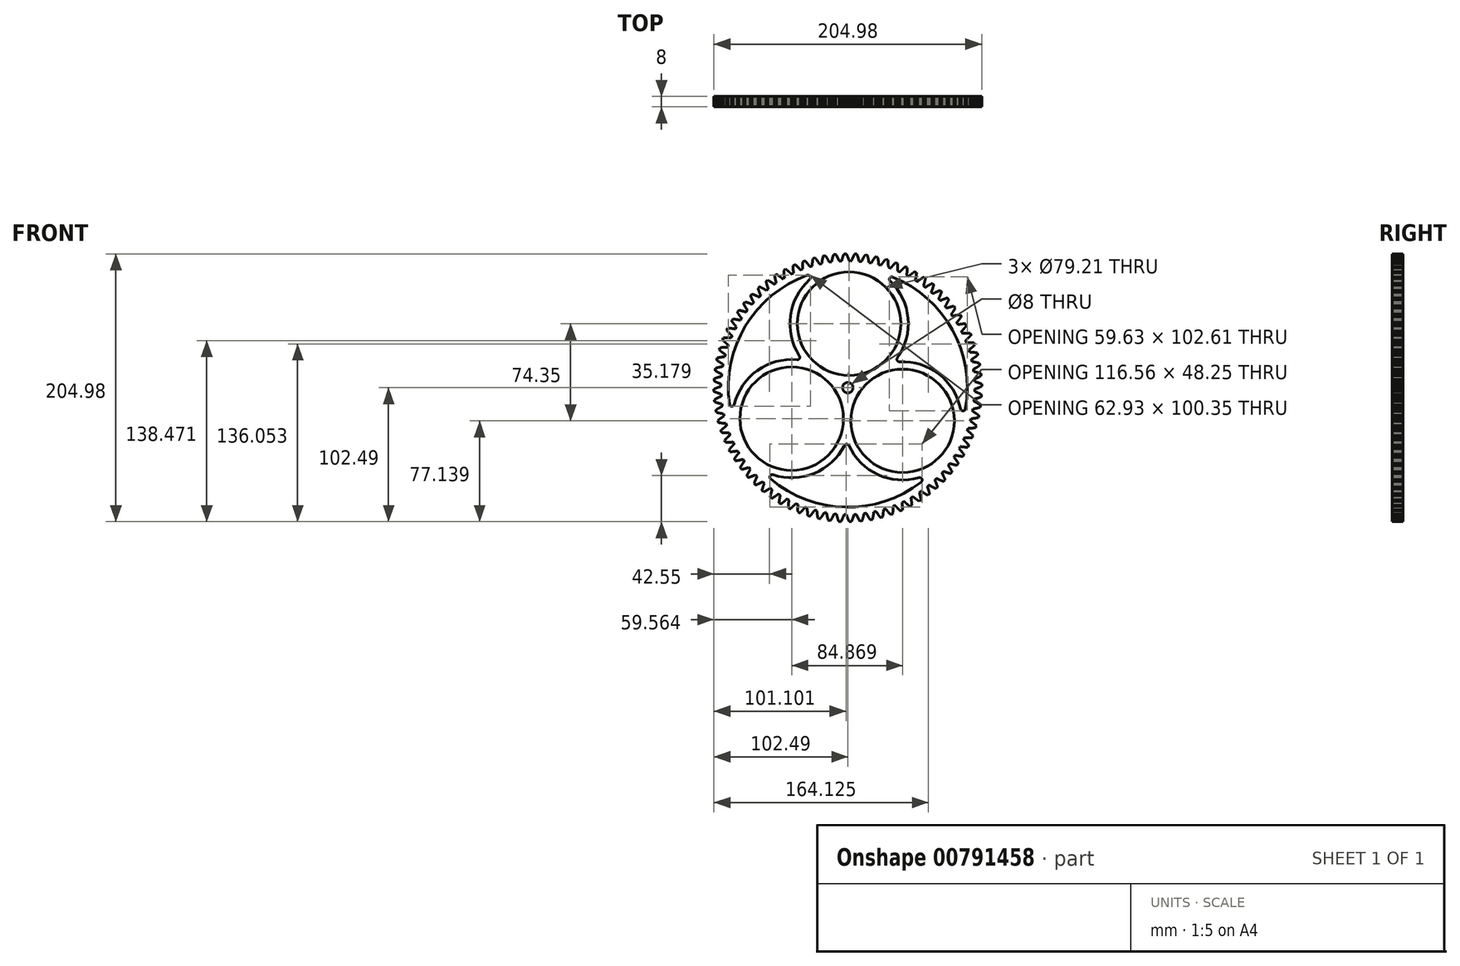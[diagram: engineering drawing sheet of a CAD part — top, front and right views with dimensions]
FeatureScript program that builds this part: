
annotation { "Feature Type Name" : "Feature", "Feature Type Description" : "" }
export const myFeature = defineFeature(function(context is Context, id is Id, definition is map)
    precondition{}
    {
        {
            var Q0;
            Q0=qCreatedBy(makeId("Front.planeOp"),FACE);
            var sketch = newSketch(context, id + "F0", { "sketchPlane" : qUnion([Q0])});
            skCircle(sketch, "E0", {"center": v(0, 0) * mm, "radius": 100 * mm, "construction": true});
            skCircle(sketch, "E1", {"center": v(0.98, 49) * mm, "radius": 39.6 * mm});
            skArc(sketch, "E2", {"start": v(37.95, 22.85) * mm, "mid": v(46.06, 53.26) * mm, "end": v(32.39, 81.62) * mm});
            skCircle(sketch, "E3", {"center": v(41.94, -25.35) * mm, "radius": 39.6 * mm});
            skArc(sketch, "E4", {"start": v(37.95, 22.85) * mm, "mid": v(37.83, 20.84) * mm, "end": v(39.59, 19.87) * mm});
            skArc(sketch, "E5", {"start": v(86.3, -16.23) * mm, "mid": v(69.63, 10.47) * mm, "end": v(39.59, 19.87) * mm});
            skArc(sketch, "E6", {"start": v(90, -16.19) * mm, "mid": v(80.1, 44.13) * mm, "end": v(34.41, 84.73) * mm});
            skArc(sketch, "E7", {"start": v(86.3, -16.23) * mm, "mid": v(88.17, -17.74) * mm, "end": v(90, -16.19) * mm});
            skArc(sketch, "E8", {"start": v(34.41, 84.73) * mm, "mid": v(32.11, 84) * mm, "end": v(32.39, 81.62) * mm});
            skCircle(sketch, "E9", {"center": v(-42.93, -23.65) * mm, "radius": 39.6 * mm});
            skArc(sketch, "E10", {"start": v(-38.76, 21.44) * mm, "mid": v(-36.97, 22.34) * mm, "end": v(-37, 24.35) * mm});
            skArc(sketch, "E11", {"start": v(-29.09, 82.85) * mm, "mid": v(-43.89, 55.07) * mm, "end": v(-37, 24.35) * mm});
            skArc(sketch, "E12", {"start": v(-38.76, 21.44) * mm, "mid": v(-69.16, 13.26) * mm, "end": v(-86.88, -12.76) * mm});
            skArc(sketch, "E13", {"start": v(-30.99, 86.04) * mm, "mid": v(-78.27, 47.3) * mm, "end": v(-90.59, -12.56) * mm});
            skArc(sketch, "E14", {"start": v(-29.09, 82.85) * mm, "mid": v(-28.72, 85.23) * mm, "end": v(-30.99, 86.04) * mm});
            skArc(sketch, "E15", {"start": v(-90.59, -12.56) * mm, "mid": v(-88.81, -14.2) * mm, "end": v(-86.88, -12.76) * mm});
            skArc(sketch, "E16", {"start": v(-57.2, -66.62) * mm, "mid": v(-59.45, -67.49) * mm, "end": v(-59.02, -69.86) * mm});
            skArc(sketch, "E17", {"start": v(-57.2, -66.62) * mm, "mid": v(-25.75, -65.54) * mm, "end": v(-2.59, -44.22) * mm});
            skArc(sketch, "E18", {"start": v(-59.02, -69.86) * mm, "mid": v(-1.83, -91.43) * mm, "end": v(56.17, -72.17) * mm});
            skArc(sketch, "E19", {"start": v(56.17, -72.17) * mm, "mid": v(56.7, -69.82) * mm, "end": v(54.49, -68.86) * mm});
            skArc(sketch, "E20", {"start": v(0.81, -44.29) * mm, "mid": v(23.1, -66.52) * mm, "end": v(54.49, -68.86) * mm});
            skArc(sketch, "E21", {"start": v(0.81, -44.29) * mm, "mid": v(-0.87, -43.19) * mm, "end": v(-2.59, -44.22) * mm});
            skCircle(sketch, "E22", {"center": v(0, 0) * mm, "radius": 4 * mm});
            skLineSegment(sketch, "E23", {"start": v(-97.1, 1.94) * mm, "end": v(-97.18, 1) * mm});
            skLineSegment(sketch, "E24", {"start": v(-97.18, 1) * mm, "end": v(-97.3, 0.96) * mm});
            skLineSegment(sketch, "E25", {"start": v(-97.3, 0.96) * mm, "end": v(-97.43, 0.92) * mm});
            skLineSegment(sketch, "E26", {"start": v(-97.43, 0.92) * mm, "end": v(-97.55, 0.88) * mm});
            skLineSegment(sketch, "E27", {"start": v(-97.55, 0.88) * mm, "end": v(-97.68, 0.84) * mm});
            skLineSegment(sketch, "E28", {"start": v(-97.68, 0.84) * mm, "end": v(-97.8, 0.8) * mm});
            skLineSegment(sketch, "E29", {"start": v(-97.8, 0.8) * mm, "end": v(-97.94, 0.76) * mm});
            skLineSegment(sketch, "E30", {"start": v(-97.94, 0.76) * mm, "end": v(-98.07, 0.72) * mm});
            skLineSegment(sketch, "E31", {"start": v(-98.07, 0.72) * mm, "end": v(-98.2, 0.67) * mm});
            skLineSegment(sketch, "E32", {"start": v(-98.2, 0.67) * mm, "end": v(-98.34, 0.62) * mm});
            skLineSegment(sketch, "E33", {"start": v(-98.34, 0.62) * mm, "end": v(-98.47, 0.58) * mm});
            skLineSegment(sketch, "E34", {"start": v(-98.47, 0.58) * mm, "end": v(-98.6, 0.53) * mm});
            skLineSegment(sketch, "E35", {"start": v(-98.6, 0.53) * mm, "end": v(-98.75, 0.48) * mm});
            skLineSegment(sketch, "E36", {"start": v(-98.75, 0.48) * mm, "end": v(-98.89, 0.43) * mm});
            skLineSegment(sketch, "E37", {"start": v(-98.89, 0.43) * mm, "end": v(-99.03, 0.38) * mm});
            skLineSegment(sketch, "E38", {"start": v(-99.03, 0.38) * mm, "end": v(-99.17, 0.32) * mm});
            skLineSegment(sketch, "E39", {"start": v(-99.17, 0.32) * mm, "end": v(-99.32, 0.27) * mm});
            skLineSegment(sketch, "E40", {"start": v(-99.32, 0.27) * mm, "end": v(-99.46, 0.21) * mm});
            skLineSegment(sketch, "E41", {"start": v(-99.46, 0.21) * mm, "end": v(-99.61, 0.15) * mm});
            skLineSegment(sketch, "E42", {"start": v(-99.61, 0.15) * mm, "end": v(-99.76, 0.1) * mm});
            skLineSegment(sketch, "E43", {"start": v(-99.76, 0.1) * mm, "end": v(-99.9, 0.04) * mm});
            skLineSegment(sketch, "E44", {"start": v(-99.9, 0.04) * mm, "end": v(-100.06, -0.02) * mm});
            skLineSegment(sketch, "E45", {"start": v(-100.06, -0.02) * mm, "end": v(-100.21, -0.09) * mm});
            skLineSegment(sketch, "E46", {"start": v(-100.21, -0.09) * mm, "end": v(-100.37, -0.15) * mm});
            skLineSegment(sketch, "E47", {"start": v(-100.37, -0.15) * mm, "end": v(-100.52, -0.22) * mm});
            skLineSegment(sketch, "E48", {"start": v(-100.52, -0.22) * mm, "end": v(-100.68, -0.28) * mm});
            skLineSegment(sketch, "E49", {"start": v(-100.68, -0.28) * mm, "end": v(-100.84, -0.35) * mm});
            skLineSegment(sketch, "E50", {"start": v(-100.84, -0.35) * mm, "end": v(-101, -0.42) * mm});
            skLineSegment(sketch, "E51", {"start": v(-101, -0.42) * mm, "end": v(-101.16, -0.5) * mm});
            skLineSegment(sketch, "E52", {"start": v(-101.16, -0.5) * mm, "end": v(-101.32, -0.56) * mm});
            skLineSegment(sketch, "E53", {"start": v(-101.32, -0.56) * mm, "end": v(-101.48, -0.64) * mm});
            skLineSegment(sketch, "E54", {"start": v(-101.48, -0.64) * mm, "end": v(-101.65, -0.71) * mm});
            skLineSegment(sketch, "E55", {"start": v(-101.65, -0.71) * mm, "end": v(-101.82, -0.79) * mm});
            skLineSegment(sketch, "E56", {"start": v(-101.82, -0.79) * mm, "end": v(-101.98, -0.87) * mm});
            skLineSegment(sketch, "E57", {"start": v(-101.98, -0.87) * mm, "end": v(-102.15, -0.94) * mm});
            skLineSegment(sketch, "E58", {"start": v(-102.15, -0.94) * mm, "end": v(-102.32, -1.03) * mm});
            skLineSegment(sketch, "E59", {"start": v(-102.32, -1.03) * mm, "end": v(-102.5, -1.1) * mm});
            skLineSegment(sketch, "E60", {"start": v(-102.5, -1.1) * mm, "end": v(-102.5, -1.19) * mm});
            skLineSegment(sketch, "E61", {"start": v(-102.5, -1.19) * mm, "end": v(-102.46, -2.76) * mm});
            skLineSegment(sketch, "E62", {"start": v(-102.46, -2.76) * mm, "end": v(-102.46, -2.84) * mm});
            skLineSegment(sketch, "E63", {"start": v(-102.46, -2.84) * mm, "end": v(-102.28, -2.92) * mm});
            skLineSegment(sketch, "E64", {"start": v(-102.28, -2.92) * mm, "end": v(-102.11, -3) * mm});
            skLineSegment(sketch, "E65", {"start": v(-102.11, -3) * mm, "end": v(-101.94, -3.06) * mm});
            skLineSegment(sketch, "E66", {"start": v(-101.94, -3.06) * mm, "end": v(-101.77, -3.14) * mm});
            skLineSegment(sketch, "E67", {"start": v(-101.77, -3.14) * mm, "end": v(-101.6, -3.2) * mm});
            skLineSegment(sketch, "E68", {"start": v(-101.6, -3.2) * mm, "end": v(-101.43, -3.27) * mm});
            skLineSegment(sketch, "E69", {"start": v(-101.43, -3.27) * mm, "end": v(-101.27, -3.34) * mm});
            skLineSegment(sketch, "E70", {"start": v(-101.27, -3.34) * mm, "end": v(-101.1, -3.4) * mm});
            skLineSegment(sketch, "E71", {"start": v(-101.1, -3.4) * mm, "end": v(-100.94, -3.47) * mm});
            skLineSegment(sketch, "E72", {"start": v(-100.94, -3.47) * mm, "end": v(-100.78, -3.54) * mm});
            skLineSegment(sketch, "E73", {"start": v(-100.78, -3.54) * mm, "end": v(-100.62, -3.6) * mm});
            skLineSegment(sketch, "E74", {"start": v(-100.62, -3.6) * mm, "end": v(-100.46, -3.66) * mm});
            skLineSegment(sketch, "E75", {"start": v(-100.46, -3.66) * mm, "end": v(-100.3, -3.72) * mm});
            skLineSegment(sketch, "E76", {"start": v(-100.3, -3.72) * mm, "end": v(-100.14, -3.77) * mm});
            skLineSegment(sketch, "E77", {"start": v(-100.14, -3.77) * mm, "end": v(-99.99, -3.83) * mm});
            skLineSegment(sketch, "E78", {"start": v(-99.99, -3.83) * mm, "end": v(-99.83, -3.89) * mm});
            skLineSegment(sketch, "E79", {"start": v(-99.83, -3.89) * mm, "end": v(-99.68, -3.94) * mm});
            skLineSegment(sketch, "E80", {"start": v(-99.68, -3.94) * mm, "end": v(-99.53, -4) * mm});
            skLineSegment(sketch, "E81", {"start": v(-99.53, -4) * mm, "end": v(-99.38, -4.04) * mm});
            skLineSegment(sketch, "E82", {"start": v(-99.38, -4.04) * mm, "end": v(-99.23, -4.1) * mm});
            skLineSegment(sketch, "E83", {"start": v(-99.23, -4.1) * mm, "end": v(-99.09, -4.14) * mm});
            skLineSegment(sketch, "E84", {"start": v(-99.09, -4.14) * mm, "end": v(-98.94, -4.2) * mm});
            skLineSegment(sketch, "E85", {"start": v(-98.94, -4.2) * mm, "end": v(-98.8, -4.24) * mm});
            skLineSegment(sketch, "E86", {"start": v(-98.8, -4.24) * mm, "end": v(-98.66, -4.28) * mm});
            skLineSegment(sketch, "E87", {"start": v(-98.66, -4.28) * mm, "end": v(-98.52, -4.33) * mm});
            skLineSegment(sketch, "E88", {"start": v(-98.52, -4.33) * mm, "end": v(-98.38, -4.37) * mm});
            skLineSegment(sketch, "E89", {"start": v(-98.38, -4.37) * mm, "end": v(-98.24, -4.41) * mm});
            skLineSegment(sketch, "E90", {"start": v(-98.24, -4.41) * mm, "end": v(-98.1, -4.45) * mm});
            skLineSegment(sketch, "E91", {"start": v(-98.1, -4.45) * mm, "end": v(-97.97, -4.5) * mm});
            skLineSegment(sketch, "E92", {"start": v(-97.97, -4.5) * mm, "end": v(-97.84, -4.53) * mm});
            skLineSegment(sketch, "E93", {"start": v(-97.84, -4.53) * mm, "end": v(-97.7, -4.57) * mm});
            skLineSegment(sketch, "E94", {"start": v(-97.7, -4.57) * mm, "end": v(-97.57, -4.6) * mm});
            skLineSegment(sketch, "E95", {"start": v(-97.57, -4.6) * mm, "end": v(-97.45, -4.64) * mm});
            skLineSegment(sketch, "E96", {"start": v(-97.45, -4.64) * mm, "end": v(-97.32, -4.68) * mm});
            skLineSegment(sketch, "E97", {"start": v(-97.32, -4.68) * mm, "end": v(-97.2, -4.71) * mm});
            skLineSegment(sketch, "E98", {"start": v(-97.2, -4.71) * mm, "end": v(-97.07, -4.74) * mm});
            skLineSegment(sketch, "E99", {"start": v(-97.07, -4.74) * mm, "end": v(-96.96, -5.68) * mm});
            skLineSegment(sketch, "E100", {"start": v(-96.96, -5.68) * mm, "end": v(-96.96, -6.63) * mm});
            skLineSegment(sketch, "E101", {"start": v(-96.96, -6.63) * mm, "end": v(-97.08, -6.67) * mm});
            skLineSegment(sketch, "E102", {"start": v(-97.08, -6.67) * mm, "end": v(-97.2, -6.72) * mm});
            skLineSegment(sketch, "E103", {"start": v(-97.2, -6.72) * mm, "end": v(-97.32, -6.77) * mm});
            skLineSegment(sketch, "E104", {"start": v(-97.32, -6.77) * mm, "end": v(-97.44, -6.82) * mm});
            skLineSegment(sketch, "E105", {"start": v(-97.44, -6.82) * mm, "end": v(-97.57, -6.87) * mm});
            skLineSegment(sketch, "E106", {"start": v(-97.57, -6.87) * mm, "end": v(-97.7, -6.93) * mm});
            skLineSegment(sketch, "E107", {"start": v(-97.7, -6.93) * mm, "end": v(-97.82, -6.98) * mm});
            skLineSegment(sketch, "E108", {"start": v(-97.82, -6.98) * mm, "end": v(-97.95, -7.04) * mm});
            skLineSegment(sketch, "E109", {"start": v(-97.95, -7.04) * mm, "end": v(-98.08, -7.1) * mm});
            skLineSegment(sketch, "E110", {"start": v(-98.08, -7.1) * mm, "end": v(-98.21, -7.15) * mm});
            skLineSegment(sketch, "E111", {"start": v(-98.21, -7.15) * mm, "end": v(-98.35, -7.2) * mm});
            skLineSegment(sketch, "E112", {"start": v(-98.35, -7.2) * mm, "end": v(-98.48, -7.27) * mm});
            skLineSegment(sketch, "E113", {"start": v(-98.48, -7.27) * mm, "end": v(-98.62, -7.33) * mm});
            skLineSegment(sketch, "E114", {"start": v(-98.62, -7.33) * mm, "end": v(-98.75, -7.4) * mm});
            skLineSegment(sketch, "E115", {"start": v(-98.75, -7.4) * mm, "end": v(-98.9, -7.46) * mm});
            skLineSegment(sketch, "E116", {"start": v(-98.9, -7.46) * mm, "end": v(-99.03, -7.53) * mm});
            skLineSegment(sketch, "E117", {"start": v(-99.03, -7.53) * mm, "end": v(-99.17, -7.6) * mm});
            skLineSegment(sketch, "E118", {"start": v(-99.17, -7.6) * mm, "end": v(-99.32, -7.66) * mm});
            skLineSegment(sketch, "E119", {"start": v(-99.32, -7.66) * mm, "end": v(-99.46, -7.73) * mm});
            skLineSegment(sketch, "E120", {"start": v(-99.46, -7.73) * mm, "end": v(-99.6, -7.8) * mm});
            skLineSegment(sketch, "E121", {"start": v(-99.6, -7.8) * mm, "end": v(-99.75, -7.88) * mm});
            skLineSegment(sketch, "E122", {"start": v(-99.75, -7.88) * mm, "end": v(-99.9, -7.95) * mm});
            skLineSegment(sketch, "E123", {"start": v(-99.9, -7.95) * mm, "end": v(-100.05, -8.03) * mm});
            skLineSegment(sketch, "E124", {"start": v(-100.05, -8.03) * mm, "end": v(-100.2, -8.1) * mm});
            skLineSegment(sketch, "E125", {"start": v(-100.2, -8.1) * mm, "end": v(-100.35, -8.18) * mm});
            skLineSegment(sketch, "E126", {"start": v(-100.35, -8.18) * mm, "end": v(-100.5, -8.26) * mm});
            skLineSegment(sketch, "E127", {"start": v(-100.5, -8.26) * mm, "end": v(-100.65, -8.34) * mm});
            skLineSegment(sketch, "E128", {"start": v(-100.65, -8.34) * mm, "end": v(-100.8, -8.43) * mm});
            skLineSegment(sketch, "E129", {"start": v(-100.8, -8.43) * mm, "end": v(-100.96, -8.51) * mm});
            skLineSegment(sketch, "E130", {"start": v(-100.96, -8.51) * mm, "end": v(-101.12, -8.6) * mm});
            skLineSegment(sketch, "E131", {"start": v(-101.12, -8.6) * mm, "end": v(-101.28, -8.68) * mm});
            skLineSegment(sketch, "E132", {"start": v(-101.28, -8.68) * mm, "end": v(-101.44, -8.77) * mm});
            skLineSegment(sketch, "E133", {"start": v(-101.44, -8.77) * mm, "end": v(-101.6, -8.86) * mm});
            skLineSegment(sketch, "E134", {"start": v(-101.6, -8.86) * mm, "end": v(-101.76, -8.96) * mm});
            skLineSegment(sketch, "E135", {"start": v(-101.76, -8.96) * mm, "end": v(-101.92, -9.05) * mm});
            skLineSegment(sketch, "E136", {"start": v(-101.92, -9.05) * mm, "end": v(-102.09, -9.15) * mm});
            skLineSegment(sketch, "E137", {"start": v(-102.09, -9.15) * mm, "end": v(-102.08, -9.23) * mm});
            skLineSegment(sketch, "E138", {"start": v(-102.08, -9.23) * mm, "end": v(-101.93, -10.8) * mm});
            skLineSegment(sketch, "E139", {"start": v(-101.93, -10.8) * mm, "end": v(-101.92, -10.87) * mm});
            skLineSegment(sketch, "E140", {"start": v(-101.92, -10.87) * mm, "end": v(-101.74, -10.93) * mm});
            skLineSegment(sketch, "E141", {"start": v(-101.74, -10.93) * mm, "end": v(-101.56, -11) * mm});
            skLineSegment(sketch, "E142", {"start": v(-101.56, -11) * mm, "end": v(-101.39, -11.05) * mm});
            skLineSegment(sketch, "E143", {"start": v(-101.39, -11.05) * mm, "end": v(-101.21, -11.11) * mm});
            skLineSegment(sketch, "E144", {"start": v(-101.21, -11.11) * mm, "end": v(-101.04, -11.17) * mm});
            skLineSegment(sketch, "E145", {"start": v(-101.04, -11.17) * mm, "end": v(-100.86, -11.22) * mm});
            skLineSegment(sketch, "E146", {"start": v(-100.86, -11.22) * mm, "end": v(-100.7, -11.28) * mm});
            skLineSegment(sketch, "E147", {"start": v(-100.7, -11.28) * mm, "end": v(-100.52, -11.33) * mm});
            skLineSegment(sketch, "E148", {"start": v(-100.52, -11.33) * mm, "end": v(-100.36, -11.38) * mm});
            skLineSegment(sketch, "E149", {"start": v(-100.36, -11.38) * mm, "end": v(-100.19, -11.43) * mm});
            skLineSegment(sketch, "E150", {"start": v(-100.19, -11.43) * mm, "end": v(-100.02, -11.48) * mm});
            skLineSegment(sketch, "E151", {"start": v(-100.02, -11.48) * mm, "end": v(-99.86, -11.53) * mm});
            skLineSegment(sketch, "E152", {"start": v(-99.86, -11.53) * mm, "end": v(-99.7, -11.57) * mm});
            skLineSegment(sketch, "E153", {"start": v(-99.7, -11.57) * mm, "end": v(-99.54, -11.62) * mm});
            skLineSegment(sketch, "E154", {"start": v(-99.54, -11.62) * mm, "end": v(-99.38, -11.66) * mm});
            skLineSegment(sketch, "E155", {"start": v(-99.38, -11.66) * mm, "end": v(-99.22, -11.7) * mm});
            skLineSegment(sketch, "E156", {"start": v(-99.22, -11.7) * mm, "end": v(-99.07, -11.75) * mm});
            skLineSegment(sketch, "E157", {"start": v(-99.07, -11.75) * mm, "end": v(-98.91, -11.79) * mm});
            skLineSegment(sketch, "E158", {"start": v(-98.91, -11.79) * mm, "end": v(-98.76, -11.83) * mm});
            skLineSegment(sketch, "E159", {"start": v(-98.76, -11.83) * mm, "end": v(-98.6, -11.87) * mm});
            skLineSegment(sketch, "E160", {"start": v(-98.6, -11.87) * mm, "end": v(-98.46, -11.9) * mm});
            skLineSegment(sketch, "E161", {"start": v(-98.46, -11.9) * mm, "end": v(-98.3, -11.94) * mm});
            skLineSegment(sketch, "E162", {"start": v(-98.3, -11.94) * mm, "end": v(-98.16, -11.98) * mm});
            skLineSegment(sketch, "E163", {"start": v(-98.16, -11.98) * mm, "end": v(-98.02, -12.01) * mm});
            skLineSegment(sketch, "E164", {"start": v(-98.02, -12.01) * mm, "end": v(-97.87, -12.04) * mm});
            skLineSegment(sketch, "E165", {"start": v(-97.87, -12.04) * mm, "end": v(-97.73, -12.08) * mm});
            skLineSegment(sketch, "E166", {"start": v(-97.73, -12.08) * mm, "end": v(-97.6, -12.1) * mm});
            skLineSegment(sketch, "E167", {"start": v(-97.6, -12.1) * mm, "end": v(-97.45, -12.14) * mm});
            skLineSegment(sketch, "E168", {"start": v(-97.45, -12.14) * mm, "end": v(-97.31, -12.17) * mm});
            skLineSegment(sketch, "E169", {"start": v(-97.31, -12.17) * mm, "end": v(-97.18, -12.2) * mm});
            skLineSegment(sketch, "E170", {"start": v(-97.18, -12.2) * mm, "end": v(-97.04, -12.22) * mm});
            skLineSegment(sketch, "E171", {"start": v(-97.04, -12.22) * mm, "end": v(-96.91, -12.25) * mm});
            skLineSegment(sketch, "E172", {"start": v(-96.91, -12.25) * mm, "end": v(-96.78, -12.27) * mm});
            skLineSegment(sketch, "E173", {"start": v(-96.78, -12.27) * mm, "end": v(-96.65, -12.3) * mm});
            skLineSegment(sketch, "E174", {"start": v(-96.65, -12.3) * mm, "end": v(-96.52, -12.32) * mm});
            skLineSegment(sketch, "E175", {"start": v(-96.52, -12.32) * mm, "end": v(-96.4, -12.35) * mm});
            skLineSegment(sketch, "E176", {"start": v(-96.4, -12.35) * mm, "end": v(-96.21, -13.27) * mm});
            skLineSegment(sketch, "E177", {"start": v(-96.21, -13.27) * mm, "end": v(-96.14, -14.21) * mm});
            skLineSegment(sketch, "E178", {"start": v(-96.14, -14.21) * mm, "end": v(-96.26, -14.27) * mm});
            skLineSegment(sketch, "E179", {"start": v(-96.26, -14.27) * mm, "end": v(-96.37, -14.33) * mm});
            skLineSegment(sketch, "E180", {"start": v(-96.37, -14.33) * mm, "end": v(-96.5, -14.39) * mm});
            skLineSegment(sketch, "E181", {"start": v(-96.5, -14.39) * mm, "end": v(-96.6, -14.45) * mm});
            skLineSegment(sketch, "E182", {"start": v(-96.6, -14.45) * mm, "end": v(-96.73, -14.5) * mm});
            skLineSegment(sketch, "E183", {"start": v(-96.73, -14.5) * mm, "end": v(-96.85, -14.57) * mm});
            skLineSegment(sketch, "E184", {"start": v(-96.85, -14.57) * mm, "end": v(-96.97, -14.63) * mm});
            skLineSegment(sketch, "E185", {"start": v(-96.97, -14.63) * mm, "end": v(-97.1, -14.7) * mm});
            skLineSegment(sketch, "E186", {"start": v(-97.1, -14.7) * mm, "end": v(-97.22, -14.77) * mm});
            skLineSegment(sketch, "E187", {"start": v(-97.22, -14.77) * mm, "end": v(-97.35, -14.83) * mm});
            skLineSegment(sketch, "E188", {"start": v(-97.35, -14.83) * mm, "end": v(-97.48, -14.9) * mm});
            skLineSegment(sketch, "E189", {"start": v(-97.48, -14.9) * mm, "end": v(-97.6, -14.97) * mm});
            skLineSegment(sketch, "E190", {"start": v(-97.6, -14.97) * mm, "end": v(-97.74, -15.05) * mm});
            skLineSegment(sketch, "E191", {"start": v(-97.74, -15.05) * mm, "end": v(-97.87, -15.12) * mm});
            skLineSegment(sketch, "E192", {"start": v(-97.87, -15.12) * mm, "end": v(-98, -15.2) * mm});
            skLineSegment(sketch, "E193", {"start": v(-98, -15.2) * mm, "end": v(-98.14, -15.27) * mm});
            skLineSegment(sketch, "E194", {"start": v(-98.14, -15.27) * mm, "end": v(-98.27, -15.35) * mm});
            skLineSegment(sketch, "E195", {"start": v(-98.27, -15.35) * mm, "end": v(-98.4, -15.43) * mm});
            skLineSegment(sketch, "E196", {"start": v(-98.4, -15.43) * mm, "end": v(-98.55, -15.51) * mm});
            skLineSegment(sketch, "E197", {"start": v(-98.55, -15.51) * mm, "end": v(-98.69, -15.6) * mm});
            skLineSegment(sketch, "E198", {"start": v(-98.69, -15.6) * mm, "end": v(-98.83, -15.68) * mm});
            skLineSegment(sketch, "E199", {"start": v(-98.83, -15.68) * mm, "end": v(-98.97, -15.76) * mm});
            skLineSegment(sketch, "E200", {"start": v(-98.97, -15.76) * mm, "end": v(-99.1, -15.85) * mm});
            skLineSegment(sketch, "E201", {"start": v(-99.1, -15.85) * mm, "end": v(-99.25, -15.94) * mm});
            skLineSegment(sketch, "E202", {"start": v(-99.25, -15.94) * mm, "end": v(-99.4, -16.03) * mm});
            skLineSegment(sketch, "E203", {"start": v(-99.4, -16.03) * mm, "end": v(-99.54, -16.12) * mm});
            skLineSegment(sketch, "E204", {"start": v(-99.54, -16.12) * mm, "end": v(-99.69, -16.21) * mm});
            skLineSegment(sketch, "E205", {"start": v(-99.69, -16.21) * mm, "end": v(-99.84, -16.3) * mm});
            skLineSegment(sketch, "E206", {"start": v(-99.84, -16.3) * mm, "end": v(-99.99, -16.4) * mm});
            skLineSegment(sketch, "E207", {"start": v(-99.99, -16.4) * mm, "end": v(-100.14, -16.5) * mm});
            skLineSegment(sketch, "E208", {"start": v(-100.14, -16.5) * mm, "end": v(-100.29, -16.6) * mm});
            skLineSegment(sketch, "E209", {"start": v(-100.29, -16.6) * mm, "end": v(-100.44, -16.7) * mm});
            skLineSegment(sketch, "E210", {"start": v(-100.44, -16.7) * mm, "end": v(-100.6, -16.8) * mm});
            skLineSegment(sketch, "E211", {"start": v(-100.6, -16.8) * mm, "end": v(-100.75, -16.91) * mm});
            skLineSegment(sketch, "E212", {"start": v(-100.75, -16.91) * mm, "end": v(-100.9, -17.02) * mm});
            skLineSegment(sketch, "E213", {"start": v(-100.9, -17.02) * mm, "end": v(-101.06, -17.13) * mm});
            skLineSegment(sketch, "E214", {"start": v(-101.06, -17.13) * mm, "end": v(-101.05, -17.2) * mm});
            skLineSegment(sketch, "E215", {"start": v(-101.05, -17.2) * mm, "end": v(-100.77, -18.76) * mm});
            skLineSegment(sketch, "E216", {"start": v(-100.77, -18.76) * mm, "end": v(-100.75, -18.84) * mm});
            skLineSegment(sketch, "E217", {"start": v(-100.75, -18.84) * mm, "end": v(-100.57, -18.88) * mm});
            skLineSegment(sketch, "E218", {"start": v(-100.57, -18.88) * mm, "end": v(-100.39, -18.93) * mm});
            skLineSegment(sketch, "E219", {"start": v(-100.39, -18.93) * mm, "end": v(-100.2, -18.97) * mm});
            skLineSegment(sketch, "E220", {"start": v(-100.2, -18.97) * mm, "end": v(-100.03, -19.02) * mm});
            skLineSegment(sketch, "E221", {"start": v(-100.03, -19.02) * mm, "end": v(-99.85, -19.06) * mm});
            skLineSegment(sketch, "E222", {"start": v(-99.85, -19.06) * mm, "end": v(-99.67, -19.1) * mm});
            skLineSegment(sketch, "E223", {"start": v(-99.67, -19.1) * mm, "end": v(-99.5, -19.14) * mm});
            skLineSegment(sketch, "E224", {"start": v(-99.5, -19.14) * mm, "end": v(-99.32, -19.18) * mm});
            skLineSegment(sketch, "E225", {"start": v(-99.32, -19.18) * mm, "end": v(-99.15, -19.22) * mm});
            skLineSegment(sketch, "E226", {"start": v(-99.15, -19.22) * mm, "end": v(-98.98, -19.26) * mm});
            skLineSegment(sketch, "E227", {"start": v(-98.98, -19.26) * mm, "end": v(-98.82, -19.3) * mm});
            skLineSegment(sketch, "E228", {"start": v(-98.82, -19.3) * mm, "end": v(-98.65, -19.33) * mm});
            skLineSegment(sketch, "E229", {"start": v(-98.65, -19.33) * mm, "end": v(-98.48, -19.36) * mm});
            skLineSegment(sketch, "E230", {"start": v(-98.48, -19.36) * mm, "end": v(-98.32, -19.4) * mm});
            skLineSegment(sketch, "E231", {"start": v(-98.32, -19.4) * mm, "end": v(-98.16, -19.43) * mm});
            skLineSegment(sketch, "E232", {"start": v(-98.16, -19.43) * mm, "end": v(-98, -19.46) * mm});
            skLineSegment(sketch, "E233", {"start": v(-98, -19.46) * mm, "end": v(-97.84, -19.49) * mm});
            skLineSegment(sketch, "E234", {"start": v(-97.84, -19.49) * mm, "end": v(-97.68, -19.51) * mm});
            skLineSegment(sketch, "E235", {"start": v(-97.68, -19.51) * mm, "end": v(-97.53, -19.54) * mm});
            skLineSegment(sketch, "E236", {"start": v(-97.53, -19.54) * mm, "end": v(-97.37, -19.57) * mm});
            skLineSegment(sketch, "E237", {"start": v(-97.37, -19.57) * mm, "end": v(-97.22, -19.6) * mm});
            skLineSegment(sketch, "E238", {"start": v(-97.22, -19.6) * mm, "end": v(-97.07, -19.62) * mm});
            skLineSegment(sketch, "E239", {"start": v(-97.07, -19.62) * mm, "end": v(-96.92, -19.64) * mm});
            skLineSegment(sketch, "E240", {"start": v(-96.92, -19.64) * mm, "end": v(-96.77, -19.66) * mm});
            skLineSegment(sketch, "E241", {"start": v(-96.77, -19.66) * mm, "end": v(-96.63, -19.69) * mm});
            skLineSegment(sketch, "E242", {"start": v(-96.63, -19.69) * mm, "end": v(-96.48, -19.7) * mm});
            skLineSegment(sketch, "E243", {"start": v(-96.48, -19.7) * mm, "end": v(-96.34, -19.73) * mm});
            skLineSegment(sketch, "E244", {"start": v(-96.34, -19.73) * mm, "end": v(-96.2, -19.75) * mm});
            skLineSegment(sketch, "E245", {"start": v(-96.2, -19.75) * mm, "end": v(-96.06, -19.76) * mm});
            skLineSegment(sketch, "E246", {"start": v(-96.06, -19.76) * mm, "end": v(-95.92, -19.78) * mm});
            skLineSegment(sketch, "E247", {"start": v(-95.92, -19.78) * mm, "end": v(-95.79, -19.8) * mm});
            skLineSegment(sketch, "E248", {"start": v(-95.79, -19.8) * mm, "end": v(-95.65, -19.81) * mm});
            skLineSegment(sketch, "E249", {"start": v(-95.65, -19.81) * mm, "end": v(-95.52, -19.83) * mm});
            skLineSegment(sketch, "E250", {"start": v(-95.52, -19.83) * mm, "end": v(-95.39, -19.84) * mm});
            skLineSegment(sketch, "E251", {"start": v(-95.39, -19.84) * mm, "end": v(-95.26, -19.86) * mm});
            skLineSegment(sketch, "E252", {"start": v(-95.26, -19.86) * mm, "end": v(-95.13, -19.87) * mm});
            skLineSegment(sketch, "E253", {"start": v(-95.13, -19.87) * mm, "end": v(-94.88, -20.78) * mm});
            skLineSegment(sketch, "E254", {"start": v(-94.88, -20.78) * mm, "end": v(-94.73, -21.71) * mm});
            skLineSegment(sketch, "E255", {"start": v(-94.73, -21.71) * mm, "end": v(-94.84, -21.78) * mm});
            skLineSegment(sketch, "E256", {"start": v(-94.84, -21.78) * mm, "end": v(-94.95, -21.85) * mm});
            skLineSegment(sketch, "E257", {"start": v(-94.95, -21.85) * mm, "end": v(-95.06, -21.91) * mm});
            skLineSegment(sketch, "E258", {"start": v(-95.06, -21.91) * mm, "end": v(-95.18, -21.98) * mm});
            skLineSegment(sketch, "E259", {"start": v(-95.18, -21.98) * mm, "end": v(-95.3, -22.05) * mm});
            skLineSegment(sketch, "E260", {"start": v(-95.3, -22.05) * mm, "end": v(-95.4, -22.12) * mm});
            skLineSegment(sketch, "E261", {"start": v(-95.4, -22.12) * mm, "end": v(-95.53, -22.2) * mm});
            skLineSegment(sketch, "E262", {"start": v(-95.53, -22.2) * mm, "end": v(-95.65, -22.27) * mm});
            skLineSegment(sketch, "E263", {"start": v(-95.65, -22.27) * mm, "end": v(-95.77, -22.35) * mm});
            skLineSegment(sketch, "E264", {"start": v(-95.77, -22.35) * mm, "end": v(-95.89, -22.43) * mm});
            skLineSegment(sketch, "E265", {"start": v(-95.89, -22.43) * mm, "end": v(-96, -22.5) * mm});
            skLineSegment(sketch, "E266", {"start": v(-96, -22.5) * mm, "end": v(-96.13, -22.59) * mm});
            skLineSegment(sketch, "E267", {"start": v(-96.13, -22.59) * mm, "end": v(-96.26, -22.67) * mm});
            skLineSegment(sketch, "E268", {"start": v(-96.26, -22.67) * mm, "end": v(-96.38, -22.75) * mm});
            skLineSegment(sketch, "E269", {"start": v(-96.38, -22.75) * mm, "end": v(-96.5, -22.84) * mm});
            skLineSegment(sketch, "E270", {"start": v(-96.5, -22.84) * mm, "end": v(-96.64, -22.92) * mm});
            skLineSegment(sketch, "E271", {"start": v(-96.64, -22.92) * mm, "end": v(-96.77, -23.01) * mm});
            skLineSegment(sketch, "E272", {"start": v(-96.77, -23.01) * mm, "end": v(-96.9, -23.1) * mm});
            skLineSegment(sketch, "E273", {"start": v(-96.9, -23.1) * mm, "end": v(-97.03, -23.2) * mm});
            skLineSegment(sketch, "E274", {"start": v(-97.03, -23.2) * mm, "end": v(-97.16, -23.29) * mm});
            skLineSegment(sketch, "E275", {"start": v(-97.16, -23.29) * mm, "end": v(-97.3, -23.38) * mm});
            skLineSegment(sketch, "E276", {"start": v(-97.3, -23.38) * mm, "end": v(-97.42, -23.48) * mm});
            skLineSegment(sketch, "E277", {"start": v(-97.42, -23.48) * mm, "end": v(-97.56, -23.58) * mm});
            skLineSegment(sketch, "E278", {"start": v(-97.56, -23.58) * mm, "end": v(-97.7, -23.68) * mm});
            skLineSegment(sketch, "E279", {"start": v(-97.7, -23.68) * mm, "end": v(-97.83, -23.78) * mm});
            skLineSegment(sketch, "E280", {"start": v(-97.83, -23.78) * mm, "end": v(-97.97, -23.88) * mm});
            skLineSegment(sketch, "E281", {"start": v(-97.97, -23.88) * mm, "end": v(-98.1, -23.99) * mm});
            skLineSegment(sketch, "E282", {"start": v(-98.1, -23.99) * mm, "end": v(-98.25, -24.1) * mm});
            skLineSegment(sketch, "E283", {"start": v(-98.25, -24.1) * mm, "end": v(-98.4, -24.2) * mm});
            skLineSegment(sketch, "E284", {"start": v(-98.4, -24.2) * mm, "end": v(-98.53, -24.3) * mm});
            skLineSegment(sketch, "E285", {"start": v(-98.53, -24.3) * mm, "end": v(-98.67, -24.42) * mm});
            skLineSegment(sketch, "E286", {"start": v(-98.67, -24.42) * mm, "end": v(-98.82, -24.53) * mm});
            skLineSegment(sketch, "E287", {"start": v(-98.82, -24.53) * mm, "end": v(-98.96, -24.65) * mm});
            skLineSegment(sketch, "E288", {"start": v(-98.96, -24.65) * mm, "end": v(-99.1, -24.77) * mm});
            skLineSegment(sketch, "E289", {"start": v(-99.1, -24.77) * mm, "end": v(-99.25, -24.88) * mm});
            skLineSegment(sketch, "E290", {"start": v(-99.25, -24.88) * mm, "end": v(-99.4, -25) * mm});
            skLineSegment(sketch, "E291", {"start": v(-99.4, -25) * mm, "end": v(-99.38, -25.08) * mm});
            skLineSegment(sketch, "E292", {"start": v(-99.38, -25.08) * mm, "end": v(-98.99, -26.6) * mm});
            skLineSegment(sketch, "E293", {"start": v(-98.99, -26.6) * mm, "end": v(-98.96, -26.68) * mm});
            skLineSegment(sketch, "E294", {"start": v(-98.96, -26.68) * mm, "end": v(-98.78, -26.72) * mm});
            skLineSegment(sketch, "E295", {"start": v(-98.78, -26.72) * mm, "end": v(-98.6, -26.75) * mm});
            skLineSegment(sketch, "E296", {"start": v(-98.6, -26.75) * mm, "end": v(-98.4, -26.78) * mm});
            skLineSegment(sketch, "E297", {"start": v(-98.4, -26.78) * mm, "end": v(-98.23, -26.8) * mm});
            skLineSegment(sketch, "E298", {"start": v(-98.23, -26.8) * mm, "end": v(-98.05, -26.84) * mm});
            skLineSegment(sketch, "E299", {"start": v(-98.05, -26.84) * mm, "end": v(-97.87, -26.86) * mm});
            skLineSegment(sketch, "E300", {"start": v(-97.87, -26.86) * mm, "end": v(-97.69, -26.9) * mm});
            skLineSegment(sketch, "E301", {"start": v(-97.69, -26.9) * mm, "end": v(-97.51, -26.92) * mm});
            skLineSegment(sketch, "E302", {"start": v(-97.51, -26.92) * mm, "end": v(-97.34, -26.94) * mm});
            skLineSegment(sketch, "E303", {"start": v(-97.34, -26.94) * mm, "end": v(-97.17, -26.96) * mm});
            skLineSegment(sketch, "E304", {"start": v(-97.17, -26.96) * mm, "end": v(-97, -26.99) * mm});
            skLineSegment(sketch, "E305", {"start": v(-97, -26.99) * mm, "end": v(-96.83, -27) * mm});
            skLineSegment(sketch, "E306", {"start": v(-96.83, -27) * mm, "end": v(-96.66, -27.03) * mm});
            skLineSegment(sketch, "E307", {"start": v(-96.66, -27.03) * mm, "end": v(-96.5, -27.05) * mm});
            skLineSegment(sketch, "E308", {"start": v(-96.5, -27.05) * mm, "end": v(-96.33, -27.07) * mm});
            skLineSegment(sketch, "E309", {"start": v(-96.33, -27.07) * mm, "end": v(-96.17, -27.08) * mm});
            skLineSegment(sketch, "E310", {"start": v(-96.17, -27.08) * mm, "end": v(-96, -27.1) * mm});
            skLineSegment(sketch, "E311", {"start": v(-96, -27.1) * mm, "end": v(-95.85, -27.12) * mm});
            skLineSegment(sketch, "E312", {"start": v(-95.85, -27.12) * mm, "end": v(-95.7, -27.13) * mm});
            skLineSegment(sketch, "E313", {"start": v(-95.7, -27.13) * mm, "end": v(-95.54, -27.15) * mm});
            skLineSegment(sketch, "E314", {"start": v(-95.54, -27.15) * mm, "end": v(-95.38, -27.16) * mm});
            skLineSegment(sketch, "E315", {"start": v(-95.38, -27.16) * mm, "end": v(-95.23, -27.17) * mm});
            skLineSegment(sketch, "E316", {"start": v(-95.23, -27.17) * mm, "end": v(-95.08, -27.19) * mm});
            skLineSegment(sketch, "E317", {"start": v(-95.08, -27.19) * mm, "end": v(-94.93, -27.2) * mm});
            skLineSegment(sketch, "E318", {"start": v(-94.93, -27.2) * mm, "end": v(-94.78, -27.2) * mm});
            skLineSegment(sketch, "E319", {"start": v(-94.78, -27.2) * mm, "end": v(-94.64, -27.22) * mm});
            skLineSegment(sketch, "E320", {"start": v(-94.64, -27.22) * mm, "end": v(-94.5, -27.23) * mm});
            skLineSegment(sketch, "E321", {"start": v(-94.5, -27.23) * mm, "end": v(-94.35, -27.23) * mm});
            skLineSegment(sketch, "E322", {"start": v(-94.35, -27.23) * mm, "end": v(-94.21, -27.24) * mm});
            skLineSegment(sketch, "E323", {"start": v(-94.21, -27.24) * mm, "end": v(-94.07, -27.25) * mm});
            skLineSegment(sketch, "E324", {"start": v(-94.07, -27.25) * mm, "end": v(-93.94, -27.25) * mm});
            skLineSegment(sketch, "E325", {"start": v(-93.94, -27.25) * mm, "end": v(-93.8, -27.26) * mm});
            skLineSegment(sketch, "E326", {"start": v(-93.8, -27.26) * mm, "end": v(-93.67, -27.26) * mm});
            skLineSegment(sketch, "E327", {"start": v(-93.67, -27.26) * mm, "end": v(-93.54, -27.27) * mm});
            skLineSegment(sketch, "E328", {"start": v(-93.54, -27.27) * mm, "end": v(-93.4, -27.27) * mm});
            skLineSegment(sketch, "E329", {"start": v(-93.4, -27.27) * mm, "end": v(-93.28, -27.27) * mm});
            skLineSegment(sketch, "E330", {"start": v(-93.28, -27.27) * mm, "end": v(-92.95, -28.16) * mm});
            skLineSegment(sketch, "E331", {"start": v(-92.95, -28.16) * mm, "end": v(-92.73, -29.08) * mm});
            skLineSegment(sketch, "E332", {"start": v(-92.73, -29.08) * mm, "end": v(-92.84, -29.15) * mm});
            skLineSegment(sketch, "E333", {"start": v(-92.84, -29.15) * mm, "end": v(-92.94, -29.23) * mm});
            skLineSegment(sketch, "E334", {"start": v(-92.94, -29.23) * mm, "end": v(-93.05, -29.3) * mm});
            skLineSegment(sketch, "E335", {"start": v(-93.05, -29.3) * mm, "end": v(-93.16, -29.38) * mm});
            skLineSegment(sketch, "E336", {"start": v(-93.16, -29.38) * mm, "end": v(-93.27, -29.46) * mm});
            skLineSegment(sketch, "E337", {"start": v(-93.27, -29.46) * mm, "end": v(-93.38, -29.54) * mm});
            skLineSegment(sketch, "E338", {"start": v(-93.38, -29.54) * mm, "end": v(-93.5, -29.62) * mm});
            skLineSegment(sketch, "E339", {"start": v(-93.5, -29.62) * mm, "end": v(-93.6, -29.7) * mm});
            skLineSegment(sketch, "E340", {"start": v(-93.6, -29.7) * mm, "end": v(-93.72, -29.8) * mm});
            skLineSegment(sketch, "E341", {"start": v(-93.72, -29.8) * mm, "end": v(-93.83, -29.88) * mm});
            skLineSegment(sketch, "E342", {"start": v(-93.83, -29.88) * mm, "end": v(-93.95, -29.97) * mm});
            skLineSegment(sketch, "E343", {"start": v(-93.95, -29.97) * mm, "end": v(-94.06, -30.06) * mm});
            skLineSegment(sketch, "E344", {"start": v(-94.06, -30.06) * mm, "end": v(-94.18, -30.15) * mm});
            skLineSegment(sketch, "E345", {"start": v(-94.18, -30.15) * mm, "end": v(-94.3, -30.24) * mm});
            skLineSegment(sketch, "E346", {"start": v(-94.3, -30.24) * mm, "end": v(-94.42, -30.34) * mm});
            skLineSegment(sketch, "E347", {"start": v(-94.42, -30.34) * mm, "end": v(-94.54, -30.44) * mm});
            skLineSegment(sketch, "E348", {"start": v(-94.54, -30.44) * mm, "end": v(-94.66, -30.53) * mm});
            skLineSegment(sketch, "E349", {"start": v(-94.66, -30.53) * mm, "end": v(-94.78, -30.63) * mm});
            skLineSegment(sketch, "E350", {"start": v(-94.78, -30.63) * mm, "end": v(-94.9, -30.74) * mm});
            skLineSegment(sketch, "E351", {"start": v(-94.9, -30.74) * mm, "end": v(-95.03, -30.84) * mm});
            skLineSegment(sketch, "E352", {"start": v(-95.03, -30.84) * mm, "end": v(-95.16, -30.94) * mm});
            skLineSegment(sketch, "E353", {"start": v(-95.16, -30.94) * mm, "end": v(-95.28, -31.05) * mm});
            skLineSegment(sketch, "E354", {"start": v(-95.28, -31.05) * mm, "end": v(-95.4, -31.16) * mm});
            skLineSegment(sketch, "E355", {"start": v(-95.4, -31.16) * mm, "end": v(-95.54, -31.27) * mm});
            skLineSegment(sketch, "E356", {"start": v(-95.54, -31.27) * mm, "end": v(-95.67, -31.38) * mm});
            skLineSegment(sketch, "E357", {"start": v(-95.67, -31.38) * mm, "end": v(-95.8, -31.5) * mm});
            skLineSegment(sketch, "E358", {"start": v(-95.8, -31.5) * mm, "end": v(-95.93, -31.6) * mm});
            skLineSegment(sketch, "E359", {"start": v(-95.93, -31.6) * mm, "end": v(-96.06, -31.73) * mm});
            skLineSegment(sketch, "E360", {"start": v(-96.06, -31.73) * mm, "end": v(-96.19, -31.84) * mm});
            skLineSegment(sketch, "E361", {"start": v(-96.19, -31.84) * mm, "end": v(-96.32, -31.97) * mm});
            skLineSegment(sketch, "E362", {"start": v(-96.32, -31.97) * mm, "end": v(-96.45, -32.09) * mm});
            skLineSegment(sketch, "E363", {"start": v(-96.45, -32.09) * mm, "end": v(-96.59, -32.21) * mm});
            skLineSegment(sketch, "E364", {"start": v(-96.59, -32.21) * mm, "end": v(-96.72, -32.34) * mm});
            skLineSegment(sketch, "E365", {"start": v(-96.72, -32.34) * mm, "end": v(-96.86, -32.46) * mm});
            skLineSegment(sketch, "E366", {"start": v(-96.86, -32.46) * mm, "end": v(-97, -32.6) * mm});
            skLineSegment(sketch, "E367", {"start": v(-97, -32.6) * mm, "end": v(-97.13, -32.73) * mm});
            skLineSegment(sketch, "E368", {"start": v(-97.13, -32.73) * mm, "end": v(-97.1, -32.8) * mm});
            skLineSegment(sketch, "E369", {"start": v(-97.1, -32.8) * mm, "end": v(-96.6, -34.29) * mm});
            skLineSegment(sketch, "E370", {"start": v(-96.6, -34.29) * mm, "end": v(-96.57, -34.36) * mm});
            skLineSegment(sketch, "E371", {"start": v(-96.57, -34.36) * mm, "end": v(-96.38, -34.38) * mm});
            skLineSegment(sketch, "E372", {"start": v(-96.38, -34.38) * mm, "end": v(-96.19, -34.4) * mm});
            skLineSegment(sketch, "E373", {"start": v(-96.19, -34.4) * mm, "end": v(-96, -34.42) * mm});
            skLineSegment(sketch, "E374", {"start": v(-96, -34.42) * mm, "end": v(-95.82, -34.43) * mm});
            skLineSegment(sketch, "E375", {"start": v(-95.82, -34.43) * mm, "end": v(-95.64, -34.45) * mm});
            skLineSegment(sketch, "E376", {"start": v(-95.64, -34.45) * mm, "end": v(-95.46, -34.46) * mm});
            skLineSegment(sketch, "E377", {"start": v(-95.46, -34.46) * mm, "end": v(-95.28, -34.47) * mm});
            skLineSegment(sketch, "E378", {"start": v(-95.28, -34.47) * mm, "end": v(-95.1, -34.48) * mm});
            skLineSegment(sketch, "E379", {"start": v(-95.1, -34.48) * mm, "end": v(-94.93, -34.5) * mm});
            skLineSegment(sketch, "E380", {"start": v(-94.93, -34.5) * mm, "end": v(-94.75, -34.5) * mm});
            skLineSegment(sketch, "E381", {"start": v(-94.75, -34.5) * mm, "end": v(-94.58, -34.51) * mm});
            skLineSegment(sketch, "E382", {"start": v(-94.58, -34.51) * mm, "end": v(-94.41, -34.52) * mm});
            skLineSegment(sketch, "E383", {"start": v(-94.41, -34.52) * mm, "end": v(-94.24, -34.53) * mm});
            skLineSegment(sketch, "E384", {"start": v(-94.24, -34.53) * mm, "end": v(-94.08, -34.54) * mm});
            skLineSegment(sketch, "E385", {"start": v(-94.08, -34.54) * mm, "end": v(-93.91, -34.54) * mm});
            skLineSegment(sketch, "E386", {"start": v(-93.91, -34.54) * mm, "end": v(-93.75, -34.55) * mm});
            skLineSegment(sketch, "E387", {"start": v(-93.75, -34.55) * mm, "end": v(-93.59, -34.55) * mm});
            skLineSegment(sketch, "E388", {"start": v(-93.59, -34.55) * mm, "end": v(-93.43, -34.55) * mm});
            skLineSegment(sketch, "E389", {"start": v(-93.43, -34.55) * mm, "end": v(-93.27, -34.56) * mm});
            skLineSegment(sketch, "E390", {"start": v(-93.27, -34.56) * mm, "end": v(-93.11, -34.56) * mm});
            skLineSegment(sketch, "E391", {"start": v(-93.11, -34.56) * mm, "end": v(-92.96, -34.56) * mm});
            skLineSegment(sketch, "E392", {"start": v(-92.96, -34.56) * mm, "end": v(-92.8, -34.56) * mm});
            skLineSegment(sketch, "E393", {"start": v(-92.8, -34.56) * mm, "end": v(-92.65, -34.56) * mm});
            skLineSegment(sketch, "E394", {"start": v(-92.65, -34.56) * mm, "end": v(-92.5, -34.56) * mm});
            skLineSegment(sketch, "E395", {"start": v(-92.5, -34.56) * mm, "end": v(-92.36, -34.56) * mm});
            skLineSegment(sketch, "E396", {"start": v(-92.36, -34.56) * mm, "end": v(-92.21, -34.56) * mm});
            skLineSegment(sketch, "E397", {"start": v(-92.21, -34.56) * mm, "end": v(-92.07, -34.56) * mm});
            skLineSegment(sketch, "E398", {"start": v(-92.07, -34.56) * mm, "end": v(-91.93, -34.55) * mm});
            skLineSegment(sketch, "E399", {"start": v(-91.93, -34.55) * mm, "end": v(-91.79, -34.55) * mm});
            skLineSegment(sketch, "E400", {"start": v(-91.79, -34.55) * mm, "end": v(-91.65, -34.54) * mm});
            skLineSegment(sketch, "E401", {"start": v(-91.65, -34.54) * mm, "end": v(-91.51, -34.54) * mm});
            skLineSegment(sketch, "E402", {"start": v(-91.51, -34.54) * mm, "end": v(-91.38, -34.53) * mm});
            skLineSegment(sketch, "E403", {"start": v(-91.38, -34.53) * mm, "end": v(-91.24, -34.53) * mm});
            skLineSegment(sketch, "E404", {"start": v(-91.24, -34.53) * mm, "end": v(-91.11, -34.52) * mm});
            skLineSegment(sketch, "E405", {"start": v(-91.11, -34.52) * mm, "end": v(-90.98, -34.52) * mm});
            skLineSegment(sketch, "E406", {"start": v(-90.98, -34.52) * mm, "end": v(-90.85, -34.5) * mm});
            skLineSegment(sketch, "E407", {"start": v(-90.85, -34.5) * mm, "end": v(-90.46, -35.37) * mm});
            skLineSegment(sketch, "E408", {"start": v(-90.46, -35.37) * mm, "end": v(-90.17, -36.27) * mm});
            skLineSegment(sketch, "E409", {"start": v(-90.17, -36.27) * mm, "end": v(-90.27, -36.35) * mm});
            skLineSegment(sketch, "E410", {"start": v(-90.27, -36.35) * mm, "end": v(-90.36, -36.43) * mm});
            skLineSegment(sketch, "E411", {"start": v(-90.36, -36.43) * mm, "end": v(-90.47, -36.51) * mm});
            skLineSegment(sketch, "E412", {"start": v(-90.47, -36.51) * mm, "end": v(-90.57, -36.6) * mm});
            skLineSegment(sketch, "E413", {"start": v(-90.57, -36.6) * mm, "end": v(-90.67, -36.69) * mm});
            skLineSegment(sketch, "E414", {"start": v(-90.67, -36.69) * mm, "end": v(-90.77, -36.78) * mm});
            skLineSegment(sketch, "E415", {"start": v(-90.77, -36.78) * mm, "end": v(-90.88, -36.87) * mm});
            skLineSegment(sketch, "E416", {"start": v(-90.88, -36.87) * mm, "end": v(-90.98, -36.96) * mm});
            skLineSegment(sketch, "E417", {"start": v(-90.98, -36.96) * mm, "end": v(-91.1, -37.05) * mm});
            skLineSegment(sketch, "E418", {"start": v(-91.1, -37.05) * mm, "end": v(-91.2, -37.15) * mm});
            skLineSegment(sketch, "E419", {"start": v(-91.2, -37.15) * mm, "end": v(-91.3, -37.25) * mm});
            skLineSegment(sketch, "E420", {"start": v(-91.3, -37.25) * mm, "end": v(-91.42, -37.35) * mm});
            skLineSegment(sketch, "E421", {"start": v(-91.42, -37.35) * mm, "end": v(-91.53, -37.45) * mm});
            skLineSegment(sketch, "E422", {"start": v(-91.53, -37.45) * mm, "end": v(-91.64, -37.55) * mm});
            skLineSegment(sketch, "E423", {"start": v(-91.64, -37.55) * mm, "end": v(-91.75, -37.65) * mm});
            skLineSegment(sketch, "E424", {"start": v(-91.75, -37.65) * mm, "end": v(-91.86, -37.76) * mm});
            skLineSegment(sketch, "E425", {"start": v(-91.86, -37.76) * mm, "end": v(-91.97, -37.87) * mm});
            skLineSegment(sketch, "E426", {"start": v(-91.97, -37.87) * mm, "end": v(-92.09, -37.98) * mm});
            skLineSegment(sketch, "E427", {"start": v(-92.09, -37.98) * mm, "end": v(-92.2, -38.09) * mm});
            skLineSegment(sketch, "E428", {"start": v(-92.2, -38.09) * mm, "end": v(-92.32, -38.2) * mm});
            skLineSegment(sketch, "E429", {"start": v(-92.32, -38.2) * mm, "end": v(-92.44, -38.31) * mm});
            skLineSegment(sketch, "E430", {"start": v(-92.44, -38.31) * mm, "end": v(-92.55, -38.43) * mm});
            skLineSegment(sketch, "E431", {"start": v(-92.55, -38.43) * mm, "end": v(-92.67, -38.55) * mm});
            skLineSegment(sketch, "E432", {"start": v(-92.67, -38.55) * mm, "end": v(-92.79, -38.67) * mm});
            skLineSegment(sketch, "E433", {"start": v(-92.79, -38.67) * mm, "end": v(-92.9, -38.79) * mm});
            skLineSegment(sketch, "E434", {"start": v(-92.9, -38.79) * mm, "end": v(-93.03, -38.91) * mm});
            skLineSegment(sketch, "E435", {"start": v(-93.03, -38.91) * mm, "end": v(-93.15, -39.04) * mm});
            skLineSegment(sketch, "E436", {"start": v(-93.15, -39.04) * mm, "end": v(-93.27, -39.16) * mm});
            skLineSegment(sketch, "E437", {"start": v(-93.27, -39.16) * mm, "end": v(-93.4, -39.3) * mm});
            skLineSegment(sketch, "E438", {"start": v(-93.4, -39.3) * mm, "end": v(-93.52, -39.42) * mm});
            skLineSegment(sketch, "E439", {"start": v(-93.52, -39.42) * mm, "end": v(-93.64, -39.56) * mm});
            skLineSegment(sketch, "E440", {"start": v(-93.64, -39.56) * mm, "end": v(-93.76, -39.7) * mm});
            skLineSegment(sketch, "E441", {"start": v(-93.76, -39.7) * mm, "end": v(-93.89, -39.83) * mm});
            skLineSegment(sketch, "E442", {"start": v(-93.89, -39.83) * mm, "end": v(-94.01, -39.96) * mm});
            skLineSegment(sketch, "E443", {"start": v(-94.01, -39.96) * mm, "end": v(-94.14, -40.1) * mm});
            skLineSegment(sketch, "E444", {"start": v(-94.14, -40.1) * mm, "end": v(-94.27, -40.25) * mm});
            skLineSegment(sketch, "E445", {"start": v(-94.27, -40.25) * mm, "end": v(-94.24, -40.32) * mm});
            skLineSegment(sketch, "E446", {"start": v(-94.24, -40.32) * mm, "end": v(-93.6, -41.76) * mm});
            skLineSegment(sketch, "E447", {"start": v(-93.6, -41.76) * mm, "end": v(-93.57, -41.83) * mm});
            skLineSegment(sketch, "E448", {"start": v(-93.57, -41.83) * mm, "end": v(-93.38, -41.84) * mm});
            skLineSegment(sketch, "E449", {"start": v(-93.38, -41.84) * mm, "end": v(-93.2, -41.84) * mm});
            skLineSegment(sketch, "E450", {"start": v(-93.2, -41.84) * mm, "end": v(-93, -41.84) * mm});
            skLineSegment(sketch, "E451", {"start": v(-93, -41.84) * mm, "end": v(-92.82, -41.84) * mm});
            skLineSegment(sketch, "E452", {"start": v(-92.82, -41.84) * mm, "end": v(-92.64, -41.84) * mm});
            skLineSegment(sketch, "E453", {"start": v(-92.64, -41.84) * mm, "end": v(-92.46, -41.84) * mm});
            skLineSegment(sketch, "E454", {"start": v(-92.46, -41.84) * mm, "end": v(-92.28, -41.84) * mm});
            skLineSegment(sketch, "E455", {"start": v(-92.28, -41.84) * mm, "end": v(-92.1, -41.84) * mm});
            skLineSegment(sketch, "E456", {"start": v(-92.1, -41.84) * mm, "end": v(-91.93, -41.84) * mm});
            skLineSegment(sketch, "E457", {"start": v(-91.93, -41.84) * mm, "end": v(-91.75, -41.83) * mm});
            skLineSegment(sketch, "E458", {"start": v(-91.75, -41.83) * mm, "end": v(-91.58, -41.83) * mm});
            skLineSegment(sketch, "E459", {"start": v(-91.58, -41.83) * mm, "end": v(-91.41, -41.82) * mm});
            skLineSegment(sketch, "E460", {"start": v(-91.41, -41.82) * mm, "end": v(-91.24, -41.82) * mm});
            skLineSegment(sketch, "E461", {"start": v(-91.24, -41.82) * mm, "end": v(-91.08, -41.81) * mm});
            skLineSegment(sketch, "E462", {"start": v(-91.08, -41.81) * mm, "end": v(-90.91, -41.8) * mm});
            skLineSegment(sketch, "E463", {"start": v(-90.91, -41.8) * mm, "end": v(-90.75, -41.8) * mm});
            skLineSegment(sketch, "E464", {"start": v(-90.75, -41.8) * mm, "end": v(-90.59, -41.79) * mm});
            skLineSegment(sketch, "E465", {"start": v(-90.59, -41.79) * mm, "end": v(-90.43, -41.78) * mm});
            skLineSegment(sketch, "E466", {"start": v(-90.43, -41.78) * mm, "end": v(-90.27, -41.77) * mm});
            skLineSegment(sketch, "E467", {"start": v(-90.27, -41.77) * mm, "end": v(-90.11, -41.76) * mm});
            skLineSegment(sketch, "E468", {"start": v(-90.11, -41.76) * mm, "end": v(-89.96, -41.75) * mm});
            skLineSegment(sketch, "E469", {"start": v(-89.96, -41.75) * mm, "end": v(-89.8, -41.74) * mm});
            skLineSegment(sketch, "E470", {"start": v(-89.8, -41.74) * mm, "end": v(-89.66, -41.72) * mm});
            skLineSegment(sketch, "E471", {"start": v(-89.66, -41.72) * mm, "end": v(-89.5, -41.71) * mm});
            skLineSegment(sketch, "E472", {"start": v(-89.5, -41.71) * mm, "end": v(-89.36, -41.7) * mm});
            skLineSegment(sketch, "E473", {"start": v(-89.36, -41.7) * mm, "end": v(-89.22, -41.69) * mm});
            skLineSegment(sketch, "E474", {"start": v(-89.22, -41.69) * mm, "end": v(-89.07, -41.67) * mm});
            skLineSegment(sketch, "E475", {"start": v(-89.07, -41.67) * mm, "end": v(-88.93, -41.66) * mm});
            skLineSegment(sketch, "E476", {"start": v(-88.93, -41.66) * mm, "end": v(-88.8, -41.64) * mm});
            skLineSegment(sketch, "E477", {"start": v(-88.8, -41.64) * mm, "end": v(-88.65, -41.63) * mm});
            skLineSegment(sketch, "E478", {"start": v(-88.65, -41.63) * mm, "end": v(-88.52, -41.61) * mm});
            skLineSegment(sketch, "E479", {"start": v(-88.52, -41.61) * mm, "end": v(-88.38, -41.6) * mm});
            skLineSegment(sketch, "E480", {"start": v(-88.38, -41.6) * mm, "end": v(-88.25, -41.58) * mm});
            skLineSegment(sketch, "E481", {"start": v(-88.25, -41.58) * mm, "end": v(-88.12, -41.56) * mm});
            skLineSegment(sketch, "E482", {"start": v(-88.12, -41.56) * mm, "end": v(-88, -41.55) * mm});
            skLineSegment(sketch, "E483", {"start": v(-88, -41.55) * mm, "end": v(-87.87, -41.53) * mm});
            skLineSegment(sketch, "E484", {"start": v(-87.87, -41.53) * mm, "end": v(-87.4, -42.35) * mm});
            skLineSegment(sketch, "E485", {"start": v(-87.4, -42.35) * mm, "end": v(-87.04, -43.23) * mm});
            skLineSegment(sketch, "E486", {"start": v(-87.04, -43.23) * mm, "end": v(-87.14, -43.32) * mm});
            skLineSegment(sketch, "E487", {"start": v(-87.14, -43.32) * mm, "end": v(-87.23, -43.4) * mm});
            skLineSegment(sketch, "E488", {"start": v(-87.23, -43.4) * mm, "end": v(-87.32, -43.5) * mm});
            skLineSegment(sketch, "E489", {"start": v(-87.32, -43.5) * mm, "end": v(-87.42, -43.6) * mm});
            skLineSegment(sketch, "E490", {"start": v(-87.42, -43.6) * mm, "end": v(-87.51, -43.69) * mm});
            skLineSegment(sketch, "E491", {"start": v(-87.51, -43.69) * mm, "end": v(-87.6, -43.79) * mm});
            skLineSegment(sketch, "E492", {"start": v(-87.6, -43.79) * mm, "end": v(-87.7, -43.88) * mm});
            skLineSegment(sketch, "E493", {"start": v(-87.7, -43.88) * mm, "end": v(-87.8, -43.99) * mm});
            skLineSegment(sketch, "E494", {"start": v(-87.8, -43.99) * mm, "end": v(-87.9, -44.09) * mm});
            skLineSegment(sketch, "E495", {"start": v(-87.9, -44.09) * mm, "end": v(-88, -44.2) * mm});
            skLineSegment(sketch, "E496", {"start": v(-88, -44.2) * mm, "end": v(-88.1, -44.3) * mm});
            skLineSegment(sketch, "E497", {"start": v(-88.1, -44.3) * mm, "end": v(-88.2, -44.4) * mm});
            skLineSegment(sketch, "E498", {"start": v(-88.2, -44.4) * mm, "end": v(-88.3, -44.51) * mm});
            skLineSegment(sketch, "E499", {"start": v(-88.3, -44.51) * mm, "end": v(-88.4, -44.62) * mm});
            skLineSegment(sketch, "E500", {"start": v(-88.4, -44.62) * mm, "end": v(-88.51, -44.74) * mm});
            skLineSegment(sketch, "E501", {"start": v(-88.51, -44.74) * mm, "end": v(-88.61, -44.85) * mm});
            skLineSegment(sketch, "E502", {"start": v(-88.61, -44.85) * mm, "end": v(-88.72, -44.97) * mm});
            skLineSegment(sketch, "E503", {"start": v(-88.72, -44.97) * mm, "end": v(-88.82, -45.08) * mm});
            skLineSegment(sketch, "E504", {"start": v(-88.82, -45.08) * mm, "end": v(-88.93, -45.2) * mm});
            skLineSegment(sketch, "E505", {"start": v(-88.93, -45.2) * mm, "end": v(-89.04, -45.33) * mm});
            skLineSegment(sketch, "E506", {"start": v(-89.04, -45.33) * mm, "end": v(-89.14, -45.45) * mm});
            skLineSegment(sketch, "E507", {"start": v(-89.14, -45.45) * mm, "end": v(-89.25, -45.57) * mm});
            skLineSegment(sketch, "E508", {"start": v(-89.25, -45.57) * mm, "end": v(-89.36, -45.7) * mm});
            skLineSegment(sketch, "E509", {"start": v(-89.36, -45.7) * mm, "end": v(-89.47, -45.83) * mm});
            skLineSegment(sketch, "E510", {"start": v(-89.47, -45.83) * mm, "end": v(-89.58, -45.96) * mm});
            skLineSegment(sketch, "E511", {"start": v(-89.58, -45.96) * mm, "end": v(-89.69, -46.1) * mm});
            skLineSegment(sketch, "E512", {"start": v(-89.69, -46.1) * mm, "end": v(-89.8, -46.23) * mm});
            skLineSegment(sketch, "E513", {"start": v(-89.8, -46.23) * mm, "end": v(-89.91, -46.36) * mm});
            skLineSegment(sketch, "E514", {"start": v(-89.91, -46.36) * mm, "end": v(-90.02, -46.5) * mm});
            skLineSegment(sketch, "E515", {"start": v(-90.02, -46.5) * mm, "end": v(-90.13, -46.64) * mm});
            skLineSegment(sketch, "E516", {"start": v(-90.13, -46.64) * mm, "end": v(-90.25, -46.78) * mm});
            skLineSegment(sketch, "E517", {"start": v(-90.25, -46.78) * mm, "end": v(-90.36, -46.92) * mm});
            skLineSegment(sketch, "E518", {"start": v(-90.36, -46.92) * mm, "end": v(-90.47, -47.07) * mm});
            skLineSegment(sketch, "E519", {"start": v(-90.47, -47.07) * mm, "end": v(-90.59, -47.22) * mm});
            skLineSegment(sketch, "E520", {"start": v(-90.59, -47.22) * mm, "end": v(-90.7, -47.37) * mm});
            skLineSegment(sketch, "E521", {"start": v(-90.7, -47.37) * mm, "end": v(-90.82, -47.52) * mm});
            skLineSegment(sketch, "E522", {"start": v(-90.82, -47.52) * mm, "end": v(-90.78, -47.6) * mm});
            skLineSegment(sketch, "E523", {"start": v(-90.78, -47.6) * mm, "end": v(-90.04, -48.98) * mm});
            skLineSegment(sketch, "E524", {"start": v(-90.04, -48.98) * mm, "end": v(-90, -49.05) * mm});
            skLineSegment(sketch, "E525", {"start": v(-90, -49.05) * mm, "end": v(-89.81, -49.04) * mm});
            skLineSegment(sketch, "E526", {"start": v(-89.81, -49.04) * mm, "end": v(-89.62, -49.02) * mm});
            skLineSegment(sketch, "E527", {"start": v(-89.62, -49.02) * mm, "end": v(-89.44, -49.01) * mm});
            skLineSegment(sketch, "E528", {"start": v(-89.44, -49.01) * mm, "end": v(-89.25, -49) * mm});
            skLineSegment(sketch, "E529", {"start": v(-89.25, -49) * mm, "end": v(-89.07, -48.98) * mm});
            skLineSegment(sketch, "E530", {"start": v(-89.07, -48.98) * mm, "end": v(-88.9, -48.97) * mm});
            skLineSegment(sketch, "E531", {"start": v(-88.9, -48.97) * mm, "end": v(-88.71, -48.95) * mm});
            skLineSegment(sketch, "E532", {"start": v(-88.71, -48.95) * mm, "end": v(-88.54, -48.94) * mm});
            skLineSegment(sketch, "E533", {"start": v(-88.54, -48.94) * mm, "end": v(-88.36, -48.92) * mm});
            skLineSegment(sketch, "E534", {"start": v(-88.36, -48.92) * mm, "end": v(-88.19, -48.9) * mm});
            skLineSegment(sketch, "E535", {"start": v(-88.19, -48.9) * mm, "end": v(-88.02, -48.88) * mm});
            skLineSegment(sketch, "E536", {"start": v(-88.02, -48.88) * mm, "end": v(-87.85, -48.87) * mm});
            skLineSegment(sketch, "E537", {"start": v(-87.85, -48.87) * mm, "end": v(-87.68, -48.85) * mm});
            skLineSegment(sketch, "E538", {"start": v(-87.68, -48.85) * mm, "end": v(-87.51, -48.83) * mm});
            skLineSegment(sketch, "E539", {"start": v(-87.51, -48.83) * mm, "end": v(-87.35, -48.8) * mm});
            skLineSegment(sketch, "E540", {"start": v(-87.35, -48.8) * mm, "end": v(-87.19, -48.79) * mm});
            skLineSegment(sketch, "E541", {"start": v(-87.19, -48.79) * mm, "end": v(-87.03, -48.77) * mm});
            skLineSegment(sketch, "E542", {"start": v(-87.03, -48.77) * mm, "end": v(-86.87, -48.74) * mm});
            skLineSegment(sketch, "E543", {"start": v(-86.87, -48.74) * mm, "end": v(-86.71, -48.72) * mm});
            skLineSegment(sketch, "E544", {"start": v(-86.71, -48.72) * mm, "end": v(-86.56, -48.7) * mm});
            skLineSegment(sketch, "E545", {"start": v(-86.56, -48.7) * mm, "end": v(-86.4, -48.68) * mm});
            skLineSegment(sketch, "E546", {"start": v(-86.4, -48.68) * mm, "end": v(-86.26, -48.65) * mm});
            skLineSegment(sketch, "E547", {"start": v(-86.26, -48.65) * mm, "end": v(-86.1, -48.63) * mm});
            skLineSegment(sketch, "E548", {"start": v(-86.1, -48.63) * mm, "end": v(-85.96, -48.6) * mm});
            skLineSegment(sketch, "E549", {"start": v(-85.96, -48.6) * mm, "end": v(-85.81, -48.58) * mm});
            skLineSegment(sketch, "E550", {"start": v(-85.81, -48.58) * mm, "end": v(-85.67, -48.56) * mm});
            skLineSegment(sketch, "E551", {"start": v(-85.67, -48.56) * mm, "end": v(-85.53, -48.53) * mm});
            skLineSegment(sketch, "E552", {"start": v(-85.53, -48.53) * mm, "end": v(-85.39, -48.5) * mm});
            skLineSegment(sketch, "E553", {"start": v(-85.39, -48.5) * mm, "end": v(-85.25, -48.48) * mm});
            skLineSegment(sketch, "E554", {"start": v(-85.25, -48.48) * mm, "end": v(-85.11, -48.46) * mm});
            skLineSegment(sketch, "E555", {"start": v(-85.11, -48.46) * mm, "end": v(-84.98, -48.43) * mm});
            skLineSegment(sketch, "E556", {"start": v(-84.98, -48.43) * mm, "end": v(-84.85, -48.4) * mm});
            skLineSegment(sketch, "E557", {"start": v(-84.85, -48.4) * mm, "end": v(-84.72, -48.38) * mm});
            skLineSegment(sketch, "E558", {"start": v(-84.72, -48.38) * mm, "end": v(-84.59, -48.35) * mm});
            skLineSegment(sketch, "E559", {"start": v(-84.59, -48.35) * mm, "end": v(-84.46, -48.32) * mm});
            skLineSegment(sketch, "E560", {"start": v(-84.46, -48.32) * mm, "end": v(-84.34, -48.3) * mm});
            skLineSegment(sketch, "E561", {"start": v(-84.34, -48.3) * mm, "end": v(-83.81, -49.08) * mm});
            skLineSegment(sketch, "E562", {"start": v(-83.81, -49.08) * mm, "end": v(-83.38, -49.92) * mm});
            skLineSegment(sketch, "E563", {"start": v(-83.38, -49.92) * mm, "end": v(-83.47, -50.02) * mm});
            skLineSegment(sketch, "E564", {"start": v(-83.47, -50.02) * mm, "end": v(-83.55, -50.12) * mm});
            skLineSegment(sketch, "E565", {"start": v(-83.55, -50.12) * mm, "end": v(-83.64, -50.22) * mm});
            skLineSegment(sketch, "E566", {"start": v(-83.64, -50.22) * mm, "end": v(-83.73, -50.32) * mm});
            skLineSegment(sketch, "E567", {"start": v(-83.73, -50.32) * mm, "end": v(-83.81, -50.42) * mm});
            skLineSegment(sketch, "E568", {"start": v(-83.81, -50.42) * mm, "end": v(-83.9, -50.52) * mm});
            skLineSegment(sketch, "E569", {"start": v(-83.9, -50.52) * mm, "end": v(-84, -50.63) * mm});
            skLineSegment(sketch, "E570", {"start": v(-84, -50.63) * mm, "end": v(-84.08, -50.74) * mm});
            skLineSegment(sketch, "E571", {"start": v(-84.08, -50.74) * mm, "end": v(-84.17, -50.85) * mm});
            skLineSegment(sketch, "E572", {"start": v(-84.17, -50.85) * mm, "end": v(-84.26, -50.96) * mm});
            skLineSegment(sketch, "E573", {"start": v(-84.26, -50.96) * mm, "end": v(-84.36, -51.07) * mm});
            skLineSegment(sketch, "E574", {"start": v(-84.36, -51.07) * mm, "end": v(-84.45, -51.19) * mm});
            skLineSegment(sketch, "E575", {"start": v(-84.45, -51.19) * mm, "end": v(-84.54, -51.3) * mm});
            skLineSegment(sketch, "E576", {"start": v(-84.54, -51.3) * mm, "end": v(-84.63, -51.42) * mm});
            skLineSegment(sketch, "E577", {"start": v(-84.63, -51.42) * mm, "end": v(-84.73, -51.54) * mm});
            skLineSegment(sketch, "E578", {"start": v(-84.73, -51.54) * mm, "end": v(-84.82, -51.67) * mm});
            skLineSegment(sketch, "E579", {"start": v(-84.82, -51.67) * mm, "end": v(-84.92, -51.79) * mm});
            skLineSegment(sketch, "E580", {"start": v(-84.92, -51.79) * mm, "end": v(-85.01, -51.91) * mm});
            skLineSegment(sketch, "E581", {"start": v(-85.01, -51.91) * mm, "end": v(-85.1, -52.04) * mm});
            skLineSegment(sketch, "E582", {"start": v(-85.1, -52.04) * mm, "end": v(-85.2, -52.17) * mm});
            skLineSegment(sketch, "E583", {"start": v(-85.2, -52.17) * mm, "end": v(-85.3, -52.3) * mm});
            skLineSegment(sketch, "E584", {"start": v(-85.3, -52.3) * mm, "end": v(-85.4, -52.44) * mm});
            skLineSegment(sketch, "E585", {"start": v(-85.4, -52.44) * mm, "end": v(-85.5, -52.57) * mm});
            skLineSegment(sketch, "E586", {"start": v(-85.5, -52.57) * mm, "end": v(-85.6, -52.7) * mm});
            skLineSegment(sketch, "E587", {"start": v(-85.6, -52.7) * mm, "end": v(-85.7, -52.85) * mm});
            skLineSegment(sketch, "E588", {"start": v(-85.7, -52.85) * mm, "end": v(-85.8, -52.99) * mm});
            skLineSegment(sketch, "E589", {"start": v(-85.8, -52.99) * mm, "end": v(-85.9, -53.13) * mm});
            skLineSegment(sketch, "E590", {"start": v(-85.9, -53.13) * mm, "end": v(-86, -53.27) * mm});
            skLineSegment(sketch, "E591", {"start": v(-86, -53.27) * mm, "end": v(-86.1, -53.42) * mm});
            skLineSegment(sketch, "E592", {"start": v(-86.1, -53.42) * mm, "end": v(-86.2, -53.57) * mm});
            skLineSegment(sketch, "E593", {"start": v(-86.2, -53.57) * mm, "end": v(-86.3, -53.72) * mm});
            skLineSegment(sketch, "E594", {"start": v(-86.3, -53.72) * mm, "end": v(-86.4, -53.87) * mm});
            skLineSegment(sketch, "E595", {"start": v(-86.4, -53.87) * mm, "end": v(-86.5, -54.02) * mm});
            skLineSegment(sketch, "E596", {"start": v(-86.5, -54.02) * mm, "end": v(-86.6, -54.18) * mm});
            skLineSegment(sketch, "E597", {"start": v(-86.6, -54.18) * mm, "end": v(-86.7, -54.34) * mm});
            skLineSegment(sketch, "E598", {"start": v(-86.7, -54.34) * mm, "end": v(-86.8, -54.5) * mm});
            skLineSegment(sketch, "E599", {"start": v(-86.8, -54.5) * mm, "end": v(-86.77, -54.57) * mm});
            skLineSegment(sketch, "E600", {"start": v(-86.77, -54.57) * mm, "end": v(-85.92, -55.9) * mm});
            skLineSegment(sketch, "E601", {"start": v(-85.92, -55.9) * mm, "end": v(-85.87, -55.96) * mm});
            skLineSegment(sketch, "E602", {"start": v(-85.87, -55.96) * mm, "end": v(-85.69, -55.93) * mm});
            skLineSegment(sketch, "E603", {"start": v(-85.69, -55.93) * mm, "end": v(-85.5, -55.9) * mm});
            skLineSegment(sketch, "E604", {"start": v(-85.5, -55.9) * mm, "end": v(-85.32, -55.88) * mm});
            skLineSegment(sketch, "E605", {"start": v(-85.32, -55.88) * mm, "end": v(-85.13, -55.85) * mm});
            skLineSegment(sketch, "E606", {"start": v(-85.13, -55.85) * mm, "end": v(-84.95, -55.82) * mm});
            skLineSegment(sketch, "E607", {"start": v(-84.95, -55.82) * mm, "end": v(-84.78, -55.8) * mm});
            skLineSegment(sketch, "E608", {"start": v(-84.78, -55.8) * mm, "end": v(-84.6, -55.76) * mm});
            skLineSegment(sketch, "E609", {"start": v(-84.6, -55.76) * mm, "end": v(-84.42, -55.73) * mm});
            skLineSegment(sketch, "E610", {"start": v(-84.42, -55.73) * mm, "end": v(-84.25, -55.7) * mm});
            skLineSegment(sketch, "E611", {"start": v(-84.25, -55.7) * mm, "end": v(-84.08, -55.67) * mm});
            skLineSegment(sketch, "E612", {"start": v(-84.08, -55.67) * mm, "end": v(-83.91, -55.64) * mm});
            skLineSegment(sketch, "E613", {"start": v(-83.91, -55.64) * mm, "end": v(-83.74, -55.6) * mm});
            skLineSegment(sketch, "E614", {"start": v(-83.74, -55.6) * mm, "end": v(-83.58, -55.58) * mm});
            skLineSegment(sketch, "E615", {"start": v(-83.58, -55.58) * mm, "end": v(-83.41, -55.54) * mm});
            skLineSegment(sketch, "E616", {"start": v(-83.41, -55.54) * mm, "end": v(-83.25, -55.5) * mm});
            skLineSegment(sketch, "E617", {"start": v(-83.25, -55.5) * mm, "end": v(-83.1, -55.48) * mm});
            skLineSegment(sketch, "E618", {"start": v(-83.1, -55.48) * mm, "end": v(-82.93, -55.44) * mm});
            skLineSegment(sketch, "E619", {"start": v(-82.93, -55.44) * mm, "end": v(-82.78, -55.4) * mm});
            skLineSegment(sketch, "E620", {"start": v(-82.78, -55.4) * mm, "end": v(-82.62, -55.38) * mm});
            skLineSegment(sketch, "E621", {"start": v(-82.62, -55.38) * mm, "end": v(-82.47, -55.34) * mm});
            skLineSegment(sketch, "E622", {"start": v(-82.47, -55.34) * mm, "end": v(-82.32, -55.3) * mm});
            skLineSegment(sketch, "E623", {"start": v(-82.32, -55.3) * mm, "end": v(-82.17, -55.27) * mm});
            skLineSegment(sketch, "E624", {"start": v(-82.17, -55.27) * mm, "end": v(-82.03, -55.24) * mm});
            skLineSegment(sketch, "E625", {"start": v(-82.03, -55.24) * mm, "end": v(-81.88, -55.2) * mm});
            skLineSegment(sketch, "E626", {"start": v(-81.88, -55.2) * mm, "end": v(-81.74, -55.16) * mm});
            skLineSegment(sketch, "E627", {"start": v(-81.74, -55.16) * mm, "end": v(-81.6, -55.13) * mm});
            skLineSegment(sketch, "E628", {"start": v(-81.6, -55.13) * mm, "end": v(-81.46, -55.1) * mm});
            skLineSegment(sketch, "E629", {"start": v(-81.46, -55.1) * mm, "end": v(-81.32, -55.06) * mm});
            skLineSegment(sketch, "E630", {"start": v(-81.32, -55.06) * mm, "end": v(-81.18, -55.02) * mm});
            skLineSegment(sketch, "E631", {"start": v(-81.18, -55.02) * mm, "end": v(-81.05, -54.98) * mm});
            skLineSegment(sketch, "E632", {"start": v(-81.05, -54.98) * mm, "end": v(-80.92, -54.95) * mm});
            skLineSegment(sketch, "E633", {"start": v(-80.92, -54.95) * mm, "end": v(-80.79, -54.91) * mm});
            skLineSegment(sketch, "E634", {"start": v(-80.79, -54.91) * mm, "end": v(-80.66, -54.87) * mm});
            skLineSegment(sketch, "E635", {"start": v(-80.66, -54.87) * mm, "end": v(-80.53, -54.84) * mm});
            skLineSegment(sketch, "E636", {"start": v(-80.53, -54.84) * mm, "end": v(-80.4, -54.8) * mm});
            skLineSegment(sketch, "E637", {"start": v(-80.4, -54.8) * mm, "end": v(-80.29, -54.76) * mm});
            skLineSegment(sketch, "E638", {"start": v(-80.29, -54.76) * mm, "end": v(-79.7, -55.5) * mm});
            skLineSegment(sketch, "E639", {"start": v(-79.7, -55.5) * mm, "end": v(-79.2, -56.31) * mm});
            skLineSegment(sketch, "E640", {"start": v(-79.2, -56.31) * mm, "end": v(-79.29, -56.41) * mm});
            skLineSegment(sketch, "E641", {"start": v(-79.29, -56.41) * mm, "end": v(-79.36, -56.52) * mm});
            skLineSegment(sketch, "E642", {"start": v(-79.36, -56.52) * mm, "end": v(-79.44, -56.62) * mm});
            skLineSegment(sketch, "E643", {"start": v(-79.44, -56.62) * mm, "end": v(-79.52, -56.73) * mm});
            skLineSegment(sketch, "E644", {"start": v(-79.52, -56.73) * mm, "end": v(-79.6, -56.84) * mm});
            skLineSegment(sketch, "E645", {"start": v(-79.6, -56.84) * mm, "end": v(-79.68, -56.95) * mm});
            skLineSegment(sketch, "E646", {"start": v(-79.68, -56.95) * mm, "end": v(-79.76, -57.06) * mm});
            skLineSegment(sketch, "E647", {"start": v(-79.76, -57.06) * mm, "end": v(-79.84, -57.18) * mm});
            skLineSegment(sketch, "E648", {"start": v(-79.84, -57.18) * mm, "end": v(-79.92, -57.3) * mm});
            skLineSegment(sketch, "E649", {"start": v(-79.92, -57.3) * mm, "end": v(-80, -57.41) * mm});
            skLineSegment(sketch, "E650", {"start": v(-80, -57.41) * mm, "end": v(-80.09, -57.53) * mm});
            skLineSegment(sketch, "E651", {"start": v(-80.09, -57.53) * mm, "end": v(-80.17, -57.66) * mm});
            skLineSegment(sketch, "E652", {"start": v(-80.17, -57.66) * mm, "end": v(-80.25, -57.78) * mm});
            skLineSegment(sketch, "E653", {"start": v(-80.25, -57.78) * mm, "end": v(-80.34, -57.9) * mm});
            skLineSegment(sketch, "E654", {"start": v(-80.34, -57.9) * mm, "end": v(-80.42, -58.03) * mm});
            skLineSegment(sketch, "E655", {"start": v(-80.42, -58.03) * mm, "end": v(-80.5, -58.16) * mm});
            skLineSegment(sketch, "E656", {"start": v(-80.5, -58.16) * mm, "end": v(-80.6, -58.3) * mm});
            skLineSegment(sketch, "E657", {"start": v(-80.6, -58.3) * mm, "end": v(-80.68, -58.42) * mm});
            skLineSegment(sketch, "E658", {"start": v(-80.68, -58.42) * mm, "end": v(-80.76, -58.56) * mm});
            skLineSegment(sketch, "E659", {"start": v(-80.76, -58.56) * mm, "end": v(-80.85, -58.7) * mm});
            skLineSegment(sketch, "E660", {"start": v(-80.85, -58.7) * mm, "end": v(-80.94, -58.83) * mm});
            skLineSegment(sketch, "E661", {"start": v(-80.94, -58.83) * mm, "end": v(-81.02, -58.97) * mm});
            skLineSegment(sketch, "E662", {"start": v(-81.02, -58.97) * mm, "end": v(-81.11, -59.12) * mm});
            skLineSegment(sketch, "E663", {"start": v(-81.11, -59.12) * mm, "end": v(-81.2, -59.26) * mm});
            skLineSegment(sketch, "E664", {"start": v(-81.2, -59.26) * mm, "end": v(-81.29, -59.4) * mm});
            skLineSegment(sketch, "E665", {"start": v(-81.29, -59.4) * mm, "end": v(-81.37, -59.56) * mm});
            skLineSegment(sketch, "E666", {"start": v(-81.37, -59.56) * mm, "end": v(-81.46, -59.7) * mm});
            skLineSegment(sketch, "E667", {"start": v(-81.46, -59.7) * mm, "end": v(-81.55, -59.86) * mm});
            skLineSegment(sketch, "E668", {"start": v(-81.55, -59.86) * mm, "end": v(-81.64, -60.01) * mm});
            skLineSegment(sketch, "E669", {"start": v(-81.64, -60.01) * mm, "end": v(-81.73, -60.17) * mm});
            skLineSegment(sketch, "E670", {"start": v(-81.73, -60.17) * mm, "end": v(-81.82, -60.32) * mm});
            skLineSegment(sketch, "E671", {"start": v(-81.82, -60.32) * mm, "end": v(-81.9, -60.48) * mm});
            skLineSegment(sketch, "E672", {"start": v(-81.9, -60.48) * mm, "end": v(-82, -60.64) * mm});
            skLineSegment(sketch, "E673", {"start": v(-82, -60.64) * mm, "end": v(-82.09, -60.8) * mm});
            skLineSegment(sketch, "E674", {"start": v(-82.09, -60.8) * mm, "end": v(-82.18, -60.97) * mm});
            skLineSegment(sketch, "E675", {"start": v(-82.18, -60.97) * mm, "end": v(-82.27, -61.14) * mm});
            skLineSegment(sketch, "E676", {"start": v(-82.27, -61.14) * mm, "end": v(-82.22, -61.2) * mm});
            skLineSegment(sketch, "E677", {"start": v(-82.22, -61.2) * mm, "end": v(-81.27, -62.46) * mm});
            skLineSegment(sketch, "E678", {"start": v(-81.27, -62.46) * mm, "end": v(-81.22, -62.52) * mm});
            skLineSegment(sketch, "E679", {"start": v(-81.22, -62.52) * mm, "end": v(-81.03, -62.48) * mm});
            skLineSegment(sketch, "E680", {"start": v(-81.03, -62.48) * mm, "end": v(-80.85, -62.44) * mm});
            skLineSegment(sketch, "E681", {"start": v(-80.85, -62.44) * mm, "end": v(-80.67, -62.4) * mm});
            skLineSegment(sketch, "E682", {"start": v(-80.67, -62.4) * mm, "end": v(-80.5, -62.36) * mm});
            skLineSegment(sketch, "E683", {"start": v(-80.5, -62.36) * mm, "end": v(-80.31, -62.31) * mm});
            skLineSegment(sketch, "E684", {"start": v(-80.31, -62.31) * mm, "end": v(-80.14, -62.27) * mm});
            skLineSegment(sketch, "E685", {"start": v(-80.14, -62.27) * mm, "end": v(-79.96, -62.23) * mm});
            skLineSegment(sketch, "E686", {"start": v(-79.96, -62.23) * mm, "end": v(-79.8, -62.18) * mm});
            skLineSegment(sketch, "E687", {"start": v(-79.8, -62.18) * mm, "end": v(-79.62, -62.14) * mm});
            skLineSegment(sketch, "E688", {"start": v(-79.62, -62.14) * mm, "end": v(-79.45, -62.1) * mm});
            skLineSegment(sketch, "E689", {"start": v(-79.45, -62.1) * mm, "end": v(-79.29, -62.05) * mm});
            skLineSegment(sketch, "E690", {"start": v(-79.29, -62.05) * mm, "end": v(-79.12, -62) * mm});
            skLineSegment(sketch, "E691", {"start": v(-79.12, -62) * mm, "end": v(-78.96, -61.96) * mm});
            skLineSegment(sketch, "E692", {"start": v(-78.96, -61.96) * mm, "end": v(-78.8, -61.92) * mm});
            skLineSegment(sketch, "E693", {"start": v(-78.8, -61.92) * mm, "end": v(-78.64, -61.87) * mm});
            skLineSegment(sketch, "E694", {"start": v(-78.64, -61.87) * mm, "end": v(-78.48, -61.83) * mm});
            skLineSegment(sketch, "E695", {"start": v(-78.48, -61.83) * mm, "end": v(-78.33, -61.78) * mm});
            skLineSegment(sketch, "E696", {"start": v(-78.33, -61.78) * mm, "end": v(-78.18, -61.73) * mm});
            skLineSegment(sketch, "E697", {"start": v(-78.18, -61.73) * mm, "end": v(-78.02, -61.69) * mm});
            skLineSegment(sketch, "E698", {"start": v(-78.02, -61.69) * mm, "end": v(-77.88, -61.64) * mm});
            skLineSegment(sketch, "E699", {"start": v(-77.88, -61.64) * mm, "end": v(-77.73, -61.6) * mm});
            skLineSegment(sketch, "E700", {"start": v(-77.73, -61.6) * mm, "end": v(-77.58, -61.55) * mm});
            skLineSegment(sketch, "E701", {"start": v(-77.58, -61.55) * mm, "end": v(-77.44, -61.5) * mm});
            skLineSegment(sketch, "E702", {"start": v(-77.44, -61.5) * mm, "end": v(-77.3, -61.45) * mm});
            skLineSegment(sketch, "E703", {"start": v(-77.3, -61.45) * mm, "end": v(-77.16, -61.4) * mm});
            skLineSegment(sketch, "E704", {"start": v(-77.16, -61.4) * mm, "end": v(-77.02, -61.36) * mm});
            skLineSegment(sketch, "E705", {"start": v(-77.02, -61.36) * mm, "end": v(-76.88, -61.31) * mm});
            skLineSegment(sketch, "E706", {"start": v(-76.88, -61.31) * mm, "end": v(-76.75, -61.27) * mm});
            skLineSegment(sketch, "E707", {"start": v(-76.75, -61.27) * mm, "end": v(-76.62, -61.22) * mm});
            skLineSegment(sketch, "E708", {"start": v(-76.62, -61.22) * mm, "end": v(-76.49, -61.17) * mm});
            skLineSegment(sketch, "E709", {"start": v(-76.49, -61.17) * mm, "end": v(-76.36, -61.13) * mm});
            skLineSegment(sketch, "E710", {"start": v(-76.36, -61.13) * mm, "end": v(-76.23, -61.08) * mm});
            skLineSegment(sketch, "E711", {"start": v(-76.23, -61.08) * mm, "end": v(-76.1, -61.03) * mm});
            skLineSegment(sketch, "E712", {"start": v(-76.1, -61.03) * mm, "end": v(-75.98, -60.99) * mm});
            skLineSegment(sketch, "E713", {"start": v(-75.98, -60.99) * mm, "end": v(-75.86, -60.94) * mm});
            skLineSegment(sketch, "E714", {"start": v(-75.86, -60.94) * mm, "end": v(-75.74, -60.9) * mm});
            skLineSegment(sketch, "E715", {"start": v(-75.74, -60.9) * mm, "end": v(-75.1, -61.59) * mm});
            skLineSegment(sketch, "E716", {"start": v(-75.1, -61.59) * mm, "end": v(-74.55, -62.35) * mm});
            skLineSegment(sketch, "E717", {"start": v(-74.55, -62.35) * mm, "end": v(-74.62, -62.46) * mm});
            skLineSegment(sketch, "E718", {"start": v(-74.62, -62.46) * mm, "end": v(-74.68, -62.57) * mm});
            skLineSegment(sketch, "E719", {"start": v(-74.68, -62.57) * mm, "end": v(-74.75, -62.68) * mm});
            skLineSegment(sketch, "E720", {"start": v(-74.75, -62.68) * mm, "end": v(-74.82, -62.8) * mm});
            skLineSegment(sketch, "E721", {"start": v(-74.82, -62.8) * mm, "end": v(-74.9, -62.91) * mm});
            skLineSegment(sketch, "E722", {"start": v(-74.9, -62.91) * mm, "end": v(-74.97, -63.03) * mm});
            skLineSegment(sketch, "E723", {"start": v(-74.97, -63.03) * mm, "end": v(-75.04, -63.15) * mm});
            skLineSegment(sketch, "E724", {"start": v(-75.04, -63.15) * mm, "end": v(-75.1, -63.27) * mm});
            skLineSegment(sketch, "E725", {"start": v(-75.1, -63.27) * mm, "end": v(-75.18, -63.39) * mm});
            skLineSegment(sketch, "E726", {"start": v(-75.18, -63.39) * mm, "end": v(-75.25, -63.51) * mm});
            skLineSegment(sketch, "E727", {"start": v(-75.25, -63.51) * mm, "end": v(-75.33, -63.64) * mm});
            skLineSegment(sketch, "E728", {"start": v(-75.33, -63.64) * mm, "end": v(-75.4, -63.77) * mm});
            skLineSegment(sketch, "E729", {"start": v(-75.4, -63.77) * mm, "end": v(-75.47, -63.9) * mm});
            skLineSegment(sketch, "E730", {"start": v(-75.47, -63.9) * mm, "end": v(-75.55, -64.03) * mm});
            skLineSegment(sketch, "E731", {"start": v(-75.55, -64.03) * mm, "end": v(-75.62, -64.16) * mm});
            skLineSegment(sketch, "E732", {"start": v(-75.62, -64.16) * mm, "end": v(-75.7, -64.3) * mm});
            skLineSegment(sketch, "E733", {"start": v(-75.7, -64.3) * mm, "end": v(-75.77, -64.44) * mm});
            skLineSegment(sketch, "E734", {"start": v(-75.77, -64.44) * mm, "end": v(-75.85, -64.57) * mm});
            skLineSegment(sketch, "E735", {"start": v(-75.85, -64.57) * mm, "end": v(-75.92, -64.72) * mm});
            skLineSegment(sketch, "E736", {"start": v(-75.92, -64.72) * mm, "end": v(-76, -64.86) * mm});
            skLineSegment(sketch, "E737", {"start": v(-76, -64.86) * mm, "end": v(-76.07, -65) * mm});
            skLineSegment(sketch, "E738", {"start": v(-76.07, -65) * mm, "end": v(-76.15, -65.15) * mm});
            skLineSegment(sketch, "E739", {"start": v(-76.15, -65.15) * mm, "end": v(-76.22, -65.3) * mm});
            skLineSegment(sketch, "E740", {"start": v(-76.22, -65.3) * mm, "end": v(-76.3, -65.45) * mm});
            skLineSegment(sketch, "E741", {"start": v(-76.3, -65.45) * mm, "end": v(-76.37, -65.6) * mm});
            skLineSegment(sketch, "E742", {"start": v(-76.37, -65.6) * mm, "end": v(-76.45, -65.76) * mm});
            skLineSegment(sketch, "E743", {"start": v(-76.45, -65.76) * mm, "end": v(-76.53, -65.91) * mm});
            skLineSegment(sketch, "E744", {"start": v(-76.53, -65.91) * mm, "end": v(-76.6, -66.07) * mm});
            skLineSegment(sketch, "E745", {"start": v(-76.6, -66.07) * mm, "end": v(-76.68, -66.23) * mm});
            skLineSegment(sketch, "E746", {"start": v(-76.68, -66.23) * mm, "end": v(-76.76, -66.4) * mm});
            skLineSegment(sketch, "E747", {"start": v(-76.76, -66.4) * mm, "end": v(-76.83, -66.56) * mm});
            skLineSegment(sketch, "E748", {"start": v(-76.83, -66.56) * mm, "end": v(-76.9, -66.72) * mm});
            skLineSegment(sketch, "E749", {"start": v(-76.9, -66.72) * mm, "end": v(-76.99, -66.9) * mm});
            skLineSegment(sketch, "E750", {"start": v(-76.99, -66.9) * mm, "end": v(-77.06, -67.06) * mm});
            skLineSegment(sketch, "E751", {"start": v(-77.06, -67.06) * mm, "end": v(-77.14, -67.23) * mm});
            skLineSegment(sketch, "E752", {"start": v(-77.14, -67.23) * mm, "end": v(-77.22, -67.4) * mm});
            skLineSegment(sketch, "E753", {"start": v(-77.22, -67.4) * mm, "end": v(-77.16, -67.47) * mm});
            skLineSegment(sketch, "E754", {"start": v(-77.16, -67.47) * mm, "end": v(-76.12, -68.64) * mm});
            skLineSegment(sketch, "E755", {"start": v(-76.12, -68.64) * mm, "end": v(-76.06, -68.7) * mm});
            skLineSegment(sketch, "E756", {"start": v(-76.06, -68.7) * mm, "end": v(-75.88, -68.65) * mm});
            skLineSegment(sketch, "E757", {"start": v(-75.88, -68.65) * mm, "end": v(-75.7, -68.6) * mm});
            skLineSegment(sketch, "E758", {"start": v(-75.7, -68.6) * mm, "end": v(-75.53, -68.54) * mm});
            skLineSegment(sketch, "E759", {"start": v(-75.53, -68.54) * mm, "end": v(-75.35, -68.48) * mm});
            skLineSegment(sketch, "E760", {"start": v(-75.35, -68.48) * mm, "end": v(-75.18, -68.42) * mm});
            skLineSegment(sketch, "E761", {"start": v(-75.18, -68.42) * mm, "end": v(-75, -68.37) * mm});
            skLineSegment(sketch, "E762", {"start": v(-75, -68.37) * mm, "end": v(-74.83, -68.3) * mm});
            skLineSegment(sketch, "E763", {"start": v(-74.83, -68.3) * mm, "end": v(-74.67, -68.25) * mm});
            skLineSegment(sketch, "E764", {"start": v(-74.67, -68.25) * mm, "end": v(-74.5, -68.2) * mm});
            skLineSegment(sketch, "E765", {"start": v(-74.5, -68.2) * mm, "end": v(-74.34, -68.14) * mm});
            skLineSegment(sketch, "E766", {"start": v(-74.34, -68.14) * mm, "end": v(-74.17, -68.08) * mm});
            skLineSegment(sketch, "E767", {"start": v(-74.17, -68.08) * mm, "end": v(-74.01, -68.02) * mm});
            skLineSegment(sketch, "E768", {"start": v(-74.01, -68.02) * mm, "end": v(-73.85, -67.97) * mm});
            skLineSegment(sketch, "E769", {"start": v(-73.85, -67.97) * mm, "end": v(-73.7, -67.9) * mm});
            skLineSegment(sketch, "E770", {"start": v(-73.7, -67.9) * mm, "end": v(-73.54, -67.85) * mm});
            skLineSegment(sketch, "E771", {"start": v(-73.54, -67.85) * mm, "end": v(-73.4, -67.8) * mm});
            skLineSegment(sketch, "E772", {"start": v(-73.4, -67.8) * mm, "end": v(-73.24, -67.73) * mm});
            skLineSegment(sketch, "E773", {"start": v(-73.24, -67.73) * mm, "end": v(-73.1, -67.68) * mm});
            skLineSegment(sketch, "E774", {"start": v(-73.1, -67.68) * mm, "end": v(-72.94, -67.62) * mm});
            skLineSegment(sketch, "E775", {"start": v(-72.94, -67.62) * mm, "end": v(-72.8, -67.56) * mm});
            skLineSegment(sketch, "E776", {"start": v(-72.8, -67.56) * mm, "end": v(-72.66, -67.5) * mm});
            skLineSegment(sketch, "E777", {"start": v(-72.66, -67.5) * mm, "end": v(-72.51, -67.45) * mm});
            skLineSegment(sketch, "E778", {"start": v(-72.51, -67.45) * mm, "end": v(-72.37, -67.39) * mm});
            skLineSegment(sketch, "E779", {"start": v(-72.37, -67.39) * mm, "end": v(-72.24, -67.33) * mm});
            skLineSegment(sketch, "E780", {"start": v(-72.24, -67.33) * mm, "end": v(-72.1, -67.27) * mm});
            skLineSegment(sketch, "E781", {"start": v(-72.1, -67.27) * mm, "end": v(-71.97, -67.21) * mm});
            skLineSegment(sketch, "E782", {"start": v(-71.97, -67.21) * mm, "end": v(-71.84, -67.16) * mm});
            skLineSegment(sketch, "E783", {"start": v(-71.84, -67.16) * mm, "end": v(-71.7, -67.1) * mm});
            skLineSegment(sketch, "E784", {"start": v(-71.7, -67.1) * mm, "end": v(-71.58, -67.04) * mm});
            skLineSegment(sketch, "E785", {"start": v(-71.58, -67.04) * mm, "end": v(-71.45, -66.99) * mm});
            skLineSegment(sketch, "E786", {"start": v(-71.45, -66.99) * mm, "end": v(-71.33, -66.93) * mm});
            skLineSegment(sketch, "E787", {"start": v(-71.33, -66.93) * mm, "end": v(-71.2, -66.87) * mm});
            skLineSegment(sketch, "E788", {"start": v(-71.2, -66.87) * mm, "end": v(-71.08, -66.82) * mm});
            skLineSegment(sketch, "E789", {"start": v(-71.08, -66.82) * mm, "end": v(-70.96, -66.76) * mm});
            skLineSegment(sketch, "E790", {"start": v(-70.96, -66.76) * mm, "end": v(-70.85, -66.7) * mm});
            skLineSegment(sketch, "E791", {"start": v(-70.85, -66.7) * mm, "end": v(-70.73, -66.65) * mm});
            skLineSegment(sketch, "E792", {"start": v(-70.73, -66.65) * mm, "end": v(-70.04, -67.3) * mm});
            skLineSegment(sketch, "E793", {"start": v(-70.04, -67.3) * mm, "end": v(-69.42, -68.01) * mm});
            skLineSegment(sketch, "E794", {"start": v(-69.42, -68.01) * mm, "end": v(-69.48, -68.12) * mm});
            skLineSegment(sketch, "E795", {"start": v(-69.48, -68.12) * mm, "end": v(-69.55, -68.24) * mm});
            skLineSegment(sketch, "E796", {"start": v(-69.55, -68.24) * mm, "end": v(-69.6, -68.35) * mm});
            skLineSegment(sketch, "E797", {"start": v(-69.6, -68.35) * mm, "end": v(-69.67, -68.47) * mm});
            skLineSegment(sketch, "E798", {"start": v(-69.67, -68.47) * mm, "end": v(-69.73, -68.6) * mm});
            skLineSegment(sketch, "E799", {"start": v(-69.73, -68.6) * mm, "end": v(-69.8, -68.72) * mm});
            skLineSegment(sketch, "E800", {"start": v(-69.8, -68.72) * mm, "end": v(-69.85, -68.84) * mm});
            skLineSegment(sketch, "E801", {"start": v(-69.85, -68.84) * mm, "end": v(-69.91, -68.97) * mm});
            skLineSegment(sketch, "E802", {"start": v(-69.91, -68.97) * mm, "end": v(-69.98, -69.1) * mm});
            skLineSegment(sketch, "E803", {"start": v(-69.98, -69.1) * mm, "end": v(-70.04, -69.22) * mm});
            skLineSegment(sketch, "E804", {"start": v(-70.04, -69.22) * mm, "end": v(-70.1, -69.35) * mm});
            skLineSegment(sketch, "E805", {"start": v(-70.1, -69.35) * mm, "end": v(-70.16, -69.49) * mm});
            skLineSegment(sketch, "E806", {"start": v(-70.16, -69.49) * mm, "end": v(-70.23, -69.62) * mm});
            skLineSegment(sketch, "E807", {"start": v(-70.23, -69.62) * mm, "end": v(-70.3, -69.76) * mm});
            skLineSegment(sketch, "E808", {"start": v(-70.3, -69.76) * mm, "end": v(-70.35, -69.9) * mm});
            skLineSegment(sketch, "E809", {"start": v(-70.35, -69.9) * mm, "end": v(-70.42, -70.04) * mm});
            skLineSegment(sketch, "E810", {"start": v(-70.42, -70.04) * mm, "end": v(-70.48, -70.18) * mm});
            skLineSegment(sketch, "E811", {"start": v(-70.48, -70.18) * mm, "end": v(-70.55, -70.33) * mm});
            skLineSegment(sketch, "E812", {"start": v(-70.55, -70.33) * mm, "end": v(-70.6, -70.47) * mm});
            skLineSegment(sketch, "E813", {"start": v(-70.6, -70.47) * mm, "end": v(-70.67, -70.62) * mm});
            skLineSegment(sketch, "E814", {"start": v(-70.67, -70.62) * mm, "end": v(-70.74, -70.77) * mm});
            skLineSegment(sketch, "E815", {"start": v(-70.74, -70.77) * mm, "end": v(-70.8, -70.92) * mm});
            skLineSegment(sketch, "E816", {"start": v(-70.8, -70.92) * mm, "end": v(-70.86, -71.08) * mm});
            skLineSegment(sketch, "E817", {"start": v(-70.86, -71.08) * mm, "end": v(-70.93, -71.23) * mm});
            skLineSegment(sketch, "E818", {"start": v(-70.93, -71.23) * mm, "end": v(-71, -71.4) * mm});
            skLineSegment(sketch, "E819", {"start": v(-71, -71.4) * mm, "end": v(-71.06, -71.55) * mm});
            skLineSegment(sketch, "E820", {"start": v(-71.06, -71.55) * mm, "end": v(-71.12, -71.71) * mm});
            skLineSegment(sketch, "E821", {"start": v(-71.12, -71.71) * mm, "end": v(-71.18, -71.88) * mm});
            skLineSegment(sketch, "E822", {"start": v(-71.18, -71.88) * mm, "end": v(-71.25, -72.04) * mm});
            skLineSegment(sketch, "E823", {"start": v(-71.25, -72.04) * mm, "end": v(-71.31, -72.21) * mm});
            skLineSegment(sketch, "E824", {"start": v(-71.31, -72.21) * mm, "end": v(-71.37, -72.38) * mm});
            skLineSegment(sketch, "E825", {"start": v(-71.37, -72.38) * mm, "end": v(-71.44, -72.55) * mm});
            skLineSegment(sketch, "E826", {"start": v(-71.44, -72.55) * mm, "end": v(-71.5, -72.72) * mm});
            skLineSegment(sketch, "E827", {"start": v(-71.5, -72.72) * mm, "end": v(-71.56, -72.9) * mm});
            skLineSegment(sketch, "E828", {"start": v(-71.56, -72.9) * mm, "end": v(-71.63, -73.08) * mm});
            skLineSegment(sketch, "E829", {"start": v(-71.63, -73.08) * mm, "end": v(-71.69, -73.26) * mm});
            skLineSegment(sketch, "E830", {"start": v(-71.69, -73.26) * mm, "end": v(-71.63, -73.31) * mm});
            skLineSegment(sketch, "E831", {"start": v(-71.63, -73.31) * mm, "end": v(-70.5, -74.4) * mm});
            skLineSegment(sketch, "E832", {"start": v(-70.5, -74.4) * mm, "end": v(-70.44, -74.46) * mm});
            skLineSegment(sketch, "E833", {"start": v(-70.44, -74.46) * mm, "end": v(-70.26, -74.39) * mm});
            skLineSegment(sketch, "E834", {"start": v(-70.26, -74.39) * mm, "end": v(-70.09, -74.32) * mm});
            skLineSegment(sketch, "E835", {"start": v(-70.09, -74.32) * mm, "end": v(-69.92, -74.25) * mm});
            skLineSegment(sketch, "E836", {"start": v(-69.92, -74.25) * mm, "end": v(-69.74, -74.18) * mm});
            skLineSegment(sketch, "E837", {"start": v(-69.74, -74.18) * mm, "end": v(-69.58, -74.11) * mm});
            skLineSegment(sketch, "E838", {"start": v(-69.58, -74.11) * mm, "end": v(-69.4, -74.04) * mm});
            skLineSegment(sketch, "E839", {"start": v(-69.4, -74.04) * mm, "end": v(-69.24, -73.97) * mm});
            skLineSegment(sketch, "E840", {"start": v(-69.24, -73.97) * mm, "end": v(-69.08, -73.9) * mm});
            skLineSegment(sketch, "E841", {"start": v(-69.08, -73.9) * mm, "end": v(-68.92, -73.83) * mm});
            skLineSegment(sketch, "E842", {"start": v(-68.92, -73.83) * mm, "end": v(-68.76, -73.76) * mm});
            skLineSegment(sketch, "E843", {"start": v(-68.76, -73.76) * mm, "end": v(-68.6, -73.7) * mm});
            skLineSegment(sketch, "E844", {"start": v(-68.6, -73.7) * mm, "end": v(-68.45, -73.62) * mm});
            skLineSegment(sketch, "E845", {"start": v(-68.45, -73.62) * mm, "end": v(-68.3, -73.55) * mm});
            skLineSegment(sketch, "E846", {"start": v(-68.3, -73.55) * mm, "end": v(-68.14, -73.48) * mm});
            skLineSegment(sketch, "E847", {"start": v(-68.14, -73.48) * mm, "end": v(-68, -73.41) * mm});
            skLineSegment(sketch, "E848", {"start": v(-68, -73.41) * mm, "end": v(-67.85, -73.34) * mm});
            skLineSegment(sketch, "E849", {"start": v(-67.85, -73.34) * mm, "end": v(-67.7, -73.27) * mm});
            skLineSegment(sketch, "E850", {"start": v(-67.7, -73.27) * mm, "end": v(-67.56, -73.2) * mm});
            skLineSegment(sketch, "E851", {"start": v(-67.56, -73.2) * mm, "end": v(-67.41, -73.13) * mm});
            skLineSegment(sketch, "E852", {"start": v(-67.41, -73.13) * mm, "end": v(-67.27, -73.06) * mm});
            skLineSegment(sketch, "E853", {"start": v(-67.27, -73.06) * mm, "end": v(-67.14, -73) * mm});
            skLineSegment(sketch, "E854", {"start": v(-67.14, -73) * mm, "end": v(-67, -72.93) * mm});
            skLineSegment(sketch, "E855", {"start": v(-67, -72.93) * mm, "end": v(-66.86, -72.86) * mm});
            skLineSegment(sketch, "E856", {"start": v(-66.86, -72.86) * mm, "end": v(-66.73, -72.8) * mm});
            skLineSegment(sketch, "E857", {"start": v(-66.73, -72.8) * mm, "end": v(-66.6, -72.72) * mm});
            skLineSegment(sketch, "E858", {"start": v(-66.6, -72.72) * mm, "end": v(-66.47, -72.65) * mm});
            skLineSegment(sketch, "E859", {"start": v(-66.47, -72.65) * mm, "end": v(-66.35, -72.59) * mm});
            skLineSegment(sketch, "E860", {"start": v(-66.35, -72.59) * mm, "end": v(-66.22, -72.52) * mm});
            skLineSegment(sketch, "E861", {"start": v(-66.22, -72.52) * mm, "end": v(-66.1, -72.45) * mm});
            skLineSegment(sketch, "E862", {"start": v(-66.1, -72.45) * mm, "end": v(-65.98, -72.39) * mm});
            skLineSegment(sketch, "E863", {"start": v(-65.98, -72.39) * mm, "end": v(-65.86, -72.32) * mm});
            skLineSegment(sketch, "E864", {"start": v(-65.86, -72.32) * mm, "end": v(-65.74, -72.25) * mm});
            skLineSegment(sketch, "E865", {"start": v(-65.74, -72.25) * mm, "end": v(-65.62, -72.19) * mm});
            skLineSegment(sketch, "E866", {"start": v(-65.62, -72.19) * mm, "end": v(-65.5, -72.12) * mm});
            skLineSegment(sketch, "E867", {"start": v(-65.5, -72.12) * mm, "end": v(-65.4, -72.06) * mm});
            skLineSegment(sketch, "E868", {"start": v(-65.4, -72.06) * mm, "end": v(-65.28, -72) * mm});
            skLineSegment(sketch, "E869", {"start": v(-65.28, -72) * mm, "end": v(-64.54, -72.58) * mm});
            skLineSegment(sketch, "E870", {"start": v(-64.54, -72.58) * mm, "end": v(-63.87, -73.25) * mm});
            skLineSegment(sketch, "E871", {"start": v(-63.87, -73.25) * mm, "end": v(-63.93, -73.36) * mm});
            skLineSegment(sketch, "E872", {"start": v(-63.93, -73.36) * mm, "end": v(-63.98, -73.48) * mm});
            skLineSegment(sketch, "E873", {"start": v(-63.98, -73.48) * mm, "end": v(-64.03, -73.6) * mm});
            skLineSegment(sketch, "E874", {"start": v(-64.03, -73.6) * mm, "end": v(-64.08, -73.73) * mm});
            skLineSegment(sketch, "E875", {"start": v(-64.08, -73.73) * mm, "end": v(-64.13, -73.85) * mm});
            skLineSegment(sketch, "E876", {"start": v(-64.13, -73.85) * mm, "end": v(-64.18, -73.98) * mm});
            skLineSegment(sketch, "E877", {"start": v(-64.18, -73.98) * mm, "end": v(-64.24, -74.1) * mm});
            skLineSegment(sketch, "E878", {"start": v(-64.24, -74.1) * mm, "end": v(-64.29, -74.24) * mm});
            skLineSegment(sketch, "E879", {"start": v(-64.29, -74.24) * mm, "end": v(-64.34, -74.37) * mm});
            skLineSegment(sketch, "E880", {"start": v(-64.34, -74.37) * mm, "end": v(-64.4, -74.5) * mm});
            skLineSegment(sketch, "E881", {"start": v(-64.4, -74.5) * mm, "end": v(-64.44, -74.64) * mm});
            skLineSegment(sketch, "E882", {"start": v(-64.44, -74.64) * mm, "end": v(-64.5, -74.78) * mm});
            skLineSegment(sketch, "E883", {"start": v(-64.5, -74.78) * mm, "end": v(-64.55, -74.92) * mm});
            skLineSegment(sketch, "E884", {"start": v(-64.55, -74.92) * mm, "end": v(-64.6, -75.06) * mm});
            skLineSegment(sketch, "E885", {"start": v(-64.6, -75.06) * mm, "end": v(-64.65, -75.2) * mm});
            skLineSegment(sketch, "E886", {"start": v(-64.65, -75.2) * mm, "end": v(-64.7, -75.35) * mm});
            skLineSegment(sketch, "E887", {"start": v(-64.7, -75.35) * mm, "end": v(-64.76, -75.5) * mm});
            skLineSegment(sketch, "E888", {"start": v(-64.76, -75.5) * mm, "end": v(-64.8, -75.64) * mm});
            skLineSegment(sketch, "E889", {"start": v(-64.8, -75.64) * mm, "end": v(-64.86, -75.8) * mm});
            skLineSegment(sketch, "E890", {"start": v(-64.86, -75.8) * mm, "end": v(-64.91, -75.95) * mm});
            skLineSegment(sketch, "E891", {"start": v(-64.91, -75.95) * mm, "end": v(-64.97, -76.1) * mm});
            skLineSegment(sketch, "E892", {"start": v(-64.97, -76.1) * mm, "end": v(-65.02, -76.26) * mm});
            skLineSegment(sketch, "E893", {"start": v(-65.02, -76.26) * mm, "end": v(-65.07, -76.42) * mm});
            skLineSegment(sketch, "E894", {"start": v(-65.07, -76.42) * mm, "end": v(-65.12, -76.58) * mm});
            skLineSegment(sketch, "E895", {"start": v(-65.12, -76.58) * mm, "end": v(-65.17, -76.74) * mm});
            skLineSegment(sketch, "E896", {"start": v(-65.17, -76.74) * mm, "end": v(-65.22, -76.9) * mm});
            skLineSegment(sketch, "E897", {"start": v(-65.22, -76.9) * mm, "end": v(-65.27, -77.07) * mm});
            skLineSegment(sketch, "E898", {"start": v(-65.27, -77.07) * mm, "end": v(-65.32, -77.24) * mm});
            skLineSegment(sketch, "E899", {"start": v(-65.32, -77.24) * mm, "end": v(-65.38, -77.41) * mm});
            skLineSegment(sketch, "E900", {"start": v(-65.38, -77.41) * mm, "end": v(-65.43, -77.58) * mm});
            skLineSegment(sketch, "E901", {"start": v(-65.43, -77.58) * mm, "end": v(-65.48, -77.76) * mm});
            skLineSegment(sketch, "E902", {"start": v(-65.48, -77.76) * mm, "end": v(-65.52, -77.93) * mm});
            skLineSegment(sketch, "E903", {"start": v(-65.52, -77.93) * mm, "end": v(-65.57, -78.1) * mm});
            skLineSegment(sketch, "E904", {"start": v(-65.57, -78.1) * mm, "end": v(-65.62, -78.29) * mm});
            skLineSegment(sketch, "E905", {"start": v(-65.62, -78.29) * mm, "end": v(-65.67, -78.47) * mm});
            skLineSegment(sketch, "E906", {"start": v(-65.67, -78.47) * mm, "end": v(-65.72, -78.65) * mm});
            skLineSegment(sketch, "E907", {"start": v(-65.72, -78.65) * mm, "end": v(-65.66, -78.7) * mm});
            skLineSegment(sketch, "E908", {"start": v(-65.66, -78.7) * mm, "end": v(-64.45, -79.7) * mm});
            skLineSegment(sketch, "E909", {"start": v(-64.45, -79.7) * mm, "end": v(-64.38, -79.76) * mm});
            skLineSegment(sketch, "E910", {"start": v(-64.38, -79.76) * mm, "end": v(-64.2, -79.67) * mm});
            skLineSegment(sketch, "E911", {"start": v(-64.2, -79.67) * mm, "end": v(-64.04, -79.59) * mm});
            skLineSegment(sketch, "E912", {"start": v(-64.04, -79.59) * mm, "end": v(-63.87, -79.5) * mm});
            skLineSegment(sketch, "E913", {"start": v(-63.87, -79.5) * mm, "end": v(-63.7, -79.42) * mm});
            skLineSegment(sketch, "E914", {"start": v(-63.7, -79.42) * mm, "end": v(-63.55, -79.34) * mm});
            skLineSegment(sketch, "E915", {"start": v(-63.55, -79.34) * mm, "end": v(-63.39, -79.26) * mm});
            skLineSegment(sketch, "E916", {"start": v(-63.39, -79.26) * mm, "end": v(-63.23, -79.17) * mm});
            skLineSegment(sketch, "E917", {"start": v(-63.23, -79.17) * mm, "end": v(-63.07, -79.1) * mm});
            skLineSegment(sketch, "E918", {"start": v(-63.07, -79.1) * mm, "end": v(-62.91, -79.01) * mm});
            skLineSegment(sketch, "E919", {"start": v(-62.91, -79.01) * mm, "end": v(-62.76, -78.93) * mm});
            skLineSegment(sketch, "E920", {"start": v(-62.76, -78.93) * mm, "end": v(-62.61, -78.85) * mm});
            skLineSegment(sketch, "E921", {"start": v(-62.61, -78.85) * mm, "end": v(-62.46, -78.76) * mm});
            skLineSegment(sketch, "E922", {"start": v(-62.46, -78.76) * mm, "end": v(-62.31, -78.68) * mm});
            skLineSegment(sketch, "E923", {"start": v(-62.31, -78.68) * mm, "end": v(-62.17, -78.6) * mm});
            skLineSegment(sketch, "E924", {"start": v(-62.17, -78.6) * mm, "end": v(-62.02, -78.52) * mm});
            skLineSegment(sketch, "E925", {"start": v(-62.02, -78.52) * mm, "end": v(-61.88, -78.44) * mm});
            skLineSegment(sketch, "E926", {"start": v(-61.88, -78.44) * mm, "end": v(-61.74, -78.36) * mm});
            skLineSegment(sketch, "E927", {"start": v(-61.74, -78.36) * mm, "end": v(-61.6, -78.28) * mm});
            skLineSegment(sketch, "E928", {"start": v(-61.6, -78.28) * mm, "end": v(-61.47, -78.2) * mm});
            skLineSegment(sketch, "E929", {"start": v(-61.47, -78.2) * mm, "end": v(-61.33, -78.12) * mm});
            skLineSegment(sketch, "E930", {"start": v(-61.33, -78.12) * mm, "end": v(-61.2, -78.04) * mm});
            skLineSegment(sketch, "E931", {"start": v(-61.2, -78.04) * mm, "end": v(-61.07, -77.96) * mm});
            skLineSegment(sketch, "E932", {"start": v(-61.07, -77.96) * mm, "end": v(-60.94, -77.88) * mm});
            skLineSegment(sketch, "E933", {"start": v(-60.94, -77.88) * mm, "end": v(-60.82, -77.8) * mm});
            skLineSegment(sketch, "E934", {"start": v(-60.82, -77.8) * mm, "end": v(-60.7, -77.72) * mm});
            skLineSegment(sketch, "E935", {"start": v(-60.7, -77.72) * mm, "end": v(-60.57, -77.65) * mm});
            skLineSegment(sketch, "E936", {"start": v(-60.57, -77.65) * mm, "end": v(-60.45, -77.57) * mm});
            skLineSegment(sketch, "E937", {"start": v(-60.45, -77.57) * mm, "end": v(-60.33, -77.5) * mm});
            skLineSegment(sketch, "E938", {"start": v(-60.33, -77.5) * mm, "end": v(-60.2, -77.42) * mm});
            skLineSegment(sketch, "E939", {"start": v(-60.2, -77.42) * mm, "end": v(-60.1, -77.34) * mm});
            skLineSegment(sketch, "E940", {"start": v(-60.1, -77.34) * mm, "end": v(-59.98, -77.26) * mm});
            skLineSegment(sketch, "E941", {"start": v(-59.98, -77.26) * mm, "end": v(-59.87, -77.19) * mm});
            skLineSegment(sketch, "E942", {"start": v(-59.87, -77.19) * mm, "end": v(-59.76, -77.11) * mm});
            skLineSegment(sketch, "E943", {"start": v(-59.76, -77.11) * mm, "end": v(-59.65, -77.04) * mm});
            skLineSegment(sketch, "E944", {"start": v(-59.65, -77.04) * mm, "end": v(-59.54, -76.97) * mm});
            skLineSegment(sketch, "E945", {"start": v(-59.54, -76.97) * mm, "end": v(-59.43, -76.9) * mm});
            skLineSegment(sketch, "E946", {"start": v(-59.43, -76.9) * mm, "end": v(-58.65, -77.42) * mm});
            skLineSegment(sketch, "E947", {"start": v(-58.65, -77.42) * mm, "end": v(-57.93, -78.03) * mm});
            skLineSegment(sketch, "E948", {"start": v(-57.93, -78.03) * mm, "end": v(-57.97, -78.15) * mm});
            skLineSegment(sketch, "E949", {"start": v(-57.97, -78.15) * mm, "end": v(-58.01, -78.28) * mm});
            skLineSegment(sketch, "E950", {"start": v(-58.01, -78.28) * mm, "end": v(-58.06, -78.4) * mm});
            skLineSegment(sketch, "E951", {"start": v(-58.06, -78.4) * mm, "end": v(-58.1, -78.53) * mm});
            skLineSegment(sketch, "E952", {"start": v(-58.1, -78.53) * mm, "end": v(-58.14, -78.66) * mm});
            skLineSegment(sketch, "E953", {"start": v(-58.14, -78.66) * mm, "end": v(-58.18, -78.79) * mm});
            skLineSegment(sketch, "E954", {"start": v(-58.18, -78.79) * mm, "end": v(-58.22, -78.92) * mm});
            skLineSegment(sketch, "E955", {"start": v(-58.22, -78.92) * mm, "end": v(-58.26, -79.05) * mm});
            skLineSegment(sketch, "E956", {"start": v(-58.26, -79.05) * mm, "end": v(-58.3, -79.19) * mm});
            skLineSegment(sketch, "E957", {"start": v(-58.3, -79.19) * mm, "end": v(-58.35, -79.33) * mm});
            skLineSegment(sketch, "E958", {"start": v(-58.35, -79.33) * mm, "end": v(-58.39, -79.47) * mm});
            skLineSegment(sketch, "E959", {"start": v(-58.39, -79.47) * mm, "end": v(-58.43, -79.6) * mm});
            skLineSegment(sketch, "E960", {"start": v(-58.43, -79.6) * mm, "end": v(-58.47, -79.75) * mm});
            skLineSegment(sketch, "E961", {"start": v(-58.47, -79.75) * mm, "end": v(-58.51, -79.9) * mm});
            skLineSegment(sketch, "E962", {"start": v(-58.51, -79.9) * mm, "end": v(-58.55, -80.04) * mm});
            skLineSegment(sketch, "E963", {"start": v(-58.55, -80.04) * mm, "end": v(-58.6, -80.2) * mm});
            skLineSegment(sketch, "E964", {"start": v(-58.6, -80.2) * mm, "end": v(-58.63, -80.34) * mm});
            skLineSegment(sketch, "E965", {"start": v(-58.63, -80.34) * mm, "end": v(-58.68, -80.5) * mm});
            skLineSegment(sketch, "E966", {"start": v(-58.68, -80.5) * mm, "end": v(-58.72, -80.65) * mm});
            skLineSegment(sketch, "E967", {"start": v(-58.72, -80.65) * mm, "end": v(-58.76, -80.8) * mm});
            skLineSegment(sketch, "E968", {"start": v(-58.76, -80.8) * mm, "end": v(-58.8, -80.97) * mm});
            skLineSegment(sketch, "E969", {"start": v(-58.8, -80.97) * mm, "end": v(-58.83, -81.13) * mm});
            skLineSegment(sketch, "E970", {"start": v(-58.83, -81.13) * mm, "end": v(-58.87, -81.29) * mm});
            skLineSegment(sketch, "E971", {"start": v(-58.87, -81.29) * mm, "end": v(-58.91, -81.45) * mm});
            skLineSegment(sketch, "E972", {"start": v(-58.91, -81.45) * mm, "end": v(-58.95, -81.62) * mm});
            skLineSegment(sketch, "E973", {"start": v(-58.95, -81.62) * mm, "end": v(-58.99, -81.79) * mm});
            skLineSegment(sketch, "E974", {"start": v(-58.99, -81.79) * mm, "end": v(-59.03, -81.96) * mm});
            skLineSegment(sketch, "E975", {"start": v(-59.03, -81.96) * mm, "end": v(-59.06, -82.13) * mm});
            skLineSegment(sketch, "E976", {"start": v(-59.06, -82.13) * mm, "end": v(-59.1, -82.3) * mm});
            skLineSegment(sketch, "E977", {"start": v(-59.1, -82.3) * mm, "end": v(-59.14, -82.48) * mm});
            skLineSegment(sketch, "E978", {"start": v(-59.14, -82.48) * mm, "end": v(-59.17, -82.65) * mm});
            skLineSegment(sketch, "E979", {"start": v(-59.17, -82.65) * mm, "end": v(-59.2, -82.83) * mm});
            skLineSegment(sketch, "E980", {"start": v(-59.2, -82.83) * mm, "end": v(-59.24, -83.01) * mm});
            skLineSegment(sketch, "E981", {"start": v(-59.24, -83.01) * mm, "end": v(-59.28, -83.2) * mm});
            skLineSegment(sketch, "E982", {"start": v(-59.28, -83.2) * mm, "end": v(-59.31, -83.38) * mm});
            skLineSegment(sketch, "E983", {"start": v(-59.31, -83.38) * mm, "end": v(-59.35, -83.57) * mm});
            skLineSegment(sketch, "E984", {"start": v(-59.35, -83.57) * mm, "end": v(-59.28, -83.62) * mm});
            skLineSegment(sketch, "E985", {"start": v(-59.28, -83.62) * mm, "end": v(-58, -84.52) * mm});
            skLineSegment(sketch, "E986", {"start": v(-58, -84.52) * mm, "end": v(-57.92, -84.56) * mm});
            skLineSegment(sketch, "E987", {"start": v(-57.92, -84.56) * mm, "end": v(-57.76, -84.46) * mm});
            skLineSegment(sketch, "E988", {"start": v(-57.76, -84.46) * mm, "end": v(-57.6, -84.37) * mm});
            skLineSegment(sketch, "E989", {"start": v(-57.6, -84.37) * mm, "end": v(-57.44, -84.27) * mm});
            skLineSegment(sketch, "E990", {"start": v(-57.44, -84.27) * mm, "end": v(-57.28, -84.18) * mm});
            skLineSegment(sketch, "E991", {"start": v(-57.28, -84.18) * mm, "end": v(-57.13, -84.08) * mm});
            skLineSegment(sketch, "E992", {"start": v(-57.13, -84.08) * mm, "end": v(-56.97, -83.99) * mm});
            skLineSegment(sketch, "E993", {"start": v(-56.97, -83.99) * mm, "end": v(-56.82, -83.9) * mm});
            skLineSegment(sketch, "E994", {"start": v(-56.82, -83.9) * mm, "end": v(-56.67, -83.8) * mm});
            skLineSegment(sketch, "E995", {"start": v(-56.67, -83.8) * mm, "end": v(-56.52, -83.7) * mm});
            skLineSegment(sketch, "E996", {"start": v(-56.52, -83.7) * mm, "end": v(-56.38, -83.6) * mm});
            skLineSegment(sketch, "E997", {"start": v(-56.38, -83.6) * mm, "end": v(-56.23, -83.51) * mm});
            skLineSegment(sketch, "E998", {"start": v(-56.23, -83.51) * mm, "end": v(-56.09, -83.42) * mm});
            skLineSegment(sketch, "E999", {"start": v(-56.09, -83.42) * mm, "end": v(-55.95, -83.33) * mm});
            skLineSegment(sketch, "E1000", {"start": v(-55.95, -83.33) * mm, "end": v(-55.8, -83.24) * mm});
            skLineSegment(sketch, "E1001", {"start": v(-55.8, -83.24) * mm, "end": v(-55.67, -83.14) * mm});
            skLineSegment(sketch, "E1002", {"start": v(-55.67, -83.14) * mm, "end": v(-55.54, -83.05) * mm});
            skLineSegment(sketch, "E1003", {"start": v(-55.54, -83.05) * mm, "end": v(-55.4, -82.96) * mm});
            skLineSegment(sketch, "E1004", {"start": v(-55.4, -82.96) * mm, "end": v(-55.27, -82.87) * mm});
            skLineSegment(sketch, "E1005", {"start": v(-55.27, -82.87) * mm, "end": v(-55.14, -82.78) * mm});
            skLineSegment(sketch, "E1006", {"start": v(-55.14, -82.78) * mm, "end": v(-55.02, -82.69) * mm});
            skLineSegment(sketch, "E1007", {"start": v(-55.02, -82.69) * mm, "end": v(-54.89, -82.6) * mm});
            skLineSegment(sketch, "E1008", {"start": v(-54.89, -82.6) * mm, "end": v(-54.77, -82.5) * mm});
            skLineSegment(sketch, "E1009", {"start": v(-54.77, -82.5) * mm, "end": v(-54.64, -82.42) * mm});
            skLineSegment(sketch, "E1010", {"start": v(-54.64, -82.42) * mm, "end": v(-54.52, -82.33) * mm});
            skLineSegment(sketch, "E1011", {"start": v(-54.52, -82.33) * mm, "end": v(-54.4, -82.25) * mm});
            skLineSegment(sketch, "E1012", {"start": v(-54.4, -82.25) * mm, "end": v(-54.29, -82.16) * mm});
            skLineSegment(sketch, "E1013", {"start": v(-54.29, -82.16) * mm, "end": v(-54.17, -82.07) * mm});
            skLineSegment(sketch, "E1014", {"start": v(-54.17, -82.07) * mm, "end": v(-54.06, -81.99) * mm});
            skLineSegment(sketch, "E1015", {"start": v(-54.06, -81.99) * mm, "end": v(-53.95, -81.9) * mm});
            skLineSegment(sketch, "E1016", {"start": v(-53.95, -81.9) * mm, "end": v(-53.84, -81.82) * mm});
            skLineSegment(sketch, "E1017", {"start": v(-53.84, -81.82) * mm, "end": v(-53.73, -81.73) * mm});
            skLineSegment(sketch, "E1018", {"start": v(-53.73, -81.73) * mm, "end": v(-53.63, -81.65) * mm});
            skLineSegment(sketch, "E1019", {"start": v(-53.63, -81.65) * mm, "end": v(-53.52, -81.56) * mm});
            skLineSegment(sketch, "E1020", {"start": v(-53.52, -81.56) * mm, "end": v(-53.42, -81.48) * mm});
            skLineSegment(sketch, "E1021", {"start": v(-53.42, -81.48) * mm, "end": v(-53.32, -81.4) * mm});
            skLineSegment(sketch, "E1022", {"start": v(-53.32, -81.4) * mm, "end": v(-53.22, -81.32) * mm});
            skLineSegment(sketch, "E1023", {"start": v(-53.22, -81.32) * mm, "end": v(-52.4, -81.78) * mm});
            skLineSegment(sketch, "E1024", {"start": v(-52.4, -81.78) * mm, "end": v(-51.63, -82.34) * mm});
            skLineSegment(sketch, "E1025", {"start": v(-51.63, -82.34) * mm, "end": v(-51.66, -82.46) * mm});
            skLineSegment(sketch, "E1026", {"start": v(-51.66, -82.46) * mm, "end": v(-51.7, -82.59) * mm});
            skLineSegment(sketch, "E1027", {"start": v(-51.7, -82.59) * mm, "end": v(-51.73, -82.72) * mm});
            skLineSegment(sketch, "E1028", {"start": v(-51.73, -82.72) * mm, "end": v(-51.76, -82.84) * mm});
            skLineSegment(sketch, "E1029", {"start": v(-51.76, -82.84) * mm, "end": v(-51.79, -82.98) * mm});
            skLineSegment(sketch, "E1030", {"start": v(-51.79, -82.98) * mm, "end": v(-51.82, -83.1) * mm});
            skLineSegment(sketch, "E1031", {"start": v(-51.82, -83.1) * mm, "end": v(-51.85, -83.24) * mm});
            skLineSegment(sketch, "E1032", {"start": v(-51.85, -83.24) * mm, "end": v(-51.88, -83.38) * mm});
            skLineSegment(sketch, "E1033", {"start": v(-51.88, -83.38) * mm, "end": v(-51.91, -83.52) * mm});
            skLineSegment(sketch, "E1034", {"start": v(-51.91, -83.52) * mm, "end": v(-51.94, -83.66) * mm});
            skLineSegment(sketch, "E1035", {"start": v(-51.94, -83.66) * mm, "end": v(-51.97, -83.8) * mm});
            skLineSegment(sketch, "E1036", {"start": v(-51.97, -83.8) * mm, "end": v(-52, -83.95) * mm});
            skLineSegment(sketch, "E1037", {"start": v(-52, -83.95) * mm, "end": v(-52.03, -84.1) * mm});
            skLineSegment(sketch, "E1038", {"start": v(-52.03, -84.1) * mm, "end": v(-52.06, -84.24) * mm});
            skLineSegment(sketch, "E1039", {"start": v(-52.06, -84.24) * mm, "end": v(-52.1, -84.4) * mm});
            skLineSegment(sketch, "E1040", {"start": v(-52.1, -84.4) * mm, "end": v(-52.12, -84.54) * mm});
            skLineSegment(sketch, "E1041", {"start": v(-52.12, -84.54) * mm, "end": v(-52.15, -84.7) * mm});
            skLineSegment(sketch, "E1042", {"start": v(-52.15, -84.7) * mm, "end": v(-52.18, -84.85) * mm});
            skLineSegment(sketch, "E1043", {"start": v(-52.18, -84.85) * mm, "end": v(-52.2, -85) * mm});
            skLineSegment(sketch, "E1044", {"start": v(-52.2, -85) * mm, "end": v(-52.23, -85.17) * mm});
            skLineSegment(sketch, "E1045", {"start": v(-52.23, -85.17) * mm, "end": v(-52.26, -85.33) * mm});
            skLineSegment(sketch, "E1046", {"start": v(-52.26, -85.33) * mm, "end": v(-52.29, -85.5) * mm});
            skLineSegment(sketch, "E1047", {"start": v(-52.29, -85.5) * mm, "end": v(-52.31, -85.66) * mm});
            skLineSegment(sketch, "E1048", {"start": v(-52.31, -85.66) * mm, "end": v(-52.34, -85.82) * mm});
            skLineSegment(sketch, "E1049", {"start": v(-52.34, -85.82) * mm, "end": v(-52.36, -86) * mm});
            skLineSegment(sketch, "E1050", {"start": v(-52.36, -86) * mm, "end": v(-52.39, -86.16) * mm});
            skLineSegment(sketch, "E1051", {"start": v(-52.39, -86.16) * mm, "end": v(-52.41, -86.33) * mm});
            skLineSegment(sketch, "E1052", {"start": v(-52.41, -86.33) * mm, "end": v(-52.44, -86.5) * mm});
            skLineSegment(sketch, "E1053", {"start": v(-52.44, -86.5) * mm, "end": v(-52.46, -86.68) * mm});
            skLineSegment(sketch, "E1054", {"start": v(-52.46, -86.68) * mm, "end": v(-52.48, -86.86) * mm});
            skLineSegment(sketch, "E1055", {"start": v(-52.48, -86.86) * mm, "end": v(-52.5, -87.04) * mm});
            skLineSegment(sketch, "E1056", {"start": v(-52.5, -87.04) * mm, "end": v(-52.53, -87.22) * mm});
            skLineSegment(sketch, "E1057", {"start": v(-52.53, -87.22) * mm, "end": v(-52.55, -87.4) * mm});
            skLineSegment(sketch, "E1058", {"start": v(-52.55, -87.4) * mm, "end": v(-52.57, -87.6) * mm});
            skLineSegment(sketch, "E1059", {"start": v(-52.57, -87.6) * mm, "end": v(-52.59, -87.78) * mm});
            skLineSegment(sketch, "E1060", {"start": v(-52.59, -87.78) * mm, "end": v(-52.6, -87.97) * mm});
            skLineSegment(sketch, "E1061", {"start": v(-52.6, -87.97) * mm, "end": v(-52.54, -88.01) * mm});
            skLineSegment(sketch, "E1062", {"start": v(-52.54, -88.01) * mm, "end": v(-51.18, -88.8) * mm});
            skLineSegment(sketch, "E1063", {"start": v(-51.18, -88.8) * mm, "end": v(-51.11, -88.84) * mm});
            skLineSegment(sketch, "E1064", {"start": v(-51.11, -88.84) * mm, "end": v(-50.96, -88.74) * mm});
            skLineSegment(sketch, "E1065", {"start": v(-50.96, -88.74) * mm, "end": v(-50.8, -88.63) * mm});
            skLineSegment(sketch, "E1066", {"start": v(-50.8, -88.63) * mm, "end": v(-50.65, -88.52) * mm});
            skLineSegment(sketch, "E1067", {"start": v(-50.65, -88.52) * mm, "end": v(-50.5, -88.41) * mm});
            skLineSegment(sketch, "E1068", {"start": v(-50.5, -88.41) * mm, "end": v(-50.35, -88.3) * mm});
            skLineSegment(sketch, "E1069", {"start": v(-50.35, -88.3) * mm, "end": v(-50.2, -88.2) * mm});
            skLineSegment(sketch, "E1070", {"start": v(-50.2, -88.2) * mm, "end": v(-50.06, -88.1) * mm});
            skLineSegment(sketch, "E1071", {"start": v(-50.06, -88.1) * mm, "end": v(-49.92, -87.98) * mm});
            skLineSegment(sketch, "E1072", {"start": v(-49.92, -87.98) * mm, "end": v(-49.78, -87.88) * mm});
            skLineSegment(sketch, "E1073", {"start": v(-49.78, -87.88) * mm, "end": v(-49.64, -87.77) * mm});
            skLineSegment(sketch, "E1074", {"start": v(-49.64, -87.77) * mm, "end": v(-49.5, -87.67) * mm});
            skLineSegment(sketch, "E1075", {"start": v(-49.5, -87.67) * mm, "end": v(-49.37, -87.57) * mm});
            skLineSegment(sketch, "E1076", {"start": v(-49.37, -87.57) * mm, "end": v(-49.24, -87.46) * mm});
            skLineSegment(sketch, "E1077", {"start": v(-49.24, -87.46) * mm, "end": v(-49.1, -87.36) * mm});
            skLineSegment(sketch, "E1078", {"start": v(-49.1, -87.36) * mm, "end": v(-48.98, -87.26) * mm});
            skLineSegment(sketch, "E1079", {"start": v(-48.98, -87.26) * mm, "end": v(-48.85, -87.15) * mm});
            skLineSegment(sketch, "E1080", {"start": v(-48.85, -87.15) * mm, "end": v(-48.72, -87.05) * mm});
            skLineSegment(sketch, "E1081", {"start": v(-48.72, -87.05) * mm, "end": v(-48.6, -86.95) * mm});
            skLineSegment(sketch, "E1082", {"start": v(-48.6, -86.95) * mm, "end": v(-48.48, -86.85) * mm});
            skLineSegment(sketch, "E1083", {"start": v(-48.48, -86.85) * mm, "end": v(-48.36, -86.75) * mm});
            skLineSegment(sketch, "E1084", {"start": v(-48.36, -86.75) * mm, "end": v(-48.24, -86.65) * mm});
            skLineSegment(sketch, "E1085", {"start": v(-48.24, -86.65) * mm, "end": v(-48.12, -86.55) * mm});
            skLineSegment(sketch, "E1086", {"start": v(-48.12, -86.55) * mm, "end": v(-48, -86.45) * mm});
            skLineSegment(sketch, "E1087", {"start": v(-48, -86.45) * mm, "end": v(-47.9, -86.36) * mm});
            skLineSegment(sketch, "E1088", {"start": v(-47.9, -86.36) * mm, "end": v(-47.78, -86.26) * mm});
            skLineSegment(sketch, "E1089", {"start": v(-47.78, -86.26) * mm, "end": v(-47.67, -86.16) * mm});
            skLineSegment(sketch, "E1090", {"start": v(-47.67, -86.16) * mm, "end": v(-47.57, -86.07) * mm});
            skLineSegment(sketch, "E1091", {"start": v(-47.57, -86.07) * mm, "end": v(-47.46, -85.97) * mm});
            skLineSegment(sketch, "E1092", {"start": v(-47.46, -85.97) * mm, "end": v(-47.36, -85.88) * mm});
            skLineSegment(sketch, "E1093", {"start": v(-47.36, -85.88) * mm, "end": v(-47.25, -85.79) * mm});
            skLineSegment(sketch, "E1094", {"start": v(-47.25, -85.79) * mm, "end": v(-47.15, -85.7) * mm});
            skLineSegment(sketch, "E1095", {"start": v(-47.15, -85.7) * mm, "end": v(-47.05, -85.6) * mm});
            skLineSegment(sketch, "E1096", {"start": v(-47.05, -85.6) * mm, "end": v(-46.96, -85.51) * mm});
            skLineSegment(sketch, "E1097", {"start": v(-46.96, -85.51) * mm, "end": v(-46.86, -85.42) * mm});
            skLineSegment(sketch, "E1098", {"start": v(-46.86, -85.42) * mm, "end": v(-46.77, -85.33) * mm});
            skLineSegment(sketch, "E1099", {"start": v(-46.77, -85.33) * mm, "end": v(-46.67, -85.24) * mm});
            skLineSegment(sketch, "E1100", {"start": v(-46.67, -85.24) * mm, "end": v(-45.82, -85.64) * mm});
            skLineSegment(sketch, "E1101", {"start": v(-45.82, -85.64) * mm, "end": v(-45.01, -86.13) * mm});
            skLineSegment(sketch, "E1102", {"start": v(-45.01, -86.13) * mm, "end": v(-45.03, -86.26) * mm});
            skLineSegment(sketch, "E1103", {"start": v(-45.03, -86.26) * mm, "end": v(-45.05, -86.39) * mm});
            skLineSegment(sketch, "E1104", {"start": v(-45.05, -86.39) * mm, "end": v(-45.08, -86.52) * mm});
            skLineSegment(sketch, "E1105", {"start": v(-45.08, -86.52) * mm, "end": v(-45.1, -86.65) * mm});
            skLineSegment(sketch, "E1106", {"start": v(-45.1, -86.65) * mm, "end": v(-45.12, -86.78) * mm});
            skLineSegment(sketch, "E1107", {"start": v(-45.12, -86.78) * mm, "end": v(-45.14, -86.92) * mm});
            skLineSegment(sketch, "E1108", {"start": v(-45.14, -86.92) * mm, "end": v(-45.16, -87.06) * mm});
            skLineSegment(sketch, "E1109", {"start": v(-45.16, -87.06) * mm, "end": v(-45.18, -87.2) * mm});
            skLineSegment(sketch, "E1110", {"start": v(-45.18, -87.2) * mm, "end": v(-45.2, -87.34) * mm});
            skLineSegment(sketch, "E1111", {"start": v(-45.2, -87.34) * mm, "end": v(-45.22, -87.48) * mm});
            skLineSegment(sketch, "E1112", {"start": v(-45.22, -87.48) * mm, "end": v(-45.24, -87.62) * mm});
            skLineSegment(sketch, "E1113", {"start": v(-45.24, -87.62) * mm, "end": v(-45.26, -87.77) * mm});
            skLineSegment(sketch, "E1114", {"start": v(-45.26, -87.77) * mm, "end": v(-45.28, -87.92) * mm});
            skLineSegment(sketch, "E1115", {"start": v(-45.28, -87.92) * mm, "end": v(-45.3, -88.07) * mm});
            skLineSegment(sketch, "E1116", {"start": v(-45.3, -88.07) * mm, "end": v(-45.31, -88.22) * mm});
            skLineSegment(sketch, "E1117", {"start": v(-45.31, -88.22) * mm, "end": v(-45.33, -88.37) * mm});
            skLineSegment(sketch, "E1118", {"start": v(-45.33, -88.37) * mm, "end": v(-45.34, -88.53) * mm});
            skLineSegment(sketch, "E1119", {"start": v(-45.34, -88.53) * mm, "end": v(-45.36, -88.68) * mm});
            skLineSegment(sketch, "E1120", {"start": v(-45.36, -88.68) * mm, "end": v(-45.38, -88.84) * mm});
            skLineSegment(sketch, "E1121", {"start": v(-45.38, -88.84) * mm, "end": v(-45.4, -89) * mm});
            skLineSegment(sketch, "E1122", {"start": v(-45.4, -89) * mm, "end": v(-45.4, -89.17) * mm});
            skLineSegment(sketch, "E1123", {"start": v(-45.4, -89.17) * mm, "end": v(-45.42, -89.33) * mm});
            skLineSegment(sketch, "E1124", {"start": v(-45.42, -89.33) * mm, "end": v(-45.43, -89.5) * mm});
            skLineSegment(sketch, "E1125", {"start": v(-45.43, -89.5) * mm, "end": v(-45.44, -89.67) * mm});
            skLineSegment(sketch, "E1126", {"start": v(-45.44, -89.67) * mm, "end": v(-45.46, -89.84) * mm});
            skLineSegment(sketch, "E1127", {"start": v(-45.46, -89.84) * mm, "end": v(-45.47, -90) * mm});
            skLineSegment(sketch, "E1128", {"start": v(-45.47, -90) * mm, "end": v(-45.48, -90.18) * mm});
            skLineSegment(sketch, "E1129", {"start": v(-45.48, -90.18) * mm, "end": v(-45.49, -90.36) * mm});
            skLineSegment(sketch, "E1130", {"start": v(-45.49, -90.36) * mm, "end": v(-45.5, -90.53) * mm});
            skLineSegment(sketch, "E1131", {"start": v(-45.5, -90.53) * mm, "end": v(-45.5, -90.71) * mm});
            skLineSegment(sketch, "E1132", {"start": v(-45.5, -90.71) * mm, "end": v(-45.51, -90.9) * mm});
            skLineSegment(sketch, "E1133", {"start": v(-45.51, -90.9) * mm, "end": v(-45.52, -91.08) * mm});
            skLineSegment(sketch, "E1134", {"start": v(-45.52, -91.08) * mm, "end": v(-45.53, -91.26) * mm});
            skLineSegment(sketch, "E1135", {"start": v(-45.53, -91.26) * mm, "end": v(-45.53, -91.45) * mm});
            skLineSegment(sketch, "E1136", {"start": v(-45.53, -91.45) * mm, "end": v(-45.54, -91.63) * mm});
            skLineSegment(sketch, "E1137", {"start": v(-45.54, -91.63) * mm, "end": v(-45.54, -91.82) * mm});
            skLineSegment(sketch, "E1138", {"start": v(-45.54, -91.82) * mm, "end": v(-45.47, -91.86) * mm});
            skLineSegment(sketch, "E1139", {"start": v(-45.47, -91.86) * mm, "end": v(-44.06, -92.55) * mm});
            skLineSegment(sketch, "E1140", {"start": v(-44.06, -92.55) * mm, "end": v(-43.98, -92.58) * mm});
            skLineSegment(sketch, "E1141", {"start": v(-43.98, -92.58) * mm, "end": v(-43.84, -92.46) * mm});
            skLineSegment(sketch, "E1142", {"start": v(-43.84, -92.46) * mm, "end": v(-43.7, -92.34) * mm});
            skLineSegment(sketch, "E1143", {"start": v(-43.7, -92.34) * mm, "end": v(-43.55, -92.22) * mm});
            skLineSegment(sketch, "E1144", {"start": v(-43.55, -92.22) * mm, "end": v(-43.4, -92.1) * mm});
            skLineSegment(sketch, "E1145", {"start": v(-43.4, -92.1) * mm, "end": v(-43.27, -91.98) * mm});
            skLineSegment(sketch, "E1146", {"start": v(-43.27, -91.98) * mm, "end": v(-43.13, -91.86) * mm});
            skLineSegment(sketch, "E1147", {"start": v(-43.13, -91.86) * mm, "end": v(-43, -91.75) * mm});
            skLineSegment(sketch, "E1148", {"start": v(-43, -91.75) * mm, "end": v(-42.86, -91.63) * mm});
            skLineSegment(sketch, "E1149", {"start": v(-42.86, -91.63) * mm, "end": v(-42.73, -91.51) * mm});
            skLineSegment(sketch, "E1150", {"start": v(-42.73, -91.51) * mm, "end": v(-42.6, -91.4) * mm});
            skLineSegment(sketch, "E1151", {"start": v(-42.6, -91.4) * mm, "end": v(-42.47, -91.28) * mm});
            skLineSegment(sketch, "E1152", {"start": v(-42.47, -91.28) * mm, "end": v(-42.35, -91.17) * mm});
            skLineSegment(sketch, "E1153", {"start": v(-42.35, -91.17) * mm, "end": v(-42.22, -91.05) * mm});
            skLineSegment(sketch, "E1154", {"start": v(-42.22, -91.05) * mm, "end": v(-42.1, -90.94) * mm});
            skLineSegment(sketch, "E1155", {"start": v(-42.1, -90.94) * mm, "end": v(-41.98, -90.83) * mm});
            skLineSegment(sketch, "E1156", {"start": v(-41.98, -90.83) * mm, "end": v(-41.86, -90.72) * mm});
            skLineSegment(sketch, "E1157", {"start": v(-41.86, -90.72) * mm, "end": v(-41.74, -90.6) * mm});
            skLineSegment(sketch, "E1158", {"start": v(-41.74, -90.6) * mm, "end": v(-41.63, -90.5) * mm});
            skLineSegment(sketch, "E1159", {"start": v(-41.63, -90.5) * mm, "end": v(-41.51, -90.39) * mm});
            skLineSegment(sketch, "E1160", {"start": v(-41.51, -90.39) * mm, "end": v(-41.4, -90.28) * mm});
            skLineSegment(sketch, "E1161", {"start": v(-41.4, -90.28) * mm, "end": v(-41.3, -90.17) * mm});
            skLineSegment(sketch, "E1162", {"start": v(-41.3, -90.17) * mm, "end": v(-41.18, -90.06) * mm});
            skLineSegment(sketch, "E1163", {"start": v(-41.18, -90.06) * mm, "end": v(-41.08, -89.95) * mm});
            skLineSegment(sketch, "E1164", {"start": v(-41.08, -89.95) * mm, "end": v(-40.97, -89.85) * mm});
            skLineSegment(sketch, "E1165", {"start": v(-40.97, -89.85) * mm, "end": v(-40.87, -89.74) * mm});
            skLineSegment(sketch, "E1166", {"start": v(-40.87, -89.74) * mm, "end": v(-40.77, -89.64) * mm});
            skLineSegment(sketch, "E1167", {"start": v(-40.77, -89.64) * mm, "end": v(-40.67, -89.54) * mm});
            skLineSegment(sketch, "E1168", {"start": v(-40.67, -89.54) * mm, "end": v(-40.57, -89.43) * mm});
            skLineSegment(sketch, "E1169", {"start": v(-40.57, -89.43) * mm, "end": v(-40.47, -89.33) * mm});
            skLineSegment(sketch, "E1170", {"start": v(-40.47, -89.33) * mm, "end": v(-40.38, -89.23) * mm});
            skLineSegment(sketch, "E1171", {"start": v(-40.38, -89.23) * mm, "end": v(-40.28, -89.13) * mm});
            skLineSegment(sketch, "E1172", {"start": v(-40.28, -89.13) * mm, "end": v(-40.2, -89.03) * mm});
            skLineSegment(sketch, "E1173", {"start": v(-40.2, -89.03) * mm, "end": v(-40.1, -88.93) * mm});
            skLineSegment(sketch, "E1174", {"start": v(-40.1, -88.93) * mm, "end": v(-40.01, -88.84) * mm});
            skLineSegment(sketch, "E1175", {"start": v(-40.01, -88.84) * mm, "end": v(-39.93, -88.74) * mm});
            skLineSegment(sketch, "E1176", {"start": v(-39.93, -88.74) * mm, "end": v(-39.84, -88.64) * mm});
            skLineSegment(sketch, "E1177", {"start": v(-39.84, -88.64) * mm, "end": v(-38.96, -88.97) * mm});
            skLineSegment(sketch, "E1178", {"start": v(-38.96, -88.97) * mm, "end": v(-38.11, -89.4) * mm});
            skLineSegment(sketch, "E1179", {"start": v(-38.11, -89.4) * mm, "end": v(-38.13, -89.53) * mm});
            skLineSegment(sketch, "E1180", {"start": v(-38.13, -89.53) * mm, "end": v(-38.14, -89.66) * mm});
            skLineSegment(sketch, "E1181", {"start": v(-38.14, -89.66) * mm, "end": v(-38.15, -89.79) * mm});
            skLineSegment(sketch, "E1182", {"start": v(-38.15, -89.79) * mm, "end": v(-38.16, -89.92) * mm});
            skLineSegment(sketch, "E1183", {"start": v(-38.16, -89.92) * mm, "end": v(-38.17, -90.06) * mm});
            skLineSegment(sketch, "E1184", {"start": v(-38.17, -90.06) * mm, "end": v(-38.18, -90.2) * mm});
            skLineSegment(sketch, "E1185", {"start": v(-38.18, -90.2) * mm, "end": v(-38.2, -90.33) * mm});
            skLineSegment(sketch, "E1186", {"start": v(-38.2, -90.33) * mm, "end": v(-38.2, -90.47) * mm});
            skLineSegment(sketch, "E1187", {"start": v(-38.2, -90.47) * mm, "end": v(-38.2, -90.61) * mm});
            skLineSegment(sketch, "E1188", {"start": v(-38.2, -90.61) * mm, "end": v(-38.22, -90.76) * mm});
            skLineSegment(sketch, "E1189", {"start": v(-38.22, -90.76) * mm, "end": v(-38.22, -90.9) * mm});
            skLineSegment(sketch, "E1190", {"start": v(-38.22, -90.9) * mm, "end": v(-38.23, -91.05) * mm});
            skLineSegment(sketch, "E1191", {"start": v(-38.23, -91.05) * mm, "end": v(-38.24, -91.2) * mm});
            skLineSegment(sketch, "E1192", {"start": v(-38.24, -91.2) * mm, "end": v(-38.24, -91.35) * mm});
            skLineSegment(sketch, "E1193", {"start": v(-38.24, -91.35) * mm, "end": v(-38.25, -91.5) * mm});
            skLineSegment(sketch, "E1194", {"start": v(-38.25, -91.5) * mm, "end": v(-38.25, -91.66) * mm});
            skLineSegment(sketch, "E1195", {"start": v(-38.25, -91.66) * mm, "end": v(-38.26, -91.81) * mm});
            skLineSegment(sketch, "E1196", {"start": v(-38.26, -91.81) * mm, "end": v(-38.26, -91.97) * mm});
            skLineSegment(sketch, "E1197", {"start": v(-38.26, -91.97) * mm, "end": v(-38.27, -92.13) * mm});
            skLineSegment(sketch, "E1198", {"start": v(-38.27, -92.13) * mm, "end": v(-38.27, -92.3) * mm});
            skLineSegment(sketch, "E1199", {"start": v(-38.27, -92.3) * mm, "end": v(-38.27, -92.45) * mm});
            skLineSegment(sketch, "E1200", {"start": v(-38.27, -92.45) * mm, "end": v(-38.27, -92.62) * mm});
            skLineSegment(sketch, "E1201", {"start": v(-38.27, -92.62) * mm, "end": v(-38.27, -92.79) * mm});
            skLineSegment(sketch, "E1202", {"start": v(-38.27, -92.79) * mm, "end": v(-38.27, -92.95) * mm});
            skLineSegment(sketch, "E1203", {"start": v(-38.27, -92.95) * mm, "end": v(-38.27, -93.12) * mm});
            skLineSegment(sketch, "E1204", {"start": v(-38.27, -93.12) * mm, "end": v(-38.27, -93.3) * mm});
            skLineSegment(sketch, "E1205", {"start": v(-38.27, -93.3) * mm, "end": v(-38.26, -93.47) * mm});
            skLineSegment(sketch, "E1206", {"start": v(-38.26, -93.47) * mm, "end": v(-38.26, -93.65) * mm});
            skLineSegment(sketch, "E1207", {"start": v(-38.26, -93.65) * mm, "end": v(-38.25, -93.82) * mm});
            skLineSegment(sketch, "E1208", {"start": v(-38.25, -93.82) * mm, "end": v(-38.25, -94) * mm});
            skLineSegment(sketch, "E1209", {"start": v(-38.25, -94) * mm, "end": v(-38.24, -94.18) * mm});
            skLineSegment(sketch, "E1210", {"start": v(-38.24, -94.18) * mm, "end": v(-38.24, -94.37) * mm});
            skLineSegment(sketch, "E1211", {"start": v(-38.24, -94.37) * mm, "end": v(-38.23, -94.55) * mm});
            skLineSegment(sketch, "E1212", {"start": v(-38.23, -94.55) * mm, "end": v(-38.22, -94.74) * mm});
            skLineSegment(sketch, "E1213", {"start": v(-38.22, -94.74) * mm, "end": v(-38.2, -94.92) * mm});
            skLineSegment(sketch, "E1214", {"start": v(-38.2, -94.92) * mm, "end": v(-38.2, -95.11) * mm});
            skLineSegment(sketch, "E1215", {"start": v(-38.2, -95.11) * mm, "end": v(-38.12, -95.15) * mm});
            skLineSegment(sketch, "E1216", {"start": v(-38.12, -95.15) * mm, "end": v(-36.66, -95.72) * mm});
            skLineSegment(sketch, "E1217", {"start": v(-36.66, -95.72) * mm, "end": v(-36.58, -95.75) * mm});
            skLineSegment(sketch, "E1218", {"start": v(-36.58, -95.75) * mm, "end": v(-36.45, -95.61) * mm});
            skLineSegment(sketch, "E1219", {"start": v(-36.45, -95.61) * mm, "end": v(-36.31, -95.48) * mm});
            skLineSegment(sketch, "E1220", {"start": v(-36.31, -95.48) * mm, "end": v(-36.18, -95.35) * mm});
            skLineSegment(sketch, "E1221", {"start": v(-36.18, -95.35) * mm, "end": v(-36.05, -95.22) * mm});
            skLineSegment(sketch, "E1222", {"start": v(-36.05, -95.22) * mm, "end": v(-35.92, -95.1) * mm});
            skLineSegment(sketch, "E1223", {"start": v(-35.92, -95.1) * mm, "end": v(-35.8, -94.97) * mm});
            skLineSegment(sketch, "E1224", {"start": v(-35.8, -94.97) * mm, "end": v(-35.67, -94.84) * mm});
            skLineSegment(sketch, "E1225", {"start": v(-35.67, -94.84) * mm, "end": v(-35.54, -94.71) * mm});
            skLineSegment(sketch, "E1226", {"start": v(-35.54, -94.71) * mm, "end": v(-35.42, -94.58) * mm});
            skLineSegment(sketch, "E1227", {"start": v(-35.42, -94.58) * mm, "end": v(-35.3, -94.46) * mm});
            skLineSegment(sketch, "E1228", {"start": v(-35.3, -94.46) * mm, "end": v(-35.18, -94.33) * mm});
            skLineSegment(sketch, "E1229", {"start": v(-35.18, -94.33) * mm, "end": v(-35.06, -94.21) * mm});
            skLineSegment(sketch, "E1230", {"start": v(-35.06, -94.21) * mm, "end": v(-34.95, -94.09) * mm});
            skLineSegment(sketch, "E1231", {"start": v(-34.95, -94.09) * mm, "end": v(-34.84, -93.96) * mm});
            skLineSegment(sketch, "E1232", {"start": v(-34.84, -93.96) * mm, "end": v(-34.72, -93.84) * mm});
            skLineSegment(sketch, "E1233", {"start": v(-34.72, -93.84) * mm, "end": v(-34.61, -93.72) * mm});
            skLineSegment(sketch, "E1234", {"start": v(-34.61, -93.72) * mm, "end": v(-34.5, -93.6) * mm});
            skLineSegment(sketch, "E1235", {"start": v(-34.5, -93.6) * mm, "end": v(-34.4, -93.48) * mm});
            skLineSegment(sketch, "E1236", {"start": v(-34.4, -93.48) * mm, "end": v(-34.3, -93.36) * mm});
            skLineSegment(sketch, "E1237", {"start": v(-34.3, -93.36) * mm, "end": v(-34.2, -93.25) * mm});
            skLineSegment(sketch, "E1238", {"start": v(-34.2, -93.25) * mm, "end": v(-34.1, -93.13) * mm});
            skLineSegment(sketch, "E1239", {"start": v(-34.1, -93.13) * mm, "end": v(-34, -93.02) * mm});
            skLineSegment(sketch, "E1240", {"start": v(-34, -93.02) * mm, "end": v(-33.9, -92.9) * mm});
            skLineSegment(sketch, "E1241", {"start": v(-33.9, -92.9) * mm, "end": v(-33.8, -92.79) * mm});
            skLineSegment(sketch, "E1242", {"start": v(-33.8, -92.79) * mm, "end": v(-33.7, -92.67) * mm});
            skLineSegment(sketch, "E1243", {"start": v(-33.7, -92.67) * mm, "end": v(-33.6, -92.56) * mm});
            skLineSegment(sketch, "E1244", {"start": v(-33.6, -92.56) * mm, "end": v(-33.52, -92.45) * mm});
            skLineSegment(sketch, "E1245", {"start": v(-33.52, -92.45) * mm, "end": v(-33.43, -92.34) * mm});
            skLineSegment(sketch, "E1246", {"start": v(-33.43, -92.34) * mm, "end": v(-33.34, -92.23) * mm});
            skLineSegment(sketch, "E1247", {"start": v(-33.34, -92.23) * mm, "end": v(-33.25, -92.12) * mm});
            skLineSegment(sketch, "E1248", {"start": v(-33.25, -92.12) * mm, "end": v(-33.17, -92.02) * mm});
            skLineSegment(sketch, "E1249", {"start": v(-33.17, -92.02) * mm, "end": v(-33.08, -91.91) * mm});
            skLineSegment(sketch, "E1250", {"start": v(-33.08, -91.91) * mm, "end": v(-33, -91.8) * mm});
            skLineSegment(sketch, "E1251", {"start": v(-33, -91.8) * mm, "end": v(-32.92, -91.7) * mm});
            skLineSegment(sketch, "E1252", {"start": v(-32.92, -91.7) * mm, "end": v(-32.84, -91.6) * mm});
            skLineSegment(sketch, "E1253", {"start": v(-32.84, -91.6) * mm, "end": v(-32.76, -91.5) * mm});
            skLineSegment(sketch, "E1254", {"start": v(-32.76, -91.5) * mm, "end": v(-31.85, -91.75) * mm});
            skLineSegment(sketch, "E1255", {"start": v(-31.85, -91.75) * mm, "end": v(-30.98, -92.12) * mm});
            skLineSegment(sketch, "E1256", {"start": v(-30.98, -92.12) * mm, "end": v(-30.98, -92.24) * mm});
            skLineSegment(sketch, "E1257", {"start": v(-30.98, -92.24) * mm, "end": v(-30.99, -92.37) * mm});
            skLineSegment(sketch, "E1258", {"start": v(-30.99, -92.37) * mm, "end": v(-30.99, -92.5) * mm});
            skLineSegment(sketch, "E1259", {"start": v(-30.99, -92.5) * mm, "end": v(-30.99, -92.64) * mm});
            skLineSegment(sketch, "E1260", {"start": v(-30.99, -92.64) * mm, "end": v(-30.99, -92.77) * mm});
            skLineSegment(sketch, "E1261", {"start": v(-30.99, -92.77) * mm, "end": v(-30.99, -92.9) * mm});
            skLineSegment(sketch, "E1262", {"start": v(-30.99, -92.9) * mm, "end": v(-30.99, -93.05) * mm});
            skLineSegment(sketch, "E1263", {"start": v(-30.99, -93.05) * mm, "end": v(-30.98, -93.19) * mm});
            skLineSegment(sketch, "E1264", {"start": v(-30.98, -93.19) * mm, "end": v(-30.98, -93.33) * mm});
            skLineSegment(sketch, "E1265", {"start": v(-30.98, -93.33) * mm, "end": v(-30.98, -93.47) * mm});
            skLineSegment(sketch, "E1266", {"start": v(-30.98, -93.47) * mm, "end": v(-30.98, -93.62) * mm});
            skLineSegment(sketch, "E1267", {"start": v(-30.98, -93.62) * mm, "end": v(-30.97, -93.77) * mm});
            skLineSegment(sketch, "E1268", {"start": v(-30.97, -93.77) * mm, "end": v(-30.97, -93.92) * mm});
            skLineSegment(sketch, "E1269", {"start": v(-30.97, -93.92) * mm, "end": v(-30.96, -94.07) * mm});
            skLineSegment(sketch, "E1270", {"start": v(-30.96, -94.07) * mm, "end": v(-30.95, -94.22) * mm});
            skLineSegment(sketch, "E1271", {"start": v(-30.95, -94.22) * mm, "end": v(-30.95, -94.37) * mm});
            skLineSegment(sketch, "E1272", {"start": v(-30.95, -94.37) * mm, "end": v(-30.94, -94.53) * mm});
            skLineSegment(sketch, "E1273", {"start": v(-30.94, -94.53) * mm, "end": v(-30.93, -94.69) * mm});
            skLineSegment(sketch, "E1274", {"start": v(-30.93, -94.69) * mm, "end": v(-30.92, -94.85) * mm});
            skLineSegment(sketch, "E1275", {"start": v(-30.92, -94.85) * mm, "end": v(-30.9, -95) * mm});
            skLineSegment(sketch, "E1276", {"start": v(-30.9, -95) * mm, "end": v(-30.9, -95.17) * mm});
            skLineSegment(sketch, "E1277", {"start": v(-30.9, -95.17) * mm, "end": v(-30.88, -95.34) * mm});
            skLineSegment(sketch, "E1278", {"start": v(-30.88, -95.34) * mm, "end": v(-30.87, -95.5) * mm});
            skLineSegment(sketch, "E1279", {"start": v(-30.87, -95.5) * mm, "end": v(-30.86, -95.67) * mm});
            skLineSegment(sketch, "E1280", {"start": v(-30.86, -95.67) * mm, "end": v(-30.84, -95.84) * mm});
            skLineSegment(sketch, "E1281", {"start": v(-30.84, -95.84) * mm, "end": v(-30.83, -96.01) * mm});
            skLineSegment(sketch, "E1282", {"start": v(-30.83, -96.01) * mm, "end": v(-30.81, -96.18) * mm});
            skLineSegment(sketch, "E1283", {"start": v(-30.81, -96.18) * mm, "end": v(-30.8, -96.36) * mm});
            skLineSegment(sketch, "E1284", {"start": v(-30.8, -96.36) * mm, "end": v(-30.78, -96.54) * mm});
            skLineSegment(sketch, "E1285", {"start": v(-30.78, -96.54) * mm, "end": v(-30.76, -96.71) * mm});
            skLineSegment(sketch, "E1286", {"start": v(-30.76, -96.71) * mm, "end": v(-30.74, -96.9) * mm});
            skLineSegment(sketch, "E1287", {"start": v(-30.74, -96.9) * mm, "end": v(-30.71, -97.08) * mm});
            skLineSegment(sketch, "E1288", {"start": v(-30.71, -97.08) * mm, "end": v(-30.7, -97.26) * mm});
            skLineSegment(sketch, "E1289", {"start": v(-30.7, -97.26) * mm, "end": v(-30.67, -97.44) * mm});
            skLineSegment(sketch, "E1290", {"start": v(-30.67, -97.44) * mm, "end": v(-30.64, -97.63) * mm});
            skLineSegment(sketch, "E1291", {"start": v(-30.64, -97.63) * mm, "end": v(-30.62, -97.82) * mm});
            skLineSegment(sketch, "E1292", {"start": v(-30.62, -97.82) * mm, "end": v(-30.54, -97.84) * mm});
            skLineSegment(sketch, "E1293", {"start": v(-30.54, -97.84) * mm, "end": v(-29.04, -98.3) * mm});
            skLineSegment(sketch, "E1294", {"start": v(-29.04, -98.3) * mm, "end": v(-28.96, -98.32) * mm});
            skLineSegment(sketch, "E1295", {"start": v(-28.96, -98.32) * mm, "end": v(-28.83, -98.18) * mm});
            skLineSegment(sketch, "E1296", {"start": v(-28.83, -98.18) * mm, "end": v(-28.7, -98.04) * mm});
            skLineSegment(sketch, "E1297", {"start": v(-28.7, -98.04) * mm, "end": v(-28.59, -97.9) * mm});
            skLineSegment(sketch, "E1298", {"start": v(-28.59, -97.9) * mm, "end": v(-28.47, -97.76) * mm});
            skLineSegment(sketch, "E1299", {"start": v(-28.47, -97.76) * mm, "end": v(-28.35, -97.62) * mm});
            skLineSegment(sketch, "E1300", {"start": v(-28.35, -97.62) * mm, "end": v(-28.23, -97.48) * mm});
            skLineSegment(sketch, "E1301", {"start": v(-28.23, -97.48) * mm, "end": v(-28.11, -97.34) * mm});
            skLineSegment(sketch, "E1302", {"start": v(-28.11, -97.34) * mm, "end": v(-28, -97.2) * mm});
            skLineSegment(sketch, "E1303", {"start": v(-28, -97.2) * mm, "end": v(-27.89, -97.07) * mm});
            skLineSegment(sketch, "E1304", {"start": v(-27.89, -97.07) * mm, "end": v(-27.78, -96.94) * mm});
            skLineSegment(sketch, "E1305", {"start": v(-27.78, -96.94) * mm, "end": v(-27.67, -96.8) * mm});
            skLineSegment(sketch, "E1306", {"start": v(-27.67, -96.8) * mm, "end": v(-27.56, -96.67) * mm});
            skLineSegment(sketch, "E1307", {"start": v(-27.56, -96.67) * mm, "end": v(-27.46, -96.54) * mm});
            skLineSegment(sketch, "E1308", {"start": v(-27.46, -96.54) * mm, "end": v(-27.36, -96.4) * mm});
            skLineSegment(sketch, "E1309", {"start": v(-27.36, -96.4) * mm, "end": v(-27.25, -96.28) * mm});
            skLineSegment(sketch, "E1310", {"start": v(-27.25, -96.28) * mm, "end": v(-27.15, -96.15) * mm});
            skLineSegment(sketch, "E1311", {"start": v(-27.15, -96.15) * mm, "end": v(-27.06, -96.02) * mm});
            skLineSegment(sketch, "E1312", {"start": v(-27.06, -96.02) * mm, "end": v(-26.96, -95.9) * mm});
            skLineSegment(sketch, "E1313", {"start": v(-26.96, -95.9) * mm, "end": v(-26.86, -95.77) * mm});
            skLineSegment(sketch, "E1314", {"start": v(-26.86, -95.77) * mm, "end": v(-26.77, -95.64) * mm});
            skLineSegment(sketch, "E1315", {"start": v(-26.77, -95.64) * mm, "end": v(-26.68, -95.52) * mm});
            skLineSegment(sketch, "E1316", {"start": v(-26.68, -95.52) * mm, "end": v(-26.59, -95.4) * mm});
            skLineSegment(sketch, "E1317", {"start": v(-26.59, -95.4) * mm, "end": v(-26.5, -95.27) * mm});
            skLineSegment(sketch, "E1318", {"start": v(-26.5, -95.27) * mm, "end": v(-26.41, -95.15) * mm});
            skLineSegment(sketch, "E1319", {"start": v(-26.41, -95.15) * mm, "end": v(-26.33, -95.03) * mm});
            skLineSegment(sketch, "E1320", {"start": v(-26.33, -95.03) * mm, "end": v(-26.24, -94.91) * mm});
            skLineSegment(sketch, "E1321", {"start": v(-26.24, -94.91) * mm, "end": v(-26.16, -94.8) * mm});
            skLineSegment(sketch, "E1322", {"start": v(-26.16, -94.8) * mm, "end": v(-26.08, -94.68) * mm});
            skLineSegment(sketch, "E1323", {"start": v(-26.08, -94.68) * mm, "end": v(-26, -94.56) * mm});
            skLineSegment(sketch, "E1324", {"start": v(-26, -94.56) * mm, "end": v(-25.92, -94.45) * mm});
            skLineSegment(sketch, "E1325", {"start": v(-25.92, -94.45) * mm, "end": v(-25.85, -94.34) * mm});
            skLineSegment(sketch, "E1326", {"start": v(-25.85, -94.34) * mm, "end": v(-25.77, -94.22) * mm});
            skLineSegment(sketch, "E1327", {"start": v(-25.77, -94.22) * mm, "end": v(-25.7, -94.11) * mm});
            skLineSegment(sketch, "E1328", {"start": v(-25.7, -94.11) * mm, "end": v(-25.62, -94) * mm});
            skLineSegment(sketch, "E1329", {"start": v(-25.62, -94) * mm, "end": v(-25.55, -93.9) * mm});
            skLineSegment(sketch, "E1330", {"start": v(-25.55, -93.9) * mm, "end": v(-25.48, -93.79) * mm});
            skLineSegment(sketch, "E1331", {"start": v(-25.48, -93.79) * mm, "end": v(-24.56, -93.97) * mm});
            skLineSegment(sketch, "E1332", {"start": v(-24.56, -93.97) * mm, "end": v(-23.66, -94.26) * mm});
            skLineSegment(sketch, "E1333", {"start": v(-23.66, -94.26) * mm, "end": v(-23.65, -94.4) * mm});
            skLineSegment(sketch, "E1334", {"start": v(-23.65, -94.4) * mm, "end": v(-23.64, -94.52) * mm});
            skLineSegment(sketch, "E1335", {"start": v(-23.64, -94.52) * mm, "end": v(-23.63, -94.65) * mm});
            skLineSegment(sketch, "E1336", {"start": v(-23.63, -94.65) * mm, "end": v(-23.62, -94.78) * mm});
            skLineSegment(sketch, "E1337", {"start": v(-23.62, -94.78) * mm, "end": v(-23.61, -94.92) * mm});
            skLineSegment(sketch, "E1338", {"start": v(-23.61, -94.92) * mm, "end": v(-23.6, -95.05) * mm});
            skLineSegment(sketch, "E1339", {"start": v(-23.6, -95.05) * mm, "end": v(-23.6, -95.2) * mm});
            skLineSegment(sketch, "E1340", {"start": v(-23.6, -95.2) * mm, "end": v(-23.58, -95.33) * mm});
            skLineSegment(sketch, "E1341", {"start": v(-23.58, -95.33) * mm, "end": v(-23.56, -95.47) * mm});
            skLineSegment(sketch, "E1342", {"start": v(-23.56, -95.47) * mm, "end": v(-23.55, -95.62) * mm});
            skLineSegment(sketch, "E1343", {"start": v(-23.55, -95.62) * mm, "end": v(-23.53, -95.76) * mm});
            skLineSegment(sketch, "E1344", {"start": v(-23.53, -95.76) * mm, "end": v(-23.52, -95.9) * mm});
            skLineSegment(sketch, "E1345", {"start": v(-23.52, -95.9) * mm, "end": v(-23.5, -96.06) * mm});
            skLineSegment(sketch, "E1346", {"start": v(-23.5, -96.06) * mm, "end": v(-23.48, -96.2) * mm});
            skLineSegment(sketch, "E1347", {"start": v(-23.48, -96.2) * mm, "end": v(-23.47, -96.36) * mm});
            skLineSegment(sketch, "E1348", {"start": v(-23.47, -96.36) * mm, "end": v(-23.45, -96.51) * mm});
            skLineSegment(sketch, "E1349", {"start": v(-23.45, -96.51) * mm, "end": v(-23.43, -96.67) * mm});
            skLineSegment(sketch, "E1350", {"start": v(-23.43, -96.67) * mm, "end": v(-23.4, -96.82) * mm});
            skLineSegment(sketch, "E1351", {"start": v(-23.4, -96.82) * mm, "end": v(-23.38, -96.98) * mm});
            skLineSegment(sketch, "E1352", {"start": v(-23.38, -96.98) * mm, "end": v(-23.36, -97.14) * mm});
            skLineSegment(sketch, "E1353", {"start": v(-23.36, -97.14) * mm, "end": v(-23.33, -97.3) * mm});
            skLineSegment(sketch, "E1354", {"start": v(-23.33, -97.3) * mm, "end": v(-23.3, -97.47) * mm});
            skLineSegment(sketch, "E1355", {"start": v(-23.3, -97.47) * mm, "end": v(-23.28, -97.63) * mm});
            skLineSegment(sketch, "E1356", {"start": v(-23.28, -97.63) * mm, "end": v(-23.26, -97.8) * mm});
            skLineSegment(sketch, "E1357", {"start": v(-23.26, -97.8) * mm, "end": v(-23.23, -97.96) * mm});
            skLineSegment(sketch, "E1358", {"start": v(-23.23, -97.96) * mm, "end": v(-23.2, -98.13) * mm});
            skLineSegment(sketch, "E1359", {"start": v(-23.2, -98.13) * mm, "end": v(-23.17, -98.3) * mm});
            skLineSegment(sketch, "E1360", {"start": v(-23.17, -98.3) * mm, "end": v(-23.14, -98.48) * mm});
            skLineSegment(sketch, "E1361", {"start": v(-23.14, -98.48) * mm, "end": v(-23.1, -98.65) * mm});
            skLineSegment(sketch, "E1362", {"start": v(-23.1, -98.65) * mm, "end": v(-23.07, -98.83) * mm});
            skLineSegment(sketch, "E1363", {"start": v(-23.07, -98.83) * mm, "end": v(-23.04, -99) * mm});
            skLineSegment(sketch, "E1364", {"start": v(-23.04, -99) * mm, "end": v(-23, -99.19) * mm});
            skLineSegment(sketch, "E1365", {"start": v(-23, -99.19) * mm, "end": v(-22.97, -99.37) * mm});
            skLineSegment(sketch, "E1366", {"start": v(-22.97, -99.37) * mm, "end": v(-22.93, -99.55) * mm});
            skLineSegment(sketch, "E1367", {"start": v(-22.93, -99.55) * mm, "end": v(-22.89, -99.73) * mm});
            skLineSegment(sketch, "E1368", {"start": v(-22.89, -99.73) * mm, "end": v(-22.85, -99.92) * mm});
            skLineSegment(sketch, "E1369", {"start": v(-22.85, -99.92) * mm, "end": v(-22.77, -99.94) * mm});
            skLineSegment(sketch, "E1370", {"start": v(-22.77, -99.94) * mm, "end": v(-21.24, -100.28) * mm});
            skLineSegment(sketch, "E1371", {"start": v(-21.24, -100.28) * mm, "end": v(-21.15, -100.3) * mm});
            skLineSegment(sketch, "E1372", {"start": v(-21.15, -100.3) * mm, "end": v(-21.04, -100.14) * mm});
            skLineSegment(sketch, "E1373", {"start": v(-21.04, -100.14) * mm, "end": v(-20.93, -99.99) * mm});
            skLineSegment(sketch, "E1374", {"start": v(-20.93, -99.99) * mm, "end": v(-20.82, -99.84) * mm});
            skLineSegment(sketch, "E1375", {"start": v(-20.82, -99.84) * mm, "end": v(-20.7, -99.7) * mm});
            skLineSegment(sketch, "E1376", {"start": v(-20.7, -99.7) * mm, "end": v(-20.6, -99.54) * mm});
            skLineSegment(sketch, "E1377", {"start": v(-20.6, -99.54) * mm, "end": v(-20.5, -99.4) * mm});
            skLineSegment(sketch, "E1378", {"start": v(-20.5, -99.4) * mm, "end": v(-20.4, -99.25) * mm});
            skLineSegment(sketch, "E1379", {"start": v(-20.4, -99.25) * mm, "end": v(-20.29, -99.1) * mm});
            skLineSegment(sketch, "E1380", {"start": v(-20.29, -99.1) * mm, "end": v(-20.19, -98.96) * mm});
            skLineSegment(sketch, "E1381", {"start": v(-20.19, -98.96) * mm, "end": v(-20.09, -98.82) * mm});
            skLineSegment(sketch, "E1382", {"start": v(-20.09, -98.82) * mm, "end": v(-20, -98.68) * mm});
            skLineSegment(sketch, "E1383", {"start": v(-20, -98.68) * mm, "end": v(-19.9, -98.54) * mm});
            skLineSegment(sketch, "E1384", {"start": v(-19.9, -98.54) * mm, "end": v(-19.8, -98.4) * mm});
            skLineSegment(sketch, "E1385", {"start": v(-19.8, -98.4) * mm, "end": v(-19.7, -98.26) * mm});
            skLineSegment(sketch, "E1386", {"start": v(-19.7, -98.26) * mm, "end": v(-19.62, -98.12) * mm});
            skLineSegment(sketch, "E1387", {"start": v(-19.62, -98.12) * mm, "end": v(-19.53, -97.98) * mm});
            skLineSegment(sketch, "E1388", {"start": v(-19.53, -97.98) * mm, "end": v(-19.44, -97.85) * mm});
            skLineSegment(sketch, "E1389", {"start": v(-19.44, -97.85) * mm, "end": v(-19.35, -97.71) * mm});
            skLineSegment(sketch, "E1390", {"start": v(-19.35, -97.71) * mm, "end": v(-19.27, -97.58) * mm});
            skLineSegment(sketch, "E1391", {"start": v(-19.27, -97.58) * mm, "end": v(-19.18, -97.45) * mm});
            skLineSegment(sketch, "E1392", {"start": v(-19.18, -97.45) * mm, "end": v(-19.1, -97.32) * mm});
            skLineSegment(sketch, "E1393", {"start": v(-19.1, -97.32) * mm, "end": v(-19.02, -97.19) * mm});
            skLineSegment(sketch, "E1394", {"start": v(-19.02, -97.19) * mm, "end": v(-18.94, -97.06) * mm});
            skLineSegment(sketch, "E1395", {"start": v(-18.94, -97.06) * mm, "end": v(-18.87, -96.93) * mm});
            skLineSegment(sketch, "E1396", {"start": v(-18.87, -96.93) * mm, "end": v(-18.79, -96.8) * mm});
            skLineSegment(sketch, "E1397", {"start": v(-18.79, -96.8) * mm, "end": v(-18.72, -96.68) * mm});
            skLineSegment(sketch, "E1398", {"start": v(-18.72, -96.68) * mm, "end": v(-18.64, -96.56) * mm});
            skLineSegment(sketch, "E1399", {"start": v(-18.64, -96.56) * mm, "end": v(-18.57, -96.43) * mm});
            skLineSegment(sketch, "E1400", {"start": v(-18.57, -96.43) * mm, "end": v(-18.5, -96.31) * mm});
            skLineSegment(sketch, "E1401", {"start": v(-18.5, -96.31) * mm, "end": v(-18.43, -96.2) * mm});
            skLineSegment(sketch, "E1402", {"start": v(-18.43, -96.2) * mm, "end": v(-18.36, -96.07) * mm});
            skLineSegment(sketch, "E1403", {"start": v(-18.36, -96.07) * mm, "end": v(-18.3, -95.95) * mm});
            skLineSegment(sketch, "E1404", {"start": v(-18.3, -95.95) * mm, "end": v(-18.23, -95.84) * mm});
            skLineSegment(sketch, "E1405", {"start": v(-18.23, -95.84) * mm, "end": v(-18.17, -95.72) * mm});
            skLineSegment(sketch, "E1406", {"start": v(-18.17, -95.72) * mm, "end": v(-18.1, -95.6) * mm});
            skLineSegment(sketch, "E1407", {"start": v(-18.1, -95.6) * mm, "end": v(-18.05, -95.5) * mm});
            skLineSegment(sketch, "E1408", {"start": v(-18.05, -95.5) * mm, "end": v(-17.1, -95.6) * mm});
            skLineSegment(sketch, "E1409", {"start": v(-17.1, -95.6) * mm, "end": v(-16.2, -95.83) * mm});
            skLineSegment(sketch, "E1410", {"start": v(-16.2, -95.83) * mm, "end": v(-16.17, -95.95) * mm});
            skLineSegment(sketch, "E1411", {"start": v(-16.17, -95.95) * mm, "end": v(-16.15, -96.08) * mm});
            skLineSegment(sketch, "E1412", {"start": v(-16.15, -96.08) * mm, "end": v(-16.13, -96.21) * mm});
            skLineSegment(sketch, "E1413", {"start": v(-16.13, -96.21) * mm, "end": v(-16.11, -96.35) * mm});
            skLineSegment(sketch, "E1414", {"start": v(-16.11, -96.35) * mm, "end": v(-16.1, -96.48) * mm});
            skLineSegment(sketch, "E1415", {"start": v(-16.1, -96.48) * mm, "end": v(-16.07, -96.61) * mm});
            skLineSegment(sketch, "E1416", {"start": v(-16.07, -96.61) * mm, "end": v(-16.05, -96.75) * mm});
            skLineSegment(sketch, "E1417", {"start": v(-16.05, -96.75) * mm, "end": v(-16.02, -96.89) * mm});
            skLineSegment(sketch, "E1418", {"start": v(-16.02, -96.89) * mm, "end": v(-16, -97.03) * mm});
            skLineSegment(sketch, "E1419", {"start": v(-16, -97.03) * mm, "end": v(-15.97, -97.17) * mm});
            skLineSegment(sketch, "E1420", {"start": v(-15.97, -97.17) * mm, "end": v(-15.95, -97.31) * mm});
            skLineSegment(sketch, "E1421", {"start": v(-15.95, -97.31) * mm, "end": v(-15.92, -97.46) * mm});
            skLineSegment(sketch, "E1422", {"start": v(-15.92, -97.46) * mm, "end": v(-15.9, -97.6) * mm});
            skLineSegment(sketch, "E1423", {"start": v(-15.9, -97.6) * mm, "end": v(-15.86, -97.75) * mm});
            skLineSegment(sketch, "E1424", {"start": v(-15.86, -97.75) * mm, "end": v(-15.83, -97.9) * mm});
            skLineSegment(sketch, "E1425", {"start": v(-15.83, -97.9) * mm, "end": v(-15.8, -98.05) * mm});
            skLineSegment(sketch, "E1426", {"start": v(-15.8, -98.05) * mm, "end": v(-15.77, -98.2) * mm});
            skLineSegment(sketch, "E1427", {"start": v(-15.77, -98.2) * mm, "end": v(-15.74, -98.36) * mm});
            skLineSegment(sketch, "E1428", {"start": v(-15.74, -98.36) * mm, "end": v(-15.7, -98.52) * mm});
            skLineSegment(sketch, "E1429", {"start": v(-15.7, -98.52) * mm, "end": v(-15.67, -98.67) * mm});
            skLineSegment(sketch, "E1430", {"start": v(-15.67, -98.67) * mm, "end": v(-15.63, -98.83) * mm});
            skLineSegment(sketch, "E1431", {"start": v(-15.63, -98.83) * mm, "end": v(-15.6, -99) * mm});
            skLineSegment(sketch, "E1432", {"start": v(-15.6, -99) * mm, "end": v(-15.55, -99.16) * mm});
            skLineSegment(sketch, "E1433", {"start": v(-15.55, -99.16) * mm, "end": v(-15.51, -99.32) * mm});
            skLineSegment(sketch, "E1434", {"start": v(-15.51, -99.32) * mm, "end": v(-15.47, -99.49) * mm});
            skLineSegment(sketch, "E1435", {"start": v(-15.47, -99.49) * mm, "end": v(-15.43, -99.65) * mm});
            skLineSegment(sketch, "E1436", {"start": v(-15.43, -99.65) * mm, "end": v(-15.39, -99.82) * mm});
            skLineSegment(sketch, "E1437", {"start": v(-15.39, -99.82) * mm, "end": v(-15.34, -100) * mm});
            skLineSegment(sketch, "E1438", {"start": v(-15.34, -100) * mm, "end": v(-15.3, -100.16) * mm});
            skLineSegment(sketch, "E1439", {"start": v(-15.3, -100.16) * mm, "end": v(-15.25, -100.33) * mm});
            skLineSegment(sketch, "E1440", {"start": v(-15.25, -100.33) * mm, "end": v(-15.2, -100.5) * mm});
            skLineSegment(sketch, "E1441", {"start": v(-15.2, -100.5) * mm, "end": v(-15.15, -100.68) * mm});
            skLineSegment(sketch, "E1442", {"start": v(-15.15, -100.68) * mm, "end": v(-15.1, -100.86) * mm});
            skLineSegment(sketch, "E1443", {"start": v(-15.1, -100.86) * mm, "end": v(-15.05, -101.04) * mm});
            skLineSegment(sketch, "E1444", {"start": v(-15.05, -101.04) * mm, "end": v(-15, -101.22) * mm});
            skLineSegment(sketch, "E1445", {"start": v(-15, -101.22) * mm, "end": v(-14.94, -101.4) * mm});
            skLineSegment(sketch, "E1446", {"start": v(-14.94, -101.4) * mm, "end": v(-14.86, -101.42) * mm});
            skLineSegment(sketch, "E1447", {"start": v(-14.86, -101.42) * mm, "end": v(-13.3, -101.63) * mm});
            skLineSegment(sketch, "E1448", {"start": v(-13.3, -101.63) * mm, "end": v(-13.22, -101.64) * mm});
            skLineSegment(sketch, "E1449", {"start": v(-13.22, -101.64) * mm, "end": v(-13.12, -101.48) * mm});
            skLineSegment(sketch, "E1450", {"start": v(-13.12, -101.48) * mm, "end": v(-13.02, -101.32) * mm});
            skLineSegment(sketch, "E1451", {"start": v(-13.02, -101.32) * mm, "end": v(-12.92, -101.16) * mm});
            skLineSegment(sketch, "E1452", {"start": v(-12.92, -101.16) * mm, "end": v(-12.82, -101) * mm});
            skLineSegment(sketch, "E1453", {"start": v(-12.82, -101) * mm, "end": v(-12.73, -100.85) * mm});
            skLineSegment(sketch, "E1454", {"start": v(-12.73, -100.85) * mm, "end": v(-12.63, -100.7) * mm});
            skLineSegment(sketch, "E1455", {"start": v(-12.63, -100.7) * mm, "end": v(-12.54, -100.54) * mm});
            skLineSegment(sketch, "E1456", {"start": v(-12.54, -100.54) * mm, "end": v(-12.45, -100.4) * mm});
            skLineSegment(sketch, "E1457", {"start": v(-12.45, -100.4) * mm, "end": v(-12.36, -100.24) * mm});
            skLineSegment(sketch, "E1458", {"start": v(-12.36, -100.24) * mm, "end": v(-12.27, -100.09) * mm});
            skLineSegment(sketch, "E1459", {"start": v(-12.27, -100.09) * mm, "end": v(-12.19, -99.94) * mm});
            skLineSegment(sketch, "E1460", {"start": v(-12.19, -99.94) * mm, "end": v(-12.1, -99.8) * mm});
            skLineSegment(sketch, "E1461", {"start": v(-12.1, -99.8) * mm, "end": v(-12.02, -99.65) * mm});
            skLineSegment(sketch, "E1462", {"start": v(-12.02, -99.65) * mm, "end": v(-11.94, -99.5) * mm});
            skLineSegment(sketch, "E1463", {"start": v(-11.94, -99.5) * mm, "end": v(-11.86, -99.36) * mm});
            skLineSegment(sketch, "E1464", {"start": v(-11.86, -99.36) * mm, "end": v(-11.78, -99.21) * mm});
            skLineSegment(sketch, "E1465", {"start": v(-11.78, -99.21) * mm, "end": v(-11.7, -99.07) * mm});
            skLineSegment(sketch, "E1466", {"start": v(-11.7, -99.07) * mm, "end": v(-11.63, -98.93) * mm});
            skLineSegment(sketch, "E1467", {"start": v(-11.63, -98.93) * mm, "end": v(-11.55, -98.8) * mm});
            skLineSegment(sketch, "E1468", {"start": v(-11.55, -98.8) * mm, "end": v(-11.48, -98.65) * mm});
            skLineSegment(sketch, "E1469", {"start": v(-11.48, -98.65) * mm, "end": v(-11.4, -98.52) * mm});
            skLineSegment(sketch, "E1470", {"start": v(-11.4, -98.52) * mm, "end": v(-11.34, -98.38) * mm});
            skLineSegment(sketch, "E1471", {"start": v(-11.34, -98.38) * mm, "end": v(-11.27, -98.25) * mm});
            skLineSegment(sketch, "E1472", {"start": v(-11.27, -98.25) * mm, "end": v(-11.2, -98.11) * mm});
            skLineSegment(sketch, "E1473", {"start": v(-11.2, -98.11) * mm, "end": v(-11.14, -97.98) * mm});
            skLineSegment(sketch, "E1474", {"start": v(-11.14, -97.98) * mm, "end": v(-11.07, -97.85) * mm});
            skLineSegment(sketch, "E1475", {"start": v(-11.07, -97.85) * mm, "end": v(-11, -97.72) * mm});
            skLineSegment(sketch, "E1476", {"start": v(-11, -97.72) * mm, "end": v(-10.95, -97.6) * mm});
            skLineSegment(sketch, "E1477", {"start": v(-10.95, -97.6) * mm, "end": v(-10.89, -97.47) * mm});
            skLineSegment(sketch, "E1478", {"start": v(-10.89, -97.47) * mm, "end": v(-10.83, -97.34) * mm});
            skLineSegment(sketch, "E1479", {"start": v(-10.83, -97.34) * mm, "end": v(-10.77, -97.22) * mm});
            skLineSegment(sketch, "E1480", {"start": v(-10.77, -97.22) * mm, "end": v(-10.71, -97.1) * mm});
            skLineSegment(sketch, "E1481", {"start": v(-10.71, -97.1) * mm, "end": v(-10.66, -96.97) * mm});
            skLineSegment(sketch, "E1482", {"start": v(-10.66, -96.97) * mm, "end": v(-10.6, -96.85) * mm});
            skLineSegment(sketch, "E1483", {"start": v(-10.6, -96.85) * mm, "end": v(-10.55, -96.73) * mm});
            skLineSegment(sketch, "E1484", {"start": v(-10.55, -96.73) * mm, "end": v(-10.5, -96.62) * mm});
            skLineSegment(sketch, "E1485", {"start": v(-10.5, -96.62) * mm, "end": v(-9.56, -96.65) * mm});
            skLineSegment(sketch, "E1486", {"start": v(-9.56, -96.65) * mm, "end": v(-8.62, -96.8) * mm});
            skLineSegment(sketch, "E1487", {"start": v(-8.62, -96.8) * mm, "end": v(-8.6, -96.93) * mm});
            skLineSegment(sketch, "E1488", {"start": v(-8.6, -96.93) * mm, "end": v(-8.57, -97.05) * mm});
            skLineSegment(sketch, "E1489", {"start": v(-8.57, -97.05) * mm, "end": v(-8.54, -97.18) * mm});
            skLineSegment(sketch, "E1490", {"start": v(-8.54, -97.18) * mm, "end": v(-8.5, -97.31) * mm});
            skLineSegment(sketch, "E1491", {"start": v(-8.5, -97.31) * mm, "end": v(-8.47, -97.44) * mm});
            skLineSegment(sketch, "E1492", {"start": v(-8.47, -97.44) * mm, "end": v(-8.44, -97.58) * mm});
            skLineSegment(sketch, "E1493", {"start": v(-8.44, -97.58) * mm, "end": v(-8.4, -97.71) * mm});
            skLineSegment(sketch, "E1494", {"start": v(-8.4, -97.71) * mm, "end": v(-8.37, -97.85) * mm});
            skLineSegment(sketch, "E1495", {"start": v(-8.37, -97.85) * mm, "end": v(-8.34, -97.98) * mm});
            skLineSegment(sketch, "E1496", {"start": v(-8.34, -97.98) * mm, "end": v(-8.3, -98.12) * mm});
            skLineSegment(sketch, "E1497", {"start": v(-8.3, -98.12) * mm, "end": v(-8.26, -98.26) * mm});
            skLineSegment(sketch, "E1498", {"start": v(-8.26, -98.26) * mm, "end": v(-8.23, -98.4) * mm});
            skLineSegment(sketch, "E1499", {"start": v(-8.23, -98.4) * mm, "end": v(-8.19, -98.55) * mm});
            skLineSegment(sketch, "E1500", {"start": v(-8.19, -98.55) * mm, "end": v(-8.14, -98.7) * mm});
            skLineSegment(sketch, "E1501", {"start": v(-8.14, -98.7) * mm, "end": v(-8.1, -98.84) * mm});
            skLineSegment(sketch, "E1502", {"start": v(-8.1, -98.84) * mm, "end": v(-8.06, -99) * mm});
            skLineSegment(sketch, "E1503", {"start": v(-8.06, -99) * mm, "end": v(-8.02, -99.14) * mm});
            skLineSegment(sketch, "E1504", {"start": v(-8.02, -99.14) * mm, "end": v(-7.97, -99.3) * mm});
            skLineSegment(sketch, "E1505", {"start": v(-7.97, -99.3) * mm, "end": v(-7.92, -99.44) * mm});
            skLineSegment(sketch, "E1506", {"start": v(-7.92, -99.44) * mm, "end": v(-7.88, -99.6) * mm});
            skLineSegment(sketch, "E1507", {"start": v(-7.88, -99.6) * mm, "end": v(-7.83, -99.75) * mm});
            skLineSegment(sketch, "E1508", {"start": v(-7.83, -99.75) * mm, "end": v(-7.78, -99.91) * mm});
            skLineSegment(sketch, "E1509", {"start": v(-7.78, -99.91) * mm, "end": v(-7.72, -100.07) * mm});
            skLineSegment(sketch, "E1510", {"start": v(-7.72, -100.07) * mm, "end": v(-7.67, -100.23) * mm});
            skLineSegment(sketch, "E1511", {"start": v(-7.67, -100.23) * mm, "end": v(-7.62, -100.4) * mm});
            skLineSegment(sketch, "E1512", {"start": v(-7.62, -100.4) * mm, "end": v(-7.56, -100.56) * mm});
            skLineSegment(sketch, "E1513", {"start": v(-7.56, -100.56) * mm, "end": v(-7.5, -100.72) * mm});
            skLineSegment(sketch, "E1514", {"start": v(-7.5, -100.72) * mm, "end": v(-7.45, -100.89) * mm});
            skLineSegment(sketch, "E1515", {"start": v(-7.45, -100.89) * mm, "end": v(-7.39, -101.05) * mm});
            skLineSegment(sketch, "E1516", {"start": v(-7.39, -101.05) * mm, "end": v(-7.33, -101.22) * mm});
            skLineSegment(sketch, "E1517", {"start": v(-7.33, -101.22) * mm, "end": v(-7.27, -101.4) * mm});
            skLineSegment(sketch, "E1518", {"start": v(-7.27, -101.4) * mm, "end": v(-7.2, -101.56) * mm});
            skLineSegment(sketch, "E1519", {"start": v(-7.2, -101.56) * mm, "end": v(-7.14, -101.74) * mm});
            skLineSegment(sketch, "E1520", {"start": v(-7.14, -101.74) * mm, "end": v(-7.07, -101.91) * mm});
            skLineSegment(sketch, "E1521", {"start": v(-7.07, -101.91) * mm, "end": v(-7, -102.09) * mm});
            skLineSegment(sketch, "E1522", {"start": v(-7, -102.09) * mm, "end": v(-6.94, -102.26) * mm});
            skLineSegment(sketch, "E1523", {"start": v(-6.94, -102.26) * mm, "end": v(-6.86, -102.27) * mm});
            skLineSegment(sketch, "E1524", {"start": v(-6.86, -102.27) * mm, "end": v(-5.29, -102.36) * mm});
            skLineSegment(sketch, "E1525", {"start": v(-5.29, -102.36) * mm, "end": v(-5.2, -102.37) * mm});
            skLineSegment(sketch, "E1526", {"start": v(-5.2, -102.37) * mm, "end": v(-5.12, -102.2) * mm});
            skLineSegment(sketch, "E1527", {"start": v(-5.12, -102.2) * mm, "end": v(-5.03, -102.03) * mm});
            skLineSegment(sketch, "E1528", {"start": v(-5.03, -102.03) * mm, "end": v(-4.94, -101.87) * mm});
            skLineSegment(sketch, "E1529", {"start": v(-4.94, -101.87) * mm, "end": v(-4.86, -101.7) * mm});
            skLineSegment(sketch, "E1530", {"start": v(-4.86, -101.7) * mm, "end": v(-4.78, -101.54) * mm});
            skLineSegment(sketch, "E1531", {"start": v(-4.78, -101.54) * mm, "end": v(-4.7, -101.38) * mm});
            skLineSegment(sketch, "E1532", {"start": v(-4.7, -101.38) * mm, "end": v(-4.61, -101.22) * mm});
            skLineSegment(sketch, "E1533", {"start": v(-4.61, -101.22) * mm, "end": v(-4.54, -101.06) * mm});
            skLineSegment(sketch, "E1534", {"start": v(-4.54, -101.06) * mm, "end": v(-4.46, -100.9) * mm});
            skLineSegment(sketch, "E1535", {"start": v(-4.46, -100.9) * mm, "end": v(-4.38, -100.74) * mm});
            skLineSegment(sketch, "E1536", {"start": v(-4.38, -100.74) * mm, "end": v(-4.3, -100.59) * mm});
            skLineSegment(sketch, "E1537", {"start": v(-4.3, -100.59) * mm, "end": v(-4.24, -100.43) * mm});
            skLineSegment(sketch, "E1538", {"start": v(-4.24, -100.43) * mm, "end": v(-4.16, -100.28) * mm});
            skLineSegment(sketch, "E1539", {"start": v(-4.16, -100.28) * mm, "end": v(-4.1, -100.13) * mm});
            skLineSegment(sketch, "E1540", {"start": v(-4.1, -100.13) * mm, "end": v(-4.03, -99.98) * mm});
            skLineSegment(sketch, "E1541", {"start": v(-4.03, -99.98) * mm, "end": v(-3.96, -99.83) * mm});
            skLineSegment(sketch, "E1542", {"start": v(-3.96, -99.83) * mm, "end": v(-3.9, -99.68) * mm});
            skLineSegment(sketch, "E1543", {"start": v(-3.9, -99.68) * mm, "end": v(-3.83, -99.54) * mm});
            skLineSegment(sketch, "E1544", {"start": v(-3.83, -99.54) * mm, "end": v(-3.77, -99.4) * mm});
            skLineSegment(sketch, "E1545", {"start": v(-3.77, -99.4) * mm, "end": v(-3.7, -99.25) * mm});
            skLineSegment(sketch, "E1546", {"start": v(-3.7, -99.25) * mm, "end": v(-3.64, -99.1) * mm});
            skLineSegment(sketch, "E1547", {"start": v(-3.64, -99.1) * mm, "end": v(-3.58, -98.97) * mm});
            skLineSegment(sketch, "E1548", {"start": v(-3.58, -98.97) * mm, "end": v(-3.53, -98.83) * mm});
            skLineSegment(sketch, "E1549", {"start": v(-3.53, -98.83) * mm, "end": v(-3.47, -98.69) * mm});
            skLineSegment(sketch, "E1550", {"start": v(-3.47, -98.69) * mm, "end": v(-3.41, -98.55) * mm});
            skLineSegment(sketch, "E1551", {"start": v(-3.41, -98.55) * mm, "end": v(-3.36, -98.42) * mm});
            skLineSegment(sketch, "E1552", {"start": v(-3.36, -98.42) * mm, "end": v(-3.3, -98.28) * mm});
            skLineSegment(sketch, "E1553", {"start": v(-3.3, -98.28) * mm, "end": v(-3.26, -98.15) * mm});
            skLineSegment(sketch, "E1554", {"start": v(-3.26, -98.15) * mm, "end": v(-3.2, -98.02) * mm});
            skLineSegment(sketch, "E1555", {"start": v(-3.2, -98.02) * mm, "end": v(-3.16, -97.9) * mm});
            skLineSegment(sketch, "E1556", {"start": v(-3.16, -97.9) * mm, "end": v(-3.1, -97.76) * mm});
            skLineSegment(sketch, "E1557", {"start": v(-3.1, -97.76) * mm, "end": v(-3.06, -97.64) * mm});
            skLineSegment(sketch, "E1558", {"start": v(-3.06, -97.64) * mm, "end": v(-3.02, -97.51) * mm});
            skLineSegment(sketch, "E1559", {"start": v(-3.02, -97.51) * mm, "end": v(-2.97, -97.39) * mm});
            skLineSegment(sketch, "E1560", {"start": v(-2.97, -97.39) * mm, "end": v(-2.93, -97.26) * mm});
            skLineSegment(sketch, "E1561", {"start": v(-2.93, -97.26) * mm, "end": v(-2.89, -97.14) * mm});
            skLineSegment(sketch, "E1562", {"start": v(-2.89, -97.14) * mm, "end": v(-1.94, -97.1) * mm});
            skLineSegment(sketch, "E1563", {"start": v(-1.94, -97.1) * mm, "end": v(-1, -97.18) * mm});
            skLineSegment(sketch, "E1564", {"start": v(-1, -97.18) * mm, "end": v(-0.96, -97.3) * mm});
            skLineSegment(sketch, "E1565", {"start": v(-0.96, -97.3) * mm, "end": v(-0.92, -97.43) * mm});
            skLineSegment(sketch, "E1566", {"start": v(-0.92, -97.43) * mm, "end": v(-0.88, -97.55) * mm});
            skLineSegment(sketch, "E1567", {"start": v(-0.88, -97.55) * mm, "end": v(-0.84, -97.68) * mm});
            skLineSegment(sketch, "E1568", {"start": v(-0.84, -97.68) * mm, "end": v(-0.8, -97.8) * mm});
            skLineSegment(sketch, "E1569", {"start": v(-0.8, -97.8) * mm, "end": v(-0.76, -97.94) * mm});
            skLineSegment(sketch, "E1570", {"start": v(-0.76, -97.94) * mm, "end": v(-0.72, -98.07) * mm});
            skLineSegment(sketch, "E1571", {"start": v(-0.72, -98.07) * mm, "end": v(-0.67, -98.2) * mm});
            skLineSegment(sketch, "E1572", {"start": v(-0.67, -98.2) * mm, "end": v(-0.62, -98.34) * mm});
            skLineSegment(sketch, "E1573", {"start": v(-0.62, -98.34) * mm, "end": v(-0.58, -98.47) * mm});
            skLineSegment(sketch, "E1574", {"start": v(-0.58, -98.47) * mm, "end": v(-0.53, -98.6) * mm});
            skLineSegment(sketch, "E1575", {"start": v(-0.53, -98.6) * mm, "end": v(-0.48, -98.75) * mm});
            skLineSegment(sketch, "E1576", {"start": v(-0.48, -98.75) * mm, "end": v(-0.43, -98.89) * mm});
            skLineSegment(sketch, "E1577", {"start": v(-0.43, -98.89) * mm, "end": v(-0.38, -99.03) * mm});
            skLineSegment(sketch, "E1578", {"start": v(-0.38, -99.03) * mm, "end": v(-0.32, -99.17) * mm});
            skLineSegment(sketch, "E1579", {"start": v(-0.32, -99.17) * mm, "end": v(-0.27, -99.32) * mm});
            skLineSegment(sketch, "E1580", {"start": v(-0.27, -99.32) * mm, "end": v(-0.21, -99.46) * mm});
            skLineSegment(sketch, "E1581", {"start": v(-0.21, -99.46) * mm, "end": v(-0.15, -99.61) * mm});
            skLineSegment(sketch, "E1582", {"start": v(-0.15, -99.61) * mm, "end": v(-0.1, -99.76) * mm});
            skLineSegment(sketch, "E1583", {"start": v(-0.1, -99.76) * mm, "end": v(-0.04, -99.9) * mm});
            skLineSegment(sketch, "E1584", {"start": v(-0.04, -99.9) * mm, "end": v(0.02, -100.06) * mm});
            skLineSegment(sketch, "E1585", {"start": v(0.02, -100.06) * mm, "end": v(0.09, -100.21) * mm});
            skLineSegment(sketch, "E1586", {"start": v(0.09, -100.21) * mm, "end": v(0.15, -100.37) * mm});
            skLineSegment(sketch, "E1587", {"start": v(0.15, -100.37) * mm, "end": v(0.22, -100.52) * mm});
            skLineSegment(sketch, "E1588", {"start": v(0.22, -100.52) * mm, "end": v(0.28, -100.68) * mm});
            skLineSegment(sketch, "E1589", {"start": v(0.28, -100.68) * mm, "end": v(0.35, -100.84) * mm});
            skLineSegment(sketch, "E1590", {"start": v(0.35, -100.84) * mm, "end": v(0.42, -101) * mm});
            skLineSegment(sketch, "E1591", {"start": v(0.42, -101) * mm, "end": v(0.5, -101.16) * mm});
            skLineSegment(sketch, "E1592", {"start": v(0.5, -101.16) * mm, "end": v(0.56, -101.32) * mm});
            skLineSegment(sketch, "E1593", {"start": v(0.56, -101.32) * mm, "end": v(0.64, -101.48) * mm});
            skLineSegment(sketch, "E1594", {"start": v(0.64, -101.48) * mm, "end": v(0.71, -101.65) * mm});
            skLineSegment(sketch, "E1595", {"start": v(0.71, -101.65) * mm, "end": v(0.79, -101.82) * mm});
            skLineSegment(sketch, "E1596", {"start": v(0.79, -101.82) * mm, "end": v(0.87, -101.98) * mm});
            skLineSegment(sketch, "E1597", {"start": v(0.87, -101.98) * mm, "end": v(0.94, -102.15) * mm});
            skLineSegment(sketch, "E1598", {"start": v(0.94, -102.15) * mm, "end": v(1.03, -102.32) * mm});
            skLineSegment(sketch, "E1599", {"start": v(1.03, -102.32) * mm, "end": v(1.1, -102.5) * mm});
            skLineSegment(sketch, "E1600", {"start": v(1.1, -102.5) * mm, "end": v(1.19, -102.5) * mm});
            skLineSegment(sketch, "E1601", {"start": v(1.19, -102.5) * mm, "end": v(2.76, -102.46) * mm});
            skLineSegment(sketch, "E1602", {"start": v(2.76, -102.46) * mm, "end": v(2.84, -102.46) * mm});
            skLineSegment(sketch, "E1603", {"start": v(2.84, -102.46) * mm, "end": v(2.92, -102.28) * mm});
            skLineSegment(sketch, "E1604", {"start": v(2.92, -102.28) * mm, "end": v(3, -102.11) * mm});
            skLineSegment(sketch, "E1605", {"start": v(3, -102.11) * mm, "end": v(3.06, -101.94) * mm});
            skLineSegment(sketch, "E1606", {"start": v(3.06, -101.94) * mm, "end": v(3.14, -101.77) * mm});
            skLineSegment(sketch, "E1607", {"start": v(3.14, -101.77) * mm, "end": v(3.2, -101.6) * mm});
            skLineSegment(sketch, "E1608", {"start": v(3.2, -101.6) * mm, "end": v(3.27, -101.43) * mm});
            skLineSegment(sketch, "E1609", {"start": v(3.27, -101.43) * mm, "end": v(3.34, -101.27) * mm});
            skLineSegment(sketch, "E1610", {"start": v(3.34, -101.27) * mm, "end": v(3.4, -101.1) * mm});
            skLineSegment(sketch, "E1611", {"start": v(3.4, -101.1) * mm, "end": v(3.47, -100.94) * mm});
            skLineSegment(sketch, "E1612", {"start": v(3.47, -100.94) * mm, "end": v(3.54, -100.78) * mm});
            skLineSegment(sketch, "E1613", {"start": v(3.54, -100.78) * mm, "end": v(3.6, -100.62) * mm});
            skLineSegment(sketch, "E1614", {"start": v(3.6, -100.62) * mm, "end": v(3.66, -100.46) * mm});
            skLineSegment(sketch, "E1615", {"start": v(3.66, -100.46) * mm, "end": v(3.72, -100.3) * mm});
            skLineSegment(sketch, "E1616", {"start": v(3.72, -100.3) * mm, "end": v(3.77, -100.14) * mm});
            skLineSegment(sketch, "E1617", {"start": v(3.77, -100.14) * mm, "end": v(3.83, -99.99) * mm});
            skLineSegment(sketch, "E1618", {"start": v(3.83, -99.99) * mm, "end": v(3.89, -99.83) * mm});
            skLineSegment(sketch, "E1619", {"start": v(3.89, -99.83) * mm, "end": v(3.94, -99.68) * mm});
            skLineSegment(sketch, "E1620", {"start": v(3.94, -99.68) * mm, "end": v(4, -99.53) * mm});
            skLineSegment(sketch, "E1621", {"start": v(4, -99.53) * mm, "end": v(4.04, -99.38) * mm});
            skLineSegment(sketch, "E1622", {"start": v(4.04, -99.38) * mm, "end": v(4.1, -99.23) * mm});
            skLineSegment(sketch, "E1623", {"start": v(4.1, -99.23) * mm, "end": v(4.14, -99.09) * mm});
            skLineSegment(sketch, "E1624", {"start": v(4.14, -99.09) * mm, "end": v(4.2, -98.94) * mm});
            skLineSegment(sketch, "E1625", {"start": v(4.2, -98.94) * mm, "end": v(4.24, -98.8) * mm});
            skLineSegment(sketch, "E1626", {"start": v(4.24, -98.8) * mm, "end": v(4.28, -98.66) * mm});
            skLineSegment(sketch, "E1627", {"start": v(4.28, -98.66) * mm, "end": v(4.33, -98.52) * mm});
            skLineSegment(sketch, "E1628", {"start": v(4.33, -98.52) * mm, "end": v(4.37, -98.38) * mm});
            skLineSegment(sketch, "E1629", {"start": v(4.37, -98.38) * mm, "end": v(4.41, -98.24) * mm});
            skLineSegment(sketch, "E1630", {"start": v(4.41, -98.24) * mm, "end": v(4.45, -98.1) * mm});
            skLineSegment(sketch, "E1631", {"start": v(4.45, -98.1) * mm, "end": v(4.5, -97.97) * mm});
            skLineSegment(sketch, "E1632", {"start": v(4.5, -97.97) * mm, "end": v(4.53, -97.84) * mm});
            skLineSegment(sketch, "E1633", {"start": v(4.53, -97.84) * mm, "end": v(4.57, -97.7) * mm});
            skLineSegment(sketch, "E1634", {"start": v(4.57, -97.7) * mm, "end": v(4.6, -97.57) * mm});
            skLineSegment(sketch, "E1635", {"start": v(4.6, -97.57) * mm, "end": v(4.64, -97.45) * mm});
            skLineSegment(sketch, "E1636", {"start": v(4.64, -97.45) * mm, "end": v(4.68, -97.32) * mm});
            skLineSegment(sketch, "E1637", {"start": v(4.68, -97.32) * mm, "end": v(4.71, -97.2) * mm});
            skLineSegment(sketch, "E1638", {"start": v(4.71, -97.2) * mm, "end": v(4.74, -97.07) * mm});
            skLineSegment(sketch, "E1639", {"start": v(4.74, -97.07) * mm, "end": v(5.68, -96.96) * mm});
            skLineSegment(sketch, "E1640", {"start": v(5.68, -96.96) * mm, "end": v(6.63, -96.96) * mm});
            skLineSegment(sketch, "E1641", {"start": v(6.63, -96.96) * mm, "end": v(6.67, -97.08) * mm});
            skLineSegment(sketch, "E1642", {"start": v(6.67, -97.08) * mm, "end": v(6.72, -97.2) * mm});
            skLineSegment(sketch, "E1643", {"start": v(6.72, -97.2) * mm, "end": v(6.77, -97.32) * mm});
            skLineSegment(sketch, "E1644", {"start": v(6.77, -97.32) * mm, "end": v(6.82, -97.44) * mm});
            skLineSegment(sketch, "E1645", {"start": v(6.82, -97.44) * mm, "end": v(6.87, -97.57) * mm});
            skLineSegment(sketch, "E1646", {"start": v(6.87, -97.57) * mm, "end": v(6.93, -97.7) * mm});
            skLineSegment(sketch, "E1647", {"start": v(6.93, -97.7) * mm, "end": v(6.98, -97.82) * mm});
            skLineSegment(sketch, "E1648", {"start": v(6.98, -97.82) * mm, "end": v(7.04, -97.95) * mm});
            skLineSegment(sketch, "E1649", {"start": v(7.04, -97.95) * mm, "end": v(7.1, -98.08) * mm});
            skLineSegment(sketch, "E1650", {"start": v(7.1, -98.08) * mm, "end": v(7.15, -98.21) * mm});
            skLineSegment(sketch, "E1651", {"start": v(7.15, -98.21) * mm, "end": v(7.2, -98.35) * mm});
            skLineSegment(sketch, "E1652", {"start": v(7.2, -98.35) * mm, "end": v(7.27, -98.48) * mm});
            skLineSegment(sketch, "E1653", {"start": v(7.27, -98.48) * mm, "end": v(7.33, -98.62) * mm});
            skLineSegment(sketch, "E1654", {"start": v(7.33, -98.62) * mm, "end": v(7.4, -98.75) * mm});
            skLineSegment(sketch, "E1655", {"start": v(7.4, -98.75) * mm, "end": v(7.46, -98.9) * mm});
            skLineSegment(sketch, "E1656", {"start": v(7.46, -98.9) * mm, "end": v(7.53, -99.03) * mm});
            skLineSegment(sketch, "E1657", {"start": v(7.53, -99.03) * mm, "end": v(7.6, -99.17) * mm});
            skLineSegment(sketch, "E1658", {"start": v(7.6, -99.17) * mm, "end": v(7.66, -99.32) * mm});
            skLineSegment(sketch, "E1659", {"start": v(7.66, -99.32) * mm, "end": v(7.73, -99.46) * mm});
            skLineSegment(sketch, "E1660", {"start": v(7.73, -99.46) * mm, "end": v(7.8, -99.6) * mm});
            skLineSegment(sketch, "E1661", {"start": v(7.8, -99.6) * mm, "end": v(7.88, -99.75) * mm});
            skLineSegment(sketch, "E1662", {"start": v(7.88, -99.75) * mm, "end": v(7.95, -99.9) * mm});
            skLineSegment(sketch, "E1663", {"start": v(7.95, -99.9) * mm, "end": v(8.03, -100.05) * mm});
            skLineSegment(sketch, "E1664", {"start": v(8.03, -100.05) * mm, "end": v(8.1, -100.2) * mm});
            skLineSegment(sketch, "E1665", {"start": v(8.1, -100.2) * mm, "end": v(8.18, -100.35) * mm});
            skLineSegment(sketch, "E1666", {"start": v(8.18, -100.35) * mm, "end": v(8.26, -100.5) * mm});
            skLineSegment(sketch, "E1667", {"start": v(8.26, -100.5) * mm, "end": v(8.34, -100.65) * mm});
            skLineSegment(sketch, "E1668", {"start": v(8.34, -100.65) * mm, "end": v(8.43, -100.8) * mm});
            skLineSegment(sketch, "E1669", {"start": v(8.43, -100.8) * mm, "end": v(8.51, -100.96) * mm});
            skLineSegment(sketch, "E1670", {"start": v(8.51, -100.96) * mm, "end": v(8.6, -101.12) * mm});
            skLineSegment(sketch, "E1671", {"start": v(8.6, -101.12) * mm, "end": v(8.68, -101.28) * mm});
            skLineSegment(sketch, "E1672", {"start": v(8.68, -101.28) * mm, "end": v(8.77, -101.44) * mm});
            skLineSegment(sketch, "E1673", {"start": v(8.77, -101.44) * mm, "end": v(8.86, -101.6) * mm});
            skLineSegment(sketch, "E1674", {"start": v(8.86, -101.6) * mm, "end": v(8.96, -101.76) * mm});
            skLineSegment(sketch, "E1675", {"start": v(8.96, -101.76) * mm, "end": v(9.05, -101.92) * mm});
            skLineSegment(sketch, "E1676", {"start": v(9.05, -101.92) * mm, "end": v(9.15, -102.09) * mm});
            skLineSegment(sketch, "E1677", {"start": v(9.15, -102.09) * mm, "end": v(9.23, -102.08) * mm});
            skLineSegment(sketch, "E1678", {"start": v(9.23, -102.08) * mm, "end": v(10.8, -101.93) * mm});
            skLineSegment(sketch, "E1679", {"start": v(10.8, -101.93) * mm, "end": v(10.87, -101.92) * mm});
            skLineSegment(sketch, "E1680", {"start": v(10.87, -101.92) * mm, "end": v(10.93, -101.74) * mm});
            skLineSegment(sketch, "E1681", {"start": v(10.93, -101.74) * mm, "end": v(11, -101.56) * mm});
            skLineSegment(sketch, "E1682", {"start": v(11, -101.56) * mm, "end": v(11.05, -101.39) * mm});
            skLineSegment(sketch, "E1683", {"start": v(11.05, -101.39) * mm, "end": v(11.11, -101.21) * mm});
            skLineSegment(sketch, "E1684", {"start": v(11.11, -101.21) * mm, "end": v(11.17, -101.04) * mm});
            skLineSegment(sketch, "E1685", {"start": v(11.17, -101.04) * mm, "end": v(11.22, -100.86) * mm});
            skLineSegment(sketch, "E1686", {"start": v(11.22, -100.86) * mm, "end": v(11.28, -100.7) * mm});
            skLineSegment(sketch, "E1687", {"start": v(11.28, -100.7) * mm, "end": v(11.33, -100.52) * mm});
            skLineSegment(sketch, "E1688", {"start": v(11.33, -100.52) * mm, "end": v(11.38, -100.36) * mm});
            skLineSegment(sketch, "E1689", {"start": v(11.38, -100.36) * mm, "end": v(11.43, -100.19) * mm});
            skLineSegment(sketch, "E1690", {"start": v(11.43, -100.19) * mm, "end": v(11.48, -100.02) * mm});
            skLineSegment(sketch, "E1691", {"start": v(11.48, -100.02) * mm, "end": v(11.53, -99.86) * mm});
            skLineSegment(sketch, "E1692", {"start": v(11.53, -99.86) * mm, "end": v(11.57, -99.7) * mm});
            skLineSegment(sketch, "E1693", {"start": v(11.57, -99.7) * mm, "end": v(11.62, -99.54) * mm});
            skLineSegment(sketch, "E1694", {"start": v(11.62, -99.54) * mm, "end": v(11.66, -99.38) * mm});
            skLineSegment(sketch, "E1695", {"start": v(11.66, -99.38) * mm, "end": v(11.7, -99.22) * mm});
            skLineSegment(sketch, "E1696", {"start": v(11.7, -99.22) * mm, "end": v(11.75, -99.07) * mm});
            skLineSegment(sketch, "E1697", {"start": v(11.75, -99.07) * mm, "end": v(11.79, -98.91) * mm});
            skLineSegment(sketch, "E1698", {"start": v(11.79, -98.91) * mm, "end": v(11.83, -98.76) * mm});
            skLineSegment(sketch, "E1699", {"start": v(11.83, -98.76) * mm, "end": v(11.87, -98.6) * mm});
            skLineSegment(sketch, "E1700", {"start": v(11.87, -98.6) * mm, "end": v(11.9, -98.46) * mm});
            skLineSegment(sketch, "E1701", {"start": v(11.9, -98.46) * mm, "end": v(11.94, -98.3) * mm});
            skLineSegment(sketch, "E1702", {"start": v(11.94, -98.3) * mm, "end": v(11.98, -98.16) * mm});
            skLineSegment(sketch, "E1703", {"start": v(11.98, -98.16) * mm, "end": v(12.01, -98.02) * mm});
            skLineSegment(sketch, "E1704", {"start": v(12.01, -98.02) * mm, "end": v(12.04, -97.87) * mm});
            skLineSegment(sketch, "E1705", {"start": v(12.04, -97.87) * mm, "end": v(12.08, -97.73) * mm});
            skLineSegment(sketch, "E1706", {"start": v(12.08, -97.73) * mm, "end": v(12.1, -97.6) * mm});
            skLineSegment(sketch, "E1707", {"start": v(12.1, -97.6) * mm, "end": v(12.14, -97.45) * mm});
            skLineSegment(sketch, "E1708", {"start": v(12.14, -97.45) * mm, "end": v(12.17, -97.31) * mm});
            skLineSegment(sketch, "E1709", {"start": v(12.17, -97.31) * mm, "end": v(12.2, -97.18) * mm});
            skLineSegment(sketch, "E1710", {"start": v(12.2, -97.18) * mm, "end": v(12.22, -97.04) * mm});
            skLineSegment(sketch, "E1711", {"start": v(12.22, -97.04) * mm, "end": v(12.25, -96.91) * mm});
            skLineSegment(sketch, "E1712", {"start": v(12.25, -96.91) * mm, "end": v(12.27, -96.78) * mm});
            skLineSegment(sketch, "E1713", {"start": v(12.27, -96.78) * mm, "end": v(12.3, -96.65) * mm});
            skLineSegment(sketch, "E1714", {"start": v(12.3, -96.65) * mm, "end": v(12.32, -96.52) * mm});
            skLineSegment(sketch, "E1715", {"start": v(12.32, -96.52) * mm, "end": v(12.35, -96.4) * mm});
            skLineSegment(sketch, "E1716", {"start": v(12.35, -96.4) * mm, "end": v(13.27, -96.21) * mm});
            skLineSegment(sketch, "E1717", {"start": v(13.27, -96.21) * mm, "end": v(14.21, -96.14) * mm});
            skLineSegment(sketch, "E1718", {"start": v(14.21, -96.14) * mm, "end": v(14.27, -96.26) * mm});
            skLineSegment(sketch, "E1719", {"start": v(14.27, -96.26) * mm, "end": v(14.33, -96.37) * mm});
            skLineSegment(sketch, "E1720", {"start": v(14.33, -96.37) * mm, "end": v(14.39, -96.5) * mm});
            skLineSegment(sketch, "E1721", {"start": v(14.39, -96.5) * mm, "end": v(14.45, -96.6) * mm});
            skLineSegment(sketch, "E1722", {"start": v(14.45, -96.6) * mm, "end": v(14.5, -96.73) * mm});
            skLineSegment(sketch, "E1723", {"start": v(14.5, -96.73) * mm, "end": v(14.57, -96.85) * mm});
            skLineSegment(sketch, "E1724", {"start": v(14.57, -96.85) * mm, "end": v(14.63, -96.97) * mm});
            skLineSegment(sketch, "E1725", {"start": v(14.63, -96.97) * mm, "end": v(14.7, -97.1) * mm});
            skLineSegment(sketch, "E1726", {"start": v(14.7, -97.1) * mm, "end": v(14.77, -97.22) * mm});
            skLineSegment(sketch, "E1727", {"start": v(14.77, -97.22) * mm, "end": v(14.83, -97.35) * mm});
            skLineSegment(sketch, "E1728", {"start": v(14.83, -97.35) * mm, "end": v(14.9, -97.48) * mm});
            skLineSegment(sketch, "E1729", {"start": v(14.9, -97.48) * mm, "end": v(14.97, -97.6) * mm});
            skLineSegment(sketch, "E1730", {"start": v(14.97, -97.6) * mm, "end": v(15.05, -97.74) * mm});
            skLineSegment(sketch, "E1731", {"start": v(15.05, -97.74) * mm, "end": v(15.12, -97.87) * mm});
            skLineSegment(sketch, "E1732", {"start": v(15.12, -97.87) * mm, "end": v(15.2, -98) * mm});
            skLineSegment(sketch, "E1733", {"start": v(15.2, -98) * mm, "end": v(15.27, -98.14) * mm});
            skLineSegment(sketch, "E1734", {"start": v(15.27, -98.14) * mm, "end": v(15.35, -98.27) * mm});
            skLineSegment(sketch, "E1735", {"start": v(15.35, -98.27) * mm, "end": v(15.43, -98.4) * mm});
            skLineSegment(sketch, "E1736", {"start": v(15.43, -98.4) * mm, "end": v(15.51, -98.55) * mm});
            skLineSegment(sketch, "E1737", {"start": v(15.51, -98.55) * mm, "end": v(15.6, -98.69) * mm});
            skLineSegment(sketch, "E1738", {"start": v(15.6, -98.69) * mm, "end": v(15.68, -98.83) * mm});
            skLineSegment(sketch, "E1739", {"start": v(15.68, -98.83) * mm, "end": v(15.76, -98.97) * mm});
            skLineSegment(sketch, "E1740", {"start": v(15.76, -98.97) * mm, "end": v(15.85, -99.1) * mm});
            skLineSegment(sketch, "E1741", {"start": v(15.85, -99.1) * mm, "end": v(15.94, -99.25) * mm});
            skLineSegment(sketch, "E1742", {"start": v(15.94, -99.25) * mm, "end": v(16.03, -99.4) * mm});
            skLineSegment(sketch, "E1743", {"start": v(16.03, -99.4) * mm, "end": v(16.12, -99.54) * mm});
            skLineSegment(sketch, "E1744", {"start": v(16.12, -99.54) * mm, "end": v(16.21, -99.69) * mm});
            skLineSegment(sketch, "E1745", {"start": v(16.21, -99.69) * mm, "end": v(16.3, -99.84) * mm});
            skLineSegment(sketch, "E1746", {"start": v(16.3, -99.84) * mm, "end": v(16.4, -99.99) * mm});
            skLineSegment(sketch, "E1747", {"start": v(16.4, -99.99) * mm, "end": v(16.5, -100.14) * mm});
            skLineSegment(sketch, "E1748", {"start": v(16.5, -100.14) * mm, "end": v(16.6, -100.29) * mm});
            skLineSegment(sketch, "E1749", {"start": v(16.6, -100.29) * mm, "end": v(16.7, -100.44) * mm});
            skLineSegment(sketch, "E1750", {"start": v(16.7, -100.44) * mm, "end": v(16.8, -100.6) * mm});
            skLineSegment(sketch, "E1751", {"start": v(16.8, -100.6) * mm, "end": v(16.91, -100.75) * mm});
            skLineSegment(sketch, "E1752", {"start": v(16.91, -100.75) * mm, "end": v(17.02, -100.9) * mm});
            skLineSegment(sketch, "E1753", {"start": v(17.02, -100.9) * mm, "end": v(17.13, -101.06) * mm});
            skLineSegment(sketch, "E1754", {"start": v(17.13, -101.06) * mm, "end": v(17.2, -101.05) * mm});
            skLineSegment(sketch, "E1755", {"start": v(17.2, -101.05) * mm, "end": v(18.76, -100.77) * mm});
            skLineSegment(sketch, "E1756", {"start": v(18.76, -100.77) * mm, "end": v(18.84, -100.75) * mm});
            skLineSegment(sketch, "E1757", {"start": v(18.84, -100.75) * mm, "end": v(18.88, -100.57) * mm});
            skLineSegment(sketch, "E1758", {"start": v(18.88, -100.57) * mm, "end": v(18.93, -100.39) * mm});
            skLineSegment(sketch, "E1759", {"start": v(18.93, -100.39) * mm, "end": v(18.97, -100.2) * mm});
            skLineSegment(sketch, "E1760", {"start": v(18.97, -100.2) * mm, "end": v(19.02, -100.03) * mm});
            skLineSegment(sketch, "E1761", {"start": v(19.02, -100.03) * mm, "end": v(19.06, -99.85) * mm});
            skLineSegment(sketch, "E1762", {"start": v(19.06, -99.85) * mm, "end": v(19.1, -99.67) * mm});
            skLineSegment(sketch, "E1763", {"start": v(19.1, -99.67) * mm, "end": v(19.14, -99.5) * mm});
            skLineSegment(sketch, "E1764", {"start": v(19.14, -99.5) * mm, "end": v(19.18, -99.32) * mm});
            skLineSegment(sketch, "E1765", {"start": v(19.18, -99.32) * mm, "end": v(19.22, -99.15) * mm});
            skLineSegment(sketch, "E1766", {"start": v(19.22, -99.15) * mm, "end": v(19.26, -98.98) * mm});
            skLineSegment(sketch, "E1767", {"start": v(19.26, -98.98) * mm, "end": v(19.3, -98.82) * mm});
            skLineSegment(sketch, "E1768", {"start": v(19.3, -98.82) * mm, "end": v(19.33, -98.65) * mm});
            skLineSegment(sketch, "E1769", {"start": v(19.33, -98.65) * mm, "end": v(19.36, -98.48) * mm});
            skLineSegment(sketch, "E1770", {"start": v(19.36, -98.48) * mm, "end": v(19.4, -98.32) * mm});
            skLineSegment(sketch, "E1771", {"start": v(19.4, -98.32) * mm, "end": v(19.43, -98.16) * mm});
            skLineSegment(sketch, "E1772", {"start": v(19.43, -98.16) * mm, "end": v(19.46, -98) * mm});
            skLineSegment(sketch, "E1773", {"start": v(19.46, -98) * mm, "end": v(19.49, -97.84) * mm});
            skLineSegment(sketch, "E1774", {"start": v(19.49, -97.84) * mm, "end": v(19.51, -97.68) * mm});
            skLineSegment(sketch, "E1775", {"start": v(19.51, -97.68) * mm, "end": v(19.54, -97.53) * mm});
            skLineSegment(sketch, "E1776", {"start": v(19.54, -97.53) * mm, "end": v(19.57, -97.37) * mm});
            skLineSegment(sketch, "E1777", {"start": v(19.57, -97.37) * mm, "end": v(19.6, -97.22) * mm});
            skLineSegment(sketch, "E1778", {"start": v(19.6, -97.22) * mm, "end": v(19.62, -97.07) * mm});
            skLineSegment(sketch, "E1779", {"start": v(19.62, -97.07) * mm, "end": v(19.64, -96.92) * mm});
            skLineSegment(sketch, "E1780", {"start": v(19.64, -96.92) * mm, "end": v(19.66, -96.77) * mm});
            skLineSegment(sketch, "E1781", {"start": v(19.66, -96.77) * mm, "end": v(19.69, -96.63) * mm});
            skLineSegment(sketch, "E1782", {"start": v(19.69, -96.63) * mm, "end": v(19.7, -96.48) * mm});
            skLineSegment(sketch, "E1783", {"start": v(19.7, -96.48) * mm, "end": v(19.73, -96.34) * mm});
            skLineSegment(sketch, "E1784", {"start": v(19.73, -96.34) * mm, "end": v(19.75, -96.2) * mm});
            skLineSegment(sketch, "E1785", {"start": v(19.75, -96.2) * mm, "end": v(19.76, -96.06) * mm});
            skLineSegment(sketch, "E1786", {"start": v(19.76, -96.06) * mm, "end": v(19.78, -95.92) * mm});
            skLineSegment(sketch, "E1787", {"start": v(19.78, -95.92) * mm, "end": v(19.8, -95.79) * mm});
            skLineSegment(sketch, "E1788", {"start": v(19.8, -95.79) * mm, "end": v(19.81, -95.65) * mm});
            skLineSegment(sketch, "E1789", {"start": v(19.81, -95.65) * mm, "end": v(19.83, -95.52) * mm});
            skLineSegment(sketch, "E1790", {"start": v(19.83, -95.52) * mm, "end": v(19.84, -95.39) * mm});
            skLineSegment(sketch, "E1791", {"start": v(19.84, -95.39) * mm, "end": v(19.86, -95.26) * mm});
            skLineSegment(sketch, "E1792", {"start": v(19.86, -95.26) * mm, "end": v(19.87, -95.13) * mm});
            skLineSegment(sketch, "E1793", {"start": v(19.87, -95.13) * mm, "end": v(20.78, -94.88) * mm});
            skLineSegment(sketch, "E1794", {"start": v(20.78, -94.88) * mm, "end": v(21.71, -94.73) * mm});
            skLineSegment(sketch, "E1795", {"start": v(21.71, -94.73) * mm, "end": v(21.78, -94.84) * mm});
            skLineSegment(sketch, "E1796", {"start": v(21.78, -94.84) * mm, "end": v(21.85, -94.95) * mm});
            skLineSegment(sketch, "E1797", {"start": v(21.85, -94.95) * mm, "end": v(21.91, -95.06) * mm});
            skLineSegment(sketch, "E1798", {"start": v(21.91, -95.06) * mm, "end": v(21.98, -95.18) * mm});
            skLineSegment(sketch, "E1799", {"start": v(21.98, -95.18) * mm, "end": v(22.05, -95.3) * mm});
            skLineSegment(sketch, "E1800", {"start": v(22.05, -95.3) * mm, "end": v(22.12, -95.4) * mm});
            skLineSegment(sketch, "E1801", {"start": v(22.12, -95.4) * mm, "end": v(22.2, -95.53) * mm});
            skLineSegment(sketch, "E1802", {"start": v(22.2, -95.53) * mm, "end": v(22.27, -95.65) * mm});
            skLineSegment(sketch, "E1803", {"start": v(22.27, -95.65) * mm, "end": v(22.35, -95.77) * mm});
            skLineSegment(sketch, "E1804", {"start": v(22.35, -95.77) * mm, "end": v(22.43, -95.89) * mm});
            skLineSegment(sketch, "E1805", {"start": v(22.43, -95.89) * mm, "end": v(22.5, -96) * mm});
            skLineSegment(sketch, "E1806", {"start": v(22.5, -96) * mm, "end": v(22.59, -96.13) * mm});
            skLineSegment(sketch, "E1807", {"start": v(22.59, -96.13) * mm, "end": v(22.67, -96.26) * mm});
            skLineSegment(sketch, "E1808", {"start": v(22.67, -96.26) * mm, "end": v(22.75, -96.38) * mm});
            skLineSegment(sketch, "E1809", {"start": v(22.75, -96.38) * mm, "end": v(22.84, -96.5) * mm});
            skLineSegment(sketch, "E1810", {"start": v(22.84, -96.5) * mm, "end": v(22.92, -96.64) * mm});
            skLineSegment(sketch, "E1811", {"start": v(22.92, -96.64) * mm, "end": v(23.01, -96.77) * mm});
            skLineSegment(sketch, "E1812", {"start": v(23.01, -96.77) * mm, "end": v(23.1, -96.9) * mm});
            skLineSegment(sketch, "E1813", {"start": v(23.1, -96.9) * mm, "end": v(23.2, -97.03) * mm});
            skLineSegment(sketch, "E1814", {"start": v(23.2, -97.03) * mm, "end": v(23.29, -97.16) * mm});
            skLineSegment(sketch, "E1815", {"start": v(23.29, -97.16) * mm, "end": v(23.38, -97.3) * mm});
            skLineSegment(sketch, "E1816", {"start": v(23.38, -97.3) * mm, "end": v(23.48, -97.42) * mm});
            skLineSegment(sketch, "E1817", {"start": v(23.48, -97.42) * mm, "end": v(23.58, -97.56) * mm});
            skLineSegment(sketch, "E1818", {"start": v(23.58, -97.56) * mm, "end": v(23.68, -97.7) * mm});
            skLineSegment(sketch, "E1819", {"start": v(23.68, -97.7) * mm, "end": v(23.78, -97.83) * mm});
            skLineSegment(sketch, "E1820", {"start": v(23.78, -97.83) * mm, "end": v(23.88, -97.97) * mm});
            skLineSegment(sketch, "E1821", {"start": v(23.88, -97.97) * mm, "end": v(23.99, -98.1) * mm});
            skLineSegment(sketch, "E1822", {"start": v(23.99, -98.1) * mm, "end": v(24.1, -98.25) * mm});
            skLineSegment(sketch, "E1823", {"start": v(24.1, -98.25) * mm, "end": v(24.2, -98.4) * mm});
            skLineSegment(sketch, "E1824", {"start": v(24.2, -98.4) * mm, "end": v(24.3, -98.53) * mm});
            skLineSegment(sketch, "E1825", {"start": v(24.3, -98.53) * mm, "end": v(24.42, -98.67) * mm});
            skLineSegment(sketch, "E1826", {"start": v(24.42, -98.67) * mm, "end": v(24.53, -98.82) * mm});
            skLineSegment(sketch, "E1827", {"start": v(24.53, -98.82) * mm, "end": v(24.65, -98.96) * mm});
            skLineSegment(sketch, "E1828", {"start": v(24.65, -98.96) * mm, "end": v(24.77, -99.1) * mm});
            skLineSegment(sketch, "E1829", {"start": v(24.77, -99.1) * mm, "end": v(24.88, -99.25) * mm});
            skLineSegment(sketch, "E1830", {"start": v(24.88, -99.25) * mm, "end": v(25, -99.4) * mm});
            skLineSegment(sketch, "E1831", {"start": v(25, -99.4) * mm, "end": v(25.08, -99.38) * mm});
            skLineSegment(sketch, "E1832", {"start": v(25.08, -99.38) * mm, "end": v(26.6, -98.99) * mm});
            skLineSegment(sketch, "E1833", {"start": v(26.6, -98.99) * mm, "end": v(26.68, -98.96) * mm});
            skLineSegment(sketch, "E1834", {"start": v(26.68, -98.96) * mm, "end": v(26.72, -98.78) * mm});
            skLineSegment(sketch, "E1835", {"start": v(26.72, -98.78) * mm, "end": v(26.75, -98.6) * mm});
            skLineSegment(sketch, "E1836", {"start": v(26.75, -98.6) * mm, "end": v(26.78, -98.4) * mm});
            skLineSegment(sketch, "E1837", {"start": v(26.78, -98.4) * mm, "end": v(26.8, -98.23) * mm});
            skLineSegment(sketch, "E1838", {"start": v(26.8, -98.23) * mm, "end": v(26.84, -98.05) * mm});
            skLineSegment(sketch, "E1839", {"start": v(26.84, -98.05) * mm, "end": v(26.86, -97.87) * mm});
            skLineSegment(sketch, "E1840", {"start": v(26.86, -97.87) * mm, "end": v(26.9, -97.69) * mm});
            skLineSegment(sketch, "E1841", {"start": v(26.9, -97.69) * mm, "end": v(26.92, -97.51) * mm});
            skLineSegment(sketch, "E1842", {"start": v(26.92, -97.51) * mm, "end": v(26.94, -97.34) * mm});
            skLineSegment(sketch, "E1843", {"start": v(26.94, -97.34) * mm, "end": v(26.96, -97.17) * mm});
            skLineSegment(sketch, "E1844", {"start": v(26.96, -97.17) * mm, "end": v(26.99, -97) * mm});
            skLineSegment(sketch, "E1845", {"start": v(26.99, -97) * mm, "end": v(27, -96.83) * mm});
            skLineSegment(sketch, "E1846", {"start": v(27, -96.83) * mm, "end": v(27.03, -96.66) * mm});
            skLineSegment(sketch, "E1847", {"start": v(27.03, -96.66) * mm, "end": v(27.05, -96.5) * mm});
            skLineSegment(sketch, "E1848", {"start": v(27.05, -96.5) * mm, "end": v(27.07, -96.33) * mm});
            skLineSegment(sketch, "E1849", {"start": v(27.07, -96.33) * mm, "end": v(27.08, -96.17) * mm});
            skLineSegment(sketch, "E1850", {"start": v(27.08, -96.17) * mm, "end": v(27.1, -96) * mm});
            skLineSegment(sketch, "E1851", {"start": v(27.1, -96) * mm, "end": v(27.12, -95.85) * mm});
            skLineSegment(sketch, "E1852", {"start": v(27.12, -95.85) * mm, "end": v(27.13, -95.7) * mm});
            skLineSegment(sketch, "E1853", {"start": v(27.13, -95.7) * mm, "end": v(27.15, -95.54) * mm});
            skLineSegment(sketch, "E1854", {"start": v(27.15, -95.54) * mm, "end": v(27.16, -95.38) * mm});
            skLineSegment(sketch, "E1855", {"start": v(27.16, -95.38) * mm, "end": v(27.17, -95.23) * mm});
            skLineSegment(sketch, "E1856", {"start": v(27.17, -95.23) * mm, "end": v(27.19, -95.08) * mm});
            skLineSegment(sketch, "E1857", {"start": v(27.19, -95.08) * mm, "end": v(27.2, -94.93) * mm});
            skLineSegment(sketch, "E1858", {"start": v(27.2, -94.93) * mm, "end": v(27.2, -94.78) * mm});
            skLineSegment(sketch, "E1859", {"start": v(27.2, -94.78) * mm, "end": v(27.22, -94.64) * mm});
            skLineSegment(sketch, "E1860", {"start": v(27.22, -94.64) * mm, "end": v(27.23, -94.5) * mm});
            skLineSegment(sketch, "E1861", {"start": v(27.23, -94.5) * mm, "end": v(27.23, -94.35) * mm});
            skLineSegment(sketch, "E1862", {"start": v(27.23, -94.35) * mm, "end": v(27.24, -94.21) * mm});
            skLineSegment(sketch, "E1863", {"start": v(27.24, -94.21) * mm, "end": v(27.25, -94.07) * mm});
            skLineSegment(sketch, "E1864", {"start": v(27.25, -94.07) * mm, "end": v(27.25, -93.94) * mm});
            skLineSegment(sketch, "E1865", {"start": v(27.25, -93.94) * mm, "end": v(27.26, -93.8) * mm});
            skLineSegment(sketch, "E1866", {"start": v(27.26, -93.8) * mm, "end": v(27.26, -93.67) * mm});
            skLineSegment(sketch, "E1867", {"start": v(27.26, -93.67) * mm, "end": v(27.27, -93.54) * mm});
            skLineSegment(sketch, "E1868", {"start": v(27.27, -93.54) * mm, "end": v(27.27, -93.4) * mm});
            skLineSegment(sketch, "E1869", {"start": v(27.27, -93.4) * mm, "end": v(27.27, -93.28) * mm});
            skLineSegment(sketch, "E1870", {"start": v(27.27, -93.28) * mm, "end": v(28.16, -92.95) * mm});
            skLineSegment(sketch, "E1871", {"start": v(28.16, -92.95) * mm, "end": v(29.08, -92.73) * mm});
            skLineSegment(sketch, "E1872", {"start": v(29.08, -92.73) * mm, "end": v(29.15, -92.84) * mm});
            skLineSegment(sketch, "E1873", {"start": v(29.15, -92.84) * mm, "end": v(29.23, -92.94) * mm});
            skLineSegment(sketch, "E1874", {"start": v(29.23, -92.94) * mm, "end": v(29.3, -93.05) * mm});
            skLineSegment(sketch, "E1875", {"start": v(29.3, -93.05) * mm, "end": v(29.38, -93.16) * mm});
            skLineSegment(sketch, "E1876", {"start": v(29.38, -93.16) * mm, "end": v(29.46, -93.27) * mm});
            skLineSegment(sketch, "E1877", {"start": v(29.46, -93.27) * mm, "end": v(29.54, -93.38) * mm});
            skLineSegment(sketch, "E1878", {"start": v(29.54, -93.38) * mm, "end": v(29.62, -93.5) * mm});
            skLineSegment(sketch, "E1879", {"start": v(29.62, -93.5) * mm, "end": v(29.7, -93.6) * mm});
            skLineSegment(sketch, "E1880", {"start": v(29.7, -93.6) * mm, "end": v(29.8, -93.72) * mm});
            skLineSegment(sketch, "E1881", {"start": v(29.8, -93.72) * mm, "end": v(29.88, -93.83) * mm});
            skLineSegment(sketch, "E1882", {"start": v(29.88, -93.83) * mm, "end": v(29.97, -93.95) * mm});
            skLineSegment(sketch, "E1883", {"start": v(29.97, -93.95) * mm, "end": v(30.06, -94.06) * mm});
            skLineSegment(sketch, "E1884", {"start": v(30.06, -94.06) * mm, "end": v(30.15, -94.18) * mm});
            skLineSegment(sketch, "E1885", {"start": v(30.15, -94.18) * mm, "end": v(30.24, -94.3) * mm});
            skLineSegment(sketch, "E1886", {"start": v(30.24, -94.3) * mm, "end": v(30.34, -94.42) * mm});
            skLineSegment(sketch, "E1887", {"start": v(30.34, -94.42) * mm, "end": v(30.44, -94.54) * mm});
            skLineSegment(sketch, "E1888", {"start": v(30.44, -94.54) * mm, "end": v(30.53, -94.66) * mm});
            skLineSegment(sketch, "E1889", {"start": v(30.53, -94.66) * mm, "end": v(30.63, -94.78) * mm});
            skLineSegment(sketch, "E1890", {"start": v(30.63, -94.78) * mm, "end": v(30.74, -94.9) * mm});
            skLineSegment(sketch, "E1891", {"start": v(30.74, -94.9) * mm, "end": v(30.84, -95.03) * mm});
            skLineSegment(sketch, "E1892", {"start": v(30.84, -95.03) * mm, "end": v(30.94, -95.16) * mm});
            skLineSegment(sketch, "E1893", {"start": v(30.94, -95.16) * mm, "end": v(31.05, -95.28) * mm});
            skLineSegment(sketch, "E1894", {"start": v(31.05, -95.28) * mm, "end": v(31.16, -95.4) * mm});
            skLineSegment(sketch, "E1895", {"start": v(31.16, -95.4) * mm, "end": v(31.27, -95.54) * mm});
            skLineSegment(sketch, "E1896", {"start": v(31.27, -95.54) * mm, "end": v(31.38, -95.67) * mm});
            skLineSegment(sketch, "E1897", {"start": v(31.38, -95.67) * mm, "end": v(31.5, -95.8) * mm});
            skLineSegment(sketch, "E1898", {"start": v(31.5, -95.8) * mm, "end": v(31.6, -95.93) * mm});
            skLineSegment(sketch, "E1899", {"start": v(31.6, -95.93) * mm, "end": v(31.73, -96.06) * mm});
            skLineSegment(sketch, "E1900", {"start": v(31.73, -96.06) * mm, "end": v(31.84, -96.19) * mm});
            skLineSegment(sketch, "E1901", {"start": v(31.84, -96.19) * mm, "end": v(31.97, -96.32) * mm});
            skLineSegment(sketch, "E1902", {"start": v(31.97, -96.32) * mm, "end": v(32.09, -96.45) * mm});
            skLineSegment(sketch, "E1903", {"start": v(32.09, -96.45) * mm, "end": v(32.21, -96.59) * mm});
            skLineSegment(sketch, "E1904", {"start": v(32.21, -96.59) * mm, "end": v(32.34, -96.72) * mm});
            skLineSegment(sketch, "E1905", {"start": v(32.34, -96.72) * mm, "end": v(32.46, -96.86) * mm});
            skLineSegment(sketch, "E1906", {"start": v(32.46, -96.86) * mm, "end": v(32.6, -97) * mm});
            skLineSegment(sketch, "E1907", {"start": v(32.6, -97) * mm, "end": v(32.73, -97.13) * mm});
            skLineSegment(sketch, "E1908", {"start": v(32.73, -97.13) * mm, "end": v(32.8, -97.1) * mm});
            skLineSegment(sketch, "E1909", {"start": v(32.8, -97.1) * mm, "end": v(34.29, -96.6) * mm});
            skLineSegment(sketch, "E1910", {"start": v(34.29, -96.6) * mm, "end": v(34.36, -96.57) * mm});
            skLineSegment(sketch, "E1911", {"start": v(34.36, -96.57) * mm, "end": v(34.38, -96.38) * mm});
            skLineSegment(sketch, "E1912", {"start": v(34.38, -96.38) * mm, "end": v(34.4, -96.19) * mm});
            skLineSegment(sketch, "E1913", {"start": v(34.4, -96.19) * mm, "end": v(34.42, -96) * mm});
            skLineSegment(sketch, "E1914", {"start": v(34.42, -96) * mm, "end": v(34.43, -95.82) * mm});
            skLineSegment(sketch, "E1915", {"start": v(34.43, -95.82) * mm, "end": v(34.45, -95.64) * mm});
            skLineSegment(sketch, "E1916", {"start": v(34.45, -95.64) * mm, "end": v(34.46, -95.46) * mm});
            skLineSegment(sketch, "E1917", {"start": v(34.46, -95.46) * mm, "end": v(34.47, -95.28) * mm});
            skLineSegment(sketch, "E1918", {"start": v(34.47, -95.28) * mm, "end": v(34.48, -95.1) * mm});
            skLineSegment(sketch, "E1919", {"start": v(34.48, -95.1) * mm, "end": v(34.5, -94.93) * mm});
            skLineSegment(sketch, "E1920", {"start": v(34.5, -94.93) * mm, "end": v(34.5, -94.75) * mm});
            skLineSegment(sketch, "E1921", {"start": v(34.5, -94.75) * mm, "end": v(34.51, -94.58) * mm});
            skLineSegment(sketch, "E1922", {"start": v(34.51, -94.58) * mm, "end": v(34.52, -94.41) * mm});
            skLineSegment(sketch, "E1923", {"start": v(34.52, -94.41) * mm, "end": v(34.53, -94.24) * mm});
            skLineSegment(sketch, "E1924", {"start": v(34.53, -94.24) * mm, "end": v(34.54, -94.08) * mm});
            skLineSegment(sketch, "E1925", {"start": v(34.54, -94.08) * mm, "end": v(34.54, -93.91) * mm});
            skLineSegment(sketch, "E1926", {"start": v(34.54, -93.91) * mm, "end": v(34.55, -93.75) * mm});
            skLineSegment(sketch, "E1927", {"start": v(34.55, -93.75) * mm, "end": v(34.55, -93.59) * mm});
            skLineSegment(sketch, "E1928", {"start": v(34.55, -93.59) * mm, "end": v(34.55, -93.43) * mm});
            skLineSegment(sketch, "E1929", {"start": v(34.55, -93.43) * mm, "end": v(34.56, -93.27) * mm});
            skLineSegment(sketch, "E1930", {"start": v(34.56, -93.27) * mm, "end": v(34.56, -93.11) * mm});
            skLineSegment(sketch, "E1931", {"start": v(34.56, -93.11) * mm, "end": v(34.56, -92.96) * mm});
            skLineSegment(sketch, "E1932", {"start": v(34.56, -92.96) * mm, "end": v(34.56, -92.8) * mm});
            skLineSegment(sketch, "E1933", {"start": v(34.56, -92.8) * mm, "end": v(34.56, -92.65) * mm});
            skLineSegment(sketch, "E1934", {"start": v(34.56, -92.65) * mm, "end": v(34.56, -92.5) * mm});
            skLineSegment(sketch, "E1935", {"start": v(34.56, -92.5) * mm, "end": v(34.56, -92.36) * mm});
            skLineSegment(sketch, "E1936", {"start": v(34.56, -92.36) * mm, "end": v(34.56, -92.21) * mm});
            skLineSegment(sketch, "E1937", {"start": v(34.56, -92.21) * mm, "end": v(34.56, -92.07) * mm});
            skLineSegment(sketch, "E1938", {"start": v(34.56, -92.07) * mm, "end": v(34.55, -91.93) * mm});
            skLineSegment(sketch, "E1939", {"start": v(34.55, -91.93) * mm, "end": v(34.55, -91.79) * mm});
            skLineSegment(sketch, "E1940", {"start": v(34.55, -91.79) * mm, "end": v(34.54, -91.65) * mm});
            skLineSegment(sketch, "E1941", {"start": v(34.54, -91.65) * mm, "end": v(34.54, -91.51) * mm});
            skLineSegment(sketch, "E1942", {"start": v(34.54, -91.51) * mm, "end": v(34.53, -91.38) * mm});
            skLineSegment(sketch, "E1943", {"start": v(34.53, -91.38) * mm, "end": v(34.53, -91.24) * mm});
            skLineSegment(sketch, "E1944", {"start": v(34.53, -91.24) * mm, "end": v(34.52, -91.11) * mm});
            skLineSegment(sketch, "E1945", {"start": v(34.52, -91.11) * mm, "end": v(34.52, -90.98) * mm});
            skLineSegment(sketch, "E1946", {"start": v(34.52, -90.98) * mm, "end": v(34.5, -90.85) * mm});
            skLineSegment(sketch, "E1947", {"start": v(34.5, -90.85) * mm, "end": v(35.37, -90.46) * mm});
            skLineSegment(sketch, "E1948", {"start": v(35.37, -90.46) * mm, "end": v(36.27, -90.17) * mm});
            skLineSegment(sketch, "E1949", {"start": v(36.27, -90.17) * mm, "end": v(36.35, -90.27) * mm});
            skLineSegment(sketch, "E1950", {"start": v(36.35, -90.27) * mm, "end": v(36.43, -90.36) * mm});
            skLineSegment(sketch, "E1951", {"start": v(36.43, -90.36) * mm, "end": v(36.51, -90.47) * mm});
            skLineSegment(sketch, "E1952", {"start": v(36.51, -90.47) * mm, "end": v(36.6, -90.57) * mm});
            skLineSegment(sketch, "E1953", {"start": v(36.6, -90.57) * mm, "end": v(36.69, -90.67) * mm});
            skLineSegment(sketch, "E1954", {"start": v(36.69, -90.67) * mm, "end": v(36.78, -90.77) * mm});
            skLineSegment(sketch, "E1955", {"start": v(36.78, -90.77) * mm, "end": v(36.87, -90.88) * mm});
            skLineSegment(sketch, "E1956", {"start": v(36.87, -90.88) * mm, "end": v(36.96, -90.98) * mm});
            skLineSegment(sketch, "E1957", {"start": v(36.96, -90.98) * mm, "end": v(37.05, -91.1) * mm});
            skLineSegment(sketch, "E1958", {"start": v(37.05, -91.1) * mm, "end": v(37.15, -91.2) * mm});
            skLineSegment(sketch, "E1959", {"start": v(37.15, -91.2) * mm, "end": v(37.25, -91.3) * mm});
            skLineSegment(sketch, "E1960", {"start": v(37.25, -91.3) * mm, "end": v(37.35, -91.42) * mm});
            skLineSegment(sketch, "E1961", {"start": v(37.35, -91.42) * mm, "end": v(37.45, -91.53) * mm});
            skLineSegment(sketch, "E1962", {"start": v(37.45, -91.53) * mm, "end": v(37.55, -91.64) * mm});
            skLineSegment(sketch, "E1963", {"start": v(37.55, -91.64) * mm, "end": v(37.65, -91.75) * mm});
            skLineSegment(sketch, "E1964", {"start": v(37.65, -91.75) * mm, "end": v(37.76, -91.86) * mm});
            skLineSegment(sketch, "E1965", {"start": v(37.76, -91.86) * mm, "end": v(37.87, -91.97) * mm});
            skLineSegment(sketch, "E1966", {"start": v(37.87, -91.97) * mm, "end": v(37.98, -92.09) * mm});
            skLineSegment(sketch, "E1967", {"start": v(37.98, -92.09) * mm, "end": v(38.09, -92.2) * mm});
            skLineSegment(sketch, "E1968", {"start": v(38.09, -92.2) * mm, "end": v(38.2, -92.32) * mm});
            skLineSegment(sketch, "E1969", {"start": v(38.2, -92.32) * mm, "end": v(38.31, -92.44) * mm});
            skLineSegment(sketch, "E1970", {"start": v(38.31, -92.44) * mm, "end": v(38.43, -92.55) * mm});
            skLineSegment(sketch, "E1971", {"start": v(38.43, -92.55) * mm, "end": v(38.55, -92.67) * mm});
            skLineSegment(sketch, "E1972", {"start": v(38.55, -92.67) * mm, "end": v(38.67, -92.79) * mm});
            skLineSegment(sketch, "E1973", {"start": v(38.67, -92.79) * mm, "end": v(38.79, -92.9) * mm});
            skLineSegment(sketch, "E1974", {"start": v(38.79, -92.9) * mm, "end": v(38.91, -93.03) * mm});
            skLineSegment(sketch, "E1975", {"start": v(38.91, -93.03) * mm, "end": v(39.04, -93.15) * mm});
            skLineSegment(sketch, "E1976", {"start": v(39.04, -93.15) * mm, "end": v(39.16, -93.27) * mm});
            skLineSegment(sketch, "E1977", {"start": v(39.16, -93.27) * mm, "end": v(39.3, -93.4) * mm});
            skLineSegment(sketch, "E1978", {"start": v(39.3, -93.4) * mm, "end": v(39.42, -93.52) * mm});
            skLineSegment(sketch, "E1979", {"start": v(39.42, -93.52) * mm, "end": v(39.56, -93.64) * mm});
            skLineSegment(sketch, "E1980", {"start": v(39.56, -93.64) * mm, "end": v(39.7, -93.76) * mm});
            skLineSegment(sketch, "E1981", {"start": v(39.7, -93.76) * mm, "end": v(39.83, -93.89) * mm});
            skLineSegment(sketch, "E1982", {"start": v(39.83, -93.89) * mm, "end": v(39.96, -94.01) * mm});
            skLineSegment(sketch, "E1983", {"start": v(39.96, -94.01) * mm, "end": v(40.1, -94.14) * mm});
            skLineSegment(sketch, "E1984", {"start": v(40.1, -94.14) * mm, "end": v(40.25, -94.27) * mm});
            skLineSegment(sketch, "E1985", {"start": v(40.25, -94.27) * mm, "end": v(40.32, -94.24) * mm});
            skLineSegment(sketch, "E1986", {"start": v(40.32, -94.24) * mm, "end": v(41.76, -93.6) * mm});
            skLineSegment(sketch, "E1987", {"start": v(41.76, -93.6) * mm, "end": v(41.83, -93.57) * mm});
            skLineSegment(sketch, "E1988", {"start": v(41.83, -93.57) * mm, "end": v(41.84, -93.38) * mm});
            skLineSegment(sketch, "E1989", {"start": v(41.84, -93.38) * mm, "end": v(41.84, -93.2) * mm});
            skLineSegment(sketch, "E1990", {"start": v(41.84, -93.2) * mm, "end": v(41.84, -93) * mm});
            skLineSegment(sketch, "E1991", {"start": v(41.84, -93) * mm, "end": v(41.84, -92.82) * mm});
            skLineSegment(sketch, "E1992", {"start": v(41.84, -92.82) * mm, "end": v(41.84, -92.64) * mm});
            skLineSegment(sketch, "E1993", {"start": v(41.84, -92.64) * mm, "end": v(41.84, -92.46) * mm});
            skLineSegment(sketch, "E1994", {"start": v(41.84, -92.46) * mm, "end": v(41.84, -92.28) * mm});
            skLineSegment(sketch, "E1995", {"start": v(41.84, -92.28) * mm, "end": v(41.84, -92.1) * mm});
            skLineSegment(sketch, "E1996", {"start": v(41.84, -92.1) * mm, "end": v(41.84, -91.93) * mm});
            skLineSegment(sketch, "E1997", {"start": v(41.84, -91.93) * mm, "end": v(41.83, -91.75) * mm});
            skLineSegment(sketch, "E1998", {"start": v(41.83, -91.75) * mm, "end": v(41.83, -91.58) * mm});
            skLineSegment(sketch, "E1999", {"start": v(41.83, -91.58) * mm, "end": v(41.82, -91.41) * mm});
            skLineSegment(sketch, "E2000", {"start": v(41.82, -91.41) * mm, "end": v(41.82, -91.24) * mm});
            skLineSegment(sketch, "E2001", {"start": v(41.82, -91.24) * mm, "end": v(41.81, -91.08) * mm});
            skLineSegment(sketch, "E2002", {"start": v(41.81, -91.08) * mm, "end": v(41.8, -90.91) * mm});
            skLineSegment(sketch, "E2003", {"start": v(41.8, -90.91) * mm, "end": v(41.8, -90.75) * mm});
            skLineSegment(sketch, "E2004", {"start": v(41.8, -90.75) * mm, "end": v(41.79, -90.59) * mm});
            skLineSegment(sketch, "E2005", {"start": v(41.79, -90.59) * mm, "end": v(41.78, -90.43) * mm});
            skLineSegment(sketch, "E2006", {"start": v(41.78, -90.43) * mm, "end": v(41.77, -90.27) * mm});
            skLineSegment(sketch, "E2007", {"start": v(41.77, -90.27) * mm, "end": v(41.76, -90.11) * mm});
            skLineSegment(sketch, "E2008", {"start": v(41.76, -90.11) * mm, "end": v(41.75, -89.96) * mm});
            skLineSegment(sketch, "E2009", {"start": v(41.75, -89.96) * mm, "end": v(41.74, -89.8) * mm});
            skLineSegment(sketch, "E2010", {"start": v(41.74, -89.8) * mm, "end": v(41.72, -89.66) * mm});
            skLineSegment(sketch, "E2011", {"start": v(41.72, -89.66) * mm, "end": v(41.71, -89.5) * mm});
            skLineSegment(sketch, "E2012", {"start": v(41.71, -89.5) * mm, "end": v(41.7, -89.36) * mm});
            skLineSegment(sketch, "E2013", {"start": v(41.7, -89.36) * mm, "end": v(41.69, -89.22) * mm});
            skLineSegment(sketch, "E2014", {"start": v(41.69, -89.22) * mm, "end": v(41.67, -89.07) * mm});
            skLineSegment(sketch, "E2015", {"start": v(41.67, -89.07) * mm, "end": v(41.66, -88.93) * mm});
            skLineSegment(sketch, "E2016", {"start": v(41.66, -88.93) * mm, "end": v(41.64, -88.8) * mm});
            skLineSegment(sketch, "E2017", {"start": v(41.64, -88.8) * mm, "end": v(41.63, -88.65) * mm});
            skLineSegment(sketch, "E2018", {"start": v(41.63, -88.65) * mm, "end": v(41.61, -88.52) * mm});
            skLineSegment(sketch, "E2019", {"start": v(41.61, -88.52) * mm, "end": v(41.6, -88.38) * mm});
            skLineSegment(sketch, "E2020", {"start": v(41.6, -88.38) * mm, "end": v(41.58, -88.25) * mm});
            skLineSegment(sketch, "E2021", {"start": v(41.58, -88.25) * mm, "end": v(41.56, -88.12) * mm});
            skLineSegment(sketch, "E2022", {"start": v(41.56, -88.12) * mm, "end": v(41.55, -88) * mm});
            skLineSegment(sketch, "E2023", {"start": v(41.55, -88) * mm, "end": v(41.53, -87.87) * mm});
            skLineSegment(sketch, "E2024", {"start": v(41.53, -87.87) * mm, "end": v(42.35, -87.4) * mm});
            skLineSegment(sketch, "E2025", {"start": v(42.35, -87.4) * mm, "end": v(43.23, -87.04) * mm});
            skLineSegment(sketch, "E2026", {"start": v(43.23, -87.04) * mm, "end": v(43.32, -87.14) * mm});
            skLineSegment(sketch, "E2027", {"start": v(43.32, -87.14) * mm, "end": v(43.4, -87.23) * mm});
            skLineSegment(sketch, "E2028", {"start": v(43.4, -87.23) * mm, "end": v(43.5, -87.32) * mm});
            skLineSegment(sketch, "E2029", {"start": v(43.5, -87.32) * mm, "end": v(43.6, -87.42) * mm});
            skLineSegment(sketch, "E2030", {"start": v(43.6, -87.42) * mm, "end": v(43.69, -87.51) * mm});
            skLineSegment(sketch, "E2031", {"start": v(43.69, -87.51) * mm, "end": v(43.79, -87.6) * mm});
            skLineSegment(sketch, "E2032", {"start": v(43.79, -87.6) * mm, "end": v(43.88, -87.7) * mm});
            skLineSegment(sketch, "E2033", {"start": v(43.88, -87.7) * mm, "end": v(43.99, -87.8) * mm});
            skLineSegment(sketch, "E2034", {"start": v(43.99, -87.8) * mm, "end": v(44.09, -87.9) * mm});
            skLineSegment(sketch, "E2035", {"start": v(44.09, -87.9) * mm, "end": v(44.2, -88) * mm});
            skLineSegment(sketch, "E2036", {"start": v(44.2, -88) * mm, "end": v(44.3, -88.1) * mm});
            skLineSegment(sketch, "E2037", {"start": v(44.3, -88.1) * mm, "end": v(44.4, -88.2) * mm});
            skLineSegment(sketch, "E2038", {"start": v(44.4, -88.2) * mm, "end": v(44.51, -88.3) * mm});
            skLineSegment(sketch, "E2039", {"start": v(44.51, -88.3) * mm, "end": v(44.62, -88.4) * mm});
            skLineSegment(sketch, "E2040", {"start": v(44.62, -88.4) * mm, "end": v(44.74, -88.51) * mm});
            skLineSegment(sketch, "E2041", {"start": v(44.74, -88.51) * mm, "end": v(44.85, -88.61) * mm});
            skLineSegment(sketch, "E2042", {"start": v(44.85, -88.61) * mm, "end": v(44.97, -88.72) * mm});
            skLineSegment(sketch, "E2043", {"start": v(44.97, -88.72) * mm, "end": v(45.08, -88.82) * mm});
            skLineSegment(sketch, "E2044", {"start": v(45.08, -88.82) * mm, "end": v(45.2, -88.93) * mm});
            skLineSegment(sketch, "E2045", {"start": v(45.2, -88.93) * mm, "end": v(45.33, -89.04) * mm});
            skLineSegment(sketch, "E2046", {"start": v(45.33, -89.04) * mm, "end": v(45.45, -89.14) * mm});
            skLineSegment(sketch, "E2047", {"start": v(45.45, -89.14) * mm, "end": v(45.57, -89.25) * mm});
            skLineSegment(sketch, "E2048", {"start": v(45.57, -89.25) * mm, "end": v(45.7, -89.36) * mm});
            skLineSegment(sketch, "E2049", {"start": v(45.7, -89.36) * mm, "end": v(45.83, -89.47) * mm});
            skLineSegment(sketch, "E2050", {"start": v(45.83, -89.47) * mm, "end": v(45.96, -89.58) * mm});
            skLineSegment(sketch, "E2051", {"start": v(45.96, -89.58) * mm, "end": v(46.1, -89.69) * mm});
            skLineSegment(sketch, "E2052", {"start": v(46.1, -89.69) * mm, "end": v(46.23, -89.8) * mm});
            skLineSegment(sketch, "E2053", {"start": v(46.23, -89.8) * mm, "end": v(46.36, -89.91) * mm});
            skLineSegment(sketch, "E2054", {"start": v(46.36, -89.91) * mm, "end": v(46.5, -90.02) * mm});
            skLineSegment(sketch, "E2055", {"start": v(46.5, -90.02) * mm, "end": v(46.64, -90.13) * mm});
            skLineSegment(sketch, "E2056", {"start": v(46.64, -90.13) * mm, "end": v(46.78, -90.25) * mm});
            skLineSegment(sketch, "E2057", {"start": v(46.78, -90.25) * mm, "end": v(46.92, -90.36) * mm});
            skLineSegment(sketch, "E2058", {"start": v(46.92, -90.36) * mm, "end": v(47.07, -90.47) * mm});
            skLineSegment(sketch, "E2059", {"start": v(47.07, -90.47) * mm, "end": v(47.22, -90.59) * mm});
            skLineSegment(sketch, "E2060", {"start": v(47.22, -90.59) * mm, "end": v(47.37, -90.7) * mm});
            skLineSegment(sketch, "E2061", {"start": v(47.37, -90.7) * mm, "end": v(47.52, -90.82) * mm});
            skLineSegment(sketch, "E2062", {"start": v(47.52, -90.82) * mm, "end": v(47.6, -90.78) * mm});
            skLineSegment(sketch, "E2063", {"start": v(47.6, -90.78) * mm, "end": v(48.98, -90.04) * mm});
            skLineSegment(sketch, "E2064", {"start": v(48.98, -90.04) * mm, "end": v(49.05, -90) * mm});
            skLineSegment(sketch, "E2065", {"start": v(49.05, -90) * mm, "end": v(49.04, -89.81) * mm});
            skLineSegment(sketch, "E2066", {"start": v(49.04, -89.81) * mm, "end": v(49.02, -89.62) * mm});
            skLineSegment(sketch, "E2067", {"start": v(49.02, -89.62) * mm, "end": v(49.01, -89.44) * mm});
            skLineSegment(sketch, "E2068", {"start": v(49.01, -89.44) * mm, "end": v(49, -89.25) * mm});
            skLineSegment(sketch, "E2069", {"start": v(49, -89.25) * mm, "end": v(48.98, -89.07) * mm});
            skLineSegment(sketch, "E2070", {"start": v(48.98, -89.07) * mm, "end": v(48.97, -88.9) * mm});
            skLineSegment(sketch, "E2071", {"start": v(48.97, -88.9) * mm, "end": v(48.95, -88.71) * mm});
            skLineSegment(sketch, "E2072", {"start": v(48.95, -88.71) * mm, "end": v(48.94, -88.54) * mm});
            skLineSegment(sketch, "E2073", {"start": v(48.94, -88.54) * mm, "end": v(48.92, -88.36) * mm});
            skLineSegment(sketch, "E2074", {"start": v(48.92, -88.36) * mm, "end": v(48.9, -88.19) * mm});
            skLineSegment(sketch, "E2075", {"start": v(48.9, -88.19) * mm, "end": v(48.88, -88.02) * mm});
            skLineSegment(sketch, "E2076", {"start": v(48.88, -88.02) * mm, "end": v(48.87, -87.85) * mm});
            skLineSegment(sketch, "E2077", {"start": v(48.87, -87.85) * mm, "end": v(48.85, -87.68) * mm});
            skLineSegment(sketch, "E2078", {"start": v(48.85, -87.68) * mm, "end": v(48.83, -87.51) * mm});
            skLineSegment(sketch, "E2079", {"start": v(48.83, -87.51) * mm, "end": v(48.8, -87.35) * mm});
            skLineSegment(sketch, "E2080", {"start": v(48.8, -87.35) * mm, "end": v(48.79, -87.19) * mm});
            skLineSegment(sketch, "E2081", {"start": v(48.79, -87.19) * mm, "end": v(48.77, -87.03) * mm});
            skLineSegment(sketch, "E2082", {"start": v(48.77, -87.03) * mm, "end": v(48.74, -86.87) * mm});
            skLineSegment(sketch, "E2083", {"start": v(48.74, -86.87) * mm, "end": v(48.72, -86.71) * mm});
            skLineSegment(sketch, "E2084", {"start": v(48.72, -86.71) * mm, "end": v(48.7, -86.56) * mm});
            skLineSegment(sketch, "E2085", {"start": v(48.7, -86.56) * mm, "end": v(48.68, -86.4) * mm});
            skLineSegment(sketch, "E2086", {"start": v(48.68, -86.4) * mm, "end": v(48.65, -86.26) * mm});
            skLineSegment(sketch, "E2087", {"start": v(48.65, -86.26) * mm, "end": v(48.63, -86.1) * mm});
            skLineSegment(sketch, "E2088", {"start": v(48.63, -86.1) * mm, "end": v(48.6, -85.96) * mm});
            skLineSegment(sketch, "E2089", {"start": v(48.6, -85.96) * mm, "end": v(48.58, -85.81) * mm});
            skLineSegment(sketch, "E2090", {"start": v(48.58, -85.81) * mm, "end": v(48.56, -85.67) * mm});
            skLineSegment(sketch, "E2091", {"start": v(48.56, -85.67) * mm, "end": v(48.53, -85.53) * mm});
            skLineSegment(sketch, "E2092", {"start": v(48.53, -85.53) * mm, "end": v(48.5, -85.39) * mm});
            skLineSegment(sketch, "E2093", {"start": v(48.5, -85.39) * mm, "end": v(48.48, -85.25) * mm});
            skLineSegment(sketch, "E2094", {"start": v(48.48, -85.25) * mm, "end": v(48.46, -85.11) * mm});
            skLineSegment(sketch, "E2095", {"start": v(48.46, -85.11) * mm, "end": v(48.43, -84.98) * mm});
            skLineSegment(sketch, "E2096", {"start": v(48.43, -84.98) * mm, "end": v(48.4, -84.85) * mm});
            skLineSegment(sketch, "E2097", {"start": v(48.4, -84.85) * mm, "end": v(48.38, -84.72) * mm});
            skLineSegment(sketch, "E2098", {"start": v(48.38, -84.72) * mm, "end": v(48.35, -84.59) * mm});
            skLineSegment(sketch, "E2099", {"start": v(48.35, -84.59) * mm, "end": v(48.32, -84.46) * mm});
            skLineSegment(sketch, "E2100", {"start": v(48.32, -84.46) * mm, "end": v(48.3, -84.34) * mm});
            skLineSegment(sketch, "E2101", {"start": v(48.3, -84.34) * mm, "end": v(49.08, -83.81) * mm});
            skLineSegment(sketch, "E2102", {"start": v(49.08, -83.81) * mm, "end": v(49.92, -83.38) * mm});
            skLineSegment(sketch, "E2103", {"start": v(49.92, -83.38) * mm, "end": v(50.02, -83.47) * mm});
            skLineSegment(sketch, "E2104", {"start": v(50.02, -83.47) * mm, "end": v(50.12, -83.55) * mm});
            skLineSegment(sketch, "E2105", {"start": v(50.12, -83.55) * mm, "end": v(50.22, -83.64) * mm});
            skLineSegment(sketch, "E2106", {"start": v(50.22, -83.64) * mm, "end": v(50.32, -83.73) * mm});
            skLineSegment(sketch, "E2107", {"start": v(50.32, -83.73) * mm, "end": v(50.42, -83.81) * mm});
            skLineSegment(sketch, "E2108", {"start": v(50.42, -83.81) * mm, "end": v(50.52, -83.9) * mm});
            skLineSegment(sketch, "E2109", {"start": v(50.52, -83.9) * mm, "end": v(50.63, -84) * mm});
            skLineSegment(sketch, "E2110", {"start": v(50.63, -84) * mm, "end": v(50.74, -84.08) * mm});
            skLineSegment(sketch, "E2111", {"start": v(50.74, -84.08) * mm, "end": v(50.85, -84.17) * mm});
            skLineSegment(sketch, "E2112", {"start": v(50.85, -84.17) * mm, "end": v(50.96, -84.26) * mm});
            skLineSegment(sketch, "E2113", {"start": v(50.96, -84.26) * mm, "end": v(51.07, -84.36) * mm});
            skLineSegment(sketch, "E2114", {"start": v(51.07, -84.36) * mm, "end": v(51.19, -84.45) * mm});
            skLineSegment(sketch, "E2115", {"start": v(51.19, -84.45) * mm, "end": v(51.3, -84.54) * mm});
            skLineSegment(sketch, "E2116", {"start": v(51.3, -84.54) * mm, "end": v(51.42, -84.63) * mm});
            skLineSegment(sketch, "E2117", {"start": v(51.42, -84.63) * mm, "end": v(51.54, -84.73) * mm});
            skLineSegment(sketch, "E2118", {"start": v(51.54, -84.73) * mm, "end": v(51.67, -84.82) * mm});
            skLineSegment(sketch, "E2119", {"start": v(51.67, -84.82) * mm, "end": v(51.79, -84.92) * mm});
            skLineSegment(sketch, "E2120", {"start": v(51.79, -84.92) * mm, "end": v(51.91, -85.01) * mm});
            skLineSegment(sketch, "E2121", {"start": v(51.91, -85.01) * mm, "end": v(52.04, -85.1) * mm});
            skLineSegment(sketch, "E2122", {"start": v(52.04, -85.1) * mm, "end": v(52.17, -85.2) * mm});
            skLineSegment(sketch, "E2123", {"start": v(52.17, -85.2) * mm, "end": v(52.3, -85.3) * mm});
            skLineSegment(sketch, "E2124", {"start": v(52.3, -85.3) * mm, "end": v(52.44, -85.4) * mm});
            skLineSegment(sketch, "E2125", {"start": v(52.44, -85.4) * mm, "end": v(52.57, -85.5) * mm});
            skLineSegment(sketch, "E2126", {"start": v(52.57, -85.5) * mm, "end": v(52.7, -85.6) * mm});
            skLineSegment(sketch, "E2127", {"start": v(52.7, -85.6) * mm, "end": v(52.85, -85.7) * mm});
            skLineSegment(sketch, "E2128", {"start": v(52.85, -85.7) * mm, "end": v(52.99, -85.8) * mm});
            skLineSegment(sketch, "E2129", {"start": v(52.99, -85.8) * mm, "end": v(53.13, -85.9) * mm});
            skLineSegment(sketch, "E2130", {"start": v(53.13, -85.9) * mm, "end": v(53.27, -86) * mm});
            skLineSegment(sketch, "E2131", {"start": v(53.27, -86) * mm, "end": v(53.42, -86.1) * mm});
            skLineSegment(sketch, "E2132", {"start": v(53.42, -86.1) * mm, "end": v(53.57, -86.2) * mm});
            skLineSegment(sketch, "E2133", {"start": v(53.57, -86.2) * mm, "end": v(53.72, -86.3) * mm});
            skLineSegment(sketch, "E2134", {"start": v(53.72, -86.3) * mm, "end": v(53.87, -86.4) * mm});
            skLineSegment(sketch, "E2135", {"start": v(53.87, -86.4) * mm, "end": v(54.02, -86.5) * mm});
            skLineSegment(sketch, "E2136", {"start": v(54.02, -86.5) * mm, "end": v(54.18, -86.6) * mm});
            skLineSegment(sketch, "E2137", {"start": v(54.18, -86.6) * mm, "end": v(54.34, -86.7) * mm});
            skLineSegment(sketch, "E2138", {"start": v(54.34, -86.7) * mm, "end": v(54.5, -86.8) * mm});
            skLineSegment(sketch, "E2139", {"start": v(54.5, -86.8) * mm, "end": v(54.57, -86.77) * mm});
            skLineSegment(sketch, "E2140", {"start": v(54.57, -86.77) * mm, "end": v(55.9, -85.92) * mm});
            skLineSegment(sketch, "E2141", {"start": v(55.9, -85.92) * mm, "end": v(55.96, -85.87) * mm});
            skLineSegment(sketch, "E2142", {"start": v(55.96, -85.87) * mm, "end": v(55.93, -85.69) * mm});
            skLineSegment(sketch, "E2143", {"start": v(55.93, -85.69) * mm, "end": v(55.9, -85.5) * mm});
            skLineSegment(sketch, "E2144", {"start": v(55.9, -85.5) * mm, "end": v(55.88, -85.32) * mm});
            skLineSegment(sketch, "E2145", {"start": v(55.88, -85.32) * mm, "end": v(55.85, -85.13) * mm});
            skLineSegment(sketch, "E2146", {"start": v(55.85, -85.13) * mm, "end": v(55.82, -84.95) * mm});
            skLineSegment(sketch, "E2147", {"start": v(55.82, -84.95) * mm, "end": v(55.8, -84.78) * mm});
            skLineSegment(sketch, "E2148", {"start": v(55.8, -84.78) * mm, "end": v(55.76, -84.6) * mm});
            skLineSegment(sketch, "E2149", {"start": v(55.76, -84.6) * mm, "end": v(55.73, -84.42) * mm});
            skLineSegment(sketch, "E2150", {"start": v(55.73, -84.42) * mm, "end": v(55.7, -84.25) * mm});
            skLineSegment(sketch, "E2151", {"start": v(55.7, -84.25) * mm, "end": v(55.67, -84.08) * mm});
            skLineSegment(sketch, "E2152", {"start": v(55.67, -84.08) * mm, "end": v(55.64, -83.91) * mm});
            skLineSegment(sketch, "E2153", {"start": v(55.64, -83.91) * mm, "end": v(55.6, -83.74) * mm});
            skLineSegment(sketch, "E2154", {"start": v(55.6, -83.74) * mm, "end": v(55.58, -83.58) * mm});
            skLineSegment(sketch, "E2155", {"start": v(55.58, -83.58) * mm, "end": v(55.54, -83.41) * mm});
            skLineSegment(sketch, "E2156", {"start": v(55.54, -83.41) * mm, "end": v(55.5, -83.25) * mm});
            skLineSegment(sketch, "E2157", {"start": v(55.5, -83.25) * mm, "end": v(55.48, -83.1) * mm});
            skLineSegment(sketch, "E2158", {"start": v(55.48, -83.1) * mm, "end": v(55.44, -82.93) * mm});
            skLineSegment(sketch, "E2159", {"start": v(55.44, -82.93) * mm, "end": v(55.4, -82.78) * mm});
            skLineSegment(sketch, "E2160", {"start": v(55.4, -82.78) * mm, "end": v(55.38, -82.62) * mm});
            skLineSegment(sketch, "E2161", {"start": v(55.38, -82.62) * mm, "end": v(55.34, -82.47) * mm});
            skLineSegment(sketch, "E2162", {"start": v(55.34, -82.47) * mm, "end": v(55.3, -82.32) * mm});
            skLineSegment(sketch, "E2163", {"start": v(55.3, -82.32) * mm, "end": v(55.27, -82.17) * mm});
            skLineSegment(sketch, "E2164", {"start": v(55.27, -82.17) * mm, "end": v(55.24, -82.03) * mm});
            skLineSegment(sketch, "E2165", {"start": v(55.24, -82.03) * mm, "end": v(55.2, -81.88) * mm});
            skLineSegment(sketch, "E2166", {"start": v(55.2, -81.88) * mm, "end": v(55.16, -81.74) * mm});
            skLineSegment(sketch, "E2167", {"start": v(55.16, -81.74) * mm, "end": v(55.13, -81.6) * mm});
            skLineSegment(sketch, "E2168", {"start": v(55.13, -81.6) * mm, "end": v(55.1, -81.46) * mm});
            skLineSegment(sketch, "E2169", {"start": v(55.1, -81.46) * mm, "end": v(55.06, -81.32) * mm});
            skLineSegment(sketch, "E2170", {"start": v(55.06, -81.32) * mm, "end": v(55.02, -81.18) * mm});
            skLineSegment(sketch, "E2171", {"start": v(55.02, -81.18) * mm, "end": v(54.98, -81.05) * mm});
            skLineSegment(sketch, "E2172", {"start": v(54.98, -81.05) * mm, "end": v(54.95, -80.92) * mm});
            skLineSegment(sketch, "E2173", {"start": v(54.95, -80.92) * mm, "end": v(54.91, -80.79) * mm});
            skLineSegment(sketch, "E2174", {"start": v(54.91, -80.79) * mm, "end": v(54.87, -80.66) * mm});
            skLineSegment(sketch, "E2175", {"start": v(54.87, -80.66) * mm, "end": v(54.84, -80.53) * mm});
            skLineSegment(sketch, "E2176", {"start": v(54.84, -80.53) * mm, "end": v(54.8, -80.4) * mm});
            skLineSegment(sketch, "E2177", {"start": v(54.8, -80.4) * mm, "end": v(54.76, -80.29) * mm});
            skLineSegment(sketch, "E2178", {"start": v(54.76, -80.29) * mm, "end": v(55.5, -79.7) * mm});
            skLineSegment(sketch, "E2179", {"start": v(55.5, -79.7) * mm, "end": v(56.31, -79.2) * mm});
            skLineSegment(sketch, "E2180", {"start": v(56.31, -79.2) * mm, "end": v(56.41, -79.29) * mm});
            skLineSegment(sketch, "E2181", {"start": v(56.41, -79.29) * mm, "end": v(56.52, -79.36) * mm});
            skLineSegment(sketch, "E2182", {"start": v(56.52, -79.36) * mm, "end": v(56.62, -79.44) * mm});
            skLineSegment(sketch, "E2183", {"start": v(56.62, -79.44) * mm, "end": v(56.73, -79.52) * mm});
            skLineSegment(sketch, "E2184", {"start": v(56.73, -79.52) * mm, "end": v(56.84, -79.6) * mm});
            skLineSegment(sketch, "E2185", {"start": v(56.84, -79.6) * mm, "end": v(56.95, -79.68) * mm});
            skLineSegment(sketch, "E2186", {"start": v(56.95, -79.68) * mm, "end": v(57.06, -79.76) * mm});
            skLineSegment(sketch, "E2187", {"start": v(57.06, -79.76) * mm, "end": v(57.18, -79.84) * mm});
            skLineSegment(sketch, "E2188", {"start": v(57.18, -79.84) * mm, "end": v(57.3, -79.92) * mm});
            skLineSegment(sketch, "E2189", {"start": v(57.3, -79.92) * mm, "end": v(57.41, -80) * mm});
            skLineSegment(sketch, "E2190", {"start": v(57.41, -80) * mm, "end": v(57.53, -80.09) * mm});
            skLineSegment(sketch, "E2191", {"start": v(57.53, -80.09) * mm, "end": v(57.66, -80.17) * mm});
            skLineSegment(sketch, "E2192", {"start": v(57.66, -80.17) * mm, "end": v(57.78, -80.25) * mm});
            skLineSegment(sketch, "E2193", {"start": v(57.78, -80.25) * mm, "end": v(57.9, -80.34) * mm});
            skLineSegment(sketch, "E2194", {"start": v(57.9, -80.34) * mm, "end": v(58.03, -80.42) * mm});
            skLineSegment(sketch, "E2195", {"start": v(58.03, -80.42) * mm, "end": v(58.16, -80.5) * mm});
            skLineSegment(sketch, "E2196", {"start": v(58.16, -80.5) * mm, "end": v(58.3, -80.6) * mm});
            skLineSegment(sketch, "E2197", {"start": v(58.3, -80.6) * mm, "end": v(58.42, -80.68) * mm});
            skLineSegment(sketch, "E2198", {"start": v(58.42, -80.68) * mm, "end": v(58.56, -80.76) * mm});
            skLineSegment(sketch, "E2199", {"start": v(58.56, -80.76) * mm, "end": v(58.7, -80.85) * mm});
            skLineSegment(sketch, "E2200", {"start": v(58.7, -80.85) * mm, "end": v(58.83, -80.94) * mm});
            skLineSegment(sketch, "E2201", {"start": v(58.83, -80.94) * mm, "end": v(58.97, -81.02) * mm});
            skLineSegment(sketch, "E2202", {"start": v(58.97, -81.02) * mm, "end": v(59.12, -81.11) * mm});
            skLineSegment(sketch, "E2203", {"start": v(59.12, -81.11) * mm, "end": v(59.26, -81.2) * mm});
            skLineSegment(sketch, "E2204", {"start": v(59.26, -81.2) * mm, "end": v(59.4, -81.29) * mm});
            skLineSegment(sketch, "E2205", {"start": v(59.4, -81.29) * mm, "end": v(59.56, -81.37) * mm});
            skLineSegment(sketch, "E2206", {"start": v(59.56, -81.37) * mm, "end": v(59.7, -81.46) * mm});
            skLineSegment(sketch, "E2207", {"start": v(59.7, -81.46) * mm, "end": v(59.86, -81.55) * mm});
            skLineSegment(sketch, "E2208", {"start": v(59.86, -81.55) * mm, "end": v(60.01, -81.64) * mm});
            skLineSegment(sketch, "E2209", {"start": v(60.01, -81.64) * mm, "end": v(60.17, -81.73) * mm});
            skLineSegment(sketch, "E2210", {"start": v(60.17, -81.73) * mm, "end": v(60.32, -81.82) * mm});
            skLineSegment(sketch, "E2211", {"start": v(60.32, -81.82) * mm, "end": v(60.48, -81.9) * mm});
            skLineSegment(sketch, "E2212", {"start": v(60.48, -81.9) * mm, "end": v(60.64, -82) * mm});
            skLineSegment(sketch, "E2213", {"start": v(60.64, -82) * mm, "end": v(60.8, -82.09) * mm});
            skLineSegment(sketch, "E2214", {"start": v(60.8, -82.09) * mm, "end": v(60.97, -82.18) * mm});
            skLineSegment(sketch, "E2215", {"start": v(60.97, -82.18) * mm, "end": v(61.14, -82.27) * mm});
            skLineSegment(sketch, "E2216", {"start": v(61.14, -82.27) * mm, "end": v(61.2, -82.22) * mm});
            skLineSegment(sketch, "E2217", {"start": v(61.2, -82.22) * mm, "end": v(62.46, -81.27) * mm});
            skLineSegment(sketch, "E2218", {"start": v(62.46, -81.27) * mm, "end": v(62.52, -81.22) * mm});
            skLineSegment(sketch, "E2219", {"start": v(62.52, -81.22) * mm, "end": v(62.48, -81.03) * mm});
            skLineSegment(sketch, "E2220", {"start": v(62.48, -81.03) * mm, "end": v(62.44, -80.85) * mm});
            skLineSegment(sketch, "E2221", {"start": v(62.44, -80.85) * mm, "end": v(62.4, -80.67) * mm});
            skLineSegment(sketch, "E2222", {"start": v(62.4, -80.67) * mm, "end": v(62.36, -80.5) * mm});
            skLineSegment(sketch, "E2223", {"start": v(62.36, -80.5) * mm, "end": v(62.31, -80.31) * mm});
            skLineSegment(sketch, "E2224", {"start": v(62.31, -80.31) * mm, "end": v(62.27, -80.14) * mm});
            skLineSegment(sketch, "E2225", {"start": v(62.27, -80.14) * mm, "end": v(62.23, -79.96) * mm});
            skLineSegment(sketch, "E2226", {"start": v(62.23, -79.96) * mm, "end": v(62.18, -79.8) * mm});
            skLineSegment(sketch, "E2227", {"start": v(62.18, -79.8) * mm, "end": v(62.14, -79.62) * mm});
            skLineSegment(sketch, "E2228", {"start": v(62.14, -79.62) * mm, "end": v(62.1, -79.45) * mm});
            skLineSegment(sketch, "E2229", {"start": v(62.1, -79.45) * mm, "end": v(62.05, -79.29) * mm});
            skLineSegment(sketch, "E2230", {"start": v(62.05, -79.29) * mm, "end": v(62, -79.12) * mm});
            skLineSegment(sketch, "E2231", {"start": v(62, -79.12) * mm, "end": v(61.96, -78.96) * mm});
            skLineSegment(sketch, "E2232", {"start": v(61.96, -78.96) * mm, "end": v(61.92, -78.8) * mm});
            skLineSegment(sketch, "E2233", {"start": v(61.92, -78.8) * mm, "end": v(61.87, -78.64) * mm});
            skLineSegment(sketch, "E2234", {"start": v(61.87, -78.64) * mm, "end": v(61.83, -78.48) * mm});
            skLineSegment(sketch, "E2235", {"start": v(61.83, -78.48) * mm, "end": v(61.78, -78.33) * mm});
            skLineSegment(sketch, "E2236", {"start": v(61.78, -78.33) * mm, "end": v(61.73, -78.18) * mm});
            skLineSegment(sketch, "E2237", {"start": v(61.73, -78.18) * mm, "end": v(61.69, -78.02) * mm});
            skLineSegment(sketch, "E2238", {"start": v(61.69, -78.02) * mm, "end": v(61.64, -77.88) * mm});
            skLineSegment(sketch, "E2239", {"start": v(61.64, -77.88) * mm, "end": v(61.6, -77.73) * mm});
            skLineSegment(sketch, "E2240", {"start": v(61.6, -77.73) * mm, "end": v(61.55, -77.58) * mm});
            skLineSegment(sketch, "E2241", {"start": v(61.55, -77.58) * mm, "end": v(61.5, -77.44) * mm});
            skLineSegment(sketch, "E2242", {"start": v(61.5, -77.44) * mm, "end": v(61.45, -77.3) * mm});
            skLineSegment(sketch, "E2243", {"start": v(61.45, -77.3) * mm, "end": v(61.4, -77.16) * mm});
            skLineSegment(sketch, "E2244", {"start": v(61.4, -77.16) * mm, "end": v(61.36, -77.02) * mm});
            skLineSegment(sketch, "E2245", {"start": v(61.36, -77.02) * mm, "end": v(61.31, -76.88) * mm});
            skLineSegment(sketch, "E2246", {"start": v(61.31, -76.88) * mm, "end": v(61.27, -76.75) * mm});
            skLineSegment(sketch, "E2247", {"start": v(61.27, -76.75) * mm, "end": v(61.22, -76.62) * mm});
            skLineSegment(sketch, "E2248", {"start": v(61.22, -76.62) * mm, "end": v(61.17, -76.49) * mm});
            skLineSegment(sketch, "E2249", {"start": v(61.17, -76.49) * mm, "end": v(61.13, -76.36) * mm});
            skLineSegment(sketch, "E2250", {"start": v(61.13, -76.36) * mm, "end": v(61.08, -76.23) * mm});
            skLineSegment(sketch, "E2251", {"start": v(61.08, -76.23) * mm, "end": v(61.03, -76.1) * mm});
            skLineSegment(sketch, "E2252", {"start": v(61.03, -76.1) * mm, "end": v(60.99, -75.98) * mm});
            skLineSegment(sketch, "E2253", {"start": v(60.99, -75.98) * mm, "end": v(60.94, -75.86) * mm});
            skLineSegment(sketch, "E2254", {"start": v(60.94, -75.86) * mm, "end": v(60.9, -75.74) * mm});
            skLineSegment(sketch, "E2255", {"start": v(60.9, -75.74) * mm, "end": v(61.59, -75.1) * mm});
            skLineSegment(sketch, "E2256", {"start": v(61.59, -75.1) * mm, "end": v(62.35, -74.55) * mm});
            skLineSegment(sketch, "E2257", {"start": v(62.35, -74.55) * mm, "end": v(62.46, -74.62) * mm});
            skLineSegment(sketch, "E2258", {"start": v(62.46, -74.62) * mm, "end": v(62.57, -74.68) * mm});
            skLineSegment(sketch, "E2259", {"start": v(62.57, -74.68) * mm, "end": v(62.68, -74.75) * mm});
            skLineSegment(sketch, "E2260", {"start": v(62.68, -74.75) * mm, "end": v(62.8, -74.82) * mm});
            skLineSegment(sketch, "E2261", {"start": v(62.8, -74.82) * mm, "end": v(62.91, -74.9) * mm});
            skLineSegment(sketch, "E2262", {"start": v(62.91, -74.9) * mm, "end": v(63.03, -74.97) * mm});
            skLineSegment(sketch, "E2263", {"start": v(63.03, -74.97) * mm, "end": v(63.15, -75.04) * mm});
            skLineSegment(sketch, "E2264", {"start": v(63.15, -75.04) * mm, "end": v(63.27, -75.1) * mm});
            skLineSegment(sketch, "E2265", {"start": v(63.27, -75.1) * mm, "end": v(63.39, -75.18) * mm});
            skLineSegment(sketch, "E2266", {"start": v(63.39, -75.18) * mm, "end": v(63.51, -75.25) * mm});
            skLineSegment(sketch, "E2267", {"start": v(63.51, -75.25) * mm, "end": v(63.64, -75.33) * mm});
            skLineSegment(sketch, "E2268", {"start": v(63.64, -75.33) * mm, "end": v(63.77, -75.4) * mm});
            skLineSegment(sketch, "E2269", {"start": v(63.77, -75.4) * mm, "end": v(63.9, -75.47) * mm});
            skLineSegment(sketch, "E2270", {"start": v(63.9, -75.47) * mm, "end": v(64.03, -75.55) * mm});
            skLineSegment(sketch, "E2271", {"start": v(64.03, -75.55) * mm, "end": v(64.16, -75.62) * mm});
            skLineSegment(sketch, "E2272", {"start": v(64.16, -75.62) * mm, "end": v(64.3, -75.7) * mm});
            skLineSegment(sketch, "E2273", {"start": v(64.3, -75.7) * mm, "end": v(64.44, -75.77) * mm});
            skLineSegment(sketch, "E2274", {"start": v(64.44, -75.77) * mm, "end": v(64.57, -75.85) * mm});
            skLineSegment(sketch, "E2275", {"start": v(64.57, -75.85) * mm, "end": v(64.72, -75.92) * mm});
            skLineSegment(sketch, "E2276", {"start": v(64.72, -75.92) * mm, "end": v(64.86, -76) * mm});
            skLineSegment(sketch, "E2277", {"start": v(64.86, -76) * mm, "end": v(65, -76.07) * mm});
            skLineSegment(sketch, "E2278", {"start": v(65, -76.07) * mm, "end": v(65.15, -76.15) * mm});
            skLineSegment(sketch, "E2279", {"start": v(65.15, -76.15) * mm, "end": v(65.3, -76.22) * mm});
            skLineSegment(sketch, "E2280", {"start": v(65.3, -76.22) * mm, "end": v(65.45, -76.3) * mm});
            skLineSegment(sketch, "E2281", {"start": v(65.45, -76.3) * mm, "end": v(65.6, -76.37) * mm});
            skLineSegment(sketch, "E2282", {"start": v(65.6, -76.37) * mm, "end": v(65.76, -76.45) * mm});
            skLineSegment(sketch, "E2283", {"start": v(65.76, -76.45) * mm, "end": v(65.91, -76.53) * mm});
            skLineSegment(sketch, "E2284", {"start": v(65.91, -76.53) * mm, "end": v(66.07, -76.6) * mm});
            skLineSegment(sketch, "E2285", {"start": v(66.07, -76.6) * mm, "end": v(66.23, -76.68) * mm});
            skLineSegment(sketch, "E2286", {"start": v(66.23, -76.68) * mm, "end": v(66.4, -76.76) * mm});
            skLineSegment(sketch, "E2287", {"start": v(66.4, -76.76) * mm, "end": v(66.56, -76.83) * mm});
            skLineSegment(sketch, "E2288", {"start": v(66.56, -76.83) * mm, "end": v(66.72, -76.9) * mm});
            skLineSegment(sketch, "E2289", {"start": v(66.72, -76.9) * mm, "end": v(66.9, -76.99) * mm});
            skLineSegment(sketch, "E2290", {"start": v(66.9, -76.99) * mm, "end": v(67.06, -77.06) * mm});
            skLineSegment(sketch, "E2291", {"start": v(67.06, -77.06) * mm, "end": v(67.23, -77.14) * mm});
            skLineSegment(sketch, "E2292", {"start": v(67.23, -77.14) * mm, "end": v(67.4, -77.22) * mm});
            skLineSegment(sketch, "E2293", {"start": v(67.4, -77.22) * mm, "end": v(67.47, -77.16) * mm});
            skLineSegment(sketch, "E2294", {"start": v(67.47, -77.16) * mm, "end": v(68.64, -76.12) * mm});
            skLineSegment(sketch, "E2295", {"start": v(68.64, -76.12) * mm, "end": v(68.7, -76.06) * mm});
            skLineSegment(sketch, "E2296", {"start": v(68.7, -76.06) * mm, "end": v(68.65, -75.88) * mm});
            skLineSegment(sketch, "E2297", {"start": v(68.65, -75.88) * mm, "end": v(68.6, -75.7) * mm});
            skLineSegment(sketch, "E2298", {"start": v(68.6, -75.7) * mm, "end": v(68.54, -75.53) * mm});
            skLineSegment(sketch, "E2299", {"start": v(68.54, -75.53) * mm, "end": v(68.48, -75.35) * mm});
            skLineSegment(sketch, "E2300", {"start": v(68.48, -75.35) * mm, "end": v(68.42, -75.18) * mm});
            skLineSegment(sketch, "E2301", {"start": v(68.42, -75.18) * mm, "end": v(68.37, -75) * mm});
            skLineSegment(sketch, "E2302", {"start": v(68.37, -75) * mm, "end": v(68.3, -74.83) * mm});
            skLineSegment(sketch, "E2303", {"start": v(68.3, -74.83) * mm, "end": v(68.25, -74.67) * mm});
            skLineSegment(sketch, "E2304", {"start": v(68.25, -74.67) * mm, "end": v(68.2, -74.5) * mm});
            skLineSegment(sketch, "E2305", {"start": v(68.2, -74.5) * mm, "end": v(68.14, -74.34) * mm});
            skLineSegment(sketch, "E2306", {"start": v(68.14, -74.34) * mm, "end": v(68.08, -74.17) * mm});
            skLineSegment(sketch, "E2307", {"start": v(68.08, -74.17) * mm, "end": v(68.02, -74.01) * mm});
            skLineSegment(sketch, "E2308", {"start": v(68.02, -74.01) * mm, "end": v(67.97, -73.85) * mm});
            skLineSegment(sketch, "E2309", {"start": v(67.97, -73.85) * mm, "end": v(67.9, -73.7) * mm});
            skLineSegment(sketch, "E2310", {"start": v(67.9, -73.7) * mm, "end": v(67.85, -73.54) * mm});
            skLineSegment(sketch, "E2311", {"start": v(67.85, -73.54) * mm, "end": v(67.8, -73.4) * mm});
            skLineSegment(sketch, "E2312", {"start": v(67.8, -73.4) * mm, "end": v(67.73, -73.24) * mm});
            skLineSegment(sketch, "E2313", {"start": v(67.73, -73.24) * mm, "end": v(67.68, -73.1) * mm});
            skLineSegment(sketch, "E2314", {"start": v(67.68, -73.1) * mm, "end": v(67.62, -72.94) * mm});
            skLineSegment(sketch, "E2315", {"start": v(67.62, -72.94) * mm, "end": v(67.56, -72.8) * mm});
            skLineSegment(sketch, "E2316", {"start": v(67.56, -72.8) * mm, "end": v(67.5, -72.66) * mm});
            skLineSegment(sketch, "E2317", {"start": v(67.5, -72.66) * mm, "end": v(67.45, -72.51) * mm});
            skLineSegment(sketch, "E2318", {"start": v(67.45, -72.51) * mm, "end": v(67.39, -72.37) * mm});
            skLineSegment(sketch, "E2319", {"start": v(67.39, -72.37) * mm, "end": v(67.33, -72.24) * mm});
            skLineSegment(sketch, "E2320", {"start": v(67.33, -72.24) * mm, "end": v(67.27, -72.1) * mm});
            skLineSegment(sketch, "E2321", {"start": v(67.27, -72.1) * mm, "end": v(67.21, -71.97) * mm});
            skLineSegment(sketch, "E2322", {"start": v(67.21, -71.97) * mm, "end": v(67.16, -71.84) * mm});
            skLineSegment(sketch, "E2323", {"start": v(67.16, -71.84) * mm, "end": v(67.1, -71.7) * mm});
            skLineSegment(sketch, "E2324", {"start": v(67.1, -71.7) * mm, "end": v(67.04, -71.58) * mm});
            skLineSegment(sketch, "E2325", {"start": v(67.04, -71.58) * mm, "end": v(66.99, -71.45) * mm});
            skLineSegment(sketch, "E2326", {"start": v(66.99, -71.45) * mm, "end": v(66.93, -71.33) * mm});
            skLineSegment(sketch, "E2327", {"start": v(66.93, -71.33) * mm, "end": v(66.87, -71.2) * mm});
            skLineSegment(sketch, "E2328", {"start": v(66.87, -71.2) * mm, "end": v(66.82, -71.08) * mm});
            skLineSegment(sketch, "E2329", {"start": v(66.82, -71.08) * mm, "end": v(66.76, -70.96) * mm});
            skLineSegment(sketch, "E2330", {"start": v(66.76, -70.96) * mm, "end": v(66.7, -70.85) * mm});
            skLineSegment(sketch, "E2331", {"start": v(66.7, -70.85) * mm, "end": v(66.65, -70.73) * mm});
            skLineSegment(sketch, "E2332", {"start": v(66.65, -70.73) * mm, "end": v(67.3, -70.04) * mm});
            skLineSegment(sketch, "E2333", {"start": v(67.3, -70.04) * mm, "end": v(68.01, -69.42) * mm});
            skLineSegment(sketch, "E2334", {"start": v(68.01, -69.42) * mm, "end": v(68.12, -69.48) * mm});
            skLineSegment(sketch, "E2335", {"start": v(68.12, -69.48) * mm, "end": v(68.24, -69.55) * mm});
            skLineSegment(sketch, "E2336", {"start": v(68.24, -69.55) * mm, "end": v(68.35, -69.6) * mm});
            skLineSegment(sketch, "E2337", {"start": v(68.35, -69.6) * mm, "end": v(68.47, -69.67) * mm});
            skLineSegment(sketch, "E2338", {"start": v(68.47, -69.67) * mm, "end": v(68.6, -69.73) * mm});
            skLineSegment(sketch, "E2339", {"start": v(68.6, -69.73) * mm, "end": v(68.72, -69.8) * mm});
            skLineSegment(sketch, "E2340", {"start": v(68.72, -69.8) * mm, "end": v(68.84, -69.85) * mm});
            skLineSegment(sketch, "E2341", {"start": v(68.84, -69.85) * mm, "end": v(68.97, -69.91) * mm});
            skLineSegment(sketch, "E2342", {"start": v(68.97, -69.91) * mm, "end": v(69.1, -69.98) * mm});
            skLineSegment(sketch, "E2343", {"start": v(69.1, -69.98) * mm, "end": v(69.22, -70.04) * mm});
            skLineSegment(sketch, "E2344", {"start": v(69.22, -70.04) * mm, "end": v(69.35, -70.1) * mm});
            skLineSegment(sketch, "E2345", {"start": v(69.35, -70.1) * mm, "end": v(69.49, -70.16) * mm});
            skLineSegment(sketch, "E2346", {"start": v(69.49, -70.16) * mm, "end": v(69.62, -70.23) * mm});
            skLineSegment(sketch, "E2347", {"start": v(69.62, -70.23) * mm, "end": v(69.76, -70.3) * mm});
            skLineSegment(sketch, "E2348", {"start": v(69.76, -70.3) * mm, "end": v(69.9, -70.35) * mm});
            skLineSegment(sketch, "E2349", {"start": v(69.9, -70.35) * mm, "end": v(70.04, -70.42) * mm});
            skLineSegment(sketch, "E2350", {"start": v(70.04, -70.42) * mm, "end": v(70.18, -70.48) * mm});
            skLineSegment(sketch, "E2351", {"start": v(70.18, -70.48) * mm, "end": v(70.33, -70.55) * mm});
            skLineSegment(sketch, "E2352", {"start": v(70.33, -70.55) * mm, "end": v(70.47, -70.6) * mm});
            skLineSegment(sketch, "E2353", {"start": v(70.47, -70.6) * mm, "end": v(70.62, -70.67) * mm});
            skLineSegment(sketch, "E2354", {"start": v(70.62, -70.67) * mm, "end": v(70.77, -70.74) * mm});
            skLineSegment(sketch, "E2355", {"start": v(70.77, -70.74) * mm, "end": v(70.92, -70.8) * mm});
            skLineSegment(sketch, "E2356", {"start": v(70.92, -70.8) * mm, "end": v(71.08, -70.86) * mm});
            skLineSegment(sketch, "E2357", {"start": v(71.08, -70.86) * mm, "end": v(71.23, -70.93) * mm});
            skLineSegment(sketch, "E2358", {"start": v(71.23, -70.93) * mm, "end": v(71.4, -71) * mm});
            skLineSegment(sketch, "E2359", {"start": v(71.4, -71) * mm, "end": v(71.55, -71.06) * mm});
            skLineSegment(sketch, "E2360", {"start": v(71.55, -71.06) * mm, "end": v(71.71, -71.12) * mm});
            skLineSegment(sketch, "E2361", {"start": v(71.71, -71.12) * mm, "end": v(71.88, -71.18) * mm});
            skLineSegment(sketch, "E2362", {"start": v(71.88, -71.18) * mm, "end": v(72.04, -71.25) * mm});
            skLineSegment(sketch, "E2363", {"start": v(72.04, -71.25) * mm, "end": v(72.21, -71.31) * mm});
            skLineSegment(sketch, "E2364", {"start": v(72.21, -71.31) * mm, "end": v(72.38, -71.37) * mm});
            skLineSegment(sketch, "E2365", {"start": v(72.38, -71.37) * mm, "end": v(72.55, -71.44) * mm});
            skLineSegment(sketch, "E2366", {"start": v(72.55, -71.44) * mm, "end": v(72.72, -71.5) * mm});
            skLineSegment(sketch, "E2367", {"start": v(72.72, -71.5) * mm, "end": v(72.9, -71.56) * mm});
            skLineSegment(sketch, "E2368", {"start": v(72.9, -71.56) * mm, "end": v(73.08, -71.63) * mm});
            skLineSegment(sketch, "E2369", {"start": v(73.08, -71.63) * mm, "end": v(73.26, -71.69) * mm});
            skLineSegment(sketch, "E2370", {"start": v(73.26, -71.69) * mm, "end": v(73.31, -71.63) * mm});
            skLineSegment(sketch, "E2371", {"start": v(73.31, -71.63) * mm, "end": v(74.4, -70.5) * mm});
            skLineSegment(sketch, "E2372", {"start": v(74.4, -70.5) * mm, "end": v(74.46, -70.44) * mm});
            skLineSegment(sketch, "E2373", {"start": v(74.46, -70.44) * mm, "end": v(74.39, -70.26) * mm});
            skLineSegment(sketch, "E2374", {"start": v(74.39, -70.26) * mm, "end": v(74.32, -70.09) * mm});
            skLineSegment(sketch, "E2375", {"start": v(74.32, -70.09) * mm, "end": v(74.25, -69.92) * mm});
            skLineSegment(sketch, "E2376", {"start": v(74.25, -69.92) * mm, "end": v(74.18, -69.74) * mm});
            skLineSegment(sketch, "E2377", {"start": v(74.18, -69.74) * mm, "end": v(74.11, -69.58) * mm});
            skLineSegment(sketch, "E2378", {"start": v(74.11, -69.58) * mm, "end": v(74.04, -69.4) * mm});
            skLineSegment(sketch, "E2379", {"start": v(74.04, -69.4) * mm, "end": v(73.97, -69.24) * mm});
            skLineSegment(sketch, "E2380", {"start": v(73.97, -69.24) * mm, "end": v(73.9, -69.08) * mm});
            skLineSegment(sketch, "E2381", {"start": v(73.9, -69.08) * mm, "end": v(73.83, -68.92) * mm});
            skLineSegment(sketch, "E2382", {"start": v(73.83, -68.92) * mm, "end": v(73.76, -68.76) * mm});
            skLineSegment(sketch, "E2383", {"start": v(73.76, -68.76) * mm, "end": v(73.7, -68.6) * mm});
            skLineSegment(sketch, "E2384", {"start": v(73.7, -68.6) * mm, "end": v(73.62, -68.45) * mm});
            skLineSegment(sketch, "E2385", {"start": v(73.62, -68.45) * mm, "end": v(73.55, -68.3) * mm});
            skLineSegment(sketch, "E2386", {"start": v(73.55, -68.3) * mm, "end": v(73.48, -68.14) * mm});
            skLineSegment(sketch, "E2387", {"start": v(73.48, -68.14) * mm, "end": v(73.41, -68) * mm});
            skLineSegment(sketch, "E2388", {"start": v(73.41, -68) * mm, "end": v(73.34, -67.85) * mm});
            skLineSegment(sketch, "E2389", {"start": v(73.34, -67.85) * mm, "end": v(73.27, -67.7) * mm});
            skLineSegment(sketch, "E2390", {"start": v(73.27, -67.7) * mm, "end": v(73.2, -67.56) * mm});
            skLineSegment(sketch, "E2391", {"start": v(73.2, -67.56) * mm, "end": v(73.13, -67.41) * mm});
            skLineSegment(sketch, "E2392", {"start": v(73.13, -67.41) * mm, "end": v(73.06, -67.27) * mm});
            skLineSegment(sketch, "E2393", {"start": v(73.06, -67.27) * mm, "end": v(73, -67.14) * mm});
            skLineSegment(sketch, "E2394", {"start": v(73, -67.14) * mm, "end": v(72.93, -67) * mm});
            skLineSegment(sketch, "E2395", {"start": v(72.93, -67) * mm, "end": v(72.86, -66.86) * mm});
            skLineSegment(sketch, "E2396", {"start": v(72.86, -66.86) * mm, "end": v(72.8, -66.73) * mm});
            skLineSegment(sketch, "E2397", {"start": v(72.8, -66.73) * mm, "end": v(72.72, -66.6) * mm});
            skLineSegment(sketch, "E2398", {"start": v(72.72, -66.6) * mm, "end": v(72.65, -66.47) * mm});
            skLineSegment(sketch, "E2399", {"start": v(72.65, -66.47) * mm, "end": v(72.59, -66.35) * mm});
            skLineSegment(sketch, "E2400", {"start": v(72.59, -66.35) * mm, "end": v(72.52, -66.22) * mm});
            skLineSegment(sketch, "E2401", {"start": v(72.52, -66.22) * mm, "end": v(72.45, -66.1) * mm});
            skLineSegment(sketch, "E2402", {"start": v(72.45, -66.1) * mm, "end": v(72.39, -65.98) * mm});
            skLineSegment(sketch, "E2403", {"start": v(72.39, -65.98) * mm, "end": v(72.32, -65.86) * mm});
            skLineSegment(sketch, "E2404", {"start": v(72.32, -65.86) * mm, "end": v(72.25, -65.74) * mm});
            skLineSegment(sketch, "E2405", {"start": v(72.25, -65.74) * mm, "end": v(72.19, -65.62) * mm});
            skLineSegment(sketch, "E2406", {"start": v(72.19, -65.62) * mm, "end": v(72.12, -65.5) * mm});
            skLineSegment(sketch, "E2407", {"start": v(72.12, -65.5) * mm, "end": v(72.06, -65.4) * mm});
            skLineSegment(sketch, "E2408", {"start": v(72.06, -65.4) * mm, "end": v(72, -65.28) * mm});
            skLineSegment(sketch, "E2409", {"start": v(72, -65.28) * mm, "end": v(72.58, -64.54) * mm});
            skLineSegment(sketch, "E2410", {"start": v(72.58, -64.54) * mm, "end": v(73.25, -63.87) * mm});
            skLineSegment(sketch, "E2411", {"start": v(73.25, -63.87) * mm, "end": v(73.36, -63.93) * mm});
            skLineSegment(sketch, "E2412", {"start": v(73.36, -63.93) * mm, "end": v(73.48, -63.98) * mm});
            skLineSegment(sketch, "E2413", {"start": v(73.48, -63.98) * mm, "end": v(73.6, -64.03) * mm});
            skLineSegment(sketch, "E2414", {"start": v(73.6, -64.03) * mm, "end": v(73.73, -64.08) * mm});
            skLineSegment(sketch, "E2415", {"start": v(73.73, -64.08) * mm, "end": v(73.85, -64.13) * mm});
            skLineSegment(sketch, "E2416", {"start": v(73.85, -64.13) * mm, "end": v(73.98, -64.18) * mm});
            skLineSegment(sketch, "E2417", {"start": v(73.98, -64.18) * mm, "end": v(74.1, -64.24) * mm});
            skLineSegment(sketch, "E2418", {"start": v(74.1, -64.24) * mm, "end": v(74.24, -64.29) * mm});
            skLineSegment(sketch, "E2419", {"start": v(74.24, -64.29) * mm, "end": v(74.37, -64.34) * mm});
            skLineSegment(sketch, "E2420", {"start": v(74.37, -64.34) * mm, "end": v(74.5, -64.4) * mm});
            skLineSegment(sketch, "E2421", {"start": v(74.5, -64.4) * mm, "end": v(74.64, -64.44) * mm});
            skLineSegment(sketch, "E2422", {"start": v(74.64, -64.44) * mm, "end": v(74.78, -64.5) * mm});
            skLineSegment(sketch, "E2423", {"start": v(74.78, -64.5) * mm, "end": v(74.92, -64.55) * mm});
            skLineSegment(sketch, "E2424", {"start": v(74.92, -64.55) * mm, "end": v(75.06, -64.6) * mm});
            skLineSegment(sketch, "E2425", {"start": v(75.06, -64.6) * mm, "end": v(75.2, -64.65) * mm});
            skLineSegment(sketch, "E2426", {"start": v(75.2, -64.65) * mm, "end": v(75.35, -64.7) * mm});
            skLineSegment(sketch, "E2427", {"start": v(75.35, -64.7) * mm, "end": v(75.5, -64.76) * mm});
            skLineSegment(sketch, "E2428", {"start": v(75.5, -64.76) * mm, "end": v(75.64, -64.8) * mm});
            skLineSegment(sketch, "E2429", {"start": v(75.64, -64.8) * mm, "end": v(75.8, -64.86) * mm});
            skLineSegment(sketch, "E2430", {"start": v(75.8, -64.86) * mm, "end": v(75.95, -64.91) * mm});
            skLineSegment(sketch, "E2431", {"start": v(75.95, -64.91) * mm, "end": v(76.1, -64.97) * mm});
            skLineSegment(sketch, "E2432", {"start": v(76.1, -64.97) * mm, "end": v(76.26, -65.02) * mm});
            skLineSegment(sketch, "E2433", {"start": v(76.26, -65.02) * mm, "end": v(76.42, -65.07) * mm});
            skLineSegment(sketch, "E2434", {"start": v(76.42, -65.07) * mm, "end": v(76.58, -65.12) * mm});
            skLineSegment(sketch, "E2435", {"start": v(76.58, -65.12) * mm, "end": v(76.74, -65.17) * mm});
            skLineSegment(sketch, "E2436", {"start": v(76.74, -65.17) * mm, "end": v(76.9, -65.22) * mm});
            skLineSegment(sketch, "E2437", {"start": v(76.9, -65.22) * mm, "end": v(77.07, -65.27) * mm});
            skLineSegment(sketch, "E2438", {"start": v(77.07, -65.27) * mm, "end": v(77.24, -65.32) * mm});
            skLineSegment(sketch, "E2439", {"start": v(77.24, -65.32) * mm, "end": v(77.41, -65.38) * mm});
            skLineSegment(sketch, "E2440", {"start": v(77.41, -65.38) * mm, "end": v(77.58, -65.43) * mm});
            skLineSegment(sketch, "E2441", {"start": v(77.58, -65.43) * mm, "end": v(77.76, -65.48) * mm});
            skLineSegment(sketch, "E2442", {"start": v(77.76, -65.48) * mm, "end": v(77.93, -65.52) * mm});
            skLineSegment(sketch, "E2443", {"start": v(77.93, -65.52) * mm, "end": v(78.1, -65.57) * mm});
            skLineSegment(sketch, "E2444", {"start": v(78.1, -65.57) * mm, "end": v(78.29, -65.62) * mm});
            skLineSegment(sketch, "E2445", {"start": v(78.29, -65.62) * mm, "end": v(78.47, -65.67) * mm});
            skLineSegment(sketch, "E2446", {"start": v(78.47, -65.67) * mm, "end": v(78.65, -65.72) * mm});
            skLineSegment(sketch, "E2447", {"start": v(78.65, -65.72) * mm, "end": v(78.7, -65.66) * mm});
            skLineSegment(sketch, "E2448", {"start": v(78.7, -65.66) * mm, "end": v(79.7, -64.45) * mm});
            skLineSegment(sketch, "E2449", {"start": v(79.7, -64.45) * mm, "end": v(79.76, -64.38) * mm});
            skLineSegment(sketch, "E2450", {"start": v(79.76, -64.38) * mm, "end": v(79.67, -64.2) * mm});
            skLineSegment(sketch, "E2451", {"start": v(79.67, -64.2) * mm, "end": v(79.59, -64.04) * mm});
            skLineSegment(sketch, "E2452", {"start": v(79.59, -64.04) * mm, "end": v(79.5, -63.87) * mm});
            skLineSegment(sketch, "E2453", {"start": v(79.5, -63.87) * mm, "end": v(79.42, -63.7) * mm});
            skLineSegment(sketch, "E2454", {"start": v(79.42, -63.7) * mm, "end": v(79.34, -63.55) * mm});
            skLineSegment(sketch, "E2455", {"start": v(79.34, -63.55) * mm, "end": v(79.26, -63.39) * mm});
            skLineSegment(sketch, "E2456", {"start": v(79.26, -63.39) * mm, "end": v(79.17, -63.23) * mm});
            skLineSegment(sketch, "E2457", {"start": v(79.17, -63.23) * mm, "end": v(79.1, -63.07) * mm});
            skLineSegment(sketch, "E2458", {"start": v(79.1, -63.07) * mm, "end": v(79.01, -62.91) * mm});
            skLineSegment(sketch, "E2459", {"start": v(79.01, -62.91) * mm, "end": v(78.93, -62.76) * mm});
            skLineSegment(sketch, "E2460", {"start": v(78.93, -62.76) * mm, "end": v(78.85, -62.61) * mm});
            skLineSegment(sketch, "E2461", {"start": v(78.85, -62.61) * mm, "end": v(78.76, -62.46) * mm});
            skLineSegment(sketch, "E2462", {"start": v(78.76, -62.46) * mm, "end": v(78.68, -62.31) * mm});
            skLineSegment(sketch, "E2463", {"start": v(78.68, -62.31) * mm, "end": v(78.6, -62.17) * mm});
            skLineSegment(sketch, "E2464", {"start": v(78.6, -62.17) * mm, "end": v(78.52, -62.02) * mm});
            skLineSegment(sketch, "E2465", {"start": v(78.52, -62.02) * mm, "end": v(78.44, -61.88) * mm});
            skLineSegment(sketch, "E2466", {"start": v(78.44, -61.88) * mm, "end": v(78.36, -61.74) * mm});
            skLineSegment(sketch, "E2467", {"start": v(78.36, -61.74) * mm, "end": v(78.28, -61.6) * mm});
            skLineSegment(sketch, "E2468", {"start": v(78.28, -61.6) * mm, "end": v(78.2, -61.47) * mm});
            skLineSegment(sketch, "E2469", {"start": v(78.2, -61.47) * mm, "end": v(78.12, -61.33) * mm});
            skLineSegment(sketch, "E2470", {"start": v(78.12, -61.33) * mm, "end": v(78.04, -61.2) * mm});
            skLineSegment(sketch, "E2471", {"start": v(78.04, -61.2) * mm, "end": v(77.96, -61.07) * mm});
            skLineSegment(sketch, "E2472", {"start": v(77.96, -61.07) * mm, "end": v(77.88, -60.94) * mm});
            skLineSegment(sketch, "E2473", {"start": v(77.88, -60.94) * mm, "end": v(77.8, -60.82) * mm});
            skLineSegment(sketch, "E2474", {"start": v(77.8, -60.82) * mm, "end": v(77.72, -60.7) * mm});
            skLineSegment(sketch, "E2475", {"start": v(77.72, -60.7) * mm, "end": v(77.65, -60.57) * mm});
            skLineSegment(sketch, "E2476", {"start": v(77.65, -60.57) * mm, "end": v(77.57, -60.45) * mm});
            skLineSegment(sketch, "E2477", {"start": v(77.57, -60.45) * mm, "end": v(77.5, -60.33) * mm});
            skLineSegment(sketch, "E2478", {"start": v(77.5, -60.33) * mm, "end": v(77.42, -60.2) * mm});
            skLineSegment(sketch, "E2479", {"start": v(77.42, -60.2) * mm, "end": v(77.34, -60.1) * mm});
            skLineSegment(sketch, "E2480", {"start": v(77.34, -60.1) * mm, "end": v(77.26, -59.98) * mm});
            skLineSegment(sketch, "E2481", {"start": v(77.26, -59.98) * mm, "end": v(77.19, -59.87) * mm});
            skLineSegment(sketch, "E2482", {"start": v(77.19, -59.87) * mm, "end": v(77.11, -59.76) * mm});
            skLineSegment(sketch, "E2483", {"start": v(77.11, -59.76) * mm, "end": v(77.04, -59.65) * mm});
            skLineSegment(sketch, "E2484", {"start": v(77.04, -59.65) * mm, "end": v(76.97, -59.54) * mm});
            skLineSegment(sketch, "E2485", {"start": v(76.97, -59.54) * mm, "end": v(76.9, -59.43) * mm});
            skLineSegment(sketch, "E2486", {"start": v(76.9, -59.43) * mm, "end": v(77.42, -58.65) * mm});
            skLineSegment(sketch, "E2487", {"start": v(77.42, -58.65) * mm, "end": v(78.03, -57.93) * mm});
            skLineSegment(sketch, "E2488", {"start": v(78.03, -57.93) * mm, "end": v(78.15, -57.97) * mm});
            skLineSegment(sketch, "E2489", {"start": v(78.15, -57.97) * mm, "end": v(78.28, -58.01) * mm});
            skLineSegment(sketch, "E2490", {"start": v(78.28, -58.01) * mm, "end": v(78.4, -58.06) * mm});
            skLineSegment(sketch, "E2491", {"start": v(78.4, -58.06) * mm, "end": v(78.53, -58.1) * mm});
            skLineSegment(sketch, "E2492", {"start": v(78.53, -58.1) * mm, "end": v(78.66, -58.14) * mm});
            skLineSegment(sketch, "E2493", {"start": v(78.66, -58.14) * mm, "end": v(78.79, -58.18) * mm});
            skLineSegment(sketch, "E2494", {"start": v(78.79, -58.18) * mm, "end": v(78.92, -58.22) * mm});
            skLineSegment(sketch, "E2495", {"start": v(78.92, -58.22) * mm, "end": v(79.05, -58.26) * mm});
            skLineSegment(sketch, "E2496", {"start": v(79.05, -58.26) * mm, "end": v(79.19, -58.3) * mm});
            skLineSegment(sketch, "E2497", {"start": v(79.19, -58.3) * mm, "end": v(79.33, -58.35) * mm});
            skLineSegment(sketch, "E2498", {"start": v(79.33, -58.35) * mm, "end": v(79.47, -58.39) * mm});
            skLineSegment(sketch, "E2499", {"start": v(79.47, -58.39) * mm, "end": v(79.6, -58.43) * mm});
            skLineSegment(sketch, "E2500", {"start": v(79.6, -58.43) * mm, "end": v(79.75, -58.47) * mm});
            skLineSegment(sketch, "E2501", {"start": v(79.75, -58.47) * mm, "end": v(79.9, -58.51) * mm});
            skLineSegment(sketch, "E2502", {"start": v(79.9, -58.51) * mm, "end": v(80.04, -58.55) * mm});
            skLineSegment(sketch, "E2503", {"start": v(80.04, -58.55) * mm, "end": v(80.2, -58.6) * mm});
            skLineSegment(sketch, "E2504", {"start": v(80.2, -58.6) * mm, "end": v(80.34, -58.63) * mm});
            skLineSegment(sketch, "E2505", {"start": v(80.34, -58.63) * mm, "end": v(80.5, -58.68) * mm});
            skLineSegment(sketch, "E2506", {"start": v(80.5, -58.68) * mm, "end": v(80.65, -58.72) * mm});
            skLineSegment(sketch, "E2507", {"start": v(80.65, -58.72) * mm, "end": v(80.8, -58.76) * mm});
            skLineSegment(sketch, "E2508", {"start": v(80.8, -58.76) * mm, "end": v(80.97, -58.8) * mm});
            skLineSegment(sketch, "E2509", {"start": v(80.97, -58.8) * mm, "end": v(81.13, -58.83) * mm});
            skLineSegment(sketch, "E2510", {"start": v(81.13, -58.83) * mm, "end": v(81.29, -58.87) * mm});
            skLineSegment(sketch, "E2511", {"start": v(81.29, -58.87) * mm, "end": v(81.45, -58.91) * mm});
            skLineSegment(sketch, "E2512", {"start": v(81.45, -58.91) * mm, "end": v(81.62, -58.95) * mm});
            skLineSegment(sketch, "E2513", {"start": v(81.62, -58.95) * mm, "end": v(81.79, -58.99) * mm});
            skLineSegment(sketch, "E2514", {"start": v(81.79, -58.99) * mm, "end": v(81.96, -59.03) * mm});
            skLineSegment(sketch, "E2515", {"start": v(81.96, -59.03) * mm, "end": v(82.13, -59.06) * mm});
            skLineSegment(sketch, "E2516", {"start": v(82.13, -59.06) * mm, "end": v(82.3, -59.1) * mm});
            skLineSegment(sketch, "E2517", {"start": v(82.3, -59.1) * mm, "end": v(82.48, -59.14) * mm});
            skLineSegment(sketch, "E2518", {"start": v(82.48, -59.14) * mm, "end": v(82.65, -59.17) * mm});
            skLineSegment(sketch, "E2519", {"start": v(82.65, -59.17) * mm, "end": v(82.83, -59.2) * mm});
            skLineSegment(sketch, "E2520", {"start": v(82.83, -59.2) * mm, "end": v(83.01, -59.24) * mm});
            skLineSegment(sketch, "E2521", {"start": v(83.01, -59.24) * mm, "end": v(83.2, -59.28) * mm});
            skLineSegment(sketch, "E2522", {"start": v(83.2, -59.28) * mm, "end": v(83.38, -59.31) * mm});
            skLineSegment(sketch, "E2523", {"start": v(83.38, -59.31) * mm, "end": v(83.57, -59.35) * mm});
            skLineSegment(sketch, "E2524", {"start": v(83.57, -59.35) * mm, "end": v(83.62, -59.28) * mm});
            skLineSegment(sketch, "E2525", {"start": v(83.62, -59.28) * mm, "end": v(84.52, -58) * mm});
            skLineSegment(sketch, "E2526", {"start": v(84.52, -58) * mm, "end": v(84.56, -57.92) * mm});
            skLineSegment(sketch, "E2527", {"start": v(84.56, -57.92) * mm, "end": v(84.46, -57.76) * mm});
            skLineSegment(sketch, "E2528", {"start": v(84.46, -57.76) * mm, "end": v(84.37, -57.6) * mm});
            skLineSegment(sketch, "E2529", {"start": v(84.37, -57.6) * mm, "end": v(84.27, -57.44) * mm});
            skLineSegment(sketch, "E2530", {"start": v(84.27, -57.44) * mm, "end": v(84.18, -57.28) * mm});
            skLineSegment(sketch, "E2531", {"start": v(84.18, -57.28) * mm, "end": v(84.08, -57.13) * mm});
            skLineSegment(sketch, "E2532", {"start": v(84.08, -57.13) * mm, "end": v(83.99, -56.97) * mm});
            skLineSegment(sketch, "E2533", {"start": v(83.99, -56.97) * mm, "end": v(83.9, -56.82) * mm});
            skLineSegment(sketch, "E2534", {"start": v(83.9, -56.82) * mm, "end": v(83.8, -56.67) * mm});
            skLineSegment(sketch, "E2535", {"start": v(83.8, -56.67) * mm, "end": v(83.7, -56.52) * mm});
            skLineSegment(sketch, "E2536", {"start": v(83.7, -56.52) * mm, "end": v(83.6, -56.38) * mm});
            skLineSegment(sketch, "E2537", {"start": v(83.6, -56.38) * mm, "end": v(83.51, -56.23) * mm});
            skLineSegment(sketch, "E2538", {"start": v(83.51, -56.23) * mm, "end": v(83.42, -56.09) * mm});
            skLineSegment(sketch, "E2539", {"start": v(83.42, -56.09) * mm, "end": v(83.33, -55.95) * mm});
            skLineSegment(sketch, "E2540", {"start": v(83.33, -55.95) * mm, "end": v(83.24, -55.8) * mm});
            skLineSegment(sketch, "E2541", {"start": v(83.24, -55.8) * mm, "end": v(83.14, -55.67) * mm});
            skLineSegment(sketch, "E2542", {"start": v(83.14, -55.67) * mm, "end": v(83.05, -55.54) * mm});
            skLineSegment(sketch, "E2543", {"start": v(83.05, -55.54) * mm, "end": v(82.96, -55.4) * mm});
            skLineSegment(sketch, "E2544", {"start": v(82.96, -55.4) * mm, "end": v(82.87, -55.27) * mm});
            skLineSegment(sketch, "E2545", {"start": v(82.87, -55.27) * mm, "end": v(82.78, -55.14) * mm});
            skLineSegment(sketch, "E2546", {"start": v(82.78, -55.14) * mm, "end": v(82.69, -55.02) * mm});
            skLineSegment(sketch, "E2547", {"start": v(82.69, -55.02) * mm, "end": v(82.6, -54.89) * mm});
            skLineSegment(sketch, "E2548", {"start": v(82.6, -54.89) * mm, "end": v(82.5, -54.77) * mm});
            skLineSegment(sketch, "E2549", {"start": v(82.5, -54.77) * mm, "end": v(82.42, -54.64) * mm});
            skLineSegment(sketch, "E2550", {"start": v(82.42, -54.64) * mm, "end": v(82.33, -54.52) * mm});
            skLineSegment(sketch, "E2551", {"start": v(82.33, -54.52) * mm, "end": v(82.25, -54.4) * mm});
            skLineSegment(sketch, "E2552", {"start": v(82.25, -54.4) * mm, "end": v(82.16, -54.29) * mm});
            skLineSegment(sketch, "E2553", {"start": v(82.16, -54.29) * mm, "end": v(82.07, -54.17) * mm});
            skLineSegment(sketch, "E2554", {"start": v(82.07, -54.17) * mm, "end": v(81.99, -54.06) * mm});
            skLineSegment(sketch, "E2555", {"start": v(81.99, -54.06) * mm, "end": v(81.9, -53.95) * mm});
            skLineSegment(sketch, "E2556", {"start": v(81.9, -53.95) * mm, "end": v(81.82, -53.84) * mm});
            skLineSegment(sketch, "E2557", {"start": v(81.82, -53.84) * mm, "end": v(81.73, -53.73) * mm});
            skLineSegment(sketch, "E2558", {"start": v(81.73, -53.73) * mm, "end": v(81.65, -53.63) * mm});
            skLineSegment(sketch, "E2559", {"start": v(81.65, -53.63) * mm, "end": v(81.56, -53.52) * mm});
            skLineSegment(sketch, "E2560", {"start": v(81.56, -53.52) * mm, "end": v(81.48, -53.42) * mm});
            skLineSegment(sketch, "E2561", {"start": v(81.48, -53.42) * mm, "end": v(81.4, -53.32) * mm});
            skLineSegment(sketch, "E2562", {"start": v(81.4, -53.32) * mm, "end": v(81.32, -53.22) * mm});
            skLineSegment(sketch, "E2563", {"start": v(81.32, -53.22) * mm, "end": v(81.78, -52.4) * mm});
            skLineSegment(sketch, "E2564", {"start": v(81.78, -52.4) * mm, "end": v(82.34, -51.63) * mm});
            skLineSegment(sketch, "E2565", {"start": v(82.34, -51.63) * mm, "end": v(82.46, -51.66) * mm});
            skLineSegment(sketch, "E2566", {"start": v(82.46, -51.66) * mm, "end": v(82.59, -51.7) * mm});
            skLineSegment(sketch, "E2567", {"start": v(82.59, -51.7) * mm, "end": v(82.72, -51.73) * mm});
            skLineSegment(sketch, "E2568", {"start": v(82.72, -51.73) * mm, "end": v(82.84, -51.76) * mm});
            skLineSegment(sketch, "E2569", {"start": v(82.84, -51.76) * mm, "end": v(82.98, -51.79) * mm});
            skLineSegment(sketch, "E2570", {"start": v(82.98, -51.79) * mm, "end": v(83.1, -51.82) * mm});
            skLineSegment(sketch, "E2571", {"start": v(83.1, -51.82) * mm, "end": v(83.24, -51.85) * mm});
            skLineSegment(sketch, "E2572", {"start": v(83.24, -51.85) * mm, "end": v(83.38, -51.88) * mm});
            skLineSegment(sketch, "E2573", {"start": v(83.38, -51.88) * mm, "end": v(83.52, -51.91) * mm});
            skLineSegment(sketch, "E2574", {"start": v(83.52, -51.91) * mm, "end": v(83.66, -51.94) * mm});
            skLineSegment(sketch, "E2575", {"start": v(83.66, -51.94) * mm, "end": v(83.8, -51.97) * mm});
            skLineSegment(sketch, "E2576", {"start": v(83.8, -51.97) * mm, "end": v(83.95, -52) * mm});
            skLineSegment(sketch, "E2577", {"start": v(83.95, -52) * mm, "end": v(84.1, -52.03) * mm});
            skLineSegment(sketch, "E2578", {"start": v(84.1, -52.03) * mm, "end": v(84.24, -52.06) * mm});
            skLineSegment(sketch, "E2579", {"start": v(84.24, -52.06) * mm, "end": v(84.4, -52.1) * mm});
            skLineSegment(sketch, "E2580", {"start": v(84.4, -52.1) * mm, "end": v(84.54, -52.12) * mm});
            skLineSegment(sketch, "E2581", {"start": v(84.54, -52.12) * mm, "end": v(84.7, -52.15) * mm});
            skLineSegment(sketch, "E2582", {"start": v(84.7, -52.15) * mm, "end": v(84.85, -52.18) * mm});
            skLineSegment(sketch, "E2583", {"start": v(84.85, -52.18) * mm, "end": v(85, -52.2) * mm});
            skLineSegment(sketch, "E2584", {"start": v(85, -52.2) * mm, "end": v(85.17, -52.23) * mm});
            skLineSegment(sketch, "E2585", {"start": v(85.17, -52.23) * mm, "end": v(85.33, -52.26) * mm});
            skLineSegment(sketch, "E2586", {"start": v(85.33, -52.26) * mm, "end": v(85.5, -52.29) * mm});
            skLineSegment(sketch, "E2587", {"start": v(85.5, -52.29) * mm, "end": v(85.66, -52.31) * mm});
            skLineSegment(sketch, "E2588", {"start": v(85.66, -52.31) * mm, "end": v(85.82, -52.34) * mm});
            skLineSegment(sketch, "E2589", {"start": v(85.82, -52.34) * mm, "end": v(86, -52.36) * mm});
            skLineSegment(sketch, "E2590", {"start": v(86, -52.36) * mm, "end": v(86.16, -52.39) * mm});
            skLineSegment(sketch, "E2591", {"start": v(86.16, -52.39) * mm, "end": v(86.33, -52.41) * mm});
            skLineSegment(sketch, "E2592", {"start": v(86.33, -52.41) * mm, "end": v(86.5, -52.44) * mm});
            skLineSegment(sketch, "E2593", {"start": v(86.5, -52.44) * mm, "end": v(86.68, -52.46) * mm});
            skLineSegment(sketch, "E2594", {"start": v(86.68, -52.46) * mm, "end": v(86.86, -52.48) * mm});
            skLineSegment(sketch, "E2595", {"start": v(86.86, -52.48) * mm, "end": v(87.04, -52.5) * mm});
            skLineSegment(sketch, "E2596", {"start": v(87.04, -52.5) * mm, "end": v(87.22, -52.53) * mm});
            skLineSegment(sketch, "E2597", {"start": v(87.22, -52.53) * mm, "end": v(87.4, -52.55) * mm});
            skLineSegment(sketch, "E2598", {"start": v(87.4, -52.55) * mm, "end": v(87.6, -52.57) * mm});
            skLineSegment(sketch, "E2599", {"start": v(87.6, -52.57) * mm, "end": v(87.78, -52.59) * mm});
            skLineSegment(sketch, "E2600", {"start": v(87.78, -52.59) * mm, "end": v(87.97, -52.6) * mm});
            skLineSegment(sketch, "E2601", {"start": v(87.97, -52.6) * mm, "end": v(88.01, -52.54) * mm});
            skLineSegment(sketch, "E2602", {"start": v(88.01, -52.54) * mm, "end": v(88.8, -51.18) * mm});
            skLineSegment(sketch, "E2603", {"start": v(88.8, -51.18) * mm, "end": v(88.84, -51.11) * mm});
            skLineSegment(sketch, "E2604", {"start": v(88.84, -51.11) * mm, "end": v(88.74, -50.96) * mm});
            skLineSegment(sketch, "E2605", {"start": v(88.74, -50.96) * mm, "end": v(88.63, -50.8) * mm});
            skLineSegment(sketch, "E2606", {"start": v(88.63, -50.8) * mm, "end": v(88.52, -50.65) * mm});
            skLineSegment(sketch, "E2607", {"start": v(88.52, -50.65) * mm, "end": v(88.41, -50.5) * mm});
            skLineSegment(sketch, "E2608", {"start": v(88.41, -50.5) * mm, "end": v(88.3, -50.35) * mm});
            skLineSegment(sketch, "E2609", {"start": v(88.3, -50.35) * mm, "end": v(88.2, -50.2) * mm});
            skLineSegment(sketch, "E2610", {"start": v(88.2, -50.2) * mm, "end": v(88.1, -50.06) * mm});
            skLineSegment(sketch, "E2611", {"start": v(88.1, -50.06) * mm, "end": v(87.98, -49.92) * mm});
            skLineSegment(sketch, "E2612", {"start": v(87.98, -49.92) * mm, "end": v(87.88, -49.78) * mm});
            skLineSegment(sketch, "E2613", {"start": v(87.88, -49.78) * mm, "end": v(87.77, -49.64) * mm});
            skLineSegment(sketch, "E2614", {"start": v(87.77, -49.64) * mm, "end": v(87.67, -49.5) * mm});
            skLineSegment(sketch, "E2615", {"start": v(87.67, -49.5) * mm, "end": v(87.57, -49.37) * mm});
            skLineSegment(sketch, "E2616", {"start": v(87.57, -49.37) * mm, "end": v(87.46, -49.24) * mm});
            skLineSegment(sketch, "E2617", {"start": v(87.46, -49.24) * mm, "end": v(87.36, -49.1) * mm});
            skLineSegment(sketch, "E2618", {"start": v(87.36, -49.1) * mm, "end": v(87.26, -48.98) * mm});
            skLineSegment(sketch, "E2619", {"start": v(87.26, -48.98) * mm, "end": v(87.15, -48.85) * mm});
            skLineSegment(sketch, "E2620", {"start": v(87.15, -48.85) * mm, "end": v(87.05, -48.72) * mm});
            skLineSegment(sketch, "E2621", {"start": v(87.05, -48.72) * mm, "end": v(86.95, -48.6) * mm});
            skLineSegment(sketch, "E2622", {"start": v(86.95, -48.6) * mm, "end": v(86.85, -48.48) * mm});
            skLineSegment(sketch, "E2623", {"start": v(86.85, -48.48) * mm, "end": v(86.75, -48.36) * mm});
            skLineSegment(sketch, "E2624", {"start": v(86.75, -48.36) * mm, "end": v(86.65, -48.24) * mm});
            skLineSegment(sketch, "E2625", {"start": v(86.65, -48.24) * mm, "end": v(86.55, -48.12) * mm});
            skLineSegment(sketch, "E2626", {"start": v(86.55, -48.12) * mm, "end": v(86.45, -48) * mm});
            skLineSegment(sketch, "E2627", {"start": v(86.45, -48) * mm, "end": v(86.36, -47.9) * mm});
            skLineSegment(sketch, "E2628", {"start": v(86.36, -47.9) * mm, "end": v(86.26, -47.78) * mm});
            skLineSegment(sketch, "E2629", {"start": v(86.26, -47.78) * mm, "end": v(86.16, -47.67) * mm});
            skLineSegment(sketch, "E2630", {"start": v(86.16, -47.67) * mm, "end": v(86.07, -47.57) * mm});
            skLineSegment(sketch, "E2631", {"start": v(86.07, -47.57) * mm, "end": v(85.97, -47.46) * mm});
            skLineSegment(sketch, "E2632", {"start": v(85.97, -47.46) * mm, "end": v(85.88, -47.36) * mm});
            skLineSegment(sketch, "E2633", {"start": v(85.88, -47.36) * mm, "end": v(85.79, -47.25) * mm});
            skLineSegment(sketch, "E2634", {"start": v(85.79, -47.25) * mm, "end": v(85.7, -47.15) * mm});
            skLineSegment(sketch, "E2635", {"start": v(85.7, -47.15) * mm, "end": v(85.6, -47.05) * mm});
            skLineSegment(sketch, "E2636", {"start": v(85.6, -47.05) * mm, "end": v(85.51, -46.96) * mm});
            skLineSegment(sketch, "E2637", {"start": v(85.51, -46.96) * mm, "end": v(85.42, -46.86) * mm});
            skLineSegment(sketch, "E2638", {"start": v(85.42, -46.86) * mm, "end": v(85.33, -46.77) * mm});
            skLineSegment(sketch, "E2639", {"start": v(85.33, -46.77) * mm, "end": v(85.24, -46.67) * mm});
            skLineSegment(sketch, "E2640", {"start": v(85.24, -46.67) * mm, "end": v(85.64, -45.82) * mm});
            skLineSegment(sketch, "E2641", {"start": v(85.64, -45.82) * mm, "end": v(86.13, -45.01) * mm});
            skLineSegment(sketch, "E2642", {"start": v(86.13, -45.01) * mm, "end": v(86.26, -45.03) * mm});
            skLineSegment(sketch, "E2643", {"start": v(86.26, -45.03) * mm, "end": v(86.39, -45.05) * mm});
            skLineSegment(sketch, "E2644", {"start": v(86.39, -45.05) * mm, "end": v(86.52, -45.08) * mm});
            skLineSegment(sketch, "E2645", {"start": v(86.52, -45.08) * mm, "end": v(86.65, -45.1) * mm});
            skLineSegment(sketch, "E2646", {"start": v(86.65, -45.1) * mm, "end": v(86.78, -45.12) * mm});
            skLineSegment(sketch, "E2647", {"start": v(86.78, -45.12) * mm, "end": v(86.92, -45.14) * mm});
            skLineSegment(sketch, "E2648", {"start": v(86.92, -45.14) * mm, "end": v(87.06, -45.16) * mm});
            skLineSegment(sketch, "E2649", {"start": v(87.06, -45.16) * mm, "end": v(87.2, -45.18) * mm});
            skLineSegment(sketch, "E2650", {"start": v(87.2, -45.18) * mm, "end": v(87.34, -45.2) * mm});
            skLineSegment(sketch, "E2651", {"start": v(87.34, -45.2) * mm, "end": v(87.48, -45.22) * mm});
            skLineSegment(sketch, "E2652", {"start": v(87.48, -45.22) * mm, "end": v(87.62, -45.24) * mm});
            skLineSegment(sketch, "E2653", {"start": v(87.62, -45.24) * mm, "end": v(87.77, -45.26) * mm});
            skLineSegment(sketch, "E2654", {"start": v(87.77, -45.26) * mm, "end": v(87.92, -45.28) * mm});
            skLineSegment(sketch, "E2655", {"start": v(87.92, -45.28) * mm, "end": v(88.07, -45.3) * mm});
            skLineSegment(sketch, "E2656", {"start": v(88.07, -45.3) * mm, "end": v(88.22, -45.31) * mm});
            skLineSegment(sketch, "E2657", {"start": v(88.22, -45.31) * mm, "end": v(88.37, -45.33) * mm});
            skLineSegment(sketch, "E2658", {"start": v(88.37, -45.33) * mm, "end": v(88.53, -45.34) * mm});
            skLineSegment(sketch, "E2659", {"start": v(88.53, -45.34) * mm, "end": v(88.68, -45.36) * mm});
            skLineSegment(sketch, "E2660", {"start": v(88.68, -45.36) * mm, "end": v(88.84, -45.38) * mm});
            skLineSegment(sketch, "E2661", {"start": v(88.84, -45.38) * mm, "end": v(89, -45.4) * mm});
            skLineSegment(sketch, "E2662", {"start": v(89, -45.4) * mm, "end": v(89.17, -45.4) * mm});
            skLineSegment(sketch, "E2663", {"start": v(89.17, -45.4) * mm, "end": v(89.33, -45.42) * mm});
            skLineSegment(sketch, "E2664", {"start": v(89.33, -45.42) * mm, "end": v(89.5, -45.43) * mm});
            skLineSegment(sketch, "E2665", {"start": v(89.5, -45.43) * mm, "end": v(89.67, -45.44) * mm});
            skLineSegment(sketch, "E2666", {"start": v(89.67, -45.44) * mm, "end": v(89.84, -45.46) * mm});
            skLineSegment(sketch, "E2667", {"start": v(89.84, -45.46) * mm, "end": v(90, -45.47) * mm});
            skLineSegment(sketch, "E2668", {"start": v(90, -45.47) * mm, "end": v(90.18, -45.48) * mm});
            skLineSegment(sketch, "E2669", {"start": v(90.18, -45.48) * mm, "end": v(90.36, -45.49) * mm});
            skLineSegment(sketch, "E2670", {"start": v(90.36, -45.49) * mm, "end": v(90.53, -45.5) * mm});
            skLineSegment(sketch, "E2671", {"start": v(90.53, -45.5) * mm, "end": v(90.71, -45.5) * mm});
            skLineSegment(sketch, "E2672", {"start": v(90.71, -45.5) * mm, "end": v(90.9, -45.51) * mm});
            skLineSegment(sketch, "E2673", {"start": v(90.9, -45.51) * mm, "end": v(91.08, -45.52) * mm});
            skLineSegment(sketch, "E2674", {"start": v(91.08, -45.52) * mm, "end": v(91.26, -45.53) * mm});
            skLineSegment(sketch, "E2675", {"start": v(91.26, -45.53) * mm, "end": v(91.45, -45.53) * mm});
            skLineSegment(sketch, "E2676", {"start": v(91.45, -45.53) * mm, "end": v(91.63, -45.54) * mm});
            skLineSegment(sketch, "E2677", {"start": v(91.63, -45.54) * mm, "end": v(91.82, -45.54) * mm});
            skLineSegment(sketch, "E2678", {"start": v(91.82, -45.54) * mm, "end": v(91.86, -45.47) * mm});
            skLineSegment(sketch, "E2679", {"start": v(91.86, -45.47) * mm, "end": v(92.55, -44.06) * mm});
            skLineSegment(sketch, "E2680", {"start": v(92.55, -44.06) * mm, "end": v(92.58, -43.98) * mm});
            skLineSegment(sketch, "E2681", {"start": v(92.58, -43.98) * mm, "end": v(92.46, -43.84) * mm});
            skLineSegment(sketch, "E2682", {"start": v(92.46, -43.84) * mm, "end": v(92.34, -43.7) * mm});
            skLineSegment(sketch, "E2683", {"start": v(92.34, -43.7) * mm, "end": v(92.22, -43.55) * mm});
            skLineSegment(sketch, "E2684", {"start": v(92.22, -43.55) * mm, "end": v(92.1, -43.4) * mm});
            skLineSegment(sketch, "E2685", {"start": v(92.1, -43.4) * mm, "end": v(91.98, -43.27) * mm});
            skLineSegment(sketch, "E2686", {"start": v(91.98, -43.27) * mm, "end": v(91.86, -43.13) * mm});
            skLineSegment(sketch, "E2687", {"start": v(91.86, -43.13) * mm, "end": v(91.75, -43) * mm});
            skLineSegment(sketch, "E2688", {"start": v(91.75, -43) * mm, "end": v(91.63, -42.86) * mm});
            skLineSegment(sketch, "E2689", {"start": v(91.63, -42.86) * mm, "end": v(91.51, -42.73) * mm});
            skLineSegment(sketch, "E2690", {"start": v(91.51, -42.73) * mm, "end": v(91.4, -42.6) * mm});
            skLineSegment(sketch, "E2691", {"start": v(91.4, -42.6) * mm, "end": v(91.28, -42.47) * mm});
            skLineSegment(sketch, "E2692", {"start": v(91.28, -42.47) * mm, "end": v(91.17, -42.35) * mm});
            skLineSegment(sketch, "E2693", {"start": v(91.17, -42.35) * mm, "end": v(91.05, -42.22) * mm});
            skLineSegment(sketch, "E2694", {"start": v(91.05, -42.22) * mm, "end": v(90.94, -42.1) * mm});
            skLineSegment(sketch, "E2695", {"start": v(90.94, -42.1) * mm, "end": v(90.83, -41.98) * mm});
            skLineSegment(sketch, "E2696", {"start": v(90.83, -41.98) * mm, "end": v(90.72, -41.86) * mm});
            skLineSegment(sketch, "E2697", {"start": v(90.72, -41.86) * mm, "end": v(90.6, -41.74) * mm});
            skLineSegment(sketch, "E2698", {"start": v(90.6, -41.74) * mm, "end": v(90.5, -41.63) * mm});
            skLineSegment(sketch, "E2699", {"start": v(90.5, -41.63) * mm, "end": v(90.39, -41.51) * mm});
            skLineSegment(sketch, "E2700", {"start": v(90.39, -41.51) * mm, "end": v(90.28, -41.4) * mm});
            skLineSegment(sketch, "E2701", {"start": v(90.28, -41.4) * mm, "end": v(90.17, -41.3) * mm});
            skLineSegment(sketch, "E2702", {"start": v(90.17, -41.3) * mm, "end": v(90.06, -41.18) * mm});
            skLineSegment(sketch, "E2703", {"start": v(90.06, -41.18) * mm, "end": v(89.95, -41.08) * mm});
            skLineSegment(sketch, "E2704", {"start": v(89.95, -41.08) * mm, "end": v(89.85, -40.97) * mm});
            skLineSegment(sketch, "E2705", {"start": v(89.85, -40.97) * mm, "end": v(89.74, -40.87) * mm});
            skLineSegment(sketch, "E2706", {"start": v(89.74, -40.87) * mm, "end": v(89.64, -40.77) * mm});
            skLineSegment(sketch, "E2707", {"start": v(89.64, -40.77) * mm, "end": v(89.54, -40.67) * mm});
            skLineSegment(sketch, "E2708", {"start": v(89.54, -40.67) * mm, "end": v(89.43, -40.57) * mm});
            skLineSegment(sketch, "E2709", {"start": v(89.43, -40.57) * mm, "end": v(89.33, -40.47) * mm});
            skLineSegment(sketch, "E2710", {"start": v(89.33, -40.47) * mm, "end": v(89.23, -40.38) * mm});
            skLineSegment(sketch, "E2711", {"start": v(89.23, -40.38) * mm, "end": v(89.13, -40.28) * mm});
            skLineSegment(sketch, "E2712", {"start": v(89.13, -40.28) * mm, "end": v(89.03, -40.2) * mm});
            skLineSegment(sketch, "E2713", {"start": v(89.03, -40.2) * mm, "end": v(88.93, -40.1) * mm});
            skLineSegment(sketch, "E2714", {"start": v(88.93, -40.1) * mm, "end": v(88.84, -40.01) * mm});
            skLineSegment(sketch, "E2715", {"start": v(88.84, -40.01) * mm, "end": v(88.74, -39.93) * mm});
            skLineSegment(sketch, "E2716", {"start": v(88.74, -39.93) * mm, "end": v(88.64, -39.84) * mm});
            skLineSegment(sketch, "E2717", {"start": v(88.64, -39.84) * mm, "end": v(88.97, -38.96) * mm});
            skLineSegment(sketch, "E2718", {"start": v(88.97, -38.96) * mm, "end": v(89.4, -38.11) * mm});
            skLineSegment(sketch, "E2719", {"start": v(89.4, -38.11) * mm, "end": v(89.53, -38.13) * mm});
            skLineSegment(sketch, "E2720", {"start": v(89.53, -38.13) * mm, "end": v(89.66, -38.14) * mm});
            skLineSegment(sketch, "E2721", {"start": v(89.66, -38.14) * mm, "end": v(89.79, -38.15) * mm});
            skLineSegment(sketch, "E2722", {"start": v(89.79, -38.15) * mm, "end": v(89.92, -38.16) * mm});
            skLineSegment(sketch, "E2723", {"start": v(89.92, -38.16) * mm, "end": v(90.06, -38.17) * mm});
            skLineSegment(sketch, "E2724", {"start": v(90.06, -38.17) * mm, "end": v(90.2, -38.18) * mm});
            skLineSegment(sketch, "E2725", {"start": v(90.2, -38.18) * mm, "end": v(90.33, -38.2) * mm});
            skLineSegment(sketch, "E2726", {"start": v(90.33, -38.2) * mm, "end": v(90.47, -38.2) * mm});
            skLineSegment(sketch, "E2727", {"start": v(90.47, -38.2) * mm, "end": v(90.61, -38.2) * mm});
            skLineSegment(sketch, "E2728", {"start": v(90.61, -38.2) * mm, "end": v(90.76, -38.22) * mm});
            skLineSegment(sketch, "E2729", {"start": v(90.76, -38.22) * mm, "end": v(90.9, -38.22) * mm});
            skLineSegment(sketch, "E2730", {"start": v(90.9, -38.22) * mm, "end": v(91.05, -38.23) * mm});
            skLineSegment(sketch, "E2731", {"start": v(91.05, -38.23) * mm, "end": v(91.2, -38.24) * mm});
            skLineSegment(sketch, "E2732", {"start": v(91.2, -38.24) * mm, "end": v(91.35, -38.24) * mm});
            skLineSegment(sketch, "E2733", {"start": v(91.35, -38.24) * mm, "end": v(91.5, -38.25) * mm});
            skLineSegment(sketch, "E2734", {"start": v(91.5, -38.25) * mm, "end": v(91.66, -38.25) * mm});
            skLineSegment(sketch, "E2735", {"start": v(91.66, -38.25) * mm, "end": v(91.81, -38.26) * mm});
            skLineSegment(sketch, "E2736", {"start": v(91.81, -38.26) * mm, "end": v(91.97, -38.26) * mm});
            skLineSegment(sketch, "E2737", {"start": v(91.97, -38.26) * mm, "end": v(92.13, -38.27) * mm});
            skLineSegment(sketch, "E2738", {"start": v(92.13, -38.27) * mm, "end": v(92.3, -38.27) * mm});
            skLineSegment(sketch, "E2739", {"start": v(92.3, -38.27) * mm, "end": v(92.45, -38.27) * mm});
            skLineSegment(sketch, "E2740", {"start": v(92.45, -38.27) * mm, "end": v(92.62, -38.27) * mm});
            skLineSegment(sketch, "E2741", {"start": v(92.62, -38.27) * mm, "end": v(92.79, -38.27) * mm});
            skLineSegment(sketch, "E2742", {"start": v(92.79, -38.27) * mm, "end": v(92.95, -38.27) * mm});
            skLineSegment(sketch, "E2743", {"start": v(92.95, -38.27) * mm, "end": v(93.12, -38.27) * mm});
            skLineSegment(sketch, "E2744", {"start": v(93.12, -38.27) * mm, "end": v(93.3, -38.27) * mm});
            skLineSegment(sketch, "E2745", {"start": v(93.3, -38.27) * mm, "end": v(93.47, -38.26) * mm});
            skLineSegment(sketch, "E2746", {"start": v(93.47, -38.26) * mm, "end": v(93.65, -38.26) * mm});
            skLineSegment(sketch, "E2747", {"start": v(93.65, -38.26) * mm, "end": v(93.82, -38.25) * mm});
            skLineSegment(sketch, "E2748", {"start": v(93.82, -38.25) * mm, "end": v(94, -38.25) * mm});
            skLineSegment(sketch, "E2749", {"start": v(94, -38.25) * mm, "end": v(94.18, -38.24) * mm});
            skLineSegment(sketch, "E2750", {"start": v(94.18, -38.24) * mm, "end": v(94.37, -38.24) * mm});
            skLineSegment(sketch, "E2751", {"start": v(94.37, -38.24) * mm, "end": v(94.55, -38.23) * mm});
            skLineSegment(sketch, "E2752", {"start": v(94.55, -38.23) * mm, "end": v(94.74, -38.22) * mm});
            skLineSegment(sketch, "E2753", {"start": v(94.74, -38.22) * mm, "end": v(94.92, -38.2) * mm});
            skLineSegment(sketch, "E2754", {"start": v(94.92, -38.2) * mm, "end": v(95.11, -38.2) * mm});
            skLineSegment(sketch, "E2755", {"start": v(95.11, -38.2) * mm, "end": v(95.15, -38.12) * mm});
            skLineSegment(sketch, "E2756", {"start": v(95.15, -38.12) * mm, "end": v(95.72, -36.66) * mm});
            skLineSegment(sketch, "E2757", {"start": v(95.72, -36.66) * mm, "end": v(95.75, -36.58) * mm});
            skLineSegment(sketch, "E2758", {"start": v(95.75, -36.58) * mm, "end": v(95.61, -36.45) * mm});
            skLineSegment(sketch, "E2759", {"start": v(95.61, -36.45) * mm, "end": v(95.48, -36.31) * mm});
            skLineSegment(sketch, "E2760", {"start": v(95.48, -36.31) * mm, "end": v(95.35, -36.18) * mm});
            skLineSegment(sketch, "E2761", {"start": v(95.35, -36.18) * mm, "end": v(95.22, -36.05) * mm});
            skLineSegment(sketch, "E2762", {"start": v(95.22, -36.05) * mm, "end": v(95.1, -35.92) * mm});
            skLineSegment(sketch, "E2763", {"start": v(95.1, -35.92) * mm, "end": v(94.97, -35.8) * mm});
            skLineSegment(sketch, "E2764", {"start": v(94.97, -35.8) * mm, "end": v(94.84, -35.67) * mm});
            skLineSegment(sketch, "E2765", {"start": v(94.84, -35.67) * mm, "end": v(94.71, -35.54) * mm});
            skLineSegment(sketch, "E2766", {"start": v(94.71, -35.54) * mm, "end": v(94.58, -35.42) * mm});
            skLineSegment(sketch, "E2767", {"start": v(94.58, -35.42) * mm, "end": v(94.46, -35.3) * mm});
            skLineSegment(sketch, "E2768", {"start": v(94.46, -35.3) * mm, "end": v(94.33, -35.18) * mm});
            skLineSegment(sketch, "E2769", {"start": v(94.33, -35.18) * mm, "end": v(94.21, -35.06) * mm});
            skLineSegment(sketch, "E2770", {"start": v(94.21, -35.06) * mm, "end": v(94.09, -34.95) * mm});
            skLineSegment(sketch, "E2771", {"start": v(94.09, -34.95) * mm, "end": v(93.96, -34.84) * mm});
            skLineSegment(sketch, "E2772", {"start": v(93.96, -34.84) * mm, "end": v(93.84, -34.72) * mm});
            skLineSegment(sketch, "E2773", {"start": v(93.84, -34.72) * mm, "end": v(93.72, -34.61) * mm});
            skLineSegment(sketch, "E2774", {"start": v(93.72, -34.61) * mm, "end": v(93.6, -34.5) * mm});
            skLineSegment(sketch, "E2775", {"start": v(93.6, -34.5) * mm, "end": v(93.48, -34.4) * mm});
            skLineSegment(sketch, "E2776", {"start": v(93.48, -34.4) * mm, "end": v(93.36, -34.3) * mm});
            skLineSegment(sketch, "E2777", {"start": v(93.36, -34.3) * mm, "end": v(93.25, -34.2) * mm});
            skLineSegment(sketch, "E2778", {"start": v(93.25, -34.2) * mm, "end": v(93.13, -34.1) * mm});
            skLineSegment(sketch, "E2779", {"start": v(93.13, -34.1) * mm, "end": v(93.02, -34) * mm});
            skLineSegment(sketch, "E2780", {"start": v(93.02, -34) * mm, "end": v(92.9, -33.9) * mm});
            skLineSegment(sketch, "E2781", {"start": v(92.9, -33.9) * mm, "end": v(92.79, -33.8) * mm});
            skLineSegment(sketch, "E2782", {"start": v(92.79, -33.8) * mm, "end": v(92.67, -33.7) * mm});
            skLineSegment(sketch, "E2783", {"start": v(92.67, -33.7) * mm, "end": v(92.56, -33.6) * mm});
            skLineSegment(sketch, "E2784", {"start": v(92.56, -33.6) * mm, "end": v(92.45, -33.52) * mm});
            skLineSegment(sketch, "E2785", {"start": v(92.45, -33.52) * mm, "end": v(92.34, -33.43) * mm});
            skLineSegment(sketch, "E2786", {"start": v(92.34, -33.43) * mm, "end": v(92.23, -33.34) * mm});
            skLineSegment(sketch, "E2787", {"start": v(92.23, -33.34) * mm, "end": v(92.12, -33.25) * mm});
            skLineSegment(sketch, "E2788", {"start": v(92.12, -33.25) * mm, "end": v(92.02, -33.17) * mm});
            skLineSegment(sketch, "E2789", {"start": v(92.02, -33.17) * mm, "end": v(91.91, -33.08) * mm});
            skLineSegment(sketch, "E2790", {"start": v(91.91, -33.08) * mm, "end": v(91.8, -33) * mm});
            skLineSegment(sketch, "E2791", {"start": v(91.8, -33) * mm, "end": v(91.7, -32.92) * mm});
            skLineSegment(sketch, "E2792", {"start": v(91.7, -32.92) * mm, "end": v(91.6, -32.84) * mm});
            skLineSegment(sketch, "E2793", {"start": v(91.6, -32.84) * mm, "end": v(91.5, -32.76) * mm});
            skLineSegment(sketch, "E2794", {"start": v(91.5, -32.76) * mm, "end": v(91.75, -31.85) * mm});
            skLineSegment(sketch, "E2795", {"start": v(91.75, -31.85) * mm, "end": v(92.12, -30.98) * mm});
            skLineSegment(sketch, "E2796", {"start": v(92.12, -30.98) * mm, "end": v(92.24, -30.98) * mm});
            skLineSegment(sketch, "E2797", {"start": v(92.24, -30.98) * mm, "end": v(92.37, -30.99) * mm});
            skLineSegment(sketch, "E2798", {"start": v(92.37, -30.99) * mm, "end": v(92.5, -30.99) * mm});
            skLineSegment(sketch, "E2799", {"start": v(92.5, -30.99) * mm, "end": v(92.64, -30.99) * mm});
            skLineSegment(sketch, "E2800", {"start": v(92.64, -30.99) * mm, "end": v(92.77, -30.99) * mm});
            skLineSegment(sketch, "E2801", {"start": v(92.77, -30.99) * mm, "end": v(92.9, -30.99) * mm});
            skLineSegment(sketch, "E2802", {"start": v(92.9, -30.99) * mm, "end": v(93.05, -30.99) * mm});
            skLineSegment(sketch, "E2803", {"start": v(93.05, -30.99) * mm, "end": v(93.19, -30.98) * mm});
            skLineSegment(sketch, "E2804", {"start": v(93.19, -30.98) * mm, "end": v(93.33, -30.98) * mm});
            skLineSegment(sketch, "E2805", {"start": v(93.33, -30.98) * mm, "end": v(93.47, -30.98) * mm});
            skLineSegment(sketch, "E2806", {"start": v(93.47, -30.98) * mm, "end": v(93.62, -30.98) * mm});
            skLineSegment(sketch, "E2807", {"start": v(93.62, -30.98) * mm, "end": v(93.77, -30.97) * mm});
            skLineSegment(sketch, "E2808", {"start": v(93.77, -30.97) * mm, "end": v(93.92, -30.97) * mm});
            skLineSegment(sketch, "E2809", {"start": v(93.92, -30.97) * mm, "end": v(94.07, -30.96) * mm});
            skLineSegment(sketch, "E2810", {"start": v(94.07, -30.96) * mm, "end": v(94.22, -30.95) * mm});
            skLineSegment(sketch, "E2811", {"start": v(94.22, -30.95) * mm, "end": v(94.37, -30.95) * mm});
            skLineSegment(sketch, "E2812", {"start": v(94.37, -30.95) * mm, "end": v(94.53, -30.94) * mm});
            skLineSegment(sketch, "E2813", {"start": v(94.53, -30.94) * mm, "end": v(94.69, -30.93) * mm});
            skLineSegment(sketch, "E2814", {"start": v(94.69, -30.93) * mm, "end": v(94.85, -30.92) * mm});
            skLineSegment(sketch, "E2815", {"start": v(94.85, -30.92) * mm, "end": v(95, -30.9) * mm});
            skLineSegment(sketch, "E2816", {"start": v(95, -30.9) * mm, "end": v(95.17, -30.9) * mm});
            skLineSegment(sketch, "E2817", {"start": v(95.17, -30.9) * mm, "end": v(95.34, -30.88) * mm});
            skLineSegment(sketch, "E2818", {"start": v(95.34, -30.88) * mm, "end": v(95.5, -30.87) * mm});
            skLineSegment(sketch, "E2819", {"start": v(95.5, -30.87) * mm, "end": v(95.67, -30.86) * mm});
            skLineSegment(sketch, "E2820", {"start": v(95.67, -30.86) * mm, "end": v(95.84, -30.84) * mm});
            skLineSegment(sketch, "E2821", {"start": v(95.84, -30.84) * mm, "end": v(96.01, -30.83) * mm});
            skLineSegment(sketch, "E2822", {"start": v(96.01, -30.83) * mm, "end": v(96.18, -30.81) * mm});
            skLineSegment(sketch, "E2823", {"start": v(96.18, -30.81) * mm, "end": v(96.36, -30.8) * mm});
            skLineSegment(sketch, "E2824", {"start": v(96.36, -30.8) * mm, "end": v(96.54, -30.78) * mm});
            skLineSegment(sketch, "E2825", {"start": v(96.54, -30.78) * mm, "end": v(96.71, -30.76) * mm});
            skLineSegment(sketch, "E2826", {"start": v(96.71, -30.76) * mm, "end": v(96.9, -30.74) * mm});
            skLineSegment(sketch, "E2827", {"start": v(96.9, -30.74) * mm, "end": v(97.08, -30.71) * mm});
            skLineSegment(sketch, "E2828", {"start": v(97.08, -30.71) * mm, "end": v(97.26, -30.7) * mm});
            skLineSegment(sketch, "E2829", {"start": v(97.26, -30.7) * mm, "end": v(97.44, -30.67) * mm});
            skLineSegment(sketch, "E2830", {"start": v(97.44, -30.67) * mm, "end": v(97.63, -30.64) * mm});
            skLineSegment(sketch, "E2831", {"start": v(97.63, -30.64) * mm, "end": v(97.82, -30.62) * mm});
            skLineSegment(sketch, "E2832", {"start": v(97.82, -30.62) * mm, "end": v(97.84, -30.54) * mm});
            skLineSegment(sketch, "E2833", {"start": v(97.84, -30.54) * mm, "end": v(98.3, -29.04) * mm});
            skLineSegment(sketch, "E2834", {"start": v(98.3, -29.04) * mm, "end": v(98.32, -28.96) * mm});
            skLineSegment(sketch, "E2835", {"start": v(98.32, -28.96) * mm, "end": v(98.18, -28.83) * mm});
            skLineSegment(sketch, "E2836", {"start": v(98.18, -28.83) * mm, "end": v(98.04, -28.7) * mm});
            skLineSegment(sketch, "E2837", {"start": v(98.04, -28.7) * mm, "end": v(97.9, -28.59) * mm});
            skLineSegment(sketch, "E2838", {"start": v(97.9, -28.59) * mm, "end": v(97.76, -28.47) * mm});
            skLineSegment(sketch, "E2839", {"start": v(97.76, -28.47) * mm, "end": v(97.62, -28.35) * mm});
            skLineSegment(sketch, "E2840", {"start": v(97.62, -28.35) * mm, "end": v(97.48, -28.23) * mm});
            skLineSegment(sketch, "E2841", {"start": v(97.48, -28.23) * mm, "end": v(97.34, -28.11) * mm});
            skLineSegment(sketch, "E2842", {"start": v(97.34, -28.11) * mm, "end": v(97.2, -28) * mm});
            skLineSegment(sketch, "E2843", {"start": v(97.2, -28) * mm, "end": v(97.07, -27.89) * mm});
            skLineSegment(sketch, "E2844", {"start": v(97.07, -27.89) * mm, "end": v(96.94, -27.78) * mm});
            skLineSegment(sketch, "E2845", {"start": v(96.94, -27.78) * mm, "end": v(96.8, -27.67) * mm});
            skLineSegment(sketch, "E2846", {"start": v(96.8, -27.67) * mm, "end": v(96.67, -27.56) * mm});
            skLineSegment(sketch, "E2847", {"start": v(96.67, -27.56) * mm, "end": v(96.54, -27.46) * mm});
            skLineSegment(sketch, "E2848", {"start": v(96.54, -27.46) * mm, "end": v(96.4, -27.36) * mm});
            skLineSegment(sketch, "E2849", {"start": v(96.4, -27.36) * mm, "end": v(96.28, -27.25) * mm});
            skLineSegment(sketch, "E2850", {"start": v(96.28, -27.25) * mm, "end": v(96.15, -27.15) * mm});
            skLineSegment(sketch, "E2851", {"start": v(96.15, -27.15) * mm, "end": v(96.02, -27.06) * mm});
            skLineSegment(sketch, "E2852", {"start": v(96.02, -27.06) * mm, "end": v(95.9, -26.96) * mm});
            skLineSegment(sketch, "E2853", {"start": v(95.9, -26.96) * mm, "end": v(95.77, -26.86) * mm});
            skLineSegment(sketch, "E2854", {"start": v(95.77, -26.86) * mm, "end": v(95.64, -26.77) * mm});
            skLineSegment(sketch, "E2855", {"start": v(95.64, -26.77) * mm, "end": v(95.52, -26.68) * mm});
            skLineSegment(sketch, "E2856", {"start": v(95.52, -26.68) * mm, "end": v(95.4, -26.59) * mm});
            skLineSegment(sketch, "E2857", {"start": v(95.4, -26.59) * mm, "end": v(95.27, -26.5) * mm});
            skLineSegment(sketch, "E2858", {"start": v(95.27, -26.5) * mm, "end": v(95.15, -26.41) * mm});
            skLineSegment(sketch, "E2859", {"start": v(95.15, -26.41) * mm, "end": v(95.03, -26.33) * mm});
            skLineSegment(sketch, "E2860", {"start": v(95.03, -26.33) * mm, "end": v(94.91, -26.24) * mm});
            skLineSegment(sketch, "E2861", {"start": v(94.91, -26.24) * mm, "end": v(94.8, -26.16) * mm});
            skLineSegment(sketch, "E2862", {"start": v(94.8, -26.16) * mm, "end": v(94.68, -26.08) * mm});
            skLineSegment(sketch, "E2863", {"start": v(94.68, -26.08) * mm, "end": v(94.56, -26) * mm});
            skLineSegment(sketch, "E2864", {"start": v(94.56, -26) * mm, "end": v(94.45, -25.92) * mm});
            skLineSegment(sketch, "E2865", {"start": v(94.45, -25.92) * mm, "end": v(94.34, -25.85) * mm});
            skLineSegment(sketch, "E2866", {"start": v(94.34, -25.85) * mm, "end": v(94.22, -25.77) * mm});
            skLineSegment(sketch, "E2867", {"start": v(94.22, -25.77) * mm, "end": v(94.11, -25.7) * mm});
            skLineSegment(sketch, "E2868", {"start": v(94.11, -25.7) * mm, "end": v(94, -25.62) * mm});
            skLineSegment(sketch, "E2869", {"start": v(94, -25.62) * mm, "end": v(93.9, -25.55) * mm});
            skLineSegment(sketch, "E2870", {"start": v(93.9, -25.55) * mm, "end": v(93.79, -25.48) * mm});
            skLineSegment(sketch, "E2871", {"start": v(93.79, -25.48) * mm, "end": v(93.97, -24.56) * mm});
            skLineSegment(sketch, "E2872", {"start": v(93.97, -24.56) * mm, "end": v(94.26, -23.66) * mm});
            skLineSegment(sketch, "E2873", {"start": v(94.26, -23.66) * mm, "end": v(94.4, -23.65) * mm});
            skLineSegment(sketch, "E2874", {"start": v(94.4, -23.65) * mm, "end": v(94.52, -23.64) * mm});
            skLineSegment(sketch, "E2875", {"start": v(94.52, -23.64) * mm, "end": v(94.65, -23.63) * mm});
            skLineSegment(sketch, "E2876", {"start": v(94.65, -23.63) * mm, "end": v(94.78, -23.62) * mm});
            skLineSegment(sketch, "E2877", {"start": v(94.78, -23.62) * mm, "end": v(94.92, -23.61) * mm});
            skLineSegment(sketch, "E2878", {"start": v(94.92, -23.61) * mm, "end": v(95.05, -23.6) * mm});
            skLineSegment(sketch, "E2879", {"start": v(95.05, -23.6) * mm, "end": v(95.2, -23.6) * mm});
            skLineSegment(sketch, "E2880", {"start": v(95.2, -23.6) * mm, "end": v(95.33, -23.58) * mm});
            skLineSegment(sketch, "E2881", {"start": v(95.33, -23.58) * mm, "end": v(95.47, -23.56) * mm});
            skLineSegment(sketch, "E2882", {"start": v(95.47, -23.56) * mm, "end": v(95.62, -23.55) * mm});
            skLineSegment(sketch, "E2883", {"start": v(95.62, -23.55) * mm, "end": v(95.76, -23.53) * mm});
            skLineSegment(sketch, "E2884", {"start": v(95.76, -23.53) * mm, "end": v(95.9, -23.52) * mm});
            skLineSegment(sketch, "E2885", {"start": v(95.9, -23.52) * mm, "end": v(96.06, -23.5) * mm});
            skLineSegment(sketch, "E2886", {"start": v(96.06, -23.5) * mm, "end": v(96.2, -23.48) * mm});
            skLineSegment(sketch, "E2887", {"start": v(96.2, -23.48) * mm, "end": v(96.36, -23.47) * mm});
            skLineSegment(sketch, "E2888", {"start": v(96.36, -23.47) * mm, "end": v(96.51, -23.45) * mm});
            skLineSegment(sketch, "E2889", {"start": v(96.51, -23.45) * mm, "end": v(96.67, -23.43) * mm});
            skLineSegment(sketch, "E2890", {"start": v(96.67, -23.43) * mm, "end": v(96.82, -23.4) * mm});
            skLineSegment(sketch, "E2891", {"start": v(96.82, -23.4) * mm, "end": v(96.98, -23.38) * mm});
            skLineSegment(sketch, "E2892", {"start": v(96.98, -23.38) * mm, "end": v(97.14, -23.36) * mm});
            skLineSegment(sketch, "E2893", {"start": v(97.14, -23.36) * mm, "end": v(97.3, -23.33) * mm});
            skLineSegment(sketch, "E2894", {"start": v(97.3, -23.33) * mm, "end": v(97.47, -23.3) * mm});
            skLineSegment(sketch, "E2895", {"start": v(97.47, -23.3) * mm, "end": v(97.63, -23.28) * mm});
            skLineSegment(sketch, "E2896", {"start": v(97.63, -23.28) * mm, "end": v(97.8, -23.26) * mm});
            skLineSegment(sketch, "E2897", {"start": v(97.8, -23.26) * mm, "end": v(97.96, -23.23) * mm});
            skLineSegment(sketch, "E2898", {"start": v(97.96, -23.23) * mm, "end": v(98.13, -23.2) * mm});
            skLineSegment(sketch, "E2899", {"start": v(98.13, -23.2) * mm, "end": v(98.3, -23.17) * mm});
            skLineSegment(sketch, "E2900", {"start": v(98.3, -23.17) * mm, "end": v(98.48, -23.14) * mm});
            skLineSegment(sketch, "E2901", {"start": v(98.48, -23.14) * mm, "end": v(98.65, -23.1) * mm});
            skLineSegment(sketch, "E2902", {"start": v(98.65, -23.1) * mm, "end": v(98.83, -23.07) * mm});
            skLineSegment(sketch, "E2903", {"start": v(98.83, -23.07) * mm, "end": v(99, -23.04) * mm});
            skLineSegment(sketch, "E2904", {"start": v(99, -23.04) * mm, "end": v(99.19, -23) * mm});
            skLineSegment(sketch, "E2905", {"start": v(99.19, -23) * mm, "end": v(99.37, -22.97) * mm});
            skLineSegment(sketch, "E2906", {"start": v(99.37, -22.97) * mm, "end": v(99.55, -22.93) * mm});
            skLineSegment(sketch, "E2907", {"start": v(99.55, -22.93) * mm, "end": v(99.73, -22.89) * mm});
            skLineSegment(sketch, "E2908", {"start": v(99.73, -22.89) * mm, "end": v(99.92, -22.85) * mm});
            skLineSegment(sketch, "E2909", {"start": v(99.92, -22.85) * mm, "end": v(99.94, -22.77) * mm});
            skLineSegment(sketch, "E2910", {"start": v(99.94, -22.77) * mm, "end": v(100.28, -21.24) * mm});
            skLineSegment(sketch, "E2911", {"start": v(100.28, -21.24) * mm, "end": v(100.3, -21.15) * mm});
            skLineSegment(sketch, "E2912", {"start": v(100.3, -21.15) * mm, "end": v(100.14, -21.04) * mm});
            skLineSegment(sketch, "E2913", {"start": v(100.14, -21.04) * mm, "end": v(99.99, -20.93) * mm});
            skLineSegment(sketch, "E2914", {"start": v(99.99, -20.93) * mm, "end": v(99.84, -20.82) * mm});
            skLineSegment(sketch, "E2915", {"start": v(99.84, -20.82) * mm, "end": v(99.7, -20.7) * mm});
            skLineSegment(sketch, "E2916", {"start": v(99.7, -20.7) * mm, "end": v(99.54, -20.6) * mm});
            skLineSegment(sketch, "E2917", {"start": v(99.54, -20.6) * mm, "end": v(99.4, -20.5) * mm});
            skLineSegment(sketch, "E2918", {"start": v(99.4, -20.5) * mm, "end": v(99.25, -20.4) * mm});
            skLineSegment(sketch, "E2919", {"start": v(99.25, -20.4) * mm, "end": v(99.1, -20.29) * mm});
            skLineSegment(sketch, "E2920", {"start": v(99.1, -20.29) * mm, "end": v(98.96, -20.19) * mm});
            skLineSegment(sketch, "E2921", {"start": v(98.96, -20.19) * mm, "end": v(98.82, -20.09) * mm});
            skLineSegment(sketch, "E2922", {"start": v(98.82, -20.09) * mm, "end": v(98.68, -20) * mm});
            skLineSegment(sketch, "E2923", {"start": v(98.68, -20) * mm, "end": v(98.54, -19.9) * mm});
            skLineSegment(sketch, "E2924", {"start": v(98.54, -19.9) * mm, "end": v(98.4, -19.8) * mm});
            skLineSegment(sketch, "E2925", {"start": v(98.4, -19.8) * mm, "end": v(98.26, -19.7) * mm});
            skLineSegment(sketch, "E2926", {"start": v(98.26, -19.7) * mm, "end": v(98.12, -19.62) * mm});
            skLineSegment(sketch, "E2927", {"start": v(98.12, -19.62) * mm, "end": v(97.98, -19.53) * mm});
            skLineSegment(sketch, "E2928", {"start": v(97.98, -19.53) * mm, "end": v(97.85, -19.44) * mm});
            skLineSegment(sketch, "E2929", {"start": v(97.85, -19.44) * mm, "end": v(97.71, -19.35) * mm});
            skLineSegment(sketch, "E2930", {"start": v(97.71, -19.35) * mm, "end": v(97.58, -19.27) * mm});
            skLineSegment(sketch, "E2931", {"start": v(97.58, -19.27) * mm, "end": v(97.45, -19.18) * mm});
            skLineSegment(sketch, "E2932", {"start": v(97.45, -19.18) * mm, "end": v(97.32, -19.1) * mm});
            skLineSegment(sketch, "E2933", {"start": v(97.32, -19.1) * mm, "end": v(97.19, -19.02) * mm});
            skLineSegment(sketch, "E2934", {"start": v(97.19, -19.02) * mm, "end": v(97.06, -18.94) * mm});
            skLineSegment(sketch, "E2935", {"start": v(97.06, -18.94) * mm, "end": v(96.93, -18.87) * mm});
            skLineSegment(sketch, "E2936", {"start": v(96.93, -18.87) * mm, "end": v(96.8, -18.79) * mm});
            skLineSegment(sketch, "E2937", {"start": v(96.8, -18.79) * mm, "end": v(96.68, -18.72) * mm});
            skLineSegment(sketch, "E2938", {"start": v(96.68, -18.72) * mm, "end": v(96.56, -18.64) * mm});
            skLineSegment(sketch, "E2939", {"start": v(96.56, -18.64) * mm, "end": v(96.43, -18.57) * mm});
            skLineSegment(sketch, "E2940", {"start": v(96.43, -18.57) * mm, "end": v(96.31, -18.5) * mm});
            skLineSegment(sketch, "E2941", {"start": v(96.31, -18.5) * mm, "end": v(96.2, -18.43) * mm});
            skLineSegment(sketch, "E2942", {"start": v(96.2, -18.43) * mm, "end": v(96.07, -18.36) * mm});
            skLineSegment(sketch, "E2943", {"start": v(96.07, -18.36) * mm, "end": v(95.95, -18.3) * mm});
            skLineSegment(sketch, "E2944", {"start": v(95.95, -18.3) * mm, "end": v(95.84, -18.23) * mm});
            skLineSegment(sketch, "E2945", {"start": v(95.84, -18.23) * mm, "end": v(95.72, -18.17) * mm});
            skLineSegment(sketch, "E2946", {"start": v(95.72, -18.17) * mm, "end": v(95.6, -18.1) * mm});
            skLineSegment(sketch, "E2947", {"start": v(95.6, -18.1) * mm, "end": v(95.5, -18.05) * mm});
            skLineSegment(sketch, "E2948", {"start": v(95.5, -18.05) * mm, "end": v(95.6, -17.1) * mm});
            skLineSegment(sketch, "E2949", {"start": v(95.6, -17.1) * mm, "end": v(95.83, -16.2) * mm});
            skLineSegment(sketch, "E2950", {"start": v(95.83, -16.2) * mm, "end": v(95.95, -16.17) * mm});
            skLineSegment(sketch, "E2951", {"start": v(95.95, -16.17) * mm, "end": v(96.08, -16.15) * mm});
            skLineSegment(sketch, "E2952", {"start": v(96.08, -16.15) * mm, "end": v(96.21, -16.13) * mm});
            skLineSegment(sketch, "E2953", {"start": v(96.21, -16.13) * mm, "end": v(96.35, -16.11) * mm});
            skLineSegment(sketch, "E2954", {"start": v(96.35, -16.11) * mm, "end": v(96.48, -16.1) * mm});
            skLineSegment(sketch, "E2955", {"start": v(96.48, -16.1) * mm, "end": v(96.61, -16.07) * mm});
            skLineSegment(sketch, "E2956", {"start": v(96.61, -16.07) * mm, "end": v(96.75, -16.05) * mm});
            skLineSegment(sketch, "E2957", {"start": v(96.75, -16.05) * mm, "end": v(96.89, -16.02) * mm});
            skLineSegment(sketch, "E2958", {"start": v(96.89, -16.02) * mm, "end": v(97.03, -16) * mm});
            skLineSegment(sketch, "E2959", {"start": v(97.03, -16) * mm, "end": v(97.17, -15.97) * mm});
            skLineSegment(sketch, "E2960", {"start": v(97.17, -15.97) * mm, "end": v(97.31, -15.95) * mm});
            skLineSegment(sketch, "E2961", {"start": v(97.31, -15.95) * mm, "end": v(97.46, -15.92) * mm});
            skLineSegment(sketch, "E2962", {"start": v(97.46, -15.92) * mm, "end": v(97.6, -15.9) * mm});
            skLineSegment(sketch, "E2963", {"start": v(97.6, -15.9) * mm, "end": v(97.75, -15.86) * mm});
            skLineSegment(sketch, "E2964", {"start": v(97.75, -15.86) * mm, "end": v(97.9, -15.83) * mm});
            skLineSegment(sketch, "E2965", {"start": v(97.9, -15.83) * mm, "end": v(98.05, -15.8) * mm});
            skLineSegment(sketch, "E2966", {"start": v(98.05, -15.8) * mm, "end": v(98.2, -15.77) * mm});
            skLineSegment(sketch, "E2967", {"start": v(98.2, -15.77) * mm, "end": v(98.36, -15.74) * mm});
            skLineSegment(sketch, "E2968", {"start": v(98.36, -15.74) * mm, "end": v(98.52, -15.7) * mm});
            skLineSegment(sketch, "E2969", {"start": v(98.52, -15.7) * mm, "end": v(98.67, -15.67) * mm});
            skLineSegment(sketch, "E2970", {"start": v(98.67, -15.67) * mm, "end": v(98.83, -15.63) * mm});
            skLineSegment(sketch, "E2971", {"start": v(98.83, -15.63) * mm, "end": v(99, -15.6) * mm});
            skLineSegment(sketch, "E2972", {"start": v(99, -15.6) * mm, "end": v(99.16, -15.55) * mm});
            skLineSegment(sketch, "E2973", {"start": v(99.16, -15.55) * mm, "end": v(99.32, -15.51) * mm});
            skLineSegment(sketch, "E2974", {"start": v(99.32, -15.51) * mm, "end": v(99.49, -15.47) * mm});
            skLineSegment(sketch, "E2975", {"start": v(99.49, -15.47) * mm, "end": v(99.65, -15.43) * mm});
            skLineSegment(sketch, "E2976", {"start": v(99.65, -15.43) * mm, "end": v(99.82, -15.39) * mm});
            skLineSegment(sketch, "E2977", {"start": v(99.82, -15.39) * mm, "end": v(100, -15.34) * mm});
            skLineSegment(sketch, "E2978", {"start": v(100, -15.34) * mm, "end": v(100.16, -15.3) * mm});
            skLineSegment(sketch, "E2979", {"start": v(100.16, -15.3) * mm, "end": v(100.33, -15.25) * mm});
            skLineSegment(sketch, "E2980", {"start": v(100.33, -15.25) * mm, "end": v(100.5, -15.2) * mm});
            skLineSegment(sketch, "E2981", {"start": v(100.5, -15.2) * mm, "end": v(100.68, -15.15) * mm});
            skLineSegment(sketch, "E2982", {"start": v(100.68, -15.15) * mm, "end": v(100.86, -15.1) * mm});
            skLineSegment(sketch, "E2983", {"start": v(100.86, -15.1) * mm, "end": v(101.04, -15.05) * mm});
            skLineSegment(sketch, "E2984", {"start": v(101.04, -15.05) * mm, "end": v(101.22, -15) * mm});
            skLineSegment(sketch, "E2985", {"start": v(101.22, -15) * mm, "end": v(101.4, -14.94) * mm});
            skLineSegment(sketch, "E2986", {"start": v(101.4, -14.94) * mm, "end": v(101.42, -14.86) * mm});
            skLineSegment(sketch, "E2987", {"start": v(101.42, -14.86) * mm, "end": v(101.63, -13.3) * mm});
            skLineSegment(sketch, "E2988", {"start": v(101.63, -13.3) * mm, "end": v(101.64, -13.22) * mm});
            skLineSegment(sketch, "E2989", {"start": v(101.64, -13.22) * mm, "end": v(101.48, -13.12) * mm});
            skLineSegment(sketch, "E2990", {"start": v(101.48, -13.12) * mm, "end": v(101.32, -13.02) * mm});
            skLineSegment(sketch, "E2991", {"start": v(101.32, -13.02) * mm, "end": v(101.16, -12.92) * mm});
            skLineSegment(sketch, "E2992", {"start": v(101.16, -12.92) * mm, "end": v(101, -12.82) * mm});
            skLineSegment(sketch, "E2993", {"start": v(101, -12.82) * mm, "end": v(100.85, -12.73) * mm});
            skLineSegment(sketch, "E2994", {"start": v(100.85, -12.73) * mm, "end": v(100.7, -12.63) * mm});
            skLineSegment(sketch, "E2995", {"start": v(100.7, -12.63) * mm, "end": v(100.54, -12.54) * mm});
            skLineSegment(sketch, "E2996", {"start": v(100.54, -12.54) * mm, "end": v(100.4, -12.45) * mm});
            skLineSegment(sketch, "E2997", {"start": v(100.4, -12.45) * mm, "end": v(100.24, -12.36) * mm});
            skLineSegment(sketch, "E2998", {"start": v(100.24, -12.36) * mm, "end": v(100.09, -12.27) * mm});
            skLineSegment(sketch, "E2999", {"start": v(100.09, -12.27) * mm, "end": v(99.94, -12.19) * mm});
            skLineSegment(sketch, "E3000", {"start": v(99.94, -12.19) * mm, "end": v(99.8, -12.1) * mm});
            skLineSegment(sketch, "E3001", {"start": v(99.8, -12.1) * mm, "end": v(99.65, -12.02) * mm});
            skLineSegment(sketch, "E3002", {"start": v(99.65, -12.02) * mm, "end": v(99.5, -11.94) * mm});
            skLineSegment(sketch, "E3003", {"start": v(99.5, -11.94) * mm, "end": v(99.36, -11.86) * mm});
            skLineSegment(sketch, "E3004", {"start": v(99.36, -11.86) * mm, "end": v(99.21, -11.78) * mm});
            skLineSegment(sketch, "E3005", {"start": v(99.21, -11.78) * mm, "end": v(99.07, -11.7) * mm});
            skLineSegment(sketch, "E3006", {"start": v(99.07, -11.7) * mm, "end": v(98.93, -11.63) * mm});
            skLineSegment(sketch, "E3007", {"start": v(98.93, -11.63) * mm, "end": v(98.8, -11.55) * mm});
            skLineSegment(sketch, "E3008", {"start": v(98.8, -11.55) * mm, "end": v(98.65, -11.48) * mm});
            skLineSegment(sketch, "E3009", {"start": v(98.65, -11.48) * mm, "end": v(98.52, -11.4) * mm});
            skLineSegment(sketch, "E3010", {"start": v(98.52, -11.4) * mm, "end": v(98.38, -11.34) * mm});
            skLineSegment(sketch, "E3011", {"start": v(98.38, -11.34) * mm, "end": v(98.25, -11.27) * mm});
            skLineSegment(sketch, "E3012", {"start": v(98.25, -11.27) * mm, "end": v(98.11, -11.2) * mm});
            skLineSegment(sketch, "E3013", {"start": v(98.11, -11.2) * mm, "end": v(97.98, -11.14) * mm});
            skLineSegment(sketch, "E3014", {"start": v(97.98, -11.14) * mm, "end": v(97.85, -11.07) * mm});
            skLineSegment(sketch, "E3015", {"start": v(97.85, -11.07) * mm, "end": v(97.72, -11) * mm});
            skLineSegment(sketch, "E3016", {"start": v(97.72, -11) * mm, "end": v(97.6, -10.95) * mm});
            skLineSegment(sketch, "E3017", {"start": v(97.6, -10.95) * mm, "end": v(97.47, -10.89) * mm});
            skLineSegment(sketch, "E3018", {"start": v(97.47, -10.89) * mm, "end": v(97.34, -10.83) * mm});
            skLineSegment(sketch, "E3019", {"start": v(97.34, -10.83) * mm, "end": v(97.22, -10.77) * mm});
            skLineSegment(sketch, "E3020", {"start": v(97.22, -10.77) * mm, "end": v(97.1, -10.71) * mm});
            skLineSegment(sketch, "E3021", {"start": v(97.1, -10.71) * mm, "end": v(96.97, -10.66) * mm});
            skLineSegment(sketch, "E3022", {"start": v(96.97, -10.66) * mm, "end": v(96.85, -10.6) * mm});
            skLineSegment(sketch, "E3023", {"start": v(96.85, -10.6) * mm, "end": v(96.73, -10.55) * mm});
            skLineSegment(sketch, "E3024", {"start": v(96.73, -10.55) * mm, "end": v(96.62, -10.5) * mm});
            skLineSegment(sketch, "E3025", {"start": v(96.62, -10.5) * mm, "end": v(96.65, -9.56) * mm});
            skLineSegment(sketch, "E3026", {"start": v(96.65, -9.56) * mm, "end": v(96.8, -8.62) * mm});
            skLineSegment(sketch, "E3027", {"start": v(96.8, -8.62) * mm, "end": v(96.93, -8.6) * mm});
            skLineSegment(sketch, "E3028", {"start": v(96.93, -8.6) * mm, "end": v(97.05, -8.57) * mm});
            skLineSegment(sketch, "E3029", {"start": v(97.05, -8.57) * mm, "end": v(97.18, -8.54) * mm});
            skLineSegment(sketch, "E3030", {"start": v(97.18, -8.54) * mm, "end": v(97.31, -8.5) * mm});
            skLineSegment(sketch, "E3031", {"start": v(97.31, -8.5) * mm, "end": v(97.44, -8.47) * mm});
            skLineSegment(sketch, "E3032", {"start": v(97.44, -8.47) * mm, "end": v(97.58, -8.44) * mm});
            skLineSegment(sketch, "E3033", {"start": v(97.58, -8.44) * mm, "end": v(97.71, -8.4) * mm});
            skLineSegment(sketch, "E3034", {"start": v(97.71, -8.4) * mm, "end": v(97.85, -8.37) * mm});
            skLineSegment(sketch, "E3035", {"start": v(97.85, -8.37) * mm, "end": v(97.98, -8.34) * mm});
            skLineSegment(sketch, "E3036", {"start": v(97.98, -8.34) * mm, "end": v(98.12, -8.3) * mm});
            skLineSegment(sketch, "E3037", {"start": v(98.12, -8.3) * mm, "end": v(98.26, -8.26) * mm});
            skLineSegment(sketch, "E3038", {"start": v(98.26, -8.26) * mm, "end": v(98.4, -8.23) * mm});
            skLineSegment(sketch, "E3039", {"start": v(98.4, -8.23) * mm, "end": v(98.55, -8.19) * mm});
            skLineSegment(sketch, "E3040", {"start": v(98.55, -8.19) * mm, "end": v(98.7, -8.14) * mm});
            skLineSegment(sketch, "E3041", {"start": v(98.7, -8.14) * mm, "end": v(98.84, -8.1) * mm});
            skLineSegment(sketch, "E3042", {"start": v(98.84, -8.1) * mm, "end": v(99, -8.06) * mm});
            skLineSegment(sketch, "E3043", {"start": v(99, -8.06) * mm, "end": v(99.14, -8.02) * mm});
            skLineSegment(sketch, "E3044", {"start": v(99.14, -8.02) * mm, "end": v(99.3, -7.97) * mm});
            skLineSegment(sketch, "E3045", {"start": v(99.3, -7.97) * mm, "end": v(99.44, -7.92) * mm});
            skLineSegment(sketch, "E3046", {"start": v(99.44, -7.92) * mm, "end": v(99.6, -7.88) * mm});
            skLineSegment(sketch, "E3047", {"start": v(99.6, -7.88) * mm, "end": v(99.75, -7.83) * mm});
            skLineSegment(sketch, "E3048", {"start": v(99.75, -7.83) * mm, "end": v(99.91, -7.78) * mm});
            skLineSegment(sketch, "E3049", {"start": v(99.91, -7.78) * mm, "end": v(100.07, -7.72) * mm});
            skLineSegment(sketch, "E3050", {"start": v(100.07, -7.72) * mm, "end": v(100.23, -7.67) * mm});
            skLineSegment(sketch, "E3051", {"start": v(100.23, -7.67) * mm, "end": v(100.4, -7.62) * mm});
            skLineSegment(sketch, "E3052", {"start": v(100.4, -7.62) * mm, "end": v(100.56, -7.56) * mm});
            skLineSegment(sketch, "E3053", {"start": v(100.56, -7.56) * mm, "end": v(100.72, -7.5) * mm});
            skLineSegment(sketch, "E3054", {"start": v(100.72, -7.5) * mm, "end": v(100.89, -7.45) * mm});
            skLineSegment(sketch, "E3055", {"start": v(100.89, -7.45) * mm, "end": v(101.05, -7.39) * mm});
            skLineSegment(sketch, "E3056", {"start": v(101.05, -7.39) * mm, "end": v(101.22, -7.33) * mm});
            skLineSegment(sketch, "E3057", {"start": v(101.22, -7.33) * mm, "end": v(101.4, -7.27) * mm});
            skLineSegment(sketch, "E3058", {"start": v(101.4, -7.27) * mm, "end": v(101.56, -7.2) * mm});
            skLineSegment(sketch, "E3059", {"start": v(101.56, -7.2) * mm, "end": v(101.74, -7.14) * mm});
            skLineSegment(sketch, "E3060", {"start": v(101.74, -7.14) * mm, "end": v(101.91, -7.07) * mm});
            skLineSegment(sketch, "E3061", {"start": v(101.91, -7.07) * mm, "end": v(102.09, -7) * mm});
            skLineSegment(sketch, "E3062", {"start": v(102.09, -7) * mm, "end": v(102.26, -6.94) * mm});
            skLineSegment(sketch, "E3063", {"start": v(102.26, -6.94) * mm, "end": v(102.27, -6.86) * mm});
            skLineSegment(sketch, "E3064", {"start": v(102.27, -6.86) * mm, "end": v(102.36, -5.29) * mm});
            skLineSegment(sketch, "E3065", {"start": v(102.36, -5.29) * mm, "end": v(102.37, -5.2) * mm});
            skLineSegment(sketch, "E3066", {"start": v(102.37, -5.2) * mm, "end": v(102.2, -5.12) * mm});
            skLineSegment(sketch, "E3067", {"start": v(102.2, -5.12) * mm, "end": v(102.03, -5.03) * mm});
            skLineSegment(sketch, "E3068", {"start": v(102.03, -5.03) * mm, "end": v(101.87, -4.94) * mm});
            skLineSegment(sketch, "E3069", {"start": v(101.87, -4.94) * mm, "end": v(101.7, -4.86) * mm});
            skLineSegment(sketch, "E3070", {"start": v(101.7, -4.86) * mm, "end": v(101.54, -4.78) * mm});
            skLineSegment(sketch, "E3071", {"start": v(101.54, -4.78) * mm, "end": v(101.38, -4.7) * mm});
            skLineSegment(sketch, "E3072", {"start": v(101.38, -4.7) * mm, "end": v(101.22, -4.61) * mm});
            skLineSegment(sketch, "E3073", {"start": v(101.22, -4.61) * mm, "end": v(101.06, -4.54) * mm});
            skLineSegment(sketch, "E3074", {"start": v(101.06, -4.54) * mm, "end": v(100.9, -4.46) * mm});
            skLineSegment(sketch, "E3075", {"start": v(100.9, -4.46) * mm, "end": v(100.74, -4.38) * mm});
            skLineSegment(sketch, "E3076", {"start": v(100.74, -4.38) * mm, "end": v(100.59, -4.3) * mm});
            skLineSegment(sketch, "E3077", {"start": v(100.59, -4.3) * mm, "end": v(100.43, -4.24) * mm});
            skLineSegment(sketch, "E3078", {"start": v(100.43, -4.24) * mm, "end": v(100.28, -4.16) * mm});
            skLineSegment(sketch, "E3079", {"start": v(100.28, -4.16) * mm, "end": v(100.13, -4.1) * mm});
            skLineSegment(sketch, "E3080", {"start": v(100.13, -4.1) * mm, "end": v(99.98, -4.03) * mm});
            skLineSegment(sketch, "E3081", {"start": v(99.98, -4.03) * mm, "end": v(99.83, -3.96) * mm});
            skLineSegment(sketch, "E3082", {"start": v(99.83, -3.96) * mm, "end": v(99.68, -3.9) * mm});
            skLineSegment(sketch, "E3083", {"start": v(99.68, -3.9) * mm, "end": v(99.54, -3.83) * mm});
            skLineSegment(sketch, "E3084", {"start": v(99.54, -3.83) * mm, "end": v(99.4, -3.77) * mm});
            skLineSegment(sketch, "E3085", {"start": v(99.4, -3.77) * mm, "end": v(99.25, -3.7) * mm});
            skLineSegment(sketch, "E3086", {"start": v(99.25, -3.7) * mm, "end": v(99.1, -3.64) * mm});
            skLineSegment(sketch, "E3087", {"start": v(99.1, -3.64) * mm, "end": v(98.97, -3.58) * mm});
            skLineSegment(sketch, "E3088", {"start": v(98.97, -3.58) * mm, "end": v(98.83, -3.53) * mm});
            skLineSegment(sketch, "E3089", {"start": v(98.83, -3.53) * mm, "end": v(98.69, -3.47) * mm});
            skLineSegment(sketch, "E3090", {"start": v(98.69, -3.47) * mm, "end": v(98.55, -3.41) * mm});
            skLineSegment(sketch, "E3091", {"start": v(98.55, -3.41) * mm, "end": v(98.42, -3.36) * mm});
            skLineSegment(sketch, "E3092", {"start": v(98.42, -3.36) * mm, "end": v(98.28, -3.3) * mm});
            skLineSegment(sketch, "E3093", {"start": v(98.28, -3.3) * mm, "end": v(98.15, -3.26) * mm});
            skLineSegment(sketch, "E3094", {"start": v(98.15, -3.26) * mm, "end": v(98.02, -3.2) * mm});
            skLineSegment(sketch, "E3095", {"start": v(98.02, -3.2) * mm, "end": v(97.9, -3.16) * mm});
            skLineSegment(sketch, "E3096", {"start": v(97.9, -3.16) * mm, "end": v(97.76, -3.1) * mm});
            skLineSegment(sketch, "E3097", {"start": v(97.76, -3.1) * mm, "end": v(97.64, -3.06) * mm});
            skLineSegment(sketch, "E3098", {"start": v(97.64, -3.06) * mm, "end": v(97.51, -3.02) * mm});
            skLineSegment(sketch, "E3099", {"start": v(97.51, -3.02) * mm, "end": v(97.39, -2.97) * mm});
            skLineSegment(sketch, "E3100", {"start": v(97.39, -2.97) * mm, "end": v(97.26, -2.93) * mm});
            skLineSegment(sketch, "E3101", {"start": v(97.26, -2.93) * mm, "end": v(97.14, -2.89) * mm});
            skLineSegment(sketch, "E3102", {"start": v(97.14, -2.89) * mm, "end": v(97.1, -1.94) * mm});
            skLineSegment(sketch, "E3103", {"start": v(97.1, -1.94) * mm, "end": v(97.18, -1) * mm});
            skLineSegment(sketch, "E3104", {"start": v(97.18, -1) * mm, "end": v(97.3, -0.96) * mm});
            skLineSegment(sketch, "E3105", {"start": v(97.3, -0.96) * mm, "end": v(97.43, -0.92) * mm});
            skLineSegment(sketch, "E3106", {"start": v(97.43, -0.92) * mm, "end": v(97.55, -0.88) * mm});
            skLineSegment(sketch, "E3107", {"start": v(97.55, -0.88) * mm, "end": v(97.68, -0.84) * mm});
            skLineSegment(sketch, "E3108", {"start": v(97.68, -0.84) * mm, "end": v(97.8, -0.8) * mm});
            skLineSegment(sketch, "E3109", {"start": v(97.8, -0.8) * mm, "end": v(97.94, -0.76) * mm});
            skLineSegment(sketch, "E3110", {"start": v(97.94, -0.76) * mm, "end": v(98.07, -0.72) * mm});
            skLineSegment(sketch, "E3111", {"start": v(98.07, -0.72) * mm, "end": v(98.2, -0.67) * mm});
            skLineSegment(sketch, "E3112", {"start": v(98.2, -0.67) * mm, "end": v(98.34, -0.62) * mm});
            skLineSegment(sketch, "E3113", {"start": v(98.34, -0.62) * mm, "end": v(98.47, -0.58) * mm});
            skLineSegment(sketch, "E3114", {"start": v(98.47, -0.58) * mm, "end": v(98.6, -0.53) * mm});
            skLineSegment(sketch, "E3115", {"start": v(98.6, -0.53) * mm, "end": v(98.75, -0.48) * mm});
            skLineSegment(sketch, "E3116", {"start": v(98.75, -0.48) * mm, "end": v(98.89, -0.43) * mm});
            skLineSegment(sketch, "E3117", {"start": v(98.89, -0.43) * mm, "end": v(99.03, -0.38) * mm});
            skLineSegment(sketch, "E3118", {"start": v(99.03, -0.38) * mm, "end": v(99.17, -0.32) * mm});
            skLineSegment(sketch, "E3119", {"start": v(99.17, -0.32) * mm, "end": v(99.32, -0.27) * mm});
            skLineSegment(sketch, "E3120", {"start": v(99.32, -0.27) * mm, "end": v(99.46, -0.21) * mm});
            skLineSegment(sketch, "E3121", {"start": v(99.46, -0.21) * mm, "end": v(99.61, -0.15) * mm});
            skLineSegment(sketch, "E3122", {"start": v(99.61, -0.15) * mm, "end": v(99.76, -0.1) * mm});
            skLineSegment(sketch, "E3123", {"start": v(99.76, -0.1) * mm, "end": v(99.9, -0.04) * mm});
            skLineSegment(sketch, "E3124", {"start": v(99.9, -0.04) * mm, "end": v(100.06, 0.02) * mm});
            skLineSegment(sketch, "E3125", {"start": v(100.06, 0.02) * mm, "end": v(100.21, 0.09) * mm});
            skLineSegment(sketch, "E3126", {"start": v(100.21, 0.09) * mm, "end": v(100.37, 0.15) * mm});
            skLineSegment(sketch, "E3127", {"start": v(100.37, 0.15) * mm, "end": v(100.52, 0.22) * mm});
            skLineSegment(sketch, "E3128", {"start": v(100.52, 0.22) * mm, "end": v(100.68, 0.28) * mm});
            skLineSegment(sketch, "E3129", {"start": v(100.68, 0.28) * mm, "end": v(100.84, 0.35) * mm});
            skLineSegment(sketch, "E3130", {"start": v(100.84, 0.35) * mm, "end": v(101, 0.42) * mm});
            skLineSegment(sketch, "E3131", {"start": v(101, 0.42) * mm, "end": v(101.16, 0.5) * mm});
            skLineSegment(sketch, "E3132", {"start": v(101.16, 0.5) * mm, "end": v(101.32, 0.56) * mm});
            skLineSegment(sketch, "E3133", {"start": v(101.32, 0.56) * mm, "end": v(101.48, 0.64) * mm});
            skLineSegment(sketch, "E3134", {"start": v(101.48, 0.64) * mm, "end": v(101.65, 0.71) * mm});
            skLineSegment(sketch, "E3135", {"start": v(101.65, 0.71) * mm, "end": v(101.82, 0.79) * mm});
            skLineSegment(sketch, "E3136", {"start": v(101.82, 0.79) * mm, "end": v(101.98, 0.87) * mm});
            skLineSegment(sketch, "E3137", {"start": v(101.98, 0.87) * mm, "end": v(102.15, 0.94) * mm});
            skLineSegment(sketch, "E3138", {"start": v(102.15, 0.94) * mm, "end": v(102.32, 1.03) * mm});
            skLineSegment(sketch, "E3139", {"start": v(102.32, 1.03) * mm, "end": v(102.5, 1.1) * mm});
            skLineSegment(sketch, "E3140", {"start": v(102.5, 1.1) * mm, "end": v(102.5, 1.19) * mm});
            skLineSegment(sketch, "E3141", {"start": v(102.5, 1.19) * mm, "end": v(102.46, 2.76) * mm});
            skLineSegment(sketch, "E3142", {"start": v(102.46, 2.76) * mm, "end": v(102.46, 2.84) * mm});
            skLineSegment(sketch, "E3143", {"start": v(102.46, 2.84) * mm, "end": v(102.28, 2.92) * mm});
            skLineSegment(sketch, "E3144", {"start": v(102.28, 2.92) * mm, "end": v(102.11, 3) * mm});
            skLineSegment(sketch, "E3145", {"start": v(102.11, 3) * mm, "end": v(101.94, 3.06) * mm});
            skLineSegment(sketch, "E3146", {"start": v(101.94, 3.06) * mm, "end": v(101.77, 3.14) * mm});
            skLineSegment(sketch, "E3147", {"start": v(101.77, 3.14) * mm, "end": v(101.6, 3.2) * mm});
            skLineSegment(sketch, "E3148", {"start": v(101.6, 3.2) * mm, "end": v(101.43, 3.27) * mm});
            skLineSegment(sketch, "E3149", {"start": v(101.43, 3.27) * mm, "end": v(101.27, 3.34) * mm});
            skLineSegment(sketch, "E3150", {"start": v(101.27, 3.34) * mm, "end": v(101.1, 3.4) * mm});
            skLineSegment(sketch, "E3151", {"start": v(101.1, 3.4) * mm, "end": v(100.94, 3.47) * mm});
            skLineSegment(sketch, "E3152", {"start": v(100.94, 3.47) * mm, "end": v(100.78, 3.54) * mm});
            skLineSegment(sketch, "E3153", {"start": v(100.78, 3.54) * mm, "end": v(100.62, 3.6) * mm});
            skLineSegment(sketch, "E3154", {"start": v(100.62, 3.6) * mm, "end": v(100.46, 3.66) * mm});
            skLineSegment(sketch, "E3155", {"start": v(100.46, 3.66) * mm, "end": v(100.3, 3.72) * mm});
            skLineSegment(sketch, "E3156", {"start": v(100.3, 3.72) * mm, "end": v(100.14, 3.77) * mm});
            skLineSegment(sketch, "E3157", {"start": v(100.14, 3.77) * mm, "end": v(99.99, 3.83) * mm});
            skLineSegment(sketch, "E3158", {"start": v(99.99, 3.83) * mm, "end": v(99.83, 3.89) * mm});
            skLineSegment(sketch, "E3159", {"start": v(99.83, 3.89) * mm, "end": v(99.68, 3.94) * mm});
            skLineSegment(sketch, "E3160", {"start": v(99.68, 3.94) * mm, "end": v(99.53, 4) * mm});
            skLineSegment(sketch, "E3161", {"start": v(99.53, 4) * mm, "end": v(99.38, 4.04) * mm});
            skLineSegment(sketch, "E3162", {"start": v(99.38, 4.04) * mm, "end": v(99.23, 4.1) * mm});
            skLineSegment(sketch, "E3163", {"start": v(99.23, 4.1) * mm, "end": v(99.09, 4.14) * mm});
            skLineSegment(sketch, "E3164", {"start": v(99.09, 4.14) * mm, "end": v(98.94, 4.2) * mm});
            skLineSegment(sketch, "E3165", {"start": v(98.94, 4.2) * mm, "end": v(98.8, 4.24) * mm});
            skLineSegment(sketch, "E3166", {"start": v(98.8, 4.24) * mm, "end": v(98.66, 4.28) * mm});
            skLineSegment(sketch, "E3167", {"start": v(98.66, 4.28) * mm, "end": v(98.52, 4.33) * mm});
            skLineSegment(sketch, "E3168", {"start": v(98.52, 4.33) * mm, "end": v(98.38, 4.37) * mm});
            skLineSegment(sketch, "E3169", {"start": v(98.38, 4.37) * mm, "end": v(98.24, 4.41) * mm});
            skLineSegment(sketch, "E3170", {"start": v(98.24, 4.41) * mm, "end": v(98.1, 4.45) * mm});
            skLineSegment(sketch, "E3171", {"start": v(98.1, 4.45) * mm, "end": v(97.97, 4.5) * mm});
            skLineSegment(sketch, "E3172", {"start": v(97.97, 4.5) * mm, "end": v(97.84, 4.53) * mm});
            skLineSegment(sketch, "E3173", {"start": v(97.84, 4.53) * mm, "end": v(97.7, 4.57) * mm});
            skLineSegment(sketch, "E3174", {"start": v(97.7, 4.57) * mm, "end": v(97.57, 4.6) * mm});
            skLineSegment(sketch, "E3175", {"start": v(97.57, 4.6) * mm, "end": v(97.45, 4.64) * mm});
            skLineSegment(sketch, "E3176", {"start": v(97.45, 4.64) * mm, "end": v(97.32, 4.68) * mm});
            skLineSegment(sketch, "E3177", {"start": v(97.32, 4.68) * mm, "end": v(97.2, 4.71) * mm});
            skLineSegment(sketch, "E3178", {"start": v(97.2, 4.71) * mm, "end": v(97.07, 4.74) * mm});
            skLineSegment(sketch, "E3179", {"start": v(97.07, 4.74) * mm, "end": v(96.96, 5.68) * mm});
            skLineSegment(sketch, "E3180", {"start": v(96.96, 5.68) * mm, "end": v(96.96, 6.63) * mm});
            skLineSegment(sketch, "E3181", {"start": v(96.96, 6.63) * mm, "end": v(97.08, 6.67) * mm});
            skLineSegment(sketch, "E3182", {"start": v(97.08, 6.67) * mm, "end": v(97.2, 6.72) * mm});
            skLineSegment(sketch, "E3183", {"start": v(97.2, 6.72) * mm, "end": v(97.32, 6.77) * mm});
            skLineSegment(sketch, "E3184", {"start": v(97.32, 6.77) * mm, "end": v(97.44, 6.82) * mm});
            skLineSegment(sketch, "E3185", {"start": v(97.44, 6.82) * mm, "end": v(97.57, 6.87) * mm});
            skLineSegment(sketch, "E3186", {"start": v(97.57, 6.87) * mm, "end": v(97.7, 6.93) * mm});
            skLineSegment(sketch, "E3187", {"start": v(97.7, 6.93) * mm, "end": v(97.82, 6.98) * mm});
            skLineSegment(sketch, "E3188", {"start": v(97.82, 6.98) * mm, "end": v(97.95, 7.04) * mm});
            skLineSegment(sketch, "E3189", {"start": v(97.95, 7.04) * mm, "end": v(98.08, 7.1) * mm});
            skLineSegment(sketch, "E3190", {"start": v(98.08, 7.1) * mm, "end": v(98.21, 7.15) * mm});
            skLineSegment(sketch, "E3191", {"start": v(98.21, 7.15) * mm, "end": v(98.35, 7.2) * mm});
            skLineSegment(sketch, "E3192", {"start": v(98.35, 7.2) * mm, "end": v(98.48, 7.27) * mm});
            skLineSegment(sketch, "E3193", {"start": v(98.48, 7.27) * mm, "end": v(98.62, 7.33) * mm});
            skLineSegment(sketch, "E3194", {"start": v(98.62, 7.33) * mm, "end": v(98.75, 7.4) * mm});
            skLineSegment(sketch, "E3195", {"start": v(98.75, 7.4) * mm, "end": v(98.9, 7.46) * mm});
            skLineSegment(sketch, "E3196", {"start": v(98.9, 7.46) * mm, "end": v(99.03, 7.53) * mm});
            skLineSegment(sketch, "E3197", {"start": v(99.03, 7.53) * mm, "end": v(99.17, 7.6) * mm});
            skLineSegment(sketch, "E3198", {"start": v(99.17, 7.6) * mm, "end": v(99.32, 7.66) * mm});
            skLineSegment(sketch, "E3199", {"start": v(99.32, 7.66) * mm, "end": v(99.46, 7.73) * mm});
            skLineSegment(sketch, "E3200", {"start": v(99.46, 7.73) * mm, "end": v(99.6, 7.8) * mm});
            skLineSegment(sketch, "E3201", {"start": v(99.6, 7.8) * mm, "end": v(99.75, 7.88) * mm});
            skLineSegment(sketch, "E3202", {"start": v(99.75, 7.88) * mm, "end": v(99.9, 7.95) * mm});
            skLineSegment(sketch, "E3203", {"start": v(99.9, 7.95) * mm, "end": v(100.05, 8.03) * mm});
            skLineSegment(sketch, "E3204", {"start": v(100.05, 8.03) * mm, "end": v(100.2, 8.1) * mm});
            skLineSegment(sketch, "E3205", {"start": v(100.2, 8.1) * mm, "end": v(100.35, 8.18) * mm});
            skLineSegment(sketch, "E3206", {"start": v(100.35, 8.18) * mm, "end": v(100.5, 8.26) * mm});
            skLineSegment(sketch, "E3207", {"start": v(100.5, 8.26) * mm, "end": v(100.65, 8.34) * mm});
            skLineSegment(sketch, "E3208", {"start": v(100.65, 8.34) * mm, "end": v(100.8, 8.43) * mm});
            skLineSegment(sketch, "E3209", {"start": v(100.8, 8.43) * mm, "end": v(100.96, 8.51) * mm});
            skLineSegment(sketch, "E3210", {"start": v(100.96, 8.51) * mm, "end": v(101.12, 8.6) * mm});
            skLineSegment(sketch, "E3211", {"start": v(101.12, 8.6) * mm, "end": v(101.28, 8.68) * mm});
            skLineSegment(sketch, "E3212", {"start": v(101.28, 8.68) * mm, "end": v(101.44, 8.77) * mm});
            skLineSegment(sketch, "E3213", {"start": v(101.44, 8.77) * mm, "end": v(101.6, 8.86) * mm});
            skLineSegment(sketch, "E3214", {"start": v(101.6, 8.86) * mm, "end": v(101.76, 8.96) * mm});
            skLineSegment(sketch, "E3215", {"start": v(101.76, 8.96) * mm, "end": v(101.92, 9.05) * mm});
            skLineSegment(sketch, "E3216", {"start": v(101.92, 9.05) * mm, "end": v(102.09, 9.15) * mm});
            skLineSegment(sketch, "E3217", {"start": v(102.09, 9.15) * mm, "end": v(102.08, 9.23) * mm});
            skLineSegment(sketch, "E3218", {"start": v(102.08, 9.23) * mm, "end": v(101.93, 10.8) * mm});
            skLineSegment(sketch, "E3219", {"start": v(101.93, 10.8) * mm, "end": v(101.92, 10.87) * mm});
            skLineSegment(sketch, "E3220", {"start": v(101.92, 10.87) * mm, "end": v(101.74, 10.93) * mm});
            skLineSegment(sketch, "E3221", {"start": v(101.74, 10.93) * mm, "end": v(101.56, 11) * mm});
            skLineSegment(sketch, "E3222", {"start": v(101.56, 11) * mm, "end": v(101.39, 11.05) * mm});
            skLineSegment(sketch, "E3223", {"start": v(101.39, 11.05) * mm, "end": v(101.21, 11.11) * mm});
            skLineSegment(sketch, "E3224", {"start": v(101.21, 11.11) * mm, "end": v(101.04, 11.17) * mm});
            skLineSegment(sketch, "E3225", {"start": v(101.04, 11.17) * mm, "end": v(100.86, 11.22) * mm});
            skLineSegment(sketch, "E3226", {"start": v(100.86, 11.22) * mm, "end": v(100.7, 11.28) * mm});
            skLineSegment(sketch, "E3227", {"start": v(100.7, 11.28) * mm, "end": v(100.52, 11.33) * mm});
            skLineSegment(sketch, "E3228", {"start": v(100.52, 11.33) * mm, "end": v(100.36, 11.38) * mm});
            skLineSegment(sketch, "E3229", {"start": v(100.36, 11.38) * mm, "end": v(100.19, 11.43) * mm});
            skLineSegment(sketch, "E3230", {"start": v(100.19, 11.43) * mm, "end": v(100.02, 11.48) * mm});
            skLineSegment(sketch, "E3231", {"start": v(100.02, 11.48) * mm, "end": v(99.86, 11.53) * mm});
            skLineSegment(sketch, "E3232", {"start": v(99.86, 11.53) * mm, "end": v(99.7, 11.57) * mm});
            skLineSegment(sketch, "E3233", {"start": v(99.7, 11.57) * mm, "end": v(99.54, 11.62) * mm});
            skLineSegment(sketch, "E3234", {"start": v(99.54, 11.62) * mm, "end": v(99.38, 11.66) * mm});
            skLineSegment(sketch, "E3235", {"start": v(99.38, 11.66) * mm, "end": v(99.22, 11.7) * mm});
            skLineSegment(sketch, "E3236", {"start": v(99.22, 11.7) * mm, "end": v(99.07, 11.75) * mm});
            skLineSegment(sketch, "E3237", {"start": v(99.07, 11.75) * mm, "end": v(98.91, 11.79) * mm});
            skLineSegment(sketch, "E3238", {"start": v(98.91, 11.79) * mm, "end": v(98.76, 11.83) * mm});
            skLineSegment(sketch, "E3239", {"start": v(98.76, 11.83) * mm, "end": v(98.6, 11.87) * mm});
            skLineSegment(sketch, "E3240", {"start": v(98.6, 11.87) * mm, "end": v(98.46, 11.9) * mm});
            skLineSegment(sketch, "E3241", {"start": v(98.46, 11.9) * mm, "end": v(98.3, 11.94) * mm});
            skLineSegment(sketch, "E3242", {"start": v(98.3, 11.94) * mm, "end": v(98.16, 11.98) * mm});
            skLineSegment(sketch, "E3243", {"start": v(98.16, 11.98) * mm, "end": v(98.02, 12.01) * mm});
            skLineSegment(sketch, "E3244", {"start": v(98.02, 12.01) * mm, "end": v(97.87, 12.04) * mm});
            skLineSegment(sketch, "E3245", {"start": v(97.87, 12.04) * mm, "end": v(97.73, 12.08) * mm});
            skLineSegment(sketch, "E3246", {"start": v(97.73, 12.08) * mm, "end": v(97.6, 12.1) * mm});
            skLineSegment(sketch, "E3247", {"start": v(97.6, 12.1) * mm, "end": v(97.45, 12.14) * mm});
            skLineSegment(sketch, "E3248", {"start": v(97.45, 12.14) * mm, "end": v(97.31, 12.17) * mm});
            skLineSegment(sketch, "E3249", {"start": v(97.31, 12.17) * mm, "end": v(97.18, 12.2) * mm});
            skLineSegment(sketch, "E3250", {"start": v(97.18, 12.2) * mm, "end": v(97.04, 12.22) * mm});
            skLineSegment(sketch, "E3251", {"start": v(97.04, 12.22) * mm, "end": v(96.91, 12.25) * mm});
            skLineSegment(sketch, "E3252", {"start": v(96.91, 12.25) * mm, "end": v(96.78, 12.27) * mm});
            skLineSegment(sketch, "E3253", {"start": v(96.78, 12.27) * mm, "end": v(96.65, 12.3) * mm});
            skLineSegment(sketch, "E3254", {"start": v(96.65, 12.3) * mm, "end": v(96.52, 12.32) * mm});
            skLineSegment(sketch, "E3255", {"start": v(96.52, 12.32) * mm, "end": v(96.4, 12.35) * mm});
            skLineSegment(sketch, "E3256", {"start": v(96.4, 12.35) * mm, "end": v(96.21, 13.27) * mm});
            skLineSegment(sketch, "E3257", {"start": v(96.21, 13.27) * mm, "end": v(96.14, 14.21) * mm});
            skLineSegment(sketch, "E3258", {"start": v(96.14, 14.21) * mm, "end": v(96.26, 14.27) * mm});
            skLineSegment(sketch, "E3259", {"start": v(96.26, 14.27) * mm, "end": v(96.37, 14.33) * mm});
            skLineSegment(sketch, "E3260", {"start": v(96.37, 14.33) * mm, "end": v(96.5, 14.39) * mm});
            skLineSegment(sketch, "E3261", {"start": v(96.5, 14.39) * mm, "end": v(96.6, 14.45) * mm});
            skLineSegment(sketch, "E3262", {"start": v(96.6, 14.45) * mm, "end": v(96.73, 14.5) * mm});
            skLineSegment(sketch, "E3263", {"start": v(96.73, 14.5) * mm, "end": v(96.85, 14.57) * mm});
            skLineSegment(sketch, "E3264", {"start": v(96.85, 14.57) * mm, "end": v(96.97, 14.63) * mm});
            skLineSegment(sketch, "E3265", {"start": v(96.97, 14.63) * mm, "end": v(97.1, 14.7) * mm});
            skLineSegment(sketch, "E3266", {"start": v(97.1, 14.7) * mm, "end": v(97.22, 14.77) * mm});
            skLineSegment(sketch, "E3267", {"start": v(97.22, 14.77) * mm, "end": v(97.35, 14.83) * mm});
            skLineSegment(sketch, "E3268", {"start": v(97.35, 14.83) * mm, "end": v(97.48, 14.9) * mm});
            skLineSegment(sketch, "E3269", {"start": v(97.48, 14.9) * mm, "end": v(97.6, 14.97) * mm});
            skLineSegment(sketch, "E3270", {"start": v(97.6, 14.97) * mm, "end": v(97.74, 15.05) * mm});
            skLineSegment(sketch, "E3271", {"start": v(97.74, 15.05) * mm, "end": v(97.87, 15.12) * mm});
            skLineSegment(sketch, "E3272", {"start": v(97.87, 15.12) * mm, "end": v(98, 15.2) * mm});
            skLineSegment(sketch, "E3273", {"start": v(98, 15.2) * mm, "end": v(98.14, 15.27) * mm});
            skLineSegment(sketch, "E3274", {"start": v(98.14, 15.27) * mm, "end": v(98.27, 15.35) * mm});
            skLineSegment(sketch, "E3275", {"start": v(98.27, 15.35) * mm, "end": v(98.4, 15.43) * mm});
            skLineSegment(sketch, "E3276", {"start": v(98.4, 15.43) * mm, "end": v(98.55, 15.51) * mm});
            skLineSegment(sketch, "E3277", {"start": v(98.55, 15.51) * mm, "end": v(98.69, 15.6) * mm});
            skLineSegment(sketch, "E3278", {"start": v(98.69, 15.6) * mm, "end": v(98.83, 15.68) * mm});
            skLineSegment(sketch, "E3279", {"start": v(98.83, 15.68) * mm, "end": v(98.97, 15.76) * mm});
            skLineSegment(sketch, "E3280", {"start": v(98.97, 15.76) * mm, "end": v(99.1, 15.85) * mm});
            skLineSegment(sketch, "E3281", {"start": v(99.1, 15.85) * mm, "end": v(99.25, 15.94) * mm});
            skLineSegment(sketch, "E3282", {"start": v(99.25, 15.94) * mm, "end": v(99.4, 16.03) * mm});
            skLineSegment(sketch, "E3283", {"start": v(99.4, 16.03) * mm, "end": v(99.54, 16.12) * mm});
            skLineSegment(sketch, "E3284", {"start": v(99.54, 16.12) * mm, "end": v(99.69, 16.21) * mm});
            skLineSegment(sketch, "E3285", {"start": v(99.69, 16.21) * mm, "end": v(99.84, 16.3) * mm});
            skLineSegment(sketch, "E3286", {"start": v(99.84, 16.3) * mm, "end": v(99.99, 16.4) * mm});
            skLineSegment(sketch, "E3287", {"start": v(99.99, 16.4) * mm, "end": v(100.14, 16.5) * mm});
            skLineSegment(sketch, "E3288", {"start": v(100.14, 16.5) * mm, "end": v(100.29, 16.6) * mm});
            skLineSegment(sketch, "E3289", {"start": v(100.29, 16.6) * mm, "end": v(100.44, 16.7) * mm});
            skLineSegment(sketch, "E3290", {"start": v(100.44, 16.7) * mm, "end": v(100.6, 16.8) * mm});
            skLineSegment(sketch, "E3291", {"start": v(100.6, 16.8) * mm, "end": v(100.75, 16.91) * mm});
            skLineSegment(sketch, "E3292", {"start": v(100.75, 16.91) * mm, "end": v(100.9, 17.02) * mm});
            skLineSegment(sketch, "E3293", {"start": v(100.9, 17.02) * mm, "end": v(101.06, 17.13) * mm});
            skLineSegment(sketch, "E3294", {"start": v(101.06, 17.13) * mm, "end": v(101.05, 17.2) * mm});
            skLineSegment(sketch, "E3295", {"start": v(101.05, 17.2) * mm, "end": v(100.77, 18.76) * mm});
            skLineSegment(sketch, "E3296", {"start": v(100.77, 18.76) * mm, "end": v(100.75, 18.84) * mm});
            skLineSegment(sketch, "E3297", {"start": v(100.75, 18.84) * mm, "end": v(100.57, 18.88) * mm});
            skLineSegment(sketch, "E3298", {"start": v(100.57, 18.88) * mm, "end": v(100.39, 18.93) * mm});
            skLineSegment(sketch, "E3299", {"start": v(100.39, 18.93) * mm, "end": v(100.2, 18.97) * mm});
            skLineSegment(sketch, "E3300", {"start": v(100.2, 18.97) * mm, "end": v(100.03, 19.02) * mm});
            skLineSegment(sketch, "E3301", {"start": v(100.03, 19.02) * mm, "end": v(99.85, 19.06) * mm});
            skLineSegment(sketch, "E3302", {"start": v(99.85, 19.06) * mm, "end": v(99.67, 19.1) * mm});
            skLineSegment(sketch, "E3303", {"start": v(99.67, 19.1) * mm, "end": v(99.5, 19.14) * mm});
            skLineSegment(sketch, "E3304", {"start": v(99.5, 19.14) * mm, "end": v(99.32, 19.18) * mm});
            skLineSegment(sketch, "E3305", {"start": v(99.32, 19.18) * mm, "end": v(99.15, 19.22) * mm});
            skLineSegment(sketch, "E3306", {"start": v(99.15, 19.22) * mm, "end": v(98.98, 19.26) * mm});
            skLineSegment(sketch, "E3307", {"start": v(98.98, 19.26) * mm, "end": v(98.82, 19.3) * mm});
            skLineSegment(sketch, "E3308", {"start": v(98.82, 19.3) * mm, "end": v(98.65, 19.33) * mm});
            skLineSegment(sketch, "E3309", {"start": v(98.65, 19.33) * mm, "end": v(98.48, 19.36) * mm});
            skLineSegment(sketch, "E3310", {"start": v(98.48, 19.36) * mm, "end": v(98.32, 19.4) * mm});
            skLineSegment(sketch, "E3311", {"start": v(98.32, 19.4) * mm, "end": v(98.16, 19.43) * mm});
            skLineSegment(sketch, "E3312", {"start": v(98.16, 19.43) * mm, "end": v(98, 19.46) * mm});
            skLineSegment(sketch, "E3313", {"start": v(98, 19.46) * mm, "end": v(97.84, 19.49) * mm});
            skLineSegment(sketch, "E3314", {"start": v(97.84, 19.49) * mm, "end": v(97.68, 19.51) * mm});
            skLineSegment(sketch, "E3315", {"start": v(97.68, 19.51) * mm, "end": v(97.53, 19.54) * mm});
            skLineSegment(sketch, "E3316", {"start": v(97.53, 19.54) * mm, "end": v(97.37, 19.57) * mm});
            skLineSegment(sketch, "E3317", {"start": v(97.37, 19.57) * mm, "end": v(97.22, 19.6) * mm});
            skLineSegment(sketch, "E3318", {"start": v(97.22, 19.6) * mm, "end": v(97.07, 19.62) * mm});
            skLineSegment(sketch, "E3319", {"start": v(97.07, 19.62) * mm, "end": v(96.92, 19.64) * mm});
            skLineSegment(sketch, "E3320", {"start": v(96.92, 19.64) * mm, "end": v(96.77, 19.66) * mm});
            skLineSegment(sketch, "E3321", {"start": v(96.77, 19.66) * mm, "end": v(96.63, 19.69) * mm});
            skLineSegment(sketch, "E3322", {"start": v(96.63, 19.69) * mm, "end": v(96.48, 19.7) * mm});
            skLineSegment(sketch, "E3323", {"start": v(96.48, 19.7) * mm, "end": v(96.34, 19.73) * mm});
            skLineSegment(sketch, "E3324", {"start": v(96.34, 19.73) * mm, "end": v(96.2, 19.75) * mm});
            skLineSegment(sketch, "E3325", {"start": v(96.2, 19.75) * mm, "end": v(96.06, 19.76) * mm});
            skLineSegment(sketch, "E3326", {"start": v(96.06, 19.76) * mm, "end": v(95.92, 19.78) * mm});
            skLineSegment(sketch, "E3327", {"start": v(95.92, 19.78) * mm, "end": v(95.79, 19.8) * mm});
            skLineSegment(sketch, "E3328", {"start": v(95.79, 19.8) * mm, "end": v(95.65, 19.81) * mm});
            skLineSegment(sketch, "E3329", {"start": v(95.65, 19.81) * mm, "end": v(95.52, 19.83) * mm});
            skLineSegment(sketch, "E3330", {"start": v(95.52, 19.83) * mm, "end": v(95.39, 19.84) * mm});
            skLineSegment(sketch, "E3331", {"start": v(95.39, 19.84) * mm, "end": v(95.26, 19.86) * mm});
            skLineSegment(sketch, "E3332", {"start": v(95.26, 19.86) * mm, "end": v(95.13, 19.87) * mm});
            skLineSegment(sketch, "E3333", {"start": v(95.13, 19.87) * mm, "end": v(94.88, 20.78) * mm});
            skLineSegment(sketch, "E3334", {"start": v(94.88, 20.78) * mm, "end": v(94.73, 21.71) * mm});
            skLineSegment(sketch, "E3335", {"start": v(94.73, 21.71) * mm, "end": v(94.84, 21.78) * mm});
            skLineSegment(sketch, "E3336", {"start": v(94.84, 21.78) * mm, "end": v(94.95, 21.85) * mm});
            skLineSegment(sketch, "E3337", {"start": v(94.95, 21.85) * mm, "end": v(95.06, 21.91) * mm});
            skLineSegment(sketch, "E3338", {"start": v(95.06, 21.91) * mm, "end": v(95.18, 21.98) * mm});
            skLineSegment(sketch, "E3339", {"start": v(95.18, 21.98) * mm, "end": v(95.3, 22.05) * mm});
            skLineSegment(sketch, "E3340", {"start": v(95.3, 22.05) * mm, "end": v(95.4, 22.12) * mm});
            skLineSegment(sketch, "E3341", {"start": v(95.4, 22.12) * mm, "end": v(95.53, 22.2) * mm});
            skLineSegment(sketch, "E3342", {"start": v(95.53, 22.2) * mm, "end": v(95.65, 22.27) * mm});
            skLineSegment(sketch, "E3343", {"start": v(95.65, 22.27) * mm, "end": v(95.77, 22.35) * mm});
            skLineSegment(sketch, "E3344", {"start": v(95.77, 22.35) * mm, "end": v(95.89, 22.43) * mm});
            skLineSegment(sketch, "E3345", {"start": v(95.89, 22.43) * mm, "end": v(96, 22.5) * mm});
            skLineSegment(sketch, "E3346", {"start": v(96, 22.5) * mm, "end": v(96.13, 22.59) * mm});
            skLineSegment(sketch, "E3347", {"start": v(96.13, 22.59) * mm, "end": v(96.26, 22.67) * mm});
            skLineSegment(sketch, "E3348", {"start": v(96.26, 22.67) * mm, "end": v(96.38, 22.75) * mm});
            skLineSegment(sketch, "E3349", {"start": v(96.38, 22.75) * mm, "end": v(96.5, 22.84) * mm});
            skLineSegment(sketch, "E3350", {"start": v(96.5, 22.84) * mm, "end": v(96.64, 22.92) * mm});
            skLineSegment(sketch, "E3351", {"start": v(96.64, 22.92) * mm, "end": v(96.77, 23.01) * mm});
            skLineSegment(sketch, "E3352", {"start": v(96.77, 23.01) * mm, "end": v(96.9, 23.1) * mm});
            skLineSegment(sketch, "E3353", {"start": v(96.9, 23.1) * mm, "end": v(97.03, 23.2) * mm});
            skLineSegment(sketch, "E3354", {"start": v(97.03, 23.2) * mm, "end": v(97.16, 23.29) * mm});
            skLineSegment(sketch, "E3355", {"start": v(97.16, 23.29) * mm, "end": v(97.3, 23.38) * mm});
            skLineSegment(sketch, "E3356", {"start": v(97.3, 23.38) * mm, "end": v(97.42, 23.48) * mm});
            skLineSegment(sketch, "E3357", {"start": v(97.42, 23.48) * mm, "end": v(97.56, 23.58) * mm});
            skLineSegment(sketch, "E3358", {"start": v(97.56, 23.58) * mm, "end": v(97.7, 23.68) * mm});
            skLineSegment(sketch, "E3359", {"start": v(97.7, 23.68) * mm, "end": v(97.83, 23.78) * mm});
            skLineSegment(sketch, "E3360", {"start": v(97.83, 23.78) * mm, "end": v(97.97, 23.88) * mm});
            skLineSegment(sketch, "E3361", {"start": v(97.97, 23.88) * mm, "end": v(98.1, 23.99) * mm});
            skLineSegment(sketch, "E3362", {"start": v(98.1, 23.99) * mm, "end": v(98.25, 24.1) * mm});
            skLineSegment(sketch, "E3363", {"start": v(98.25, 24.1) * mm, "end": v(98.4, 24.2) * mm});
            skLineSegment(sketch, "E3364", {"start": v(98.4, 24.2) * mm, "end": v(98.53, 24.3) * mm});
            skLineSegment(sketch, "E3365", {"start": v(98.53, 24.3) * mm, "end": v(98.67, 24.42) * mm});
            skLineSegment(sketch, "E3366", {"start": v(98.67, 24.42) * mm, "end": v(98.82, 24.53) * mm});
            skLineSegment(sketch, "E3367", {"start": v(98.82, 24.53) * mm, "end": v(98.96, 24.65) * mm});
            skLineSegment(sketch, "E3368", {"start": v(98.96, 24.65) * mm, "end": v(99.1, 24.77) * mm});
            skLineSegment(sketch, "E3369", {"start": v(99.1, 24.77) * mm, "end": v(99.25, 24.88) * mm});
            skLineSegment(sketch, "E3370", {"start": v(99.25, 24.88) * mm, "end": v(99.4, 25) * mm});
            skLineSegment(sketch, "E3371", {"start": v(99.4, 25) * mm, "end": v(99.38, 25.08) * mm});
            skLineSegment(sketch, "E3372", {"start": v(99.38, 25.08) * mm, "end": v(98.99, 26.6) * mm});
            skLineSegment(sketch, "E3373", {"start": v(98.99, 26.6) * mm, "end": v(98.96, 26.68) * mm});
            skLineSegment(sketch, "E3374", {"start": v(98.96, 26.68) * mm, "end": v(98.78, 26.72) * mm});
            skLineSegment(sketch, "E3375", {"start": v(98.78, 26.72) * mm, "end": v(98.6, 26.75) * mm});
            skLineSegment(sketch, "E3376", {"start": v(98.6, 26.75) * mm, "end": v(98.4, 26.78) * mm});
            skLineSegment(sketch, "E3377", {"start": v(98.4, 26.78) * mm, "end": v(98.23, 26.8) * mm});
            skLineSegment(sketch, "E3378", {"start": v(98.23, 26.8) * mm, "end": v(98.05, 26.84) * mm});
            skLineSegment(sketch, "E3379", {"start": v(98.05, 26.84) * mm, "end": v(97.87, 26.86) * mm});
            skLineSegment(sketch, "E3380", {"start": v(97.87, 26.86) * mm, "end": v(97.69, 26.9) * mm});
            skLineSegment(sketch, "E3381", {"start": v(97.69, 26.9) * mm, "end": v(97.51, 26.92) * mm});
            skLineSegment(sketch, "E3382", {"start": v(97.51, 26.92) * mm, "end": v(97.34, 26.94) * mm});
            skLineSegment(sketch, "E3383", {"start": v(97.34, 26.94) * mm, "end": v(97.17, 26.96) * mm});
            skLineSegment(sketch, "E3384", {"start": v(97.17, 26.96) * mm, "end": v(97, 26.99) * mm});
            skLineSegment(sketch, "E3385", {"start": v(97, 26.99) * mm, "end": v(96.83, 27) * mm});
            skLineSegment(sketch, "E3386", {"start": v(96.83, 27) * mm, "end": v(96.66, 27.03) * mm});
            skLineSegment(sketch, "E3387", {"start": v(96.66, 27.03) * mm, "end": v(96.5, 27.05) * mm});
            skLineSegment(sketch, "E3388", {"start": v(96.5, 27.05) * mm, "end": v(96.33, 27.07) * mm});
            skLineSegment(sketch, "E3389", {"start": v(96.33, 27.07) * mm, "end": v(96.17, 27.08) * mm});
            skLineSegment(sketch, "E3390", {"start": v(96.17, 27.08) * mm, "end": v(96, 27.1) * mm});
            skLineSegment(sketch, "E3391", {"start": v(96, 27.1) * mm, "end": v(95.85, 27.12) * mm});
            skLineSegment(sketch, "E3392", {"start": v(95.85, 27.12) * mm, "end": v(95.7, 27.13) * mm});
            skLineSegment(sketch, "E3393", {"start": v(95.7, 27.13) * mm, "end": v(95.54, 27.15) * mm});
            skLineSegment(sketch, "E3394", {"start": v(95.54, 27.15) * mm, "end": v(95.38, 27.16) * mm});
            skLineSegment(sketch, "E3395", {"start": v(95.38, 27.16) * mm, "end": v(95.23, 27.17) * mm});
            skLineSegment(sketch, "E3396", {"start": v(95.23, 27.17) * mm, "end": v(95.08, 27.19) * mm});
            skLineSegment(sketch, "E3397", {"start": v(95.08, 27.19) * mm, "end": v(94.93, 27.2) * mm});
            skLineSegment(sketch, "E3398", {"start": v(94.93, 27.2) * mm, "end": v(94.78, 27.2) * mm});
            skLineSegment(sketch, "E3399", {"start": v(94.78, 27.2) * mm, "end": v(94.64, 27.22) * mm});
            skLineSegment(sketch, "E3400", {"start": v(94.64, 27.22) * mm, "end": v(94.5, 27.23) * mm});
            skLineSegment(sketch, "E3401", {"start": v(94.5, 27.23) * mm, "end": v(94.35, 27.23) * mm});
            skLineSegment(sketch, "E3402", {"start": v(94.35, 27.23) * mm, "end": v(94.21, 27.24) * mm});
            skLineSegment(sketch, "E3403", {"start": v(94.21, 27.24) * mm, "end": v(94.07, 27.25) * mm});
            skLineSegment(sketch, "E3404", {"start": v(94.07, 27.25) * mm, "end": v(93.94, 27.25) * mm});
            skLineSegment(sketch, "E3405", {"start": v(93.94, 27.25) * mm, "end": v(93.8, 27.26) * mm});
            skLineSegment(sketch, "E3406", {"start": v(93.8, 27.26) * mm, "end": v(93.67, 27.26) * mm});
            skLineSegment(sketch, "E3407", {"start": v(93.67, 27.26) * mm, "end": v(93.54, 27.27) * mm});
            skLineSegment(sketch, "E3408", {"start": v(93.54, 27.27) * mm, "end": v(93.4, 27.27) * mm});
            skLineSegment(sketch, "E3409", {"start": v(93.4, 27.27) * mm, "end": v(93.28, 27.27) * mm});
            skLineSegment(sketch, "E3410", {"start": v(93.28, 27.27) * mm, "end": v(92.95, 28.16) * mm});
            skLineSegment(sketch, "E3411", {"start": v(92.95, 28.16) * mm, "end": v(92.73, 29.08) * mm});
            skLineSegment(sketch, "E3412", {"start": v(92.73, 29.08) * mm, "end": v(92.84, 29.15) * mm});
            skLineSegment(sketch, "E3413", {"start": v(92.84, 29.15) * mm, "end": v(92.94, 29.23) * mm});
            skLineSegment(sketch, "E3414", {"start": v(92.94, 29.23) * mm, "end": v(93.05, 29.3) * mm});
            skLineSegment(sketch, "E3415", {"start": v(93.05, 29.3) * mm, "end": v(93.16, 29.38) * mm});
            skLineSegment(sketch, "E3416", {"start": v(93.16, 29.38) * mm, "end": v(93.27, 29.46) * mm});
            skLineSegment(sketch, "E3417", {"start": v(93.27, 29.46) * mm, "end": v(93.38, 29.54) * mm});
            skLineSegment(sketch, "E3418", {"start": v(93.38, 29.54) * mm, "end": v(93.5, 29.62) * mm});
            skLineSegment(sketch, "E3419", {"start": v(93.5, 29.62) * mm, "end": v(93.6, 29.7) * mm});
            skLineSegment(sketch, "E3420", {"start": v(93.6, 29.7) * mm, "end": v(93.72, 29.8) * mm});
            skLineSegment(sketch, "E3421", {"start": v(93.72, 29.8) * mm, "end": v(93.83, 29.88) * mm});
            skLineSegment(sketch, "E3422", {"start": v(93.83, 29.88) * mm, "end": v(93.95, 29.97) * mm});
            skLineSegment(sketch, "E3423", {"start": v(93.95, 29.97) * mm, "end": v(94.06, 30.06) * mm});
            skLineSegment(sketch, "E3424", {"start": v(94.06, 30.06) * mm, "end": v(94.18, 30.15) * mm});
            skLineSegment(sketch, "E3425", {"start": v(94.18, 30.15) * mm, "end": v(94.3, 30.24) * mm});
            skLineSegment(sketch, "E3426", {"start": v(94.3, 30.24) * mm, "end": v(94.42, 30.34) * mm});
            skLineSegment(sketch, "E3427", {"start": v(94.42, 30.34) * mm, "end": v(94.54, 30.44) * mm});
            skLineSegment(sketch, "E3428", {"start": v(94.54, 30.44) * mm, "end": v(94.66, 30.53) * mm});
            skLineSegment(sketch, "E3429", {"start": v(94.66, 30.53) * mm, "end": v(94.78, 30.63) * mm});
            skLineSegment(sketch, "E3430", {"start": v(94.78, 30.63) * mm, "end": v(94.9, 30.74) * mm});
            skLineSegment(sketch, "E3431", {"start": v(94.9, 30.74) * mm, "end": v(95.03, 30.84) * mm});
            skLineSegment(sketch, "E3432", {"start": v(95.03, 30.84) * mm, "end": v(95.16, 30.94) * mm});
            skLineSegment(sketch, "E3433", {"start": v(95.16, 30.94) * mm, "end": v(95.28, 31.05) * mm});
            skLineSegment(sketch, "E3434", {"start": v(95.28, 31.05) * mm, "end": v(95.4, 31.16) * mm});
            skLineSegment(sketch, "E3435", {"start": v(95.4, 31.16) * mm, "end": v(95.54, 31.27) * mm});
            skLineSegment(sketch, "E3436", {"start": v(95.54, 31.27) * mm, "end": v(95.67, 31.38) * mm});
            skLineSegment(sketch, "E3437", {"start": v(95.67, 31.38) * mm, "end": v(95.8, 31.5) * mm});
            skLineSegment(sketch, "E3438", {"start": v(95.8, 31.5) * mm, "end": v(95.93, 31.6) * mm});
            skLineSegment(sketch, "E3439", {"start": v(95.93, 31.6) * mm, "end": v(96.06, 31.73) * mm});
            skLineSegment(sketch, "E3440", {"start": v(96.06, 31.73) * mm, "end": v(96.19, 31.84) * mm});
            skLineSegment(sketch, "E3441", {"start": v(96.19, 31.84) * mm, "end": v(96.32, 31.97) * mm});
            skLineSegment(sketch, "E3442", {"start": v(96.32, 31.97) * mm, "end": v(96.45, 32.09) * mm});
            skLineSegment(sketch, "E3443", {"start": v(96.45, 32.09) * mm, "end": v(96.59, 32.21) * mm});
            skLineSegment(sketch, "E3444", {"start": v(96.59, 32.21) * mm, "end": v(96.72, 32.34) * mm});
            skLineSegment(sketch, "E3445", {"start": v(96.72, 32.34) * mm, "end": v(96.86, 32.46) * mm});
            skLineSegment(sketch, "E3446", {"start": v(96.86, 32.46) * mm, "end": v(97, 32.6) * mm});
            skLineSegment(sketch, "E3447", {"start": v(97, 32.6) * mm, "end": v(97.13, 32.73) * mm});
            skLineSegment(sketch, "E3448", {"start": v(97.13, 32.73) * mm, "end": v(97.1, 32.8) * mm});
            skLineSegment(sketch, "E3449", {"start": v(97.1, 32.8) * mm, "end": v(96.6, 34.29) * mm});
            skLineSegment(sketch, "E3450", {"start": v(96.6, 34.29) * mm, "end": v(96.57, 34.36) * mm});
            skLineSegment(sketch, "E3451", {"start": v(96.57, 34.36) * mm, "end": v(96.38, 34.38) * mm});
            skLineSegment(sketch, "E3452", {"start": v(96.38, 34.38) * mm, "end": v(96.19, 34.4) * mm});
            skLineSegment(sketch, "E3453", {"start": v(96.19, 34.4) * mm, "end": v(96, 34.42) * mm});
            skLineSegment(sketch, "E3454", {"start": v(96, 34.42) * mm, "end": v(95.82, 34.43) * mm});
            skLineSegment(sketch, "E3455", {"start": v(95.82, 34.43) * mm, "end": v(95.64, 34.45) * mm});
            skLineSegment(sketch, "E3456", {"start": v(95.64, 34.45) * mm, "end": v(95.46, 34.46) * mm});
            skLineSegment(sketch, "E3457", {"start": v(95.46, 34.46) * mm, "end": v(95.28, 34.47) * mm});
            skLineSegment(sketch, "E3458", {"start": v(95.28, 34.47) * mm, "end": v(95.1, 34.48) * mm});
            skLineSegment(sketch, "E3459", {"start": v(95.1, 34.48) * mm, "end": v(94.93, 34.5) * mm});
            skLineSegment(sketch, "E3460", {"start": v(94.93, 34.5) * mm, "end": v(94.75, 34.5) * mm});
            skLineSegment(sketch, "E3461", {"start": v(94.75, 34.5) * mm, "end": v(94.58, 34.51) * mm});
            skLineSegment(sketch, "E3462", {"start": v(94.58, 34.51) * mm, "end": v(94.41, 34.52) * mm});
            skLineSegment(sketch, "E3463", {"start": v(94.41, 34.52) * mm, "end": v(94.24, 34.53) * mm});
            skLineSegment(sketch, "E3464", {"start": v(94.24, 34.53) * mm, "end": v(94.08, 34.54) * mm});
            skLineSegment(sketch, "E3465", {"start": v(94.08, 34.54) * mm, "end": v(93.91, 34.54) * mm});
            skLineSegment(sketch, "E3466", {"start": v(93.91, 34.54) * mm, "end": v(93.75, 34.55) * mm});
            skLineSegment(sketch, "E3467", {"start": v(93.75, 34.55) * mm, "end": v(93.59, 34.55) * mm});
            skLineSegment(sketch, "E3468", {"start": v(93.59, 34.55) * mm, "end": v(93.43, 34.55) * mm});
            skLineSegment(sketch, "E3469", {"start": v(93.43, 34.55) * mm, "end": v(93.27, 34.56) * mm});
            skLineSegment(sketch, "E3470", {"start": v(93.27, 34.56) * mm, "end": v(93.11, 34.56) * mm});
            skLineSegment(sketch, "E3471", {"start": v(93.11, 34.56) * mm, "end": v(92.96, 34.56) * mm});
            skLineSegment(sketch, "E3472", {"start": v(92.96, 34.56) * mm, "end": v(92.8, 34.56) * mm});
            skLineSegment(sketch, "E3473", {"start": v(92.8, 34.56) * mm, "end": v(92.65, 34.56) * mm});
            skLineSegment(sketch, "E3474", {"start": v(92.65, 34.56) * mm, "end": v(92.5, 34.56) * mm});
            skLineSegment(sketch, "E3475", {"start": v(92.5, 34.56) * mm, "end": v(92.36, 34.56) * mm});
            skLineSegment(sketch, "E3476", {"start": v(92.36, 34.56) * mm, "end": v(92.21, 34.56) * mm});
            skLineSegment(sketch, "E3477", {"start": v(92.21, 34.56) * mm, "end": v(92.07, 34.56) * mm});
            skLineSegment(sketch, "E3478", {"start": v(92.07, 34.56) * mm, "end": v(91.93, 34.55) * mm});
            skLineSegment(sketch, "E3479", {"start": v(91.93, 34.55) * mm, "end": v(91.79, 34.55) * mm});
            skLineSegment(sketch, "E3480", {"start": v(91.79, 34.55) * mm, "end": v(91.65, 34.54) * mm});
            skLineSegment(sketch, "E3481", {"start": v(91.65, 34.54) * mm, "end": v(91.51, 34.54) * mm});
            skLineSegment(sketch, "E3482", {"start": v(91.51, 34.54) * mm, "end": v(91.38, 34.53) * mm});
            skLineSegment(sketch, "E3483", {"start": v(91.38, 34.53) * mm, "end": v(91.24, 34.53) * mm});
            skLineSegment(sketch, "E3484", {"start": v(91.24, 34.53) * mm, "end": v(91.11, 34.52) * mm});
            skLineSegment(sketch, "E3485", {"start": v(91.11, 34.52) * mm, "end": v(90.98, 34.52) * mm});
            skLineSegment(sketch, "E3486", {"start": v(90.98, 34.52) * mm, "end": v(90.85, 34.5) * mm});
            skLineSegment(sketch, "E3487", {"start": v(90.85, 34.5) * mm, "end": v(90.46, 35.37) * mm});
            skLineSegment(sketch, "E3488", {"start": v(90.46, 35.37) * mm, "end": v(90.17, 36.27) * mm});
            skLineSegment(sketch, "E3489", {"start": v(90.17, 36.27) * mm, "end": v(90.27, 36.35) * mm});
            skLineSegment(sketch, "E3490", {"start": v(90.27, 36.35) * mm, "end": v(90.36, 36.43) * mm});
            skLineSegment(sketch, "E3491", {"start": v(90.36, 36.43) * mm, "end": v(90.47, 36.51) * mm});
            skLineSegment(sketch, "E3492", {"start": v(90.47, 36.51) * mm, "end": v(90.57, 36.6) * mm});
            skLineSegment(sketch, "E3493", {"start": v(90.57, 36.6) * mm, "end": v(90.67, 36.69) * mm});
            skLineSegment(sketch, "E3494", {"start": v(90.67, 36.69) * mm, "end": v(90.77, 36.78) * mm});
            skLineSegment(sketch, "E3495", {"start": v(90.77, 36.78) * mm, "end": v(90.88, 36.87) * mm});
            skLineSegment(sketch, "E3496", {"start": v(90.88, 36.87) * mm, "end": v(90.98, 36.96) * mm});
            skLineSegment(sketch, "E3497", {"start": v(90.98, 36.96) * mm, "end": v(91.1, 37.05) * mm});
            skLineSegment(sketch, "E3498", {"start": v(91.1, 37.05) * mm, "end": v(91.2, 37.15) * mm});
            skLineSegment(sketch, "E3499", {"start": v(91.2, 37.15) * mm, "end": v(91.3, 37.25) * mm});
            skLineSegment(sketch, "E3500", {"start": v(91.3, 37.25) * mm, "end": v(91.42, 37.35) * mm});
            skLineSegment(sketch, "E3501", {"start": v(91.42, 37.35) * mm, "end": v(91.53, 37.45) * mm});
            skLineSegment(sketch, "E3502", {"start": v(91.53, 37.45) * mm, "end": v(91.64, 37.55) * mm});
            skLineSegment(sketch, "E3503", {"start": v(91.64, 37.55) * mm, "end": v(91.75, 37.65) * mm});
            skLineSegment(sketch, "E3504", {"start": v(91.75, 37.65) * mm, "end": v(91.86, 37.76) * mm});
            skLineSegment(sketch, "E3505", {"start": v(91.86, 37.76) * mm, "end": v(91.97, 37.87) * mm});
            skLineSegment(sketch, "E3506", {"start": v(91.97, 37.87) * mm, "end": v(92.09, 37.98) * mm});
            skLineSegment(sketch, "E3507", {"start": v(92.09, 37.98) * mm, "end": v(92.2, 38.09) * mm});
            skLineSegment(sketch, "E3508", {"start": v(92.2, 38.09) * mm, "end": v(92.32, 38.2) * mm});
            skLineSegment(sketch, "E3509", {"start": v(92.32, 38.2) * mm, "end": v(92.44, 38.31) * mm});
            skLineSegment(sketch, "E3510", {"start": v(92.44, 38.31) * mm, "end": v(92.55, 38.43) * mm});
            skLineSegment(sketch, "E3511", {"start": v(92.55, 38.43) * mm, "end": v(92.67, 38.55) * mm});
            skLineSegment(sketch, "E3512", {"start": v(92.67, 38.55) * mm, "end": v(92.79, 38.67) * mm});
            skLineSegment(sketch, "E3513", {"start": v(92.79, 38.67) * mm, "end": v(92.9, 38.79) * mm});
            skLineSegment(sketch, "E3514", {"start": v(92.9, 38.79) * mm, "end": v(93.03, 38.91) * mm});
            skLineSegment(sketch, "E3515", {"start": v(93.03, 38.91) * mm, "end": v(93.15, 39.04) * mm});
            skLineSegment(sketch, "E3516", {"start": v(93.15, 39.04) * mm, "end": v(93.27, 39.16) * mm});
            skLineSegment(sketch, "E3517", {"start": v(93.27, 39.16) * mm, "end": v(93.4, 39.3) * mm});
            skLineSegment(sketch, "E3518", {"start": v(93.4, 39.3) * mm, "end": v(93.52, 39.42) * mm});
            skLineSegment(sketch, "E3519", {"start": v(93.52, 39.42) * mm, "end": v(93.64, 39.56) * mm});
            skLineSegment(sketch, "E3520", {"start": v(93.64, 39.56) * mm, "end": v(93.76, 39.7) * mm});
            skLineSegment(sketch, "E3521", {"start": v(93.76, 39.7) * mm, "end": v(93.89, 39.83) * mm});
            skLineSegment(sketch, "E3522", {"start": v(93.89, 39.83) * mm, "end": v(94.01, 39.96) * mm});
            skLineSegment(sketch, "E3523", {"start": v(94.01, 39.96) * mm, "end": v(94.14, 40.1) * mm});
            skLineSegment(sketch, "E3524", {"start": v(94.14, 40.1) * mm, "end": v(94.27, 40.25) * mm});
            skLineSegment(sketch, "E3525", {"start": v(94.27, 40.25) * mm, "end": v(94.24, 40.32) * mm});
            skLineSegment(sketch, "E3526", {"start": v(94.24, 40.32) * mm, "end": v(93.6, 41.76) * mm});
            skLineSegment(sketch, "E3527", {"start": v(93.6, 41.76) * mm, "end": v(93.57, 41.83) * mm});
            skLineSegment(sketch, "E3528", {"start": v(93.57, 41.83) * mm, "end": v(93.38, 41.84) * mm});
            skLineSegment(sketch, "E3529", {"start": v(93.38, 41.84) * mm, "end": v(93.2, 41.84) * mm});
            skLineSegment(sketch, "E3530", {"start": v(93.2, 41.84) * mm, "end": v(93, 41.84) * mm});
            skLineSegment(sketch, "E3531", {"start": v(93, 41.84) * mm, "end": v(92.82, 41.84) * mm});
            skLineSegment(sketch, "E3532", {"start": v(92.82, 41.84) * mm, "end": v(92.64, 41.84) * mm});
            skLineSegment(sketch, "E3533", {"start": v(92.64, 41.84) * mm, "end": v(92.46, 41.84) * mm});
            skLineSegment(sketch, "E3534", {"start": v(92.46, 41.84) * mm, "end": v(92.28, 41.84) * mm});
            skLineSegment(sketch, "E3535", {"start": v(92.28, 41.84) * mm, "end": v(92.1, 41.84) * mm});
            skLineSegment(sketch, "E3536", {"start": v(92.1, 41.84) * mm, "end": v(91.93, 41.84) * mm});
            skLineSegment(sketch, "E3537", {"start": v(91.93, 41.84) * mm, "end": v(91.75, 41.83) * mm});
            skLineSegment(sketch, "E3538", {"start": v(91.75, 41.83) * mm, "end": v(91.58, 41.83) * mm});
            skLineSegment(sketch, "E3539", {"start": v(91.58, 41.83) * mm, "end": v(91.41, 41.82) * mm});
            skLineSegment(sketch, "E3540", {"start": v(91.41, 41.82) * mm, "end": v(91.24, 41.82) * mm});
            skLineSegment(sketch, "E3541", {"start": v(91.24, 41.82) * mm, "end": v(91.08, 41.81) * mm});
            skLineSegment(sketch, "E3542", {"start": v(91.08, 41.81) * mm, "end": v(90.91, 41.8) * mm});
            skLineSegment(sketch, "E3543", {"start": v(90.91, 41.8) * mm, "end": v(90.75, 41.8) * mm});
            skLineSegment(sketch, "E3544", {"start": v(90.75, 41.8) * mm, "end": v(90.59, 41.79) * mm});
            skLineSegment(sketch, "E3545", {"start": v(90.59, 41.79) * mm, "end": v(90.43, 41.78) * mm});
            skLineSegment(sketch, "E3546", {"start": v(90.43, 41.78) * mm, "end": v(90.27, 41.77) * mm});
            skLineSegment(sketch, "E3547", {"start": v(90.27, 41.77) * mm, "end": v(90.11, 41.76) * mm});
            skLineSegment(sketch, "E3548", {"start": v(90.11, 41.76) * mm, "end": v(89.96, 41.75) * mm});
            skLineSegment(sketch, "E3549", {"start": v(89.96, 41.75) * mm, "end": v(89.8, 41.74) * mm});
            skLineSegment(sketch, "E3550", {"start": v(89.8, 41.74) * mm, "end": v(89.66, 41.72) * mm});
            skLineSegment(sketch, "E3551", {"start": v(89.66, 41.72) * mm, "end": v(89.5, 41.71) * mm});
            skLineSegment(sketch, "E3552", {"start": v(89.5, 41.71) * mm, "end": v(89.36, 41.7) * mm});
            skLineSegment(sketch, "E3553", {"start": v(89.36, 41.7) * mm, "end": v(89.22, 41.69) * mm});
            skLineSegment(sketch, "E3554", {"start": v(89.22, 41.69) * mm, "end": v(89.07, 41.67) * mm});
            skLineSegment(sketch, "E3555", {"start": v(89.07, 41.67) * mm, "end": v(88.93, 41.66) * mm});
            skLineSegment(sketch, "E3556", {"start": v(88.93, 41.66) * mm, "end": v(88.8, 41.64) * mm});
            skLineSegment(sketch, "E3557", {"start": v(88.8, 41.64) * mm, "end": v(88.65, 41.63) * mm});
            skLineSegment(sketch, "E3558", {"start": v(88.65, 41.63) * mm, "end": v(88.52, 41.61) * mm});
            skLineSegment(sketch, "E3559", {"start": v(88.52, 41.61) * mm, "end": v(88.38, 41.6) * mm});
            skLineSegment(sketch, "E3560", {"start": v(88.38, 41.6) * mm, "end": v(88.25, 41.58) * mm});
            skLineSegment(sketch, "E3561", {"start": v(88.25, 41.58) * mm, "end": v(88.12, 41.56) * mm});
            skLineSegment(sketch, "E3562", {"start": v(88.12, 41.56) * mm, "end": v(88, 41.55) * mm});
            skLineSegment(sketch, "E3563", {"start": v(88, 41.55) * mm, "end": v(87.87, 41.53) * mm});
            skLineSegment(sketch, "E3564", {"start": v(87.87, 41.53) * mm, "end": v(87.4, 42.35) * mm});
            skLineSegment(sketch, "E3565", {"start": v(87.4, 42.35) * mm, "end": v(87.04, 43.23) * mm});
            skLineSegment(sketch, "E3566", {"start": v(87.04, 43.23) * mm, "end": v(87.14, 43.32) * mm});
            skLineSegment(sketch, "E3567", {"start": v(87.14, 43.32) * mm, "end": v(87.23, 43.4) * mm});
            skLineSegment(sketch, "E3568", {"start": v(87.23, 43.4) * mm, "end": v(87.32, 43.5) * mm});
            skLineSegment(sketch, "E3569", {"start": v(87.32, 43.5) * mm, "end": v(87.42, 43.6) * mm});
            skLineSegment(sketch, "E3570", {"start": v(87.42, 43.6) * mm, "end": v(87.51, 43.69) * mm});
            skLineSegment(sketch, "E3571", {"start": v(87.51, 43.69) * mm, "end": v(87.6, 43.79) * mm});
            skLineSegment(sketch, "E3572", {"start": v(87.6, 43.79) * mm, "end": v(87.7, 43.88) * mm});
            skLineSegment(sketch, "E3573", {"start": v(87.7, 43.88) * mm, "end": v(87.8, 43.99) * mm});
            skLineSegment(sketch, "E3574", {"start": v(87.8, 43.99) * mm, "end": v(87.9, 44.09) * mm});
            skLineSegment(sketch, "E3575", {"start": v(87.9, 44.09) * mm, "end": v(88, 44.2) * mm});
            skLineSegment(sketch, "E3576", {"start": v(88, 44.2) * mm, "end": v(88.1, 44.3) * mm});
            skLineSegment(sketch, "E3577", {"start": v(88.1, 44.3) * mm, "end": v(88.2, 44.4) * mm});
            skLineSegment(sketch, "E3578", {"start": v(88.2, 44.4) * mm, "end": v(88.3, 44.51) * mm});
            skLineSegment(sketch, "E3579", {"start": v(88.3, 44.51) * mm, "end": v(88.4, 44.62) * mm});
            skLineSegment(sketch, "E3580", {"start": v(88.4, 44.62) * mm, "end": v(88.51, 44.74) * mm});
            skLineSegment(sketch, "E3581", {"start": v(88.51, 44.74) * mm, "end": v(88.61, 44.85) * mm});
            skLineSegment(sketch, "E3582", {"start": v(88.61, 44.85) * mm, "end": v(88.72, 44.97) * mm});
            skLineSegment(sketch, "E3583", {"start": v(88.72, 44.97) * mm, "end": v(88.82, 45.08) * mm});
            skLineSegment(sketch, "E3584", {"start": v(88.82, 45.08) * mm, "end": v(88.93, 45.2) * mm});
            skLineSegment(sketch, "E3585", {"start": v(88.93, 45.2) * mm, "end": v(89.04, 45.33) * mm});
            skLineSegment(sketch, "E3586", {"start": v(89.04, 45.33) * mm, "end": v(89.14, 45.45) * mm});
            skLineSegment(sketch, "E3587", {"start": v(89.14, 45.45) * mm, "end": v(89.25, 45.57) * mm});
            skLineSegment(sketch, "E3588", {"start": v(89.25, 45.57) * mm, "end": v(89.36, 45.7) * mm});
            skLineSegment(sketch, "E3589", {"start": v(89.36, 45.7) * mm, "end": v(89.47, 45.83) * mm});
            skLineSegment(sketch, "E3590", {"start": v(89.47, 45.83) * mm, "end": v(89.58, 45.96) * mm});
            skLineSegment(sketch, "E3591", {"start": v(89.58, 45.96) * mm, "end": v(89.69, 46.1) * mm});
            skLineSegment(sketch, "E3592", {"start": v(89.69, 46.1) * mm, "end": v(89.8, 46.23) * mm});
            skLineSegment(sketch, "E3593", {"start": v(89.8, 46.23) * mm, "end": v(89.91, 46.36) * mm});
            skLineSegment(sketch, "E3594", {"start": v(89.91, 46.36) * mm, "end": v(90.02, 46.5) * mm});
            skLineSegment(sketch, "E3595", {"start": v(90.02, 46.5) * mm, "end": v(90.13, 46.64) * mm});
            skLineSegment(sketch, "E3596", {"start": v(90.13, 46.64) * mm, "end": v(90.25, 46.78) * mm});
            skLineSegment(sketch, "E3597", {"start": v(90.25, 46.78) * mm, "end": v(90.36, 46.92) * mm});
            skLineSegment(sketch, "E3598", {"start": v(90.36, 46.92) * mm, "end": v(90.47, 47.07) * mm});
            skLineSegment(sketch, "E3599", {"start": v(90.47, 47.07) * mm, "end": v(90.59, 47.22) * mm});
            skLineSegment(sketch, "E3600", {"start": v(90.59, 47.22) * mm, "end": v(90.7, 47.37) * mm});
            skLineSegment(sketch, "E3601", {"start": v(90.7, 47.37) * mm, "end": v(90.82, 47.52) * mm});
            skLineSegment(sketch, "E3602", {"start": v(90.82, 47.52) * mm, "end": v(90.78, 47.6) * mm});
            skLineSegment(sketch, "E3603", {"start": v(90.78, 47.6) * mm, "end": v(90.04, 48.98) * mm});
            skLineSegment(sketch, "E3604", {"start": v(90.04, 48.98) * mm, "end": v(90, 49.05) * mm});
            skLineSegment(sketch, "E3605", {"start": v(90, 49.05) * mm, "end": v(89.81, 49.04) * mm});
            skLineSegment(sketch, "E3606", {"start": v(89.81, 49.04) * mm, "end": v(89.62, 49.02) * mm});
            skLineSegment(sketch, "E3607", {"start": v(89.62, 49.02) * mm, "end": v(89.44, 49.01) * mm});
            skLineSegment(sketch, "E3608", {"start": v(89.44, 49.01) * mm, "end": v(89.25, 49) * mm});
            skLineSegment(sketch, "E3609", {"start": v(89.25, 49) * mm, "end": v(89.07, 48.98) * mm});
            skLineSegment(sketch, "E3610", {"start": v(89.07, 48.98) * mm, "end": v(88.9, 48.97) * mm});
            skLineSegment(sketch, "E3611", {"start": v(88.9, 48.97) * mm, "end": v(88.71, 48.95) * mm});
            skLineSegment(sketch, "E3612", {"start": v(88.71, 48.95) * mm, "end": v(88.54, 48.94) * mm});
            skLineSegment(sketch, "E3613", {"start": v(88.54, 48.94) * mm, "end": v(88.36, 48.92) * mm});
            skLineSegment(sketch, "E3614", {"start": v(88.36, 48.92) * mm, "end": v(88.19, 48.9) * mm});
            skLineSegment(sketch, "E3615", {"start": v(88.19, 48.9) * mm, "end": v(88.02, 48.88) * mm});
            skLineSegment(sketch, "E3616", {"start": v(88.02, 48.88) * mm, "end": v(87.85, 48.87) * mm});
            skLineSegment(sketch, "E3617", {"start": v(87.85, 48.87) * mm, "end": v(87.68, 48.85) * mm});
            skLineSegment(sketch, "E3618", {"start": v(87.68, 48.85) * mm, "end": v(87.51, 48.83) * mm});
            skLineSegment(sketch, "E3619", {"start": v(87.51, 48.83) * mm, "end": v(87.35, 48.8) * mm});
            skLineSegment(sketch, "E3620", {"start": v(87.35, 48.8) * mm, "end": v(87.19, 48.79) * mm});
            skLineSegment(sketch, "E3621", {"start": v(87.19, 48.79) * mm, "end": v(87.03, 48.77) * mm});
            skLineSegment(sketch, "E3622", {"start": v(87.03, 48.77) * mm, "end": v(86.87, 48.74) * mm});
            skLineSegment(sketch, "E3623", {"start": v(86.87, 48.74) * mm, "end": v(86.71, 48.72) * mm});
            skLineSegment(sketch, "E3624", {"start": v(86.71, 48.72) * mm, "end": v(86.56, 48.7) * mm});
            skLineSegment(sketch, "E3625", {"start": v(86.56, 48.7) * mm, "end": v(86.4, 48.68) * mm});
            skLineSegment(sketch, "E3626", {"start": v(86.4, 48.68) * mm, "end": v(86.26, 48.65) * mm});
            skLineSegment(sketch, "E3627", {"start": v(86.26, 48.65) * mm, "end": v(86.1, 48.63) * mm});
            skLineSegment(sketch, "E3628", {"start": v(86.1, 48.63) * mm, "end": v(85.96, 48.6) * mm});
            skLineSegment(sketch, "E3629", {"start": v(85.96, 48.6) * mm, "end": v(85.81, 48.58) * mm});
            skLineSegment(sketch, "E3630", {"start": v(85.81, 48.58) * mm, "end": v(85.67, 48.56) * mm});
            skLineSegment(sketch, "E3631", {"start": v(85.67, 48.56) * mm, "end": v(85.53, 48.53) * mm});
            skLineSegment(sketch, "E3632", {"start": v(85.53, 48.53) * mm, "end": v(85.39, 48.5) * mm});
            skLineSegment(sketch, "E3633", {"start": v(85.39, 48.5) * mm, "end": v(85.25, 48.48) * mm});
            skLineSegment(sketch, "E3634", {"start": v(85.25, 48.48) * mm, "end": v(85.11, 48.46) * mm});
            skLineSegment(sketch, "E3635", {"start": v(85.11, 48.46) * mm, "end": v(84.98, 48.43) * mm});
            skLineSegment(sketch, "E3636", {"start": v(84.98, 48.43) * mm, "end": v(84.85, 48.4) * mm});
            skLineSegment(sketch, "E3637", {"start": v(84.85, 48.4) * mm, "end": v(84.72, 48.38) * mm});
            skLineSegment(sketch, "E3638", {"start": v(84.72, 48.38) * mm, "end": v(84.59, 48.35) * mm});
            skLineSegment(sketch, "E3639", {"start": v(84.59, 48.35) * mm, "end": v(84.46, 48.32) * mm});
            skLineSegment(sketch, "E3640", {"start": v(84.46, 48.32) * mm, "end": v(84.34, 48.3) * mm});
            skLineSegment(sketch, "E3641", {"start": v(84.34, 48.3) * mm, "end": v(83.81, 49.08) * mm});
            skLineSegment(sketch, "E3642", {"start": v(83.81, 49.08) * mm, "end": v(83.38, 49.92) * mm});
            skLineSegment(sketch, "E3643", {"start": v(83.38, 49.92) * mm, "end": v(83.47, 50.02) * mm});
            skLineSegment(sketch, "E3644", {"start": v(83.47, 50.02) * mm, "end": v(83.55, 50.12) * mm});
            skLineSegment(sketch, "E3645", {"start": v(83.55, 50.12) * mm, "end": v(83.64, 50.22) * mm});
            skLineSegment(sketch, "E3646", {"start": v(83.64, 50.22) * mm, "end": v(83.73, 50.32) * mm});
            skLineSegment(sketch, "E3647", {"start": v(83.73, 50.32) * mm, "end": v(83.81, 50.42) * mm});
            skLineSegment(sketch, "E3648", {"start": v(83.81, 50.42) * mm, "end": v(83.9, 50.52) * mm});
            skLineSegment(sketch, "E3649", {"start": v(83.9, 50.52) * mm, "end": v(84, 50.63) * mm});
            skLineSegment(sketch, "E3650", {"start": v(84, 50.63) * mm, "end": v(84.08, 50.74) * mm});
            skLineSegment(sketch, "E3651", {"start": v(84.08, 50.74) * mm, "end": v(84.17, 50.85) * mm});
            skLineSegment(sketch, "E3652", {"start": v(84.17, 50.85) * mm, "end": v(84.26, 50.96) * mm});
            skLineSegment(sketch, "E3653", {"start": v(84.26, 50.96) * mm, "end": v(84.36, 51.07) * mm});
            skLineSegment(sketch, "E3654", {"start": v(84.36, 51.07) * mm, "end": v(84.45, 51.19) * mm});
            skLineSegment(sketch, "E3655", {"start": v(84.45, 51.19) * mm, "end": v(84.54, 51.3) * mm});
            skLineSegment(sketch, "E3656", {"start": v(84.54, 51.3) * mm, "end": v(84.63, 51.42) * mm});
            skLineSegment(sketch, "E3657", {"start": v(84.63, 51.42) * mm, "end": v(84.73, 51.54) * mm});
            skLineSegment(sketch, "E3658", {"start": v(84.73, 51.54) * mm, "end": v(84.82, 51.67) * mm});
            skLineSegment(sketch, "E3659", {"start": v(84.82, 51.67) * mm, "end": v(84.92, 51.79) * mm});
            skLineSegment(sketch, "E3660", {"start": v(84.92, 51.79) * mm, "end": v(85.01, 51.91) * mm});
            skLineSegment(sketch, "E3661", {"start": v(85.01, 51.91) * mm, "end": v(85.1, 52.04) * mm});
            skLineSegment(sketch, "E3662", {"start": v(85.1, 52.04) * mm, "end": v(85.2, 52.17) * mm});
            skLineSegment(sketch, "E3663", {"start": v(85.2, 52.17) * mm, "end": v(85.3, 52.3) * mm});
            skLineSegment(sketch, "E3664", {"start": v(85.3, 52.3) * mm, "end": v(85.4, 52.44) * mm});
            skLineSegment(sketch, "E3665", {"start": v(85.4, 52.44) * mm, "end": v(85.5, 52.57) * mm});
            skLineSegment(sketch, "E3666", {"start": v(85.5, 52.57) * mm, "end": v(85.6, 52.7) * mm});
            skLineSegment(sketch, "E3667", {"start": v(85.6, 52.7) * mm, "end": v(85.7, 52.85) * mm});
            skLineSegment(sketch, "E3668", {"start": v(85.7, 52.85) * mm, "end": v(85.8, 52.99) * mm});
            skLineSegment(sketch, "E3669", {"start": v(85.8, 52.99) * mm, "end": v(85.9, 53.13) * mm});
            skLineSegment(sketch, "E3670", {"start": v(85.9, 53.13) * mm, "end": v(86, 53.27) * mm});
            skLineSegment(sketch, "E3671", {"start": v(86, 53.27) * mm, "end": v(86.1, 53.42) * mm});
            skLineSegment(sketch, "E3672", {"start": v(86.1, 53.42) * mm, "end": v(86.2, 53.57) * mm});
            skLineSegment(sketch, "E3673", {"start": v(86.2, 53.57) * mm, "end": v(86.3, 53.72) * mm});
            skLineSegment(sketch, "E3674", {"start": v(86.3, 53.72) * mm, "end": v(86.4, 53.87) * mm});
            skLineSegment(sketch, "E3675", {"start": v(86.4, 53.87) * mm, "end": v(86.5, 54.02) * mm});
            skLineSegment(sketch, "E3676", {"start": v(86.5, 54.02) * mm, "end": v(86.6, 54.18) * mm});
            skLineSegment(sketch, "E3677", {"start": v(86.6, 54.18) * mm, "end": v(86.7, 54.34) * mm});
            skLineSegment(sketch, "E3678", {"start": v(86.7, 54.34) * mm, "end": v(86.8, 54.5) * mm});
            skLineSegment(sketch, "E3679", {"start": v(86.8, 54.5) * mm, "end": v(86.77, 54.57) * mm});
            skLineSegment(sketch, "E3680", {"start": v(86.77, 54.57) * mm, "end": v(85.92, 55.9) * mm});
            skLineSegment(sketch, "E3681", {"start": v(85.92, 55.9) * mm, "end": v(85.87, 55.96) * mm});
            skLineSegment(sketch, "E3682", {"start": v(85.87, 55.96) * mm, "end": v(85.69, 55.93) * mm});
            skLineSegment(sketch, "E3683", {"start": v(85.69, 55.93) * mm, "end": v(85.5, 55.9) * mm});
            skLineSegment(sketch, "E3684", {"start": v(85.5, 55.9) * mm, "end": v(85.32, 55.88) * mm});
            skLineSegment(sketch, "E3685", {"start": v(85.32, 55.88) * mm, "end": v(85.13, 55.85) * mm});
            skLineSegment(sketch, "E3686", {"start": v(85.13, 55.85) * mm, "end": v(84.95, 55.82) * mm});
            skLineSegment(sketch, "E3687", {"start": v(84.95, 55.82) * mm, "end": v(84.78, 55.8) * mm});
            skLineSegment(sketch, "E3688", {"start": v(84.78, 55.8) * mm, "end": v(84.6, 55.76) * mm});
            skLineSegment(sketch, "E3689", {"start": v(84.6, 55.76) * mm, "end": v(84.42, 55.73) * mm});
            skLineSegment(sketch, "E3690", {"start": v(84.42, 55.73) * mm, "end": v(84.25, 55.7) * mm});
            skLineSegment(sketch, "E3691", {"start": v(84.25, 55.7) * mm, "end": v(84.08, 55.67) * mm});
            skLineSegment(sketch, "E3692", {"start": v(84.08, 55.67) * mm, "end": v(83.91, 55.64) * mm});
            skLineSegment(sketch, "E3693", {"start": v(83.91, 55.64) * mm, "end": v(83.74, 55.6) * mm});
            skLineSegment(sketch, "E3694", {"start": v(83.74, 55.6) * mm, "end": v(83.58, 55.58) * mm});
            skLineSegment(sketch, "E3695", {"start": v(83.58, 55.58) * mm, "end": v(83.41, 55.54) * mm});
            skLineSegment(sketch, "E3696", {"start": v(83.41, 55.54) * mm, "end": v(83.25, 55.5) * mm});
            skLineSegment(sketch, "E3697", {"start": v(83.25, 55.5) * mm, "end": v(83.1, 55.48) * mm});
            skLineSegment(sketch, "E3698", {"start": v(83.1, 55.48) * mm, "end": v(82.93, 55.44) * mm});
            skLineSegment(sketch, "E3699", {"start": v(82.93, 55.44) * mm, "end": v(82.78, 55.4) * mm});
            skLineSegment(sketch, "E3700", {"start": v(82.78, 55.4) * mm, "end": v(82.62, 55.38) * mm});
            skLineSegment(sketch, "E3701", {"start": v(82.62, 55.38) * mm, "end": v(82.47, 55.34) * mm});
            skLineSegment(sketch, "E3702", {"start": v(82.47, 55.34) * mm, "end": v(82.32, 55.3) * mm});
            skLineSegment(sketch, "E3703", {"start": v(82.32, 55.3) * mm, "end": v(82.17, 55.27) * mm});
            skLineSegment(sketch, "E3704", {"start": v(82.17, 55.27) * mm, "end": v(82.03, 55.24) * mm});
            skLineSegment(sketch, "E3705", {"start": v(82.03, 55.24) * mm, "end": v(81.88, 55.2) * mm});
            skLineSegment(sketch, "E3706", {"start": v(81.88, 55.2) * mm, "end": v(81.74, 55.16) * mm});
            skLineSegment(sketch, "E3707", {"start": v(81.74, 55.16) * mm, "end": v(81.6, 55.13) * mm});
            skLineSegment(sketch, "E3708", {"start": v(81.6, 55.13) * mm, "end": v(81.46, 55.1) * mm});
            skLineSegment(sketch, "E3709", {"start": v(81.46, 55.1) * mm, "end": v(81.32, 55.06) * mm});
            skLineSegment(sketch, "E3710", {"start": v(81.32, 55.06) * mm, "end": v(81.18, 55.02) * mm});
            skLineSegment(sketch, "E3711", {"start": v(81.18, 55.02) * mm, "end": v(81.05, 54.98) * mm});
            skLineSegment(sketch, "E3712", {"start": v(81.05, 54.98) * mm, "end": v(80.92, 54.95) * mm});
            skLineSegment(sketch, "E3713", {"start": v(80.92, 54.95) * mm, "end": v(80.79, 54.91) * mm});
            skLineSegment(sketch, "E3714", {"start": v(80.79, 54.91) * mm, "end": v(80.66, 54.87) * mm});
            skLineSegment(sketch, "E3715", {"start": v(80.66, 54.87) * mm, "end": v(80.53, 54.84) * mm});
            skLineSegment(sketch, "E3716", {"start": v(80.53, 54.84) * mm, "end": v(80.4, 54.8) * mm});
            skLineSegment(sketch, "E3717", {"start": v(80.4, 54.8) * mm, "end": v(80.29, 54.76) * mm});
            skLineSegment(sketch, "E3718", {"start": v(80.29, 54.76) * mm, "end": v(79.7, 55.5) * mm});
            skLineSegment(sketch, "E3719", {"start": v(79.7, 55.5) * mm, "end": v(79.2, 56.31) * mm});
            skLineSegment(sketch, "E3720", {"start": v(79.2, 56.31) * mm, "end": v(79.29, 56.41) * mm});
            skLineSegment(sketch, "E3721", {"start": v(79.29, 56.41) * mm, "end": v(79.36, 56.52) * mm});
            skLineSegment(sketch, "E3722", {"start": v(79.36, 56.52) * mm, "end": v(79.44, 56.62) * mm});
            skLineSegment(sketch, "E3723", {"start": v(79.44, 56.62) * mm, "end": v(79.52, 56.73) * mm});
            skLineSegment(sketch, "E3724", {"start": v(79.52, 56.73) * mm, "end": v(79.6, 56.84) * mm});
            skLineSegment(sketch, "E3725", {"start": v(79.6, 56.84) * mm, "end": v(79.68, 56.95) * mm});
            skLineSegment(sketch, "E3726", {"start": v(79.68, 56.95) * mm, "end": v(79.76, 57.06) * mm});
            skLineSegment(sketch, "E3727", {"start": v(79.76, 57.06) * mm, "end": v(79.84, 57.18) * mm});
            skLineSegment(sketch, "E3728", {"start": v(79.84, 57.18) * mm, "end": v(79.92, 57.3) * mm});
            skLineSegment(sketch, "E3729", {"start": v(79.92, 57.3) * mm, "end": v(80, 57.41) * mm});
            skLineSegment(sketch, "E3730", {"start": v(80, 57.41) * mm, "end": v(80.09, 57.53) * mm});
            skLineSegment(sketch, "E3731", {"start": v(80.09, 57.53) * mm, "end": v(80.17, 57.66) * mm});
            skLineSegment(sketch, "E3732", {"start": v(80.17, 57.66) * mm, "end": v(80.25, 57.78) * mm});
            skLineSegment(sketch, "E3733", {"start": v(80.25, 57.78) * mm, "end": v(80.34, 57.9) * mm});
            skLineSegment(sketch, "E3734", {"start": v(80.34, 57.9) * mm, "end": v(80.42, 58.03) * mm});
            skLineSegment(sketch, "E3735", {"start": v(80.42, 58.03) * mm, "end": v(80.5, 58.16) * mm});
            skLineSegment(sketch, "E3736", {"start": v(80.5, 58.16) * mm, "end": v(80.6, 58.3) * mm});
            skLineSegment(sketch, "E3737", {"start": v(80.6, 58.3) * mm, "end": v(80.68, 58.42) * mm});
            skLineSegment(sketch, "E3738", {"start": v(80.68, 58.42) * mm, "end": v(80.76, 58.56) * mm});
            skLineSegment(sketch, "E3739", {"start": v(80.76, 58.56) * mm, "end": v(80.85, 58.7) * mm});
            skLineSegment(sketch, "E3740", {"start": v(80.85, 58.7) * mm, "end": v(80.94, 58.83) * mm});
            skLineSegment(sketch, "E3741", {"start": v(80.94, 58.83) * mm, "end": v(81.02, 58.97) * mm});
            skLineSegment(sketch, "E3742", {"start": v(81.02, 58.97) * mm, "end": v(81.11, 59.12) * mm});
            skLineSegment(sketch, "E3743", {"start": v(81.11, 59.12) * mm, "end": v(81.2, 59.26) * mm});
            skLineSegment(sketch, "E3744", {"start": v(81.2, 59.26) * mm, "end": v(81.29, 59.4) * mm});
            skLineSegment(sketch, "E3745", {"start": v(81.29, 59.4) * mm, "end": v(81.37, 59.56) * mm});
            skLineSegment(sketch, "E3746", {"start": v(81.37, 59.56) * mm, "end": v(81.46, 59.7) * mm});
            skLineSegment(sketch, "E3747", {"start": v(81.46, 59.7) * mm, "end": v(81.55, 59.86) * mm});
            skLineSegment(sketch, "E3748", {"start": v(81.55, 59.86) * mm, "end": v(81.64, 60.01) * mm});
            skLineSegment(sketch, "E3749", {"start": v(81.64, 60.01) * mm, "end": v(81.73, 60.17) * mm});
            skLineSegment(sketch, "E3750", {"start": v(81.73, 60.17) * mm, "end": v(81.82, 60.32) * mm});
            skLineSegment(sketch, "E3751", {"start": v(81.82, 60.32) * mm, "end": v(81.9, 60.48) * mm});
            skLineSegment(sketch, "E3752", {"start": v(81.9, 60.48) * mm, "end": v(82, 60.64) * mm});
            skLineSegment(sketch, "E3753", {"start": v(82, 60.64) * mm, "end": v(82.09, 60.8) * mm});
            skLineSegment(sketch, "E3754", {"start": v(82.09, 60.8) * mm, "end": v(82.18, 60.97) * mm});
            skLineSegment(sketch, "E3755", {"start": v(82.18, 60.97) * mm, "end": v(82.27, 61.14) * mm});
            skLineSegment(sketch, "E3756", {"start": v(82.27, 61.14) * mm, "end": v(82.22, 61.2) * mm});
            skLineSegment(sketch, "E3757", {"start": v(82.22, 61.2) * mm, "end": v(81.27, 62.46) * mm});
            skLineSegment(sketch, "E3758", {"start": v(81.27, 62.46) * mm, "end": v(81.22, 62.52) * mm});
            skLineSegment(sketch, "E3759", {"start": v(81.22, 62.52) * mm, "end": v(81.03, 62.48) * mm});
            skLineSegment(sketch, "E3760", {"start": v(81.03, 62.48) * mm, "end": v(80.85, 62.44) * mm});
            skLineSegment(sketch, "E3761", {"start": v(80.85, 62.44) * mm, "end": v(80.67, 62.4) * mm});
            skLineSegment(sketch, "E3762", {"start": v(80.67, 62.4) * mm, "end": v(80.5, 62.36) * mm});
            skLineSegment(sketch, "E3763", {"start": v(80.5, 62.36) * mm, "end": v(80.31, 62.31) * mm});
            skLineSegment(sketch, "E3764", {"start": v(80.31, 62.31) * mm, "end": v(80.14, 62.27) * mm});
            skLineSegment(sketch, "E3765", {"start": v(80.14, 62.27) * mm, "end": v(79.96, 62.23) * mm});
            skLineSegment(sketch, "E3766", {"start": v(79.96, 62.23) * mm, "end": v(79.8, 62.18) * mm});
            skLineSegment(sketch, "E3767", {"start": v(79.8, 62.18) * mm, "end": v(79.62, 62.14) * mm});
            skLineSegment(sketch, "E3768", {"start": v(79.62, 62.14) * mm, "end": v(79.45, 62.1) * mm});
            skLineSegment(sketch, "E3769", {"start": v(79.45, 62.1) * mm, "end": v(79.29, 62.05) * mm});
            skLineSegment(sketch, "E3770", {"start": v(79.29, 62.05) * mm, "end": v(79.12, 62) * mm});
            skLineSegment(sketch, "E3771", {"start": v(79.12, 62) * mm, "end": v(78.96, 61.96) * mm});
            skLineSegment(sketch, "E3772", {"start": v(78.96, 61.96) * mm, "end": v(78.8, 61.92) * mm});
            skLineSegment(sketch, "E3773", {"start": v(78.8, 61.92) * mm, "end": v(78.64, 61.87) * mm});
            skLineSegment(sketch, "E3774", {"start": v(78.64, 61.87) * mm, "end": v(78.48, 61.83) * mm});
            skLineSegment(sketch, "E3775", {"start": v(78.48, 61.83) * mm, "end": v(78.33, 61.78) * mm});
            skLineSegment(sketch, "E3776", {"start": v(78.33, 61.78) * mm, "end": v(78.18, 61.73) * mm});
            skLineSegment(sketch, "E3777", {"start": v(78.18, 61.73) * mm, "end": v(78.02, 61.69) * mm});
            skLineSegment(sketch, "E3778", {"start": v(78.02, 61.69) * mm, "end": v(77.88, 61.64) * mm});
            skLineSegment(sketch, "E3779", {"start": v(77.88, 61.64) * mm, "end": v(77.73, 61.6) * mm});
            skLineSegment(sketch, "E3780", {"start": v(77.73, 61.6) * mm, "end": v(77.58, 61.55) * mm});
            skLineSegment(sketch, "E3781", {"start": v(77.58, 61.55) * mm, "end": v(77.44, 61.5) * mm});
            skLineSegment(sketch, "E3782", {"start": v(77.44, 61.5) * mm, "end": v(77.3, 61.45) * mm});
            skLineSegment(sketch, "E3783", {"start": v(77.3, 61.45) * mm, "end": v(77.16, 61.4) * mm});
            skLineSegment(sketch, "E3784", {"start": v(77.16, 61.4) * mm, "end": v(77.02, 61.36) * mm});
            skLineSegment(sketch, "E3785", {"start": v(77.02, 61.36) * mm, "end": v(76.88, 61.31) * mm});
            skLineSegment(sketch, "E3786", {"start": v(76.88, 61.31) * mm, "end": v(76.75, 61.27) * mm});
            skLineSegment(sketch, "E3787", {"start": v(76.75, 61.27) * mm, "end": v(76.62, 61.22) * mm});
            skLineSegment(sketch, "E3788", {"start": v(76.62, 61.22) * mm, "end": v(76.49, 61.17) * mm});
            skLineSegment(sketch, "E3789", {"start": v(76.49, 61.17) * mm, "end": v(76.36, 61.13) * mm});
            skLineSegment(sketch, "E3790", {"start": v(76.36, 61.13) * mm, "end": v(76.23, 61.08) * mm});
            skLineSegment(sketch, "E3791", {"start": v(76.23, 61.08) * mm, "end": v(76.1, 61.03) * mm});
            skLineSegment(sketch, "E3792", {"start": v(76.1, 61.03) * mm, "end": v(75.98, 60.99) * mm});
            skLineSegment(sketch, "E3793", {"start": v(75.98, 60.99) * mm, "end": v(75.86, 60.94) * mm});
            skLineSegment(sketch, "E3794", {"start": v(75.86, 60.94) * mm, "end": v(75.74, 60.9) * mm});
            skLineSegment(sketch, "E3795", {"start": v(75.74, 60.9) * mm, "end": v(75.1, 61.59) * mm});
            skLineSegment(sketch, "E3796", {"start": v(75.1, 61.59) * mm, "end": v(74.55, 62.35) * mm});
            skLineSegment(sketch, "E3797", {"start": v(74.55, 62.35) * mm, "end": v(74.62, 62.46) * mm});
            skLineSegment(sketch, "E3798", {"start": v(74.62, 62.46) * mm, "end": v(74.68, 62.57) * mm});
            skLineSegment(sketch, "E3799", {"start": v(74.68, 62.57) * mm, "end": v(74.75, 62.68) * mm});
            skLineSegment(sketch, "E3800", {"start": v(74.75, 62.68) * mm, "end": v(74.82, 62.8) * mm});
            skLineSegment(sketch, "E3801", {"start": v(74.82, 62.8) * mm, "end": v(74.9, 62.91) * mm});
            skLineSegment(sketch, "E3802", {"start": v(74.9, 62.91) * mm, "end": v(74.97, 63.03) * mm});
            skLineSegment(sketch, "E3803", {"start": v(74.97, 63.03) * mm, "end": v(75.04, 63.15) * mm});
            skLineSegment(sketch, "E3804", {"start": v(75.04, 63.15) * mm, "end": v(75.1, 63.27) * mm});
            skLineSegment(sketch, "E3805", {"start": v(75.1, 63.27) * mm, "end": v(75.18, 63.39) * mm});
            skLineSegment(sketch, "E3806", {"start": v(75.18, 63.39) * mm, "end": v(75.25, 63.51) * mm});
            skLineSegment(sketch, "E3807", {"start": v(75.25, 63.51) * mm, "end": v(75.33, 63.64) * mm});
            skLineSegment(sketch, "E3808", {"start": v(75.33, 63.64) * mm, "end": v(75.4, 63.77) * mm});
            skLineSegment(sketch, "E3809", {"start": v(75.4, 63.77) * mm, "end": v(75.47, 63.9) * mm});
            skLineSegment(sketch, "E3810", {"start": v(75.47, 63.9) * mm, "end": v(75.55, 64.03) * mm});
            skLineSegment(sketch, "E3811", {"start": v(75.55, 64.03) * mm, "end": v(75.62, 64.16) * mm});
            skLineSegment(sketch, "E3812", {"start": v(75.62, 64.16) * mm, "end": v(75.7, 64.3) * mm});
            skLineSegment(sketch, "E3813", {"start": v(75.7, 64.3) * mm, "end": v(75.77, 64.44) * mm});
            skLineSegment(sketch, "E3814", {"start": v(75.77, 64.44) * mm, "end": v(75.85, 64.57) * mm});
            skLineSegment(sketch, "E3815", {"start": v(75.85, 64.57) * mm, "end": v(75.92, 64.72) * mm});
            skLineSegment(sketch, "E3816", {"start": v(75.92, 64.72) * mm, "end": v(76, 64.86) * mm});
            skLineSegment(sketch, "E3817", {"start": v(76, 64.86) * mm, "end": v(76.07, 65) * mm});
            skLineSegment(sketch, "E3818", {"start": v(76.07, 65) * mm, "end": v(76.15, 65.15) * mm});
            skLineSegment(sketch, "E3819", {"start": v(76.15, 65.15) * mm, "end": v(76.22, 65.3) * mm});
            skLineSegment(sketch, "E3820", {"start": v(76.22, 65.3) * mm, "end": v(76.3, 65.45) * mm});
            skLineSegment(sketch, "E3821", {"start": v(76.3, 65.45) * mm, "end": v(76.37, 65.6) * mm});
            skLineSegment(sketch, "E3822", {"start": v(76.37, 65.6) * mm, "end": v(76.45, 65.76) * mm});
            skLineSegment(sketch, "E3823", {"start": v(76.45, 65.76) * mm, "end": v(76.53, 65.91) * mm});
            skLineSegment(sketch, "E3824", {"start": v(76.53, 65.91) * mm, "end": v(76.6, 66.07) * mm});
            skLineSegment(sketch, "E3825", {"start": v(76.6, 66.07) * mm, "end": v(76.68, 66.23) * mm});
            skLineSegment(sketch, "E3826", {"start": v(76.68, 66.23) * mm, "end": v(76.76, 66.4) * mm});
            skLineSegment(sketch, "E3827", {"start": v(76.76, 66.4) * mm, "end": v(76.83, 66.56) * mm});
            skLineSegment(sketch, "E3828", {"start": v(76.83, 66.56) * mm, "end": v(76.9, 66.72) * mm});
            skLineSegment(sketch, "E3829", {"start": v(76.9, 66.72) * mm, "end": v(76.99, 66.9) * mm});
            skLineSegment(sketch, "E3830", {"start": v(76.99, 66.9) * mm, "end": v(77.06, 67.06) * mm});
            skLineSegment(sketch, "E3831", {"start": v(77.06, 67.06) * mm, "end": v(77.14, 67.23) * mm});
            skLineSegment(sketch, "E3832", {"start": v(77.14, 67.23) * mm, "end": v(77.22, 67.4) * mm});
            skLineSegment(sketch, "E3833", {"start": v(77.22, 67.4) * mm, "end": v(77.16, 67.47) * mm});
            skLineSegment(sketch, "E3834", {"start": v(77.16, 67.47) * mm, "end": v(76.12, 68.64) * mm});
            skLineSegment(sketch, "E3835", {"start": v(76.12, 68.64) * mm, "end": v(76.06, 68.7) * mm});
            skLineSegment(sketch, "E3836", {"start": v(76.06, 68.7) * mm, "end": v(75.88, 68.65) * mm});
            skLineSegment(sketch, "E3837", {"start": v(75.88, 68.65) * mm, "end": v(75.7, 68.6) * mm});
            skLineSegment(sketch, "E3838", {"start": v(75.7, 68.6) * mm, "end": v(75.53, 68.54) * mm});
            skLineSegment(sketch, "E3839", {"start": v(75.53, 68.54) * mm, "end": v(75.35, 68.48) * mm});
            skLineSegment(sketch, "E3840", {"start": v(75.35, 68.48) * mm, "end": v(75.18, 68.42) * mm});
            skLineSegment(sketch, "E3841", {"start": v(75.18, 68.42) * mm, "end": v(75, 68.37) * mm});
            skLineSegment(sketch, "E3842", {"start": v(75, 68.37) * mm, "end": v(74.83, 68.3) * mm});
            skLineSegment(sketch, "E3843", {"start": v(74.83, 68.3) * mm, "end": v(74.67, 68.25) * mm});
            skLineSegment(sketch, "E3844", {"start": v(74.67, 68.25) * mm, "end": v(74.5, 68.2) * mm});
            skLineSegment(sketch, "E3845", {"start": v(74.5, 68.2) * mm, "end": v(74.34, 68.14) * mm});
            skLineSegment(sketch, "E3846", {"start": v(74.34, 68.14) * mm, "end": v(74.17, 68.08) * mm});
            skLineSegment(sketch, "E3847", {"start": v(74.17, 68.08) * mm, "end": v(74.01, 68.02) * mm});
            skLineSegment(sketch, "E3848", {"start": v(74.01, 68.02) * mm, "end": v(73.85, 67.97) * mm});
            skLineSegment(sketch, "E3849", {"start": v(73.85, 67.97) * mm, "end": v(73.7, 67.9) * mm});
            skLineSegment(sketch, "E3850", {"start": v(73.7, 67.9) * mm, "end": v(73.54, 67.85) * mm});
            skLineSegment(sketch, "E3851", {"start": v(73.54, 67.85) * mm, "end": v(73.4, 67.8) * mm});
            skLineSegment(sketch, "E3852", {"start": v(73.4, 67.8) * mm, "end": v(73.24, 67.73) * mm});
            skLineSegment(sketch, "E3853", {"start": v(73.24, 67.73) * mm, "end": v(73.1, 67.68) * mm});
            skLineSegment(sketch, "E3854", {"start": v(73.1, 67.68) * mm, "end": v(72.94, 67.62) * mm});
            skLineSegment(sketch, "E3855", {"start": v(72.94, 67.62) * mm, "end": v(72.8, 67.56) * mm});
            skLineSegment(sketch, "E3856", {"start": v(72.8, 67.56) * mm, "end": v(72.66, 67.5) * mm});
            skLineSegment(sketch, "E3857", {"start": v(72.66, 67.5) * mm, "end": v(72.51, 67.45) * mm});
            skLineSegment(sketch, "E3858", {"start": v(72.51, 67.45) * mm, "end": v(72.37, 67.39) * mm});
            skLineSegment(sketch, "E3859", {"start": v(72.37, 67.39) * mm, "end": v(72.24, 67.33) * mm});
            skLineSegment(sketch, "E3860", {"start": v(72.24, 67.33) * mm, "end": v(72.1, 67.27) * mm});
            skLineSegment(sketch, "E3861", {"start": v(72.1, 67.27) * mm, "end": v(71.97, 67.21) * mm});
            skLineSegment(sketch, "E3862", {"start": v(71.97, 67.21) * mm, "end": v(71.84, 67.16) * mm});
            skLineSegment(sketch, "E3863", {"start": v(71.84, 67.16) * mm, "end": v(71.7, 67.1) * mm});
            skLineSegment(sketch, "E3864", {"start": v(71.7, 67.1) * mm, "end": v(71.58, 67.04) * mm});
            skLineSegment(sketch, "E3865", {"start": v(71.58, 67.04) * mm, "end": v(71.45, 66.99) * mm});
            skLineSegment(sketch, "E3866", {"start": v(71.45, 66.99) * mm, "end": v(71.33, 66.93) * mm});
            skLineSegment(sketch, "E3867", {"start": v(71.33, 66.93) * mm, "end": v(71.2, 66.87) * mm});
            skLineSegment(sketch, "E3868", {"start": v(71.2, 66.87) * mm, "end": v(71.08, 66.82) * mm});
            skLineSegment(sketch, "E3869", {"start": v(71.08, 66.82) * mm, "end": v(70.96, 66.76) * mm});
            skLineSegment(sketch, "E3870", {"start": v(70.96, 66.76) * mm, "end": v(70.85, 66.7) * mm});
            skLineSegment(sketch, "E3871", {"start": v(70.85, 66.7) * mm, "end": v(70.73, 66.65) * mm});
            skLineSegment(sketch, "E3872", {"start": v(70.73, 66.65) * mm, "end": v(70.04, 67.3) * mm});
            skLineSegment(sketch, "E3873", {"start": v(70.04, 67.3) * mm, "end": v(69.42, 68.01) * mm});
            skLineSegment(sketch, "E3874", {"start": v(69.42, 68.01) * mm, "end": v(69.48, 68.12) * mm});
            skLineSegment(sketch, "E3875", {"start": v(69.48, 68.12) * mm, "end": v(69.55, 68.24) * mm});
            skLineSegment(sketch, "E3876", {"start": v(69.55, 68.24) * mm, "end": v(69.6, 68.35) * mm});
            skLineSegment(sketch, "E3877", {"start": v(69.6, 68.35) * mm, "end": v(69.67, 68.47) * mm});
            skLineSegment(sketch, "E3878", {"start": v(69.67, 68.47) * mm, "end": v(69.73, 68.6) * mm});
            skLineSegment(sketch, "E3879", {"start": v(69.73, 68.6) * mm, "end": v(69.8, 68.72) * mm});
            skLineSegment(sketch, "E3880", {"start": v(69.8, 68.72) * mm, "end": v(69.85, 68.84) * mm});
            skLineSegment(sketch, "E3881", {"start": v(69.85, 68.84) * mm, "end": v(69.91, 68.97) * mm});
            skLineSegment(sketch, "E3882", {"start": v(69.91, 68.97) * mm, "end": v(69.98, 69.1) * mm});
            skLineSegment(sketch, "E3883", {"start": v(69.98, 69.1) * mm, "end": v(70.04, 69.22) * mm});
            skLineSegment(sketch, "E3884", {"start": v(70.04, 69.22) * mm, "end": v(70.1, 69.35) * mm});
            skLineSegment(sketch, "E3885", {"start": v(70.1, 69.35) * mm, "end": v(70.16, 69.49) * mm});
            skLineSegment(sketch, "E3886", {"start": v(70.16, 69.49) * mm, "end": v(70.23, 69.62) * mm});
            skLineSegment(sketch, "E3887", {"start": v(70.23, 69.62) * mm, "end": v(70.3, 69.76) * mm});
            skLineSegment(sketch, "E3888", {"start": v(70.3, 69.76) * mm, "end": v(70.35, 69.9) * mm});
            skLineSegment(sketch, "E3889", {"start": v(70.35, 69.9) * mm, "end": v(70.42, 70.04) * mm});
            skLineSegment(sketch, "E3890", {"start": v(70.42, 70.04) * mm, "end": v(70.48, 70.18) * mm});
            skLineSegment(sketch, "E3891", {"start": v(70.48, 70.18) * mm, "end": v(70.55, 70.33) * mm});
            skLineSegment(sketch, "E3892", {"start": v(70.55, 70.33) * mm, "end": v(70.6, 70.47) * mm});
            skLineSegment(sketch, "E3893", {"start": v(70.6, 70.47) * mm, "end": v(70.67, 70.62) * mm});
            skLineSegment(sketch, "E3894", {"start": v(70.67, 70.62) * mm, "end": v(70.74, 70.77) * mm});
            skLineSegment(sketch, "E3895", {"start": v(70.74, 70.77) * mm, "end": v(70.8, 70.92) * mm});
            skLineSegment(sketch, "E3896", {"start": v(70.8, 70.92) * mm, "end": v(70.86, 71.08) * mm});
            skLineSegment(sketch, "E3897", {"start": v(70.86, 71.08) * mm, "end": v(70.93, 71.23) * mm});
            skLineSegment(sketch, "E3898", {"start": v(70.93, 71.23) * mm, "end": v(71, 71.4) * mm});
            skLineSegment(sketch, "E3899", {"start": v(71, 71.4) * mm, "end": v(71.06, 71.55) * mm});
            skLineSegment(sketch, "E3900", {"start": v(71.06, 71.55) * mm, "end": v(71.12, 71.71) * mm});
            skLineSegment(sketch, "E3901", {"start": v(71.12, 71.71) * mm, "end": v(71.18, 71.88) * mm});
            skLineSegment(sketch, "E3902", {"start": v(71.18, 71.88) * mm, "end": v(71.25, 72.04) * mm});
            skLineSegment(sketch, "E3903", {"start": v(71.25, 72.04) * mm, "end": v(71.31, 72.21) * mm});
            skLineSegment(sketch, "E3904", {"start": v(71.31, 72.21) * mm, "end": v(71.37, 72.38) * mm});
            skLineSegment(sketch, "E3905", {"start": v(71.37, 72.38) * mm, "end": v(71.44, 72.55) * mm});
            skLineSegment(sketch, "E3906", {"start": v(71.44, 72.55) * mm, "end": v(71.5, 72.72) * mm});
            skLineSegment(sketch, "E3907", {"start": v(71.5, 72.72) * mm, "end": v(71.56, 72.9) * mm});
            skLineSegment(sketch, "E3908", {"start": v(71.56, 72.9) * mm, "end": v(71.63, 73.08) * mm});
            skLineSegment(sketch, "E3909", {"start": v(71.63, 73.08) * mm, "end": v(71.69, 73.26) * mm});
            skLineSegment(sketch, "E3910", {"start": v(71.69, 73.26) * mm, "end": v(71.63, 73.31) * mm});
            skLineSegment(sketch, "E3911", {"start": v(71.63, 73.31) * mm, "end": v(70.5, 74.4) * mm});
            skLineSegment(sketch, "E3912", {"start": v(70.5, 74.4) * mm, "end": v(70.44, 74.46) * mm});
            skLineSegment(sketch, "E3913", {"start": v(70.44, 74.46) * mm, "end": v(70.26, 74.39) * mm});
            skLineSegment(sketch, "E3914", {"start": v(70.26, 74.39) * mm, "end": v(70.09, 74.32) * mm});
            skLineSegment(sketch, "E3915", {"start": v(70.09, 74.32) * mm, "end": v(69.92, 74.25) * mm});
            skLineSegment(sketch, "E3916", {"start": v(69.92, 74.25) * mm, "end": v(69.74, 74.18) * mm});
            skLineSegment(sketch, "E3917", {"start": v(69.74, 74.18) * mm, "end": v(69.58, 74.11) * mm});
            skLineSegment(sketch, "E3918", {"start": v(69.58, 74.11) * mm, "end": v(69.4, 74.04) * mm});
            skLineSegment(sketch, "E3919", {"start": v(69.4, 74.04) * mm, "end": v(69.24, 73.97) * mm});
            skLineSegment(sketch, "E3920", {"start": v(69.24, 73.97) * mm, "end": v(69.08, 73.9) * mm});
            skLineSegment(sketch, "E3921", {"start": v(69.08, 73.9) * mm, "end": v(68.92, 73.83) * mm});
            skLineSegment(sketch, "E3922", {"start": v(68.92, 73.83) * mm, "end": v(68.76, 73.76) * mm});
            skLineSegment(sketch, "E3923", {"start": v(68.76, 73.76) * mm, "end": v(68.6, 73.7) * mm});
            skLineSegment(sketch, "E3924", {"start": v(68.6, 73.7) * mm, "end": v(68.45, 73.62) * mm});
            skLineSegment(sketch, "E3925", {"start": v(68.45, 73.62) * mm, "end": v(68.3, 73.55) * mm});
            skLineSegment(sketch, "E3926", {"start": v(68.3, 73.55) * mm, "end": v(68.14, 73.48) * mm});
            skLineSegment(sketch, "E3927", {"start": v(68.14, 73.48) * mm, "end": v(68, 73.41) * mm});
            skLineSegment(sketch, "E3928", {"start": v(68, 73.41) * mm, "end": v(67.85, 73.34) * mm});
            skLineSegment(sketch, "E3929", {"start": v(67.85, 73.34) * mm, "end": v(67.7, 73.27) * mm});
            skLineSegment(sketch, "E3930", {"start": v(67.7, 73.27) * mm, "end": v(67.56, 73.2) * mm});
            skLineSegment(sketch, "E3931", {"start": v(67.56, 73.2) * mm, "end": v(67.41, 73.13) * mm});
            skLineSegment(sketch, "E3932", {"start": v(67.41, 73.13) * mm, "end": v(67.27, 73.06) * mm});
            skLineSegment(sketch, "E3933", {"start": v(67.27, 73.06) * mm, "end": v(67.14, 73) * mm});
            skLineSegment(sketch, "E3934", {"start": v(67.14, 73) * mm, "end": v(67, 72.93) * mm});
            skLineSegment(sketch, "E3935", {"start": v(67, 72.93) * mm, "end": v(66.86, 72.86) * mm});
            skLineSegment(sketch, "E3936", {"start": v(66.86, 72.86) * mm, "end": v(66.73, 72.8) * mm});
            skLineSegment(sketch, "E3937", {"start": v(66.73, 72.8) * mm, "end": v(66.6, 72.72) * mm});
            skLineSegment(sketch, "E3938", {"start": v(66.6, 72.72) * mm, "end": v(66.47, 72.65) * mm});
            skLineSegment(sketch, "E3939", {"start": v(66.47, 72.65) * mm, "end": v(66.35, 72.59) * mm});
            skLineSegment(sketch, "E3940", {"start": v(66.35, 72.59) * mm, "end": v(66.22, 72.52) * mm});
            skLineSegment(sketch, "E3941", {"start": v(66.22, 72.52) * mm, "end": v(66.1, 72.45) * mm});
            skLineSegment(sketch, "E3942", {"start": v(66.1, 72.45) * mm, "end": v(65.98, 72.39) * mm});
            skLineSegment(sketch, "E3943", {"start": v(65.98, 72.39) * mm, "end": v(65.86, 72.32) * mm});
            skLineSegment(sketch, "E3944", {"start": v(65.86, 72.32) * mm, "end": v(65.74, 72.25) * mm});
            skLineSegment(sketch, "E3945", {"start": v(65.74, 72.25) * mm, "end": v(65.62, 72.19) * mm});
            skLineSegment(sketch, "E3946", {"start": v(65.62, 72.19) * mm, "end": v(65.5, 72.12) * mm});
            skLineSegment(sketch, "E3947", {"start": v(65.5, 72.12) * mm, "end": v(65.4, 72.06) * mm});
            skLineSegment(sketch, "E3948", {"start": v(65.4, 72.06) * mm, "end": v(65.28, 72) * mm});
            skLineSegment(sketch, "E3949", {"start": v(65.28, 72) * mm, "end": v(64.54, 72.58) * mm});
            skLineSegment(sketch, "E3950", {"start": v(64.54, 72.58) * mm, "end": v(63.87, 73.25) * mm});
            skLineSegment(sketch, "E3951", {"start": v(63.87, 73.25) * mm, "end": v(63.93, 73.36) * mm});
            skLineSegment(sketch, "E3952", {"start": v(63.93, 73.36) * mm, "end": v(63.98, 73.48) * mm});
            skLineSegment(sketch, "E3953", {"start": v(63.98, 73.48) * mm, "end": v(64.03, 73.6) * mm});
            skLineSegment(sketch, "E3954", {"start": v(64.03, 73.6) * mm, "end": v(64.08, 73.73) * mm});
            skLineSegment(sketch, "E3955", {"start": v(64.08, 73.73) * mm, "end": v(64.13, 73.85) * mm});
            skLineSegment(sketch, "E3956", {"start": v(64.13, 73.85) * mm, "end": v(64.18, 73.98) * mm});
            skLineSegment(sketch, "E3957", {"start": v(64.18, 73.98) * mm, "end": v(64.24, 74.1) * mm});
            skLineSegment(sketch, "E3958", {"start": v(64.24, 74.1) * mm, "end": v(64.29, 74.24) * mm});
            skLineSegment(sketch, "E3959", {"start": v(64.29, 74.24) * mm, "end": v(64.34, 74.37) * mm});
            skLineSegment(sketch, "E3960", {"start": v(64.34, 74.37) * mm, "end": v(64.4, 74.5) * mm});
            skLineSegment(sketch, "E3961", {"start": v(64.4, 74.5) * mm, "end": v(64.44, 74.64) * mm});
            skLineSegment(sketch, "E3962", {"start": v(64.44, 74.64) * mm, "end": v(64.5, 74.78) * mm});
            skLineSegment(sketch, "E3963", {"start": v(64.5, 74.78) * mm, "end": v(64.55, 74.92) * mm});
            skLineSegment(sketch, "E3964", {"start": v(64.55, 74.92) * mm, "end": v(64.6, 75.06) * mm});
            skLineSegment(sketch, "E3965", {"start": v(64.6, 75.06) * mm, "end": v(64.65, 75.2) * mm});
            skLineSegment(sketch, "E3966", {"start": v(64.65, 75.2) * mm, "end": v(64.7, 75.35) * mm});
            skLineSegment(sketch, "E3967", {"start": v(64.7, 75.35) * mm, "end": v(64.76, 75.5) * mm});
            skLineSegment(sketch, "E3968", {"start": v(64.76, 75.5) * mm, "end": v(64.8, 75.64) * mm});
            skLineSegment(sketch, "E3969", {"start": v(64.8, 75.64) * mm, "end": v(64.86, 75.8) * mm});
            skLineSegment(sketch, "E3970", {"start": v(64.86, 75.8) * mm, "end": v(64.91, 75.95) * mm});
            skLineSegment(sketch, "E3971", {"start": v(64.91, 75.95) * mm, "end": v(64.97, 76.1) * mm});
            skLineSegment(sketch, "E3972", {"start": v(64.97, 76.1) * mm, "end": v(65.02, 76.26) * mm});
            skLineSegment(sketch, "E3973", {"start": v(65.02, 76.26) * mm, "end": v(65.07, 76.42) * mm});
            skLineSegment(sketch, "E3974", {"start": v(65.07, 76.42) * mm, "end": v(65.12, 76.58) * mm});
            skLineSegment(sketch, "E3975", {"start": v(65.12, 76.58) * mm, "end": v(65.17, 76.74) * mm});
            skLineSegment(sketch, "E3976", {"start": v(65.17, 76.74) * mm, "end": v(65.22, 76.9) * mm});
            skLineSegment(sketch, "E3977", {"start": v(65.22, 76.9) * mm, "end": v(65.27, 77.07) * mm});
            skLineSegment(sketch, "E3978", {"start": v(65.27, 77.07) * mm, "end": v(65.32, 77.24) * mm});
            skLineSegment(sketch, "E3979", {"start": v(65.32, 77.24) * mm, "end": v(65.38, 77.41) * mm});
            skLineSegment(sketch, "E3980", {"start": v(65.38, 77.41) * mm, "end": v(65.43, 77.58) * mm});
            skLineSegment(sketch, "E3981", {"start": v(65.43, 77.58) * mm, "end": v(65.48, 77.76) * mm});
            skLineSegment(sketch, "E3982", {"start": v(65.48, 77.76) * mm, "end": v(65.52, 77.93) * mm});
            skLineSegment(sketch, "E3983", {"start": v(65.52, 77.93) * mm, "end": v(65.57, 78.1) * mm});
            skLineSegment(sketch, "E3984", {"start": v(65.57, 78.1) * mm, "end": v(65.62, 78.29) * mm});
            skLineSegment(sketch, "E3985", {"start": v(65.62, 78.29) * mm, "end": v(65.67, 78.47) * mm});
            skLineSegment(sketch, "E3986", {"start": v(65.67, 78.47) * mm, "end": v(65.72, 78.65) * mm});
            skLineSegment(sketch, "E3987", {"start": v(65.72, 78.65) * mm, "end": v(65.66, 78.7) * mm});
            skLineSegment(sketch, "E3988", {"start": v(65.66, 78.7) * mm, "end": v(64.45, 79.7) * mm});
            skLineSegment(sketch, "E3989", {"start": v(64.45, 79.7) * mm, "end": v(64.38, 79.76) * mm});
            skLineSegment(sketch, "E3990", {"start": v(64.38, 79.76) * mm, "end": v(64.2, 79.67) * mm});
            skLineSegment(sketch, "E3991", {"start": v(64.2, 79.67) * mm, "end": v(64.04, 79.59) * mm});
            skLineSegment(sketch, "E3992", {"start": v(64.04, 79.59) * mm, "end": v(63.87, 79.5) * mm});
            skLineSegment(sketch, "E3993", {"start": v(63.87, 79.5) * mm, "end": v(63.7, 79.42) * mm});
            skLineSegment(sketch, "E3994", {"start": v(63.7, 79.42) * mm, "end": v(63.55, 79.34) * mm});
            skLineSegment(sketch, "E3995", {"start": v(63.55, 79.34) * mm, "end": v(63.39, 79.26) * mm});
            skLineSegment(sketch, "E3996", {"start": v(63.39, 79.26) * mm, "end": v(63.23, 79.17) * mm});
            skLineSegment(sketch, "E3997", {"start": v(63.23, 79.17) * mm, "end": v(63.07, 79.1) * mm});
            skLineSegment(sketch, "E3998", {"start": v(63.07, 79.1) * mm, "end": v(62.91, 79.01) * mm});
            skLineSegment(sketch, "E3999", {"start": v(62.91, 79.01) * mm, "end": v(62.76, 78.93) * mm});
            skLineSegment(sketch, "E4000", {"start": v(62.76, 78.93) * mm, "end": v(62.61, 78.85) * mm});
            skLineSegment(sketch, "E4001", {"start": v(62.61, 78.85) * mm, "end": v(62.46, 78.76) * mm});
            skLineSegment(sketch, "E4002", {"start": v(62.46, 78.76) * mm, "end": v(62.31, 78.68) * mm});
            skLineSegment(sketch, "E4003", {"start": v(62.31, 78.68) * mm, "end": v(62.17, 78.6) * mm});
            skLineSegment(sketch, "E4004", {"start": v(62.17, 78.6) * mm, "end": v(62.02, 78.52) * mm});
            skLineSegment(sketch, "E4005", {"start": v(62.02, 78.52) * mm, "end": v(61.88, 78.44) * mm});
            skLineSegment(sketch, "E4006", {"start": v(61.88, 78.44) * mm, "end": v(61.74, 78.36) * mm});
            skLineSegment(sketch, "E4007", {"start": v(61.74, 78.36) * mm, "end": v(61.6, 78.28) * mm});
            skLineSegment(sketch, "E4008", {"start": v(61.6, 78.28) * mm, "end": v(61.47, 78.2) * mm});
            skLineSegment(sketch, "E4009", {"start": v(61.47, 78.2) * mm, "end": v(61.33, 78.12) * mm});
            skLineSegment(sketch, "E4010", {"start": v(61.33, 78.12) * mm, "end": v(61.2, 78.04) * mm});
            skLineSegment(sketch, "E4011", {"start": v(61.2, 78.04) * mm, "end": v(61.07, 77.96) * mm});
            skLineSegment(sketch, "E4012", {"start": v(61.07, 77.96) * mm, "end": v(60.94, 77.88) * mm});
            skLineSegment(sketch, "E4013", {"start": v(60.94, 77.88) * mm, "end": v(60.82, 77.8) * mm});
            skLineSegment(sketch, "E4014", {"start": v(60.82, 77.8) * mm, "end": v(60.7, 77.72) * mm});
            skLineSegment(sketch, "E4015", {"start": v(60.7, 77.72) * mm, "end": v(60.57, 77.65) * mm});
            skLineSegment(sketch, "E4016", {"start": v(60.57, 77.65) * mm, "end": v(60.45, 77.57) * mm});
            skLineSegment(sketch, "E4017", {"start": v(60.45, 77.57) * mm, "end": v(60.33, 77.5) * mm});
            skLineSegment(sketch, "E4018", {"start": v(60.33, 77.5) * mm, "end": v(60.2, 77.42) * mm});
            skLineSegment(sketch, "E4019", {"start": v(60.2, 77.42) * mm, "end": v(60.1, 77.34) * mm});
            skLineSegment(sketch, "E4020", {"start": v(60.1, 77.34) * mm, "end": v(59.98, 77.26) * mm});
            skLineSegment(sketch, "E4021", {"start": v(59.98, 77.26) * mm, "end": v(59.87, 77.19) * mm});
            skLineSegment(sketch, "E4022", {"start": v(59.87, 77.19) * mm, "end": v(59.76, 77.11) * mm});
            skLineSegment(sketch, "E4023", {"start": v(59.76, 77.11) * mm, "end": v(59.65, 77.04) * mm});
            skLineSegment(sketch, "E4024", {"start": v(59.65, 77.04) * mm, "end": v(59.54, 76.97) * mm});
            skLineSegment(sketch, "E4025", {"start": v(59.54, 76.97) * mm, "end": v(59.43, 76.9) * mm});
            skLineSegment(sketch, "E4026", {"start": v(59.43, 76.9) * mm, "end": v(58.65, 77.42) * mm});
            skLineSegment(sketch, "E4027", {"start": v(58.65, 77.42) * mm, "end": v(57.93, 78.03) * mm});
            skLineSegment(sketch, "E4028", {"start": v(57.93, 78.03) * mm, "end": v(57.97, 78.15) * mm});
            skLineSegment(sketch, "E4029", {"start": v(57.97, 78.15) * mm, "end": v(58.01, 78.28) * mm});
            skLineSegment(sketch, "E4030", {"start": v(58.01, 78.28) * mm, "end": v(58.06, 78.4) * mm});
            skLineSegment(sketch, "E4031", {"start": v(58.06, 78.4) * mm, "end": v(58.1, 78.53) * mm});
            skLineSegment(sketch, "E4032", {"start": v(58.1, 78.53) * mm, "end": v(58.14, 78.66) * mm});
            skLineSegment(sketch, "E4033", {"start": v(58.14, 78.66) * mm, "end": v(58.18, 78.79) * mm});
            skLineSegment(sketch, "E4034", {"start": v(58.18, 78.79) * mm, "end": v(58.22, 78.92) * mm});
            skLineSegment(sketch, "E4035", {"start": v(58.22, 78.92) * mm, "end": v(58.26, 79.05) * mm});
            skLineSegment(sketch, "E4036", {"start": v(58.26, 79.05) * mm, "end": v(58.3, 79.19) * mm});
            skLineSegment(sketch, "E4037", {"start": v(58.3, 79.19) * mm, "end": v(58.35, 79.33) * mm});
            skLineSegment(sketch, "E4038", {"start": v(58.35, 79.33) * mm, "end": v(58.39, 79.47) * mm});
            skLineSegment(sketch, "E4039", {"start": v(58.39, 79.47) * mm, "end": v(58.43, 79.6) * mm});
            skLineSegment(sketch, "E4040", {"start": v(58.43, 79.6) * mm, "end": v(58.47, 79.75) * mm});
            skLineSegment(sketch, "E4041", {"start": v(58.47, 79.75) * mm, "end": v(58.51, 79.9) * mm});
            skLineSegment(sketch, "E4042", {"start": v(58.51, 79.9) * mm, "end": v(58.55, 80.04) * mm});
            skLineSegment(sketch, "E4043", {"start": v(58.55, 80.04) * mm, "end": v(58.6, 80.2) * mm});
            skLineSegment(sketch, "E4044", {"start": v(58.6, 80.2) * mm, "end": v(58.63, 80.34) * mm});
            skLineSegment(sketch, "E4045", {"start": v(58.63, 80.34) * mm, "end": v(58.68, 80.5) * mm});
            skLineSegment(sketch, "E4046", {"start": v(58.68, 80.5) * mm, "end": v(58.72, 80.65) * mm});
            skLineSegment(sketch, "E4047", {"start": v(58.72, 80.65) * mm, "end": v(58.76, 80.8) * mm});
            skLineSegment(sketch, "E4048", {"start": v(58.76, 80.8) * mm, "end": v(58.8, 80.97) * mm});
            skLineSegment(sketch, "E4049", {"start": v(58.8, 80.97) * mm, "end": v(58.83, 81.13) * mm});
            skLineSegment(sketch, "E4050", {"start": v(58.83, 81.13) * mm, "end": v(58.87, 81.29) * mm});
            skLineSegment(sketch, "E4051", {"start": v(58.87, 81.29) * mm, "end": v(58.91, 81.45) * mm});
            skLineSegment(sketch, "E4052", {"start": v(58.91, 81.45) * mm, "end": v(58.95, 81.62) * mm});
            skLineSegment(sketch, "E4053", {"start": v(58.95, 81.62) * mm, "end": v(58.99, 81.79) * mm});
            skLineSegment(sketch, "E4054", {"start": v(58.99, 81.79) * mm, "end": v(59.03, 81.96) * mm});
            skLineSegment(sketch, "E4055", {"start": v(59.03, 81.96) * mm, "end": v(59.06, 82.13) * mm});
            skLineSegment(sketch, "E4056", {"start": v(59.06, 82.13) * mm, "end": v(59.1, 82.3) * mm});
            skLineSegment(sketch, "E4057", {"start": v(59.1, 82.3) * mm, "end": v(59.14, 82.48) * mm});
            skLineSegment(sketch, "E4058", {"start": v(59.14, 82.48) * mm, "end": v(59.17, 82.65) * mm});
            skLineSegment(sketch, "E4059", {"start": v(59.17, 82.65) * mm, "end": v(59.2, 82.83) * mm});
            skLineSegment(sketch, "E4060", {"start": v(59.2, 82.83) * mm, "end": v(59.24, 83.01) * mm});
            skLineSegment(sketch, "E4061", {"start": v(59.24, 83.01) * mm, "end": v(59.28, 83.2) * mm});
            skLineSegment(sketch, "E4062", {"start": v(59.28, 83.2) * mm, "end": v(59.31, 83.38) * mm});
            skLineSegment(sketch, "E4063", {"start": v(59.31, 83.38) * mm, "end": v(59.35, 83.57) * mm});
            skLineSegment(sketch, "E4064", {"start": v(59.35, 83.57) * mm, "end": v(59.28, 83.62) * mm});
            skLineSegment(sketch, "E4065", {"start": v(59.28, 83.62) * mm, "end": v(58, 84.52) * mm});
            skLineSegment(sketch, "E4066", {"start": v(58, 84.52) * mm, "end": v(57.92, 84.56) * mm});
            skLineSegment(sketch, "E4067", {"start": v(57.92, 84.56) * mm, "end": v(57.76, 84.46) * mm});
            skLineSegment(sketch, "E4068", {"start": v(57.76, 84.46) * mm, "end": v(57.6, 84.37) * mm});
            skLineSegment(sketch, "E4069", {"start": v(57.6, 84.37) * mm, "end": v(57.44, 84.27) * mm});
            skLineSegment(sketch, "E4070", {"start": v(57.44, 84.27) * mm, "end": v(57.28, 84.18) * mm});
            skLineSegment(sketch, "E4071", {"start": v(57.28, 84.18) * mm, "end": v(57.13, 84.08) * mm});
            skLineSegment(sketch, "E4072", {"start": v(57.13, 84.08) * mm, "end": v(56.97, 83.99) * mm});
            skLineSegment(sketch, "E4073", {"start": v(56.97, 83.99) * mm, "end": v(56.82, 83.9) * mm});
            skLineSegment(sketch, "E4074", {"start": v(56.82, 83.9) * mm, "end": v(56.67, 83.8) * mm});
            skLineSegment(sketch, "E4075", {"start": v(56.67, 83.8) * mm, "end": v(56.52, 83.7) * mm});
            skLineSegment(sketch, "E4076", {"start": v(56.52, 83.7) * mm, "end": v(56.38, 83.6) * mm});
            skLineSegment(sketch, "E4077", {"start": v(56.38, 83.6) * mm, "end": v(56.23, 83.51) * mm});
            skLineSegment(sketch, "E4078", {"start": v(56.23, 83.51) * mm, "end": v(56.09, 83.42) * mm});
            skLineSegment(sketch, "E4079", {"start": v(56.09, 83.42) * mm, "end": v(55.95, 83.33) * mm});
            skLineSegment(sketch, "E4080", {"start": v(55.95, 83.33) * mm, "end": v(55.8, 83.24) * mm});
            skLineSegment(sketch, "E4081", {"start": v(55.8, 83.24) * mm, "end": v(55.67, 83.14) * mm});
            skLineSegment(sketch, "E4082", {"start": v(55.67, 83.14) * mm, "end": v(55.54, 83.05) * mm});
            skLineSegment(sketch, "E4083", {"start": v(55.54, 83.05) * mm, "end": v(55.4, 82.96) * mm});
            skLineSegment(sketch, "E4084", {"start": v(55.4, 82.96) * mm, "end": v(55.27, 82.87) * mm});
            skLineSegment(sketch, "E4085", {"start": v(55.27, 82.87) * mm, "end": v(55.14, 82.78) * mm});
            skLineSegment(sketch, "E4086", {"start": v(55.14, 82.78) * mm, "end": v(55.02, 82.69) * mm});
            skLineSegment(sketch, "E4087", {"start": v(55.02, 82.69) * mm, "end": v(54.89, 82.6) * mm});
            skLineSegment(sketch, "E4088", {"start": v(54.89, 82.6) * mm, "end": v(54.77, 82.5) * mm});
            skLineSegment(sketch, "E4089", {"start": v(54.77, 82.5) * mm, "end": v(54.64, 82.42) * mm});
            skLineSegment(sketch, "E4090", {"start": v(54.64, 82.42) * mm, "end": v(54.52, 82.33) * mm});
            skLineSegment(sketch, "E4091", {"start": v(54.52, 82.33) * mm, "end": v(54.4, 82.25) * mm});
            skLineSegment(sketch, "E4092", {"start": v(54.4, 82.25) * mm, "end": v(54.29, 82.16) * mm});
            skLineSegment(sketch, "E4093", {"start": v(54.29, 82.16) * mm, "end": v(54.17, 82.07) * mm});
            skLineSegment(sketch, "E4094", {"start": v(54.17, 82.07) * mm, "end": v(54.06, 81.99) * mm});
            skLineSegment(sketch, "E4095", {"start": v(54.06, 81.99) * mm, "end": v(53.95, 81.9) * mm});
            skLineSegment(sketch, "E4096", {"start": v(53.95, 81.9) * mm, "end": v(53.84, 81.82) * mm});
            skLineSegment(sketch, "E4097", {"start": v(53.84, 81.82) * mm, "end": v(53.73, 81.73) * mm});
            skLineSegment(sketch, "E4098", {"start": v(53.73, 81.73) * mm, "end": v(53.63, 81.65) * mm});
            skLineSegment(sketch, "E4099", {"start": v(53.63, 81.65) * mm, "end": v(53.52, 81.56) * mm});
            skLineSegment(sketch, "E4100", {"start": v(53.52, 81.56) * mm, "end": v(53.42, 81.48) * mm});
            skLineSegment(sketch, "E4101", {"start": v(53.42, 81.48) * mm, "end": v(53.32, 81.4) * mm});
            skLineSegment(sketch, "E4102", {"start": v(53.32, 81.4) * mm, "end": v(53.22, 81.32) * mm});
            skLineSegment(sketch, "E4103", {"start": v(53.22, 81.32) * mm, "end": v(52.4, 81.78) * mm});
            skLineSegment(sketch, "E4104", {"start": v(52.4, 81.78) * mm, "end": v(51.63, 82.34) * mm});
            skLineSegment(sketch, "E4105", {"start": v(51.63, 82.34) * mm, "end": v(51.66, 82.46) * mm});
            skLineSegment(sketch, "E4106", {"start": v(51.66, 82.46) * mm, "end": v(51.7, 82.59) * mm});
            skLineSegment(sketch, "E4107", {"start": v(51.7, 82.59) * mm, "end": v(51.73, 82.72) * mm});
            skLineSegment(sketch, "E4108", {"start": v(51.73, 82.72) * mm, "end": v(51.76, 82.84) * mm});
            skLineSegment(sketch, "E4109", {"start": v(51.76, 82.84) * mm, "end": v(51.79, 82.98) * mm});
            skLineSegment(sketch, "E4110", {"start": v(51.79, 82.98) * mm, "end": v(51.82, 83.1) * mm});
            skLineSegment(sketch, "E4111", {"start": v(51.82, 83.1) * mm, "end": v(51.85, 83.24) * mm});
            skLineSegment(sketch, "E4112", {"start": v(51.85, 83.24) * mm, "end": v(51.88, 83.38) * mm});
            skLineSegment(sketch, "E4113", {"start": v(51.88, 83.38) * mm, "end": v(51.91, 83.52) * mm});
            skLineSegment(sketch, "E4114", {"start": v(51.91, 83.52) * mm, "end": v(51.94, 83.66) * mm});
            skLineSegment(sketch, "E4115", {"start": v(51.94, 83.66) * mm, "end": v(51.97, 83.8) * mm});
            skLineSegment(sketch, "E4116", {"start": v(51.97, 83.8) * mm, "end": v(52, 83.95) * mm});
            skLineSegment(sketch, "E4117", {"start": v(52, 83.95) * mm, "end": v(52.03, 84.1) * mm});
            skLineSegment(sketch, "E4118", {"start": v(52.03, 84.1) * mm, "end": v(52.06, 84.24) * mm});
            skLineSegment(sketch, "E4119", {"start": v(52.06, 84.24) * mm, "end": v(52.1, 84.4) * mm});
            skLineSegment(sketch, "E4120", {"start": v(52.1, 84.4) * mm, "end": v(52.12, 84.54) * mm});
            skLineSegment(sketch, "E4121", {"start": v(52.12, 84.54) * mm, "end": v(52.15, 84.7) * mm});
            skLineSegment(sketch, "E4122", {"start": v(52.15, 84.7) * mm, "end": v(52.18, 84.85) * mm});
            skLineSegment(sketch, "E4123", {"start": v(52.18, 84.85) * mm, "end": v(52.2, 85) * mm});
            skLineSegment(sketch, "E4124", {"start": v(52.2, 85) * mm, "end": v(52.23, 85.17) * mm});
            skLineSegment(sketch, "E4125", {"start": v(52.23, 85.17) * mm, "end": v(52.26, 85.33) * mm});
            skLineSegment(sketch, "E4126", {"start": v(52.26, 85.33) * mm, "end": v(52.29, 85.5) * mm});
            skLineSegment(sketch, "E4127", {"start": v(52.29, 85.5) * mm, "end": v(52.31, 85.66) * mm});
            skLineSegment(sketch, "E4128", {"start": v(52.31, 85.66) * mm, "end": v(52.34, 85.82) * mm});
            skLineSegment(sketch, "E4129", {"start": v(52.34, 85.82) * mm, "end": v(52.36, 86) * mm});
            skLineSegment(sketch, "E4130", {"start": v(52.36, 86) * mm, "end": v(52.39, 86.16) * mm});
            skLineSegment(sketch, "E4131", {"start": v(52.39, 86.16) * mm, "end": v(52.41, 86.33) * mm});
            skLineSegment(sketch, "E4132", {"start": v(52.41, 86.33) * mm, "end": v(52.44, 86.5) * mm});
            skLineSegment(sketch, "E4133", {"start": v(52.44, 86.5) * mm, "end": v(52.46, 86.68) * mm});
            skLineSegment(sketch, "E4134", {"start": v(52.46, 86.68) * mm, "end": v(52.48, 86.86) * mm});
            skLineSegment(sketch, "E4135", {"start": v(52.48, 86.86) * mm, "end": v(52.5, 87.04) * mm});
            skLineSegment(sketch, "E4136", {"start": v(52.5, 87.04) * mm, "end": v(52.53, 87.22) * mm});
            skLineSegment(sketch, "E4137", {"start": v(52.53, 87.22) * mm, "end": v(52.55, 87.4) * mm});
            skLineSegment(sketch, "E4138", {"start": v(52.55, 87.4) * mm, "end": v(52.57, 87.6) * mm});
            skLineSegment(sketch, "E4139", {"start": v(52.57, 87.6) * mm, "end": v(52.59, 87.78) * mm});
            skLineSegment(sketch, "E4140", {"start": v(52.59, 87.78) * mm, "end": v(52.6, 87.97) * mm});
            skLineSegment(sketch, "E4141", {"start": v(52.6, 87.97) * mm, "end": v(52.54, 88.01) * mm});
            skLineSegment(sketch, "E4142", {"start": v(52.54, 88.01) * mm, "end": v(51.18, 88.8) * mm});
            skLineSegment(sketch, "E4143", {"start": v(51.18, 88.8) * mm, "end": v(51.11, 88.84) * mm});
            skLineSegment(sketch, "E4144", {"start": v(51.11, 88.84) * mm, "end": v(50.96, 88.74) * mm});
            skLineSegment(sketch, "E4145", {"start": v(50.96, 88.74) * mm, "end": v(50.8, 88.63) * mm});
            skLineSegment(sketch, "E4146", {"start": v(50.8, 88.63) * mm, "end": v(50.65, 88.52) * mm});
            skLineSegment(sketch, "E4147", {"start": v(50.65, 88.52) * mm, "end": v(50.5, 88.41) * mm});
            skLineSegment(sketch, "E4148", {"start": v(50.5, 88.41) * mm, "end": v(50.35, 88.3) * mm});
            skLineSegment(sketch, "E4149", {"start": v(50.35, 88.3) * mm, "end": v(50.2, 88.2) * mm});
            skLineSegment(sketch, "E4150", {"start": v(50.2, 88.2) * mm, "end": v(50.06, 88.1) * mm});
            skLineSegment(sketch, "E4151", {"start": v(50.06, 88.1) * mm, "end": v(49.92, 87.98) * mm});
            skLineSegment(sketch, "E4152", {"start": v(49.92, 87.98) * mm, "end": v(49.78, 87.88) * mm});
            skLineSegment(sketch, "E4153", {"start": v(49.78, 87.88) * mm, "end": v(49.64, 87.77) * mm});
            skLineSegment(sketch, "E4154", {"start": v(49.64, 87.77) * mm, "end": v(49.5, 87.67) * mm});
            skLineSegment(sketch, "E4155", {"start": v(49.5, 87.67) * mm, "end": v(49.37, 87.57) * mm});
            skLineSegment(sketch, "E4156", {"start": v(49.37, 87.57) * mm, "end": v(49.24, 87.46) * mm});
            skLineSegment(sketch, "E4157", {"start": v(49.24, 87.46) * mm, "end": v(49.1, 87.36) * mm});
            skLineSegment(sketch, "E4158", {"start": v(49.1, 87.36) * mm, "end": v(48.98, 87.26) * mm});
            skLineSegment(sketch, "E4159", {"start": v(48.98, 87.26) * mm, "end": v(48.85, 87.15) * mm});
            skLineSegment(sketch, "E4160", {"start": v(48.85, 87.15) * mm, "end": v(48.72, 87.05) * mm});
            skLineSegment(sketch, "E4161", {"start": v(48.72, 87.05) * mm, "end": v(48.6, 86.95) * mm});
            skLineSegment(sketch, "E4162", {"start": v(48.6, 86.95) * mm, "end": v(48.48, 86.85) * mm});
            skLineSegment(sketch, "E4163", {"start": v(48.48, 86.85) * mm, "end": v(48.36, 86.75) * mm});
            skLineSegment(sketch, "E4164", {"start": v(48.36, 86.75) * mm, "end": v(48.24, 86.65) * mm});
            skLineSegment(sketch, "E4165", {"start": v(48.24, 86.65) * mm, "end": v(48.12, 86.55) * mm});
            skLineSegment(sketch, "E4166", {"start": v(48.12, 86.55) * mm, "end": v(48, 86.45) * mm});
            skLineSegment(sketch, "E4167", {"start": v(48, 86.45) * mm, "end": v(47.9, 86.36) * mm});
            skLineSegment(sketch, "E4168", {"start": v(47.9, 86.36) * mm, "end": v(47.78, 86.26) * mm});
            skLineSegment(sketch, "E4169", {"start": v(47.78, 86.26) * mm, "end": v(47.67, 86.16) * mm});
            skLineSegment(sketch, "E4170", {"start": v(47.67, 86.16) * mm, "end": v(47.57, 86.07) * mm});
            skLineSegment(sketch, "E4171", {"start": v(47.57, 86.07) * mm, "end": v(47.46, 85.97) * mm});
            skLineSegment(sketch, "E4172", {"start": v(47.46, 85.97) * mm, "end": v(47.36, 85.88) * mm});
            skLineSegment(sketch, "E4173", {"start": v(47.36, 85.88) * mm, "end": v(47.25, 85.79) * mm});
            skLineSegment(sketch, "E4174", {"start": v(47.25, 85.79) * mm, "end": v(47.15, 85.7) * mm});
            skLineSegment(sketch, "E4175", {"start": v(47.15, 85.7) * mm, "end": v(47.05, 85.6) * mm});
            skLineSegment(sketch, "E4176", {"start": v(47.05, 85.6) * mm, "end": v(46.96, 85.51) * mm});
            skLineSegment(sketch, "E4177", {"start": v(46.96, 85.51) * mm, "end": v(46.86, 85.42) * mm});
            skLineSegment(sketch, "E4178", {"start": v(46.86, 85.42) * mm, "end": v(46.77, 85.33) * mm});
            skLineSegment(sketch, "E4179", {"start": v(46.77, 85.33) * mm, "end": v(46.67, 85.24) * mm});
            skLineSegment(sketch, "E4180", {"start": v(46.67, 85.24) * mm, "end": v(45.82, 85.64) * mm});
            skLineSegment(sketch, "E4181", {"start": v(45.82, 85.64) * mm, "end": v(45.01, 86.13) * mm});
            skLineSegment(sketch, "E4182", {"start": v(45.01, 86.13) * mm, "end": v(45.03, 86.26) * mm});
            skLineSegment(sketch, "E4183", {"start": v(45.03, 86.26) * mm, "end": v(45.05, 86.39) * mm});
            skLineSegment(sketch, "E4184", {"start": v(45.05, 86.39) * mm, "end": v(45.08, 86.52) * mm});
            skLineSegment(sketch, "E4185", {"start": v(45.08, 86.52) * mm, "end": v(45.1, 86.65) * mm});
            skLineSegment(sketch, "E4186", {"start": v(45.1, 86.65) * mm, "end": v(45.12, 86.78) * mm});
            skLineSegment(sketch, "E4187", {"start": v(45.12, 86.78) * mm, "end": v(45.14, 86.92) * mm});
            skLineSegment(sketch, "E4188", {"start": v(45.14, 86.92) * mm, "end": v(45.16, 87.06) * mm});
            skLineSegment(sketch, "E4189", {"start": v(45.16, 87.06) * mm, "end": v(45.18, 87.2) * mm});
            skLineSegment(sketch, "E4190", {"start": v(45.18, 87.2) * mm, "end": v(45.2, 87.34) * mm});
            skLineSegment(sketch, "E4191", {"start": v(45.2, 87.34) * mm, "end": v(45.22, 87.48) * mm});
            skLineSegment(sketch, "E4192", {"start": v(45.22, 87.48) * mm, "end": v(45.24, 87.62) * mm});
            skLineSegment(sketch, "E4193", {"start": v(45.24, 87.62) * mm, "end": v(45.26, 87.77) * mm});
            skLineSegment(sketch, "E4194", {"start": v(45.26, 87.77) * mm, "end": v(45.28, 87.92) * mm});
            skLineSegment(sketch, "E4195", {"start": v(45.28, 87.92) * mm, "end": v(45.3, 88.07) * mm});
            skLineSegment(sketch, "E4196", {"start": v(45.3, 88.07) * mm, "end": v(45.31, 88.22) * mm});
            skLineSegment(sketch, "E4197", {"start": v(45.31, 88.22) * mm, "end": v(45.33, 88.37) * mm});
            skLineSegment(sketch, "E4198", {"start": v(45.33, 88.37) * mm, "end": v(45.34, 88.53) * mm});
            skLineSegment(sketch, "E4199", {"start": v(45.34, 88.53) * mm, "end": v(45.36, 88.68) * mm});
            skLineSegment(sketch, "E4200", {"start": v(45.36, 88.68) * mm, "end": v(45.38, 88.84) * mm});
            skLineSegment(sketch, "E4201", {"start": v(45.38, 88.84) * mm, "end": v(45.4, 89) * mm});
            skLineSegment(sketch, "E4202", {"start": v(45.4, 89) * mm, "end": v(45.4, 89.17) * mm});
            skLineSegment(sketch, "E4203", {"start": v(45.4, 89.17) * mm, "end": v(45.42, 89.33) * mm});
            skLineSegment(sketch, "E4204", {"start": v(45.42, 89.33) * mm, "end": v(45.43, 89.5) * mm});
            skLineSegment(sketch, "E4205", {"start": v(45.43, 89.5) * mm, "end": v(45.44, 89.67) * mm});
            skLineSegment(sketch, "E4206", {"start": v(45.44, 89.67) * mm, "end": v(45.46, 89.84) * mm});
            skLineSegment(sketch, "E4207", {"start": v(45.46, 89.84) * mm, "end": v(45.47, 90) * mm});
            skLineSegment(sketch, "E4208", {"start": v(45.47, 90) * mm, "end": v(45.48, 90.18) * mm});
            skLineSegment(sketch, "E4209", {"start": v(45.48, 90.18) * mm, "end": v(45.49, 90.36) * mm});
            skLineSegment(sketch, "E4210", {"start": v(45.49, 90.36) * mm, "end": v(45.5, 90.53) * mm});
            skLineSegment(sketch, "E4211", {"start": v(45.5, 90.53) * mm, "end": v(45.5, 90.71) * mm});
            skLineSegment(sketch, "E4212", {"start": v(45.5, 90.71) * mm, "end": v(45.51, 90.9) * mm});
            skLineSegment(sketch, "E4213", {"start": v(45.51, 90.9) * mm, "end": v(45.52, 91.08) * mm});
            skLineSegment(sketch, "E4214", {"start": v(45.52, 91.08) * mm, "end": v(45.53, 91.26) * mm});
            skLineSegment(sketch, "E4215", {"start": v(45.53, 91.26) * mm, "end": v(45.53, 91.45) * mm});
            skLineSegment(sketch, "E4216", {"start": v(45.53, 91.45) * mm, "end": v(45.54, 91.63) * mm});
            skLineSegment(sketch, "E4217", {"start": v(45.54, 91.63) * mm, "end": v(45.54, 91.82) * mm});
            skLineSegment(sketch, "E4218", {"start": v(45.54, 91.82) * mm, "end": v(45.47, 91.86) * mm});
            skLineSegment(sketch, "E4219", {"start": v(45.47, 91.86) * mm, "end": v(44.06, 92.55) * mm});
            skLineSegment(sketch, "E4220", {"start": v(44.06, 92.55) * mm, "end": v(43.98, 92.58) * mm});
            skLineSegment(sketch, "E4221", {"start": v(43.98, 92.58) * mm, "end": v(43.84, 92.46) * mm});
            skLineSegment(sketch, "E4222", {"start": v(43.84, 92.46) * mm, "end": v(43.7, 92.34) * mm});
            skLineSegment(sketch, "E4223", {"start": v(43.7, 92.34) * mm, "end": v(43.55, 92.22) * mm});
            skLineSegment(sketch, "E4224", {"start": v(43.55, 92.22) * mm, "end": v(43.4, 92.1) * mm});
            skLineSegment(sketch, "E4225", {"start": v(43.4, 92.1) * mm, "end": v(43.27, 91.98) * mm});
            skLineSegment(sketch, "E4226", {"start": v(43.27, 91.98) * mm, "end": v(43.13, 91.86) * mm});
            skLineSegment(sketch, "E4227", {"start": v(43.13, 91.86) * mm, "end": v(43, 91.75) * mm});
            skLineSegment(sketch, "E4228", {"start": v(43, 91.75) * mm, "end": v(42.86, 91.63) * mm});
            skLineSegment(sketch, "E4229", {"start": v(42.86, 91.63) * mm, "end": v(42.73, 91.51) * mm});
            skLineSegment(sketch, "E4230", {"start": v(42.73, 91.51) * mm, "end": v(42.6, 91.4) * mm});
            skLineSegment(sketch, "E4231", {"start": v(42.6, 91.4) * mm, "end": v(42.47, 91.28) * mm});
            skLineSegment(sketch, "E4232", {"start": v(42.47, 91.28) * mm, "end": v(42.35, 91.17) * mm});
            skLineSegment(sketch, "E4233", {"start": v(42.35, 91.17) * mm, "end": v(42.22, 91.05) * mm});
            skLineSegment(sketch, "E4234", {"start": v(42.22, 91.05) * mm, "end": v(42.1, 90.94) * mm});
            skLineSegment(sketch, "E4235", {"start": v(42.1, 90.94) * mm, "end": v(41.98, 90.83) * mm});
            skLineSegment(sketch, "E4236", {"start": v(41.98, 90.83) * mm, "end": v(41.86, 90.72) * mm});
            skLineSegment(sketch, "E4237", {"start": v(41.86, 90.72) * mm, "end": v(41.74, 90.6) * mm});
            skLineSegment(sketch, "E4238", {"start": v(41.74, 90.6) * mm, "end": v(41.63, 90.5) * mm});
            skLineSegment(sketch, "E4239", {"start": v(41.63, 90.5) * mm, "end": v(41.51, 90.39) * mm});
            skLineSegment(sketch, "E4240", {"start": v(41.51, 90.39) * mm, "end": v(41.4, 90.28) * mm});
            skLineSegment(sketch, "E4241", {"start": v(41.4, 90.28) * mm, "end": v(41.3, 90.17) * mm});
            skLineSegment(sketch, "E4242", {"start": v(41.3, 90.17) * mm, "end": v(41.18, 90.06) * mm});
            skLineSegment(sketch, "E4243", {"start": v(41.18, 90.06) * mm, "end": v(41.08, 89.95) * mm});
            skLineSegment(sketch, "E4244", {"start": v(41.08, 89.95) * mm, "end": v(40.97, 89.85) * mm});
            skLineSegment(sketch, "E4245", {"start": v(40.97, 89.85) * mm, "end": v(40.87, 89.74) * mm});
            skLineSegment(sketch, "E4246", {"start": v(40.87, 89.74) * mm, "end": v(40.77, 89.64) * mm});
            skLineSegment(sketch, "E4247", {"start": v(40.77, 89.64) * mm, "end": v(40.67, 89.54) * mm});
            skLineSegment(sketch, "E4248", {"start": v(40.67, 89.54) * mm, "end": v(40.57, 89.43) * mm});
            skLineSegment(sketch, "E4249", {"start": v(40.57, 89.43) * mm, "end": v(40.47, 89.33) * mm});
            skLineSegment(sketch, "E4250", {"start": v(40.47, 89.33) * mm, "end": v(40.38, 89.23) * mm});
            skLineSegment(sketch, "E4251", {"start": v(40.38, 89.23) * mm, "end": v(40.28, 89.13) * mm});
            skLineSegment(sketch, "E4252", {"start": v(40.28, 89.13) * mm, "end": v(40.2, 89.03) * mm});
            skLineSegment(sketch, "E4253", {"start": v(40.2, 89.03) * mm, "end": v(40.1, 88.93) * mm});
            skLineSegment(sketch, "E4254", {"start": v(40.1, 88.93) * mm, "end": v(40.01, 88.84) * mm});
            skLineSegment(sketch, "E4255", {"start": v(40.01, 88.84) * mm, "end": v(39.93, 88.74) * mm});
            skLineSegment(sketch, "E4256", {"start": v(39.93, 88.74) * mm, "end": v(39.84, 88.64) * mm});
            skLineSegment(sketch, "E4257", {"start": v(39.84, 88.64) * mm, "end": v(38.96, 88.97) * mm});
            skLineSegment(sketch, "E4258", {"start": v(38.96, 88.97) * mm, "end": v(38.11, 89.4) * mm});
            skLineSegment(sketch, "E4259", {"start": v(38.11, 89.4) * mm, "end": v(38.13, 89.53) * mm});
            skLineSegment(sketch, "E4260", {"start": v(38.13, 89.53) * mm, "end": v(38.14, 89.66) * mm});
            skLineSegment(sketch, "E4261", {"start": v(38.14, 89.66) * mm, "end": v(38.15, 89.79) * mm});
            skLineSegment(sketch, "E4262", {"start": v(38.15, 89.79) * mm, "end": v(38.16, 89.92) * mm});
            skLineSegment(sketch, "E4263", {"start": v(38.16, 89.92) * mm, "end": v(38.17, 90.06) * mm});
            skLineSegment(sketch, "E4264", {"start": v(38.17, 90.06) * mm, "end": v(38.18, 90.2) * mm});
            skLineSegment(sketch, "E4265", {"start": v(38.18, 90.2) * mm, "end": v(38.2, 90.33) * mm});
            skLineSegment(sketch, "E4266", {"start": v(38.2, 90.33) * mm, "end": v(38.2, 90.47) * mm});
            skLineSegment(sketch, "E4267", {"start": v(38.2, 90.47) * mm, "end": v(38.2, 90.61) * mm});
            skLineSegment(sketch, "E4268", {"start": v(38.2, 90.61) * mm, "end": v(38.22, 90.76) * mm});
            skLineSegment(sketch, "E4269", {"start": v(38.22, 90.76) * mm, "end": v(38.22, 90.9) * mm});
            skLineSegment(sketch, "E4270", {"start": v(38.22, 90.9) * mm, "end": v(38.23, 91.05) * mm});
            skLineSegment(sketch, "E4271", {"start": v(38.23, 91.05) * mm, "end": v(38.24, 91.2) * mm});
            skLineSegment(sketch, "E4272", {"start": v(38.24, 91.2) * mm, "end": v(38.24, 91.35) * mm});
            skLineSegment(sketch, "E4273", {"start": v(38.24, 91.35) * mm, "end": v(38.25, 91.5) * mm});
            skLineSegment(sketch, "E4274", {"start": v(38.25, 91.5) * mm, "end": v(38.25, 91.66) * mm});
            skLineSegment(sketch, "E4275", {"start": v(38.25, 91.66) * mm, "end": v(38.26, 91.81) * mm});
            skLineSegment(sketch, "E4276", {"start": v(38.26, 91.81) * mm, "end": v(38.26, 91.97) * mm});
            skLineSegment(sketch, "E4277", {"start": v(38.26, 91.97) * mm, "end": v(38.27, 92.13) * mm});
            skLineSegment(sketch, "E4278", {"start": v(38.27, 92.13) * mm, "end": v(38.27, 92.3) * mm});
            skLineSegment(sketch, "E4279", {"start": v(38.27, 92.3) * mm, "end": v(38.27, 92.45) * mm});
            skLineSegment(sketch, "E4280", {"start": v(38.27, 92.45) * mm, "end": v(38.27, 92.62) * mm});
            skLineSegment(sketch, "E4281", {"start": v(38.27, 92.62) * mm, "end": v(38.27, 92.79) * mm});
            skLineSegment(sketch, "E4282", {"start": v(38.27, 92.79) * mm, "end": v(38.27, 92.95) * mm});
            skLineSegment(sketch, "E4283", {"start": v(38.27, 92.95) * mm, "end": v(38.27, 93.12) * mm});
            skLineSegment(sketch, "E4284", {"start": v(38.27, 93.12) * mm, "end": v(38.27, 93.3) * mm});
            skLineSegment(sketch, "E4285", {"start": v(38.27, 93.3) * mm, "end": v(38.26, 93.47) * mm});
            skLineSegment(sketch, "E4286", {"start": v(38.26, 93.47) * mm, "end": v(38.26, 93.65) * mm});
            skLineSegment(sketch, "E4287", {"start": v(38.26, 93.65) * mm, "end": v(38.25, 93.82) * mm});
            skLineSegment(sketch, "E4288", {"start": v(38.25, 93.82) * mm, "end": v(38.25, 94) * mm});
            skLineSegment(sketch, "E4289", {"start": v(38.25, 94) * mm, "end": v(38.24, 94.18) * mm});
            skLineSegment(sketch, "E4290", {"start": v(38.24, 94.18) * mm, "end": v(38.24, 94.37) * mm});
            skLineSegment(sketch, "E4291", {"start": v(38.24, 94.37) * mm, "end": v(38.23, 94.55) * mm});
            skLineSegment(sketch, "E4292", {"start": v(38.23, 94.55) * mm, "end": v(38.22, 94.74) * mm});
            skLineSegment(sketch, "E4293", {"start": v(38.22, 94.74) * mm, "end": v(38.2, 94.92) * mm});
            skLineSegment(sketch, "E4294", {"start": v(38.2, 94.92) * mm, "end": v(38.2, 95.11) * mm});
            skLineSegment(sketch, "E4295", {"start": v(38.2, 95.11) * mm, "end": v(38.12, 95.15) * mm});
            skLineSegment(sketch, "E4296", {"start": v(38.12, 95.15) * mm, "end": v(36.66, 95.72) * mm});
            skLineSegment(sketch, "E4297", {"start": v(36.66, 95.72) * mm, "end": v(36.58, 95.75) * mm});
            skLineSegment(sketch, "E4298", {"start": v(36.58, 95.75) * mm, "end": v(36.45, 95.61) * mm});
            skLineSegment(sketch, "E4299", {"start": v(36.45, 95.61) * mm, "end": v(36.31, 95.48) * mm});
            skLineSegment(sketch, "E4300", {"start": v(36.31, 95.48) * mm, "end": v(36.18, 95.35) * mm});
            skLineSegment(sketch, "E4301", {"start": v(36.18, 95.35) * mm, "end": v(36.05, 95.22) * mm});
            skLineSegment(sketch, "E4302", {"start": v(36.05, 95.22) * mm, "end": v(35.92, 95.1) * mm});
            skLineSegment(sketch, "E4303", {"start": v(35.92, 95.1) * mm, "end": v(35.8, 94.97) * mm});
            skLineSegment(sketch, "E4304", {"start": v(35.8, 94.97) * mm, "end": v(35.67, 94.84) * mm});
            skLineSegment(sketch, "E4305", {"start": v(35.67, 94.84) * mm, "end": v(35.54, 94.71) * mm});
            skLineSegment(sketch, "E4306", {"start": v(35.54, 94.71) * mm, "end": v(35.42, 94.58) * mm});
            skLineSegment(sketch, "E4307", {"start": v(35.42, 94.58) * mm, "end": v(35.3, 94.46) * mm});
            skLineSegment(sketch, "E4308", {"start": v(35.3, 94.46) * mm, "end": v(35.18, 94.33) * mm});
            skLineSegment(sketch, "E4309", {"start": v(35.18, 94.33) * mm, "end": v(35.06, 94.21) * mm});
            skLineSegment(sketch, "E4310", {"start": v(35.06, 94.21) * mm, "end": v(34.95, 94.09) * mm});
            skLineSegment(sketch, "E4311", {"start": v(34.95, 94.09) * mm, "end": v(34.84, 93.96) * mm});
            skLineSegment(sketch, "E4312", {"start": v(34.84, 93.96) * mm, "end": v(34.72, 93.84) * mm});
            skLineSegment(sketch, "E4313", {"start": v(34.72, 93.84) * mm, "end": v(34.61, 93.72) * mm});
            skLineSegment(sketch, "E4314", {"start": v(34.61, 93.72) * mm, "end": v(34.5, 93.6) * mm});
            skLineSegment(sketch, "E4315", {"start": v(34.5, 93.6) * mm, "end": v(34.4, 93.48) * mm});
            skLineSegment(sketch, "E4316", {"start": v(34.4, 93.48) * mm, "end": v(34.3, 93.36) * mm});
            skLineSegment(sketch, "E4317", {"start": v(34.3, 93.36) * mm, "end": v(34.2, 93.25) * mm});
            skLineSegment(sketch, "E4318", {"start": v(34.2, 93.25) * mm, "end": v(34.1, 93.13) * mm});
            skLineSegment(sketch, "E4319", {"start": v(34.1, 93.13) * mm, "end": v(34, 93.02) * mm});
            skLineSegment(sketch, "E4320", {"start": v(34, 93.02) * mm, "end": v(33.9, 92.9) * mm});
            skLineSegment(sketch, "E4321", {"start": v(33.9, 92.9) * mm, "end": v(33.8, 92.79) * mm});
            skLineSegment(sketch, "E4322", {"start": v(33.8, 92.79) * mm, "end": v(33.7, 92.67) * mm});
            skLineSegment(sketch, "E4323", {"start": v(33.7, 92.67) * mm, "end": v(33.6, 92.56) * mm});
            skLineSegment(sketch, "E4324", {"start": v(33.6, 92.56) * mm, "end": v(33.52, 92.45) * mm});
            skLineSegment(sketch, "E4325", {"start": v(33.52, 92.45) * mm, "end": v(33.43, 92.34) * mm});
            skLineSegment(sketch, "E4326", {"start": v(33.43, 92.34) * mm, "end": v(33.34, 92.23) * mm});
            skLineSegment(sketch, "E4327", {"start": v(33.34, 92.23) * mm, "end": v(33.25, 92.12) * mm});
            skLineSegment(sketch, "E4328", {"start": v(33.25, 92.12) * mm, "end": v(33.17, 92.02) * mm});
            skLineSegment(sketch, "E4329", {"start": v(33.17, 92.02) * mm, "end": v(33.08, 91.91) * mm});
            skLineSegment(sketch, "E4330", {"start": v(33.08, 91.91) * mm, "end": v(33, 91.8) * mm});
            skLineSegment(sketch, "E4331", {"start": v(33, 91.8) * mm, "end": v(32.92, 91.7) * mm});
            skLineSegment(sketch, "E4332", {"start": v(32.92, 91.7) * mm, "end": v(32.84, 91.6) * mm});
            skLineSegment(sketch, "E4333", {"start": v(32.84, 91.6) * mm, "end": v(32.76, 91.5) * mm});
            skLineSegment(sketch, "E4334", {"start": v(32.76, 91.5) * mm, "end": v(31.85, 91.75) * mm});
            skLineSegment(sketch, "E4335", {"start": v(31.85, 91.75) * mm, "end": v(30.98, 92.12) * mm});
            skLineSegment(sketch, "E4336", {"start": v(30.98, 92.12) * mm, "end": v(30.98, 92.24) * mm});
            skLineSegment(sketch, "E4337", {"start": v(30.98, 92.24) * mm, "end": v(30.99, 92.37) * mm});
            skLineSegment(sketch, "E4338", {"start": v(30.99, 92.37) * mm, "end": v(30.99, 92.5) * mm});
            skLineSegment(sketch, "E4339", {"start": v(30.99, 92.5) * mm, "end": v(30.99, 92.64) * mm});
            skLineSegment(sketch, "E4340", {"start": v(30.99, 92.64) * mm, "end": v(30.99, 92.77) * mm});
            skLineSegment(sketch, "E4341", {"start": v(30.99, 92.77) * mm, "end": v(30.99, 92.9) * mm});
            skLineSegment(sketch, "E4342", {"start": v(30.99, 92.9) * mm, "end": v(30.99, 93.05) * mm});
            skLineSegment(sketch, "E4343", {"start": v(30.99, 93.05) * mm, "end": v(30.98, 93.19) * mm});
            skLineSegment(sketch, "E4344", {"start": v(30.98, 93.19) * mm, "end": v(30.98, 93.33) * mm});
            skLineSegment(sketch, "E4345", {"start": v(30.98, 93.33) * mm, "end": v(30.98, 93.47) * mm});
            skLineSegment(sketch, "E4346", {"start": v(30.98, 93.47) * mm, "end": v(30.98, 93.62) * mm});
            skLineSegment(sketch, "E4347", {"start": v(30.98, 93.62) * mm, "end": v(30.97, 93.77) * mm});
            skLineSegment(sketch, "E4348", {"start": v(30.97, 93.77) * mm, "end": v(30.97, 93.92) * mm});
            skLineSegment(sketch, "E4349", {"start": v(30.97, 93.92) * mm, "end": v(30.96, 94.07) * mm});
            skLineSegment(sketch, "E4350", {"start": v(30.96, 94.07) * mm, "end": v(30.95, 94.22) * mm});
            skLineSegment(sketch, "E4351", {"start": v(30.95, 94.22) * mm, "end": v(30.95, 94.37) * mm});
            skLineSegment(sketch, "E4352", {"start": v(30.95, 94.37) * mm, "end": v(30.94, 94.53) * mm});
            skLineSegment(sketch, "E4353", {"start": v(30.94, 94.53) * mm, "end": v(30.93, 94.69) * mm});
            skLineSegment(sketch, "E4354", {"start": v(30.93, 94.69) * mm, "end": v(30.92, 94.85) * mm});
            skLineSegment(sketch, "E4355", {"start": v(30.92, 94.85) * mm, "end": v(30.9, 95) * mm});
            skLineSegment(sketch, "E4356", {"start": v(30.9, 95) * mm, "end": v(30.9, 95.17) * mm});
            skLineSegment(sketch, "E4357", {"start": v(30.9, 95.17) * mm, "end": v(30.88, 95.34) * mm});
            skLineSegment(sketch, "E4358", {"start": v(30.88, 95.34) * mm, "end": v(30.87, 95.5) * mm});
            skLineSegment(sketch, "E4359", {"start": v(30.87, 95.5) * mm, "end": v(30.86, 95.67) * mm});
            skLineSegment(sketch, "E4360", {"start": v(30.86, 95.67) * mm, "end": v(30.84, 95.84) * mm});
            skLineSegment(sketch, "E4361", {"start": v(30.84, 95.84) * mm, "end": v(30.83, 96.01) * mm});
            skLineSegment(sketch, "E4362", {"start": v(30.83, 96.01) * mm, "end": v(30.81, 96.18) * mm});
            skLineSegment(sketch, "E4363", {"start": v(30.81, 96.18) * mm, "end": v(30.8, 96.36) * mm});
            skLineSegment(sketch, "E4364", {"start": v(30.8, 96.36) * mm, "end": v(30.78, 96.54) * mm});
            skLineSegment(sketch, "E4365", {"start": v(30.78, 96.54) * mm, "end": v(30.76, 96.71) * mm});
            skLineSegment(sketch, "E4366", {"start": v(30.76, 96.71) * mm, "end": v(30.74, 96.9) * mm});
            skLineSegment(sketch, "E4367", {"start": v(30.74, 96.9) * mm, "end": v(30.71, 97.08) * mm});
            skLineSegment(sketch, "E4368", {"start": v(30.71, 97.08) * mm, "end": v(30.7, 97.26) * mm});
            skLineSegment(sketch, "E4369", {"start": v(30.7, 97.26) * mm, "end": v(30.67, 97.44) * mm});
            skLineSegment(sketch, "E4370", {"start": v(30.67, 97.44) * mm, "end": v(30.64, 97.63) * mm});
            skLineSegment(sketch, "E4371", {"start": v(30.64, 97.63) * mm, "end": v(30.62, 97.82) * mm});
            skLineSegment(sketch, "E4372", {"start": v(30.62, 97.82) * mm, "end": v(30.54, 97.84) * mm});
            skLineSegment(sketch, "E4373", {"start": v(30.54, 97.84) * mm, "end": v(29.04, 98.3) * mm});
            skLineSegment(sketch, "E4374", {"start": v(29.04, 98.3) * mm, "end": v(28.96, 98.32) * mm});
            skLineSegment(sketch, "E4375", {"start": v(28.96, 98.32) * mm, "end": v(28.83, 98.18) * mm});
            skLineSegment(sketch, "E4376", {"start": v(28.83, 98.18) * mm, "end": v(28.7, 98.04) * mm});
            skLineSegment(sketch, "E4377", {"start": v(28.7, 98.04) * mm, "end": v(28.59, 97.9) * mm});
            skLineSegment(sketch, "E4378", {"start": v(28.59, 97.9) * mm, "end": v(28.47, 97.76) * mm});
            skLineSegment(sketch, "E4379", {"start": v(28.47, 97.76) * mm, "end": v(28.35, 97.62) * mm});
            skLineSegment(sketch, "E4380", {"start": v(28.35, 97.62) * mm, "end": v(28.23, 97.48) * mm});
            skLineSegment(sketch, "E4381", {"start": v(28.23, 97.48) * mm, "end": v(28.11, 97.34) * mm});
            skLineSegment(sketch, "E4382", {"start": v(28.11, 97.34) * mm, "end": v(28, 97.2) * mm});
            skLineSegment(sketch, "E4383", {"start": v(28, 97.2) * mm, "end": v(27.89, 97.07) * mm});
            skLineSegment(sketch, "E4384", {"start": v(27.89, 97.07) * mm, "end": v(27.78, 96.94) * mm});
            skLineSegment(sketch, "E4385", {"start": v(27.78, 96.94) * mm, "end": v(27.67, 96.8) * mm});
            skLineSegment(sketch, "E4386", {"start": v(27.67, 96.8) * mm, "end": v(27.56, 96.67) * mm});
            skLineSegment(sketch, "E4387", {"start": v(27.56, 96.67) * mm, "end": v(27.46, 96.54) * mm});
            skLineSegment(sketch, "E4388", {"start": v(27.46, 96.54) * mm, "end": v(27.36, 96.4) * mm});
            skLineSegment(sketch, "E4389", {"start": v(27.36, 96.4) * mm, "end": v(27.25, 96.28) * mm});
            skLineSegment(sketch, "E4390", {"start": v(27.25, 96.28) * mm, "end": v(27.15, 96.15) * mm});
            skLineSegment(sketch, "E4391", {"start": v(27.15, 96.15) * mm, "end": v(27.06, 96.02) * mm});
            skLineSegment(sketch, "E4392", {"start": v(27.06, 96.02) * mm, "end": v(26.96, 95.9) * mm});
            skLineSegment(sketch, "E4393", {"start": v(26.96, 95.9) * mm, "end": v(26.86, 95.77) * mm});
            skLineSegment(sketch, "E4394", {"start": v(26.86, 95.77) * mm, "end": v(26.77, 95.64) * mm});
            skLineSegment(sketch, "E4395", {"start": v(26.77, 95.64) * mm, "end": v(26.68, 95.52) * mm});
            skLineSegment(sketch, "E4396", {"start": v(26.68, 95.52) * mm, "end": v(26.59, 95.4) * mm});
            skLineSegment(sketch, "E4397", {"start": v(26.59, 95.4) * mm, "end": v(26.5, 95.27) * mm});
            skLineSegment(sketch, "E4398", {"start": v(26.5, 95.27) * mm, "end": v(26.41, 95.15) * mm});
            skLineSegment(sketch, "E4399", {"start": v(26.41, 95.15) * mm, "end": v(26.33, 95.03) * mm});
            skLineSegment(sketch, "E4400", {"start": v(26.33, 95.03) * mm, "end": v(26.24, 94.91) * mm});
            skLineSegment(sketch, "E4401", {"start": v(26.24, 94.91) * mm, "end": v(26.16, 94.8) * mm});
            skLineSegment(sketch, "E4402", {"start": v(26.16, 94.8) * mm, "end": v(26.08, 94.68) * mm});
            skLineSegment(sketch, "E4403", {"start": v(26.08, 94.68) * mm, "end": v(26, 94.56) * mm});
            skLineSegment(sketch, "E4404", {"start": v(26, 94.56) * mm, "end": v(25.92, 94.45) * mm});
            skLineSegment(sketch, "E4405", {"start": v(25.92, 94.45) * mm, "end": v(25.85, 94.34) * mm});
            skLineSegment(sketch, "E4406", {"start": v(25.85, 94.34) * mm, "end": v(25.77, 94.22) * mm});
            skLineSegment(sketch, "E4407", {"start": v(25.77, 94.22) * mm, "end": v(25.7, 94.11) * mm});
            skLineSegment(sketch, "E4408", {"start": v(25.7, 94.11) * mm, "end": v(25.62, 94) * mm});
            skLineSegment(sketch, "E4409", {"start": v(25.62, 94) * mm, "end": v(25.55, 93.9) * mm});
            skLineSegment(sketch, "E4410", {"start": v(25.55, 93.9) * mm, "end": v(25.48, 93.79) * mm});
            skLineSegment(sketch, "E4411", {"start": v(25.48, 93.79) * mm, "end": v(24.56, 93.97) * mm});
            skLineSegment(sketch, "E4412", {"start": v(24.56, 93.97) * mm, "end": v(23.66, 94.26) * mm});
            skLineSegment(sketch, "E4413", {"start": v(23.66, 94.26) * mm, "end": v(23.65, 94.4) * mm});
            skLineSegment(sketch, "E4414", {"start": v(23.65, 94.4) * mm, "end": v(23.64, 94.52) * mm});
            skLineSegment(sketch, "E4415", {"start": v(23.64, 94.52) * mm, "end": v(23.63, 94.65) * mm});
            skLineSegment(sketch, "E4416", {"start": v(23.63, 94.65) * mm, "end": v(23.62, 94.78) * mm});
            skLineSegment(sketch, "E4417", {"start": v(23.62, 94.78) * mm, "end": v(23.61, 94.92) * mm});
            skLineSegment(sketch, "E4418", {"start": v(23.61, 94.92) * mm, "end": v(23.6, 95.05) * mm});
            skLineSegment(sketch, "E4419", {"start": v(23.6, 95.05) * mm, "end": v(23.6, 95.2) * mm});
            skLineSegment(sketch, "E4420", {"start": v(23.6, 95.2) * mm, "end": v(23.58, 95.33) * mm});
            skLineSegment(sketch, "E4421", {"start": v(23.58, 95.33) * mm, "end": v(23.56, 95.47) * mm});
            skLineSegment(sketch, "E4422", {"start": v(23.56, 95.47) * mm, "end": v(23.55, 95.62) * mm});
            skLineSegment(sketch, "E4423", {"start": v(23.55, 95.62) * mm, "end": v(23.53, 95.76) * mm});
            skLineSegment(sketch, "E4424", {"start": v(23.53, 95.76) * mm, "end": v(23.52, 95.9) * mm});
            skLineSegment(sketch, "E4425", {"start": v(23.52, 95.9) * mm, "end": v(23.5, 96.06) * mm});
            skLineSegment(sketch, "E4426", {"start": v(23.5, 96.06) * mm, "end": v(23.48, 96.2) * mm});
            skLineSegment(sketch, "E4427", {"start": v(23.48, 96.2) * mm, "end": v(23.47, 96.36) * mm});
            skLineSegment(sketch, "E4428", {"start": v(23.47, 96.36) * mm, "end": v(23.45, 96.51) * mm});
            skLineSegment(sketch, "E4429", {"start": v(23.45, 96.51) * mm, "end": v(23.43, 96.67) * mm});
            skLineSegment(sketch, "E4430", {"start": v(23.43, 96.67) * mm, "end": v(23.4, 96.82) * mm});
            skLineSegment(sketch, "E4431", {"start": v(23.4, 96.82) * mm, "end": v(23.38, 96.98) * mm});
            skLineSegment(sketch, "E4432", {"start": v(23.38, 96.98) * mm, "end": v(23.36, 97.14) * mm});
            skLineSegment(sketch, "E4433", {"start": v(23.36, 97.14) * mm, "end": v(23.33, 97.3) * mm});
            skLineSegment(sketch, "E4434", {"start": v(23.33, 97.3) * mm, "end": v(23.3, 97.47) * mm});
            skLineSegment(sketch, "E4435", {"start": v(23.3, 97.47) * mm, "end": v(23.28, 97.63) * mm});
            skLineSegment(sketch, "E4436", {"start": v(23.28, 97.63) * mm, "end": v(23.26, 97.8) * mm});
            skLineSegment(sketch, "E4437", {"start": v(23.26, 97.8) * mm, "end": v(23.23, 97.96) * mm});
            skLineSegment(sketch, "E4438", {"start": v(23.23, 97.96) * mm, "end": v(23.2, 98.13) * mm});
            skLineSegment(sketch, "E4439", {"start": v(23.2, 98.13) * mm, "end": v(23.17, 98.3) * mm});
            skLineSegment(sketch, "E4440", {"start": v(23.17, 98.3) * mm, "end": v(23.14, 98.48) * mm});
            skLineSegment(sketch, "E4441", {"start": v(23.14, 98.48) * mm, "end": v(23.1, 98.65) * mm});
            skLineSegment(sketch, "E4442", {"start": v(23.1, 98.65) * mm, "end": v(23.07, 98.83) * mm});
            skLineSegment(sketch, "E4443", {"start": v(23.07, 98.83) * mm, "end": v(23.04, 99) * mm});
            skLineSegment(sketch, "E4444", {"start": v(23.04, 99) * mm, "end": v(23, 99.19) * mm});
            skLineSegment(sketch, "E4445", {"start": v(23, 99.19) * mm, "end": v(22.97, 99.37) * mm});
            skLineSegment(sketch, "E4446", {"start": v(22.97, 99.37) * mm, "end": v(22.93, 99.55) * mm});
            skLineSegment(sketch, "E4447", {"start": v(22.93, 99.55) * mm, "end": v(22.89, 99.73) * mm});
            skLineSegment(sketch, "E4448", {"start": v(22.89, 99.73) * mm, "end": v(22.85, 99.92) * mm});
            skLineSegment(sketch, "E4449", {"start": v(22.85, 99.92) * mm, "end": v(22.77, 99.94) * mm});
            skLineSegment(sketch, "E4450", {"start": v(22.77, 99.94) * mm, "end": v(21.24, 100.28) * mm});
            skLineSegment(sketch, "E4451", {"start": v(21.24, 100.28) * mm, "end": v(21.15, 100.3) * mm});
            skLineSegment(sketch, "E4452", {"start": v(21.15, 100.3) * mm, "end": v(21.04, 100.14) * mm});
            skLineSegment(sketch, "E4453", {"start": v(21.04, 100.14) * mm, "end": v(20.93, 99.99) * mm});
            skLineSegment(sketch, "E4454", {"start": v(20.93, 99.99) * mm, "end": v(20.82, 99.84) * mm});
            skLineSegment(sketch, "E4455", {"start": v(20.82, 99.84) * mm, "end": v(20.7, 99.7) * mm});
            skLineSegment(sketch, "E4456", {"start": v(20.7, 99.7) * mm, "end": v(20.6, 99.54) * mm});
            skLineSegment(sketch, "E4457", {"start": v(20.6, 99.54) * mm, "end": v(20.5, 99.4) * mm});
            skLineSegment(sketch, "E4458", {"start": v(20.5, 99.4) * mm, "end": v(20.4, 99.25) * mm});
            skLineSegment(sketch, "E4459", {"start": v(20.4, 99.25) * mm, "end": v(20.29, 99.1) * mm});
            skLineSegment(sketch, "E4460", {"start": v(20.29, 99.1) * mm, "end": v(20.19, 98.96) * mm});
            skLineSegment(sketch, "E4461", {"start": v(20.19, 98.96) * mm, "end": v(20.09, 98.82) * mm});
            skLineSegment(sketch, "E4462", {"start": v(20.09, 98.82) * mm, "end": v(20, 98.68) * mm});
            skLineSegment(sketch, "E4463", {"start": v(20, 98.68) * mm, "end": v(19.9, 98.54) * mm});
            skLineSegment(sketch, "E4464", {"start": v(19.9, 98.54) * mm, "end": v(19.8, 98.4) * mm});
            skLineSegment(sketch, "E4465", {"start": v(19.8, 98.4) * mm, "end": v(19.7, 98.26) * mm});
            skLineSegment(sketch, "E4466", {"start": v(19.7, 98.26) * mm, "end": v(19.62, 98.12) * mm});
            skLineSegment(sketch, "E4467", {"start": v(19.62, 98.12) * mm, "end": v(19.53, 97.98) * mm});
            skLineSegment(sketch, "E4468", {"start": v(19.53, 97.98) * mm, "end": v(19.44, 97.85) * mm});
            skLineSegment(sketch, "E4469", {"start": v(19.44, 97.85) * mm, "end": v(19.35, 97.71) * mm});
            skLineSegment(sketch, "E4470", {"start": v(19.35, 97.71) * mm, "end": v(19.27, 97.58) * mm});
            skLineSegment(sketch, "E4471", {"start": v(19.27, 97.58) * mm, "end": v(19.18, 97.45) * mm});
            skLineSegment(sketch, "E4472", {"start": v(19.18, 97.45) * mm, "end": v(19.1, 97.32) * mm});
            skLineSegment(sketch, "E4473", {"start": v(19.1, 97.32) * mm, "end": v(19.02, 97.19) * mm});
            skLineSegment(sketch, "E4474", {"start": v(19.02, 97.19) * mm, "end": v(18.94, 97.06) * mm});
            skLineSegment(sketch, "E4475", {"start": v(18.94, 97.06) * mm, "end": v(18.87, 96.93) * mm});
            skLineSegment(sketch, "E4476", {"start": v(18.87, 96.93) * mm, "end": v(18.79, 96.8) * mm});
            skLineSegment(sketch, "E4477", {"start": v(18.79, 96.8) * mm, "end": v(18.72, 96.68) * mm});
            skLineSegment(sketch, "E4478", {"start": v(18.72, 96.68) * mm, "end": v(18.64, 96.56) * mm});
            skLineSegment(sketch, "E4479", {"start": v(18.64, 96.56) * mm, "end": v(18.57, 96.43) * mm});
            skLineSegment(sketch, "E4480", {"start": v(18.57, 96.43) * mm, "end": v(18.5, 96.31) * mm});
            skLineSegment(sketch, "E4481", {"start": v(18.5, 96.31) * mm, "end": v(18.43, 96.2) * mm});
            skLineSegment(sketch, "E4482", {"start": v(18.43, 96.2) * mm, "end": v(18.36, 96.07) * mm});
            skLineSegment(sketch, "E4483", {"start": v(18.36, 96.07) * mm, "end": v(18.3, 95.95) * mm});
            skLineSegment(sketch, "E4484", {"start": v(18.3, 95.95) * mm, "end": v(18.23, 95.84) * mm});
            skLineSegment(sketch, "E4485", {"start": v(18.23, 95.84) * mm, "end": v(18.17, 95.72) * mm});
            skLineSegment(sketch, "E4486", {"start": v(18.17, 95.72) * mm, "end": v(18.1, 95.6) * mm});
            skLineSegment(sketch, "E4487", {"start": v(18.1, 95.6) * mm, "end": v(18.05, 95.5) * mm});
            skLineSegment(sketch, "E4488", {"start": v(18.05, 95.5) * mm, "end": v(17.1, 95.6) * mm});
            skLineSegment(sketch, "E4489", {"start": v(17.1, 95.6) * mm, "end": v(16.2, 95.83) * mm});
            skLineSegment(sketch, "E4490", {"start": v(16.2, 95.83) * mm, "end": v(16.17, 95.95) * mm});
            skLineSegment(sketch, "E4491", {"start": v(16.17, 95.95) * mm, "end": v(16.15, 96.08) * mm});
            skLineSegment(sketch, "E4492", {"start": v(16.15, 96.08) * mm, "end": v(16.13, 96.21) * mm});
            skLineSegment(sketch, "E4493", {"start": v(16.13, 96.21) * mm, "end": v(16.11, 96.35) * mm});
            skLineSegment(sketch, "E4494", {"start": v(16.11, 96.35) * mm, "end": v(16.1, 96.48) * mm});
            skLineSegment(sketch, "E4495", {"start": v(16.1, 96.48) * mm, "end": v(16.07, 96.61) * mm});
            skLineSegment(sketch, "E4496", {"start": v(16.07, 96.61) * mm, "end": v(16.05, 96.75) * mm});
            skLineSegment(sketch, "E4497", {"start": v(16.05, 96.75) * mm, "end": v(16.02, 96.89) * mm});
            skLineSegment(sketch, "E4498", {"start": v(16.02, 96.89) * mm, "end": v(16, 97.03) * mm});
            skLineSegment(sketch, "E4499", {"start": v(16, 97.03) * mm, "end": v(15.97, 97.17) * mm});
            skLineSegment(sketch, "E4500", {"start": v(15.97, 97.17) * mm, "end": v(15.95, 97.31) * mm});
            skLineSegment(sketch, "E4501", {"start": v(15.95, 97.31) * mm, "end": v(15.92, 97.46) * mm});
            skLineSegment(sketch, "E4502", {"start": v(15.92, 97.46) * mm, "end": v(15.9, 97.6) * mm});
            skLineSegment(sketch, "E4503", {"start": v(15.9, 97.6) * mm, "end": v(15.86, 97.75) * mm});
            skLineSegment(sketch, "E4504", {"start": v(15.86, 97.75) * mm, "end": v(15.83, 97.9) * mm});
            skLineSegment(sketch, "E4505", {"start": v(15.83, 97.9) * mm, "end": v(15.8, 98.05) * mm});
            skLineSegment(sketch, "E4506", {"start": v(15.8, 98.05) * mm, "end": v(15.77, 98.2) * mm});
            skLineSegment(sketch, "E4507", {"start": v(15.77, 98.2) * mm, "end": v(15.74, 98.36) * mm});
            skLineSegment(sketch, "E4508", {"start": v(15.74, 98.36) * mm, "end": v(15.7, 98.52) * mm});
            skLineSegment(sketch, "E4509", {"start": v(15.7, 98.52) * mm, "end": v(15.67, 98.67) * mm});
            skLineSegment(sketch, "E4510", {"start": v(15.67, 98.67) * mm, "end": v(15.63, 98.83) * mm});
            skLineSegment(sketch, "E4511", {"start": v(15.63, 98.83) * mm, "end": v(15.6, 99) * mm});
            skLineSegment(sketch, "E4512", {"start": v(15.6, 99) * mm, "end": v(15.55, 99.16) * mm});
            skLineSegment(sketch, "E4513", {"start": v(15.55, 99.16) * mm, "end": v(15.51, 99.32) * mm});
            skLineSegment(sketch, "E4514", {"start": v(15.51, 99.32) * mm, "end": v(15.47, 99.49) * mm});
            skLineSegment(sketch, "E4515", {"start": v(15.47, 99.49) * mm, "end": v(15.43, 99.65) * mm});
            skLineSegment(sketch, "E4516", {"start": v(15.43, 99.65) * mm, "end": v(15.39, 99.82) * mm});
            skLineSegment(sketch, "E4517", {"start": v(15.39, 99.82) * mm, "end": v(15.34, 100) * mm});
            skLineSegment(sketch, "E4518", {"start": v(15.34, 100) * mm, "end": v(15.3, 100.16) * mm});
            skLineSegment(sketch, "E4519", {"start": v(15.3, 100.16) * mm, "end": v(15.25, 100.33) * mm});
            skLineSegment(sketch, "E4520", {"start": v(15.25, 100.33) * mm, "end": v(15.2, 100.5) * mm});
            skLineSegment(sketch, "E4521", {"start": v(15.2, 100.5) * mm, "end": v(15.15, 100.68) * mm});
            skLineSegment(sketch, "E4522", {"start": v(15.15, 100.68) * mm, "end": v(15.1, 100.86) * mm});
            skLineSegment(sketch, "E4523", {"start": v(15.1, 100.86) * mm, "end": v(15.05, 101.04) * mm});
            skLineSegment(sketch, "E4524", {"start": v(15.05, 101.04) * mm, "end": v(15, 101.22) * mm});
            skLineSegment(sketch, "E4525", {"start": v(15, 101.22) * mm, "end": v(14.94, 101.4) * mm});
            skLineSegment(sketch, "E4526", {"start": v(14.94, 101.4) * mm, "end": v(14.86, 101.42) * mm});
            skLineSegment(sketch, "E4527", {"start": v(14.86, 101.42) * mm, "end": v(13.3, 101.63) * mm});
            skLineSegment(sketch, "E4528", {"start": v(13.3, 101.63) * mm, "end": v(13.22, 101.64) * mm});
            skLineSegment(sketch, "E4529", {"start": v(13.22, 101.64) * mm, "end": v(13.12, 101.48) * mm});
            skLineSegment(sketch, "E4530", {"start": v(13.12, 101.48) * mm, "end": v(13.02, 101.32) * mm});
            skLineSegment(sketch, "E4531", {"start": v(13.02, 101.32) * mm, "end": v(12.92, 101.16) * mm});
            skLineSegment(sketch, "E4532", {"start": v(12.92, 101.16) * mm, "end": v(12.82, 101) * mm});
            skLineSegment(sketch, "E4533", {"start": v(12.82, 101) * mm, "end": v(12.73, 100.85) * mm});
            skLineSegment(sketch, "E4534", {"start": v(12.73, 100.85) * mm, "end": v(12.63, 100.7) * mm});
            skLineSegment(sketch, "E4535", {"start": v(12.63, 100.7) * mm, "end": v(12.54, 100.54) * mm});
            skLineSegment(sketch, "E4536", {"start": v(12.54, 100.54) * mm, "end": v(12.45, 100.4) * mm});
            skLineSegment(sketch, "E4537", {"start": v(12.45, 100.4) * mm, "end": v(12.36, 100.24) * mm});
            skLineSegment(sketch, "E4538", {"start": v(12.36, 100.24) * mm, "end": v(12.27, 100.09) * mm});
            skLineSegment(sketch, "E4539", {"start": v(12.27, 100.09) * mm, "end": v(12.19, 99.94) * mm});
            skLineSegment(sketch, "E4540", {"start": v(12.19, 99.94) * mm, "end": v(12.1, 99.8) * mm});
            skLineSegment(sketch, "E4541", {"start": v(12.1, 99.8) * mm, "end": v(12.02, 99.65) * mm});
            skLineSegment(sketch, "E4542", {"start": v(12.02, 99.65) * mm, "end": v(11.94, 99.5) * mm});
            skLineSegment(sketch, "E4543", {"start": v(11.94, 99.5) * mm, "end": v(11.86, 99.36) * mm});
            skLineSegment(sketch, "E4544", {"start": v(11.86, 99.36) * mm, "end": v(11.78, 99.21) * mm});
            skLineSegment(sketch, "E4545", {"start": v(11.78, 99.21) * mm, "end": v(11.7, 99.07) * mm});
            skLineSegment(sketch, "E4546", {"start": v(11.7, 99.07) * mm, "end": v(11.63, 98.93) * mm});
            skLineSegment(sketch, "E4547", {"start": v(11.63, 98.93) * mm, "end": v(11.55, 98.8) * mm});
            skLineSegment(sketch, "E4548", {"start": v(11.55, 98.8) * mm, "end": v(11.48, 98.65) * mm});
            skLineSegment(sketch, "E4549", {"start": v(11.48, 98.65) * mm, "end": v(11.4, 98.52) * mm});
            skLineSegment(sketch, "E4550", {"start": v(11.4, 98.52) * mm, "end": v(11.34, 98.38) * mm});
            skLineSegment(sketch, "E4551", {"start": v(11.34, 98.38) * mm, "end": v(11.27, 98.25) * mm});
            skLineSegment(sketch, "E4552", {"start": v(11.27, 98.25) * mm, "end": v(11.2, 98.11) * mm});
            skLineSegment(sketch, "E4553", {"start": v(11.2, 98.11) * mm, "end": v(11.14, 97.98) * mm});
            skLineSegment(sketch, "E4554", {"start": v(11.14, 97.98) * mm, "end": v(11.07, 97.85) * mm});
            skLineSegment(sketch, "E4555", {"start": v(11.07, 97.85) * mm, "end": v(11, 97.72) * mm});
            skLineSegment(sketch, "E4556", {"start": v(11, 97.72) * mm, "end": v(10.95, 97.6) * mm});
            skLineSegment(sketch, "E4557", {"start": v(10.95, 97.6) * mm, "end": v(10.89, 97.47) * mm});
            skLineSegment(sketch, "E4558", {"start": v(10.89, 97.47) * mm, "end": v(10.83, 97.34) * mm});
            skLineSegment(sketch, "E4559", {"start": v(10.83, 97.34) * mm, "end": v(10.77, 97.22) * mm});
            skLineSegment(sketch, "E4560", {"start": v(10.77, 97.22) * mm, "end": v(10.71, 97.1) * mm});
            skLineSegment(sketch, "E4561", {"start": v(10.71, 97.1) * mm, "end": v(10.66, 96.97) * mm});
            skLineSegment(sketch, "E4562", {"start": v(10.66, 96.97) * mm, "end": v(10.6, 96.85) * mm});
            skLineSegment(sketch, "E4563", {"start": v(10.6, 96.85) * mm, "end": v(10.55, 96.73) * mm});
            skLineSegment(sketch, "E4564", {"start": v(10.55, 96.73) * mm, "end": v(10.5, 96.62) * mm});
            skLineSegment(sketch, "E4565", {"start": v(10.5, 96.62) * mm, "end": v(9.56, 96.65) * mm});
            skLineSegment(sketch, "E4566", {"start": v(9.56, 96.65) * mm, "end": v(8.62, 96.8) * mm});
            skLineSegment(sketch, "E4567", {"start": v(8.62, 96.8) * mm, "end": v(8.6, 96.93) * mm});
            skLineSegment(sketch, "E4568", {"start": v(8.6, 96.93) * mm, "end": v(8.57, 97.05) * mm});
            skLineSegment(sketch, "E4569", {"start": v(8.57, 97.05) * mm, "end": v(8.54, 97.18) * mm});
            skLineSegment(sketch, "E4570", {"start": v(8.54, 97.18) * mm, "end": v(8.5, 97.31) * mm});
            skLineSegment(sketch, "E4571", {"start": v(8.5, 97.31) * mm, "end": v(8.47, 97.44) * mm});
            skLineSegment(sketch, "E4572", {"start": v(8.47, 97.44) * mm, "end": v(8.44, 97.58) * mm});
            skLineSegment(sketch, "E4573", {"start": v(8.44, 97.58) * mm, "end": v(8.4, 97.71) * mm});
            skLineSegment(sketch, "E4574", {"start": v(8.4, 97.71) * mm, "end": v(8.37, 97.85) * mm});
            skLineSegment(sketch, "E4575", {"start": v(8.37, 97.85) * mm, "end": v(8.34, 97.98) * mm});
            skLineSegment(sketch, "E4576", {"start": v(8.34, 97.98) * mm, "end": v(8.3, 98.12) * mm});
            skLineSegment(sketch, "E4577", {"start": v(8.3, 98.12) * mm, "end": v(8.26, 98.26) * mm});
            skLineSegment(sketch, "E4578", {"start": v(8.26, 98.26) * mm, "end": v(8.23, 98.4) * mm});
            skLineSegment(sketch, "E4579", {"start": v(8.23, 98.4) * mm, "end": v(8.19, 98.55) * mm});
            skLineSegment(sketch, "E4580", {"start": v(8.19, 98.55) * mm, "end": v(8.14, 98.7) * mm});
            skLineSegment(sketch, "E4581", {"start": v(8.14, 98.7) * mm, "end": v(8.1, 98.84) * mm});
            skLineSegment(sketch, "E4582", {"start": v(8.1, 98.84) * mm, "end": v(8.06, 99) * mm});
            skLineSegment(sketch, "E4583", {"start": v(8.06, 99) * mm, "end": v(8.02, 99.14) * mm});
            skLineSegment(sketch, "E4584", {"start": v(8.02, 99.14) * mm, "end": v(7.97, 99.3) * mm});
            skLineSegment(sketch, "E4585", {"start": v(7.97, 99.3) * mm, "end": v(7.92, 99.44) * mm});
            skLineSegment(sketch, "E4586", {"start": v(7.92, 99.44) * mm, "end": v(7.88, 99.6) * mm});
            skLineSegment(sketch, "E4587", {"start": v(7.88, 99.6) * mm, "end": v(7.83, 99.75) * mm});
            skLineSegment(sketch, "E4588", {"start": v(7.83, 99.75) * mm, "end": v(7.78, 99.91) * mm});
            skLineSegment(sketch, "E4589", {"start": v(7.78, 99.91) * mm, "end": v(7.72, 100.07) * mm});
            skLineSegment(sketch, "E4590", {"start": v(7.72, 100.07) * mm, "end": v(7.67, 100.23) * mm});
            skLineSegment(sketch, "E4591", {"start": v(7.67, 100.23) * mm, "end": v(7.62, 100.4) * mm});
            skLineSegment(sketch, "E4592", {"start": v(7.62, 100.4) * mm, "end": v(7.56, 100.56) * mm});
            skLineSegment(sketch, "E4593", {"start": v(7.56, 100.56) * mm, "end": v(7.5, 100.72) * mm});
            skLineSegment(sketch, "E4594", {"start": v(7.5, 100.72) * mm, "end": v(7.45, 100.89) * mm});
            skLineSegment(sketch, "E4595", {"start": v(7.45, 100.89) * mm, "end": v(7.39, 101.05) * mm});
            skLineSegment(sketch, "E4596", {"start": v(7.39, 101.05) * mm, "end": v(7.33, 101.22) * mm});
            skLineSegment(sketch, "E4597", {"start": v(7.33, 101.22) * mm, "end": v(7.27, 101.4) * mm});
            skLineSegment(sketch, "E4598", {"start": v(7.27, 101.4) * mm, "end": v(7.2, 101.56) * mm});
            skLineSegment(sketch, "E4599", {"start": v(7.2, 101.56) * mm, "end": v(7.14, 101.74) * mm});
            skLineSegment(sketch, "E4600", {"start": v(7.14, 101.74) * mm, "end": v(7.07, 101.91) * mm});
            skLineSegment(sketch, "E4601", {"start": v(7.07, 101.91) * mm, "end": v(7, 102.09) * mm});
            skLineSegment(sketch, "E4602", {"start": v(7, 102.09) * mm, "end": v(6.94, 102.26) * mm});
            skLineSegment(sketch, "E4603", {"start": v(6.94, 102.26) * mm, "end": v(6.86, 102.27) * mm});
            skLineSegment(sketch, "E4604", {"start": v(6.86, 102.27) * mm, "end": v(5.29, 102.36) * mm});
            skLineSegment(sketch, "E4605", {"start": v(5.29, 102.36) * mm, "end": v(5.2, 102.37) * mm});
            skLineSegment(sketch, "E4606", {"start": v(5.2, 102.37) * mm, "end": v(5.12, 102.2) * mm});
            skLineSegment(sketch, "E4607", {"start": v(5.12, 102.2) * mm, "end": v(5.03, 102.03) * mm});
            skLineSegment(sketch, "E4608", {"start": v(5.03, 102.03) * mm, "end": v(4.94, 101.87) * mm});
            skLineSegment(sketch, "E4609", {"start": v(4.94, 101.87) * mm, "end": v(4.86, 101.7) * mm});
            skLineSegment(sketch, "E4610", {"start": v(4.86, 101.7) * mm, "end": v(4.78, 101.54) * mm});
            skLineSegment(sketch, "E4611", {"start": v(4.78, 101.54) * mm, "end": v(4.7, 101.38) * mm});
            skLineSegment(sketch, "E4612", {"start": v(4.7, 101.38) * mm, "end": v(4.61, 101.22) * mm});
            skLineSegment(sketch, "E4613", {"start": v(4.61, 101.22) * mm, "end": v(4.54, 101.06) * mm});
            skLineSegment(sketch, "E4614", {"start": v(4.54, 101.06) * mm, "end": v(4.46, 100.9) * mm});
            skLineSegment(sketch, "E4615", {"start": v(4.46, 100.9) * mm, "end": v(4.38, 100.74) * mm});
            skLineSegment(sketch, "E4616", {"start": v(4.38, 100.74) * mm, "end": v(4.3, 100.59) * mm});
            skLineSegment(sketch, "E4617", {"start": v(4.3, 100.59) * mm, "end": v(4.24, 100.43) * mm});
            skLineSegment(sketch, "E4618", {"start": v(4.24, 100.43) * mm, "end": v(4.16, 100.28) * mm});
            skLineSegment(sketch, "E4619", {"start": v(4.16, 100.28) * mm, "end": v(4.1, 100.13) * mm});
            skLineSegment(sketch, "E4620", {"start": v(4.1, 100.13) * mm, "end": v(4.03, 99.98) * mm});
            skLineSegment(sketch, "E4621", {"start": v(4.03, 99.98) * mm, "end": v(3.96, 99.83) * mm});
            skLineSegment(sketch, "E4622", {"start": v(3.96, 99.83) * mm, "end": v(3.9, 99.68) * mm});
            skLineSegment(sketch, "E4623", {"start": v(3.9, 99.68) * mm, "end": v(3.83, 99.54) * mm});
            skLineSegment(sketch, "E4624", {"start": v(3.83, 99.54) * mm, "end": v(3.77, 99.4) * mm});
            skLineSegment(sketch, "E4625", {"start": v(3.77, 99.4) * mm, "end": v(3.7, 99.25) * mm});
            skLineSegment(sketch, "E4626", {"start": v(3.7, 99.25) * mm, "end": v(3.64, 99.1) * mm});
            skLineSegment(sketch, "E4627", {"start": v(3.64, 99.1) * mm, "end": v(3.58, 98.97) * mm});
            skLineSegment(sketch, "E4628", {"start": v(3.58, 98.97) * mm, "end": v(3.53, 98.83) * mm});
            skLineSegment(sketch, "E4629", {"start": v(3.53, 98.83) * mm, "end": v(3.47, 98.69) * mm});
            skLineSegment(sketch, "E4630", {"start": v(3.47, 98.69) * mm, "end": v(3.41, 98.55) * mm});
            skLineSegment(sketch, "E4631", {"start": v(3.41, 98.55) * mm, "end": v(3.36, 98.42) * mm});
            skLineSegment(sketch, "E4632", {"start": v(3.36, 98.42) * mm, "end": v(3.3, 98.28) * mm});
            skLineSegment(sketch, "E4633", {"start": v(3.3, 98.28) * mm, "end": v(3.26, 98.15) * mm});
            skLineSegment(sketch, "E4634", {"start": v(3.26, 98.15) * mm, "end": v(3.2, 98.02) * mm});
            skLineSegment(sketch, "E4635", {"start": v(3.2, 98.02) * mm, "end": v(3.16, 97.9) * mm});
            skLineSegment(sketch, "E4636", {"start": v(3.16, 97.9) * mm, "end": v(3.1, 97.76) * mm});
            skLineSegment(sketch, "E4637", {"start": v(3.1, 97.76) * mm, "end": v(3.06, 97.64) * mm});
            skLineSegment(sketch, "E4638", {"start": v(3.06, 97.64) * mm, "end": v(3.02, 97.51) * mm});
            skLineSegment(sketch, "E4639", {"start": v(3.02, 97.51) * mm, "end": v(2.97, 97.39) * mm});
            skLineSegment(sketch, "E4640", {"start": v(2.97, 97.39) * mm, "end": v(2.93, 97.26) * mm});
            skLineSegment(sketch, "E4641", {"start": v(2.93, 97.26) * mm, "end": v(2.89, 97.14) * mm});
            skLineSegment(sketch, "E4642", {"start": v(2.89, 97.14) * mm, "end": v(1.94, 97.1) * mm});
            skLineSegment(sketch, "E4643", {"start": v(1.94, 97.1) * mm, "end": v(1, 97.18) * mm});
            skLineSegment(sketch, "E4644", {"start": v(1, 97.18) * mm, "end": v(0.96, 97.3) * mm});
            skLineSegment(sketch, "E4645", {"start": v(0.96, 97.3) * mm, "end": v(0.92, 97.43) * mm});
            skLineSegment(sketch, "E4646", {"start": v(0.92, 97.43) * mm, "end": v(0.88, 97.55) * mm});
            skLineSegment(sketch, "E4647", {"start": v(0.88, 97.55) * mm, "end": v(0.84, 97.68) * mm});
            skLineSegment(sketch, "E4648", {"start": v(0.84, 97.68) * mm, "end": v(0.8, 97.8) * mm});
            skLineSegment(sketch, "E4649", {"start": v(0.8, 97.8) * mm, "end": v(0.76, 97.94) * mm});
            skLineSegment(sketch, "E4650", {"start": v(0.76, 97.94) * mm, "end": v(0.72, 98.07) * mm});
            skLineSegment(sketch, "E4651", {"start": v(0.72, 98.07) * mm, "end": v(0.67, 98.2) * mm});
            skLineSegment(sketch, "E4652", {"start": v(0.67, 98.2) * mm, "end": v(0.62, 98.34) * mm});
            skLineSegment(sketch, "E4653", {"start": v(0.62, 98.34) * mm, "end": v(0.58, 98.47) * mm});
            skLineSegment(sketch, "E4654", {"start": v(0.58, 98.47) * mm, "end": v(0.53, 98.6) * mm});
            skLineSegment(sketch, "E4655", {"start": v(0.53, 98.6) * mm, "end": v(0.48, 98.75) * mm});
            skLineSegment(sketch, "E4656", {"start": v(0.48, 98.75) * mm, "end": v(0.43, 98.89) * mm});
            skLineSegment(sketch, "E4657", {"start": v(0.43, 98.89) * mm, "end": v(0.38, 99.03) * mm});
            skLineSegment(sketch, "E4658", {"start": v(0.38, 99.03) * mm, "end": v(0.32, 99.17) * mm});
            skLineSegment(sketch, "E4659", {"start": v(0.32, 99.17) * mm, "end": v(0.27, 99.32) * mm});
            skLineSegment(sketch, "E4660", {"start": v(0.27, 99.32) * mm, "end": v(0.21, 99.46) * mm});
            skLineSegment(sketch, "E4661", {"start": v(0.21, 99.46) * mm, "end": v(0.15, 99.61) * mm});
            skLineSegment(sketch, "E4662", {"start": v(0.15, 99.61) * mm, "end": v(0.1, 99.76) * mm});
            skLineSegment(sketch, "E4663", {"start": v(0.1, 99.76) * mm, "end": v(0.04, 99.9) * mm});
            skLineSegment(sketch, "E4664", {"start": v(0.04, 99.9) * mm, "end": v(-0.02, 100.06) * mm});
            skLineSegment(sketch, "E4665", {"start": v(-0.02, 100.06) * mm, "end": v(-0.09, 100.21) * mm});
            skLineSegment(sketch, "E4666", {"start": v(-0.09, 100.21) * mm, "end": v(-0.15, 100.37) * mm});
            skLineSegment(sketch, "E4667", {"start": v(-0.15, 100.37) * mm, "end": v(-0.22, 100.52) * mm});
            skLineSegment(sketch, "E4668", {"start": v(-0.22, 100.52) * mm, "end": v(-0.28, 100.68) * mm});
            skLineSegment(sketch, "E4669", {"start": v(-0.28, 100.68) * mm, "end": v(-0.35, 100.84) * mm});
            skLineSegment(sketch, "E4670", {"start": v(-0.35, 100.84) * mm, "end": v(-0.42, 101) * mm});
            skLineSegment(sketch, "E4671", {"start": v(-0.42, 101) * mm, "end": v(-0.5, 101.16) * mm});
            skLineSegment(sketch, "E4672", {"start": v(-0.5, 101.16) * mm, "end": v(-0.56, 101.32) * mm});
            skLineSegment(sketch, "E4673", {"start": v(-0.56, 101.32) * mm, "end": v(-0.64, 101.48) * mm});
            skLineSegment(sketch, "E4674", {"start": v(-0.64, 101.48) * mm, "end": v(-0.71, 101.65) * mm});
            skLineSegment(sketch, "E4675", {"start": v(-0.71, 101.65) * mm, "end": v(-0.79, 101.82) * mm});
            skLineSegment(sketch, "E4676", {"start": v(-0.79, 101.82) * mm, "end": v(-0.87, 101.98) * mm});
            skLineSegment(sketch, "E4677", {"start": v(-0.87, 101.98) * mm, "end": v(-0.94, 102.15) * mm});
            skLineSegment(sketch, "E4678", {"start": v(-0.94, 102.15) * mm, "end": v(-1.03, 102.32) * mm});
            skLineSegment(sketch, "E4679", {"start": v(-1.03, 102.32) * mm, "end": v(-1.1, 102.5) * mm});
            skLineSegment(sketch, "E4680", {"start": v(-1.1, 102.5) * mm, "end": v(-1.19, 102.5) * mm});
            skLineSegment(sketch, "E4681", {"start": v(-1.19, 102.5) * mm, "end": v(-2.76, 102.46) * mm});
            skLineSegment(sketch, "E4682", {"start": v(-2.76, 102.46) * mm, "end": v(-2.84, 102.46) * mm});
            skLineSegment(sketch, "E4683", {"start": v(-2.84, 102.46) * mm, "end": v(-2.92, 102.28) * mm});
            skLineSegment(sketch, "E4684", {"start": v(-2.92, 102.28) * mm, "end": v(-3, 102.11) * mm});
            skLineSegment(sketch, "E4685", {"start": v(-3, 102.11) * mm, "end": v(-3.06, 101.94) * mm});
            skLineSegment(sketch, "E4686", {"start": v(-3.06, 101.94) * mm, "end": v(-3.14, 101.77) * mm});
            skLineSegment(sketch, "E4687", {"start": v(-3.14, 101.77) * mm, "end": v(-3.2, 101.6) * mm});
            skLineSegment(sketch, "E4688", {"start": v(-3.2, 101.6) * mm, "end": v(-3.27, 101.43) * mm});
            skLineSegment(sketch, "E4689", {"start": v(-3.27, 101.43) * mm, "end": v(-3.34, 101.27) * mm});
            skLineSegment(sketch, "E4690", {"start": v(-3.34, 101.27) * mm, "end": v(-3.4, 101.1) * mm});
            skLineSegment(sketch, "E4691", {"start": v(-3.4, 101.1) * mm, "end": v(-3.47, 100.94) * mm});
            skLineSegment(sketch, "E4692", {"start": v(-3.47, 100.94) * mm, "end": v(-3.54, 100.78) * mm});
            skLineSegment(sketch, "E4693", {"start": v(-3.54, 100.78) * mm, "end": v(-3.6, 100.62) * mm});
            skLineSegment(sketch, "E4694", {"start": v(-3.6, 100.62) * mm, "end": v(-3.66, 100.46) * mm});
            skLineSegment(sketch, "E4695", {"start": v(-3.66, 100.46) * mm, "end": v(-3.72, 100.3) * mm});
            skLineSegment(sketch, "E4696", {"start": v(-3.72, 100.3) * mm, "end": v(-3.77, 100.14) * mm});
            skLineSegment(sketch, "E4697", {"start": v(-3.77, 100.14) * mm, "end": v(-3.83, 99.99) * mm});
            skLineSegment(sketch, "E4698", {"start": v(-3.83, 99.99) * mm, "end": v(-3.89, 99.83) * mm});
            skLineSegment(sketch, "E4699", {"start": v(-3.89, 99.83) * mm, "end": v(-3.94, 99.68) * mm});
            skLineSegment(sketch, "E4700", {"start": v(-3.94, 99.68) * mm, "end": v(-4, 99.53) * mm});
            skLineSegment(sketch, "E4701", {"start": v(-4, 99.53) * mm, "end": v(-4.04, 99.38) * mm});
            skLineSegment(sketch, "E4702", {"start": v(-4.04, 99.38) * mm, "end": v(-4.1, 99.23) * mm});
            skLineSegment(sketch, "E4703", {"start": v(-4.1, 99.23) * mm, "end": v(-4.14, 99.09) * mm});
            skLineSegment(sketch, "E4704", {"start": v(-4.14, 99.09) * mm, "end": v(-4.2, 98.94) * mm});
            skLineSegment(sketch, "E4705", {"start": v(-4.2, 98.94) * mm, "end": v(-4.24, 98.8) * mm});
            skLineSegment(sketch, "E4706", {"start": v(-4.24, 98.8) * mm, "end": v(-4.28, 98.66) * mm});
            skLineSegment(sketch, "E4707", {"start": v(-4.28, 98.66) * mm, "end": v(-4.33, 98.52) * mm});
            skLineSegment(sketch, "E4708", {"start": v(-4.33, 98.52) * mm, "end": v(-4.37, 98.38) * mm});
            skLineSegment(sketch, "E4709", {"start": v(-4.37, 98.38) * mm, "end": v(-4.41, 98.24) * mm});
            skLineSegment(sketch, "E4710", {"start": v(-4.41, 98.24) * mm, "end": v(-4.45, 98.1) * mm});
            skLineSegment(sketch, "E4711", {"start": v(-4.45, 98.1) * mm, "end": v(-4.5, 97.97) * mm});
            skLineSegment(sketch, "E4712", {"start": v(-4.5, 97.97) * mm, "end": v(-4.53, 97.84) * mm});
            skLineSegment(sketch, "E4713", {"start": v(-4.53, 97.84) * mm, "end": v(-4.57, 97.7) * mm});
            skLineSegment(sketch, "E4714", {"start": v(-4.57, 97.7) * mm, "end": v(-4.6, 97.57) * mm});
            skLineSegment(sketch, "E4715", {"start": v(-4.6, 97.57) * mm, "end": v(-4.64, 97.45) * mm});
            skLineSegment(sketch, "E4716", {"start": v(-4.64, 97.45) * mm, "end": v(-4.68, 97.32) * mm});
            skLineSegment(sketch, "E4717", {"start": v(-4.68, 97.32) * mm, "end": v(-4.71, 97.2) * mm});
            skLineSegment(sketch, "E4718", {"start": v(-4.71, 97.2) * mm, "end": v(-4.74, 97.07) * mm});
            skLineSegment(sketch, "E4719", {"start": v(-4.74, 97.07) * mm, "end": v(-5.68, 96.96) * mm});
            skLineSegment(sketch, "E4720", {"start": v(-5.68, 96.96) * mm, "end": v(-6.63, 96.96) * mm});
            skLineSegment(sketch, "E4721", {"start": v(-6.63, 96.96) * mm, "end": v(-6.67, 97.08) * mm});
            skLineSegment(sketch, "E4722", {"start": v(-6.67, 97.08) * mm, "end": v(-6.72, 97.2) * mm});
            skLineSegment(sketch, "E4723", {"start": v(-6.72, 97.2) * mm, "end": v(-6.77, 97.32) * mm});
            skLineSegment(sketch, "E4724", {"start": v(-6.77, 97.32) * mm, "end": v(-6.82, 97.44) * mm});
            skLineSegment(sketch, "E4725", {"start": v(-6.82, 97.44) * mm, "end": v(-6.87, 97.57) * mm});
            skLineSegment(sketch, "E4726", {"start": v(-6.87, 97.57) * mm, "end": v(-6.93, 97.7) * mm});
            skLineSegment(sketch, "E4727", {"start": v(-6.93, 97.7) * mm, "end": v(-6.98, 97.82) * mm});
            skLineSegment(sketch, "E4728", {"start": v(-6.98, 97.82) * mm, "end": v(-7.04, 97.95) * mm});
            skLineSegment(sketch, "E4729", {"start": v(-7.04, 97.95) * mm, "end": v(-7.1, 98.08) * mm});
            skLineSegment(sketch, "E4730", {"start": v(-7.1, 98.08) * mm, "end": v(-7.15, 98.21) * mm});
            skLineSegment(sketch, "E4731", {"start": v(-7.15, 98.21) * mm, "end": v(-7.2, 98.35) * mm});
            skLineSegment(sketch, "E4732", {"start": v(-7.2, 98.35) * mm, "end": v(-7.27, 98.48) * mm});
            skLineSegment(sketch, "E4733", {"start": v(-7.27, 98.48) * mm, "end": v(-7.33, 98.62) * mm});
            skLineSegment(sketch, "E4734", {"start": v(-7.33, 98.62) * mm, "end": v(-7.4, 98.75) * mm});
            skLineSegment(sketch, "E4735", {"start": v(-7.4, 98.75) * mm, "end": v(-7.46, 98.9) * mm});
            skLineSegment(sketch, "E4736", {"start": v(-7.46, 98.9) * mm, "end": v(-7.53, 99.03) * mm});
            skLineSegment(sketch, "E4737", {"start": v(-7.53, 99.03) * mm, "end": v(-7.6, 99.17) * mm});
            skLineSegment(sketch, "E4738", {"start": v(-7.6, 99.17) * mm, "end": v(-7.66, 99.32) * mm});
            skLineSegment(sketch, "E4739", {"start": v(-7.66, 99.32) * mm, "end": v(-7.73, 99.46) * mm});
            skLineSegment(sketch, "E4740", {"start": v(-7.73, 99.46) * mm, "end": v(-7.8, 99.6) * mm});
            skLineSegment(sketch, "E4741", {"start": v(-7.8, 99.6) * mm, "end": v(-7.88, 99.75) * mm});
            skLineSegment(sketch, "E4742", {"start": v(-7.88, 99.75) * mm, "end": v(-7.95, 99.9) * mm});
            skLineSegment(sketch, "E4743", {"start": v(-7.95, 99.9) * mm, "end": v(-8.03, 100.05) * mm});
            skLineSegment(sketch, "E4744", {"start": v(-8.03, 100.05) * mm, "end": v(-8.1, 100.2) * mm});
            skLineSegment(sketch, "E4745", {"start": v(-8.1, 100.2) * mm, "end": v(-8.18, 100.35) * mm});
            skLineSegment(sketch, "E4746", {"start": v(-8.18, 100.35) * mm, "end": v(-8.26, 100.5) * mm});
            skLineSegment(sketch, "E4747", {"start": v(-8.26, 100.5) * mm, "end": v(-8.34, 100.65) * mm});
            skLineSegment(sketch, "E4748", {"start": v(-8.34, 100.65) * mm, "end": v(-8.43, 100.8) * mm});
            skLineSegment(sketch, "E4749", {"start": v(-8.43, 100.8) * mm, "end": v(-8.51, 100.96) * mm});
            skLineSegment(sketch, "E4750", {"start": v(-8.51, 100.96) * mm, "end": v(-8.6, 101.12) * mm});
            skLineSegment(sketch, "E4751", {"start": v(-8.6, 101.12) * mm, "end": v(-8.68, 101.28) * mm});
            skLineSegment(sketch, "E4752", {"start": v(-8.68, 101.28) * mm, "end": v(-8.77, 101.44) * mm});
            skLineSegment(sketch, "E4753", {"start": v(-8.77, 101.44) * mm, "end": v(-8.86, 101.6) * mm});
            skLineSegment(sketch, "E4754", {"start": v(-8.86, 101.6) * mm, "end": v(-8.96, 101.76) * mm});
            skLineSegment(sketch, "E4755", {"start": v(-8.96, 101.76) * mm, "end": v(-9.05, 101.92) * mm});
            skLineSegment(sketch, "E4756", {"start": v(-9.05, 101.92) * mm, "end": v(-9.15, 102.09) * mm});
            skLineSegment(sketch, "E4757", {"start": v(-9.15, 102.09) * mm, "end": v(-9.23, 102.08) * mm});
            skLineSegment(sketch, "E4758", {"start": v(-9.23, 102.08) * mm, "end": v(-10.8, 101.93) * mm});
            skLineSegment(sketch, "E4759", {"start": v(-10.8, 101.93) * mm, "end": v(-10.87, 101.92) * mm});
            skLineSegment(sketch, "E4760", {"start": v(-10.87, 101.92) * mm, "end": v(-10.93, 101.74) * mm});
            skLineSegment(sketch, "E4761", {"start": v(-10.93, 101.74) * mm, "end": v(-11, 101.56) * mm});
            skLineSegment(sketch, "E4762", {"start": v(-11, 101.56) * mm, "end": v(-11.05, 101.39) * mm});
            skLineSegment(sketch, "E4763", {"start": v(-11.05, 101.39) * mm, "end": v(-11.11, 101.21) * mm});
            skLineSegment(sketch, "E4764", {"start": v(-11.11, 101.21) * mm, "end": v(-11.17, 101.04) * mm});
            skLineSegment(sketch, "E4765", {"start": v(-11.17, 101.04) * mm, "end": v(-11.22, 100.86) * mm});
            skLineSegment(sketch, "E4766", {"start": v(-11.22, 100.86) * mm, "end": v(-11.28, 100.7) * mm});
            skLineSegment(sketch, "E4767", {"start": v(-11.28, 100.7) * mm, "end": v(-11.33, 100.52) * mm});
            skLineSegment(sketch, "E4768", {"start": v(-11.33, 100.52) * mm, "end": v(-11.38, 100.36) * mm});
            skLineSegment(sketch, "E4769", {"start": v(-11.38, 100.36) * mm, "end": v(-11.43, 100.19) * mm});
            skLineSegment(sketch, "E4770", {"start": v(-11.43, 100.19) * mm, "end": v(-11.48, 100.02) * mm});
            skLineSegment(sketch, "E4771", {"start": v(-11.48, 100.02) * mm, "end": v(-11.53, 99.86) * mm});
            skLineSegment(sketch, "E4772", {"start": v(-11.53, 99.86) * mm, "end": v(-11.57, 99.7) * mm});
            skLineSegment(sketch, "E4773", {"start": v(-11.57, 99.7) * mm, "end": v(-11.62, 99.54) * mm});
            skLineSegment(sketch, "E4774", {"start": v(-11.62, 99.54) * mm, "end": v(-11.66, 99.38) * mm});
            skLineSegment(sketch, "E4775", {"start": v(-11.66, 99.38) * mm, "end": v(-11.7, 99.22) * mm});
            skLineSegment(sketch, "E4776", {"start": v(-11.7, 99.22) * mm, "end": v(-11.75, 99.07) * mm});
            skLineSegment(sketch, "E4777", {"start": v(-11.75, 99.07) * mm, "end": v(-11.79, 98.91) * mm});
            skLineSegment(sketch, "E4778", {"start": v(-11.79, 98.91) * mm, "end": v(-11.83, 98.76) * mm});
            skLineSegment(sketch, "E4779", {"start": v(-11.83, 98.76) * mm, "end": v(-11.87, 98.6) * mm});
            skLineSegment(sketch, "E4780", {"start": v(-11.87, 98.6) * mm, "end": v(-11.9, 98.46) * mm});
            skLineSegment(sketch, "E4781", {"start": v(-11.9, 98.46) * mm, "end": v(-11.94, 98.3) * mm});
            skLineSegment(sketch, "E4782", {"start": v(-11.94, 98.3) * mm, "end": v(-11.98, 98.16) * mm});
            skLineSegment(sketch, "E4783", {"start": v(-11.98, 98.16) * mm, "end": v(-12.01, 98.02) * mm});
            skLineSegment(sketch, "E4784", {"start": v(-12.01, 98.02) * mm, "end": v(-12.04, 97.87) * mm});
            skLineSegment(sketch, "E4785", {"start": v(-12.04, 97.87) * mm, "end": v(-12.08, 97.73) * mm});
            skLineSegment(sketch, "E4786", {"start": v(-12.08, 97.73) * mm, "end": v(-12.1, 97.6) * mm});
            skLineSegment(sketch, "E4787", {"start": v(-12.1, 97.6) * mm, "end": v(-12.14, 97.45) * mm});
            skLineSegment(sketch, "E4788", {"start": v(-12.14, 97.45) * mm, "end": v(-12.17, 97.31) * mm});
            skLineSegment(sketch, "E4789", {"start": v(-12.17, 97.31) * mm, "end": v(-12.2, 97.18) * mm});
            skLineSegment(sketch, "E4790", {"start": v(-12.2, 97.18) * mm, "end": v(-12.22, 97.04) * mm});
            skLineSegment(sketch, "E4791", {"start": v(-12.22, 97.04) * mm, "end": v(-12.25, 96.91) * mm});
            skLineSegment(sketch, "E4792", {"start": v(-12.25, 96.91) * mm, "end": v(-12.27, 96.78) * mm});
            skLineSegment(sketch, "E4793", {"start": v(-12.27, 96.78) * mm, "end": v(-12.3, 96.65) * mm});
            skLineSegment(sketch, "E4794", {"start": v(-12.3, 96.65) * mm, "end": v(-12.32, 96.52) * mm});
            skLineSegment(sketch, "E4795", {"start": v(-12.32, 96.52) * mm, "end": v(-12.35, 96.4) * mm});
            skLineSegment(sketch, "E4796", {"start": v(-12.35, 96.4) * mm, "end": v(-13.27, 96.21) * mm});
            skLineSegment(sketch, "E4797", {"start": v(-13.27, 96.21) * mm, "end": v(-14.21, 96.14) * mm});
            skLineSegment(sketch, "E4798", {"start": v(-14.21, 96.14) * mm, "end": v(-14.27, 96.26) * mm});
            skLineSegment(sketch, "E4799", {"start": v(-14.27, 96.26) * mm, "end": v(-14.33, 96.37) * mm});
            skLineSegment(sketch, "E4800", {"start": v(-14.33, 96.37) * mm, "end": v(-14.39, 96.5) * mm});
            skLineSegment(sketch, "E4801", {"start": v(-14.39, 96.5) * mm, "end": v(-14.45, 96.6) * mm});
            skLineSegment(sketch, "E4802", {"start": v(-14.45, 96.6) * mm, "end": v(-14.5, 96.73) * mm});
            skLineSegment(sketch, "E4803", {"start": v(-14.5, 96.73) * mm, "end": v(-14.57, 96.85) * mm});
            skLineSegment(sketch, "E4804", {"start": v(-14.57, 96.85) * mm, "end": v(-14.63, 96.97) * mm});
            skLineSegment(sketch, "E4805", {"start": v(-14.63, 96.97) * mm, "end": v(-14.7, 97.1) * mm});
            skLineSegment(sketch, "E4806", {"start": v(-14.7, 97.1) * mm, "end": v(-14.77, 97.22) * mm});
            skLineSegment(sketch, "E4807", {"start": v(-14.77, 97.22) * mm, "end": v(-14.83, 97.35) * mm});
            skLineSegment(sketch, "E4808", {"start": v(-14.83, 97.35) * mm, "end": v(-14.9, 97.48) * mm});
            skLineSegment(sketch, "E4809", {"start": v(-14.9, 97.48) * mm, "end": v(-14.97, 97.6) * mm});
            skLineSegment(sketch, "E4810", {"start": v(-14.97, 97.6) * mm, "end": v(-15.05, 97.74) * mm});
            skLineSegment(sketch, "E4811", {"start": v(-15.05, 97.74) * mm, "end": v(-15.12, 97.87) * mm});
            skLineSegment(sketch, "E4812", {"start": v(-15.12, 97.87) * mm, "end": v(-15.2, 98) * mm});
            skLineSegment(sketch, "E4813", {"start": v(-15.2, 98) * mm, "end": v(-15.27, 98.14) * mm});
            skLineSegment(sketch, "E4814", {"start": v(-15.27, 98.14) * mm, "end": v(-15.35, 98.27) * mm});
            skLineSegment(sketch, "E4815", {"start": v(-15.35, 98.27) * mm, "end": v(-15.43, 98.4) * mm});
            skLineSegment(sketch, "E4816", {"start": v(-15.43, 98.4) * mm, "end": v(-15.51, 98.55) * mm});
            skLineSegment(sketch, "E4817", {"start": v(-15.51, 98.55) * mm, "end": v(-15.6, 98.69) * mm});
            skLineSegment(sketch, "E4818", {"start": v(-15.6, 98.69) * mm, "end": v(-15.68, 98.83) * mm});
            skLineSegment(sketch, "E4819", {"start": v(-15.68, 98.83) * mm, "end": v(-15.76, 98.97) * mm});
            skLineSegment(sketch, "E4820", {"start": v(-15.76, 98.97) * mm, "end": v(-15.85, 99.1) * mm});
            skLineSegment(sketch, "E4821", {"start": v(-15.85, 99.1) * mm, "end": v(-15.94, 99.25) * mm});
            skLineSegment(sketch, "E4822", {"start": v(-15.94, 99.25) * mm, "end": v(-16.03, 99.4) * mm});
            skLineSegment(sketch, "E4823", {"start": v(-16.03, 99.4) * mm, "end": v(-16.12, 99.54) * mm});
            skLineSegment(sketch, "E4824", {"start": v(-16.12, 99.54) * mm, "end": v(-16.21, 99.69) * mm});
            skLineSegment(sketch, "E4825", {"start": v(-16.21, 99.69) * mm, "end": v(-16.3, 99.84) * mm});
            skLineSegment(sketch, "E4826", {"start": v(-16.3, 99.84) * mm, "end": v(-16.4, 99.99) * mm});
            skLineSegment(sketch, "E4827", {"start": v(-16.4, 99.99) * mm, "end": v(-16.5, 100.14) * mm});
            skLineSegment(sketch, "E4828", {"start": v(-16.5, 100.14) * mm, "end": v(-16.6, 100.29) * mm});
            skLineSegment(sketch, "E4829", {"start": v(-16.6, 100.29) * mm, "end": v(-16.7, 100.44) * mm});
            skLineSegment(sketch, "E4830", {"start": v(-16.7, 100.44) * mm, "end": v(-16.8, 100.6) * mm});
            skLineSegment(sketch, "E4831", {"start": v(-16.8, 100.6) * mm, "end": v(-16.91, 100.75) * mm});
            skLineSegment(sketch, "E4832", {"start": v(-16.91, 100.75) * mm, "end": v(-17.02, 100.9) * mm});
            skLineSegment(sketch, "E4833", {"start": v(-17.02, 100.9) * mm, "end": v(-17.13, 101.06) * mm});
            skLineSegment(sketch, "E4834", {"start": v(-17.13, 101.06) * mm, "end": v(-17.2, 101.05) * mm});
            skLineSegment(sketch, "E4835", {"start": v(-17.2, 101.05) * mm, "end": v(-18.76, 100.77) * mm});
            skLineSegment(sketch, "E4836", {"start": v(-18.76, 100.77) * mm, "end": v(-18.84, 100.75) * mm});
            skLineSegment(sketch, "E4837", {"start": v(-18.84, 100.75) * mm, "end": v(-18.88, 100.57) * mm});
            skLineSegment(sketch, "E4838", {"start": v(-18.88, 100.57) * mm, "end": v(-18.93, 100.39) * mm});
            skLineSegment(sketch, "E4839", {"start": v(-18.93, 100.39) * mm, "end": v(-18.97, 100.2) * mm});
            skLineSegment(sketch, "E4840", {"start": v(-18.97, 100.2) * mm, "end": v(-19.02, 100.03) * mm});
            skLineSegment(sketch, "E4841", {"start": v(-19.02, 100.03) * mm, "end": v(-19.06, 99.85) * mm});
            skLineSegment(sketch, "E4842", {"start": v(-19.06, 99.85) * mm, "end": v(-19.1, 99.67) * mm});
            skLineSegment(sketch, "E4843", {"start": v(-19.1, 99.67) * mm, "end": v(-19.14, 99.5) * mm});
            skLineSegment(sketch, "E4844", {"start": v(-19.14, 99.5) * mm, "end": v(-19.18, 99.32) * mm});
            skLineSegment(sketch, "E4845", {"start": v(-19.18, 99.32) * mm, "end": v(-19.22, 99.15) * mm});
            skLineSegment(sketch, "E4846", {"start": v(-19.22, 99.15) * mm, "end": v(-19.26, 98.98) * mm});
            skLineSegment(sketch, "E4847", {"start": v(-19.26, 98.98) * mm, "end": v(-19.3, 98.82) * mm});
            skLineSegment(sketch, "E4848", {"start": v(-19.3, 98.82) * mm, "end": v(-19.33, 98.65) * mm});
            skLineSegment(sketch, "E4849", {"start": v(-19.33, 98.65) * mm, "end": v(-19.36, 98.48) * mm});
            skLineSegment(sketch, "E4850", {"start": v(-19.36, 98.48) * mm, "end": v(-19.4, 98.32) * mm});
            skLineSegment(sketch, "E4851", {"start": v(-19.4, 98.32) * mm, "end": v(-19.43, 98.16) * mm});
            skLineSegment(sketch, "E4852", {"start": v(-19.43, 98.16) * mm, "end": v(-19.46, 98) * mm});
            skLineSegment(sketch, "E4853", {"start": v(-19.46, 98) * mm, "end": v(-19.49, 97.84) * mm});
            skLineSegment(sketch, "E4854", {"start": v(-19.49, 97.84) * mm, "end": v(-19.51, 97.68) * mm});
            skLineSegment(sketch, "E4855", {"start": v(-19.51, 97.68) * mm, "end": v(-19.54, 97.53) * mm});
            skLineSegment(sketch, "E4856", {"start": v(-19.54, 97.53) * mm, "end": v(-19.57, 97.37) * mm});
            skLineSegment(sketch, "E4857", {"start": v(-19.57, 97.37) * mm, "end": v(-19.6, 97.22) * mm});
            skLineSegment(sketch, "E4858", {"start": v(-19.6, 97.22) * mm, "end": v(-19.62, 97.07) * mm});
            skLineSegment(sketch, "E4859", {"start": v(-19.62, 97.07) * mm, "end": v(-19.64, 96.92) * mm});
            skLineSegment(sketch, "E4860", {"start": v(-19.64, 96.92) * mm, "end": v(-19.66, 96.77) * mm});
            skLineSegment(sketch, "E4861", {"start": v(-19.66, 96.77) * mm, "end": v(-19.69, 96.63) * mm});
            skLineSegment(sketch, "E4862", {"start": v(-19.69, 96.63) * mm, "end": v(-19.7, 96.48) * mm});
            skLineSegment(sketch, "E4863", {"start": v(-19.7, 96.48) * mm, "end": v(-19.73, 96.34) * mm});
            skLineSegment(sketch, "E4864", {"start": v(-19.73, 96.34) * mm, "end": v(-19.75, 96.2) * mm});
            skLineSegment(sketch, "E4865", {"start": v(-19.75, 96.2) * mm, "end": v(-19.76, 96.06) * mm});
            skLineSegment(sketch, "E4866", {"start": v(-19.76, 96.06) * mm, "end": v(-19.78, 95.92) * mm});
            skLineSegment(sketch, "E4867", {"start": v(-19.78, 95.92) * mm, "end": v(-19.8, 95.79) * mm});
            skLineSegment(sketch, "E4868", {"start": v(-19.8, 95.79) * mm, "end": v(-19.81, 95.65) * mm});
            skLineSegment(sketch, "E4869", {"start": v(-19.81, 95.65) * mm, "end": v(-19.83, 95.52) * mm});
            skLineSegment(sketch, "E4870", {"start": v(-19.83, 95.52) * mm, "end": v(-19.84, 95.39) * mm});
            skLineSegment(sketch, "E4871", {"start": v(-19.84, 95.39) * mm, "end": v(-19.86, 95.26) * mm});
            skLineSegment(sketch, "E4872", {"start": v(-19.86, 95.26) * mm, "end": v(-19.87, 95.13) * mm});
            skLineSegment(sketch, "E4873", {"start": v(-19.87, 95.13) * mm, "end": v(-20.78, 94.88) * mm});
            skLineSegment(sketch, "E4874", {"start": v(-20.78, 94.88) * mm, "end": v(-21.71, 94.73) * mm});
            skLineSegment(sketch, "E4875", {"start": v(-21.71, 94.73) * mm, "end": v(-21.78, 94.84) * mm});
            skLineSegment(sketch, "E4876", {"start": v(-21.78, 94.84) * mm, "end": v(-21.85, 94.95) * mm});
            skLineSegment(sketch, "E4877", {"start": v(-21.85, 94.95) * mm, "end": v(-21.91, 95.06) * mm});
            skLineSegment(sketch, "E4878", {"start": v(-21.91, 95.06) * mm, "end": v(-21.98, 95.18) * mm});
            skLineSegment(sketch, "E4879", {"start": v(-21.98, 95.18) * mm, "end": v(-22.05, 95.3) * mm});
            skLineSegment(sketch, "E4880", {"start": v(-22.05, 95.3) * mm, "end": v(-22.12, 95.4) * mm});
            skLineSegment(sketch, "E4881", {"start": v(-22.12, 95.4) * mm, "end": v(-22.2, 95.53) * mm});
            skLineSegment(sketch, "E4882", {"start": v(-22.2, 95.53) * mm, "end": v(-22.27, 95.65) * mm});
            skLineSegment(sketch, "E4883", {"start": v(-22.27, 95.65) * mm, "end": v(-22.35, 95.77) * mm});
            skLineSegment(sketch, "E4884", {"start": v(-22.35, 95.77) * mm, "end": v(-22.43, 95.89) * mm});
            skLineSegment(sketch, "E4885", {"start": v(-22.43, 95.89) * mm, "end": v(-22.5, 96) * mm});
            skLineSegment(sketch, "E4886", {"start": v(-22.5, 96) * mm, "end": v(-22.59, 96.13) * mm});
            skLineSegment(sketch, "E4887", {"start": v(-22.59, 96.13) * mm, "end": v(-22.67, 96.26) * mm});
            skLineSegment(sketch, "E4888", {"start": v(-22.67, 96.26) * mm, "end": v(-22.75, 96.38) * mm});
            skLineSegment(sketch, "E4889", {"start": v(-22.75, 96.38) * mm, "end": v(-22.84, 96.5) * mm});
            skLineSegment(sketch, "E4890", {"start": v(-22.84, 96.5) * mm, "end": v(-22.92, 96.64) * mm});
            skLineSegment(sketch, "E4891", {"start": v(-22.92, 96.64) * mm, "end": v(-23.01, 96.77) * mm});
            skLineSegment(sketch, "E4892", {"start": v(-23.01, 96.77) * mm, "end": v(-23.1, 96.9) * mm});
            skLineSegment(sketch, "E4893", {"start": v(-23.1, 96.9) * mm, "end": v(-23.2, 97.03) * mm});
            skLineSegment(sketch, "E4894", {"start": v(-23.2, 97.03) * mm, "end": v(-23.29, 97.16) * mm});
            skLineSegment(sketch, "E4895", {"start": v(-23.29, 97.16) * mm, "end": v(-23.38, 97.3) * mm});
            skLineSegment(sketch, "E4896", {"start": v(-23.38, 97.3) * mm, "end": v(-23.48, 97.42) * mm});
            skLineSegment(sketch, "E4897", {"start": v(-23.48, 97.42) * mm, "end": v(-23.58, 97.56) * mm});
            skLineSegment(sketch, "E4898", {"start": v(-23.58, 97.56) * mm, "end": v(-23.68, 97.7) * mm});
            skLineSegment(sketch, "E4899", {"start": v(-23.68, 97.7) * mm, "end": v(-23.78, 97.83) * mm});
            skLineSegment(sketch, "E4900", {"start": v(-23.78, 97.83) * mm, "end": v(-23.88, 97.97) * mm});
            skLineSegment(sketch, "E4901", {"start": v(-23.88, 97.97) * mm, "end": v(-23.99, 98.1) * mm});
            skLineSegment(sketch, "E4902", {"start": v(-23.99, 98.1) * mm, "end": v(-24.1, 98.25) * mm});
            skLineSegment(sketch, "E4903", {"start": v(-24.1, 98.25) * mm, "end": v(-24.2, 98.4) * mm});
            skLineSegment(sketch, "E4904", {"start": v(-24.2, 98.4) * mm, "end": v(-24.3, 98.53) * mm});
            skLineSegment(sketch, "E4905", {"start": v(-24.3, 98.53) * mm, "end": v(-24.42, 98.67) * mm});
            skLineSegment(sketch, "E4906", {"start": v(-24.42, 98.67) * mm, "end": v(-24.53, 98.82) * mm});
            skLineSegment(sketch, "E4907", {"start": v(-24.53, 98.82) * mm, "end": v(-24.65, 98.96) * mm});
            skLineSegment(sketch, "E4908", {"start": v(-24.65, 98.96) * mm, "end": v(-24.77, 99.1) * mm});
            skLineSegment(sketch, "E4909", {"start": v(-24.77, 99.1) * mm, "end": v(-24.88, 99.25) * mm});
            skLineSegment(sketch, "E4910", {"start": v(-24.88, 99.25) * mm, "end": v(-25, 99.4) * mm});
            skLineSegment(sketch, "E4911", {"start": v(-25, 99.4) * mm, "end": v(-25.08, 99.38) * mm});
            skLineSegment(sketch, "E4912", {"start": v(-25.08, 99.38) * mm, "end": v(-26.6, 98.99) * mm});
            skLineSegment(sketch, "E4913", {"start": v(-26.6, 98.99) * mm, "end": v(-26.68, 98.96) * mm});
            skLineSegment(sketch, "E4914", {"start": v(-26.68, 98.96) * mm, "end": v(-26.72, 98.78) * mm});
            skLineSegment(sketch, "E4915", {"start": v(-26.72, 98.78) * mm, "end": v(-26.75, 98.6) * mm});
            skLineSegment(sketch, "E4916", {"start": v(-26.75, 98.6) * mm, "end": v(-26.78, 98.4) * mm});
            skLineSegment(sketch, "E4917", {"start": v(-26.78, 98.4) * mm, "end": v(-26.8, 98.23) * mm});
            skLineSegment(sketch, "E4918", {"start": v(-26.8, 98.23) * mm, "end": v(-26.84, 98.05) * mm});
            skLineSegment(sketch, "E4919", {"start": v(-26.84, 98.05) * mm, "end": v(-26.86, 97.87) * mm});
            skLineSegment(sketch, "E4920", {"start": v(-26.86, 97.87) * mm, "end": v(-26.9, 97.69) * mm});
            skLineSegment(sketch, "E4921", {"start": v(-26.9, 97.69) * mm, "end": v(-26.92, 97.51) * mm});
            skLineSegment(sketch, "E4922", {"start": v(-26.92, 97.51) * mm, "end": v(-26.94, 97.34) * mm});
            skLineSegment(sketch, "E4923", {"start": v(-26.94, 97.34) * mm, "end": v(-26.96, 97.17) * mm});
            skLineSegment(sketch, "E4924", {"start": v(-26.96, 97.17) * mm, "end": v(-26.99, 97) * mm});
            skLineSegment(sketch, "E4925", {"start": v(-26.99, 97) * mm, "end": v(-27, 96.83) * mm});
            skLineSegment(sketch, "E4926", {"start": v(-27, 96.83) * mm, "end": v(-27.03, 96.66) * mm});
            skLineSegment(sketch, "E4927", {"start": v(-27.03, 96.66) * mm, "end": v(-27.05, 96.5) * mm});
            skLineSegment(sketch, "E4928", {"start": v(-27.05, 96.5) * mm, "end": v(-27.07, 96.33) * mm});
            skLineSegment(sketch, "E4929", {"start": v(-27.07, 96.33) * mm, "end": v(-27.08, 96.17) * mm});
            skLineSegment(sketch, "E4930", {"start": v(-27.08, 96.17) * mm, "end": v(-27.1, 96) * mm});
            skLineSegment(sketch, "E4931", {"start": v(-27.1, 96) * mm, "end": v(-27.12, 95.85) * mm});
            skLineSegment(sketch, "E4932", {"start": v(-27.12, 95.85) * mm, "end": v(-27.13, 95.7) * mm});
            skLineSegment(sketch, "E4933", {"start": v(-27.13, 95.7) * mm, "end": v(-27.15, 95.54) * mm});
            skLineSegment(sketch, "E4934", {"start": v(-27.15, 95.54) * mm, "end": v(-27.16, 95.38) * mm});
            skLineSegment(sketch, "E4935", {"start": v(-27.16, 95.38) * mm, "end": v(-27.17, 95.23) * mm});
            skLineSegment(sketch, "E4936", {"start": v(-27.17, 95.23) * mm, "end": v(-27.19, 95.08) * mm});
            skLineSegment(sketch, "E4937", {"start": v(-27.19, 95.08) * mm, "end": v(-27.2, 94.93) * mm});
            skLineSegment(sketch, "E4938", {"start": v(-27.2, 94.93) * mm, "end": v(-27.2, 94.78) * mm});
            skLineSegment(sketch, "E4939", {"start": v(-27.2, 94.78) * mm, "end": v(-27.22, 94.64) * mm});
            skLineSegment(sketch, "E4940", {"start": v(-27.22, 94.64) * mm, "end": v(-27.23, 94.5) * mm});
            skLineSegment(sketch, "E4941", {"start": v(-27.23, 94.5) * mm, "end": v(-27.23, 94.35) * mm});
            skLineSegment(sketch, "E4942", {"start": v(-27.23, 94.35) * mm, "end": v(-27.24, 94.21) * mm});
            skLineSegment(sketch, "E4943", {"start": v(-27.24, 94.21) * mm, "end": v(-27.25, 94.07) * mm});
            skLineSegment(sketch, "E4944", {"start": v(-27.25, 94.07) * mm, "end": v(-27.25, 93.94) * mm});
            skLineSegment(sketch, "E4945", {"start": v(-27.25, 93.94) * mm, "end": v(-27.26, 93.8) * mm});
            skLineSegment(sketch, "E4946", {"start": v(-27.26, 93.8) * mm, "end": v(-27.26, 93.67) * mm});
            skLineSegment(sketch, "E4947", {"start": v(-27.26, 93.67) * mm, "end": v(-27.27, 93.54) * mm});
            skLineSegment(sketch, "E4948", {"start": v(-27.27, 93.54) * mm, "end": v(-27.27, 93.4) * mm});
            skLineSegment(sketch, "E4949", {"start": v(-27.27, 93.4) * mm, "end": v(-27.27, 93.28) * mm});
            skLineSegment(sketch, "E4950", {"start": v(-27.27, 93.28) * mm, "end": v(-28.16, 92.95) * mm});
            skLineSegment(sketch, "E4951", {"start": v(-28.16, 92.95) * mm, "end": v(-29.08, 92.73) * mm});
            skLineSegment(sketch, "E4952", {"start": v(-29.08, 92.73) * mm, "end": v(-29.15, 92.84) * mm});
            skLineSegment(sketch, "E4953", {"start": v(-29.15, 92.84) * mm, "end": v(-29.23, 92.94) * mm});
            skLineSegment(sketch, "E4954", {"start": v(-29.23, 92.94) * mm, "end": v(-29.3, 93.05) * mm});
            skLineSegment(sketch, "E4955", {"start": v(-29.3, 93.05) * mm, "end": v(-29.38, 93.16) * mm});
            skLineSegment(sketch, "E4956", {"start": v(-29.38, 93.16) * mm, "end": v(-29.46, 93.27) * mm});
            skLineSegment(sketch, "E4957", {"start": v(-29.46, 93.27) * mm, "end": v(-29.54, 93.38) * mm});
            skLineSegment(sketch, "E4958", {"start": v(-29.54, 93.38) * mm, "end": v(-29.62, 93.5) * mm});
            skLineSegment(sketch, "E4959", {"start": v(-29.62, 93.5) * mm, "end": v(-29.7, 93.6) * mm});
            skLineSegment(sketch, "E4960", {"start": v(-29.7, 93.6) * mm, "end": v(-29.8, 93.72) * mm});
            skLineSegment(sketch, "E4961", {"start": v(-29.8, 93.72) * mm, "end": v(-29.88, 93.83) * mm});
            skLineSegment(sketch, "E4962", {"start": v(-29.88, 93.83) * mm, "end": v(-29.97, 93.95) * mm});
            skLineSegment(sketch, "E4963", {"start": v(-29.97, 93.95) * mm, "end": v(-30.06, 94.06) * mm});
            skLineSegment(sketch, "E4964", {"start": v(-30.06, 94.06) * mm, "end": v(-30.15, 94.18) * mm});
            skLineSegment(sketch, "E4965", {"start": v(-30.15, 94.18) * mm, "end": v(-30.24, 94.3) * mm});
            skLineSegment(sketch, "E4966", {"start": v(-30.24, 94.3) * mm, "end": v(-30.34, 94.42) * mm});
            skLineSegment(sketch, "E4967", {"start": v(-30.34, 94.42) * mm, "end": v(-30.44, 94.54) * mm});
            skLineSegment(sketch, "E4968", {"start": v(-30.44, 94.54) * mm, "end": v(-30.53, 94.66) * mm});
            skLineSegment(sketch, "E4969", {"start": v(-30.53, 94.66) * mm, "end": v(-30.63, 94.78) * mm});
            skLineSegment(sketch, "E4970", {"start": v(-30.63, 94.78) * mm, "end": v(-30.74, 94.9) * mm});
            skLineSegment(sketch, "E4971", {"start": v(-30.74, 94.9) * mm, "end": v(-30.84, 95.03) * mm});
            skLineSegment(sketch, "E4972", {"start": v(-30.84, 95.03) * mm, "end": v(-30.94, 95.16) * mm});
            skLineSegment(sketch, "E4973", {"start": v(-30.94, 95.16) * mm, "end": v(-31.05, 95.28) * mm});
            skLineSegment(sketch, "E4974", {"start": v(-31.05, 95.28) * mm, "end": v(-31.16, 95.4) * mm});
            skLineSegment(sketch, "E4975", {"start": v(-31.16, 95.4) * mm, "end": v(-31.27, 95.54) * mm});
            skLineSegment(sketch, "E4976", {"start": v(-31.27, 95.54) * mm, "end": v(-31.38, 95.67) * mm});
            skLineSegment(sketch, "E4977", {"start": v(-31.38, 95.67) * mm, "end": v(-31.5, 95.8) * mm});
            skLineSegment(sketch, "E4978", {"start": v(-31.5, 95.8) * mm, "end": v(-31.6, 95.93) * mm});
            skLineSegment(sketch, "E4979", {"start": v(-31.6, 95.93) * mm, "end": v(-31.73, 96.06) * mm});
            skLineSegment(sketch, "E4980", {"start": v(-31.73, 96.06) * mm, "end": v(-31.84, 96.19) * mm});
            skLineSegment(sketch, "E4981", {"start": v(-31.84, 96.19) * mm, "end": v(-31.97, 96.32) * mm});
            skLineSegment(sketch, "E4982", {"start": v(-31.97, 96.32) * mm, "end": v(-32.09, 96.45) * mm});
            skLineSegment(sketch, "E4983", {"start": v(-32.09, 96.45) * mm, "end": v(-32.21, 96.59) * mm});
            skLineSegment(sketch, "E4984", {"start": v(-32.21, 96.59) * mm, "end": v(-32.34, 96.72) * mm});
            skLineSegment(sketch, "E4985", {"start": v(-32.34, 96.72) * mm, "end": v(-32.46, 96.86) * mm});
            skLineSegment(sketch, "E4986", {"start": v(-32.46, 96.86) * mm, "end": v(-32.6, 97) * mm});
            skLineSegment(sketch, "E4987", {"start": v(-32.6, 97) * mm, "end": v(-32.73, 97.13) * mm});
            skLineSegment(sketch, "E4988", {"start": v(-32.73, 97.13) * mm, "end": v(-32.8, 97.1) * mm});
            skLineSegment(sketch, "E4989", {"start": v(-32.8, 97.1) * mm, "end": v(-34.29, 96.6) * mm});
            skLineSegment(sketch, "E4990", {"start": v(-34.29, 96.6) * mm, "end": v(-34.36, 96.57) * mm});
            skLineSegment(sketch, "E4991", {"start": v(-34.36, 96.57) * mm, "end": v(-34.38, 96.38) * mm});
            skLineSegment(sketch, "E4992", {"start": v(-34.38, 96.38) * mm, "end": v(-34.4, 96.19) * mm});
            skLineSegment(sketch, "E4993", {"start": v(-34.4, 96.19) * mm, "end": v(-34.42, 96) * mm});
            skLineSegment(sketch, "E4994", {"start": v(-34.42, 96) * mm, "end": v(-34.43, 95.82) * mm});
            skLineSegment(sketch, "E4995", {"start": v(-34.43, 95.82) * mm, "end": v(-34.45, 95.64) * mm});
            skLineSegment(sketch, "E4996", {"start": v(-34.45, 95.64) * mm, "end": v(-34.46, 95.46) * mm});
            skLineSegment(sketch, "E4997", {"start": v(-34.46, 95.46) * mm, "end": v(-34.47, 95.28) * mm});
            skLineSegment(sketch, "E4998", {"start": v(-34.47, 95.28) * mm, "end": v(-34.48, 95.1) * mm});
            skLineSegment(sketch, "E4999", {"start": v(-34.48, 95.1) * mm, "end": v(-34.5, 94.93) * mm});
            skLineSegment(sketch, "E5000", {"start": v(-34.5, 94.93) * mm, "end": v(-34.5, 94.75) * mm});
            skLineSegment(sketch, "E5001", {"start": v(-34.5, 94.75) * mm, "end": v(-34.51, 94.58) * mm});
            skLineSegment(sketch, "E5002", {"start": v(-34.51, 94.58) * mm, "end": v(-34.52, 94.41) * mm});
            skLineSegment(sketch, "E5003", {"start": v(-34.52, 94.41) * mm, "end": v(-34.53, 94.24) * mm});
            skLineSegment(sketch, "E5004", {"start": v(-34.53, 94.24) * mm, "end": v(-34.54, 94.08) * mm});
            skLineSegment(sketch, "E5005", {"start": v(-34.54, 94.08) * mm, "end": v(-34.54, 93.91) * mm});
            skLineSegment(sketch, "E5006", {"start": v(-34.54, 93.91) * mm, "end": v(-34.55, 93.75) * mm});
            skLineSegment(sketch, "E5007", {"start": v(-34.55, 93.75) * mm, "end": v(-34.55, 93.59) * mm});
            skLineSegment(sketch, "E5008", {"start": v(-34.55, 93.59) * mm, "end": v(-34.55, 93.43) * mm});
            skLineSegment(sketch, "E5009", {"start": v(-34.55, 93.43) * mm, "end": v(-34.56, 93.27) * mm});
            skLineSegment(sketch, "E5010", {"start": v(-34.56, 93.27) * mm, "end": v(-34.56, 93.11) * mm});
            skLineSegment(sketch, "E5011", {"start": v(-34.56, 93.11) * mm, "end": v(-34.56, 92.96) * mm});
            skLineSegment(sketch, "E5012", {"start": v(-34.56, 92.96) * mm, "end": v(-34.56, 92.8) * mm});
            skLineSegment(sketch, "E5013", {"start": v(-34.56, 92.8) * mm, "end": v(-34.56, 92.65) * mm});
            skLineSegment(sketch, "E5014", {"start": v(-34.56, 92.65) * mm, "end": v(-34.56, 92.5) * mm});
            skLineSegment(sketch, "E5015", {"start": v(-34.56, 92.5) * mm, "end": v(-34.56, 92.36) * mm});
            skLineSegment(sketch, "E5016", {"start": v(-34.56, 92.36) * mm, "end": v(-34.56, 92.21) * mm});
            skLineSegment(sketch, "E5017", {"start": v(-34.56, 92.21) * mm, "end": v(-34.56, 92.07) * mm});
            skLineSegment(sketch, "E5018", {"start": v(-34.56, 92.07) * mm, "end": v(-34.55, 91.93) * mm});
            skLineSegment(sketch, "E5019", {"start": v(-34.55, 91.93) * mm, "end": v(-34.55, 91.79) * mm});
            skLineSegment(sketch, "E5020", {"start": v(-34.55, 91.79) * mm, "end": v(-34.54, 91.65) * mm});
            skLineSegment(sketch, "E5021", {"start": v(-34.54, 91.65) * mm, "end": v(-34.54, 91.51) * mm});
            skLineSegment(sketch, "E5022", {"start": v(-34.54, 91.51) * mm, "end": v(-34.53, 91.38) * mm});
            skLineSegment(sketch, "E5023", {"start": v(-34.53, 91.38) * mm, "end": v(-34.53, 91.24) * mm});
            skLineSegment(sketch, "E5024", {"start": v(-34.53, 91.24) * mm, "end": v(-34.52, 91.11) * mm});
            skLineSegment(sketch, "E5025", {"start": v(-34.52, 91.11) * mm, "end": v(-34.52, 90.98) * mm});
            skLineSegment(sketch, "E5026", {"start": v(-34.52, 90.98) * mm, "end": v(-34.5, 90.85) * mm});
            skLineSegment(sketch, "E5027", {"start": v(-34.5, 90.85) * mm, "end": v(-35.37, 90.46) * mm});
            skLineSegment(sketch, "E5028", {"start": v(-35.37, 90.46) * mm, "end": v(-36.27, 90.17) * mm});
            skLineSegment(sketch, "E5029", {"start": v(-36.27, 90.17) * mm, "end": v(-36.35, 90.27) * mm});
            skLineSegment(sketch, "E5030", {"start": v(-36.35, 90.27) * mm, "end": v(-36.43, 90.36) * mm});
            skLineSegment(sketch, "E5031", {"start": v(-36.43, 90.36) * mm, "end": v(-36.51, 90.47) * mm});
            skLineSegment(sketch, "E5032", {"start": v(-36.51, 90.47) * mm, "end": v(-36.6, 90.57) * mm});
            skLineSegment(sketch, "E5033", {"start": v(-36.6, 90.57) * mm, "end": v(-36.69, 90.67) * mm});
            skLineSegment(sketch, "E5034", {"start": v(-36.69, 90.67) * mm, "end": v(-36.78, 90.77) * mm});
            skLineSegment(sketch, "E5035", {"start": v(-36.78, 90.77) * mm, "end": v(-36.87, 90.88) * mm});
            skLineSegment(sketch, "E5036", {"start": v(-36.87, 90.88) * mm, "end": v(-36.96, 90.98) * mm});
            skLineSegment(sketch, "E5037", {"start": v(-36.96, 90.98) * mm, "end": v(-37.05, 91.1) * mm});
            skLineSegment(sketch, "E5038", {"start": v(-37.05, 91.1) * mm, "end": v(-37.15, 91.2) * mm});
            skLineSegment(sketch, "E5039", {"start": v(-37.15, 91.2) * mm, "end": v(-37.25, 91.3) * mm});
            skLineSegment(sketch, "E5040", {"start": v(-37.25, 91.3) * mm, "end": v(-37.35, 91.42) * mm});
            skLineSegment(sketch, "E5041", {"start": v(-37.35, 91.42) * mm, "end": v(-37.45, 91.53) * mm});
            skLineSegment(sketch, "E5042", {"start": v(-37.45, 91.53) * mm, "end": v(-37.55, 91.64) * mm});
            skLineSegment(sketch, "E5043", {"start": v(-37.55, 91.64) * mm, "end": v(-37.65, 91.75) * mm});
            skLineSegment(sketch, "E5044", {"start": v(-37.65, 91.75) * mm, "end": v(-37.76, 91.86) * mm});
            skLineSegment(sketch, "E5045", {"start": v(-37.76, 91.86) * mm, "end": v(-37.87, 91.97) * mm});
            skLineSegment(sketch, "E5046", {"start": v(-37.87, 91.97) * mm, "end": v(-37.98, 92.09) * mm});
            skLineSegment(sketch, "E5047", {"start": v(-37.98, 92.09) * mm, "end": v(-38.09, 92.2) * mm});
            skLineSegment(sketch, "E5048", {"start": v(-38.09, 92.2) * mm, "end": v(-38.2, 92.32) * mm});
            skLineSegment(sketch, "E5049", {"start": v(-38.2, 92.32) * mm, "end": v(-38.31, 92.44) * mm});
            skLineSegment(sketch, "E5050", {"start": v(-38.31, 92.44) * mm, "end": v(-38.43, 92.55) * mm});
            skLineSegment(sketch, "E5051", {"start": v(-38.43, 92.55) * mm, "end": v(-38.55, 92.67) * mm});
            skLineSegment(sketch, "E5052", {"start": v(-38.55, 92.67) * mm, "end": v(-38.67, 92.79) * mm});
            skLineSegment(sketch, "E5053", {"start": v(-38.67, 92.79) * mm, "end": v(-38.79, 92.9) * mm});
            skLineSegment(sketch, "E5054", {"start": v(-38.79, 92.9) * mm, "end": v(-38.91, 93.03) * mm});
            skLineSegment(sketch, "E5055", {"start": v(-38.91, 93.03) * mm, "end": v(-39.04, 93.15) * mm});
            skLineSegment(sketch, "E5056", {"start": v(-39.04, 93.15) * mm, "end": v(-39.16, 93.27) * mm});
            skLineSegment(sketch, "E5057", {"start": v(-39.16, 93.27) * mm, "end": v(-39.3, 93.4) * mm});
            skLineSegment(sketch, "E5058", {"start": v(-39.3, 93.4) * mm, "end": v(-39.42, 93.52) * mm});
            skLineSegment(sketch, "E5059", {"start": v(-39.42, 93.52) * mm, "end": v(-39.56, 93.64) * mm});
            skLineSegment(sketch, "E5060", {"start": v(-39.56, 93.64) * mm, "end": v(-39.7, 93.76) * mm});
            skLineSegment(sketch, "E5061", {"start": v(-39.7, 93.76) * mm, "end": v(-39.83, 93.89) * mm});
            skLineSegment(sketch, "E5062", {"start": v(-39.83, 93.89) * mm, "end": v(-39.96, 94.01) * mm});
            skLineSegment(sketch, "E5063", {"start": v(-39.96, 94.01) * mm, "end": v(-40.1, 94.14) * mm});
            skLineSegment(sketch, "E5064", {"start": v(-40.1, 94.14) * mm, "end": v(-40.25, 94.27) * mm});
            skLineSegment(sketch, "E5065", {"start": v(-40.25, 94.27) * mm, "end": v(-40.32, 94.24) * mm});
            skLineSegment(sketch, "E5066", {"start": v(-40.32, 94.24) * mm, "end": v(-41.76, 93.6) * mm});
            skLineSegment(sketch, "E5067", {"start": v(-41.76, 93.6) * mm, "end": v(-41.83, 93.57) * mm});
            skLineSegment(sketch, "E5068", {"start": v(-41.83, 93.57) * mm, "end": v(-41.84, 93.38) * mm});
            skLineSegment(sketch, "E5069", {"start": v(-41.84, 93.38) * mm, "end": v(-41.84, 93.2) * mm});
            skLineSegment(sketch, "E5070", {"start": v(-41.84, 93.2) * mm, "end": v(-41.84, 93) * mm});
            skLineSegment(sketch, "E5071", {"start": v(-41.84, 93) * mm, "end": v(-41.84, 92.82) * mm});
            skLineSegment(sketch, "E5072", {"start": v(-41.84, 92.82) * mm, "end": v(-41.84, 92.64) * mm});
            skLineSegment(sketch, "E5073", {"start": v(-41.84, 92.64) * mm, "end": v(-41.84, 92.46) * mm});
            skLineSegment(sketch, "E5074", {"start": v(-41.84, 92.46) * mm, "end": v(-41.84, 92.28) * mm});
            skLineSegment(sketch, "E5075", {"start": v(-41.84, 92.28) * mm, "end": v(-41.84, 92.1) * mm});
            skLineSegment(sketch, "E5076", {"start": v(-41.84, 92.1) * mm, "end": v(-41.84, 91.93) * mm});
            skLineSegment(sketch, "E5077", {"start": v(-41.84, 91.93) * mm, "end": v(-41.83, 91.75) * mm});
            skLineSegment(sketch, "E5078", {"start": v(-41.83, 91.75) * mm, "end": v(-41.83, 91.58) * mm});
            skLineSegment(sketch, "E5079", {"start": v(-41.83, 91.58) * mm, "end": v(-41.82, 91.41) * mm});
            skLineSegment(sketch, "E5080", {"start": v(-41.82, 91.41) * mm, "end": v(-41.82, 91.24) * mm});
            skLineSegment(sketch, "E5081", {"start": v(-41.82, 91.24) * mm, "end": v(-41.81, 91.08) * mm});
            skLineSegment(sketch, "E5082", {"start": v(-41.81, 91.08) * mm, "end": v(-41.8, 90.91) * mm});
            skLineSegment(sketch, "E5083", {"start": v(-41.8, 90.91) * mm, "end": v(-41.8, 90.75) * mm});
            skLineSegment(sketch, "E5084", {"start": v(-41.8, 90.75) * mm, "end": v(-41.79, 90.59) * mm});
            skLineSegment(sketch, "E5085", {"start": v(-41.79, 90.59) * mm, "end": v(-41.78, 90.43) * mm});
            skLineSegment(sketch, "E5086", {"start": v(-41.78, 90.43) * mm, "end": v(-41.77, 90.27) * mm});
            skLineSegment(sketch, "E5087", {"start": v(-41.77, 90.27) * mm, "end": v(-41.76, 90.11) * mm});
            skLineSegment(sketch, "E5088", {"start": v(-41.76, 90.11) * mm, "end": v(-41.75, 89.96) * mm});
            skLineSegment(sketch, "E5089", {"start": v(-41.75, 89.96) * mm, "end": v(-41.74, 89.8) * mm});
            skLineSegment(sketch, "E5090", {"start": v(-41.74, 89.8) * mm, "end": v(-41.72, 89.66) * mm});
            skLineSegment(sketch, "E5091", {"start": v(-41.72, 89.66) * mm, "end": v(-41.71, 89.5) * mm});
            skLineSegment(sketch, "E5092", {"start": v(-41.71, 89.5) * mm, "end": v(-41.7, 89.36) * mm});
            skLineSegment(sketch, "E5093", {"start": v(-41.7, 89.36) * mm, "end": v(-41.69, 89.22) * mm});
            skLineSegment(sketch, "E5094", {"start": v(-41.69, 89.22) * mm, "end": v(-41.67, 89.07) * mm});
            skLineSegment(sketch, "E5095", {"start": v(-41.67, 89.07) * mm, "end": v(-41.66, 88.93) * mm});
            skLineSegment(sketch, "E5096", {"start": v(-41.66, 88.93) * mm, "end": v(-41.64, 88.8) * mm});
            skLineSegment(sketch, "E5097", {"start": v(-41.64, 88.8) * mm, "end": v(-41.63, 88.65) * mm});
            skLineSegment(sketch, "E5098", {"start": v(-41.63, 88.65) * mm, "end": v(-41.61, 88.52) * mm});
            skLineSegment(sketch, "E5099", {"start": v(-41.61, 88.52) * mm, "end": v(-41.6, 88.38) * mm});
            skLineSegment(sketch, "E5100", {"start": v(-41.6, 88.38) * mm, "end": v(-41.58, 88.25) * mm});
            skLineSegment(sketch, "E5101", {"start": v(-41.58, 88.25) * mm, "end": v(-41.56, 88.12) * mm});
            skLineSegment(sketch, "E5102", {"start": v(-41.56, 88.12) * mm, "end": v(-41.55, 88) * mm});
            skLineSegment(sketch, "E5103", {"start": v(-41.55, 88) * mm, "end": v(-41.53, 87.87) * mm});
            skLineSegment(sketch, "E5104", {"start": v(-41.53, 87.87) * mm, "end": v(-42.35, 87.4) * mm});
            skLineSegment(sketch, "E5105", {"start": v(-42.35, 87.4) * mm, "end": v(-43.23, 87.04) * mm});
            skLineSegment(sketch, "E5106", {"start": v(-43.23, 87.04) * mm, "end": v(-43.32, 87.14) * mm});
            skLineSegment(sketch, "E5107", {"start": v(-43.32, 87.14) * mm, "end": v(-43.4, 87.23) * mm});
            skLineSegment(sketch, "E5108", {"start": v(-43.4, 87.23) * mm, "end": v(-43.5, 87.32) * mm});
            skLineSegment(sketch, "E5109", {"start": v(-43.5, 87.32) * mm, "end": v(-43.6, 87.42) * mm});
            skLineSegment(sketch, "E5110", {"start": v(-43.6, 87.42) * mm, "end": v(-43.69, 87.51) * mm});
            skLineSegment(sketch, "E5111", {"start": v(-43.69, 87.51) * mm, "end": v(-43.79, 87.6) * mm});
            skLineSegment(sketch, "E5112", {"start": v(-43.79, 87.6) * mm, "end": v(-43.88, 87.7) * mm});
            skLineSegment(sketch, "E5113", {"start": v(-43.88, 87.7) * mm, "end": v(-43.99, 87.8) * mm});
            skLineSegment(sketch, "E5114", {"start": v(-43.99, 87.8) * mm, "end": v(-44.09, 87.9) * mm});
            skLineSegment(sketch, "E5115", {"start": v(-44.09, 87.9) * mm, "end": v(-44.2, 88) * mm});
            skLineSegment(sketch, "E5116", {"start": v(-44.2, 88) * mm, "end": v(-44.3, 88.1) * mm});
            skLineSegment(sketch, "E5117", {"start": v(-44.3, 88.1) * mm, "end": v(-44.4, 88.2) * mm});
            skLineSegment(sketch, "E5118", {"start": v(-44.4, 88.2) * mm, "end": v(-44.51, 88.3) * mm});
            skLineSegment(sketch, "E5119", {"start": v(-44.51, 88.3) * mm, "end": v(-44.62, 88.4) * mm});
            skLineSegment(sketch, "E5120", {"start": v(-44.62, 88.4) * mm, "end": v(-44.74, 88.51) * mm});
            skLineSegment(sketch, "E5121", {"start": v(-44.74, 88.51) * mm, "end": v(-44.85, 88.61) * mm});
            skLineSegment(sketch, "E5122", {"start": v(-44.85, 88.61) * mm, "end": v(-44.97, 88.72) * mm});
            skLineSegment(sketch, "E5123", {"start": v(-44.97, 88.72) * mm, "end": v(-45.08, 88.82) * mm});
            skLineSegment(sketch, "E5124", {"start": v(-45.08, 88.82) * mm, "end": v(-45.2, 88.93) * mm});
            skLineSegment(sketch, "E5125", {"start": v(-45.2, 88.93) * mm, "end": v(-45.33, 89.04) * mm});
            skLineSegment(sketch, "E5126", {"start": v(-45.33, 89.04) * mm, "end": v(-45.45, 89.14) * mm});
            skLineSegment(sketch, "E5127", {"start": v(-45.45, 89.14) * mm, "end": v(-45.57, 89.25) * mm});
            skLineSegment(sketch, "E5128", {"start": v(-45.57, 89.25) * mm, "end": v(-45.7, 89.36) * mm});
            skLineSegment(sketch, "E5129", {"start": v(-45.7, 89.36) * mm, "end": v(-45.83, 89.47) * mm});
            skLineSegment(sketch, "E5130", {"start": v(-45.83, 89.47) * mm, "end": v(-45.96, 89.58) * mm});
            skLineSegment(sketch, "E5131", {"start": v(-45.96, 89.58) * mm, "end": v(-46.1, 89.69) * mm});
            skLineSegment(sketch, "E5132", {"start": v(-46.1, 89.69) * mm, "end": v(-46.23, 89.8) * mm});
            skLineSegment(sketch, "E5133", {"start": v(-46.23, 89.8) * mm, "end": v(-46.36, 89.91) * mm});
            skLineSegment(sketch, "E5134", {"start": v(-46.36, 89.91) * mm, "end": v(-46.5, 90.02) * mm});
            skLineSegment(sketch, "E5135", {"start": v(-46.5, 90.02) * mm, "end": v(-46.64, 90.13) * mm});
            skLineSegment(sketch, "E5136", {"start": v(-46.64, 90.13) * mm, "end": v(-46.78, 90.25) * mm});
            skLineSegment(sketch, "E5137", {"start": v(-46.78, 90.25) * mm, "end": v(-46.92, 90.36) * mm});
            skLineSegment(sketch, "E5138", {"start": v(-46.92, 90.36) * mm, "end": v(-47.07, 90.47) * mm});
            skLineSegment(sketch, "E5139", {"start": v(-47.07, 90.47) * mm, "end": v(-47.22, 90.59) * mm});
            skLineSegment(sketch, "E5140", {"start": v(-47.22, 90.59) * mm, "end": v(-47.37, 90.7) * mm});
            skLineSegment(sketch, "E5141", {"start": v(-47.37, 90.7) * mm, "end": v(-47.52, 90.82) * mm});
            skLineSegment(sketch, "E5142", {"start": v(-47.52, 90.82) * mm, "end": v(-47.6, 90.78) * mm});
            skLineSegment(sketch, "E5143", {"start": v(-47.6, 90.78) * mm, "end": v(-48.98, 90.04) * mm});
            skLineSegment(sketch, "E5144", {"start": v(-48.98, 90.04) * mm, "end": v(-49.05, 90) * mm});
            skLineSegment(sketch, "E5145", {"start": v(-49.05, 90) * mm, "end": v(-49.04, 89.81) * mm});
            skLineSegment(sketch, "E5146", {"start": v(-49.04, 89.81) * mm, "end": v(-49.02, 89.62) * mm});
            skLineSegment(sketch, "E5147", {"start": v(-49.02, 89.62) * mm, "end": v(-49.01, 89.44) * mm});
            skLineSegment(sketch, "E5148", {"start": v(-49.01, 89.44) * mm, "end": v(-49, 89.25) * mm});
            skLineSegment(sketch, "E5149", {"start": v(-49, 89.25) * mm, "end": v(-48.98, 89.07) * mm});
            skLineSegment(sketch, "E5150", {"start": v(-48.98, 89.07) * mm, "end": v(-48.97, 88.9) * mm});
            skLineSegment(sketch, "E5151", {"start": v(-48.97, 88.9) * mm, "end": v(-48.95, 88.71) * mm});
            skLineSegment(sketch, "E5152", {"start": v(-48.95, 88.71) * mm, "end": v(-48.94, 88.54) * mm});
            skLineSegment(sketch, "E5153", {"start": v(-48.94, 88.54) * mm, "end": v(-48.92, 88.36) * mm});
            skLineSegment(sketch, "E5154", {"start": v(-48.92, 88.36) * mm, "end": v(-48.9, 88.19) * mm});
            skLineSegment(sketch, "E5155", {"start": v(-48.9, 88.19) * mm, "end": v(-48.88, 88.02) * mm});
            skLineSegment(sketch, "E5156", {"start": v(-48.88, 88.02) * mm, "end": v(-48.87, 87.85) * mm});
            skLineSegment(sketch, "E5157", {"start": v(-48.87, 87.85) * mm, "end": v(-48.85, 87.68) * mm});
            skLineSegment(sketch, "E5158", {"start": v(-48.85, 87.68) * mm, "end": v(-48.83, 87.51) * mm});
            skLineSegment(sketch, "E5159", {"start": v(-48.83, 87.51) * mm, "end": v(-48.8, 87.35) * mm});
            skLineSegment(sketch, "E5160", {"start": v(-48.8, 87.35) * mm, "end": v(-48.79, 87.19) * mm});
            skLineSegment(sketch, "E5161", {"start": v(-48.79, 87.19) * mm, "end": v(-48.77, 87.03) * mm});
            skLineSegment(sketch, "E5162", {"start": v(-48.77, 87.03) * mm, "end": v(-48.74, 86.87) * mm});
            skLineSegment(sketch, "E5163", {"start": v(-48.74, 86.87) * mm, "end": v(-48.72, 86.71) * mm});
            skLineSegment(sketch, "E5164", {"start": v(-48.72, 86.71) * mm, "end": v(-48.7, 86.56) * mm});
            skLineSegment(sketch, "E5165", {"start": v(-48.7, 86.56) * mm, "end": v(-48.68, 86.4) * mm});
            skLineSegment(sketch, "E5166", {"start": v(-48.68, 86.4) * mm, "end": v(-48.65, 86.26) * mm});
            skLineSegment(sketch, "E5167", {"start": v(-48.65, 86.26) * mm, "end": v(-48.63, 86.1) * mm});
            skLineSegment(sketch, "E5168", {"start": v(-48.63, 86.1) * mm, "end": v(-48.6, 85.96) * mm});
            skLineSegment(sketch, "E5169", {"start": v(-48.6, 85.96) * mm, "end": v(-48.58, 85.81) * mm});
            skLineSegment(sketch, "E5170", {"start": v(-48.58, 85.81) * mm, "end": v(-48.56, 85.67) * mm});
            skLineSegment(sketch, "E5171", {"start": v(-48.56, 85.67) * mm, "end": v(-48.53, 85.53) * mm});
            skLineSegment(sketch, "E5172", {"start": v(-48.53, 85.53) * mm, "end": v(-48.5, 85.39) * mm});
            skLineSegment(sketch, "E5173", {"start": v(-48.5, 85.39) * mm, "end": v(-48.48, 85.25) * mm});
            skLineSegment(sketch, "E5174", {"start": v(-48.48, 85.25) * mm, "end": v(-48.46, 85.11) * mm});
            skLineSegment(sketch, "E5175", {"start": v(-48.46, 85.11) * mm, "end": v(-48.43, 84.98) * mm});
            skLineSegment(sketch, "E5176", {"start": v(-48.43, 84.98) * mm, "end": v(-48.4, 84.85) * mm});
            skLineSegment(sketch, "E5177", {"start": v(-48.4, 84.85) * mm, "end": v(-48.38, 84.72) * mm});
            skLineSegment(sketch, "E5178", {"start": v(-48.38, 84.72) * mm, "end": v(-48.35, 84.59) * mm});
            skLineSegment(sketch, "E5179", {"start": v(-48.35, 84.59) * mm, "end": v(-48.32, 84.46) * mm});
            skLineSegment(sketch, "E5180", {"start": v(-48.32, 84.46) * mm, "end": v(-48.3, 84.34) * mm});
            skLineSegment(sketch, "E5181", {"start": v(-48.3, 84.34) * mm, "end": v(-49.08, 83.81) * mm});
            skLineSegment(sketch, "E5182", {"start": v(-49.08, 83.81) * mm, "end": v(-49.92, 83.38) * mm});
            skLineSegment(sketch, "E5183", {"start": v(-49.92, 83.38) * mm, "end": v(-50.02, 83.47) * mm});
            skLineSegment(sketch, "E5184", {"start": v(-50.02, 83.47) * mm, "end": v(-50.12, 83.55) * mm});
            skLineSegment(sketch, "E5185", {"start": v(-50.12, 83.55) * mm, "end": v(-50.22, 83.64) * mm});
            skLineSegment(sketch, "E5186", {"start": v(-50.22, 83.64) * mm, "end": v(-50.32, 83.73) * mm});
            skLineSegment(sketch, "E5187", {"start": v(-50.32, 83.73) * mm, "end": v(-50.42, 83.81) * mm});
            skLineSegment(sketch, "E5188", {"start": v(-50.42, 83.81) * mm, "end": v(-50.52, 83.9) * mm});
            skLineSegment(sketch, "E5189", {"start": v(-50.52, 83.9) * mm, "end": v(-50.63, 84) * mm});
            skLineSegment(sketch, "E5190", {"start": v(-50.63, 84) * mm, "end": v(-50.74, 84.08) * mm});
            skLineSegment(sketch, "E5191", {"start": v(-50.74, 84.08) * mm, "end": v(-50.85, 84.17) * mm});
            skLineSegment(sketch, "E5192", {"start": v(-50.85, 84.17) * mm, "end": v(-50.96, 84.26) * mm});
            skLineSegment(sketch, "E5193", {"start": v(-50.96, 84.26) * mm, "end": v(-51.07, 84.36) * mm});
            skLineSegment(sketch, "E5194", {"start": v(-51.07, 84.36) * mm, "end": v(-51.19, 84.45) * mm});
            skLineSegment(sketch, "E5195", {"start": v(-51.19, 84.45) * mm, "end": v(-51.3, 84.54) * mm});
            skLineSegment(sketch, "E5196", {"start": v(-51.3, 84.54) * mm, "end": v(-51.42, 84.63) * mm});
            skLineSegment(sketch, "E5197", {"start": v(-51.42, 84.63) * mm, "end": v(-51.54, 84.73) * mm});
            skLineSegment(sketch, "E5198", {"start": v(-51.54, 84.73) * mm, "end": v(-51.67, 84.82) * mm});
            skLineSegment(sketch, "E5199", {"start": v(-51.67, 84.82) * mm, "end": v(-51.79, 84.92) * mm});
            skLineSegment(sketch, "E5200", {"start": v(-51.79, 84.92) * mm, "end": v(-51.91, 85.01) * mm});
            skLineSegment(sketch, "E5201", {"start": v(-51.91, 85.01) * mm, "end": v(-52.04, 85.1) * mm});
            skLineSegment(sketch, "E5202", {"start": v(-52.04, 85.1) * mm, "end": v(-52.17, 85.2) * mm});
            skLineSegment(sketch, "E5203", {"start": v(-52.17, 85.2) * mm, "end": v(-52.3, 85.3) * mm});
            skLineSegment(sketch, "E5204", {"start": v(-52.3, 85.3) * mm, "end": v(-52.44, 85.4) * mm});
            skLineSegment(sketch, "E5205", {"start": v(-52.44, 85.4) * mm, "end": v(-52.57, 85.5) * mm});
            skLineSegment(sketch, "E5206", {"start": v(-52.57, 85.5) * mm, "end": v(-52.7, 85.6) * mm});
            skLineSegment(sketch, "E5207", {"start": v(-52.7, 85.6) * mm, "end": v(-52.85, 85.7) * mm});
            skLineSegment(sketch, "E5208", {"start": v(-52.85, 85.7) * mm, "end": v(-52.99, 85.8) * mm});
            skLineSegment(sketch, "E5209", {"start": v(-52.99, 85.8) * mm, "end": v(-53.13, 85.9) * mm});
            skLineSegment(sketch, "E5210", {"start": v(-53.13, 85.9) * mm, "end": v(-53.27, 86) * mm});
            skLineSegment(sketch, "E5211", {"start": v(-53.27, 86) * mm, "end": v(-53.42, 86.1) * mm});
            skLineSegment(sketch, "E5212", {"start": v(-53.42, 86.1) * mm, "end": v(-53.57, 86.2) * mm});
            skLineSegment(sketch, "E5213", {"start": v(-53.57, 86.2) * mm, "end": v(-53.72, 86.3) * mm});
            skLineSegment(sketch, "E5214", {"start": v(-53.72, 86.3) * mm, "end": v(-53.87, 86.4) * mm});
            skLineSegment(sketch, "E5215", {"start": v(-53.87, 86.4) * mm, "end": v(-54.02, 86.5) * mm});
            skLineSegment(sketch, "E5216", {"start": v(-54.02, 86.5) * mm, "end": v(-54.18, 86.6) * mm});
            skLineSegment(sketch, "E5217", {"start": v(-54.18, 86.6) * mm, "end": v(-54.34, 86.7) * mm});
            skLineSegment(sketch, "E5218", {"start": v(-54.34, 86.7) * mm, "end": v(-54.5, 86.8) * mm});
            skLineSegment(sketch, "E5219", {"start": v(-54.5, 86.8) * mm, "end": v(-54.57, 86.77) * mm});
            skLineSegment(sketch, "E5220", {"start": v(-54.57, 86.77) * mm, "end": v(-55.9, 85.92) * mm});
            skLineSegment(sketch, "E5221", {"start": v(-55.9, 85.92) * mm, "end": v(-55.96, 85.87) * mm});
            skLineSegment(sketch, "E5222", {"start": v(-55.96, 85.87) * mm, "end": v(-55.93, 85.69) * mm});
            skLineSegment(sketch, "E5223", {"start": v(-55.93, 85.69) * mm, "end": v(-55.9, 85.5) * mm});
            skLineSegment(sketch, "E5224", {"start": v(-55.9, 85.5) * mm, "end": v(-55.88, 85.32) * mm});
            skLineSegment(sketch, "E5225", {"start": v(-55.88, 85.32) * mm, "end": v(-55.85, 85.13) * mm});
            skLineSegment(sketch, "E5226", {"start": v(-55.85, 85.13) * mm, "end": v(-55.82, 84.95) * mm});
            skLineSegment(sketch, "E5227", {"start": v(-55.82, 84.95) * mm, "end": v(-55.8, 84.78) * mm});
            skLineSegment(sketch, "E5228", {"start": v(-55.8, 84.78) * mm, "end": v(-55.76, 84.6) * mm});
            skLineSegment(sketch, "E5229", {"start": v(-55.76, 84.6) * mm, "end": v(-55.73, 84.42) * mm});
            skLineSegment(sketch, "E5230", {"start": v(-55.73, 84.42) * mm, "end": v(-55.7, 84.25) * mm});
            skLineSegment(sketch, "E5231", {"start": v(-55.7, 84.25) * mm, "end": v(-55.67, 84.08) * mm});
            skLineSegment(sketch, "E5232", {"start": v(-55.67, 84.08) * mm, "end": v(-55.64, 83.91) * mm});
            skLineSegment(sketch, "E5233", {"start": v(-55.64, 83.91) * mm, "end": v(-55.6, 83.74) * mm});
            skLineSegment(sketch, "E5234", {"start": v(-55.6, 83.74) * mm, "end": v(-55.58, 83.58) * mm});
            skLineSegment(sketch, "E5235", {"start": v(-55.58, 83.58) * mm, "end": v(-55.54, 83.41) * mm});
            skLineSegment(sketch, "E5236", {"start": v(-55.54, 83.41) * mm, "end": v(-55.5, 83.25) * mm});
            skLineSegment(sketch, "E5237", {"start": v(-55.5, 83.25) * mm, "end": v(-55.48, 83.1) * mm});
            skLineSegment(sketch, "E5238", {"start": v(-55.48, 83.1) * mm, "end": v(-55.44, 82.93) * mm});
            skLineSegment(sketch, "E5239", {"start": v(-55.44, 82.93) * mm, "end": v(-55.4, 82.78) * mm});
            skLineSegment(sketch, "E5240", {"start": v(-55.4, 82.78) * mm, "end": v(-55.38, 82.62) * mm});
            skLineSegment(sketch, "E5241", {"start": v(-55.38, 82.62) * mm, "end": v(-55.34, 82.47) * mm});
            skLineSegment(sketch, "E5242", {"start": v(-55.34, 82.47) * mm, "end": v(-55.3, 82.32) * mm});
            skLineSegment(sketch, "E5243", {"start": v(-55.3, 82.32) * mm, "end": v(-55.27, 82.17) * mm});
            skLineSegment(sketch, "E5244", {"start": v(-55.27, 82.17) * mm, "end": v(-55.24, 82.03) * mm});
            skLineSegment(sketch, "E5245", {"start": v(-55.24, 82.03) * mm, "end": v(-55.2, 81.88) * mm});
            skLineSegment(sketch, "E5246", {"start": v(-55.2, 81.88) * mm, "end": v(-55.16, 81.74) * mm});
            skLineSegment(sketch, "E5247", {"start": v(-55.16, 81.74) * mm, "end": v(-55.13, 81.6) * mm});
            skLineSegment(sketch, "E5248", {"start": v(-55.13, 81.6) * mm, "end": v(-55.1, 81.46) * mm});
            skLineSegment(sketch, "E5249", {"start": v(-55.1, 81.46) * mm, "end": v(-55.06, 81.32) * mm});
            skLineSegment(sketch, "E5250", {"start": v(-55.06, 81.32) * mm, "end": v(-55.02, 81.18) * mm});
            skLineSegment(sketch, "E5251", {"start": v(-55.02, 81.18) * mm, "end": v(-54.98, 81.05) * mm});
            skLineSegment(sketch, "E5252", {"start": v(-54.98, 81.05) * mm, "end": v(-54.95, 80.92) * mm});
            skLineSegment(sketch, "E5253", {"start": v(-54.95, 80.92) * mm, "end": v(-54.91, 80.79) * mm});
            skLineSegment(sketch, "E5254", {"start": v(-54.91, 80.79) * mm, "end": v(-54.87, 80.66) * mm});
            skLineSegment(sketch, "E5255", {"start": v(-54.87, 80.66) * mm, "end": v(-54.84, 80.53) * mm});
            skLineSegment(sketch, "E5256", {"start": v(-54.84, 80.53) * mm, "end": v(-54.8, 80.4) * mm});
            skLineSegment(sketch, "E5257", {"start": v(-54.8, 80.4) * mm, "end": v(-54.76, 80.29) * mm});
            skLineSegment(sketch, "E5258", {"start": v(-54.76, 80.29) * mm, "end": v(-55.5, 79.7) * mm});
            skLineSegment(sketch, "E5259", {"start": v(-55.5, 79.7) * mm, "end": v(-56.31, 79.2) * mm});
            skLineSegment(sketch, "E5260", {"start": v(-56.31, 79.2) * mm, "end": v(-56.41, 79.29) * mm});
            skLineSegment(sketch, "E5261", {"start": v(-56.41, 79.29) * mm, "end": v(-56.52, 79.36) * mm});
            skLineSegment(sketch, "E5262", {"start": v(-56.52, 79.36) * mm, "end": v(-56.62, 79.44) * mm});
            skLineSegment(sketch, "E5263", {"start": v(-56.62, 79.44) * mm, "end": v(-56.73, 79.52) * mm});
            skLineSegment(sketch, "E5264", {"start": v(-56.73, 79.52) * mm, "end": v(-56.84, 79.6) * mm});
            skLineSegment(sketch, "E5265", {"start": v(-56.84, 79.6) * mm, "end": v(-56.95, 79.68) * mm});
            skLineSegment(sketch, "E5266", {"start": v(-56.95, 79.68) * mm, "end": v(-57.06, 79.76) * mm});
            skLineSegment(sketch, "E5267", {"start": v(-57.06, 79.76) * mm, "end": v(-57.18, 79.84) * mm});
            skLineSegment(sketch, "E5268", {"start": v(-57.18, 79.84) * mm, "end": v(-57.3, 79.92) * mm});
            skLineSegment(sketch, "E5269", {"start": v(-57.3, 79.92) * mm, "end": v(-57.41, 80) * mm});
            skLineSegment(sketch, "E5270", {"start": v(-57.41, 80) * mm, "end": v(-57.53, 80.09) * mm});
            skLineSegment(sketch, "E5271", {"start": v(-57.53, 80.09) * mm, "end": v(-57.66, 80.17) * mm});
            skLineSegment(sketch, "E5272", {"start": v(-57.66, 80.17) * mm, "end": v(-57.78, 80.25) * mm});
            skLineSegment(sketch, "E5273", {"start": v(-57.78, 80.25) * mm, "end": v(-57.9, 80.34) * mm});
            skLineSegment(sketch, "E5274", {"start": v(-57.9, 80.34) * mm, "end": v(-58.03, 80.42) * mm});
            skLineSegment(sketch, "E5275", {"start": v(-58.03, 80.42) * mm, "end": v(-58.16, 80.5) * mm});
            skLineSegment(sketch, "E5276", {"start": v(-58.16, 80.5) * mm, "end": v(-58.3, 80.6) * mm});
            skLineSegment(sketch, "E5277", {"start": v(-58.3, 80.6) * mm, "end": v(-58.42, 80.68) * mm});
            skLineSegment(sketch, "E5278", {"start": v(-58.42, 80.68) * mm, "end": v(-58.56, 80.76) * mm});
            skLineSegment(sketch, "E5279", {"start": v(-58.56, 80.76) * mm, "end": v(-58.7, 80.85) * mm});
            skLineSegment(sketch, "E5280", {"start": v(-58.7, 80.85) * mm, "end": v(-58.83, 80.94) * mm});
            skLineSegment(sketch, "E5281", {"start": v(-58.83, 80.94) * mm, "end": v(-58.97, 81.02) * mm});
            skLineSegment(sketch, "E5282", {"start": v(-58.97, 81.02) * mm, "end": v(-59.12, 81.11) * mm});
            skLineSegment(sketch, "E5283", {"start": v(-59.12, 81.11) * mm, "end": v(-59.26, 81.2) * mm});
            skLineSegment(sketch, "E5284", {"start": v(-59.26, 81.2) * mm, "end": v(-59.4, 81.29) * mm});
            skLineSegment(sketch, "E5285", {"start": v(-59.4, 81.29) * mm, "end": v(-59.56, 81.37) * mm});
            skLineSegment(sketch, "E5286", {"start": v(-59.56, 81.37) * mm, "end": v(-59.7, 81.46) * mm});
            skLineSegment(sketch, "E5287", {"start": v(-59.7, 81.46) * mm, "end": v(-59.86, 81.55) * mm});
            skLineSegment(sketch, "E5288", {"start": v(-59.86, 81.55) * mm, "end": v(-60.01, 81.64) * mm});
            skLineSegment(sketch, "E5289", {"start": v(-60.01, 81.64) * mm, "end": v(-60.17, 81.73) * mm});
            skLineSegment(sketch, "E5290", {"start": v(-60.17, 81.73) * mm, "end": v(-60.32, 81.82) * mm});
            skLineSegment(sketch, "E5291", {"start": v(-60.32, 81.82) * mm, "end": v(-60.48, 81.9) * mm});
            skLineSegment(sketch, "E5292", {"start": v(-60.48, 81.9) * mm, "end": v(-60.64, 82) * mm});
            skLineSegment(sketch, "E5293", {"start": v(-60.64, 82) * mm, "end": v(-60.8, 82.09) * mm});
            skLineSegment(sketch, "E5294", {"start": v(-60.8, 82.09) * mm, "end": v(-60.97, 82.18) * mm});
            skLineSegment(sketch, "E5295", {"start": v(-60.97, 82.18) * mm, "end": v(-61.14, 82.27) * mm});
            skLineSegment(sketch, "E5296", {"start": v(-61.14, 82.27) * mm, "end": v(-61.2, 82.22) * mm});
            skLineSegment(sketch, "E5297", {"start": v(-61.2, 82.22) * mm, "end": v(-62.46, 81.27) * mm});
            skLineSegment(sketch, "E5298", {"start": v(-62.46, 81.27) * mm, "end": v(-62.52, 81.22) * mm});
            skLineSegment(sketch, "E5299", {"start": v(-62.52, 81.22) * mm, "end": v(-62.48, 81.03) * mm});
            skLineSegment(sketch, "E5300", {"start": v(-62.48, 81.03) * mm, "end": v(-62.44, 80.85) * mm});
            skLineSegment(sketch, "E5301", {"start": v(-62.44, 80.85) * mm, "end": v(-62.4, 80.67) * mm});
            skLineSegment(sketch, "E5302", {"start": v(-62.4, 80.67) * mm, "end": v(-62.36, 80.5) * mm});
            skLineSegment(sketch, "E5303", {"start": v(-62.36, 80.5) * mm, "end": v(-62.31, 80.31) * mm});
            skLineSegment(sketch, "E5304", {"start": v(-62.31, 80.31) * mm, "end": v(-62.27, 80.14) * mm});
            skLineSegment(sketch, "E5305", {"start": v(-62.27, 80.14) * mm, "end": v(-62.23, 79.96) * mm});
            skLineSegment(sketch, "E5306", {"start": v(-62.23, 79.96) * mm, "end": v(-62.18, 79.8) * mm});
            skLineSegment(sketch, "E5307", {"start": v(-62.18, 79.8) * mm, "end": v(-62.14, 79.62) * mm});
            skLineSegment(sketch, "E5308", {"start": v(-62.14, 79.62) * mm, "end": v(-62.1, 79.45) * mm});
            skLineSegment(sketch, "E5309", {"start": v(-62.1, 79.45) * mm, "end": v(-62.05, 79.29) * mm});
            skLineSegment(sketch, "E5310", {"start": v(-62.05, 79.29) * mm, "end": v(-62, 79.12) * mm});
            skLineSegment(sketch, "E5311", {"start": v(-62, 79.12) * mm, "end": v(-61.96, 78.96) * mm});
            skLineSegment(sketch, "E5312", {"start": v(-61.96, 78.96) * mm, "end": v(-61.92, 78.8) * mm});
            skLineSegment(sketch, "E5313", {"start": v(-61.92, 78.8) * mm, "end": v(-61.87, 78.64) * mm});
            skLineSegment(sketch, "E5314", {"start": v(-61.87, 78.64) * mm, "end": v(-61.83, 78.48) * mm});
            skLineSegment(sketch, "E5315", {"start": v(-61.83, 78.48) * mm, "end": v(-61.78, 78.33) * mm});
            skLineSegment(sketch, "E5316", {"start": v(-61.78, 78.33) * mm, "end": v(-61.73, 78.18) * mm});
            skLineSegment(sketch, "E5317", {"start": v(-61.73, 78.18) * mm, "end": v(-61.69, 78.02) * mm});
            skLineSegment(sketch, "E5318", {"start": v(-61.69, 78.02) * mm, "end": v(-61.64, 77.88) * mm});
            skLineSegment(sketch, "E5319", {"start": v(-61.64, 77.88) * mm, "end": v(-61.6, 77.73) * mm});
            skLineSegment(sketch, "E5320", {"start": v(-61.6, 77.73) * mm, "end": v(-61.55, 77.58) * mm});
            skLineSegment(sketch, "E5321", {"start": v(-61.55, 77.58) * mm, "end": v(-61.5, 77.44) * mm});
            skLineSegment(sketch, "E5322", {"start": v(-61.5, 77.44) * mm, "end": v(-61.45, 77.3) * mm});
            skLineSegment(sketch, "E5323", {"start": v(-61.45, 77.3) * mm, "end": v(-61.4, 77.16) * mm});
            skLineSegment(sketch, "E5324", {"start": v(-61.4, 77.16) * mm, "end": v(-61.36, 77.02) * mm});
            skLineSegment(sketch, "E5325", {"start": v(-61.36, 77.02) * mm, "end": v(-61.31, 76.88) * mm});
            skLineSegment(sketch, "E5326", {"start": v(-61.31, 76.88) * mm, "end": v(-61.27, 76.75) * mm});
            skLineSegment(sketch, "E5327", {"start": v(-61.27, 76.75) * mm, "end": v(-61.22, 76.62) * mm});
            skLineSegment(sketch, "E5328", {"start": v(-61.22, 76.62) * mm, "end": v(-61.17, 76.49) * mm});
            skLineSegment(sketch, "E5329", {"start": v(-61.17, 76.49) * mm, "end": v(-61.13, 76.36) * mm});
            skLineSegment(sketch, "E5330", {"start": v(-61.13, 76.36) * mm, "end": v(-61.08, 76.23) * mm});
            skLineSegment(sketch, "E5331", {"start": v(-61.08, 76.23) * mm, "end": v(-61.03, 76.1) * mm});
            skLineSegment(sketch, "E5332", {"start": v(-61.03, 76.1) * mm, "end": v(-60.99, 75.98) * mm});
            skLineSegment(sketch, "E5333", {"start": v(-60.99, 75.98) * mm, "end": v(-60.94, 75.86) * mm});
            skLineSegment(sketch, "E5334", {"start": v(-60.94, 75.86) * mm, "end": v(-60.9, 75.74) * mm});
            skLineSegment(sketch, "E5335", {"start": v(-60.9, 75.74) * mm, "end": v(-61.59, 75.1) * mm});
            skLineSegment(sketch, "E5336", {"start": v(-61.59, 75.1) * mm, "end": v(-62.35, 74.55) * mm});
            skLineSegment(sketch, "E5337", {"start": v(-62.35, 74.55) * mm, "end": v(-62.46, 74.62) * mm});
            skLineSegment(sketch, "E5338", {"start": v(-62.46, 74.62) * mm, "end": v(-62.57, 74.68) * mm});
            skLineSegment(sketch, "E5339", {"start": v(-62.57, 74.68) * mm, "end": v(-62.68, 74.75) * mm});
            skLineSegment(sketch, "E5340", {"start": v(-62.68, 74.75) * mm, "end": v(-62.8, 74.82) * mm});
            skLineSegment(sketch, "E5341", {"start": v(-62.8, 74.82) * mm, "end": v(-62.91, 74.9) * mm});
            skLineSegment(sketch, "E5342", {"start": v(-62.91, 74.9) * mm, "end": v(-63.03, 74.97) * mm});
            skLineSegment(sketch, "E5343", {"start": v(-63.03, 74.97) * mm, "end": v(-63.15, 75.04) * mm});
            skLineSegment(sketch, "E5344", {"start": v(-63.15, 75.04) * mm, "end": v(-63.27, 75.1) * mm});
            skLineSegment(sketch, "E5345", {"start": v(-63.27, 75.1) * mm, "end": v(-63.39, 75.18) * mm});
            skLineSegment(sketch, "E5346", {"start": v(-63.39, 75.18) * mm, "end": v(-63.51, 75.25) * mm});
            skLineSegment(sketch, "E5347", {"start": v(-63.51, 75.25) * mm, "end": v(-63.64, 75.33) * mm});
            skLineSegment(sketch, "E5348", {"start": v(-63.64, 75.33) * mm, "end": v(-63.77, 75.4) * mm});
            skLineSegment(sketch, "E5349", {"start": v(-63.77, 75.4) * mm, "end": v(-63.9, 75.47) * mm});
            skLineSegment(sketch, "E5350", {"start": v(-63.9, 75.47) * mm, "end": v(-64.03, 75.55) * mm});
            skLineSegment(sketch, "E5351", {"start": v(-64.03, 75.55) * mm, "end": v(-64.16, 75.62) * mm});
            skLineSegment(sketch, "E5352", {"start": v(-64.16, 75.62) * mm, "end": v(-64.3, 75.7) * mm});
            skLineSegment(sketch, "E5353", {"start": v(-64.3, 75.7) * mm, "end": v(-64.44, 75.77) * mm});
            skLineSegment(sketch, "E5354", {"start": v(-64.44, 75.77) * mm, "end": v(-64.57, 75.85) * mm});
            skLineSegment(sketch, "E5355", {"start": v(-64.57, 75.85) * mm, "end": v(-64.72, 75.92) * mm});
            skLineSegment(sketch, "E5356", {"start": v(-64.72, 75.92) * mm, "end": v(-64.86, 76) * mm});
            skLineSegment(sketch, "E5357", {"start": v(-64.86, 76) * mm, "end": v(-65, 76.07) * mm});
            skLineSegment(sketch, "E5358", {"start": v(-65, 76.07) * mm, "end": v(-65.15, 76.15) * mm});
            skLineSegment(sketch, "E5359", {"start": v(-65.15, 76.15) * mm, "end": v(-65.3, 76.22) * mm});
            skLineSegment(sketch, "E5360", {"start": v(-65.3, 76.22) * mm, "end": v(-65.45, 76.3) * mm});
            skLineSegment(sketch, "E5361", {"start": v(-65.45, 76.3) * mm, "end": v(-65.6, 76.37) * mm});
            skLineSegment(sketch, "E5362", {"start": v(-65.6, 76.37) * mm, "end": v(-65.76, 76.45) * mm});
            skLineSegment(sketch, "E5363", {"start": v(-65.76, 76.45) * mm, "end": v(-65.91, 76.53) * mm});
            skLineSegment(sketch, "E5364", {"start": v(-65.91, 76.53) * mm, "end": v(-66.07, 76.6) * mm});
            skLineSegment(sketch, "E5365", {"start": v(-66.07, 76.6) * mm, "end": v(-66.23, 76.68) * mm});
            skLineSegment(sketch, "E5366", {"start": v(-66.23, 76.68) * mm, "end": v(-66.4, 76.76) * mm});
            skLineSegment(sketch, "E5367", {"start": v(-66.4, 76.76) * mm, "end": v(-66.56, 76.83) * mm});
            skLineSegment(sketch, "E5368", {"start": v(-66.56, 76.83) * mm, "end": v(-66.72, 76.9) * mm});
            skLineSegment(sketch, "E5369", {"start": v(-66.72, 76.9) * mm, "end": v(-66.9, 76.99) * mm});
            skLineSegment(sketch, "E5370", {"start": v(-66.9, 76.99) * mm, "end": v(-67.06, 77.06) * mm});
            skLineSegment(sketch, "E5371", {"start": v(-67.06, 77.06) * mm, "end": v(-67.23, 77.14) * mm});
            skLineSegment(sketch, "E5372", {"start": v(-67.23, 77.14) * mm, "end": v(-67.4, 77.22) * mm});
            skLineSegment(sketch, "E5373", {"start": v(-67.4, 77.22) * mm, "end": v(-67.47, 77.16) * mm});
            skLineSegment(sketch, "E5374", {"start": v(-67.47, 77.16) * mm, "end": v(-68.64, 76.12) * mm});
            skLineSegment(sketch, "E5375", {"start": v(-68.64, 76.12) * mm, "end": v(-68.7, 76.06) * mm});
            skLineSegment(sketch, "E5376", {"start": v(-68.7, 76.06) * mm, "end": v(-68.65, 75.88) * mm});
            skLineSegment(sketch, "E5377", {"start": v(-68.65, 75.88) * mm, "end": v(-68.6, 75.7) * mm});
            skLineSegment(sketch, "E5378", {"start": v(-68.6, 75.7) * mm, "end": v(-68.54, 75.53) * mm});
            skLineSegment(sketch, "E5379", {"start": v(-68.54, 75.53) * mm, "end": v(-68.48, 75.35) * mm});
            skLineSegment(sketch, "E5380", {"start": v(-68.48, 75.35) * mm, "end": v(-68.42, 75.18) * mm});
            skLineSegment(sketch, "E5381", {"start": v(-68.42, 75.18) * mm, "end": v(-68.37, 75) * mm});
            skLineSegment(sketch, "E5382", {"start": v(-68.37, 75) * mm, "end": v(-68.3, 74.83) * mm});
            skLineSegment(sketch, "E5383", {"start": v(-68.3, 74.83) * mm, "end": v(-68.25, 74.67) * mm});
            skLineSegment(sketch, "E5384", {"start": v(-68.25, 74.67) * mm, "end": v(-68.2, 74.5) * mm});
            skLineSegment(sketch, "E5385", {"start": v(-68.2, 74.5) * mm, "end": v(-68.14, 74.34) * mm});
            skLineSegment(sketch, "E5386", {"start": v(-68.14, 74.34) * mm, "end": v(-68.08, 74.17) * mm});
            skLineSegment(sketch, "E5387", {"start": v(-68.08, 74.17) * mm, "end": v(-68.02, 74.01) * mm});
            skLineSegment(sketch, "E5388", {"start": v(-68.02, 74.01) * mm, "end": v(-67.97, 73.85) * mm});
            skLineSegment(sketch, "E5389", {"start": v(-67.97, 73.85) * mm, "end": v(-67.9, 73.7) * mm});
            skLineSegment(sketch, "E5390", {"start": v(-67.9, 73.7) * mm, "end": v(-67.85, 73.54) * mm});
            skLineSegment(sketch, "E5391", {"start": v(-67.85, 73.54) * mm, "end": v(-67.8, 73.4) * mm});
            skLineSegment(sketch, "E5392", {"start": v(-67.8, 73.4) * mm, "end": v(-67.73, 73.24) * mm});
            skLineSegment(sketch, "E5393", {"start": v(-67.73, 73.24) * mm, "end": v(-67.68, 73.1) * mm});
            skLineSegment(sketch, "E5394", {"start": v(-67.68, 73.1) * mm, "end": v(-67.62, 72.94) * mm});
            skLineSegment(sketch, "E5395", {"start": v(-67.62, 72.94) * mm, "end": v(-67.56, 72.8) * mm});
            skLineSegment(sketch, "E5396", {"start": v(-67.56, 72.8) * mm, "end": v(-67.5, 72.66) * mm});
            skLineSegment(sketch, "E5397", {"start": v(-67.5, 72.66) * mm, "end": v(-67.45, 72.51) * mm});
            skLineSegment(sketch, "E5398", {"start": v(-67.45, 72.51) * mm, "end": v(-67.39, 72.37) * mm});
            skLineSegment(sketch, "E5399", {"start": v(-67.39, 72.37) * mm, "end": v(-67.33, 72.24) * mm});
            skLineSegment(sketch, "E5400", {"start": v(-67.33, 72.24) * mm, "end": v(-67.27, 72.1) * mm});
            skLineSegment(sketch, "E5401", {"start": v(-67.27, 72.1) * mm, "end": v(-67.21, 71.97) * mm});
            skLineSegment(sketch, "E5402", {"start": v(-67.21, 71.97) * mm, "end": v(-67.16, 71.84) * mm});
            skLineSegment(sketch, "E5403", {"start": v(-67.16, 71.84) * mm, "end": v(-67.1, 71.7) * mm});
            skLineSegment(sketch, "E5404", {"start": v(-67.1, 71.7) * mm, "end": v(-67.04, 71.58) * mm});
            skLineSegment(sketch, "E5405", {"start": v(-67.04, 71.58) * mm, "end": v(-66.99, 71.45) * mm});
            skLineSegment(sketch, "E5406", {"start": v(-66.99, 71.45) * mm, "end": v(-66.93, 71.33) * mm});
            skLineSegment(sketch, "E5407", {"start": v(-66.93, 71.33) * mm, "end": v(-66.87, 71.2) * mm});
            skLineSegment(sketch, "E5408", {"start": v(-66.87, 71.2) * mm, "end": v(-66.82, 71.08) * mm});
            skLineSegment(sketch, "E5409", {"start": v(-66.82, 71.08) * mm, "end": v(-66.76, 70.96) * mm});
            skLineSegment(sketch, "E5410", {"start": v(-66.76, 70.96) * mm, "end": v(-66.7, 70.85) * mm});
            skLineSegment(sketch, "E5411", {"start": v(-66.7, 70.85) * mm, "end": v(-66.65, 70.73) * mm});
            skLineSegment(sketch, "E5412", {"start": v(-66.65, 70.73) * mm, "end": v(-67.3, 70.04) * mm});
            skLineSegment(sketch, "E5413", {"start": v(-67.3, 70.04) * mm, "end": v(-68.01, 69.42) * mm});
            skLineSegment(sketch, "E5414", {"start": v(-68.01, 69.42) * mm, "end": v(-68.12, 69.48) * mm});
            skLineSegment(sketch, "E5415", {"start": v(-68.12, 69.48) * mm, "end": v(-68.24, 69.55) * mm});
            skLineSegment(sketch, "E5416", {"start": v(-68.24, 69.55) * mm, "end": v(-68.35, 69.6) * mm});
            skLineSegment(sketch, "E5417", {"start": v(-68.35, 69.6) * mm, "end": v(-68.47, 69.67) * mm});
            skLineSegment(sketch, "E5418", {"start": v(-68.47, 69.67) * mm, "end": v(-68.6, 69.73) * mm});
            skLineSegment(sketch, "E5419", {"start": v(-68.6, 69.73) * mm, "end": v(-68.72, 69.8) * mm});
            skLineSegment(sketch, "E5420", {"start": v(-68.72, 69.8) * mm, "end": v(-68.84, 69.85) * mm});
            skLineSegment(sketch, "E5421", {"start": v(-68.84, 69.85) * mm, "end": v(-68.97, 69.91) * mm});
            skLineSegment(sketch, "E5422", {"start": v(-68.97, 69.91) * mm, "end": v(-69.1, 69.98) * mm});
            skLineSegment(sketch, "E5423", {"start": v(-69.1, 69.98) * mm, "end": v(-69.22, 70.04) * mm});
            skLineSegment(sketch, "E5424", {"start": v(-69.22, 70.04) * mm, "end": v(-69.35, 70.1) * mm});
            skLineSegment(sketch, "E5425", {"start": v(-69.35, 70.1) * mm, "end": v(-69.49, 70.16) * mm});
            skLineSegment(sketch, "E5426", {"start": v(-69.49, 70.16) * mm, "end": v(-69.62, 70.23) * mm});
            skLineSegment(sketch, "E5427", {"start": v(-69.62, 70.23) * mm, "end": v(-69.76, 70.3) * mm});
            skLineSegment(sketch, "E5428", {"start": v(-69.76, 70.3) * mm, "end": v(-69.9, 70.35) * mm});
            skLineSegment(sketch, "E5429", {"start": v(-69.9, 70.35) * mm, "end": v(-70.04, 70.42) * mm});
            skLineSegment(sketch, "E5430", {"start": v(-70.04, 70.42) * mm, "end": v(-70.18, 70.48) * mm});
            skLineSegment(sketch, "E5431", {"start": v(-70.18, 70.48) * mm, "end": v(-70.33, 70.55) * mm});
            skLineSegment(sketch, "E5432", {"start": v(-70.33, 70.55) * mm, "end": v(-70.47, 70.6) * mm});
            skLineSegment(sketch, "E5433", {"start": v(-70.47, 70.6) * mm, "end": v(-70.62, 70.67) * mm});
            skLineSegment(sketch, "E5434", {"start": v(-70.62, 70.67) * mm, "end": v(-70.77, 70.74) * mm});
            skLineSegment(sketch, "E5435", {"start": v(-70.77, 70.74) * mm, "end": v(-70.92, 70.8) * mm});
            skLineSegment(sketch, "E5436", {"start": v(-70.92, 70.8) * mm, "end": v(-71.08, 70.86) * mm});
            skLineSegment(sketch, "E5437", {"start": v(-71.08, 70.86) * mm, "end": v(-71.23, 70.93) * mm});
            skLineSegment(sketch, "E5438", {"start": v(-71.23, 70.93) * mm, "end": v(-71.4, 71) * mm});
            skLineSegment(sketch, "E5439", {"start": v(-71.4, 71) * mm, "end": v(-71.55, 71.06) * mm});
            skLineSegment(sketch, "E5440", {"start": v(-71.55, 71.06) * mm, "end": v(-71.71, 71.12) * mm});
            skLineSegment(sketch, "E5441", {"start": v(-71.71, 71.12) * mm, "end": v(-71.88, 71.18) * mm});
            skLineSegment(sketch, "E5442", {"start": v(-71.88, 71.18) * mm, "end": v(-72.04, 71.25) * mm});
            skLineSegment(sketch, "E5443", {"start": v(-72.04, 71.25) * mm, "end": v(-72.21, 71.31) * mm});
            skLineSegment(sketch, "E5444", {"start": v(-72.21, 71.31) * mm, "end": v(-72.38, 71.37) * mm});
            skLineSegment(sketch, "E5445", {"start": v(-72.38, 71.37) * mm, "end": v(-72.55, 71.44) * mm});
            skLineSegment(sketch, "E5446", {"start": v(-72.55, 71.44) * mm, "end": v(-72.72, 71.5) * mm});
            skLineSegment(sketch, "E5447", {"start": v(-72.72, 71.5) * mm, "end": v(-72.9, 71.56) * mm});
            skLineSegment(sketch, "E5448", {"start": v(-72.9, 71.56) * mm, "end": v(-73.08, 71.63) * mm});
            skLineSegment(sketch, "E5449", {"start": v(-73.08, 71.63) * mm, "end": v(-73.26, 71.69) * mm});
            skLineSegment(sketch, "E5450", {"start": v(-73.26, 71.69) * mm, "end": v(-73.31, 71.63) * mm});
            skLineSegment(sketch, "E5451", {"start": v(-73.31, 71.63) * mm, "end": v(-74.4, 70.5) * mm});
            skLineSegment(sketch, "E5452", {"start": v(-74.4, 70.5) * mm, "end": v(-74.46, 70.44) * mm});
            skLineSegment(sketch, "E5453", {"start": v(-74.46, 70.44) * mm, "end": v(-74.39, 70.26) * mm});
            skLineSegment(sketch, "E5454", {"start": v(-74.39, 70.26) * mm, "end": v(-74.32, 70.09) * mm});
            skLineSegment(sketch, "E5455", {"start": v(-74.32, 70.09) * mm, "end": v(-74.25, 69.92) * mm});
            skLineSegment(sketch, "E5456", {"start": v(-74.25, 69.92) * mm, "end": v(-74.18, 69.74) * mm});
            skLineSegment(sketch, "E5457", {"start": v(-74.18, 69.74) * mm, "end": v(-74.11, 69.58) * mm});
            skLineSegment(sketch, "E5458", {"start": v(-74.11, 69.58) * mm, "end": v(-74.04, 69.4) * mm});
            skLineSegment(sketch, "E5459", {"start": v(-74.04, 69.4) * mm, "end": v(-73.97, 69.24) * mm});
            skLineSegment(sketch, "E5460", {"start": v(-73.97, 69.24) * mm, "end": v(-73.9, 69.08) * mm});
            skLineSegment(sketch, "E5461", {"start": v(-73.9, 69.08) * mm, "end": v(-73.83, 68.92) * mm});
            skLineSegment(sketch, "E5462", {"start": v(-73.83, 68.92) * mm, "end": v(-73.76, 68.76) * mm});
            skLineSegment(sketch, "E5463", {"start": v(-73.76, 68.76) * mm, "end": v(-73.7, 68.6) * mm});
            skLineSegment(sketch, "E5464", {"start": v(-73.7, 68.6) * mm, "end": v(-73.62, 68.45) * mm});
            skLineSegment(sketch, "E5465", {"start": v(-73.62, 68.45) * mm, "end": v(-73.55, 68.3) * mm});
            skLineSegment(sketch, "E5466", {"start": v(-73.55, 68.3) * mm, "end": v(-73.48, 68.14) * mm});
            skLineSegment(sketch, "E5467", {"start": v(-73.48, 68.14) * mm, "end": v(-73.41, 68) * mm});
            skLineSegment(sketch, "E5468", {"start": v(-73.41, 68) * mm, "end": v(-73.34, 67.85) * mm});
            skLineSegment(sketch, "E5469", {"start": v(-73.34, 67.85) * mm, "end": v(-73.27, 67.7) * mm});
            skLineSegment(sketch, "E5470", {"start": v(-73.27, 67.7) * mm, "end": v(-73.2, 67.56) * mm});
            skLineSegment(sketch, "E5471", {"start": v(-73.2, 67.56) * mm, "end": v(-73.13, 67.41) * mm});
            skLineSegment(sketch, "E5472", {"start": v(-73.13, 67.41) * mm, "end": v(-73.06, 67.27) * mm});
            skLineSegment(sketch, "E5473", {"start": v(-73.06, 67.27) * mm, "end": v(-73, 67.14) * mm});
            skLineSegment(sketch, "E5474", {"start": v(-73, 67.14) * mm, "end": v(-72.93, 67) * mm});
            skLineSegment(sketch, "E5475", {"start": v(-72.93, 67) * mm, "end": v(-72.86, 66.86) * mm});
            skLineSegment(sketch, "E5476", {"start": v(-72.86, 66.86) * mm, "end": v(-72.8, 66.73) * mm});
            skLineSegment(sketch, "E5477", {"start": v(-72.8, 66.73) * mm, "end": v(-72.72, 66.6) * mm});
            skLineSegment(sketch, "E5478", {"start": v(-72.72, 66.6) * mm, "end": v(-72.65, 66.47) * mm});
            skLineSegment(sketch, "E5479", {"start": v(-72.65, 66.47) * mm, "end": v(-72.59, 66.35) * mm});
            skLineSegment(sketch, "E5480", {"start": v(-72.59, 66.35) * mm, "end": v(-72.52, 66.22) * mm});
            skLineSegment(sketch, "E5481", {"start": v(-72.52, 66.22) * mm, "end": v(-72.45, 66.1) * mm});
            skLineSegment(sketch, "E5482", {"start": v(-72.45, 66.1) * mm, "end": v(-72.39, 65.98) * mm});
            skLineSegment(sketch, "E5483", {"start": v(-72.39, 65.98) * mm, "end": v(-72.32, 65.86) * mm});
            skLineSegment(sketch, "E5484", {"start": v(-72.32, 65.86) * mm, "end": v(-72.25, 65.74) * mm});
            skLineSegment(sketch, "E5485", {"start": v(-72.25, 65.74) * mm, "end": v(-72.19, 65.62) * mm});
            skLineSegment(sketch, "E5486", {"start": v(-72.19, 65.62) * mm, "end": v(-72.12, 65.5) * mm});
            skLineSegment(sketch, "E5487", {"start": v(-72.12, 65.5) * mm, "end": v(-72.06, 65.4) * mm});
            skLineSegment(sketch, "E5488", {"start": v(-72.06, 65.4) * mm, "end": v(-72, 65.28) * mm});
            skLineSegment(sketch, "E5489", {"start": v(-72, 65.28) * mm, "end": v(-72.58, 64.54) * mm});
            skLineSegment(sketch, "E5490", {"start": v(-72.58, 64.54) * mm, "end": v(-73.25, 63.87) * mm});
            skLineSegment(sketch, "E5491", {"start": v(-73.25, 63.87) * mm, "end": v(-73.36, 63.93) * mm});
            skLineSegment(sketch, "E5492", {"start": v(-73.36, 63.93) * mm, "end": v(-73.48, 63.98) * mm});
            skLineSegment(sketch, "E5493", {"start": v(-73.48, 63.98) * mm, "end": v(-73.6, 64.03) * mm});
            skLineSegment(sketch, "E5494", {"start": v(-73.6, 64.03) * mm, "end": v(-73.73, 64.08) * mm});
            skLineSegment(sketch, "E5495", {"start": v(-73.73, 64.08) * mm, "end": v(-73.85, 64.13) * mm});
            skLineSegment(sketch, "E5496", {"start": v(-73.85, 64.13) * mm, "end": v(-73.98, 64.18) * mm});
            skLineSegment(sketch, "E5497", {"start": v(-73.98, 64.18) * mm, "end": v(-74.1, 64.24) * mm});
            skLineSegment(sketch, "E5498", {"start": v(-74.1, 64.24) * mm, "end": v(-74.24, 64.29) * mm});
            skLineSegment(sketch, "E5499", {"start": v(-74.24, 64.29) * mm, "end": v(-74.37, 64.34) * mm});
            skLineSegment(sketch, "E5500", {"start": v(-74.37, 64.34) * mm, "end": v(-74.5, 64.4) * mm});
            skLineSegment(sketch, "E5501", {"start": v(-74.5, 64.4) * mm, "end": v(-74.64, 64.44) * mm});
            skLineSegment(sketch, "E5502", {"start": v(-74.64, 64.44) * mm, "end": v(-74.78, 64.5) * mm});
            skLineSegment(sketch, "E5503", {"start": v(-74.78, 64.5) * mm, "end": v(-74.92, 64.55) * mm});
            skLineSegment(sketch, "E5504", {"start": v(-74.92, 64.55) * mm, "end": v(-75.06, 64.6) * mm});
            skLineSegment(sketch, "E5505", {"start": v(-75.06, 64.6) * mm, "end": v(-75.2, 64.65) * mm});
            skLineSegment(sketch, "E5506", {"start": v(-75.2, 64.65) * mm, "end": v(-75.35, 64.7) * mm});
            skLineSegment(sketch, "E5507", {"start": v(-75.35, 64.7) * mm, "end": v(-75.5, 64.76) * mm});
            skLineSegment(sketch, "E5508", {"start": v(-75.5, 64.76) * mm, "end": v(-75.64, 64.8) * mm});
            skLineSegment(sketch, "E5509", {"start": v(-75.64, 64.8) * mm, "end": v(-75.8, 64.86) * mm});
            skLineSegment(sketch, "E5510", {"start": v(-75.8, 64.86) * mm, "end": v(-75.95, 64.91) * mm});
            skLineSegment(sketch, "E5511", {"start": v(-75.95, 64.91) * mm, "end": v(-76.1, 64.97) * mm});
            skLineSegment(sketch, "E5512", {"start": v(-76.1, 64.97) * mm, "end": v(-76.26, 65.02) * mm});
            skLineSegment(sketch, "E5513", {"start": v(-76.26, 65.02) * mm, "end": v(-76.42, 65.07) * mm});
            skLineSegment(sketch, "E5514", {"start": v(-76.42, 65.07) * mm, "end": v(-76.58, 65.12) * mm});
            skLineSegment(sketch, "E5515", {"start": v(-76.58, 65.12) * mm, "end": v(-76.74, 65.17) * mm});
            skLineSegment(sketch, "E5516", {"start": v(-76.74, 65.17) * mm, "end": v(-76.9, 65.22) * mm});
            skLineSegment(sketch, "E5517", {"start": v(-76.9, 65.22) * mm, "end": v(-77.07, 65.27) * mm});
            skLineSegment(sketch, "E5518", {"start": v(-77.07, 65.27) * mm, "end": v(-77.24, 65.32) * mm});
            skLineSegment(sketch, "E5519", {"start": v(-77.24, 65.32) * mm, "end": v(-77.41, 65.38) * mm});
            skLineSegment(sketch, "E5520", {"start": v(-77.41, 65.38) * mm, "end": v(-77.58, 65.43) * mm});
            skLineSegment(sketch, "E5521", {"start": v(-77.58, 65.43) * mm, "end": v(-77.76, 65.48) * mm});
            skLineSegment(sketch, "E5522", {"start": v(-77.76, 65.48) * mm, "end": v(-77.93, 65.52) * mm});
            skLineSegment(sketch, "E5523", {"start": v(-77.93, 65.52) * mm, "end": v(-78.1, 65.57) * mm});
            skLineSegment(sketch, "E5524", {"start": v(-78.1, 65.57) * mm, "end": v(-78.29, 65.62) * mm});
            skLineSegment(sketch, "E5525", {"start": v(-78.29, 65.62) * mm, "end": v(-78.47, 65.67) * mm});
            skLineSegment(sketch, "E5526", {"start": v(-78.47, 65.67) * mm, "end": v(-78.65, 65.72) * mm});
            skLineSegment(sketch, "E5527", {"start": v(-78.65, 65.72) * mm, "end": v(-78.7, 65.66) * mm});
            skLineSegment(sketch, "E5528", {"start": v(-78.7, 65.66) * mm, "end": v(-79.7, 64.45) * mm});
            skLineSegment(sketch, "E5529", {"start": v(-79.7, 64.45) * mm, "end": v(-79.76, 64.38) * mm});
            skLineSegment(sketch, "E5530", {"start": v(-79.76, 64.38) * mm, "end": v(-79.67, 64.2) * mm});
            skLineSegment(sketch, "E5531", {"start": v(-79.67, 64.2) * mm, "end": v(-79.59, 64.04) * mm});
            skLineSegment(sketch, "E5532", {"start": v(-79.59, 64.04) * mm, "end": v(-79.5, 63.87) * mm});
            skLineSegment(sketch, "E5533", {"start": v(-79.5, 63.87) * mm, "end": v(-79.42, 63.7) * mm});
            skLineSegment(sketch, "E5534", {"start": v(-79.42, 63.7) * mm, "end": v(-79.34, 63.55) * mm});
            skLineSegment(sketch, "E5535", {"start": v(-79.34, 63.55) * mm, "end": v(-79.26, 63.39) * mm});
            skLineSegment(sketch, "E5536", {"start": v(-79.26, 63.39) * mm, "end": v(-79.17, 63.23) * mm});
            skLineSegment(sketch, "E5537", {"start": v(-79.17, 63.23) * mm, "end": v(-79.1, 63.07) * mm});
            skLineSegment(sketch, "E5538", {"start": v(-79.1, 63.07) * mm, "end": v(-79.01, 62.91) * mm});
            skLineSegment(sketch, "E5539", {"start": v(-79.01, 62.91) * mm, "end": v(-78.93, 62.76) * mm});
            skLineSegment(sketch, "E5540", {"start": v(-78.93, 62.76) * mm, "end": v(-78.85, 62.61) * mm});
            skLineSegment(sketch, "E5541", {"start": v(-78.85, 62.61) * mm, "end": v(-78.76, 62.46) * mm});
            skLineSegment(sketch, "E5542", {"start": v(-78.76, 62.46) * mm, "end": v(-78.68, 62.31) * mm});
            skLineSegment(sketch, "E5543", {"start": v(-78.68, 62.31) * mm, "end": v(-78.6, 62.17) * mm});
            skLineSegment(sketch, "E5544", {"start": v(-78.6, 62.17) * mm, "end": v(-78.52, 62.02) * mm});
            skLineSegment(sketch, "E5545", {"start": v(-78.52, 62.02) * mm, "end": v(-78.44, 61.88) * mm});
            skLineSegment(sketch, "E5546", {"start": v(-78.44, 61.88) * mm, "end": v(-78.36, 61.74) * mm});
            skLineSegment(sketch, "E5547", {"start": v(-78.36, 61.74) * mm, "end": v(-78.28, 61.6) * mm});
            skLineSegment(sketch, "E5548", {"start": v(-78.28, 61.6) * mm, "end": v(-78.2, 61.47) * mm});
            skLineSegment(sketch, "E5549", {"start": v(-78.2, 61.47) * mm, "end": v(-78.12, 61.33) * mm});
            skLineSegment(sketch, "E5550", {"start": v(-78.12, 61.33) * mm, "end": v(-78.04, 61.2) * mm});
            skLineSegment(sketch, "E5551", {"start": v(-78.04, 61.2) * mm, "end": v(-77.96, 61.07) * mm});
            skLineSegment(sketch, "E5552", {"start": v(-77.96, 61.07) * mm, "end": v(-77.88, 60.94) * mm});
            skLineSegment(sketch, "E5553", {"start": v(-77.88, 60.94) * mm, "end": v(-77.8, 60.82) * mm});
            skLineSegment(sketch, "E5554", {"start": v(-77.8, 60.82) * mm, "end": v(-77.72, 60.7) * mm});
            skLineSegment(sketch, "E5555", {"start": v(-77.72, 60.7) * mm, "end": v(-77.65, 60.57) * mm});
            skLineSegment(sketch, "E5556", {"start": v(-77.65, 60.57) * mm, "end": v(-77.57, 60.45) * mm});
            skLineSegment(sketch, "E5557", {"start": v(-77.57, 60.45) * mm, "end": v(-77.5, 60.33) * mm});
            skLineSegment(sketch, "E5558", {"start": v(-77.5, 60.33) * mm, "end": v(-77.42, 60.2) * mm});
            skLineSegment(sketch, "E5559", {"start": v(-77.42, 60.2) * mm, "end": v(-77.34, 60.1) * mm});
            skLineSegment(sketch, "E5560", {"start": v(-77.34, 60.1) * mm, "end": v(-77.26, 59.98) * mm});
            skLineSegment(sketch, "E5561", {"start": v(-77.26, 59.98) * mm, "end": v(-77.19, 59.87) * mm});
            skLineSegment(sketch, "E5562", {"start": v(-77.19, 59.87) * mm, "end": v(-77.11, 59.76) * mm});
            skLineSegment(sketch, "E5563", {"start": v(-77.11, 59.76) * mm, "end": v(-77.04, 59.65) * mm});
            skLineSegment(sketch, "E5564", {"start": v(-77.04, 59.65) * mm, "end": v(-76.97, 59.54) * mm});
            skLineSegment(sketch, "E5565", {"start": v(-76.97, 59.54) * mm, "end": v(-76.9, 59.43) * mm});
            skLineSegment(sketch, "E5566", {"start": v(-76.9, 59.43) * mm, "end": v(-77.42, 58.65) * mm});
            skLineSegment(sketch, "E5567", {"start": v(-77.42, 58.65) * mm, "end": v(-78.03, 57.93) * mm});
            skLineSegment(sketch, "E5568", {"start": v(-78.03, 57.93) * mm, "end": v(-78.15, 57.97) * mm});
            skLineSegment(sketch, "E5569", {"start": v(-78.15, 57.97) * mm, "end": v(-78.28, 58.01) * mm});
            skLineSegment(sketch, "E5570", {"start": v(-78.28, 58.01) * mm, "end": v(-78.4, 58.06) * mm});
            skLineSegment(sketch, "E5571", {"start": v(-78.4, 58.06) * mm, "end": v(-78.53, 58.1) * mm});
            skLineSegment(sketch, "E5572", {"start": v(-78.53, 58.1) * mm, "end": v(-78.66, 58.14) * mm});
            skLineSegment(sketch, "E5573", {"start": v(-78.66, 58.14) * mm, "end": v(-78.79, 58.18) * mm});
            skLineSegment(sketch, "E5574", {"start": v(-78.79, 58.18) * mm, "end": v(-78.92, 58.22) * mm});
            skLineSegment(sketch, "E5575", {"start": v(-78.92, 58.22) * mm, "end": v(-79.05, 58.26) * mm});
            skLineSegment(sketch, "E5576", {"start": v(-79.05, 58.26) * mm, "end": v(-79.19, 58.3) * mm});
            skLineSegment(sketch, "E5577", {"start": v(-79.19, 58.3) * mm, "end": v(-79.33, 58.35) * mm});
            skLineSegment(sketch, "E5578", {"start": v(-79.33, 58.35) * mm, "end": v(-79.47, 58.39) * mm});
            skLineSegment(sketch, "E5579", {"start": v(-79.47, 58.39) * mm, "end": v(-79.6, 58.43) * mm});
            skLineSegment(sketch, "E5580", {"start": v(-79.6, 58.43) * mm, "end": v(-79.75, 58.47) * mm});
            skLineSegment(sketch, "E5581", {"start": v(-79.75, 58.47) * mm, "end": v(-79.9, 58.51) * mm});
            skLineSegment(sketch, "E5582", {"start": v(-79.9, 58.51) * mm, "end": v(-80.04, 58.55) * mm});
            skLineSegment(sketch, "E5583", {"start": v(-80.04, 58.55) * mm, "end": v(-80.2, 58.6) * mm});
            skLineSegment(sketch, "E5584", {"start": v(-80.2, 58.6) * mm, "end": v(-80.34, 58.63) * mm});
            skLineSegment(sketch, "E5585", {"start": v(-80.34, 58.63) * mm, "end": v(-80.5, 58.68) * mm});
            skLineSegment(sketch, "E5586", {"start": v(-80.5, 58.68) * mm, "end": v(-80.65, 58.72) * mm});
            skLineSegment(sketch, "E5587", {"start": v(-80.65, 58.72) * mm, "end": v(-80.8, 58.76) * mm});
            skLineSegment(sketch, "E5588", {"start": v(-80.8, 58.76) * mm, "end": v(-80.97, 58.8) * mm});
            skLineSegment(sketch, "E5589", {"start": v(-80.97, 58.8) * mm, "end": v(-81.13, 58.83) * mm});
            skLineSegment(sketch, "E5590", {"start": v(-81.13, 58.83) * mm, "end": v(-81.29, 58.87) * mm});
            skLineSegment(sketch, "E5591", {"start": v(-81.29, 58.87) * mm, "end": v(-81.45, 58.91) * mm});
            skLineSegment(sketch, "E5592", {"start": v(-81.45, 58.91) * mm, "end": v(-81.62, 58.95) * mm});
            skLineSegment(sketch, "E5593", {"start": v(-81.62, 58.95) * mm, "end": v(-81.79, 58.99) * mm});
            skLineSegment(sketch, "E5594", {"start": v(-81.79, 58.99) * mm, "end": v(-81.96, 59.03) * mm});
            skLineSegment(sketch, "E5595", {"start": v(-81.96, 59.03) * mm, "end": v(-82.13, 59.06) * mm});
            skLineSegment(sketch, "E5596", {"start": v(-82.13, 59.06) * mm, "end": v(-82.3, 59.1) * mm});
            skLineSegment(sketch, "E5597", {"start": v(-82.3, 59.1) * mm, "end": v(-82.48, 59.14) * mm});
            skLineSegment(sketch, "E5598", {"start": v(-82.48, 59.14) * mm, "end": v(-82.65, 59.17) * mm});
            skLineSegment(sketch, "E5599", {"start": v(-82.65, 59.17) * mm, "end": v(-82.83, 59.2) * mm});
            skLineSegment(sketch, "E5600", {"start": v(-82.83, 59.2) * mm, "end": v(-83.01, 59.24) * mm});
            skLineSegment(sketch, "E5601", {"start": v(-83.01, 59.24) * mm, "end": v(-83.2, 59.28) * mm});
            skLineSegment(sketch, "E5602", {"start": v(-83.2, 59.28) * mm, "end": v(-83.38, 59.31) * mm});
            skLineSegment(sketch, "E5603", {"start": v(-83.38, 59.31) * mm, "end": v(-83.57, 59.35) * mm});
            skLineSegment(sketch, "E5604", {"start": v(-83.57, 59.35) * mm, "end": v(-83.62, 59.28) * mm});
            skLineSegment(sketch, "E5605", {"start": v(-83.62, 59.28) * mm, "end": v(-84.52, 58) * mm});
            skLineSegment(sketch, "E5606", {"start": v(-84.52, 58) * mm, "end": v(-84.56, 57.92) * mm});
            skLineSegment(sketch, "E5607", {"start": v(-84.56, 57.92) * mm, "end": v(-84.46, 57.76) * mm});
            skLineSegment(sketch, "E5608", {"start": v(-84.46, 57.76) * mm, "end": v(-84.37, 57.6) * mm});
            skLineSegment(sketch, "E5609", {"start": v(-84.37, 57.6) * mm, "end": v(-84.27, 57.44) * mm});
            skLineSegment(sketch, "E5610", {"start": v(-84.27, 57.44) * mm, "end": v(-84.18, 57.28) * mm});
            skLineSegment(sketch, "E5611", {"start": v(-84.18, 57.28) * mm, "end": v(-84.08, 57.13) * mm});
            skLineSegment(sketch, "E5612", {"start": v(-84.08, 57.13) * mm, "end": v(-83.99, 56.97) * mm});
            skLineSegment(sketch, "E5613", {"start": v(-83.99, 56.97) * mm, "end": v(-83.9, 56.82) * mm});
            skLineSegment(sketch, "E5614", {"start": v(-83.9, 56.82) * mm, "end": v(-83.8, 56.67) * mm});
            skLineSegment(sketch, "E5615", {"start": v(-83.8, 56.67) * mm, "end": v(-83.7, 56.52) * mm});
            skLineSegment(sketch, "E5616", {"start": v(-83.7, 56.52) * mm, "end": v(-83.6, 56.38) * mm});
            skLineSegment(sketch, "E5617", {"start": v(-83.6, 56.38) * mm, "end": v(-83.51, 56.23) * mm});
            skLineSegment(sketch, "E5618", {"start": v(-83.51, 56.23) * mm, "end": v(-83.42, 56.09) * mm});
            skLineSegment(sketch, "E5619", {"start": v(-83.42, 56.09) * mm, "end": v(-83.33, 55.95) * mm});
            skLineSegment(sketch, "E5620", {"start": v(-83.33, 55.95) * mm, "end": v(-83.24, 55.8) * mm});
            skLineSegment(sketch, "E5621", {"start": v(-83.24, 55.8) * mm, "end": v(-83.14, 55.67) * mm});
            skLineSegment(sketch, "E5622", {"start": v(-83.14, 55.67) * mm, "end": v(-83.05, 55.54) * mm});
            skLineSegment(sketch, "E5623", {"start": v(-83.05, 55.54) * mm, "end": v(-82.96, 55.4) * mm});
            skLineSegment(sketch, "E5624", {"start": v(-82.96, 55.4) * mm, "end": v(-82.87, 55.27) * mm});
            skLineSegment(sketch, "E5625", {"start": v(-82.87, 55.27) * mm, "end": v(-82.78, 55.14) * mm});
            skLineSegment(sketch, "E5626", {"start": v(-82.78, 55.14) * mm, "end": v(-82.69, 55.02) * mm});
            skLineSegment(sketch, "E5627", {"start": v(-82.69, 55.02) * mm, "end": v(-82.6, 54.89) * mm});
            skLineSegment(sketch, "E5628", {"start": v(-82.6, 54.89) * mm, "end": v(-82.5, 54.77) * mm});
            skLineSegment(sketch, "E5629", {"start": v(-82.5, 54.77) * mm, "end": v(-82.42, 54.64) * mm});
            skLineSegment(sketch, "E5630", {"start": v(-82.42, 54.64) * mm, "end": v(-82.33, 54.52) * mm});
            skLineSegment(sketch, "E5631", {"start": v(-82.33, 54.52) * mm, "end": v(-82.25, 54.4) * mm});
            skLineSegment(sketch, "E5632", {"start": v(-82.25, 54.4) * mm, "end": v(-82.16, 54.29) * mm});
            skLineSegment(sketch, "E5633", {"start": v(-82.16, 54.29) * mm, "end": v(-82.07, 54.17) * mm});
            skLineSegment(sketch, "E5634", {"start": v(-82.07, 54.17) * mm, "end": v(-81.99, 54.06) * mm});
            skLineSegment(sketch, "E5635", {"start": v(-81.99, 54.06) * mm, "end": v(-81.9, 53.95) * mm});
            skLineSegment(sketch, "E5636", {"start": v(-81.9, 53.95) * mm, "end": v(-81.82, 53.84) * mm});
            skLineSegment(sketch, "E5637", {"start": v(-81.82, 53.84) * mm, "end": v(-81.73, 53.73) * mm});
            skLineSegment(sketch, "E5638", {"start": v(-81.73, 53.73) * mm, "end": v(-81.65, 53.63) * mm});
            skLineSegment(sketch, "E5639", {"start": v(-81.65, 53.63) * mm, "end": v(-81.56, 53.52) * mm});
            skLineSegment(sketch, "E5640", {"start": v(-81.56, 53.52) * mm, "end": v(-81.48, 53.42) * mm});
            skLineSegment(sketch, "E5641", {"start": v(-81.48, 53.42) * mm, "end": v(-81.4, 53.32) * mm});
            skLineSegment(sketch, "E5642", {"start": v(-81.4, 53.32) * mm, "end": v(-81.32, 53.22) * mm});
            skLineSegment(sketch, "E5643", {"start": v(-81.32, 53.22) * mm, "end": v(-81.78, 52.4) * mm});
            skLineSegment(sketch, "E5644", {"start": v(-81.78, 52.4) * mm, "end": v(-82.34, 51.63) * mm});
            skLineSegment(sketch, "E5645", {"start": v(-82.34, 51.63) * mm, "end": v(-82.46, 51.66) * mm});
            skLineSegment(sketch, "E5646", {"start": v(-82.46, 51.66) * mm, "end": v(-82.59, 51.7) * mm});
            skLineSegment(sketch, "E5647", {"start": v(-82.59, 51.7) * mm, "end": v(-82.72, 51.73) * mm});
            skLineSegment(sketch, "E5648", {"start": v(-82.72, 51.73) * mm, "end": v(-82.84, 51.76) * mm});
            skLineSegment(sketch, "E5649", {"start": v(-82.84, 51.76) * mm, "end": v(-82.98, 51.79) * mm});
            skLineSegment(sketch, "E5650", {"start": v(-82.98, 51.79) * mm, "end": v(-83.1, 51.82) * mm});
            skLineSegment(sketch, "E5651", {"start": v(-83.1, 51.82) * mm, "end": v(-83.24, 51.85) * mm});
            skLineSegment(sketch, "E5652", {"start": v(-83.24, 51.85) * mm, "end": v(-83.38, 51.88) * mm});
            skLineSegment(sketch, "E5653", {"start": v(-83.38, 51.88) * mm, "end": v(-83.52, 51.91) * mm});
            skLineSegment(sketch, "E5654", {"start": v(-83.52, 51.91) * mm, "end": v(-83.66, 51.94) * mm});
            skLineSegment(sketch, "E5655", {"start": v(-83.66, 51.94) * mm, "end": v(-83.8, 51.97) * mm});
            skLineSegment(sketch, "E5656", {"start": v(-83.8, 51.97) * mm, "end": v(-83.95, 52) * mm});
            skLineSegment(sketch, "E5657", {"start": v(-83.95, 52) * mm, "end": v(-84.1, 52.03) * mm});
            skLineSegment(sketch, "E5658", {"start": v(-84.1, 52.03) * mm, "end": v(-84.24, 52.06) * mm});
            skLineSegment(sketch, "E5659", {"start": v(-84.24, 52.06) * mm, "end": v(-84.4, 52.1) * mm});
            skLineSegment(sketch, "E5660", {"start": v(-84.4, 52.1) * mm, "end": v(-84.54, 52.12) * mm});
            skLineSegment(sketch, "E5661", {"start": v(-84.54, 52.12) * mm, "end": v(-84.7, 52.15) * mm});
            skLineSegment(sketch, "E5662", {"start": v(-84.7, 52.15) * mm, "end": v(-84.85, 52.18) * mm});
            skLineSegment(sketch, "E5663", {"start": v(-84.85, 52.18) * mm, "end": v(-85, 52.2) * mm});
            skLineSegment(sketch, "E5664", {"start": v(-85, 52.2) * mm, "end": v(-85.17, 52.23) * mm});
            skLineSegment(sketch, "E5665", {"start": v(-85.17, 52.23) * mm, "end": v(-85.33, 52.26) * mm});
            skLineSegment(sketch, "E5666", {"start": v(-85.33, 52.26) * mm, "end": v(-85.5, 52.29) * mm});
            skLineSegment(sketch, "E5667", {"start": v(-85.5, 52.29) * mm, "end": v(-85.66, 52.31) * mm});
            skLineSegment(sketch, "E5668", {"start": v(-85.66, 52.31) * mm, "end": v(-85.82, 52.34) * mm});
            skLineSegment(sketch, "E5669", {"start": v(-85.82, 52.34) * mm, "end": v(-86, 52.36) * mm});
            skLineSegment(sketch, "E5670", {"start": v(-86, 52.36) * mm, "end": v(-86.16, 52.39) * mm});
            skLineSegment(sketch, "E5671", {"start": v(-86.16, 52.39) * mm, "end": v(-86.33, 52.41) * mm});
            skLineSegment(sketch, "E5672", {"start": v(-86.33, 52.41) * mm, "end": v(-86.5, 52.44) * mm});
            skLineSegment(sketch, "E5673", {"start": v(-86.5, 52.44) * mm, "end": v(-86.68, 52.46) * mm});
            skLineSegment(sketch, "E5674", {"start": v(-86.68, 52.46) * mm, "end": v(-86.86, 52.48) * mm});
            skLineSegment(sketch, "E5675", {"start": v(-86.86, 52.48) * mm, "end": v(-87.04, 52.5) * mm});
            skLineSegment(sketch, "E5676", {"start": v(-87.04, 52.5) * mm, "end": v(-87.22, 52.53) * mm});
            skLineSegment(sketch, "E5677", {"start": v(-87.22, 52.53) * mm, "end": v(-87.4, 52.55) * mm});
            skLineSegment(sketch, "E5678", {"start": v(-87.4, 52.55) * mm, "end": v(-87.6, 52.57) * mm});
            skLineSegment(sketch, "E5679", {"start": v(-87.6, 52.57) * mm, "end": v(-87.78, 52.59) * mm});
            skLineSegment(sketch, "E5680", {"start": v(-87.78, 52.59) * mm, "end": v(-87.97, 52.6) * mm});
            skLineSegment(sketch, "E5681", {"start": v(-87.97, 52.6) * mm, "end": v(-88.01, 52.54) * mm});
            skLineSegment(sketch, "E5682", {"start": v(-88.01, 52.54) * mm, "end": v(-88.8, 51.18) * mm});
            skLineSegment(sketch, "E5683", {"start": v(-88.8, 51.18) * mm, "end": v(-88.84, 51.11) * mm});
            skLineSegment(sketch, "E5684", {"start": v(-88.84, 51.11) * mm, "end": v(-88.74, 50.96) * mm});
            skLineSegment(sketch, "E5685", {"start": v(-88.74, 50.96) * mm, "end": v(-88.63, 50.8) * mm});
            skLineSegment(sketch, "E5686", {"start": v(-88.63, 50.8) * mm, "end": v(-88.52, 50.65) * mm});
            skLineSegment(sketch, "E5687", {"start": v(-88.52, 50.65) * mm, "end": v(-88.41, 50.5) * mm});
            skLineSegment(sketch, "E5688", {"start": v(-88.41, 50.5) * mm, "end": v(-88.3, 50.35) * mm});
            skLineSegment(sketch, "E5689", {"start": v(-88.3, 50.35) * mm, "end": v(-88.2, 50.2) * mm});
            skLineSegment(sketch, "E5690", {"start": v(-88.2, 50.2) * mm, "end": v(-88.1, 50.06) * mm});
            skLineSegment(sketch, "E5691", {"start": v(-88.1, 50.06) * mm, "end": v(-87.98, 49.92) * mm});
            skLineSegment(sketch, "E5692", {"start": v(-87.98, 49.92) * mm, "end": v(-87.88, 49.78) * mm});
            skLineSegment(sketch, "E5693", {"start": v(-87.88, 49.78) * mm, "end": v(-87.77, 49.64) * mm});
            skLineSegment(sketch, "E5694", {"start": v(-87.77, 49.64) * mm, "end": v(-87.67, 49.5) * mm});
            skLineSegment(sketch, "E5695", {"start": v(-87.67, 49.5) * mm, "end": v(-87.57, 49.37) * mm});
            skLineSegment(sketch, "E5696", {"start": v(-87.57, 49.37) * mm, "end": v(-87.46, 49.24) * mm});
            skLineSegment(sketch, "E5697", {"start": v(-87.46, 49.24) * mm, "end": v(-87.36, 49.1) * mm});
            skLineSegment(sketch, "E5698", {"start": v(-87.36, 49.1) * mm, "end": v(-87.26, 48.98) * mm});
            skLineSegment(sketch, "E5699", {"start": v(-87.26, 48.98) * mm, "end": v(-87.15, 48.85) * mm});
            skLineSegment(sketch, "E5700", {"start": v(-87.15, 48.85) * mm, "end": v(-87.05, 48.72) * mm});
            skLineSegment(sketch, "E5701", {"start": v(-87.05, 48.72) * mm, "end": v(-86.95, 48.6) * mm});
            skLineSegment(sketch, "E5702", {"start": v(-86.95, 48.6) * mm, "end": v(-86.85, 48.48) * mm});
            skLineSegment(sketch, "E5703", {"start": v(-86.85, 48.48) * mm, "end": v(-86.75, 48.36) * mm});
            skLineSegment(sketch, "E5704", {"start": v(-86.75, 48.36) * mm, "end": v(-86.65, 48.24) * mm});
            skLineSegment(sketch, "E5705", {"start": v(-86.65, 48.24) * mm, "end": v(-86.55, 48.12) * mm});
            skLineSegment(sketch, "E5706", {"start": v(-86.55, 48.12) * mm, "end": v(-86.45, 48) * mm});
            skLineSegment(sketch, "E5707", {"start": v(-86.45, 48) * mm, "end": v(-86.36, 47.9) * mm});
            skLineSegment(sketch, "E5708", {"start": v(-86.36, 47.9) * mm, "end": v(-86.26, 47.78) * mm});
            skLineSegment(sketch, "E5709", {"start": v(-86.26, 47.78) * mm, "end": v(-86.16, 47.67) * mm});
            skLineSegment(sketch, "E5710", {"start": v(-86.16, 47.67) * mm, "end": v(-86.07, 47.57) * mm});
            skLineSegment(sketch, "E5711", {"start": v(-86.07, 47.57) * mm, "end": v(-85.97, 47.46) * mm});
            skLineSegment(sketch, "E5712", {"start": v(-85.97, 47.46) * mm, "end": v(-85.88, 47.36) * mm});
            skLineSegment(sketch, "E5713", {"start": v(-85.88, 47.36) * mm, "end": v(-85.79, 47.25) * mm});
            skLineSegment(sketch, "E5714", {"start": v(-85.79, 47.25) * mm, "end": v(-85.7, 47.15) * mm});
            skLineSegment(sketch, "E5715", {"start": v(-85.7, 47.15) * mm, "end": v(-85.6, 47.05) * mm});
            skLineSegment(sketch, "E5716", {"start": v(-85.6, 47.05) * mm, "end": v(-85.51, 46.96) * mm});
            skLineSegment(sketch, "E5717", {"start": v(-85.51, 46.96) * mm, "end": v(-85.42, 46.86) * mm});
            skLineSegment(sketch, "E5718", {"start": v(-85.42, 46.86) * mm, "end": v(-85.33, 46.77) * mm});
            skLineSegment(sketch, "E5719", {"start": v(-85.33, 46.77) * mm, "end": v(-85.24, 46.67) * mm});
            skLineSegment(sketch, "E5720", {"start": v(-85.24, 46.67) * mm, "end": v(-85.64, 45.82) * mm});
            skLineSegment(sketch, "E5721", {"start": v(-85.64, 45.82) * mm, "end": v(-86.13, 45.01) * mm});
            skLineSegment(sketch, "E5722", {"start": v(-86.13, 45.01) * mm, "end": v(-86.26, 45.03) * mm});
            skLineSegment(sketch, "E5723", {"start": v(-86.26, 45.03) * mm, "end": v(-86.39, 45.05) * mm});
            skLineSegment(sketch, "E5724", {"start": v(-86.39, 45.05) * mm, "end": v(-86.52, 45.08) * mm});
            skLineSegment(sketch, "E5725", {"start": v(-86.52, 45.08) * mm, "end": v(-86.65, 45.1) * mm});
            skLineSegment(sketch, "E5726", {"start": v(-86.65, 45.1) * mm, "end": v(-86.78, 45.12) * mm});
            skLineSegment(sketch, "E5727", {"start": v(-86.78, 45.12) * mm, "end": v(-86.92, 45.14) * mm});
            skLineSegment(sketch, "E5728", {"start": v(-86.92, 45.14) * mm, "end": v(-87.06, 45.16) * mm});
            skLineSegment(sketch, "E5729", {"start": v(-87.06, 45.16) * mm, "end": v(-87.2, 45.18) * mm});
            skLineSegment(sketch, "E5730", {"start": v(-87.2, 45.18) * mm, "end": v(-87.34, 45.2) * mm});
            skLineSegment(sketch, "E5731", {"start": v(-87.34, 45.2) * mm, "end": v(-87.48, 45.22) * mm});
            skLineSegment(sketch, "E5732", {"start": v(-87.48, 45.22) * mm, "end": v(-87.62, 45.24) * mm});
            skLineSegment(sketch, "E5733", {"start": v(-87.62, 45.24) * mm, "end": v(-87.77, 45.26) * mm});
            skLineSegment(sketch, "E5734", {"start": v(-87.77, 45.26) * mm, "end": v(-87.92, 45.28) * mm});
            skLineSegment(sketch, "E5735", {"start": v(-87.92, 45.28) * mm, "end": v(-88.07, 45.3) * mm});
            skLineSegment(sketch, "E5736", {"start": v(-88.07, 45.3) * mm, "end": v(-88.22, 45.31) * mm});
            skLineSegment(sketch, "E5737", {"start": v(-88.22, 45.31) * mm, "end": v(-88.37, 45.33) * mm});
            skLineSegment(sketch, "E5738", {"start": v(-88.37, 45.33) * mm, "end": v(-88.53, 45.34) * mm});
            skLineSegment(sketch, "E5739", {"start": v(-88.53, 45.34) * mm, "end": v(-88.68, 45.36) * mm});
            skLineSegment(sketch, "E5740", {"start": v(-88.68, 45.36) * mm, "end": v(-88.84, 45.38) * mm});
            skLineSegment(sketch, "E5741", {"start": v(-88.84, 45.38) * mm, "end": v(-89, 45.4) * mm});
            skLineSegment(sketch, "E5742", {"start": v(-89, 45.4) * mm, "end": v(-89.17, 45.4) * mm});
            skLineSegment(sketch, "E5743", {"start": v(-89.17, 45.4) * mm, "end": v(-89.33, 45.42) * mm});
            skLineSegment(sketch, "E5744", {"start": v(-89.33, 45.42) * mm, "end": v(-89.5, 45.43) * mm});
            skLineSegment(sketch, "E5745", {"start": v(-89.5, 45.43) * mm, "end": v(-89.67, 45.44) * mm});
            skLineSegment(sketch, "E5746", {"start": v(-89.67, 45.44) * mm, "end": v(-89.84, 45.46) * mm});
            skLineSegment(sketch, "E5747", {"start": v(-89.84, 45.46) * mm, "end": v(-90, 45.47) * mm});
            skLineSegment(sketch, "E5748", {"start": v(-90, 45.47) * mm, "end": v(-90.18, 45.48) * mm});
            skLineSegment(sketch, "E5749", {"start": v(-90.18, 45.48) * mm, "end": v(-90.36, 45.49) * mm});
            skLineSegment(sketch, "E5750", {"start": v(-90.36, 45.49) * mm, "end": v(-90.53, 45.5) * mm});
            skLineSegment(sketch, "E5751", {"start": v(-90.53, 45.5) * mm, "end": v(-90.71, 45.5) * mm});
            skLineSegment(sketch, "E5752", {"start": v(-90.71, 45.5) * mm, "end": v(-90.9, 45.51) * mm});
            skLineSegment(sketch, "E5753", {"start": v(-90.9, 45.51) * mm, "end": v(-91.08, 45.52) * mm});
            skLineSegment(sketch, "E5754", {"start": v(-91.08, 45.52) * mm, "end": v(-91.26, 45.53) * mm});
            skLineSegment(sketch, "E5755", {"start": v(-91.26, 45.53) * mm, "end": v(-91.45, 45.53) * mm});
            skLineSegment(sketch, "E5756", {"start": v(-91.45, 45.53) * mm, "end": v(-91.63, 45.54) * mm});
            skLineSegment(sketch, "E5757", {"start": v(-91.63, 45.54) * mm, "end": v(-91.82, 45.54) * mm});
            skLineSegment(sketch, "E5758", {"start": v(-91.82, 45.54) * mm, "end": v(-91.86, 45.47) * mm});
            skLineSegment(sketch, "E5759", {"start": v(-91.86, 45.47) * mm, "end": v(-92.55, 44.06) * mm});
            skLineSegment(sketch, "E5760", {"start": v(-92.55, 44.06) * mm, "end": v(-92.58, 43.98) * mm});
            skLineSegment(sketch, "E5761", {"start": v(-92.58, 43.98) * mm, "end": v(-92.46, 43.84) * mm});
            skLineSegment(sketch, "E5762", {"start": v(-92.46, 43.84) * mm, "end": v(-92.34, 43.7) * mm});
            skLineSegment(sketch, "E5763", {"start": v(-92.34, 43.7) * mm, "end": v(-92.22, 43.55) * mm});
            skLineSegment(sketch, "E5764", {"start": v(-92.22, 43.55) * mm, "end": v(-92.1, 43.4) * mm});
            skLineSegment(sketch, "E5765", {"start": v(-92.1, 43.4) * mm, "end": v(-91.98, 43.27) * mm});
            skLineSegment(sketch, "E5766", {"start": v(-91.98, 43.27) * mm, "end": v(-91.86, 43.13) * mm});
            skLineSegment(sketch, "E5767", {"start": v(-91.86, 43.13) * mm, "end": v(-91.75, 43) * mm});
            skLineSegment(sketch, "E5768", {"start": v(-91.75, 43) * mm, "end": v(-91.63, 42.86) * mm});
            skLineSegment(sketch, "E5769", {"start": v(-91.63, 42.86) * mm, "end": v(-91.51, 42.73) * mm});
            skLineSegment(sketch, "E5770", {"start": v(-91.51, 42.73) * mm, "end": v(-91.4, 42.6) * mm});
            skLineSegment(sketch, "E5771", {"start": v(-91.4, 42.6) * mm, "end": v(-91.28, 42.47) * mm});
            skLineSegment(sketch, "E5772", {"start": v(-91.28, 42.47) * mm, "end": v(-91.17, 42.35) * mm});
            skLineSegment(sketch, "E5773", {"start": v(-91.17, 42.35) * mm, "end": v(-91.05, 42.22) * mm});
            skLineSegment(sketch, "E5774", {"start": v(-91.05, 42.22) * mm, "end": v(-90.94, 42.1) * mm});
            skLineSegment(sketch, "E5775", {"start": v(-90.94, 42.1) * mm, "end": v(-90.83, 41.98) * mm});
            skLineSegment(sketch, "E5776", {"start": v(-90.83, 41.98) * mm, "end": v(-90.72, 41.86) * mm});
            skLineSegment(sketch, "E5777", {"start": v(-90.72, 41.86) * mm, "end": v(-90.6, 41.74) * mm});
            skLineSegment(sketch, "E5778", {"start": v(-90.6, 41.74) * mm, "end": v(-90.5, 41.63) * mm});
            skLineSegment(sketch, "E5779", {"start": v(-90.5, 41.63) * mm, "end": v(-90.39, 41.51) * mm});
            skLineSegment(sketch, "E5780", {"start": v(-90.39, 41.51) * mm, "end": v(-90.28, 41.4) * mm});
            skLineSegment(sketch, "E5781", {"start": v(-90.28, 41.4) * mm, "end": v(-90.17, 41.3) * mm});
            skLineSegment(sketch, "E5782", {"start": v(-90.17, 41.3) * mm, "end": v(-90.06, 41.18) * mm});
            skLineSegment(sketch, "E5783", {"start": v(-90.06, 41.18) * mm, "end": v(-89.95, 41.08) * mm});
            skLineSegment(sketch, "E5784", {"start": v(-89.95, 41.08) * mm, "end": v(-89.85, 40.97) * mm});
            skLineSegment(sketch, "E5785", {"start": v(-89.85, 40.97) * mm, "end": v(-89.74, 40.87) * mm});
            skLineSegment(sketch, "E5786", {"start": v(-89.74, 40.87) * mm, "end": v(-89.64, 40.77) * mm});
            skLineSegment(sketch, "E5787", {"start": v(-89.64, 40.77) * mm, "end": v(-89.54, 40.67) * mm});
            skLineSegment(sketch, "E5788", {"start": v(-89.54, 40.67) * mm, "end": v(-89.43, 40.57) * mm});
            skLineSegment(sketch, "E5789", {"start": v(-89.43, 40.57) * mm, "end": v(-89.33, 40.47) * mm});
            skLineSegment(sketch, "E5790", {"start": v(-89.33, 40.47) * mm, "end": v(-89.23, 40.38) * mm});
            skLineSegment(sketch, "E5791", {"start": v(-89.23, 40.38) * mm, "end": v(-89.13, 40.28) * mm});
            skLineSegment(sketch, "E5792", {"start": v(-89.13, 40.28) * mm, "end": v(-89.03, 40.2) * mm});
            skLineSegment(sketch, "E5793", {"start": v(-89.03, 40.2) * mm, "end": v(-88.93, 40.1) * mm});
            skLineSegment(sketch, "E5794", {"start": v(-88.93, 40.1) * mm, "end": v(-88.84, 40.01) * mm});
            skLineSegment(sketch, "E5795", {"start": v(-88.84, 40.01) * mm, "end": v(-88.74, 39.93) * mm});
            skLineSegment(sketch, "E5796", {"start": v(-88.74, 39.93) * mm, "end": v(-88.64, 39.84) * mm});
            skLineSegment(sketch, "E5797", {"start": v(-88.64, 39.84) * mm, "end": v(-88.97, 38.96) * mm});
            skLineSegment(sketch, "E5798", {"start": v(-88.97, 38.96) * mm, "end": v(-89.4, 38.11) * mm});
            skLineSegment(sketch, "E5799", {"start": v(-89.4, 38.11) * mm, "end": v(-89.53, 38.13) * mm});
            skLineSegment(sketch, "E5800", {"start": v(-89.53, 38.13) * mm, "end": v(-89.66, 38.14) * mm});
            skLineSegment(sketch, "E5801", {"start": v(-89.66, 38.14) * mm, "end": v(-89.79, 38.15) * mm});
            skLineSegment(sketch, "E5802", {"start": v(-89.79, 38.15) * mm, "end": v(-89.92, 38.16) * mm});
            skLineSegment(sketch, "E5803", {"start": v(-89.92, 38.16) * mm, "end": v(-90.06, 38.17) * mm});
            skLineSegment(sketch, "E5804", {"start": v(-90.06, 38.17) * mm, "end": v(-90.2, 38.18) * mm});
            skLineSegment(sketch, "E5805", {"start": v(-90.2, 38.18) * mm, "end": v(-90.33, 38.2) * mm});
            skLineSegment(sketch, "E5806", {"start": v(-90.33, 38.2) * mm, "end": v(-90.47, 38.2) * mm});
            skLineSegment(sketch, "E5807", {"start": v(-90.47, 38.2) * mm, "end": v(-90.61, 38.2) * mm});
            skLineSegment(sketch, "E5808", {"start": v(-90.61, 38.2) * mm, "end": v(-90.76, 38.22) * mm});
            skLineSegment(sketch, "E5809", {"start": v(-90.76, 38.22) * mm, "end": v(-90.9, 38.22) * mm});
            skLineSegment(sketch, "E5810", {"start": v(-90.9, 38.22) * mm, "end": v(-91.05, 38.23) * mm});
            skLineSegment(sketch, "E5811", {"start": v(-91.05, 38.23) * mm, "end": v(-91.2, 38.24) * mm});
            skLineSegment(sketch, "E5812", {"start": v(-91.2, 38.24) * mm, "end": v(-91.35, 38.24) * mm});
            skLineSegment(sketch, "E5813", {"start": v(-91.35, 38.24) * mm, "end": v(-91.5, 38.25) * mm});
            skLineSegment(sketch, "E5814", {"start": v(-91.5, 38.25) * mm, "end": v(-91.66, 38.25) * mm});
            skLineSegment(sketch, "E5815", {"start": v(-91.66, 38.25) * mm, "end": v(-91.81, 38.26) * mm});
            skLineSegment(sketch, "E5816", {"start": v(-91.81, 38.26) * mm, "end": v(-91.97, 38.26) * mm});
            skLineSegment(sketch, "E5817", {"start": v(-91.97, 38.26) * mm, "end": v(-92.13, 38.27) * mm});
            skLineSegment(sketch, "E5818", {"start": v(-92.13, 38.27) * mm, "end": v(-92.3, 38.27) * mm});
            skLineSegment(sketch, "E5819", {"start": v(-92.3, 38.27) * mm, "end": v(-92.45, 38.27) * mm});
            skLineSegment(sketch, "E5820", {"start": v(-92.45, 38.27) * mm, "end": v(-92.62, 38.27) * mm});
            skLineSegment(sketch, "E5821", {"start": v(-92.62, 38.27) * mm, "end": v(-92.79, 38.27) * mm});
            skLineSegment(sketch, "E5822", {"start": v(-92.79, 38.27) * mm, "end": v(-92.95, 38.27) * mm});
            skLineSegment(sketch, "E5823", {"start": v(-92.95, 38.27) * mm, "end": v(-93.12, 38.27) * mm});
            skLineSegment(sketch, "E5824", {"start": v(-93.12, 38.27) * mm, "end": v(-93.3, 38.27) * mm});
            skLineSegment(sketch, "E5825", {"start": v(-93.3, 38.27) * mm, "end": v(-93.47, 38.26) * mm});
            skLineSegment(sketch, "E5826", {"start": v(-93.47, 38.26) * mm, "end": v(-93.65, 38.26) * mm});
            skLineSegment(sketch, "E5827", {"start": v(-93.65, 38.26) * mm, "end": v(-93.82, 38.25) * mm});
            skLineSegment(sketch, "E5828", {"start": v(-93.82, 38.25) * mm, "end": v(-94, 38.25) * mm});
            skLineSegment(sketch, "E5829", {"start": v(-94, 38.25) * mm, "end": v(-94.18, 38.24) * mm});
            skLineSegment(sketch, "E5830", {"start": v(-94.18, 38.24) * mm, "end": v(-94.37, 38.24) * mm});
            skLineSegment(sketch, "E5831", {"start": v(-94.37, 38.24) * mm, "end": v(-94.55, 38.23) * mm});
            skLineSegment(sketch, "E5832", {"start": v(-94.55, 38.23) * mm, "end": v(-94.74, 38.22) * mm});
            skLineSegment(sketch, "E5833", {"start": v(-94.74, 38.22) * mm, "end": v(-94.92, 38.2) * mm});
            skLineSegment(sketch, "E5834", {"start": v(-94.92, 38.2) * mm, "end": v(-95.11, 38.2) * mm});
            skLineSegment(sketch, "E5835", {"start": v(-95.11, 38.2) * mm, "end": v(-95.15, 38.12) * mm});
            skLineSegment(sketch, "E5836", {"start": v(-95.15, 38.12) * mm, "end": v(-95.72, 36.66) * mm});
            skLineSegment(sketch, "E5837", {"start": v(-95.72, 36.66) * mm, "end": v(-95.75, 36.58) * mm});
            skLineSegment(sketch, "E5838", {"start": v(-95.75, 36.58) * mm, "end": v(-95.61, 36.45) * mm});
            skLineSegment(sketch, "E5839", {"start": v(-95.61, 36.45) * mm, "end": v(-95.48, 36.31) * mm});
            skLineSegment(sketch, "E5840", {"start": v(-95.48, 36.31) * mm, "end": v(-95.35, 36.18) * mm});
            skLineSegment(sketch, "E5841", {"start": v(-95.35, 36.18) * mm, "end": v(-95.22, 36.05) * mm});
            skLineSegment(sketch, "E5842", {"start": v(-95.22, 36.05) * mm, "end": v(-95.1, 35.92) * mm});
            skLineSegment(sketch, "E5843", {"start": v(-95.1, 35.92) * mm, "end": v(-94.97, 35.8) * mm});
            skLineSegment(sketch, "E5844", {"start": v(-94.97, 35.8) * mm, "end": v(-94.84, 35.67) * mm});
            skLineSegment(sketch, "E5845", {"start": v(-94.84, 35.67) * mm, "end": v(-94.71, 35.54) * mm});
            skLineSegment(sketch, "E5846", {"start": v(-94.71, 35.54) * mm, "end": v(-94.58, 35.42) * mm});
            skLineSegment(sketch, "E5847", {"start": v(-94.58, 35.42) * mm, "end": v(-94.46, 35.3) * mm});
            skLineSegment(sketch, "E5848", {"start": v(-94.46, 35.3) * mm, "end": v(-94.33, 35.18) * mm});
            skLineSegment(sketch, "E5849", {"start": v(-94.33, 35.18) * mm, "end": v(-94.21, 35.06) * mm});
            skLineSegment(sketch, "E5850", {"start": v(-94.21, 35.06) * mm, "end": v(-94.09, 34.95) * mm});
            skLineSegment(sketch, "E5851", {"start": v(-94.09, 34.95) * mm, "end": v(-93.96, 34.84) * mm});
            skLineSegment(sketch, "E5852", {"start": v(-93.96, 34.84) * mm, "end": v(-93.84, 34.72) * mm});
            skLineSegment(sketch, "E5853", {"start": v(-93.84, 34.72) * mm, "end": v(-93.72, 34.61) * mm});
            skLineSegment(sketch, "E5854", {"start": v(-93.72, 34.61) * mm, "end": v(-93.6, 34.5) * mm});
            skLineSegment(sketch, "E5855", {"start": v(-93.6, 34.5) * mm, "end": v(-93.48, 34.4) * mm});
            skLineSegment(sketch, "E5856", {"start": v(-93.48, 34.4) * mm, "end": v(-93.36, 34.3) * mm});
            skLineSegment(sketch, "E5857", {"start": v(-93.36, 34.3) * mm, "end": v(-93.25, 34.2) * mm});
            skLineSegment(sketch, "E5858", {"start": v(-93.25, 34.2) * mm, "end": v(-93.13, 34.1) * mm});
            skLineSegment(sketch, "E5859", {"start": v(-93.13, 34.1) * mm, "end": v(-93.02, 34) * mm});
            skLineSegment(sketch, "E5860", {"start": v(-93.02, 34) * mm, "end": v(-92.9, 33.9) * mm});
            skLineSegment(sketch, "E5861", {"start": v(-92.9, 33.9) * mm, "end": v(-92.79, 33.8) * mm});
            skLineSegment(sketch, "E5862", {"start": v(-92.79, 33.8) * mm, "end": v(-92.67, 33.7) * mm});
            skLineSegment(sketch, "E5863", {"start": v(-92.67, 33.7) * mm, "end": v(-92.56, 33.6) * mm});
            skLineSegment(sketch, "E5864", {"start": v(-92.56, 33.6) * mm, "end": v(-92.45, 33.52) * mm});
            skLineSegment(sketch, "E5865", {"start": v(-92.45, 33.52) * mm, "end": v(-92.34, 33.43) * mm});
            skLineSegment(sketch, "E5866", {"start": v(-92.34, 33.43) * mm, "end": v(-92.23, 33.34) * mm});
            skLineSegment(sketch, "E5867", {"start": v(-92.23, 33.34) * mm, "end": v(-92.12, 33.25) * mm});
            skLineSegment(sketch, "E5868", {"start": v(-92.12, 33.25) * mm, "end": v(-92.02, 33.17) * mm});
            skLineSegment(sketch, "E5869", {"start": v(-92.02, 33.17) * mm, "end": v(-91.91, 33.08) * mm});
            skLineSegment(sketch, "E5870", {"start": v(-91.91, 33.08) * mm, "end": v(-91.8, 33) * mm});
            skLineSegment(sketch, "E5871", {"start": v(-91.8, 33) * mm, "end": v(-91.7, 32.92) * mm});
            skLineSegment(sketch, "E5872", {"start": v(-91.7, 32.92) * mm, "end": v(-91.6, 32.84) * mm});
            skLineSegment(sketch, "E5873", {"start": v(-91.6, 32.84) * mm, "end": v(-91.5, 32.76) * mm});
            skLineSegment(sketch, "E5874", {"start": v(-91.5, 32.76) * mm, "end": v(-91.75, 31.85) * mm});
            skLineSegment(sketch, "E5875", {"start": v(-91.75, 31.85) * mm, "end": v(-92.12, 30.98) * mm});
            skLineSegment(sketch, "E5876", {"start": v(-92.12, 30.98) * mm, "end": v(-92.24, 30.98) * mm});
            skLineSegment(sketch, "E5877", {"start": v(-92.24, 30.98) * mm, "end": v(-92.37, 30.99) * mm});
            skLineSegment(sketch, "E5878", {"start": v(-92.37, 30.99) * mm, "end": v(-92.5, 30.99) * mm});
            skLineSegment(sketch, "E5879", {"start": v(-92.5, 30.99) * mm, "end": v(-92.64, 30.99) * mm});
            skLineSegment(sketch, "E5880", {"start": v(-92.64, 30.99) * mm, "end": v(-92.77, 30.99) * mm});
            skLineSegment(sketch, "E5881", {"start": v(-92.77, 30.99) * mm, "end": v(-92.9, 30.99) * mm});
            skLineSegment(sketch, "E5882", {"start": v(-92.9, 30.99) * mm, "end": v(-93.05, 30.99) * mm});
            skLineSegment(sketch, "E5883", {"start": v(-93.05, 30.99) * mm, "end": v(-93.19, 30.98) * mm});
            skLineSegment(sketch, "E5884", {"start": v(-93.19, 30.98) * mm, "end": v(-93.33, 30.98) * mm});
            skLineSegment(sketch, "E5885", {"start": v(-93.33, 30.98) * mm, "end": v(-93.47, 30.98) * mm});
            skLineSegment(sketch, "E5886", {"start": v(-93.47, 30.98) * mm, "end": v(-93.62, 30.98) * mm});
            skLineSegment(sketch, "E5887", {"start": v(-93.62, 30.98) * mm, "end": v(-93.77, 30.97) * mm});
            skLineSegment(sketch, "E5888", {"start": v(-93.77, 30.97) * mm, "end": v(-93.92, 30.97) * mm});
            skLineSegment(sketch, "E5889", {"start": v(-93.92, 30.97) * mm, "end": v(-94.07, 30.96) * mm});
            skLineSegment(sketch, "E5890", {"start": v(-94.07, 30.96) * mm, "end": v(-94.22, 30.95) * mm});
            skLineSegment(sketch, "E5891", {"start": v(-94.22, 30.95) * mm, "end": v(-94.37, 30.95) * mm});
            skLineSegment(sketch, "E5892", {"start": v(-94.37, 30.95) * mm, "end": v(-94.53, 30.94) * mm});
            skLineSegment(sketch, "E5893", {"start": v(-94.53, 30.94) * mm, "end": v(-94.69, 30.93) * mm});
            skLineSegment(sketch, "E5894", {"start": v(-94.69, 30.93) * mm, "end": v(-94.85, 30.92) * mm});
            skLineSegment(sketch, "E5895", {"start": v(-94.85, 30.92) * mm, "end": v(-95, 30.9) * mm});
            skLineSegment(sketch, "E5896", {"start": v(-95, 30.9) * mm, "end": v(-95.17, 30.9) * mm});
            skLineSegment(sketch, "E5897", {"start": v(-95.17, 30.9) * mm, "end": v(-95.34, 30.88) * mm});
            skLineSegment(sketch, "E5898", {"start": v(-95.34, 30.88) * mm, "end": v(-95.5, 30.87) * mm});
            skLineSegment(sketch, "E5899", {"start": v(-95.5, 30.87) * mm, "end": v(-95.67, 30.86) * mm});
            skLineSegment(sketch, "E5900", {"start": v(-95.67, 30.86) * mm, "end": v(-95.84, 30.84) * mm});
            skLineSegment(sketch, "E5901", {"start": v(-95.84, 30.84) * mm, "end": v(-96.01, 30.83) * mm});
            skLineSegment(sketch, "E5902", {"start": v(-96.01, 30.83) * mm, "end": v(-96.18, 30.81) * mm});
            skLineSegment(sketch, "E5903", {"start": v(-96.18, 30.81) * mm, "end": v(-96.36, 30.8) * mm});
            skLineSegment(sketch, "E5904", {"start": v(-96.36, 30.8) * mm, "end": v(-96.54, 30.78) * mm});
            skLineSegment(sketch, "E5905", {"start": v(-96.54, 30.78) * mm, "end": v(-96.71, 30.76) * mm});
            skLineSegment(sketch, "E5906", {"start": v(-96.71, 30.76) * mm, "end": v(-96.9, 30.74) * mm});
            skLineSegment(sketch, "E5907", {"start": v(-96.9, 30.74) * mm, "end": v(-97.08, 30.71) * mm});
            skLineSegment(sketch, "E5908", {"start": v(-97.08, 30.71) * mm, "end": v(-97.26, 30.7) * mm});
            skLineSegment(sketch, "E5909", {"start": v(-97.26, 30.7) * mm, "end": v(-97.44, 30.67) * mm});
            skLineSegment(sketch, "E5910", {"start": v(-97.44, 30.67) * mm, "end": v(-97.63, 30.64) * mm});
            skLineSegment(sketch, "E5911", {"start": v(-97.63, 30.64) * mm, "end": v(-97.82, 30.62) * mm});
            skLineSegment(sketch, "E5912", {"start": v(-97.82, 30.62) * mm, "end": v(-97.84, 30.54) * mm});
            skLineSegment(sketch, "E5913", {"start": v(-97.84, 30.54) * mm, "end": v(-98.3, 29.04) * mm});
            skLineSegment(sketch, "E5914", {"start": v(-98.3, 29.04) * mm, "end": v(-98.32, 28.96) * mm});
            skLineSegment(sketch, "E5915", {"start": v(-98.32, 28.96) * mm, "end": v(-98.18, 28.83) * mm});
            skLineSegment(sketch, "E5916", {"start": v(-98.18, 28.83) * mm, "end": v(-98.04, 28.7) * mm});
            skLineSegment(sketch, "E5917", {"start": v(-98.04, 28.7) * mm, "end": v(-97.9, 28.59) * mm});
            skLineSegment(sketch, "E5918", {"start": v(-97.9, 28.59) * mm, "end": v(-97.76, 28.47) * mm});
            skLineSegment(sketch, "E5919", {"start": v(-97.76, 28.47) * mm, "end": v(-97.62, 28.35) * mm});
            skLineSegment(sketch, "E5920", {"start": v(-97.62, 28.35) * mm, "end": v(-97.48, 28.23) * mm});
            skLineSegment(sketch, "E5921", {"start": v(-97.48, 28.23) * mm, "end": v(-97.34, 28.11) * mm});
            skLineSegment(sketch, "E5922", {"start": v(-97.34, 28.11) * mm, "end": v(-97.2, 28) * mm});
            skLineSegment(sketch, "E5923", {"start": v(-97.2, 28) * mm, "end": v(-97.07, 27.89) * mm});
            skLineSegment(sketch, "E5924", {"start": v(-97.07, 27.89) * mm, "end": v(-96.94, 27.78) * mm});
            skLineSegment(sketch, "E5925", {"start": v(-96.94, 27.78) * mm, "end": v(-96.8, 27.67) * mm});
            skLineSegment(sketch, "E5926", {"start": v(-96.8, 27.67) * mm, "end": v(-96.67, 27.56) * mm});
            skLineSegment(sketch, "E5927", {"start": v(-96.67, 27.56) * mm, "end": v(-96.54, 27.46) * mm});
            skLineSegment(sketch, "E5928", {"start": v(-96.54, 27.46) * mm, "end": v(-96.4, 27.36) * mm});
            skLineSegment(sketch, "E5929", {"start": v(-96.4, 27.36) * mm, "end": v(-96.28, 27.25) * mm});
            skLineSegment(sketch, "E5930", {"start": v(-96.28, 27.25) * mm, "end": v(-96.15, 27.15) * mm});
            skLineSegment(sketch, "E5931", {"start": v(-96.15, 27.15) * mm, "end": v(-96.02, 27.06) * mm});
            skLineSegment(sketch, "E5932", {"start": v(-96.02, 27.06) * mm, "end": v(-95.9, 26.96) * mm});
            skLineSegment(sketch, "E5933", {"start": v(-95.9, 26.96) * mm, "end": v(-95.77, 26.86) * mm});
            skLineSegment(sketch, "E5934", {"start": v(-95.77, 26.86) * mm, "end": v(-95.64, 26.77) * mm});
            skLineSegment(sketch, "E5935", {"start": v(-95.64, 26.77) * mm, "end": v(-95.52, 26.68) * mm});
            skLineSegment(sketch, "E5936", {"start": v(-95.52, 26.68) * mm, "end": v(-95.4, 26.59) * mm});
            skLineSegment(sketch, "E5937", {"start": v(-95.4, 26.59) * mm, "end": v(-95.27, 26.5) * mm});
            skLineSegment(sketch, "E5938", {"start": v(-95.27, 26.5) * mm, "end": v(-95.15, 26.41) * mm});
            skLineSegment(sketch, "E5939", {"start": v(-95.15, 26.41) * mm, "end": v(-95.03, 26.33) * mm});
            skLineSegment(sketch, "E5940", {"start": v(-95.03, 26.33) * mm, "end": v(-94.91, 26.24) * mm});
            skLineSegment(sketch, "E5941", {"start": v(-94.91, 26.24) * mm, "end": v(-94.8, 26.16) * mm});
            skLineSegment(sketch, "E5942", {"start": v(-94.8, 26.16) * mm, "end": v(-94.68, 26.08) * mm});
            skLineSegment(sketch, "E5943", {"start": v(-94.68, 26.08) * mm, "end": v(-94.56, 26) * mm});
            skLineSegment(sketch, "E5944", {"start": v(-94.56, 26) * mm, "end": v(-94.45, 25.92) * mm});
            skLineSegment(sketch, "E5945", {"start": v(-94.45, 25.92) * mm, "end": v(-94.34, 25.85) * mm});
            skLineSegment(sketch, "E5946", {"start": v(-94.34, 25.85) * mm, "end": v(-94.22, 25.77) * mm});
            skLineSegment(sketch, "E5947", {"start": v(-94.22, 25.77) * mm, "end": v(-94.11, 25.7) * mm});
            skLineSegment(sketch, "E5948", {"start": v(-94.11, 25.7) * mm, "end": v(-94, 25.62) * mm});
            skLineSegment(sketch, "E5949", {"start": v(-94, 25.62) * mm, "end": v(-93.9, 25.55) * mm});
            skLineSegment(sketch, "E5950", {"start": v(-93.9, 25.55) * mm, "end": v(-93.79, 25.48) * mm});
            skLineSegment(sketch, "E5951", {"start": v(-93.79, 25.48) * mm, "end": v(-93.97, 24.56) * mm});
            skLineSegment(sketch, "E5952", {"start": v(-93.97, 24.56) * mm, "end": v(-94.26, 23.66) * mm});
            skLineSegment(sketch, "E5953", {"start": v(-94.26, 23.66) * mm, "end": v(-94.4, 23.65) * mm});
            skLineSegment(sketch, "E5954", {"start": v(-94.4, 23.65) * mm, "end": v(-94.52, 23.64) * mm});
            skLineSegment(sketch, "E5955", {"start": v(-94.52, 23.64) * mm, "end": v(-94.65, 23.63) * mm});
            skLineSegment(sketch, "E5956", {"start": v(-94.65, 23.63) * mm, "end": v(-94.78, 23.62) * mm});
            skLineSegment(sketch, "E5957", {"start": v(-94.78, 23.62) * mm, "end": v(-94.92, 23.61) * mm});
            skLineSegment(sketch, "E5958", {"start": v(-94.92, 23.61) * mm, "end": v(-95.05, 23.6) * mm});
            skLineSegment(sketch, "E5959", {"start": v(-95.05, 23.6) * mm, "end": v(-95.2, 23.6) * mm});
            skLineSegment(sketch, "E5960", {"start": v(-95.2, 23.6) * mm, "end": v(-95.33, 23.58) * mm});
            skLineSegment(sketch, "E5961", {"start": v(-95.33, 23.58) * mm, "end": v(-95.47, 23.56) * mm});
            skLineSegment(sketch, "E5962", {"start": v(-95.47, 23.56) * mm, "end": v(-95.62, 23.55) * mm});
            skLineSegment(sketch, "E5963", {"start": v(-95.62, 23.55) * mm, "end": v(-95.76, 23.53) * mm});
            skLineSegment(sketch, "E5964", {"start": v(-95.76, 23.53) * mm, "end": v(-95.9, 23.52) * mm});
            skLineSegment(sketch, "E5965", {"start": v(-95.9, 23.52) * mm, "end": v(-96.06, 23.5) * mm});
            skLineSegment(sketch, "E5966", {"start": v(-96.06, 23.5) * mm, "end": v(-96.2, 23.48) * mm});
            skLineSegment(sketch, "E5967", {"start": v(-96.2, 23.48) * mm, "end": v(-96.36, 23.47) * mm});
            skLineSegment(sketch, "E5968", {"start": v(-96.36, 23.47) * mm, "end": v(-96.51, 23.45) * mm});
            skLineSegment(sketch, "E5969", {"start": v(-96.51, 23.45) * mm, "end": v(-96.67, 23.43) * mm});
            skLineSegment(sketch, "E5970", {"start": v(-96.67, 23.43) * mm, "end": v(-96.82, 23.4) * mm});
            skLineSegment(sketch, "E5971", {"start": v(-96.82, 23.4) * mm, "end": v(-96.98, 23.38) * mm});
            skLineSegment(sketch, "E5972", {"start": v(-96.98, 23.38) * mm, "end": v(-97.14, 23.36) * mm});
            skLineSegment(sketch, "E5973", {"start": v(-97.14, 23.36) * mm, "end": v(-97.3, 23.33) * mm});
            skLineSegment(sketch, "E5974", {"start": v(-97.3, 23.33) * mm, "end": v(-97.47, 23.3) * mm});
            skLineSegment(sketch, "E5975", {"start": v(-97.47, 23.3) * mm, "end": v(-97.63, 23.28) * mm});
            skLineSegment(sketch, "E5976", {"start": v(-97.63, 23.28) * mm, "end": v(-97.8, 23.26) * mm});
            skLineSegment(sketch, "E5977", {"start": v(-97.8, 23.26) * mm, "end": v(-97.96, 23.23) * mm});
            skLineSegment(sketch, "E5978", {"start": v(-97.96, 23.23) * mm, "end": v(-98.13, 23.2) * mm});
            skLineSegment(sketch, "E5979", {"start": v(-98.13, 23.2) * mm, "end": v(-98.3, 23.17) * mm});
            skLineSegment(sketch, "E5980", {"start": v(-98.3, 23.17) * mm, "end": v(-98.48, 23.14) * mm});
            skLineSegment(sketch, "E5981", {"start": v(-98.48, 23.14) * mm, "end": v(-98.65, 23.1) * mm});
            skLineSegment(sketch, "E5982", {"start": v(-98.65, 23.1) * mm, "end": v(-98.83, 23.07) * mm});
            skLineSegment(sketch, "E5983", {"start": v(-98.83, 23.07) * mm, "end": v(-99, 23.04) * mm});
            skLineSegment(sketch, "E5984", {"start": v(-99, 23.04) * mm, "end": v(-99.19, 23) * mm});
            skLineSegment(sketch, "E5985", {"start": v(-99.19, 23) * mm, "end": v(-99.37, 22.97) * mm});
            skLineSegment(sketch, "E5986", {"start": v(-99.37, 22.97) * mm, "end": v(-99.55, 22.93) * mm});
            skLineSegment(sketch, "E5987", {"start": v(-99.55, 22.93) * mm, "end": v(-99.73, 22.89) * mm});
            skLineSegment(sketch, "E5988", {"start": v(-99.73, 22.89) * mm, "end": v(-99.92, 22.85) * mm});
            skLineSegment(sketch, "E5989", {"start": v(-99.92, 22.85) * mm, "end": v(-99.94, 22.77) * mm});
            skLineSegment(sketch, "E5990", {"start": v(-99.94, 22.77) * mm, "end": v(-100.28, 21.24) * mm});
            skLineSegment(sketch, "E5991", {"start": v(-100.28, 21.24) * mm, "end": v(-100.3, 21.15) * mm});
            skLineSegment(sketch, "E5992", {"start": v(-100.3, 21.15) * mm, "end": v(-100.14, 21.04) * mm});
            skLineSegment(sketch, "E5993", {"start": v(-100.14, 21.04) * mm, "end": v(-99.99, 20.93) * mm});
            skLineSegment(sketch, "E5994", {"start": v(-99.99, 20.93) * mm, "end": v(-99.84, 20.82) * mm});
            skLineSegment(sketch, "E5995", {"start": v(-99.84, 20.82) * mm, "end": v(-99.7, 20.7) * mm});
            skLineSegment(sketch, "E5996", {"start": v(-99.7, 20.7) * mm, "end": v(-99.54, 20.6) * mm});
            skLineSegment(sketch, "E5997", {"start": v(-99.54, 20.6) * mm, "end": v(-99.4, 20.5) * mm});
            skLineSegment(sketch, "E5998", {"start": v(-99.4, 20.5) * mm, "end": v(-99.25, 20.4) * mm});
            skLineSegment(sketch, "E5999", {"start": v(-99.25, 20.4) * mm, "end": v(-99.1, 20.29) * mm});
            skLineSegment(sketch, "E6000", {"start": v(-99.1, 20.29) * mm, "end": v(-98.96, 20.19) * mm});
            skLineSegment(sketch, "E6001", {"start": v(-98.96, 20.19) * mm, "end": v(-98.82, 20.09) * mm});
            skLineSegment(sketch, "E6002", {"start": v(-98.82, 20.09) * mm, "end": v(-98.68, 20) * mm});
            skLineSegment(sketch, "E6003", {"start": v(-98.68, 20) * mm, "end": v(-98.54, 19.9) * mm});
            skLineSegment(sketch, "E6004", {"start": v(-98.54, 19.9) * mm, "end": v(-98.4, 19.8) * mm});
            skLineSegment(sketch, "E6005", {"start": v(-98.4, 19.8) * mm, "end": v(-98.26, 19.7) * mm});
            skLineSegment(sketch, "E6006", {"start": v(-98.26, 19.7) * mm, "end": v(-98.12, 19.62) * mm});
            skLineSegment(sketch, "E6007", {"start": v(-98.12, 19.62) * mm, "end": v(-97.98, 19.53) * mm});
            skLineSegment(sketch, "E6008", {"start": v(-97.98, 19.53) * mm, "end": v(-97.85, 19.44) * mm});
            skLineSegment(sketch, "E6009", {"start": v(-97.85, 19.44) * mm, "end": v(-97.71, 19.35) * mm});
            skLineSegment(sketch, "E6010", {"start": v(-97.71, 19.35) * mm, "end": v(-97.58, 19.27) * mm});
            skLineSegment(sketch, "E6011", {"start": v(-97.58, 19.27) * mm, "end": v(-97.45, 19.18) * mm});
            skLineSegment(sketch, "E6012", {"start": v(-97.45, 19.18) * mm, "end": v(-97.32, 19.1) * mm});
            skLineSegment(sketch, "E6013", {"start": v(-97.32, 19.1) * mm, "end": v(-97.19, 19.02) * mm});
            skLineSegment(sketch, "E6014", {"start": v(-97.19, 19.02) * mm, "end": v(-97.06, 18.94) * mm});
            skLineSegment(sketch, "E6015", {"start": v(-97.06, 18.94) * mm, "end": v(-96.93, 18.87) * mm});
            skLineSegment(sketch, "E6016", {"start": v(-96.93, 18.87) * mm, "end": v(-96.8, 18.79) * mm});
            skLineSegment(sketch, "E6017", {"start": v(-96.8, 18.79) * mm, "end": v(-96.68, 18.72) * mm});
            skLineSegment(sketch, "E6018", {"start": v(-96.68, 18.72) * mm, "end": v(-96.56, 18.64) * mm});
            skLineSegment(sketch, "E6019", {"start": v(-96.56, 18.64) * mm, "end": v(-96.43, 18.57) * mm});
            skLineSegment(sketch, "E6020", {"start": v(-96.43, 18.57) * mm, "end": v(-96.31, 18.5) * mm});
            skLineSegment(sketch, "E6021", {"start": v(-96.31, 18.5) * mm, "end": v(-96.2, 18.43) * mm});
            skLineSegment(sketch, "E6022", {"start": v(-96.2, 18.43) * mm, "end": v(-96.07, 18.36) * mm});
            skLineSegment(sketch, "E6023", {"start": v(-96.07, 18.36) * mm, "end": v(-95.95, 18.3) * mm});
            skLineSegment(sketch, "E6024", {"start": v(-95.95, 18.3) * mm, "end": v(-95.84, 18.23) * mm});
            skLineSegment(sketch, "E6025", {"start": v(-95.84, 18.23) * mm, "end": v(-95.72, 18.17) * mm});
            skLineSegment(sketch, "E6026", {"start": v(-95.72, 18.17) * mm, "end": v(-95.6, 18.1) * mm});
            skLineSegment(sketch, "E6027", {"start": v(-95.6, 18.1) * mm, "end": v(-95.5, 18.05) * mm});
            skLineSegment(sketch, "E6028", {"start": v(-95.5, 18.05) * mm, "end": v(-95.6, 17.1) * mm});
            skLineSegment(sketch, "E6029", {"start": v(-95.6, 17.1) * mm, "end": v(-95.83, 16.2) * mm});
            skLineSegment(sketch, "E6030", {"start": v(-95.83, 16.2) * mm, "end": v(-95.95, 16.17) * mm});
            skLineSegment(sketch, "E6031", {"start": v(-95.95, 16.17) * mm, "end": v(-96.08, 16.15) * mm});
            skLineSegment(sketch, "E6032", {"start": v(-96.08, 16.15) * mm, "end": v(-96.21, 16.13) * mm});
            skLineSegment(sketch, "E6033", {"start": v(-96.21, 16.13) * mm, "end": v(-96.35, 16.11) * mm});
            skLineSegment(sketch, "E6034", {"start": v(-96.35, 16.11) * mm, "end": v(-96.48, 16.1) * mm});
            skLineSegment(sketch, "E6035", {"start": v(-96.48, 16.1) * mm, "end": v(-96.61, 16.07) * mm});
            skLineSegment(sketch, "E6036", {"start": v(-96.61, 16.07) * mm, "end": v(-96.75, 16.05) * mm});
            skLineSegment(sketch, "E6037", {"start": v(-96.75, 16.05) * mm, "end": v(-96.89, 16.02) * mm});
            skLineSegment(sketch, "E6038", {"start": v(-96.89, 16.02) * mm, "end": v(-97.03, 16) * mm});
            skLineSegment(sketch, "E6039", {"start": v(-97.03, 16) * mm, "end": v(-97.17, 15.97) * mm});
            skLineSegment(sketch, "E6040", {"start": v(-97.17, 15.97) * mm, "end": v(-97.31, 15.95) * mm});
            skLineSegment(sketch, "E6041", {"start": v(-97.31, 15.95) * mm, "end": v(-97.46, 15.92) * mm});
            skLineSegment(sketch, "E6042", {"start": v(-97.46, 15.92) * mm, "end": v(-97.6, 15.9) * mm});
            skLineSegment(sketch, "E6043", {"start": v(-97.6, 15.9) * mm, "end": v(-97.75, 15.86) * mm});
            skLineSegment(sketch, "E6044", {"start": v(-97.75, 15.86) * mm, "end": v(-97.9, 15.83) * mm});
            skLineSegment(sketch, "E6045", {"start": v(-97.9, 15.83) * mm, "end": v(-98.05, 15.8) * mm});
            skLineSegment(sketch, "E6046", {"start": v(-98.05, 15.8) * mm, "end": v(-98.2, 15.77) * mm});
            skLineSegment(sketch, "E6047", {"start": v(-98.2, 15.77) * mm, "end": v(-98.36, 15.74) * mm});
            skLineSegment(sketch, "E6048", {"start": v(-98.36, 15.74) * mm, "end": v(-98.52, 15.7) * mm});
            skLineSegment(sketch, "E6049", {"start": v(-98.52, 15.7) * mm, "end": v(-98.67, 15.67) * mm});
            skLineSegment(sketch, "E6050", {"start": v(-98.67, 15.67) * mm, "end": v(-98.83, 15.63) * mm});
            skLineSegment(sketch, "E6051", {"start": v(-98.83, 15.63) * mm, "end": v(-99, 15.6) * mm});
            skLineSegment(sketch, "E6052", {"start": v(-99, 15.6) * mm, "end": v(-99.16, 15.55) * mm});
            skLineSegment(sketch, "E6053", {"start": v(-99.16, 15.55) * mm, "end": v(-99.32, 15.51) * mm});
            skLineSegment(sketch, "E6054", {"start": v(-99.32, 15.51) * mm, "end": v(-99.49, 15.47) * mm});
            skLineSegment(sketch, "E6055", {"start": v(-99.49, 15.47) * mm, "end": v(-99.65, 15.43) * mm});
            skLineSegment(sketch, "E6056", {"start": v(-99.65, 15.43) * mm, "end": v(-99.82, 15.39) * mm});
            skLineSegment(sketch, "E6057", {"start": v(-99.82, 15.39) * mm, "end": v(-100, 15.34) * mm});
            skLineSegment(sketch, "E6058", {"start": v(-100, 15.34) * mm, "end": v(-100.16, 15.3) * mm});
            skLineSegment(sketch, "E6059", {"start": v(-100.16, 15.3) * mm, "end": v(-100.33, 15.25) * mm});
            skLineSegment(sketch, "E6060", {"start": v(-100.33, 15.25) * mm, "end": v(-100.5, 15.2) * mm});
            skLineSegment(sketch, "E6061", {"start": v(-100.5, 15.2) * mm, "end": v(-100.68, 15.15) * mm});
            skLineSegment(sketch, "E6062", {"start": v(-100.68, 15.15) * mm, "end": v(-100.86, 15.1) * mm});
            skLineSegment(sketch, "E6063", {"start": v(-100.86, 15.1) * mm, "end": v(-101.04, 15.05) * mm});
            skLineSegment(sketch, "E6064", {"start": v(-101.04, 15.05) * mm, "end": v(-101.22, 15) * mm});
            skLineSegment(sketch, "E6065", {"start": v(-101.22, 15) * mm, "end": v(-101.4, 14.94) * mm});
            skLineSegment(sketch, "E6066", {"start": v(-101.4, 14.94) * mm, "end": v(-101.42, 14.86) * mm});
            skLineSegment(sketch, "E6067", {"start": v(-101.42, 14.86) * mm, "end": v(-101.63, 13.3) * mm});
            skLineSegment(sketch, "E6068", {"start": v(-101.63, 13.3) * mm, "end": v(-101.64, 13.22) * mm});
            skLineSegment(sketch, "E6069", {"start": v(-101.64, 13.22) * mm, "end": v(-101.48, 13.12) * mm});
            skLineSegment(sketch, "E6070", {"start": v(-101.48, 13.12) * mm, "end": v(-101.32, 13.02) * mm});
            skLineSegment(sketch, "E6071", {"start": v(-101.32, 13.02) * mm, "end": v(-101.16, 12.92) * mm});
            skLineSegment(sketch, "E6072", {"start": v(-101.16, 12.92) * mm, "end": v(-101, 12.82) * mm});
            skLineSegment(sketch, "E6073", {"start": v(-101, 12.82) * mm, "end": v(-100.85, 12.73) * mm});
            skLineSegment(sketch, "E6074", {"start": v(-100.85, 12.73) * mm, "end": v(-100.7, 12.63) * mm});
            skLineSegment(sketch, "E6075", {"start": v(-100.7, 12.63) * mm, "end": v(-100.54, 12.54) * mm});
            skLineSegment(sketch, "E6076", {"start": v(-100.54, 12.54) * mm, "end": v(-100.4, 12.45) * mm});
            skLineSegment(sketch, "E6077", {"start": v(-100.4, 12.45) * mm, "end": v(-100.24, 12.36) * mm});
            skLineSegment(sketch, "E6078", {"start": v(-100.24, 12.36) * mm, "end": v(-100.09, 12.27) * mm});
            skLineSegment(sketch, "E6079", {"start": v(-100.09, 12.27) * mm, "end": v(-99.94, 12.19) * mm});
            skLineSegment(sketch, "E6080", {"start": v(-99.94, 12.19) * mm, "end": v(-99.8, 12.1) * mm});
            skLineSegment(sketch, "E6081", {"start": v(-99.8, 12.1) * mm, "end": v(-99.65, 12.02) * mm});
            skLineSegment(sketch, "E6082", {"start": v(-99.65, 12.02) * mm, "end": v(-99.5, 11.94) * mm});
            skLineSegment(sketch, "E6083", {"start": v(-99.5, 11.94) * mm, "end": v(-99.36, 11.86) * mm});
            skLineSegment(sketch, "E6084", {"start": v(-99.36, 11.86) * mm, "end": v(-99.21, 11.78) * mm});
            skLineSegment(sketch, "E6085", {"start": v(-99.21, 11.78) * mm, "end": v(-99.07, 11.7) * mm});
            skLineSegment(sketch, "E6086", {"start": v(-99.07, 11.7) * mm, "end": v(-98.93, 11.63) * mm});
            skLineSegment(sketch, "E6087", {"start": v(-98.93, 11.63) * mm, "end": v(-98.8, 11.55) * mm});
            skLineSegment(sketch, "E6088", {"start": v(-98.8, 11.55) * mm, "end": v(-98.65, 11.48) * mm});
            skLineSegment(sketch, "E6089", {"start": v(-98.65, 11.48) * mm, "end": v(-98.52, 11.4) * mm});
            skLineSegment(sketch, "E6090", {"start": v(-98.52, 11.4) * mm, "end": v(-98.38, 11.34) * mm});
            skLineSegment(sketch, "E6091", {"start": v(-98.38, 11.34) * mm, "end": v(-98.25, 11.27) * mm});
            skLineSegment(sketch, "E6092", {"start": v(-98.25, 11.27) * mm, "end": v(-98.11, 11.2) * mm});
            skLineSegment(sketch, "E6093", {"start": v(-98.11, 11.2) * mm, "end": v(-97.98, 11.14) * mm});
            skLineSegment(sketch, "E6094", {"start": v(-97.98, 11.14) * mm, "end": v(-97.85, 11.07) * mm});
            skLineSegment(sketch, "E6095", {"start": v(-97.85, 11.07) * mm, "end": v(-97.72, 11) * mm});
            skLineSegment(sketch, "E6096", {"start": v(-97.72, 11) * mm, "end": v(-97.6, 10.95) * mm});
            skLineSegment(sketch, "E6097", {"start": v(-97.6, 10.95) * mm, "end": v(-97.47, 10.89) * mm});
            skLineSegment(sketch, "E6098", {"start": v(-97.47, 10.89) * mm, "end": v(-97.34, 10.83) * mm});
            skLineSegment(sketch, "E6099", {"start": v(-97.34, 10.83) * mm, "end": v(-97.22, 10.77) * mm});
            skLineSegment(sketch, "E6100", {"start": v(-97.22, 10.77) * mm, "end": v(-97.1, 10.71) * mm});
            skLineSegment(sketch, "E6101", {"start": v(-97.1, 10.71) * mm, "end": v(-96.97, 10.66) * mm});
            skLineSegment(sketch, "E6102", {"start": v(-96.97, 10.66) * mm, "end": v(-96.85, 10.6) * mm});
            skLineSegment(sketch, "E6103", {"start": v(-96.85, 10.6) * mm, "end": v(-96.73, 10.55) * mm});
            skLineSegment(sketch, "E6104", {"start": v(-96.73, 10.55) * mm, "end": v(-96.62, 10.5) * mm});
            skLineSegment(sketch, "E6105", {"start": v(-96.62, 10.5) * mm, "end": v(-96.65, 9.56) * mm});
            skLineSegment(sketch, "E6106", {"start": v(-96.65, 9.56) * mm, "end": v(-96.8, 8.62) * mm});
            skLineSegment(sketch, "E6107", {"start": v(-96.8, 8.62) * mm, "end": v(-96.93, 8.6) * mm});
            skLineSegment(sketch, "E6108", {"start": v(-96.93, 8.6) * mm, "end": v(-97.05, 8.57) * mm});
            skLineSegment(sketch, "E6109", {"start": v(-97.05, 8.57) * mm, "end": v(-97.18, 8.54) * mm});
            skLineSegment(sketch, "E6110", {"start": v(-97.18, 8.54) * mm, "end": v(-97.31, 8.5) * mm});
            skLineSegment(sketch, "E6111", {"start": v(-97.31, 8.5) * mm, "end": v(-97.44, 8.47) * mm});
            skLineSegment(sketch, "E6112", {"start": v(-97.44, 8.47) * mm, "end": v(-97.58, 8.44) * mm});
            skLineSegment(sketch, "E6113", {"start": v(-97.58, 8.44) * mm, "end": v(-97.71, 8.4) * mm});
            skLineSegment(sketch, "E6114", {"start": v(-97.71, 8.4) * mm, "end": v(-97.85, 8.37) * mm});
            skLineSegment(sketch, "E6115", {"start": v(-97.85, 8.37) * mm, "end": v(-97.98, 8.34) * mm});
            skLineSegment(sketch, "E6116", {"start": v(-97.98, 8.34) * mm, "end": v(-98.12, 8.3) * mm});
            skLineSegment(sketch, "E6117", {"start": v(-98.12, 8.3) * mm, "end": v(-98.26, 8.26) * mm});
            skLineSegment(sketch, "E6118", {"start": v(-98.26, 8.26) * mm, "end": v(-98.4, 8.23) * mm});
            skLineSegment(sketch, "E6119", {"start": v(-98.4, 8.23) * mm, "end": v(-98.55, 8.19) * mm});
            skLineSegment(sketch, "E6120", {"start": v(-98.55, 8.19) * mm, "end": v(-98.7, 8.14) * mm});
            skLineSegment(sketch, "E6121", {"start": v(-98.7, 8.14) * mm, "end": v(-98.84, 8.1) * mm});
            skLineSegment(sketch, "E6122", {"start": v(-98.84, 8.1) * mm, "end": v(-99, 8.06) * mm});
            skLineSegment(sketch, "E6123", {"start": v(-99, 8.06) * mm, "end": v(-99.14, 8.02) * mm});
            skLineSegment(sketch, "E6124", {"start": v(-99.14, 8.02) * mm, "end": v(-99.3, 7.97) * mm});
            skLineSegment(sketch, "E6125", {"start": v(-99.3, 7.97) * mm, "end": v(-99.44, 7.92) * mm});
            skLineSegment(sketch, "E6126", {"start": v(-99.44, 7.92) * mm, "end": v(-99.6, 7.88) * mm});
            skLineSegment(sketch, "E6127", {"start": v(-99.6, 7.88) * mm, "end": v(-99.75, 7.83) * mm});
            skLineSegment(sketch, "E6128", {"start": v(-99.75, 7.83) * mm, "end": v(-99.91, 7.78) * mm});
            skLineSegment(sketch, "E6129", {"start": v(-99.91, 7.78) * mm, "end": v(-100.07, 7.72) * mm});
            skLineSegment(sketch, "E6130", {"start": v(-100.07, 7.72) * mm, "end": v(-100.23, 7.67) * mm});
            skLineSegment(sketch, "E6131", {"start": v(-100.23, 7.67) * mm, "end": v(-100.4, 7.62) * mm});
            skLineSegment(sketch, "E6132", {"start": v(-100.4, 7.62) * mm, "end": v(-100.56, 7.56) * mm});
            skLineSegment(sketch, "E6133", {"start": v(-100.56, 7.56) * mm, "end": v(-100.72, 7.5) * mm});
            skLineSegment(sketch, "E6134", {"start": v(-100.72, 7.5) * mm, "end": v(-100.89, 7.45) * mm});
            skLineSegment(sketch, "E6135", {"start": v(-100.89, 7.45) * mm, "end": v(-101.05, 7.39) * mm});
            skLineSegment(sketch, "E6136", {"start": v(-101.05, 7.39) * mm, "end": v(-101.22, 7.33) * mm});
            skLineSegment(sketch, "E6137", {"start": v(-101.22, 7.33) * mm, "end": v(-101.4, 7.27) * mm});
            skLineSegment(sketch, "E6138", {"start": v(-101.4, 7.27) * mm, "end": v(-101.56, 7.2) * mm});
            skLineSegment(sketch, "E6139", {"start": v(-101.56, 7.2) * mm, "end": v(-101.74, 7.14) * mm});
            skLineSegment(sketch, "E6140", {"start": v(-101.74, 7.14) * mm, "end": v(-101.91, 7.07) * mm});
            skLineSegment(sketch, "E6141", {"start": v(-101.91, 7.07) * mm, "end": v(-102.09, 7) * mm});
            skLineSegment(sketch, "E6142", {"start": v(-102.09, 7) * mm, "end": v(-102.26, 6.94) * mm});
            skLineSegment(sketch, "E6143", {"start": v(-102.26, 6.94) * mm, "end": v(-102.27, 6.86) * mm});
            skLineSegment(sketch, "E6144", {"start": v(-102.27, 6.86) * mm, "end": v(-102.36, 5.29) * mm});
            skLineSegment(sketch, "E6145", {"start": v(-102.36, 5.29) * mm, "end": v(-102.37, 5.2) * mm});
            skLineSegment(sketch, "E6146", {"start": v(-102.37, 5.2) * mm, "end": v(-102.2, 5.12) * mm});
            skLineSegment(sketch, "E6147", {"start": v(-102.2, 5.12) * mm, "end": v(-102.03, 5.03) * mm});
            skLineSegment(sketch, "E6148", {"start": v(-102.03, 5.03) * mm, "end": v(-101.87, 4.94) * mm});
            skLineSegment(sketch, "E6149", {"start": v(-101.87, 4.94) * mm, "end": v(-101.7, 4.86) * mm});
            skLineSegment(sketch, "E6150", {"start": v(-101.7, 4.86) * mm, "end": v(-101.54, 4.78) * mm});
            skLineSegment(sketch, "E6151", {"start": v(-101.54, 4.78) * mm, "end": v(-101.38, 4.7) * mm});
            skLineSegment(sketch, "E6152", {"start": v(-101.38, 4.7) * mm, "end": v(-101.22, 4.61) * mm});
            skLineSegment(sketch, "E6153", {"start": v(-101.22, 4.61) * mm, "end": v(-101.06, 4.54) * mm});
            skLineSegment(sketch, "E6154", {"start": v(-101.06, 4.54) * mm, "end": v(-100.9, 4.46) * mm});
            skLineSegment(sketch, "E6155", {"start": v(-100.9, 4.46) * mm, "end": v(-100.74, 4.38) * mm});
            skLineSegment(sketch, "E6156", {"start": v(-100.74, 4.38) * mm, "end": v(-100.59, 4.3) * mm});
            skLineSegment(sketch, "E6157", {"start": v(-100.59, 4.3) * mm, "end": v(-100.43, 4.24) * mm});
            skLineSegment(sketch, "E6158", {"start": v(-100.43, 4.24) * mm, "end": v(-100.28, 4.16) * mm});
            skLineSegment(sketch, "E6159", {"start": v(-100.28, 4.16) * mm, "end": v(-100.13, 4.1) * mm});
            skLineSegment(sketch, "E6160", {"start": v(-100.13, 4.1) * mm, "end": v(-99.98, 4.03) * mm});
            skLineSegment(sketch, "E6161", {"start": v(-99.98, 4.03) * mm, "end": v(-99.83, 3.96) * mm});
            skLineSegment(sketch, "E6162", {"start": v(-99.83, 3.96) * mm, "end": v(-99.68, 3.9) * mm});
            skLineSegment(sketch, "E6163", {"start": v(-99.68, 3.9) * mm, "end": v(-99.54, 3.83) * mm});
            skLineSegment(sketch, "E6164", {"start": v(-99.54, 3.83) * mm, "end": v(-99.4, 3.77) * mm});
            skLineSegment(sketch, "E6165", {"start": v(-99.4, 3.77) * mm, "end": v(-99.25, 3.7) * mm});
            skLineSegment(sketch, "E6166", {"start": v(-99.25, 3.7) * mm, "end": v(-99.1, 3.64) * mm});
            skLineSegment(sketch, "E6167", {"start": v(-99.1, 3.64) * mm, "end": v(-98.97, 3.58) * mm});
            skLineSegment(sketch, "E6168", {"start": v(-98.97, 3.58) * mm, "end": v(-98.83, 3.53) * mm});
            skLineSegment(sketch, "E6169", {"start": v(-98.83, 3.53) * mm, "end": v(-98.69, 3.47) * mm});
            skLineSegment(sketch, "E6170", {"start": v(-98.69, 3.47) * mm, "end": v(-98.55, 3.41) * mm});
            skLineSegment(sketch, "E6171", {"start": v(-98.55, 3.41) * mm, "end": v(-98.42, 3.36) * mm});
            skLineSegment(sketch, "E6172", {"start": v(-98.42, 3.36) * mm, "end": v(-98.28, 3.3) * mm});
            skLineSegment(sketch, "E6173", {"start": v(-98.28, 3.3) * mm, "end": v(-98.15, 3.26) * mm});
            skLineSegment(sketch, "E6174", {"start": v(-98.15, 3.26) * mm, "end": v(-98.02, 3.2) * mm});
            skLineSegment(sketch, "E6175", {"start": v(-98.02, 3.2) * mm, "end": v(-97.9, 3.16) * mm});
            skLineSegment(sketch, "E6176", {"start": v(-97.9, 3.16) * mm, "end": v(-97.76, 3.1) * mm});
            skLineSegment(sketch, "E6177", {"start": v(-97.76, 3.1) * mm, "end": v(-97.64, 3.06) * mm});
            skLineSegment(sketch, "E6178", {"start": v(-97.64, 3.06) * mm, "end": v(-97.51, 3.02) * mm});
            skLineSegment(sketch, "E6179", {"start": v(-97.51, 3.02) * mm, "end": v(-97.39, 2.97) * mm});
            skLineSegment(sketch, "E6180", {"start": v(-97.39, 2.97) * mm, "end": v(-97.26, 2.93) * mm});
            skLineSegment(sketch, "E6181", {"start": v(-97.26, 2.93) * mm, "end": v(-97.14, 2.89) * mm});
            skLineSegment(sketch, "E6182", {"start": v(-97.14, 2.89) * mm, "end": v(-97.1, 1.94) * mm});
            skSolve(sketch);
        }
        {
            var Q0;
            Q0 = qSketchRegion(id + "F0", true);
            extrude(context, id + "F1", {"entities" : qUnion([Q0]), "depth" : 8 * mm, "offsetDistance" : 25 * mm});
        }
    });
